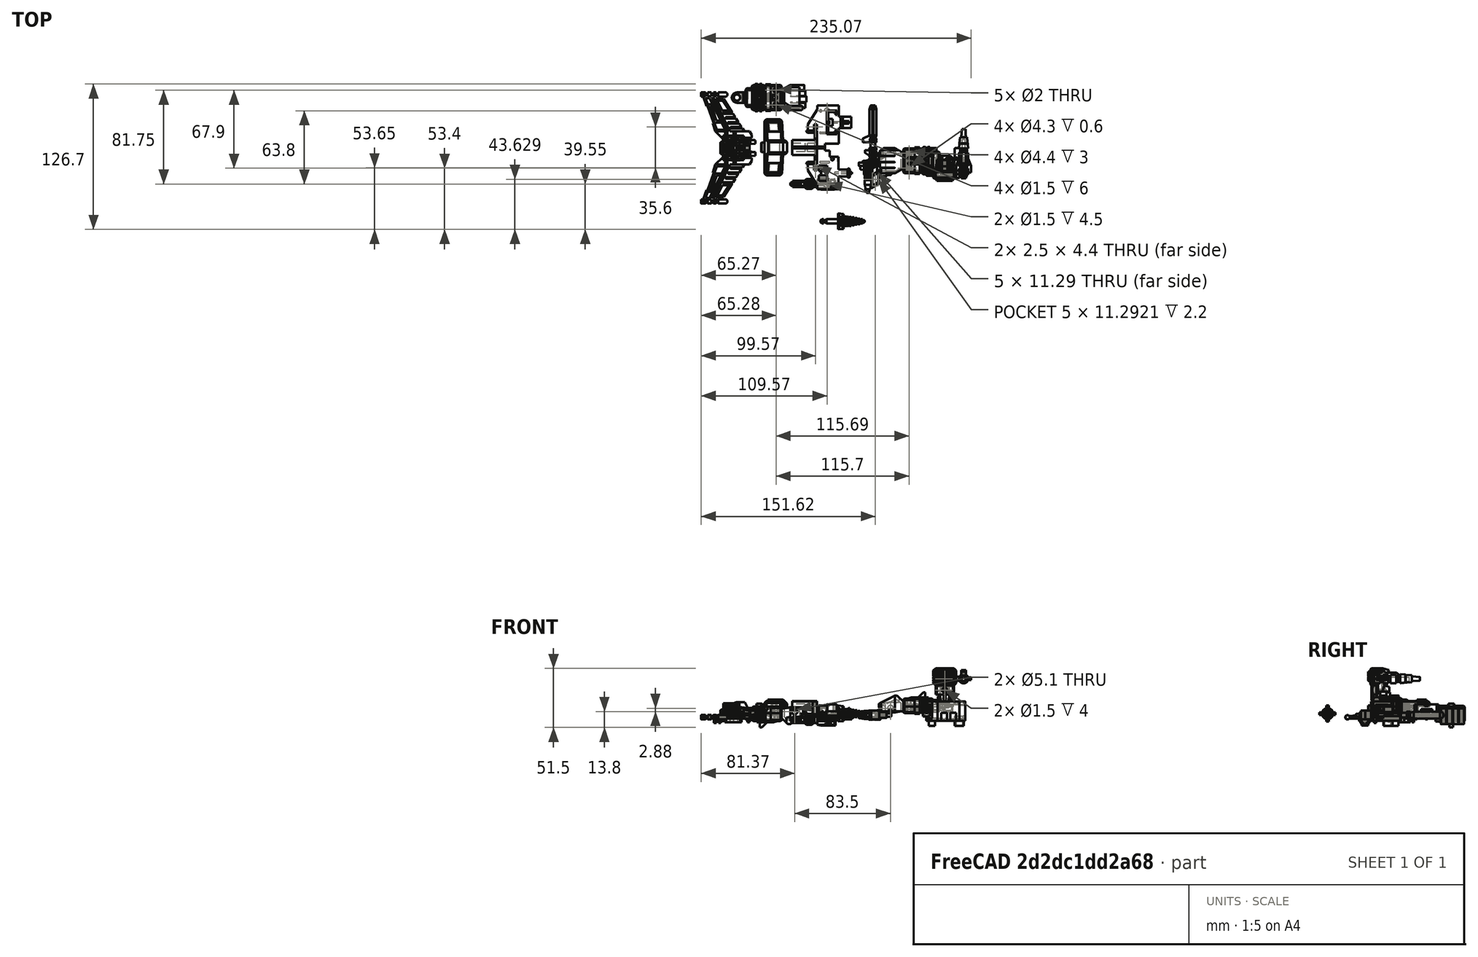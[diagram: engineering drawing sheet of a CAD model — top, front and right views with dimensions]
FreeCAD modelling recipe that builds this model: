
FCSTD DOCUMENT  (FreeCAD 1.0R39109 (Git))
Label: Accesories2
License: All rights reserved
LicenseURL: https://en.wikipedia.org/wiki/All_rights_reserved
objects: Sketcher::SketchObject×459, PartDesign::Pad×303, PartDesign::Pocket×204, PartDesign::Chamfer×40, PartDesign::Body×21, PartDesign::SubShapeBinder×9, PartDesign::Fillet×9, PartDesign::AdditiveLoft×7, PartDesign::Plane×4, App::Part×4, App::Link×3, PartDesign::Groove×3, PartDesign::SubtractiveLoft×2, Part::Mirroring×1, Part::Feature×1
note: 2658 computed .brp shape members not serialized (recipe doc carries the construction recipe); baked Part::Feature solids carry a one-line shape summary decoded from their .brp

FEATURE [Sketcher::SketchObject] Sketch508
  ArcFitTolerance = 1e-06
  AttachmentSupport = -> [XZ_Plane033]
  FullyConstrained = true
  MakeInternals = false
  MapMode = 5
  Placement = pos=(0,0,0) rot=(1,0,0;1.5708rad)
  sketch-geometry (30):
    g0: LineSegment StartX=0 StartY=0 StartZ=0 EndX=13.5 EndY=0 EndZ=0
    g1: LineSegment StartX=13.5 StartY=0 StartZ=0 EndX=13.5 EndY=-11.8 EndZ=0
    g2: LineSegment StartX=13.5 StartY=-11.8 StartZ=0 EndX=23.4 EndY=-11.8 EndZ=0
    g3: LineSegment StartX=23.4 StartY=-11.8 StartZ=0 EndX=23.4 EndY=0 EndZ=0
    g4: LineSegment StartX=23.4 StartY=0 StartZ=0 EndX=33.2 EndY=0 EndZ=0
    g5: LineSegment StartX=33.2 StartY=0 StartZ=0 EndX=33.2 EndY=17.7 EndZ=0
    g6: LineSegment StartX=33.2 StartY=17.7 StartZ=0 EndX=29.8 EndY=17.7 EndZ=0
    g7: LineSegment StartX=29.8 StartY=17.7 StartZ=0 EndX=16.75 EndY=25.9 EndZ=0
    g8: LineSegment StartX=16.75 StartY=25.9 StartZ=0 EndX=11.25 EndY=25.9 EndZ=0
    g9: LineSegment StartX=11.25 StartY=25.9 StartZ=0 EndX=11.25 EndY=27.1 EndZ=0
    g10: LineSegment StartX=11.25 StartY=27.1 StartZ=0 EndX=9.45 EndY=27.1 EndZ=0
    g11: LineSegment StartX=9.45 StartY=27.1 StartZ=0 EndX=9.45 EndY=19.8 EndZ=0
    g12: LineSegment StartX=9.45 StartY=19.8 StartZ=0 EndX=-16.15 EndY=19.8 EndZ=0
    g13: LineSegment StartX=-16.15 StartY=19.8 StartZ=0 EndX=-16.15 EndY=27.1 EndZ=0
    g14: LineSegment StartX=-16.15 StartY=27.1 StartZ=0 EndX=-17.95 EndY=27.1 EndZ=0
    g15: LineSegment StartX=-17.95 StartY=27.1 StartZ=0 EndX=-17.95 EndY=25.9 EndZ=0
    g16: LineSegment StartX=-17.95 StartY=25.9 StartZ=0 EndX=-23.45 EndY=25.9 EndZ=0
    g17: LineSegment StartX=-23.45 StartY=25.9 StartZ=0 EndX=-36.5 EndY=17.7 EndZ=0
    g18: LineSegment StartX=-36.5 StartY=17.7 StartZ=0 EndX=-39.9 EndY=17.7 EndZ=0
    g19: LineSegment StartX=-39.9 StartY=17.7 StartZ=0 EndX=-39.9 EndY=0 EndZ=0
    g20: LineSegment StartX=-39.9 StartY=0 StartZ=0 EndX=-28.8 EndY=0 EndZ=0
    g21: LineSegment StartX=-28.8 StartY=0 StartZ=0 EndX=-28.8 EndY=-10.7 EndZ=0
    g22: LineSegment StartX=-28.8 StartY=-10.7 StartZ=0 EndX=-22.8 EndY=-10.7 EndZ=0
    g23: LineSegment StartX=-22.8 StartY=-10.7 StartZ=0 EndX=-22.8 EndY=0 EndZ=0
    g24: LineSegment StartX=-22.8 StartY=0 StartZ=0 EndX=-12.9 EndY=0 EndZ=0
    g25: LineSegment StartX=-12.9 StartY=0 StartZ=0 EndX=-12.9 EndY=6.7 EndZ=0
    g26: LineSegment StartX=-12.9 StartY=6.7 StartZ=0 EndX=-6 EndY=6.7 EndZ=0
    g27: LineSegment StartX=-6 StartY=6.7 StartZ=0 EndX=-6 EndY=11 EndZ=0
    g28: LineSegment StartX=-6 StartY=11 StartZ=0 EndX=0 EndY=11 EndZ=0
    g29: LineSegment StartX=0 StartY=11 StartZ=0 EndX=0 EndY=0 EndZ=0
  constraints (91):
    c: Coincident(g0,g-1)
    c: PointOnObject(g0,g-1)
    c: Coincident(g1,g0)
    c: Vertical(g1)
    c: Coincident(g2,g1)
    c: Horizontal(g2)
    c: Coincident(g3,g2)
    c: PointOnObject(g3,g-1)
    c: Vertical(g3)
    c: Coincident(g4,g3)
    c: PointOnObject(g4,g-1)
    c: DistanceX(g0,g0) = 13.5
    c: Coincident(g5,g4)
    c: Vertical(g5)
    c: Coincident(g6,g5)
    c: Horizontal(g6)
    c: Coincident(g7,g6)
    c: Coincident(g8,g7)
    c: Horizontal(g8)
    c: Coincident(g9,g8)
    c: Vertical(g9)
    c: Coincident(g10,g9)
    c: Horizontal(g10)
    c: Coincident(g11,g10)
    c: Vertical(g11)
    c: Coincident(g12,g11)
    c: Horizontal(g12)
    c: Coincident(g13,g12)
    c: Vertical(g13)
    c: Coincident(g14,g13)
    c: Horizontal(g14)
    c: Coincident(g15,g14)
    c: Vertical(g15)
    c: Coincident(g16,g15)
    c: Horizontal(g16)
    c: Coincident(g17,g16)
    c: Coincident(g18,g17)
    c: Horizontal(g18)
    c: Coincident(g19,g18)
    c: PointOnObject(g19,g-1)
    c: Vertical(g19)
    c: Coincident(g20,g19)
    c: PointOnObject(g20,g-1)
    c: Coincident(g21,g20)
    c: Vertical(g21)
    c: Coincident(g22,g21)
    c: Horizontal(g22)
    c: Coincident(g23,g22)
    c: PointOnObject(g23,g-1)
    c: Vertical(g23)
    c: Coincident(g24,g23)
    c: PointOnObject(g24,g-1)
    c: Coincident(g25,g24)
    c: Vertical(g25)
    c: Coincident(g26,g25)
    c: Horizontal(g26)
    c: Coincident(g27,g26)
    c: Vertical(g27)
    c: Coincident(g28,g27)
    c: PointOnObject(g28,g-2)
    c: Horizontal(g28)
    c: Coincident(g29,g28)
    c: Coincident(g29,g0)
    c: DistanceX(g2,g2) = 9.9
    c: DistanceY(g1,g1) = 11.8
    c: DistanceX(g4,g4) = 9.8
    c: DistanceY(g5,g5) = 17.7
    c: DistanceY(g29,g29) = 11
    c: DistanceX(g28,g28) = 6
    c: DistanceX(g24,g0) = 12.9
    c: DistanceX(g19,g24) = 27
    c: DistanceX(g22,g22) = 6
    c: DistanceY(g23,g23) = 10.7
    c: DistanceX(g20,g20) = 11.1
    c: DistanceY(g19,g19) = 17.7
    c: DistanceX(g10,g10) = 1.8
    c: DistanceX(g14,g14) = 1.8
    c: DistanceY(g9,g9) = 1.2
    c: DistanceY(g15,g15) = 1.2
    c: DistanceX(g18,g18) = 3.4
    c: DistanceX(g6,g6) = 3.4
    c: DistanceY(g25,g25) = 6.7
    c: DistanceX(g19,g4) = 73.1
    c: DistanceX(g12,g12) = 25.6
    c: DistanceY(g11,g11) = 7.3
    c: DistanceX(g16,g16) = 5.5
    c: DistanceX(g8,g8) = 5.5
    c: DistanceY(g13,g13) = 7.3
    c: DistanceY(g28,g11) = 8.8
    c: DistanceX(g18,g12) = 23.75
    c: DistanceX(g11,g5) = 23.75
FEATURE [PartDesign::Pad] Pad351
  Direction = (0,-1,2e-16)
  Length = 2
  Length2 = 10
  Placement = pos=(0,0,0) rot=(1,0,0;1.5708rad)
  Profile = -> Sketch508
  ReferenceAxis = -> Sketch508 [N_Axis]
  Refine = true
  Suppressed = false
  Type = 0
FEATURE [Sketcher::SketchObject] Sketch509
  ArcFitTolerance = 1e-06
  AttachmentSupport = -> [Pad351]
  ExternalGeometry = -> [Pad351]
  FullyConstrained = true
  MakeInternals = false
  MapMode = 5
  Placement = pos=(0,-2,0) rot=(1,0,0;1.5708rad)
  sketch-geometry (8):
    g0: LineSegment StartX=-17.95 StartY=27.1 StartZ=0 EndX=-16.15 EndY=27.1 EndZ=0
    g1: LineSegment StartX=-16.15 StartY=27.1 StartZ=0 EndX=-16.15 EndY=19.8 EndZ=0
    g2: LineSegment StartX=-16.15 StartY=19.8 StartZ=0 EndX=9.45 EndY=19.8 EndZ=0
    g3: LineSegment StartX=9.45 StartY=19.8 StartZ=0 EndX=9.45 EndY=27.1 EndZ=0
    g4: LineSegment StartX=9.45 StartY=27.1 StartZ=0 EndX=11.25 EndY=27.1 EndZ=0
    g5: LineSegment StartX=11.25 StartY=27.1 StartZ=0 EndX=11.25 EndY=17.8 EndZ=0
    g6: LineSegment StartX=11.25 StartY=17.8 StartZ=0 EndX=-17.95 EndY=17.8 EndZ=0
    g7: LineSegment StartX=-17.95 StartY=27.1 StartZ=0 EndX=-17.95 EndY=17.8 EndZ=0
  constraints (18):
    c: Coincident(g0,g-7)
    c: Coincident(g0,g-5)
    c: Coincident(g1,g0)
    c: Coincident(g1,g-6)
    c: Coincident(g2,g1)
    c: Coincident(g2,g-6)
    c: Coincident(g3,g2)
    c: Coincident(g3,g-4)
    c: Coincident(g4,g3)
    c: Coincident(g4,g-3)
    c: Coincident(g5,g4)
    c: Vertical(g5)
    c: Coincident(g6,g5)
    c: Horizontal(g6)
    c: Coincident(g7,g0)
    c: Coincident(g7,g6)
    c: Vertical(g7)
    c: DistanceY(g6,g1) = 2
FEATURE [PartDesign::Pad] Pad352
  BaseFeature = -> Pad351
  Direction = (0,-1,2e-16)
  Length = 11
  Length2 = 10
  Placement = pos=(0,0,0) rot=(1,0,0;1.5708rad)
  Profile = -> Sketch509
  ReferenceAxis = -> Sketch509 [N_Axis]
  Refine = true
  Suppressed = false
  Type = 0
FEATURE [Sketcher::SketchObject] Sketch510
  ArcFitTolerance = 1e-06
  AttachmentSupport = -> [Pad352]
  ExternalGeometry = -> [Pad352]
  FullyConstrained = true
  MakeInternals = false
  MapMode = 5
  Placement = pos=(0,-13,0) rot=(1,0,0;1.5708rad)
  sketch-geometry (8):
    g0: LineSegment StartX=-17.95 StartY=27.1 StartZ=0 EndX=-17.95 EndY=21.7 EndZ=0
    g1: LineSegment StartX=-17.95 StartY=21.7 StartZ=0 EndX=-16.15 EndY=21.7 EndZ=0
    g2: LineSegment StartX=-16.15 StartY=21.7 StartZ=0 EndX=-16.15 EndY=27.1 EndZ=0
    g3: LineSegment StartX=-16.15 StartY=27.1 StartZ=0 EndX=-17.95 EndY=27.1 EndZ=0
    g4: LineSegment StartX=9.45 StartY=27.1 StartZ=0 EndX=9.45 EndY=21.7 EndZ=0
    g5: LineSegment StartX=9.45 StartY=21.7 StartZ=0 EndX=11.25 EndY=21.7 EndZ=0
    g6: LineSegment StartX=11.25 StartY=21.7 StartZ=0 EndX=11.25 EndY=27.1 EndZ=0
    g7: LineSegment StartX=11.25 StartY=27.1 StartZ=0 EndX=9.45 EndY=27.1 EndZ=0
  constraints (22):
    c: Coincident(g0,g1)
    c: Coincident(g1,g2)
    c: Coincident(g2,g3)
    c: Coincident(g3,g0)
    c: Vertical(g0)
    c: Vertical(g2)
    c: Horizontal(g1)
    c: Horizontal(g3)
    c: Coincident(g0,g-6)
    c: PointOnObject(g1,g-5)
    c: Coincident(g4,g5)
    c: Coincident(g5,g6)
    c: Coincident(g6,g7)
    c: Coincident(g7,g4)
    c: Vertical(g4)
    c: Vertical(g6)
    c: Horizontal(g5)
    c: Horizontal(g7)
    c: Coincident(g4,g-4)
    c: PointOnObject(g5,g-3)
    c: DistanceY(g0,g0) = 5.4
    c: DistanceY(g6,g6) = 5.4
FEATURE [PartDesign::Pocket] Pocket235
  BaseFeature = -> Pad352
  Direction = (0,1,-2e-16)
  Length = 10.7
  Length2 = 5
  Placement = pos=(0,0,0) rot=(1,0,0;1.5708rad)
  Profile = -> Sketch510
  ReferenceAxis = -> Sketch510 [N_Axis]
  Refine = true
  Suppressed = false
  Type = 0
FEATURE [Sketcher::SketchObject] Sketch511
  ArcFitTolerance = 1e-06
  AttachmentSupport = -> [Pocket235]
  ExternalGeometry = -> [Pocket235]
  FullyConstrained = true
  MakeInternals = false
  MapMode = 5
  Placement = pos=(0,-13,0) rot=(1,0,0;1.5708rad)
  sketch-geometry (4):
    g0: LineSegment StartX=-9.25 StartY=19.8 StartZ=0 EndX=2.55 EndY=19.8 EndZ=0
    g1: LineSegment StartX=2.55 StartY=19.8 StartZ=0 EndX=2.55 EndY=39.4 EndZ=0
    g2: LineSegment StartX=2.55 StartY=39.4 StartZ=0 EndX=-9.25 EndY=39.4 EndZ=0
    g3: LineSegment StartX=-9.25 StartY=39.4 StartZ=0 EndX=-9.25 EndY=19.8 EndZ=0
  constraints (13):
    c: Coincident(g0,g1)
    c: Coincident(g1,g2)
    c: Coincident(g2,g3)
    c: Coincident(g3,g0)
    c: Horizontal(g0)
    c: Horizontal(g2)
    c: Vertical(g1)
    c: Vertical(g3)
    c: PointOnObject(g0,g-3)
    c: DistanceX(g2,g2) = 11.8
    c: DistanceX(g-3,g-3) = 25.6
    c: DistanceX(g-3,g0) = 6.9
    c: DistanceY(g1,g1) = 19.6
FEATURE [PartDesign::Pad] Pad353
  BaseFeature = -> Pocket235
  Direction = (0,-1,2e-16)
  Length = 2
  Length2 = 10
  Placement = pos=(0,0,0) rot=(1,0,0;1.5708rad)
  Profile = -> Sketch511
  ReferenceAxis = -> Sketch511 [N_Axis]
  Refine = true
  Reversed = true
  Suppressed = false
  Type = 0
FEATURE [Sketcher::SketchObject] Sketch512
  ArcFitTolerance = 1e-06
  AttachmentSupport = -> [Pad353]
  ExternalGeometry = -> [Pad353]
  FullyConstrained = true
  MakeInternals = false
  MapMode = 5
  Placement = pos=(0,-11,3e-15) rot=(-1,0,0;1.5708rad)
  sketch-geometry (12):
    g0: LineSegment StartX=-9.25 StartY=-19.8 StartZ=0 EndX=-9.25 EndY=-39.4 EndZ=0
    g1: LineSegment StartX=2.55 StartY=-19.8 StartZ=0 EndX=2.55 EndY=-39.4 EndZ=0
    g2: LineSegment StartX=2.55 StartY=-39.4 StartZ=0 EndX=0.55 EndY=-39.4 EndZ=0
    g3: LineSegment StartX=0.55 StartY=-39.4 StartZ=0 EndX=0.55 EndY=-28.5 EndZ=0
    g4: LineSegment StartX=0.55 StartY=-28.5 StartZ=0 EndX=-7.25 EndY=-28.5 EndZ=0
    g5: LineSegment StartX=-7.25 StartY=-28.5 StartZ=0 EndX=-7.25 EndY=-39.4 EndZ=0
    g6: LineSegment StartX=-7.25 StartY=-39.4 StartZ=0 EndX=-9.25 EndY=-39.4 EndZ=0
    g7: LineSegment StartX=-9.25 StartY=-19.8 StartZ=0 EndX=-7.25 EndY=-19.8 EndZ=0
    g8: LineSegment StartX=-7.25 StartY=-19.8 StartZ=0 EndX=-7.25 EndY=-26 EndZ=0
    g9: LineSegment StartX=-7.25 StartY=-26 StartZ=0 EndX=0.55 EndY=-26 EndZ=0
    g10: LineSegment StartX=0.55 StartY=-26 StartZ=0 EndX=0.55 EndY=-19.8 EndZ=0
    g11: LineSegment StartX=2.55 StartY=-19.8 StartZ=0 EndX=0.55 EndY=-19.8 EndZ=0
  constraints (32):
    c: Coincident(g0,g-4)
    c: Coincident(g0,g-4)
    c: Coincident(g1,g-3)
    c: Coincident(g1,g-3)
    c: Coincident(g2,g1)
    c: Horizontal(g2)
    c: Coincident(g3,g2)
    c: Vertical(g3)
    c: Coincident(g4,g3)
    c: Horizontal(g4)
    c: Coincident(g5,g4)
    c: PointOnObject(g5,g-5)
    c: Vertical(g5)
    c: Coincident(g6,g5)
    c: Coincident(g6,g0)
    c: Coincident(g7,g0)
    c: Horizontal(g7)
    c: Coincident(g8,g7)
    c: Vertical(g8)
    c: Coincident(g9,g8)
    c: Horizontal(g9)
    c: Coincident(g10,g9)
    c: Vertical(g10)
    c: Coincident(g11,g1)
    c: Coincident(g11,g10)
    c: PointOnObject(g10,g-6)
    c: DistanceX(g7,g7) = 2
    c: DistanceX(g11,g11) = 2
    c: DistanceX(g2,g2) = 2
    c: DistanceX(g6,g6) = 2
    c: DistanceY(g4,g8) = 2.5
    c: DistanceY(g5,g4) = 10.9
FEATURE [PartDesign::Pad] Pad354
  BaseFeature = -> Pad353
  Direction = (0,1,2e-16)
  Length = 3
  Length2 = 10
  Placement = pos=(0,0,0) rot=(1,0,0;1.5708rad)
  Profile = -> Sketch512
  ReferenceAxis = -> Sketch512 [N_Axis]
  Refine = true
  Suppressed = false
  Type = 0
FEATURE [Sketcher::SketchObject] Sketch513
  ArcFitTolerance = 1e-06
  AttachmentSupport = -> [Pad354]
  ExternalGeometry = -> [Pad354]
  FullyConstrained = true
  MakeInternals = false
  MapMode = 5
  Placement = pos=(0,-13,8.7e-15) rot=(1,0,0;1.5708rad)
  sketch-geometry (4):
    g0: LineSegment StartX=-4.1 StartY=39.4 StartZ=0 EndX=-4.1 EndY=17.8 EndZ=0
    g1: LineSegment StartX=-4.1 StartY=17.8 StartZ=0 EndX=-2.6 EndY=17.8 EndZ=0
    g2: LineSegment StartX=-2.6 StartY=17.8 StartZ=0 EndX=-2.6 EndY=39.4 EndZ=0
    g3: LineSegment StartX=-2.6 StartY=39.4 StartZ=0 EndX=-4.1 EndY=39.4 EndZ=0
  constraints (14):
    c: Coincident(g0,g1)
    c: Coincident(g1,g2)
    c: Coincident(g2,g3)
    c: Coincident(g3,g0)
    c: Vertical(g0)
    c: Vertical(g2)
    c: Horizontal(g1)
    c: Horizontal(g3)
    c: PointOnObject(g0,g-3)
    c: PointOnObject(g1,g-4)
    c: DistanceX(g3,g3) = 1.5
    c: DistanceX(g-3,g-3) = 11.8
    c: DistanceX(g-3,g0) = 5.15
    c: DistanceX(g2,g-3) = 5.15
FEATURE [PartDesign::Pad] Pad355
  BaseFeature = -> Pad354
  Direction = (0,-1,2e-16)
  Length = 0.3
  Length2 = 10
  Placement = pos=(0,0,0) rot=(1,0,0;1.5708rad)
  Profile = -> Sketch513
  ReferenceAxis = -> Sketch513 [N_Axis]
  Refine = true
  Suppressed = false
  Type = 0
FEATURE [Sketcher::SketchObject] Sketch514
  ArcFitTolerance = 1e-06
  AttachmentSupport = -> [Pad355]
  ExternalGeometry = -> [Pad355]
  FullyConstrained = true
  MakeInternals = false
  MapMode = 5
  Placement = pos=(0,1.8e-15,0) rot=(-1,0,0;1.5708rad)
  sketch-geometry (11):
    g0: ArcOfCircle CenterX=9.45 CenterY=-14.95 CenterZ=0 NormalX=0 NormalY=0 NormalZ=1 AngleXU=0 Radius=0.65 StartAngle=3.14159 EndAngle=6.28319
    g1: ArcOfCircle CenterX=9.45 CenterY=-7.45 CenterZ=0 NormalX=0 NormalY=0 NormalZ=1 AngleXU=0 Radius=0.65 StartAngle=2e-16 EndAngle=3.14159
    g2: LineSegment StartX=8.8 StartY=-14.95 StartZ=0 EndX=8.8 EndY=-7.45 EndZ=0
    g3: LineSegment StartX=10.1 StartY=-14.95 StartZ=0 EndX=10.1 EndY=-7.45 EndZ=0
    g4: ArcOfCircle CenterX=-16.15 CenterY=-14.95 CenterZ=0 NormalX=0 NormalY=0 NormalZ=1 AngleXU=0 Radius=0.65 StartAngle=3.14159 EndAngle=6.28319
    g5: ArcOfCircle CenterX=-16.15 CenterY=-7.45 CenterZ=0 NormalX=0 NormalY=0 NormalZ=1 AngleXU=0 Radius=0.65 StartAngle=3e-16 EndAngle=3.14159
    g6: LineSegment StartX=-16.8 StartY=-14.95 StartZ=0 EndX=-16.8 EndY=-7.45 EndZ=0
    g7: LineSegment StartX=-15.5 StartY=-14.95 StartZ=0 EndX=-15.5 EndY=-7.45 EndZ=0
    g8: LineSegment [constr] StartX=9.45 StartY=-14.95 StartZ=0 EndX=-16.15 EndY=-14.95 EndZ=0
    g9: LineSegment [constr] StartX=9.45 StartY=-7.45 StartZ=0 EndX=-16.15 EndY=-7.45 EndZ=0
    g10: LineSegment [constr] StartX=-16.15 StartY=-14.95 StartZ=0 EndX=-16.15 EndY=-19.8 EndZ=0
  constraints (28):
    c: Tangent(g0,g2) = 1.5708
    c: Tangent(g0,g3) = -1.5708
    c: Tangent(g1,g2) = 1.5708
    c: Tangent(g1,g3) = -1.5708
    c: Equal(g0,g1)
    c: Vertical(g2)
    c: Tangent(g4,g6) = 1.5708
    c: Tangent(g4,g7) = -1.5708
    c: Tangent(g5,g6) = 1.5708
    c: Tangent(g5,g7) = -1.5708
    c: Equal(g4,g5)
    c: Vertical(g6)
    c: Diameter(g1) = 1.3
    c: Diameter(g5) = 1.3
    c: DistanceY(g4,g5) = 7.5
    c: Coincident(g8,g0)
    c: Coincident(g8,g4)
    c: Horizontal(g8)
    c: Coincident(g9,g1)
    c: Coincident(g9,g5)
    c: Horizontal(g9)
    c: DistanceX(g5,g1) = 26.9
    c: DistanceY(g5,g-3) = 7.45
    c: DistanceX(g-4,g-4) = 25.6
    c: DistanceX(g4,g0) = 25.6
    c: Coincident(g10,g4)
    c: Coincident(g10,g-4)
    c: Vertical(g10)
FEATURE [PartDesign::Pad] Pad356
  BaseFeature = -> Pad355
  Direction = (0,1,2e-16)
  Length = 2.5
  Length2 = 10
  Placement = pos=(0,0,0) rot=(1,0,0;1.5708rad)
  Profile = -> Sketch514
  ReferenceAxis = -> Sketch514 [N_Axis]
  Refine = true
  Suppressed = false
  Type = 0
FEATURE [Sketcher::SketchObject] Sketch515
  ArcFitTolerance = 1e-06
  AttachmentSupport = -> [Pad356]
  ExternalGeometry = -> [Pad356]
  FullyConstrained = true
  MakeInternals = false
  MapMode = 5
  Placement = pos=(0,1.8e-15,0) rot=(-1,0,0;1.5708rad)
  sketch-geometry (5):
    g0: Circle CenterX=28.55 CenterY=-9.15 CenterZ=0 NormalX=0 NormalY=0 NormalZ=1 AngleXU=0 Radius=2.35
    g1: Circle CenterX=-35.25 CenterY=-9.15 CenterZ=0 NormalX=0 NormalY=0 NormalZ=1 AngleXU=0 Radius=2.35
    g2: LineSegment [constr] StartX=-35.25 StartY=-9.15 StartZ=0 EndX=28.55 EndY=-9.15 EndZ=0
    g3: Circle CenterX=-35.25 CenterY=-9.15 CenterZ=0 NormalX=0 NormalY=0 NormalZ=1 AngleXU=0 Radius=0.75
    g4: Circle CenterX=28.55 CenterY=-9.15 CenterZ=0 NormalX=0 NormalY=0 NormalZ=1 AngleXU=0 Radius=0.75
  constraints (12):
    c: Diameter(g1) = 4.7
    c: Diameter(g0) = 4.7
    c: DistanceY(g0,g-3) = 9.15
    c: Coincident(g2,g1)
    c: Coincident(g2,g0)
    c: Horizontal(g2)
    c: DistanceX(g0,g-3) = 4.65
    c: DistanceX(g-4,g1) = 4.65
    c: Coincident(g3,g1)
    c: Coincident(g4,g0)
    c: Radius(g4) = 0.75
    c: Radius(g3) = 0.75
FEATURE [PartDesign::Pad] Pad357
  BaseFeature = -> Pad356
  Direction = (0,1,2e-16)
  Length = 3
  Length2 = 10
  Placement = pos=(0,0,0) rot=(1,0,0;1.5708rad)
  Profile = -> Sketch515
  ReferenceAxis = -> Sketch515 [N_Axis]
  Refine = true
  Suppressed = false
  Type = 0
FEATURE [Sketcher::SketchObject] Sketch516
  ArcFitTolerance = 1e-06
  AttachmentSupport = -> [Pad357]
  ExternalGeometry = -> [Pad357]
  FullyConstrained = true
  MakeInternals = false
  MapMode = 5
  Placement = pos=(0,1.8e-15,0) rot=(-1,0,0;1.5708rad)
  sketch-geometry (6):
    g0: Circle CenterX=-35.25 CenterY=-14.7 CenterZ=0 NormalX=0 NormalY=0 NormalZ=1 AngleXU=0 Radius=1
    g1: Circle CenterX=28.55 CenterY=-14.7 CenterZ=0 NormalX=0 NormalY=0 NormalZ=1 AngleXU=0 Radius=1
    g2: LineSegment [constr] StartX=-35.25 StartY=-9.15 StartZ=0 EndX=-35.25 EndY=-14.7 EndZ=0
    g3: LineSegment [constr] StartX=28.55 StartY=-9.15 StartZ=0 EndX=28.55 EndY=-14.7 EndZ=0
    g4: LineSegment [constr] StartX=28.55 StartY=-15.7 StartZ=0 EndX=28.55 EndY=-6.8 EndZ=0
    g5: LineSegment [constr] StartX=-35.25 StartY=-15.7 StartZ=0 EndX=-35.25 EndY=-6.8 EndZ=0
  constraints (18):
    c: Diameter(g1) = 2
    c: Diameter(g0) = 2
    c: Coincident(g2,g-3)
    c: Coincident(g2,g0)
    c: Vertical(g2)
    c: Coincident(g3,g-4)
    c: Coincident(g3,g1)
    c: Vertical(g3)
    c: PointOnObject(g4,g1)
    c: PointOnObject(g4,g-5)
    c: Vertical(g4)
    c: DistanceY(g4,g4) = 8.9
    c: PointOnObject(g5,g0)
    c: Vertical(g5)
    c: PointOnObject(g0,g5)
    c: DistanceY(g5,g5) = 8.9
    c: PointOnObject(g3,g4)
    c: PointOnObject(g5,g-6)
FEATURE [PartDesign::Pad] Pad358
  BaseFeature = -> Pad357
  Direction = (0,1,2e-16)
  Length = 3
  Length2 = 10
  Placement = pos=(0,0,0) rot=(1,0,0;1.5708rad)
  Profile = -> Sketch516
  ReferenceAxis = -> Sketch516 [N_Axis]
  Refine = true
  Suppressed = false
  Type = 0
FEATURE [Sketcher::SketchObject] Sketch517
  ArcFitTolerance = 1e-06
  AttachmentSupport = -> [Pad358]
  ExternalGeometry = -> [Pad358]
  FullyConstrained = true
  MakeInternals = false
  MapMode = 5
  Placement = pos=(0,1.8e-15,0) rot=(-1,0,0;1.5708rad)
  sketch-geometry (9):
    g0: LineSegment StartX=12.25 StartY=-17.9 StartZ=0 EndX=12.25 EndY=-20.4 EndZ=0
    g1: LineSegment StartX=12.25 StartY=-20.4 StartZ=0 EndX=16.65 EndY=-20.4 EndZ=0
    g2: LineSegment StartX=16.65 StartY=-20.4 StartZ=0 EndX=16.65 EndY=-17.9 EndZ=0
    g3: LineSegment StartX=16.65 StartY=-17.9 StartZ=0 EndX=12.25 EndY=-17.9 EndZ=0
    g4: LineSegment StartX=-23.35 StartY=-17.9 StartZ=0 EndX=-23.35 EndY=-20.4 EndZ=0
    g5: LineSegment StartX=-23.35 StartY=-20.4 StartZ=0 EndX=-18.95 EndY=-20.4 EndZ=0
    g6: LineSegment StartX=-18.95 StartY=-20.4 StartZ=0 EndX=-18.95 EndY=-17.9 EndZ=0
    g7: LineSegment StartX=-18.95 StartY=-17.9 StartZ=0 EndX=-23.35 EndY=-17.9 EndZ=0
    g8: LineSegment [constr] StartX=-18.95 StartY=-17.9 StartZ=0 EndX=12.25 EndY=-17.9 EndZ=0
  constraints (28):
    c: Coincident(g0,g1)
    c: Coincident(g1,g2)
    c: Coincident(g2,g3)
    c: Coincident(g3,g0)
    c: Vertical(g0)
    c: Vertical(g2)
    c: Horizontal(g1)
    c: Horizontal(g3)
    c: Coincident(g4,g5)
    c: Coincident(g5,g6)
    c: Coincident(g6,g7)
    c: Coincident(g7,g4)
    c: Vertical(g4)
    c: Vertical(g6)
    c: Horizontal(g5)
    c: Horizontal(g7)
    c: DistanceX(g7,g7) = 4.4
    c: DistanceX(g3,g3) = 4.4
    c: DistanceY(g2,g2) = 2.5
    c: DistanceY(g6,g6) = 2.5
    c: Coincident(g8,g6)
    c: Coincident(g8,g0)
    c: Horizontal(g8)
    c: DistanceX(g8,g8) = 31.2
    c: DistanceX(g-3,g-3) = 25.6
    c: DistanceX(g6,g-3) = 2.8
    c: DistanceX(g-3,g0) = 2.8
    c: DistanceY(g-4,g4) = 5.5
FEATURE [PartDesign::Pocket] Pocket236
  BaseFeature = -> Pad358
  Direction = (0,-1,-2e-16)
  Length = 5
  Length2 = 5
  Placement = pos=(0,0,0) rot=(1,0,0;1.5708rad)
  Profile = -> Sketch517
  ReferenceAxis = -> Sketch517 [N_Axis]
  Refine = true
  Suppressed = false
  Type = 0
FEATURE [Sketcher::SketchObject] Sketch518
  ArcFitTolerance = 1e-06
  AttachmentSupport = -> [Pocket236]
  ExternalGeometry = -> [Pocket236]
  FullyConstrained = true
  MakeInternals = false
  MapMode = 5
  Placement = pos=(0,-2,0) rot=(1,0,0;1.5708rad)
  sketch-geometry (4):
    g0: LineSegment StartX=-22.8 StartY=-10.7 StartZ=0 EndX=-22.8 EndY=-8.7 EndZ=0
    g1: LineSegment StartX=-22.8 StartY=-8.7 StartZ=0 EndX=-28.8 EndY=-8.7 EndZ=0
    g2: LineSegment StartX=-28.8 StartY=-8.7 StartZ=0 EndX=-28.8 EndY=-10.7 EndZ=0
    g3: LineSegment StartX=-28.8 StartY=-10.7 StartZ=0 EndX=-22.8 EndY=-10.7 EndZ=0
  constraints (11):
    c: Coincident(g0,g1)
    c: Coincident(g1,g2)
    c: Coincident(g2,g3)
    c: Coincident(g3,g0)
    c: Vertical(g0)
    c: Vertical(g2)
    c: Horizontal(g1)
    c: Horizontal(g3)
    c: Coincident(g0,g-3)
    c: PointOnObject(g1,g-4)
    c: DistanceY(g2,g2) = 2
FEATURE [PartDesign::Pad] Pad359
  BaseFeature = -> Pocket236
  Direction = (0,-1,2e-16)
  Length = 5.3
  Length2 = 10
  Placement = pos=(0,0,0) rot=(1,0,0;1.5708rad)
  Profile = -> Sketch518
  ReferenceAxis = -> Sketch518 [N_Axis]
  Refine = true
  Suppressed = false
  Type = 0
FEATURE [Sketcher::SketchObject] Sketch519
  ArcFitTolerance = 1e-06
  AttachmentSupport = -> [Pad359]
  ExternalGeometry = -> [Pad359]
  FullyConstrained = true
  MakeInternals = false
  MapMode = 5
  Placement = pos=(0,1.8e-15,0) rot=(-1,0,0;1.5708rad)
  sketch-geometry (6):
    g0: LineSegment StartX=-26.6 StartY=12.7 StartZ=0 EndX=-26.6 EndY=-1.7 EndZ=0
    g1: LineSegment StartX=-24.8 StartY=12.7 StartZ=0 EndX=-24.8 EndY=-1.7 EndZ=0
    g2: LineSegment StartX=-24.8 StartY=12.7 StartZ=0 EndX=-26.6 EndY=12.7 EndZ=0
    g3: ArcOfCircle CenterX=-25.7 CenterY=-1.7 CenterZ=0 NormalX=0 NormalY=0 NormalZ=1 AngleXU=0 Radius=0.9 StartAngle=3.14159 EndAngle=6.28319
    g4: LineSegment [constr] StartX=-24.8 StartY=-1.7 StartZ=0 EndX=-25.7 EndY=-1.7 EndZ=0
    g5: LineSegment [constr] StartX=-25.7 StartY=-1.7 StartZ=0 EndX=-26.6 EndY=-1.7 EndZ=0
  constraints (18):
    c: Vertical(g0)
    c: Vertical(g1)
    c: Coincident(g2,g1)
    c: Coincident(g2,g0)
    c: Horizontal(g2)
    c: Coincident(g3,g1)
    c: Coincident(g3,g0)
    c: Diameter(g3) = 1.8
    c: Coincident(g4,g1)
    c: Coincident(g4,g3)
    c: Horizontal(g4)
    c: Coincident(g5,g3)
    c: Coincident(g5,g0)
    c: Horizontal(g5)
    c: DistanceY(g-3,g1) = 2
    c: DistanceX(g-3,g-3) = 6
    c: DistanceX(g1,g-3) = 2
    c: DistanceY(g1,g1) = 14.4
FEATURE [PartDesign::Pad] Pad360
  BaseFeature = -> Pad359
  Direction = (0,1,2e-16)
  Length = 2.5
  Length2 = 10
  Placement = pos=(0,0,0) rot=(1,0,0;1.5708rad)
  Profile = -> Sketch519
  ReferenceAxis = -> Sketch519 [N_Axis]
  Refine = true
  Suppressed = false
  Type = 0
FEATURE [Sketcher::SketchObject] Sketch520
  ArcFitTolerance = 1e-06
  AttachmentSupport = -> [Pad360]
  ExternalGeometry = -> [Pad360]
  FullyConstrained = true
  MakeInternals = false
  MapMode = 5
  Placement = pos=(0,-4.3e-15,-10.7) rot=(1,0,0;3.14159rad)
  sketch-geometry (4):
    g0: LineSegment StartX=-24.8 StartY=0 StartZ=0 EndX=-26.6 EndY=0 EndZ=0
    g1: LineSegment StartX=-26.6 StartY=0 StartZ=0 EndX=-26.6 EndY=5.7 EndZ=0
    g2: LineSegment StartX=-24.8 StartY=0 StartZ=0 EndX=-24.8 EndY=5.7 EndZ=0
    g3: LineSegment StartX=-24.8 StartY=5.7 StartZ=0 EndX=-26.6 EndY=5.7 EndZ=0
  constraints (10):
    c: Coincident(g0,g-3)
    c: Coincident(g0,g-3)
    c: Coincident(g1,g0)
    c: Vertical(g1)
    c: Coincident(g2,g0)
    c: Vertical(g2)
    c: Coincident(g3,g2)
    c: Coincident(g3,g1)
    c: Horizontal(g3)
    c: DistanceY(g1,g-4) = 1.6
FEATURE [PartDesign::Pad] Pad361
  BaseFeature = -> Pad360
  Direction = (0,0,-1)
  Length = 2
  Length2 = 10
  Placement = pos=(0,0,0) rot=(1,0,0;1.5708rad)
  Profile = -> Sketch520
  ReferenceAxis = -> Sketch520 [N_Axis]
  Refine = true
  Suppressed = false
  Type = 0
FEATURE [Sketcher::SketchObject] Sketch521
  ArcFitTolerance = 1e-06
  AttachmentSupport = -> [Pad361]
  ExternalGeometry = -> [Pad361]
  FullyConstrained = true
  MakeInternals = false
  MapMode = 5
  Placement = pos=(0,-2,0) rot=(1,0,0;1.5708rad)
  sketch-geometry (4):
    g0: ArcOfCircle CenterX=-28.8 CenterY=-9.7 CenterZ=0 NormalX=0 NormalY=0 NormalZ=1 AngleXU=0 Radius=1 StartAngle=1.5708 EndAngle=4.71239
    g1: ArcOfCircle CenterX=-22.8 CenterY=-9.7 CenterZ=0 NormalX=0 NormalY=0 NormalZ=1 AngleXU=0 Radius=1 StartAngle=4.71239 EndAngle=7.85398
    g2: LineSegment StartX=-28.8 StartY=-8.7 StartZ=0 EndX=-28.8 EndY=-10.7 EndZ=0
    g3: LineSegment StartX=-22.8 StartY=-8.7 StartZ=0 EndX=-22.8 EndY=-10.7 EndZ=0
  constraints (10):
    c: Coincident(g0,g-4)
    c: Coincident(g0,g-4)
    c: Coincident(g1,g-3)
    c: Coincident(g1,g-3)
    c: PointOnObject(g0,g-4)
    c: PointOnObject(g1,g-3)
    c: Coincident(g2,g0)
    c: Coincident(g2,g0)
    c: Coincident(g3,g1)
    c: Coincident(g3,g1)
FEATURE [PartDesign::Pad] Pad362
  BaseFeature = -> Pad361
  Direction = (0,-1,2e-16)
  Length = 3.5
  Length2 = 10
  Placement = pos=(0,0,0) rot=(1,0,0;1.5708rad)
  Profile = -> Sketch521
  ReferenceAxis = -> Sketch521 [N_Axis]
  Refine = true
  Suppressed = false
  Type = 0
FEATURE [Sketcher::SketchObject] Sketch522
  ArcFitTolerance = 1e-06
  AttachmentSupport = -> [Pad362]
  ExternalGeometry = -> [Pad362]
  FullyConstrained = true
  MakeInternals = false
  MapMode = 5
  Placement = pos=(0,-2,0) rot=(1,0,0;1.5708rad)
  sketch-geometry (6):
    g0: Circle CenterX=-37.65 CenterY=2.85 CenterZ=0 NormalX=0 NormalY=0 NormalZ=1 AngleXU=0 Radius=1.25
    g1: Circle CenterX=-15.15 CenterY=2.85 CenterZ=0 NormalX=0 NormalY=0 NormalZ=1 AngleXU=0 Radius=1.25
    g2: LineSegment [constr] StartX=-37.65 StartY=2.85 StartZ=0 EndX=-15.15 EndY=2.85 EndZ=0
    g3: LineSegment [constr] StartX=-37.65 StartY=2.85 StartZ=0 EndX=-37.65 EndY=1.6 EndZ=0
    g4: LineSegment [constr] StartX=-37.65 StartY=2.85 StartZ=0 EndX=-38.9 EndY=2.85 EndZ=0
    g5: LineSegment [constr] StartX=-15.15 StartY=2.85 StartZ=0 EndX=-13.9 EndY=2.85 EndZ=0
  constraints (17):
    c: Diameter(g0) = 2.5
    c: Diameter(g1) = 2.5
    c: Coincident(g2,g0)
    c: Coincident(g2,g1)
    c: Horizontal(g2)
    c: Coincident(g3,g0)
    c: PointOnObject(g3,g0)
    c: Vertical(g3)
    c: DistanceY(g-3,g3) = 1.6
    c: Coincident(g4,g0)
    c: PointOnObject(g4,g0)
    c: Horizontal(g4)
    c: DistanceX(g-3,g4) = 1
    c: Coincident(g5,g1)
    c: PointOnObject(g5,g1)
    c: Horizontal(g5)
    c: DistanceX(g5,g-4) = 1
FEATURE [PartDesign::Pad] Pad363
  BaseFeature = -> Pad362
  Direction = (0,-1,2e-16)
  Length = 3.6
  Length2 = 10
  Placement = pos=(0,0,0) rot=(1,0,0;1.5708rad)
  Profile = -> Sketch522
  ReferenceAxis = -> Sketch522 [N_Axis]
  Refine = true
  Suppressed = false
  Type = 0
FEATURE [Sketcher::SketchObject] Sketch523
  ArcFitTolerance = 1e-06
  AttachmentSupport = -> [Pad363]
  ExternalGeometry = -> [Pad363]
  FullyConstrained = true
  MakeInternals = false
  MapMode = 5
  Placement = pos=(0,-2,0) rot=(1,0,0;1.5708rad)
  sketch-geometry (9):
    g0: LineSegment StartX=-32.8 StartY=16.4 StartZ=0 EndX=-32.8 EndY=9 EndZ=0
    g1: LineSegment StartX=-32.8 StartY=9 StartZ=0 EndX=-28.3 EndY=9 EndZ=0
    g2: LineSegment StartX=-28.3 StartY=9 StartZ=0 EndX=-28.3 EndY=16.4 EndZ=0
    g3: LineSegment StartX=-28.3 StartY=16.4 StartZ=0 EndX=-32.8 EndY=16.4 EndZ=0
    g4: LineSegment StartX=-23.3 StartY=16.4 StartZ=0 EndX=-23.3 EndY=9 EndZ=0
    g5: LineSegment StartX=-23.3 StartY=9 StartZ=0 EndX=-18.8 EndY=9 EndZ=0
    g6: LineSegment StartX=-18.8 StartY=9 StartZ=0 EndX=-18.8 EndY=16.4 EndZ=0
    g7: LineSegment StartX=-18.8 StartY=16.4 StartZ=0 EndX=-23.3 EndY=16.4 EndZ=0
    g8: LineSegment [constr] StartX=-23.3 StartY=9 StartZ=0 EndX=-28.3 EndY=9 EndZ=0
  constraints (28):
    c: Coincident(g0,g1)
    c: Coincident(g1,g2)
    c: Coincident(g2,g3)
    c: Coincident(g3,g0)
    c: Vertical(g0)
    c: Vertical(g2)
    c: Horizontal(g1)
    c: Horizontal(g3)
    c: Coincident(g4,g5)
    c: Coincident(g5,g6)
    c: Coincident(g6,g7)
    c: Coincident(g7,g4)
    c: Vertical(g4)
    c: Vertical(g6)
    c: Horizontal(g5)
    c: Horizontal(g7)
    c: DistanceY(g0,g0) = 7.4
    c: DistanceY(g6,g6) = 7.4
    c: DistanceX(g1,g1) = 4.5
    c: DistanceX(g5,g5) = 4.5
    c: Coincident(g8,g4)
    c: Coincident(g8,g1)
    c: Horizontal(g8)
    c: DistanceX(g8,g8) = 5
    c: DistanceX(g-4,g-3) = 6
    c: DistanceX(g-4,g1) = 0.5
    c: DistanceX(g4,g-3) = 0.5
    c: DistanceY(g-3,g4) = 9
FEATURE [PartDesign::Pad] Pad364
  BaseFeature = -> Pad363
  Direction = (0,-1,2e-16)
  Length = 7.7
  Length2 = 10
  Placement = pos=(0,0,0) rot=(1,0,0;1.5708rad)
  Profile = -> Sketch523
  ReferenceAxis = -> Sketch523 [N_Axis]
  Refine = true
  Suppressed = false
  Type = 0
FEATURE [Sketcher::SketchObject] Sketch524
  ArcFitTolerance = 1e-06
  AttachmentSupport = -> [Pad364]
  ExternalGeometry = -> [Pad364]
  FullyConstrained = true
  MakeInternals = false
  MapMode = 5
  Placement = pos=(0,1.8e-15,0) rot=(-1,0,0;1.5708rad)
  sketch-geometry (8):
    g0: LineSegment StartX=-31.45 StartY=-10.2 StartZ=0 EndX=-31.45 EndY=-15.2 EndZ=0
    g1: LineSegment StartX=-31.45 StartY=-15.2 StartZ=0 EndX=-29.65 EndY=-15.2 EndZ=0
    g2: LineSegment StartX=-29.65 StartY=-15.2 StartZ=0 EndX=-29.65 EndY=-10.2 EndZ=0
    g3: LineSegment StartX=-29.65 StartY=-10.2 StartZ=0 EndX=-31.45 EndY=-10.2 EndZ=0
    g4: LineSegment StartX=-21.95 StartY=-10.2 StartZ=0 EndX=-21.95 EndY=-15.2 EndZ=0
    g5: LineSegment StartX=-21.95 StartY=-15.2 StartZ=0 EndX=-20.15 EndY=-15.2 EndZ=0
    g6: LineSegment StartX=-20.15 StartY=-15.2 StartZ=0 EndX=-20.15 EndY=-10.2 EndZ=0
    g7: LineSegment StartX=-20.15 StartY=-10.2 StartZ=0 EndX=-21.95 EndY=-10.2 EndZ=0
  constraints (27):
    c: Coincident(g0,g1)
    c: Coincident(g1,g2)
    c: Coincident(g2,g3)
    c: Coincident(g3,g0)
    c: Vertical(g0)
    c: Vertical(g2)
    c: Horizontal(g1)
    c: Horizontal(g3)
    c: Coincident(g4,g5)
    c: Coincident(g5,g6)
    c: Coincident(g6,g7)
    c: Coincident(g7,g4)
    c: Vertical(g4)
    c: Vertical(g6)
    c: Horizontal(g5)
    c: Horizontal(g7)
    c: DistanceX(g-4,g-4) = 4.5
    c: DistanceX(g-3,g-3) = 4.5
    c: DistanceX(g3,g3) = 1.8
    c: DistanceX(g7,g7) = 1.8
    c: DistanceY(g0,g0) = 5
    c: DistanceY(g4,g4) = 5
    c: DistanceX(g-4,g0) = 1.35
    c: DistanceX(g-3,g4) = 1.35
    c: DistanceY(g-6,g-3) = 7.4
    c: DistanceY(g4,g-3) = 1.2
    c: DistanceY(g0,g-4) = 1.2
FEATURE [PartDesign::Pocket] Pocket237
  BaseFeature = -> Pad364
  Direction = (0,-1,-2e-16)
  Length = 7.6
  Length2 = 5
  Placement = pos=(0,0,0) rot=(1,0,0;1.5708rad)
  Profile = -> Sketch524
  ReferenceAxis = -> Sketch524 [N_Axis]
  Refine = true
  Suppressed = false
  Type = 0
FEATURE [Sketcher::SketchObject] Sketch525
  ArcFitTolerance = 1e-06
  AttachmentSupport = -> [Pocket237]
  ExternalGeometry = -> [Pocket237]
  FullyConstrained = true
  MakeInternals = false
  MapMode = 5
  Placement = pos=(0,-2,0) rot=(1,0,0;1.5708rad)
  sketch-geometry (4):
    g0: LineSegment StartX=-28.3 StartY=14.4 StartZ=0 EndX=-28.3 EndY=13.4 EndZ=0
    g1: LineSegment StartX=-28.3 StartY=13.4 StartZ=0 EndX=-23.3 EndY=13.4 EndZ=0
    g2: LineSegment StartX=-23.3 StartY=13.4 StartZ=0 EndX=-23.3 EndY=14.4 EndZ=0
    g3: LineSegment StartX=-23.3 StartY=14.4 StartZ=0 EndX=-28.3 EndY=14.4 EndZ=0
  constraints (12):
    c: Coincident(g0,g1)
    c: Coincident(g1,g2)
    c: Coincident(g2,g3)
    c: Coincident(g3,g0)
    c: Vertical(g0)
    c: Vertical(g2)
    c: Horizontal(g1)
    c: Horizontal(g3)
    c: PointOnObject(g0,g-3)
    c: PointOnObject(g1,g-4)
    c: DistanceY(g0,g0) = 1
    c: DistanceY(g0,g-3) = 2
FEATURE [PartDesign::Pad] Pad365
  BaseFeature = -> Pocket237
  Direction = (0,-1,2e-16)
  Length = 6
  Length2 = 10
  Placement = pos=(0,0,0) rot=(1,0,0;1.5708rad)
  Profile = -> Sketch525
  ReferenceAxis = -> Sketch525 [N_Axis]
  Refine = true
  Suppressed = false
  Type = 0
FEATURE [Sketcher::SketchObject] Sketch526
  ArcFitTolerance = 1e-06
  AttachmentSupport = -> [Pad365]
  ExternalGeometry = -> [Pad365]
  FullyConstrained = true
  MakeInternals = false
  MapMode = 5
  Placement = pos=(0,-8,0) rot=(1,0,0;1.5708rad)
  sketch-geometry (4):
    g0: LineSegment StartX=-28.3 StartY=13.4 StartZ=0 EndX=-28.3 EndY=10.4 EndZ=0
    g1: LineSegment StartX=-28.3 StartY=10.4 StartZ=0 EndX=-23.3 EndY=10.4 EndZ=0
    g2: LineSegment StartX=-23.3 StartY=10.4 StartZ=0 EndX=-23.3 EndY=13.4 EndZ=0
    g3: LineSegment StartX=-23.3 StartY=13.4 StartZ=0 EndX=-28.3 EndY=13.4 EndZ=0
  constraints (11):
    c: Coincident(g0,g1)
    c: Coincident(g1,g2)
    c: Coincident(g2,g3)
    c: Coincident(g3,g0)
    c: Vertical(g0)
    c: Vertical(g2)
    c: Horizontal(g1)
    c: Horizontal(g3)
    c: Coincident(g0,g-3)
    c: PointOnObject(g1,g-4)
    c: DistanceY(g1,g-6) = 4
FEATURE [PartDesign::Pad] Pad366
  BaseFeature = -> Pad365
  Direction = (0,-1,2e-16)
  Length = 1
  Length2 = 10
  Placement = pos=(0,0,0) rot=(1,0,0;1.5708rad)
  Profile = -> Sketch526
  ReferenceAxis = -> Sketch526 [N_Axis]
  Refine = true
  Reversed = true
  Suppressed = false
  Type = 0
FEATURE [Sketcher::SketchObject] Sketch527
  ArcFitTolerance = 1e-06
  AttachmentSupport = -> [Pad366]
  ExternalGeometry = -> [Pad366]
  FullyConstrained = true
  MakeInternals = false
  MapMode = 5
  Placement = pos=(0,1.8e-15,0) rot=(-1,0,0;1.5708rad)
  sketch-geometry (4):
    g0: LineSegment StartX=-28.3 StartY=-10.4 StartZ=0 EndX=-28.3 EndY=-13.4 EndZ=0
    g1: LineSegment StartX=-28.3 StartY=-13.4 StartZ=0 EndX=-23.3 EndY=-13.4 EndZ=0
    g2: LineSegment StartX=-23.3 StartY=-13.4 StartZ=0 EndX=-23.3 EndY=-10.4 EndZ=0
    g3: LineSegment StartX=-23.3 StartY=-10.4 StartZ=0 EndX=-28.3 EndY=-10.4 EndZ=0
  constraints (10):
    c: Coincident(g0,g1)
    c: Coincident(g1,g2)
    c: Coincident(g2,g3)
    c: Coincident(g3,g0)
    c: Vertical(g0)
    c: Vertical(g2)
    c: Horizontal(g1)
    c: Horizontal(g3)
    c: Coincident(g0,g-4)
    c: Coincident(g1,g-3)
FEATURE [PartDesign::Pocket] Pocket238
  BaseFeature = -> Pad366
  Direction = (0,-1,-2e-16)
  Length = 2
  Length2 = 5
  Placement = pos=(0,0,0) rot=(1,0,0;1.5708rad)
  Profile = -> Sketch527
  ReferenceAxis = -> Sketch527 [N_Axis]
  Refine = true
  Suppressed = false
  Type = 0
FEATURE [Sketcher::SketchObject] Sketch528
  ArcFitTolerance = 1e-06
  AttachmentSupport = -> [Pocket238]
  ExternalGeometry = -> [Pocket238]
  FullyConstrained = true
  MakeInternals = false
  MapMode = 5
  Placement = pos=(0,-2,0) rot=(1,0,0;1.5708rad)
  sketch-geometry (4):
    g0: LineSegment StartX=-4.1 StartY=17.8 StartZ=0 EndX=-4.1 EndY=11 EndZ=0
    g1: LineSegment StartX=-4.1 StartY=11 StartZ=0 EndX=-2.6 EndY=11 EndZ=0
    g2: LineSegment StartX=-2.6 StartY=11 StartZ=0 EndX=-2.6 EndY=17.8 EndZ=0
    g3: LineSegment StartX=-2.6 StartY=17.8 StartZ=0 EndX=-4.1 EndY=17.8 EndZ=0
  constraints (10):
    c: Coincident(g0,g1)
    c: Coincident(g1,g2)
    c: Coincident(g2,g3)
    c: Coincident(g3,g0)
    c: Vertical(g0)
    c: Vertical(g2)
    c: Horizontal(g1)
    c: Coincident(g0,g-3)
    c: PointOnObject(g1,g-4)
    c: Coincident(g2,g-3)
FEATURE [PartDesign::Pad] Pad367
  BaseFeature = -> Pocket238
  Direction = (0,-1,2e-16)
  Length = 0.3
  Length2 = 10
  Placement = pos=(0,0,0) rot=(1,0,0;1.5708rad)
  Profile = -> Sketch528
  ReferenceAxis = -> Sketch528 [N_Axis]
  Refine = true
  Suppressed = false
  Type = 0
FEATURE [PartDesign::Pad] Pad368
  BaseFeature = -> Pad367
  Direction = (1,0,0)
  Length = 0.6
  Length2 = 10
  Placement = pos=(0,0,0) rot=(1,0,0;1.5708rad)
  Profile = -> Pad367 [Face82]
  Refine = true
  Suppressed = false
  Type = 0
FEATURE [PartDesign::Pad] Pad369
  BaseFeature = -> Pad368
  Direction = (-1,0,0)
  Length = 0.6
  Length2 = 10
  Placement = pos=(0,0,0) rot=(1,0,0;1.5708rad)
  Profile = -> Pad368 [Face88]
  Refine = true
  Suppressed = false
  Type = 0
FEATURE [PartDesign::Pad] Pad370
  BaseFeature = -> Pad369
  Direction = (1,0,0)
  Length = 0.2
  Length2 = 10
  Placement = pos=(0,0,0) rot=(1,0,0;1.5708rad)
  Profile = -> Pad369 [Face28]
  Refine = true
  Suppressed = false
  Type = 0
FEATURE [PartDesign::Pad] Pad371
  BaseFeature = -> Pad370
  Direction = (-1,0,0)
  Length = 0.2
  Length2 = 10
  Placement = pos=(0,0,0) rot=(1,0,0;1.5708rad)
  Profile = -> Pad370 [Face27]
  Refine = true
  Suppressed = false
  Type = 0
FEATURE [PartDesign::Pocket] Pocket239
  BaseFeature = -> Pad371
  Direction = (-1,0,0)
  Length = 0.4
  Length2 = 5
  Placement = pos=(0,0,0) rot=(1,0,0;1.5708rad)
  Profile = -> Pad371 [Face40]
  Refine = true
  Suppressed = false
  Type = 0
FEATURE [PartDesign::Pocket] Pocket240
  BaseFeature = -> Pocket239
  Direction = (1,0,0)
  Length = 0.4
  Length2 = 5
  Placement = pos=(0,0,0) rot=(1,0,0;1.5708rad)
  Profile = -> Pocket239 [Face38]
  Refine = true
  Suppressed = false
  Type = 0
FEATURE [PartDesign::Pad] Pad372
  BaseFeature = -> Pocket240
  Direction = (1,0,0)
  Length = 0.6
  Length2 = 10
  Placement = pos=(0,0,0) rot=(1,0,0;1.5708rad)
  Profile = -> Pocket240 [Face39]
  Refine = true
  Suppressed = false
  Type = 0
FEATURE [PartDesign::Pad] Pad373
  BaseFeature = -> Pad372
  Direction = (-1,0,0)
  Length = 0.6
  Length2 = 10
  Placement = pos=(0,0,0) rot=(1,0,0;1.5708rad)
  Profile = -> Pad372 [Face39]
  Refine = true
  Suppressed = false
  Type = 0
FEATURE [PartDesign::Pocket] Pocket241
  BaseFeature = -> Pad373
  Direction = (0,1,0)
  Length = 2
  Length2 = 5
  Placement = pos=(0,0,0) rot=(1,0,0;1.5708rad)
  Profile = -> Pad373 [Face97,Face98]
  Refine = true
  Suppressed = false
  Type = 0
FEATURE [PartDesign::Pad] Pad374
  BaseFeature = -> Pocket241
  Direction = (0,1,0)
  Length = 2
  Length2 = 10
  Placement = pos=(0,0,0) rot=(1,0,0;1.5708rad)
  Profile = -> Pocket241 [Face102,Face106]
  Refine = true
  Suppressed = false
  Type = 0
FEATURE [PartDesign::Pocket] Pocket242
  BaseFeature = -> Pad374
  Direction = (0,1,0)
  Length = 3.6
  Length2 = 5
  Placement = pos=(0,0,0) rot=(1,0,0;1.5708rad)
  Profile = -> Pad374 [Face90,Face84]
  Refine = true
  Suppressed = false
  Type = 0
FEATURE [PartDesign::Pad] Pad375
  BaseFeature = -> Pocket242
  Direction = (1,0,0)
  Length = 1.2
  Length2 = 10
  Placement = pos=(0,0,0) rot=(1,0,0;1.5708rad)
  Profile = -> Pocket242 [Face26]
  Refine = true
  Suppressed = false
  Type = 0
FEATURE [Sketcher::SketchObject] Sketch529
  ArcFitTolerance = 1e-06
  AttachmentSupport = -> [Pad375]
  ExternalGeometry = -> [Pad375]
  FullyConstrained = true
  MakeInternals = false
  MapMode = 5
  Placement = pos=(0,-2,9e-16) rot=(1,0,0;1.5708rad)
  sketch-geometry (3):
    g0: Circle CenterX=-38.15 CenterY=4.5 CenterZ=0 NormalX=0 NormalY=0 NormalZ=1 AngleXU=0 Radius=1.2
    g1: Circle CenterX=-13.45 CenterY=4.5 CenterZ=0 NormalX=0 NormalY=0 NormalZ=1 AngleXU=0 Radius=1.2
    g2: LineSegment [constr] StartX=-38.15 StartY=4.5 StartZ=0 EndX=-13.45 EndY=4.5 EndZ=0
  constraints (8):
    c: Radius(g1) = 1.2
    c: Radius(g0) = 1.2
    c: DistanceX(g1,g-3) = 1.75
    c: DistanceY(g1,g-3) = 2.2
    c: Coincident(g2,g0)
    c: Coincident(g2,g1)
    c: Horizontal(g2)
    c: DistanceX(g-4,g0) = 1.75
FEATURE [PartDesign::Pad] Pad376
  BaseFeature = -> Pad375
  Direction = (0,-1,2e-16)
  Length = 3.6
  Length2 = 10
  Placement = pos=(0,0,0) rot=(1,0,0;1.5708rad)
  Profile = -> Sketch529
  ReferenceAxis = -> Sketch529 [N_Axis]
  Refine = true
  Suppressed = false
  Type = 0
FEATURE [PartDesign::Pad] Pad377
  BaseFeature = -> Pad376
  Direction = (0,-2e-16,-1)
  Length = 0.9
  Length2 = 10
  Placement = pos=(0,0,0) rot=(1,0,0;1.5708rad)
  Profile = -> Pad376 [Face18,Face9]
  Refine = true
  Suppressed = false
  Type = 0
FEATURE [Sketcher::SketchObject] Sketch507
  ArcFitTolerance = 1e-06
  AttachmentSupport = -> [Pad377]
  ExternalGeometry = -> [Pad377]
  FullyConstrained = true
  MakeInternals = false
  MapMode = 5
  Placement = pos=(0,-2,0) rot=(1,0,0;1.5708rad)
  sketch-geometry (8):
    g0: LineSegment StartX=13.5 StartY=-2.6 StartZ=0 EndX=13.5 EndY=-4.6 EndZ=0
    g1: LineSegment StartX=13.5 StartY=-4.6 StartZ=0 EndX=17.35 EndY=-4.6 EndZ=0
    g2: LineSegment StartX=17.35 StartY=-4.6 StartZ=0 EndX=17.35 EndY=-9.9 EndZ=0
    g3: LineSegment StartX=17.35 StartY=-9.9 StartZ=0 EndX=19.55 EndY=-9.9 EndZ=0
    g4: LineSegment StartX=19.55 StartY=-9.9 StartZ=0 EndX=19.55 EndY=-4.6 EndZ=0
    g5: LineSegment StartX=19.55 StartY=-4.6 StartZ=0 EndX=23.4 EndY=-4.6 EndZ=0
    g6: LineSegment StartX=23.4 StartY=-4.6 StartZ=0 EndX=23.4 EndY=-2.6 EndZ=0
    g7: LineSegment StartX=23.4 StartY=-2.6 StartZ=0 EndX=13.5 EndY=-2.6 EndZ=0
  constraints (25):
    c: Vertical(g0)
    c: Coincident(g1,g0)
    c: Horizontal(g1)
    c: Coincident(g2,g1)
    c: Vertical(g2)
    c: Coincident(g3,g2)
    c: Horizontal(g3)
    c: Coincident(g4,g3)
    c: Vertical(g4)
    c: Coincident(g5,g4)
    c: Horizontal(g5)
    c: Coincident(g6,g5)
    c: Vertical(g6)
    c: Coincident(g7,g6)
    c: Coincident(g7,g0)
    c: Horizontal(g7)
    c: DistanceX(g3,g3) = 2.2
    c: DistanceY(g0,g0) = 2
    c: DistanceY(g6,g6) = 2
    c: DistanceY(g-4,g2) = 1.9
    c: DistanceY(g-4,g1) = 7.2
    c: DistanceX(g-3,g-3) = 9.9
    c: DistanceX(g-4,g2) = 3.85
    c: PointOnObject(g0,g-4)
    c: PointOnObject(g6,g-5)
FEATURE [PartDesign::Pad] Pad350
  BaseFeature = -> Pad377
  Direction = (0,-1,2e-16)
  Length = 4.3
  Length2 = 10
  Placement = pos=(0,0,0) rot=(1,0,0;1.5708rad)
  Profile = -> Sketch507
  ReferenceAxis = -> Sketch507 [N_Axis]
  Refine = true
  Suppressed = false
  Type = 0
FEATURE [Sketcher::SketchObject] Sketch530
  ArcFitTolerance = 1e-06
  AttachmentSupport = -> [Pad350]
  ExternalGeometry = -> [Pad350]
  FullyConstrained = true
  MakeInternals = false
  MapMode = 5
  Placement = pos=(0,-2,0) rot=(1,0,0;1.5708rad)
  sketch-geometry (8):
    g0: LineSegment StartX=9.45 StartY=0.3 StartZ=0 EndX=9.45 EndY=8.05 EndZ=0
    g1: LineSegment StartX=9.45 StartY=8.05 StartZ=0 EndX=27.45 EndY=8.05 EndZ=0
    g2: LineSegment StartX=27.45 StartY=8.05 StartZ=0 EndX=27.45 EndY=0.3 EndZ=0
    g3: LineSegment StartX=27.45 StartY=0.3 StartZ=0 EndX=28.85 EndY=0.3 EndZ=0
    g4: LineSegment StartX=28.85 StartY=0.3 StartZ=0 EndX=28.85 EndY=9.45 EndZ=0
    g5: LineSegment StartX=28.85 StartY=9.45 StartZ=0 EndX=8.05 EndY=9.45 EndZ=0
    g6: LineSegment StartX=8.05 StartY=9.45 StartZ=0 EndX=8.05 EndY=0.3 EndZ=0
    g7: LineSegment StartX=9.45 StartY=0.3 StartZ=0 EndX=8.05 EndY=0.3 EndZ=0
  constraints (26):
    c: Vertical(g0)
    c: Coincident(g1,g0)
    c: Horizontal(g1)
    c: Coincident(g2,g1)
    c: Vertical(g2)
    c: Coincident(g3,g2)
    c: Horizontal(g3)
    c: Coincident(g4,g3)
    c: Vertical(g4)
    c: Coincident(g5,g4)
    c: Horizontal(g5)
    c: Coincident(g6,g5)
    c: Vertical(g6)
    c: Coincident(g7,g0)
    c: Coincident(g7,g6)
    c: Horizontal(g7)
    c: DistanceX(g7,g7) = 1.4
    c: DistanceX(g3,g3) = 1.4
    c: DistanceY(g0,g5) = 1.4
    c: DistanceX(g1,g1) = 18
    c: DistanceY(g0,g0) = 7.75
    c: DistanceY(g2,g2) = 7.75
    c: DistanceX(g-3,g-3) = 9.9
    c: DistanceX(g0,g-3) = 4.05
    c: DistanceX(g-3,g2) = 4.05
    c: DistanceY(g-4,g0) = 0.3
FEATURE [PartDesign::Pad] Pad378
  BaseFeature = -> Pad350
  Direction = (0,-1,2e-16)
  Length = 8.6
  Length2 = 10
  Placement = pos=(0,0,0) rot=(1,0,0;1.5708rad)
  Profile = -> Sketch530
  ReferenceAxis = -> Sketch530 [N_Axis]
  Refine = true
  Suppressed = false
  Type = 0
FEATURE [Sketcher::SketchObject] Sketch531
  ArcFitTolerance = 1e-06
  AttachmentSupport = -> [Pad378]
  ExternalGeometry = -> [Pad378]
  FullyConstrained = true
  MakeInternals = false
  MapMode = 5
  Placement = pos=(0,-2,0) rot=(1,0,0;1.5708rad)
  sketch-geometry (4):
    g0: LineSegment StartX=21.4 StartY=4.35 StartZ=0 EndX=21.4 EndY=8.05 EndZ=0
    g1: LineSegment StartX=21.4 StartY=8.05 StartZ=0 EndX=15.5 EndY=8.05 EndZ=0
    g2: LineSegment StartX=15.5 StartY=8.05 StartZ=0 EndX=15.5 EndY=4.35 EndZ=0
    g3: LineSegment StartX=15.5 StartY=4.35 StartZ=0 EndX=21.4 EndY=4.35 EndZ=0
  constraints (14):
    c: Coincident(g0,g1)
    c: Coincident(g1,g2)
    c: Coincident(g2,g3)
    c: Coincident(g3,g0)
    c: Vertical(g0)
    c: Vertical(g2)
    c: Horizontal(g1)
    c: Horizontal(g3)
    c: PointOnObject(g1,g-3)
    c: DistanceY(g2,g2) = 3.7
    c: DistanceX(g3,g3) = 5.9
    c: DistanceX(g-3,g-3) = 18
    c: DistanceX(g-4,g2) = 6.05
    c: DistanceX(g0,g-5) = 6.05
FEATURE [PartDesign::Pocket] Pocket234
  BaseFeature = -> Pad378
  Direction = (0,1,-2e-16)
  Length = 5
  Length2 = 5
  Placement = pos=(0,0,0) rot=(1,0,0;1.5708rad)
  Profile = -> Sketch531
  ReferenceAxis = -> Sketch531 [N_Axis]
  Refine = true
  Suppressed = false
  Type = 0
FEATURE [Sketcher::SketchObject] Sketch532
  ArcFitTolerance = 1e-06
  AttachmentSupport = -> [Pocket234]
  ExternalGeometry = -> [Pocket234]
  FullyConstrained = true
  MakeInternals = false
  MapMode = 5
  Placement = pos=(0,-2,0) rot=(1,0,0;1.5708rad)
  sketch-geometry (8):
    g0: LineSegment StartX=9.45 StartY=0.3 StartZ=0 EndX=12.05 EndY=0.3 EndZ=0
    g1: LineSegment StartX=12.05 StartY=0.3 StartZ=0 EndX=12.05 EndY=1.7 EndZ=0
    g2: LineSegment StartX=12.05 StartY=1.7 StartZ=0 EndX=9.45 EndY=1.7 EndZ=0
    g3: LineSegment StartX=9.45 StartY=1.7 StartZ=0 EndX=9.45 EndY=0.3 EndZ=0
    g4: LineSegment StartX=27.45 StartY=0.3 StartZ=0 EndX=27.45 EndY=1.7 EndZ=0
    g5: LineSegment StartX=27.45 StartY=1.7 StartZ=0 EndX=24.85 EndY=1.7 EndZ=0
    g6: LineSegment StartX=24.85 StartY=1.7 StartZ=0 EndX=24.85 EndY=0.3 EndZ=0
    g7: LineSegment StartX=24.85 StartY=0.3 StartZ=0 EndX=27.45 EndY=0.3 EndZ=0
  constraints (23):
    c: DistanceX(g-3,g-3) = 1.4
    c: Coincident(g0,g1)
    c: Coincident(g1,g2)
    c: Coincident(g2,g3)
    c: Coincident(g3,g0)
    c: Horizontal(g0)
    c: Horizontal(g2)
    c: Vertical(g1)
    c: Vertical(g3)
    c: Coincident(g0,g-4)
    c: Coincident(g4,g5)
    c: Coincident(g5,g6)
    c: Coincident(g6,g7)
    c: Coincident(g7,g4)
    c: Vertical(g4)
    c: Vertical(g6)
    c: Horizontal(g5)
    c: Horizontal(g7)
    c: Coincident(g4,g-5)
    c: DistanceY(g1,g1) = 1.4
    c: DistanceY(g6,g6) = 1.4
    c: DistanceX(g-7,g0) = 4
    c: DistanceX(g6,g-6) = 4
FEATURE [PartDesign::Pad] Pad379
  BaseFeature = -> Pocket234
  Direction = (0,-1,2e-16)
  Length = 1.8
  Length2 = 10
  Placement = pos=(0,0,0) rot=(1,0,0;1.5708rad)
  Profile = -> Sketch532
  ReferenceAxis = -> Sketch532 [N_Axis]
  Refine = true
  Suppressed = false
  Type = 0
FEATURE [Sketcher::SketchObject] Sketch533
  ArcFitTolerance = 1e-06
  AttachmentSupport = -> [Pad379]
  ExternalGeometry = -> [Pad379]
  FullyConstrained = true
  MakeInternals = false
  MapMode = 5
  Placement = pos=(0,3e-15,8.05) rot=(1,0,0;3.14159rad)
  sketch-geometry (4):
    g0: LineSegment StartX=16.95 StartY=10.3 StartZ=0 EndX=16.95 EndY=8.9 EndZ=0
    g1: LineSegment StartX=16.95 StartY=8.9 StartZ=0 EndX=19.95 EndY=8.9 EndZ=0
    g2: LineSegment StartX=19.95 StartY=8.9 StartZ=0 EndX=19.95 EndY=10.3 EndZ=0
    g3: LineSegment StartX=19.95 StartY=10.3 StartZ=0 EndX=16.95 EndY=10.3 EndZ=0
  constraints (13):
    c: Coincident(g0,g1)
    c: Coincident(g1,g2)
    c: Coincident(g2,g3)
    c: Coincident(g3,g0)
    c: Vertical(g0)
    c: Vertical(g2)
    c: Horizontal(g1)
    c: Horizontal(g3)
    c: DistanceX(g1,g1) = 3
    c: DistanceX(g-3,g-3) = 18
    c: DistanceX(g-3,g0) = 7.5
    c: DistanceY(g2,g2) = 1.4
    c: DistanceY(g2,g-3) = 0.3
FEATURE [PartDesign::Pad] Pad380
  BaseFeature = -> Pad379
  Direction = (0,0,-1)
  Length = 1
  Length2 = 10
  Placement = pos=(0,0,0) rot=(1,0,0;1.5708rad)
  Profile = -> Sketch533
  ReferenceAxis = -> Sketch533 [N_Axis]
  Refine = true
  Suppressed = false
  Type = 0
FEATURE [PartDesign::Chamfer] Chamfer006
  Angle = 45
  Base = -> Pad380 [Edge402,Edge399]
  BaseFeature = -> Pad380
  ChamferType = 0
  FlipDirection = false
  Placement = pos=(0,0,0) rot=(1,0,0;1.5708rad)
  Refine = true
  Size = 0.5
  Size2 = 1
  SupportTransform = false
  Suppressed = false
  UseAllEdges = false
FEATURE [PartDesign::Pad] Pad381
  BaseFeature = -> Chamfer006
  Direction = (-1,0,0)
  Length = 0.1
  Length2 = 10
  Placement = pos=(0,0,0) rot=(1,0,0;1.5708rad)
  Profile = -> Chamfer006 [Face15]
  Refine = true
  Suppressed = false
  Type = 0
FEATURE [PartDesign::Pad] Pad382
  BaseFeature = -> Pad381
  Direction = (1,0,0)
  Length = 0.1
  Length2 = 10
  Placement = pos=(0,0,0) rot=(1,0,0;1.5708rad)
  Profile = -> Pad381 [Face10]
  Refine = true
  Suppressed = false
  Type = 0
FEATURE [PartDesign::Chamfer] Chamfer005
  Angle = 45
  Base = -> Pad382 [Edge252,Edge228]
  BaseFeature = -> Pad382
  ChamferType = 0
  FlipDirection = false
  Placement = pos=(0,0,0) rot=(1,0,0;1.5708rad)
  Refine = true
  Size = 1
  Size2 = 1
  SupportTransform = false
  Suppressed = false
  UseAllEdges = false
FEATURE [PartDesign::Pocket] Pocket243
  BaseFeature = -> Chamfer005
  Direction = (0,1,-3e-16)
  Length = 0.8
  Length2 = 5
  Placement = pos=(0,0,0) rot=(1,0,0;1.5708rad)
  Profile = -> Chamfer005 [Face158,Face157]
  Refine = true
  Suppressed = false
  Type = 0
FEATURE [PartDesign::Pad] Pad383
  BaseFeature = -> Pocket243
  Direction = (0,-2e-16,-1)
  Length = 0.1
  Length2 = 10
  Placement = pos=(0,0,0) rot=(1,0,0;1.5708rad)
  Profile = -> Pocket243 [Face152]
  Refine = true
  Suppressed = false
  Type = 0
FEATURE [Sketcher::SketchObject] Sketch534
  ArcFitTolerance = 1e-06
  AttachmentSupport = -> [Pad383]
  ExternalGeometry = -> [Pad383]
  FullyConstrained = true
  MakeInternals = false
  MapMode = 5
  Placement = pos=(23.4,0,0) rot=(0.707107,0,0.707107;3.14159rad)
  sketch-geometry (3):
    g0: LineSegment StartX=-2.6 StartY=6.3 StartZ=0 EndX=-4 EndY=6.3 EndZ=0
    g1: LineSegment StartX=-2.6 StartY=6.3 StartZ=0 EndX=-1.6 EndY=4.3 EndZ=0
    g2: LineSegment StartX=-1.6 StartY=4.3 StartZ=0 EndX=-4 EndY=6.3 EndZ=0
  constraints (8):
    c: Coincident(g0,g-4)
    c: PointOnObject(g0,g-4)
    c: Coincident(g1,g0)
    c: PointOnObject(g1,g-3)
    c: Coincident(g2,g1)
    c: Coincident(g2,g0)
    c: DistanceX(g0,g0) = 1.4
    c: DistanceY(g1,g1) = 2
FEATURE [PartDesign::Pocket] Pocket244
  BaseFeature = -> Pad383
  Direction = (-1,0,2e-16)
  Length = 10
  Length2 = 5
  Placement = pos=(0,0,0) rot=(1,0,0;1.5708rad)
  Profile = -> Sketch534
  ReferenceAxis = -> Sketch534 [N_Axis]
  Refine = true
  Suppressed = false
  Type = 0
FEATURE [PartDesign::Chamfer] Chamfer007
  Angle = 45
  Base = -> Pocket244 [Edge380,Edge377]
  BaseFeature = -> Pocket244
  ChamferType = 0
  FlipDirection = false
  Placement = pos=(0,0,0) rot=(1,0,0;1.5708rad)
  Refine = true
  Size = 0.5
  Size2 = 1
  SupportTransform = false
  Suppressed = false
  UseAllEdges = false
FEATURE [Sketcher::SketchObject] Sketch535
  ArcFitTolerance = 1e-06
  AttachmentSupport = -> [Chamfer007]
  ExternalGeometry = -> [Chamfer007]
  FullyConstrained = true
  MakeInternals = false
  MapMode = 5
  Placement = pos=(27.35,0,0) rot=(0.707107,0,-0.707107;3.14159rad)
  sketch-geometry (4):
    g0: LineSegment StartX=-1.7 StartY=2 StartZ=0 EndX=-1.7 EndY=10.1 EndZ=0
    g1: LineSegment StartX=-1.7 StartY=10.1 StartZ=0 EndX=-3.7 EndY=10.1 EndZ=0
    g2: LineSegment StartX=-3.7 StartY=10.1 StartZ=0 EndX=-3.7 EndY=2 EndZ=0
    g3: LineSegment StartX=-3.7 StartY=2 StartZ=0 EndX=-1.7 EndY=2 EndZ=0
  constraints (11):
    c: Coincident(g0,g1)
    c: Coincident(g1,g2)
    c: Coincident(g2,g3)
    c: Coincident(g3,g0)
    c: Vertical(g0)
    c: Vertical(g2)
    c: Horizontal(g1)
    c: Horizontal(g3)
    c: Coincident(g0,g-5)
    c: PointOnObject(g1,g-4)
    c: DistanceX(g1,g1) = 2
FEATURE [PartDesign::Pad] Pad384
  BaseFeature = -> Chamfer007
  Direction = (-1,0,-2e-16)
  Length = 0.2
  Length2 = 10
  Placement = pos=(0,0,0) rot=(1,0,0;1.5708rad)
  Profile = -> Sketch535
  ReferenceAxis = -> Sketch535 [N_Axis]
  Refine = true
  Suppressed = false
  Type = 0
FEATURE [Sketcher::SketchObject] Sketch536
  ArcFitTolerance = 1e-06
  AttachmentSupport = -> [Pad384]
  ExternalGeometry = -> [Pad384]
  FullyConstrained = true
  MakeInternals = false
  MapMode = 5
  Placement = pos=(9.55,0,0) rot=(0.707107,0,0.707107;3.14159rad)
  sketch-geometry (4):
    g0: LineSegment StartX=1.7 StartY=2 StartZ=0 EndX=3.7 EndY=2 EndZ=0
    g1: LineSegment StartX=3.7 StartY=2 StartZ=0 EndX=3.7 EndY=10.1 EndZ=0
    g2: LineSegment StartX=3.7 StartY=10.1 StartZ=0 EndX=1.7 EndY=10.1 EndZ=0
    g3: LineSegment StartX=1.7 StartY=10.1 StartZ=0 EndX=1.7 EndY=2 EndZ=0
  constraints (11):
    c: Coincident(g0,g1)
    c: Coincident(g1,g2)
    c: Coincident(g2,g3)
    c: Coincident(g3,g0)
    c: Horizontal(g0)
    c: Horizontal(g2)
    c: Vertical(g1)
    c: Vertical(g3)
    c: Coincident(g0,g-4)
    c: PointOnObject(g1,g-5)
    c: DistanceX(g2,g2) = 2
FEATURE [PartDesign::Pad] Pad385
  BaseFeature = -> Pad384
  Direction = (1,0,-2e-16)
  Length = 0.2
  Length2 = 10
  Placement = pos=(0,0,0) rot=(1,0,0;1.5708rad)
  Profile = -> Sketch536
  ReferenceAxis = -> Sketch536 [N_Axis]
  Refine = true
  Suppressed = false
  Type = 0
FEATURE [Sketcher::SketchObject] Sketch537
  ArcFitTolerance = 1e-06
  AttachmentSupport = -> [Pad385]
  ExternalGeometry = -> [Pad385]
  FullyConstrained = true
  MakeInternals = false
  MapMode = 5
  Placement = pos=(4e-16,4e-16,1.7) rot=(1,0,0;3.14159rad)
  sketch-geometry (6):
    g0: LineSegment StartX=27.35 StartY=10.1 StartZ=0 EndX=27.15 EndY=10.1 EndZ=0
    g1: LineSegment StartX=27.15 StartY=10.1 StartZ=0 EndX=27.15 EndY=9.9 EndZ=0
    g2: LineSegment StartX=27.15 StartY=9.9 StartZ=0 EndX=27.35 EndY=10.1 EndZ=0
    g3: LineSegment StartX=9.55 StartY=10.1 StartZ=0 EndX=9.75 EndY=10.1 EndZ=0
    g4: LineSegment StartX=9.75 StartY=10.1 StartZ=0 EndX=9.75 EndY=9.9 EndZ=0
    g5: LineSegment StartX=9.75 StartY=9.9 StartZ=0 EndX=9.55 EndY=10.1 EndZ=0
  constraints (14):
    c: Coincident(g0,g-5)
    c: Coincident(g0,g-6)
    c: Coincident(g1,g0)
    c: PointOnObject(g1,g-6)
    c: Coincident(g2,g1)
    c: Coincident(g2,g0)
    c: Angle(g0,g2) = 0.785398
    c: Coincident(g3,g-3)
    c: Coincident(g3,g-4)
    c: Coincident(g4,g3)
    c: PointOnObject(g4,g-4)
    c: Coincident(g5,g4)
    c: Coincident(g5,g3)
    c: Angle(g5,g3) = 0.785398
FEATURE [PartDesign::Pocket] Pocket245
  BaseFeature = -> Pad385
  Direction = (0,0,1)
  Length = 2
  Length2 = 5
  Placement = pos=(0,0,0) rot=(1,0,0;1.5708rad)
  Profile = -> Sketch537
  ReferenceAxis = -> Sketch537 [N_Axis]
  Refine = true
  Suppressed = false
  Type = 0
FEATURE [PartDesign::Pocket] Pocket246
  BaseFeature = -> Pocket245
  Direction = (0,1,-3e-16)
  Length = 2.6
  Length2 = 5
  Placement = pos=(0,0,0) rot=(1,0,0;1.5708rad)
  Profile = -> Pocket245 [Face172,Face173]
  Refine = true
  Suppressed = false
  Type = 0
FEATURE [Sketcher::SketchObject] Sketch538
  ArcFitTolerance = 1e-06
  AttachmentSupport = -> [Pocket246]
  ExternalGeometry = -> [Pocket246]
  FullyConstrained = true
  MakeInternals = false
  MapMode = 5
  Placement = pos=(0,6e-16,0) rot=(-1,0,0;1.5708rad)
  sketch-geometry (8):
    g0: LineSegment StartX=-11.7 StartY=0.9 StartZ=0 EndX=-15.7 EndY=0.9 EndZ=0
    g1: LineSegment StartX=-15.7 StartY=0.9 StartZ=0 EndX=-15.7 EndY=0.1 EndZ=0
    g2: LineSegment StartX=-15.7 StartY=0.1 StartZ=0 EndX=-11.7 EndY=0.1 EndZ=0
    g3: LineSegment StartX=-11.7 StartY=0.1 StartZ=0 EndX=-11.7 EndY=0.9 EndZ=0
    g4: LineSegment StartX=-39.9 StartY=0.9 StartZ=0 EndX=-39.9 EndY=0.1 EndZ=0
    g5: LineSegment StartX=-39.9 StartY=0.1 StartZ=0 EndX=-35.9 EndY=0.1 EndZ=0
    g6: LineSegment StartX=-35.9 StartY=0.1 StartZ=0 EndX=-35.9 EndY=0.9 EndZ=0
    g7: LineSegment StartX=-35.9 StartY=0.9 StartZ=0 EndX=-39.9 EndY=0.9 EndZ=0
  constraints (22):
    c: Coincident(g0,g1)
    c: Coincident(g1,g2)
    c: Coincident(g2,g3)
    c: Coincident(g3,g0)
    c: Horizontal(g0)
    c: Horizontal(g2)
    c: Vertical(g1)
    c: Vertical(g3)
    c: Coincident(g0,g-6)
    c: Coincident(g4,g5)
    c: Coincident(g5,g6)
    c: Coincident(g6,g7)
    c: Coincident(g7,g4)
    c: Vertical(g4)
    c: Vertical(g6)
    c: Horizontal(g5)
    c: Horizontal(g7)
    c: Coincident(g4,g-4)
    c: DistanceX(g2,g2) = 4
    c: DistanceX(g5,g5) = 4
    c: DistanceY(g6,g6) = 0.8
    c: DistanceY(g3,g3) = 0.8
FEATURE [PartDesign::Pad] Pad386
  BaseFeature = -> Pocket246
  Direction = (0,1,2e-16)
  Length = 0.8
  Length2 = 10
  Placement = pos=(0,0,0) rot=(1,0,0;1.5708rad)
  Profile = -> Sketch538
  ReferenceAxis = -> Sketch538 [N_Axis]
  Refine = true
  Suppressed = false
  Type = 0
FEATURE [PartDesign::Chamfer] Chamfer008
  Angle = 45
  Base = -> Pad386 [Edge463,Edge453]
  BaseFeature = -> Pad386
  ChamferType = 0
  FlipDirection = false
  Placement = pos=(0,0,0) rot=(1,0,0;1.5708rad)
  Refine = true
  Size = 0.5
  Size2 = 1
  SupportTransform = false
  Suppressed = false
  UseAllEdges = false
FEATURE [PartDesign::Chamfer] Chamfer
  Angle = 45
  Base = -> Chamfer008 [Edge338]
  BaseFeature = -> Chamfer008
  ChamferType = 0
  FlipDirection = false
  Placement = pos=(0,0,0) rot=(1,0,0;1.5708rad)
  Refine = true
  Size = 1
  Size2 = 1
  SupportTransform = false
  Suppressed = false
  UseAllEdges = false
FEATURE [PartDesign::SubShapeBinder] Binder
  BindCopyOnChange = 0
  BindMode = 2
  ClaimChildren = false
  Context = -> Part [Body.Binder.]
  Fuse = false
  MakeFace = true
  OffsetFill = false
  OffsetIntersection = false
  OffsetJoinType = 0
  OffsetOpenResult = false
  PartialLoad = false
  Refine = true
  Relative = true
  _Version = 2
FEATURE [Sketcher::SketchObject] Sketch
  ArcFitTolerance = 1e-06
  AttachmentSupport = -> [Binder]
  ExternalGeometry = -> [Binder]
  FullyConstrained = true
  MakeInternals = false
  MapMode = 5
  Placement = pos=(0,0,-11.5) rot=(1,0,0;3.14159rad)
  sketch-geometry (9):
    g0: Circle CenterX=-66.55 CenterY=9.45 CenterZ=0 NormalX=0 NormalY=0 NormalZ=1 AngleXU=0 Radius=2.4
    g1: LineSegment StartX=-66.55 StartY=12.85 StartZ=0 EndX=-75.15 EndY=12.85 EndZ=0
    g2: LineSegment StartX=-75.15 StartY=12.85 StartZ=0 EndX=-75.15 EndY=6.05 EndZ=0
    g3: LineSegment StartX=-75.15 StartY=6.05 StartZ=0 EndX=-66.55 EndY=6.05 EndZ=0
    g4: ArcOfCircle CenterX=-66.55 CenterY=9.45 CenterZ=0 NormalX=0 NormalY=0 NormalZ=1 AngleXU=0 Radius=3.4 StartAngle=4.71239 EndAngle=7.85398
    g5: LineSegment [constr] StartX=-66.55 StartY=12.85 StartZ=0 EndX=-66.55 EndY=9.45 EndZ=0
    g6: LineSegment [constr] StartX=-66.55 StartY=9.45 StartZ=0 EndX=-66.55 EndY=6.05 EndZ=0
    g7: Circle CenterX=-72.1 CenterY=9.45 CenterZ=0 NormalX=0 NormalY=0 NormalZ=1 AngleXU=0 Radius=1.05
    g8: LineSegment [constr] StartX=-66.55 StartY=9.45 StartZ=0 EndX=-72.1 EndY=9.45 EndZ=0
  constraints (24):
    c: Coincident(g0,g-3)
    c: Radius(g-3) = 2.35
    c: Radius(g0) = 2.4
    c: Horizontal(g1)
    c: Coincident(g2,g1)
    c: Vertical(g2)
    c: Coincident(g3,g2)
    c: Horizontal(g3)
    c: Coincident(g4,g3)
    c: Coincident(g4,g1)
    c: Coincident(g5,g1)
    c: Coincident(g5,g4)
    c: Coincident(g4,g0)
    c: Vertical(g5)
    c: Coincident(g6,g0)
    c: Coincident(g6,g3)
    c: Vertical(g6)
    c: Coincident(g8,g0)
    c: Coincident(g8,g7)
    c: Horizontal(g8)
    c: Radius(g4) = 3.4
    c: Radius(g7) = 1.05
    c: DistanceX(g7,g0) = 5.55
    c: DistanceX(g1,g1) = 8.6
FEATURE [PartDesign::Pad] Pad
  Direction = (0,0,-1)
  Length = 2
  Length2 = 10
  Profile = -> Sketch
  ReferenceAxis = -> Sketch [N_Axis]
  Refine = true
  Suppressed = false
  Type = 0
FEATURE [Sketcher::SketchObject] Sketch539
  ArcFitTolerance = 1e-06
  AttachmentSupport = -> [Pad]
  ExternalGeometry = -> [Pad]
  FullyConstrained = true
  MakeInternals = false
  MapMode = 5
  Placement = pos=(0,0,-13.5) rot=(1,0,0;3.14159rad)
  sketch-geometry (4):
    g0: LineSegment StartX=-75.15 StartY=14.45 StartZ=0 EndX=-75.15 EndY=4.45 EndZ=0
    g1: LineSegment StartX=-75.15 StartY=4.45 StartZ=0 EndX=-60.15 EndY=4.45 EndZ=0
    g2: LineSegment StartX=-60.15 StartY=4.45 StartZ=0 EndX=-60.15 EndY=14.45 EndZ=0
    g3: LineSegment StartX=-60.15 StartY=14.45 StartZ=0 EndX=-75.15 EndY=14.45 EndZ=0
  constraints (12):
    c: Coincident(g0,g1)
    c: Coincident(g1,g2)
    c: Coincident(g2,g3)
    c: Coincident(g3,g0)
    c: Vertical(g0)
    c: Vertical(g2)
    c: Horizontal(g1)
    c: Horizontal(g3)
    c: DistanceX(g3,g3) = 15
    c: PointOnObject(g-3,g0)
    c: DistanceY(g0,g0) = 10
    c: DistanceY(g-4,g0) = 5
FEATURE [PartDesign::Pad] Pad387
  BaseFeature = -> Pad
  Direction = (0,0,-1)
  Length = 2
  Length2 = 10
  Profile = -> Sketch539
  ReferenceAxis = -> Sketch539 [N_Axis]
  Refine = true
  Suppressed = false
  Type = 0
FEATURE [Sketcher::SketchObject] Sketch540
  ArcFitTolerance = 1e-06
  AttachmentSupport = -> [Pad387]
  ExternalGeometry = -> [Pad387]
  FullyConstrained = true
  MakeInternals = false
  MapMode = 5
  Placement = pos=(-60.15,0,0) rot=(0.57735,0.57735,0.57735;2.0944rad)
  sketch-geometry (1):
    g0: Circle CenterX=-9.45 CenterY=-14.5 CenterZ=0 NormalX=0 NormalY=0 NormalZ=1 AngleXU=0 Radius=4.5
  constraints (4):
    c: Diameter(g0) = 9
    c: DistanceX(g-4,g-4) = 10
    c: DistanceX(g-3,g0) = 5
    c: DistanceY(g0,g-3) = 1
FEATURE [PartDesign::Pad] Pad388
  BaseFeature = -> Pad387
  Direction = (1,0,0)
  Length = 3
  Length2 = 10
  Profile = -> Sketch540
  ReferenceAxis = -> Sketch540 [N_Axis]
  Refine = true
  Reversed = true
  Suppressed = false
  Type = 0
FEATURE [Sketcher::SketchObject] Sketch541
  ArcFitTolerance = 1e-06
  AttachmentSupport = -> [Pad388]
  ExternalGeometry = -> [Pad388]
  FullyConstrained = true
  MakeInternals = false
  MapMode = 5
  Placement = pos=(-63.15,0,0) rot=(0.57735,-0.57735,-0.57735;2.0944rad)
  sketch-geometry (2):
    g0: ArcOfCircle CenterX=9.45 CenterY=-14.5 CenterZ=0 NormalX=0 NormalY=0 NormalZ=1 AngleXU=0 Radius=4.5 StartAngle=0.729728 EndAngle=2.41186
    g1: LineSegment StartX=6.0959 StartY=-11.5 StartZ=0 EndX=12.8041 EndY=-11.5 EndZ=0
  constraints (6):
    c: Tangent(g0,g-3) = -1.5708
    c: PointOnObject(g0,g-3)
    c: PointOnObject(g1,g-4)
    c: PointOnObject(g1,g-4)
    c: Coincident(g1,g0)
    c: Coincident(g1,g0)
FEATURE [PartDesign::Pocket] Pocket
  BaseFeature = -> Pad388
  Direction = (1,0,0)
  Length = 5
  Length2 = 5
  Profile = -> Sketch541
  ReferenceAxis = -> Sketch541 [N_Axis]
  Refine = true
  Suppressed = false
  Type = 0
FEATURE [PartDesign::Pocket] Pocket247
  BaseFeature = -> Pocket
  Direction = (0,0,-1)
  Length = 1.1
  Length2 = 5
  Profile = -> Pocket [Face18,Face19]
  Refine = true
  Suppressed = false
  Type = 0
FEATURE [Sketcher::SketchObject] Sketch542
  ArcFitTolerance = 1e-06
  AttachmentSupport = -> [Pocket247]
  ExternalGeometry = -> [Pocket247]
  FullyConstrained = true
  MakeInternals = false
  MapMode = 5
  Placement = pos=(0,0,-15.5) rot=(1,0,0;3.14159rad)
  sketch-geometry (4):
    g0: LineSegment StartX=-75.15 StartY=10.45 StartZ=0 EndX=-75.15 EndY=8.45 EndZ=0
    g1: LineSegment StartX=-75.15 StartY=8.45 StartZ=0 EndX=-60.15 EndY=8.45 EndZ=0
    g2: LineSegment StartX=-60.15 StartY=8.45 StartZ=0 EndX=-60.15 EndY=10.45 EndZ=0
    g3: LineSegment StartX=-60.15 StartY=10.45 StartZ=0 EndX=-75.15 EndY=10.45 EndZ=0
  constraints (13):
    c: Coincident(g0,g1)
    c: Coincident(g1,g2)
    c: Coincident(g2,g3)
    c: Coincident(g3,g0)
    c: Vertical(g0)
    c: Vertical(g2)
    c: Horizontal(g1)
    c: Horizontal(g3)
    c: PointOnObject(g0,g-4)
    c: PointOnObject(g1,g-3)
    c: DistanceY(g-4,g-4) = 10
    c: DistanceY(g0,g0) = 2
    c: DistanceY(g0,g-4) = 4
FEATURE [PartDesign::Pad] Pad389
  BaseFeature = -> Pocket247
  Direction = (0,0,-1)
  Length = 4
  Length2 = 10
  Profile = -> Sketch542
  ReferenceAxis = -> Sketch542 [N_Axis]
  Refine = true
  Suppressed = false
  Type = 0
FEATURE [Sketcher::SketchObject] Sketch543
  ArcFitTolerance = 1e-06
  AttachmentSupport = -> [Pad389]
  ExternalGeometry = -> [Pad389]
  FullyConstrained = true
  MakeInternals = false
  MapMode = 5
  Placement = pos=(-63.15,0,0) rot=(0.57735,-0.57735,-0.57735;2.0944rad)
  sketch-geometry (2):
    g0: ArcOfCircle CenterX=9.45 CenterY=-14.5 CenterZ=0 NormalX=0 NormalY=0 NormalZ=1 AngleXU=0 Radius=3 StartAngle=3.48143 EndAngle=5.94335
    g1: LineSegment StartX=6.62157 StartY=-15.5 StartZ=0 EndX=12.2784 EndY=-15.5 EndZ=0
  constraints (6):
    c: PointOnObject(g0,g-3)
    c: PointOnObject(g0,g-4)
    c: Radius(g0) = 3
    c: Coincident(g0,g-5)
    c: Coincident(g1,g0)
    c: Coincident(g1,g0)
FEATURE [PartDesign::Pad] Pad390
  BaseFeature = -> Pad389
  Direction = (-1,0,0)
  Length = 2
  Length2 = 10
  Profile = -> Sketch543
  ReferenceAxis = -> Sketch543 [N_Axis]
  Refine = true
  Suppressed = false
  Type = 0
FEATURE [Sketcher::SketchObject] Sketch544
  ArcFitTolerance = 1e-06
  AttachmentSupport = -> [Pad390]
  ExternalGeometry = -> [Pad390]
  FullyConstrained = true
  MakeInternals = false
  MapMode = 5
  Placement = pos=(-65.15,0,0) rot=(0.57735,-0.57735,-0.57735;2.0944rad)
  sketch-geometry (2):
    g0: ArcOfCircle CenterX=9.45 CenterY=-14.5 CenterZ=0 NormalX=0 NormalY=0 NormalZ=1 AngleXU=0 Radius=4.5 StartAngle=3.36569 EndAngle=6.05909
    g1: LineSegment StartX=5.06252 StartY=-15.5 StartZ=0 EndX=13.8375 EndY=-15.5 EndZ=0
  constraints (4):
    c: Coincident(g0,g-4)
    c: Tangent(g0,g-3) = -1.5708
    c: Coincident(g1,g0)
    c: Coincident(g1,g0)
FEATURE [PartDesign::Pad] Pad391
  BaseFeature = -> Pad390
  Direction = (-1,0,0)
  Length = 10
  Length2 = 10
  Profile = -> Sketch544
  ReferenceAxis = -> Sketch544 [N_Axis]
  Refine = true
  Suppressed = false
  Type = 0
FEATURE [Sketcher::SketchObject] Sketch545
  ArcFitTolerance = 1e-06
  AttachmentSupport = -> [Pad391]
  ExternalGeometry = -> [Pad391]
  FullyConstrained = true
  MakeInternals = false
  MapMode = 5
  Placement = pos=(-75.15,0,-1.368e-13) rot=(0.57735,-0.57735,-0.57735;2.0944rad)
  sketch-geometry (6):
    g0: ArcOfCircle CenterX=9.45 CenterY=-14.5 CenterZ=0 NormalX=0 NormalY=0 NormalZ=1 AngleXU=0 Radius=4.5 StartAngle=0.224093 EndAngle=0.714295
    g1: ArcOfCircle CenterX=9.45 CenterY=-14.5 CenterZ=0 NormalX=0 NormalY=0 NormalZ=1 AngleXU=0 Radius=4.5 StartAngle=2.4273 EndAngle=2.9175
    g2: LineSegment StartX=6.05 StartY=-11.5521 StartZ=0 EndX=6.05 EndY=-13.5 EndZ=0
    g3: LineSegment StartX=6.05 StartY=-13.5 StartZ=0 EndX=5.06252 EndY=-13.5 EndZ=0
    g4: LineSegment StartX=12.85 StartY=-11.5521 StartZ=0 EndX=12.85 EndY=-13.5 EndZ=0
    g5: LineSegment StartX=12.85 StartY=-13.5 StartZ=0 EndX=13.8375 EndY=-13.5 EndZ=0
  constraints (16):
    c: Radius(g-6) = 4.5
    c: PointOnObject(g0,g-4)
    c: PointOnObject(g1,g-5)
    c: PointOnObject(g1,g-8)
    c: Coincident(g1,g-6)
    c: Coincident(g0,g1)
    c: Radius(g1) = 4.5
    c: Coincident(g2,g1)
    c: Coincident(g2,g-8)
    c: Coincident(g3,g2)
    c: Coincident(g3,g1)
    c: Coincident(g0,g-9)
    c: Coincident(g4,g0)
    c: Coincident(g4,g-7)
    c: Coincident(g5,g4)
    c: Coincident(g5,g0)
FEATURE [PartDesign::Pad] Pad392
  BaseFeature = -> Pad391
  Direction = (-1,0,-1.8e-15)
  Length = 8.6
  Length2 = 10
  Profile = -> Sketch545
  ReferenceAxis = -> Sketch545 [N_Axis]
  Refine = true
  Reversed = true
  Suppressed = false
  Type = 0
FEATURE [Sketcher::SketchObject] Sketch546
  ArcFitTolerance = 1e-06
  AttachmentSupport = -> [Pad392]
  ExternalGeometry = -> [Pad392]
  FullyConstrained = true
  MakeInternals = false
  MapMode = 5
  Placement = pos=(0,0,-11.5) rot=(0,0,1;0rad)
  sketch-geometry (6):
    g0: LineSegment StartX=-66.55 StartY=-6.05 StartZ=0 EndX=-66.55 EndY=-5.06252 EndZ=0
    g1: LineSegment StartX=-66.55 StartY=-5.06252 StartZ=0 EndX=-67.55 EndY=-5.06252 EndZ=0
    g2: LineSegment StartX=-67.55 StartY=-5.06252 StartZ=0 EndX=-66.55 EndY=-6.05 EndZ=0
    g3: LineSegment StartX=-66.55 StartY=-12.85 StartZ=0 EndX=-66.55 EndY=-13.8375 EndZ=0
    g4: LineSegment StartX=-66.55 StartY=-13.8375 StartZ=0 EndX=-67.55 EndY=-13.8375 EndZ=0
    g5: LineSegment StartX=-67.55 StartY=-13.8375 StartZ=0 EndX=-66.55 EndY=-12.85 EndZ=0
  constraints (14):
    c: Coincident(g0,g-4)
    c: Coincident(g0,g-7)
    c: Coincident(g1,g0)
    c: PointOnObject(g1,g-7)
    c: Coincident(g2,g1)
    c: Coincident(g2,g0)
    c: DistanceX(g1,g1) = 1
    c: Coincident(g3,g-6)
    c: Coincident(g3,g-8)
    c: Coincident(g4,g3)
    c: PointOnObject(g4,g-8)
    c: Coincident(g5,g4)
    c: Coincident(g5,g3)
    c: DistanceX(g4,g4) = 1
FEATURE [PartDesign::Pocket] Pocket248
  BaseFeature = -> Pad392
  Direction = (0,0,-1)
  Length = 2
  Length2 = 5
  Profile = -> Sketch546
  ReferenceAxis = -> Sketch546 [N_Axis]
  Refine = true
  Suppressed = false
  Type = 0
FEATURE [Sketcher::SketchObject] Sketch547
  ArcFitTolerance = 1e-06
  AttachmentSupport = -> [Pocket248]
  ExternalGeometry = -> [Pocket248]
  FullyConstrained = true
  MakeInternals = false
  MapMode = 5
  Placement = pos=(-60.15,0,9.44e-14) rot=(0.57735,0.57735,0.57735;2.0944rad)
  sketch-geometry (1):
    g0: Circle CenterX=-9.45 CenterY=-14.5 CenterZ=0 NormalX=0 NormalY=0 NormalZ=1 AngleXU=0 Radius=3
  constraints (2):
    c: Coincident(g0,g-3)
    c: Radius(g0) = 3
FEATURE [PartDesign::Pad] Pad393
  BaseFeature = -> Pocket248
  Direction = (1,1e-16,-1.4e-15)
  Length = 1
  Length2 = 10
  Profile = -> Sketch547
  ReferenceAxis = -> Sketch547 [N_Axis]
  Refine = true
  Suppressed = false
  Type = 0
FEATURE [Sketcher::SketchObject] Sketch548
  ArcFitTolerance = 1e-06
  AttachmentSupport = -> [Pad393]
  ExternalGeometry = -> [Pad393]
  FullyConstrained = true
  MakeInternals = false
  MapMode = 5
  Placement = pos=(-59.15,-4.67e-14,8.1e-14) rot=(0.57735,0.57735,0.57735;2.0944rad)
  sketch-geometry (4):
    g0: LineSegment StartX=-10.45 StartY=-19.5 StartZ=0 EndX=-10.45 EndY=-17.3284 EndZ=0
    g1: LineSegment StartX=-8.45 StartY=-19.5 StartZ=0 EndX=-8.45 EndY=-17.3284 EndZ=0
    g2: LineSegment StartX=-8.45 StartY=-19.5 StartZ=0 EndX=-10.45 EndY=-19.5 EndZ=0
    g3: ArcOfCircle CenterX=-9.45 CenterY=-14.5 CenterZ=0 NormalX=0 NormalY=0 NormalZ=1 AngleXU=0 Radius=3 StartAngle=4.37255 EndAngle=5.05223
  constraints (11):
    c: Coincident(g0,g-3)
    c: PointOnObject(g0,g-4)
    c: Vertical(g0)
    c: Coincident(g1,g-3)
    c: PointOnObject(g1,g-4)
    c: Vertical(g1)
    c: Coincident(g2,g1)
    c: Coincident(g2,g0)
    c: Coincident(g3,g0)
    c: Coincident(g3,g1)
    c: Radius(g3) = 3
FEATURE [PartDesign::Pad] Pad394
  BaseFeature = -> Pad393
  Direction = (1,0,-1.3e-15)
  Length = 1
  Length2 = 10
  Profile = -> Sketch548
  ReferenceAxis = -> Sketch548 [N_Axis]
  Refine = true
  Reversed = true
  Suppressed = false
  Type = 0
FEATURE [Sketcher::SketchObject] Sketch549
  ArcFitTolerance = 1e-06
  AttachmentSupport = -> [Pad394]
  ExternalGeometry = -> [Pad394]
  FullyConstrained = true
  MakeInternals = false
  MapMode = 5
  Placement = pos=(0,0,-15.5) rot=(1,0,0;3.14159rad)
  sketch-geometry (6):
    g0: LineSegment StartX=-75.15 StartY=5.06252 StartZ=0 EndX=-75.15 EndY=4.45 EndZ=0
    g1: LineSegment StartX=-75.15 StartY=4.45 StartZ=0 EndX=-71.6762 EndY=4.45 EndZ=0
    g2: LineSegment StartX=-71.6762 StartY=4.45 StartZ=0 EndX=-75.15 EndY=5.06252 EndZ=0
    g3: LineSegment StartX=-75.15 StartY=14.45 StartZ=0 EndX=-75.15 EndY=13.8375 EndZ=0
    g4: LineSegment StartX=-75.15 StartY=14.45 StartZ=0 EndX=-71.6762 EndY=14.45 EndZ=0
    g5: LineSegment StartX=-71.6762 StartY=14.45 StartZ=0 EndX=-75.15 EndY=13.8375 EndZ=0
  constraints (14):
    c: Coincident(g0,g-6)
    c: Coincident(g0,g-6)
    c: Coincident(g1,g0)
    c: PointOnObject(g1,g-5)
    c: Coincident(g2,g1)
    c: Coincident(g2,g0)
    c: Coincident(g3,g-4)
    c: Coincident(g3,g-4)
    c: Coincident(g4,g3)
    c: PointOnObject(g4,g-3)
    c: Coincident(g5,g4)
    c: Coincident(g5,g3)
    c: Angle(g4,g5) = 0.174533
    c: Angle(g2,g1) = 0.174533
FEATURE [PartDesign::Pocket] Pocket249
  BaseFeature = -> Pad394
  Direction = (0,0,1)
  Length = 5
  Length2 = 5
  Profile = -> Sketch549
  ReferenceAxis = -> Sketch549 [N_Axis]
  Refine = true
  Suppressed = false
  Type = 0
FEATURE [Sketcher::SketchObject] Sketch550
  ArcFitTolerance = 1e-06
  AttachmentSupport = -> [Pocket249]
  ExternalGeometry = -> [Pocket249]
  FullyConstrained = true
  MakeInternals = false
  MapMode = 5
  Placement = pos=(-1.34e-14,-8.45,-4.255e-13) rot=(0,0.707107,0.707107;3.14159rad)
  sketch-geometry (3):
    g0: LineSegment StartX=75.15 StartY=-18.8875 StartZ=0 EndX=75.15 EndY=-19.5 EndZ=0
    g1: LineSegment StartX=75.15 StartY=-18.8875 StartZ=0 EndX=71.6762 EndY=-19.5 EndZ=0
    g2: LineSegment StartX=75.15 StartY=-19.5 StartZ=0 EndX=71.6762 EndY=-19.5 EndZ=0
  constraints (7):
    c: Coincident(g0,g-3)
    c: Coincident(g0,g-4)
    c: Coincident(g1,g0)
    c: PointOnObject(g1,g-4)
    c: Coincident(g2,g0)
    c: Coincident(g2,g1)
    c: Angle(g2,g1) = 0.174533
FEATURE [PartDesign::Pocket] Pocket250
  BaseFeature = -> Pocket249
  Direction = (-1.6e-15,-1,-5.04e-14)
  Length = 5
  Length2 = 5
  Profile = -> Sketch550
  ReferenceAxis = -> Sketch550 [N_Axis]
  Refine = true
  Suppressed = false
  Type = 0
FEATURE [Sketcher::SketchObject] Sketch551
  ArcFitTolerance = 1e-06
  AttachmentSupport = -> [Pocket250]
  ExternalGeometry = -> [Pocket250]
  FullyConstrained = false
  MakeInternals = false
  MapMode = 5
  Placement = pos=(2.81e-14,0,-19.5) rot=(1,0,0;3.14159rad)
  sketch-geometry (1):
    g0: Circle CenterX=-66.55 CenterY=9.45 CenterZ=0 NormalX=0 NormalY=0 NormalZ=1 AngleXU=0 Radius=3
  constraints (1):
    c: Radius(g0) = 3
FEATURE [PartDesign::Pad] Pad395
  BaseFeature = -> Pocket250
  Direction = (1.4e-15,0,-1)
  Length = 4
  Length2 = 10
  Profile = -> Sketch551
  ReferenceAxis = -> Sketch551 [N_Axis]
  Refine = true
  Reversed = true
  Suppressed = false
  Type = 0
FEATURE [Sketcher::SketchObject] Sketch552
  ArcFitTolerance = 1e-06
  AttachmentSupport = -> [Pad395]
  ExternalGeometry = -> [Pad395]
  FullyConstrained = true
  MakeInternals = false
  MapMode = 5
  Placement = pos=(5.09e-14,2.05e-14,-19.5) rot=(1,0,0;3.14159rad)
  sketch-geometry (1):
    g0: Circle CenterX=-66.55 CenterY=9.45 CenterZ=0 NormalX=0 NormalY=0 NormalZ=1 AngleXU=0 Radius=2
  constraints (2):
    c: Coincident(g0,g-3)
    c: Radius(g0) = 2
FEATURE [PartDesign::Pocket] Pocket251
  BaseFeature = -> Pad395
  Direction = (-2.6e-15,-1e-15,1)
  Length = 2
  Length2 = 5
  Profile = -> Sketch552
  ReferenceAxis = -> Sketch552 [N_Axis]
  Refine = true
  Suppressed = false
  Type = 0
FEATURE [Sketcher::SketchObject] Sketch553
  ArcFitTolerance = 1e-06
  AttachmentSupport = -> [Pocket251]
  ExternalGeometry = -> [Pocket251]
  FullyConstrained = true
  MakeInternals = false
  MapMode = 5
  Placement = pos=(5.18e-14,1.8e-14,-17.5) rot=(1,0,0;3.14159rad)
  sketch-geometry (1):
    g0: Circle CenterX=-66.55 CenterY=9.45 CenterZ=0 NormalX=0 NormalY=0 NormalZ=1 AngleXU=0 Radius=1
  constraints (2):
    c: Coincident(g0,g-3)
    c: Radius(g0) = 1
FEATURE [PartDesign::Pocket] Pocket252
  BaseFeature = -> Pocket251
  Direction = (-3e-15,-1e-15,1)
  Length = 5
  Length2 = 5
  Profile = -> Sketch553
  ReferenceAxis = -> Sketch553 [N_Axis]
  Refine = true
  Suppressed = false
  Type = 0
FEATURE [Sketcher::SketchObject] Sketch554
  ArcFitTolerance = 1e-06
  AttachmentSupport = -> [Pocket252]
  ExternalGeometry = -> [Pocket252]
  FullyConstrained = true
  MakeInternals = false
  MapMode = 5
  Placement = pos=(-75.15,0,-6.46e-14) rot=(0.57735,-0.57735,-0.57735;2.0944rad)
  sketch-geometry (1):
    g0: Circle CenterX=9.45 CenterY=-14.5 CenterZ=0 NormalX=0 NormalY=0 NormalZ=1 AngleXU=0 Radius=2.8
  constraints (2):
    c: Coincident(g0,g-3)
    c: Diameter(g0) = 5.6
FEATURE [PartDesign::Pad] Pad396
  BaseFeature = -> Pocket252
  Direction = (-1,0,0)
  Length = 2.5
  Length2 = 10
  Profile = -> Sketch554
  ReferenceAxis = -> Sketch554 [N_Axis]
  Refine = true
  Suppressed = false
  Type = 0
FEATURE [Sketcher::SketchObject] Sketch555
  ArcFitTolerance = 1e-06
  AttachmentSupport = -> [Pad396]
  ExternalGeometry = -> [Pad396]
  FullyConstrained = true
  MakeInternals = false
  MapMode = 5
  Placement = pos=(-77.65,0,0) rot=(0.57735,-0.57735,-0.57735;2.0944rad)
  sketch-geometry (1):
    g0: Circle CenterX=9.45 CenterY=-14.5 CenterZ=0 NormalX=0 NormalY=0 NormalZ=1 AngleXU=0 Radius=2.55
  constraints (3):
    c: Coincident(g0,g-3)
    c: Diameter(g-3) = 5.6
    c: Diameter(g0) = 5.1
FEATURE [PartDesign::Pad] Pad397
  BaseFeature = -> Pad396
  Direction = (-1,0,0)
  Length = 0.5
  Length2 = 10
  Profile = -> Sketch555
  ReferenceAxis = -> Sketch555 [N_Axis]
  Refine = true
  Suppressed = false
  Type = 0
FEATURE [Sketcher::SketchObject] Sketch556
  ArcFitTolerance = 1e-06
  AttachmentSupport = -> [Pad397]
  ExternalGeometry = -> [Pad397]
  FullyConstrained = true
  MakeInternals = false
  MapMode = 5
  Placement = pos=(-78.15,0,0) rot=(0.57735,-0.57735,-0.57735;2.0944rad)
  sketch-geometry (1):
    g0: Circle CenterX=9.45 CenterY=-14.5 CenterZ=0 NormalX=0 NormalY=0 NormalZ=1 AngleXU=0 Radius=2.8
  constraints (2):
    c: Coincident(g0,g-3)
    c: Equal(g0,g-3)
FEATURE [PartDesign::Pad] Pad398
  BaseFeature = -> Pad397
  Direction = (-1,0,0)
  Length = 1.7
  Length2 = 10
  Profile = -> Sketch556
  ReferenceAxis = -> Sketch556 [N_Axis]
  Refine = true
  Suppressed = false
  Type = 0
FEATURE [Sketcher::SketchObject] Sketch557
  ArcFitTolerance = 1e-06
  AttachmentSupport = -> [Pad398]
  ExternalGeometry = -> [Pad398]
  FullyConstrained = true
  MakeInternals = false
  MapMode = 5
  Placement = pos=(-79.85,0,0) rot=(0.57735,-0.57735,-0.57735;2.0944rad)
  sketch-geometry (1):
    g0: Circle CenterX=9.45 CenterY=-14.5 CenterZ=0 NormalX=0 NormalY=0 NormalZ=1 AngleXU=0 Radius=2.3
  constraints (3):
    c: Coincident(g0,g-3)
    c: Radius(g-3) = 2.8
    c: Radius(g0) = 2.3
FEATURE [PartDesign::Pad] Pad399
  BaseFeature = -> Pad398
  Direction = (-1,0,0)
  Length = 1
  Length2 = 10
  Profile = -> Sketch557
  ReferenceAxis = -> Sketch557 [N_Axis]
  Refine = true
  Suppressed = false
  Type = 0
FEATURE [Sketcher::SketchObject] Sketch558
  ArcFitTolerance = 1e-06
  AttachmentSupport = -> [Pad399]
  ExternalGeometry = -> [Pad399]
  FullyConstrained = true
  MakeInternals = false
  MapMode = 5
  Placement = pos=(-80.85,0,0) rot=(0.57735,-0.57735,-0.57735;2.0944rad)
  sketch-geometry (1):
    g0: Circle CenterX=9.45 CenterY=-14.5 CenterZ=0 NormalX=0 NormalY=0 NormalZ=1 AngleXU=0 Radius=2.8
  constraints (2):
    c: Coincident(g0,g-3)
    c: Equal(g0,g-3)
FEATURE [PartDesign::Pad] Pad400
  BaseFeature = -> Pad399
  Direction = (-1,0,0)
  Length = 2.5
  Length2 = 10
  Profile = -> Sketch558
  ReferenceAxis = -> Sketch558 [N_Axis]
  Refine = true
  Suppressed = false
  Type = 0
FEATURE [Sketcher::SketchObject] Sketch559
  ArcFitTolerance = 1e-06
  AttachmentSupport = -> [Pad400]
  ExternalGeometry = -> [Pad400]
  FullyConstrained = true
  MakeInternals = false
  MapMode = 5
  Placement = pos=(-83.35,0,0) rot=(0.57735,-0.57735,-0.57735;2.0944rad)
  sketch-geometry (1):
    g0: Circle CenterX=9.45 CenterY=-14.5 CenterZ=0 NormalX=0 NormalY=0 NormalZ=1 AngleXU=0 Radius=2.3
  constraints (2):
    c: Coincident(g0,g-3)
    c: Radius(g0) = 2.3
FEATURE [PartDesign::Pad] Pad401
  BaseFeature = -> Pad400
  Direction = (-1,0,0)
  Length = 1
  Length2 = 10
  Profile = -> Sketch559
  ReferenceAxis = -> Sketch559 [N_Axis]
  Refine = true
  Suppressed = false
  Type = 0
FEATURE [Sketcher::SketchObject] Sketch560
  ArcFitTolerance = 1e-06
  AttachmentSupport = -> [Pad401]
  ExternalGeometry = -> [Pad401]
  FullyConstrained = true
  MakeInternals = false
  MapMode = 5
  Placement = pos=(-84.35,0,0) rot=(0.57735,-0.57735,-0.57735;2.0944rad)
  sketch-geometry (1):
    g0: Circle CenterX=9.45 CenterY=-14.5 CenterZ=0 NormalX=0 NormalY=0 NormalZ=1 AngleXU=0 Radius=2.8
  constraints (2):
    c: Coincident(g0,g-3)
    c: Equal(g0,g-3)
FEATURE [PartDesign::Pad] Pad402
  BaseFeature = -> Pad401
  Direction = (-1,0,0)
  Length = 1.7
  Length2 = 10
  Profile = -> Sketch560
  ReferenceAxis = -> Sketch560 [N_Axis]
  Refine = true
  Suppressed = false
  Type = 0
FEATURE [Sketcher::SketchObject] Sketch561
  ArcFitTolerance = 1e-06
  AttachmentSupport = -> [Pad402]
  ExternalGeometry = -> [Pad402]
  FullyConstrained = true
  MakeInternals = false
  MapMode = 5
  Placement = pos=(-86.05,0,0) rot=(0.57735,-0.57735,-0.57735;2.0944rad)
  sketch-geometry (1):
    g0: Circle CenterX=9.45 CenterY=-14.5 CenterZ=0 NormalX=0 NormalY=0 NormalZ=1 AngleXU=0 Radius=2.55
  constraints (2):
    c: Coincident(g0,g-3)
    c: Radius(g0) = 2.55
FEATURE [PartDesign::Pad] Pad403
  BaseFeature = -> Pad402
  Direction = (-1,0,0)
  Length = 0.5
  Length2 = 10
  Profile = -> Sketch561
  ReferenceAxis = -> Sketch561 [N_Axis]
  Refine = true
  Suppressed = false
  Type = 0
FEATURE [Sketcher::SketchObject] Sketch562
  ArcFitTolerance = 1e-06
  AttachmentSupport = -> [Pad403]
  ExternalGeometry = -> [Pad403]
  FullyConstrained = true
  MakeInternals = false
  MapMode = 5
  Placement = pos=(-86.55,0,0) rot=(0.57735,-0.57735,-0.57735;2.0944rad)
  sketch-geometry (1):
    g0: Circle CenterX=9.45 CenterY=-14.5 CenterZ=0 NormalX=0 NormalY=0 NormalZ=1 AngleXU=0 Radius=2.8
  constraints (2):
    c: Coincident(g0,g-4)
    c: Equal(g0,g-4)
FEATURE [PartDesign::Pad] Pad404
  BaseFeature = -> Pad403
  Direction = (-1,0,0)
  Length = 1.9
  Length2 = 10
  Profile = -> Sketch562
  ReferenceAxis = -> Sketch562 [N_Axis]
  Refine = true
  Suppressed = false
  Type = 0
FEATURE [Sketcher::SketchObject] Sketch563
  ArcFitTolerance = 1e-06
  AttachmentSupport = -> [Pad404]
  ExternalGeometry = -> [Pad404]
  FullyConstrained = true
  MakeInternals = false
  MapMode = 5
  Placement = pos=(0,0,-11.5) rot=(0,0,1;0rad)
  sketch-geometry (4):
    g0: LineSegment StartX=-86.05 StartY=-8.65 StartZ=0 EndX=-86.05 EndY=-10.25 EndZ=0
    g1: LineSegment StartX=-86.05 StartY=-10.25 StartZ=0 EndX=-78.15 EndY=-10.25 EndZ=0
    g2: LineSegment StartX=-78.15 StartY=-10.25 StartZ=0 EndX=-78.15 EndY=-8.65 EndZ=0
    g3: LineSegment StartX=-78.15 StartY=-8.65 StartZ=0 EndX=-86.05 EndY=-8.65 EndZ=0
  constraints (12):
    c: Coincident(g0,g1)
    c: Coincident(g1,g2)
    c: Coincident(g2,g3)
    c: Coincident(g3,g0)
    c: Vertical(g0)
    c: Vertical(g2)
    c: Horizontal(g1)
    c: Horizontal(g3)
    c: PointOnObject(g0,g-4)
    c: PointOnObject(g1,g-3)
    c: DistanceY(g2,g2) = 1.6
    c: DistanceY(g-5,g2) = 0.8
FEATURE [PartDesign::Pad] Pad405
  BaseFeature = -> Pad404
  Direction = (0,0,1)
  Length = 9
  Length2 = 10
  Profile = -> Sketch563
  ReferenceAxis = -> Sketch563 [N_Axis]
  Refine = true
  Reversed = true
  Suppressed = false
  Type = 0
FEATURE [PartDesign::Pad] Pad406
  BaseFeature = -> Pad405
  Direction = (0,0,1)
  Length = 3
  Length2 = 10
  Profile = -> Sketch563
  ReferenceAxis = -> Sketch563 [N_Axis]
  Refine = true
  Suppressed = false
  Type = 0
FEATURE [Sketcher::SketchObject] Sketch564
  ArcFitTolerance = 1e-06
  AttachmentSupport = -> [Pad406]
  ExternalGeometry = -> [Pad406]
  FullyConstrained = true
  MakeInternals = false
  MapMode = 5
  Placement = pos=(0,-8.65,0) rot=(0,0.707107,0.707107;3.14159rad)
  sketch-geometry (12):
    g0: LineSegment StartX=78.15 StartY=-17.1833 StartZ=0 EndX=79.75 EndY=-18.7833 EndZ=0
    g1: LineSegment StartX=79.75 StartY=-18.7833 StartZ=0 EndX=84.45 EndY=-18.7833 EndZ=0
    g2: LineSegment StartX=84.45 StartY=-18.7833 StartZ=0 EndX=86.05 EndY=-17.1833 EndZ=0
    g3: LineSegment StartX=86.05 StartY=-17.1833 StartZ=0 EndX=86.05 EndY=-20.5 EndZ=0
    g4: LineSegment StartX=86.05 StartY=-20.5 StartZ=0 EndX=78.15 EndY=-20.5 EndZ=0
    g5: LineSegment StartX=78.15 StartY=-20.5 StartZ=0 EndX=78.15 EndY=-17.1833 EndZ=0
    g6: LineSegment StartX=78.15 StartY=-11.8167 StartZ=0 EndX=79.75 EndY=-10.2167 EndZ=0
    g7: LineSegment StartX=79.75 StartY=-10.2167 StartZ=0 EndX=84.45 EndY=-10.2167 EndZ=0
    g8: LineSegment StartX=84.45 StartY=-10.2167 StartZ=0 EndX=86.05 EndY=-11.8167 EndZ=0
    g9: LineSegment StartX=86.05 StartY=-11.8167 StartZ=0 EndX=86.05 EndY=-8.5 EndZ=0
    g10: LineSegment StartX=86.05 StartY=-8.5 StartZ=0 EndX=78.15 EndY=-8.5 EndZ=0
    g11: LineSegment StartX=78.15 StartY=-8.5 StartZ=0 EndX=78.15 EndY=-11.8167 EndZ=0
  constraints (28):
    c: Coincident(g0,g-10)
    c: Coincident(g1,g0)
    c: Horizontal(g1)
    c: Coincident(g2,g1)
    c: Coincident(g2,g-9)
    c: Coincident(g3,g2)
    c: Coincident(g3,g-9)
    c: Coincident(g4,g3)
    c: Coincident(g4,g-10)
    c: Coincident(g5,g4)
    c: Coincident(g5,g0)
    c: DistanceY(g0,g-5) = 1.6
    c: Angle(g0,g-11) = 0.785398
    c: Angle(g-14,g2) = 0.785398
    c: Coincident(g6,g-12)
    c: Coincident(g7,g6)
    c: Horizontal(g7)
    c: Coincident(g8,g7)
    c: Coincident(g8,g-13)
    c: Coincident(g9,g8)
    c: Coincident(g9,g-8)
    c: Coincident(g10,g9)
    c: Coincident(g10,g-7)
    c: Coincident(g11,g10)
    c: Coincident(g11,g6)
    c: DistanceY(g-12,g6) = 1.6
    c: Angle(g-12,g6) = 0.785398
    c: Angle(g8,g-13) = 0.785398
FEATURE [PartDesign::Pocket] Pocket253
  BaseFeature = -> Pad406
  Direction = (0,-1,2e-16)
  Length = 5
  Length2 = 5
  Profile = -> Sketch564
  ReferenceAxis = -> Sketch564 [N_Axis]
  Refine = true
  Suppressed = false
  Type = 0
FEATURE [Sketcher::SketchObject] Sketch565
  ArcFitTolerance = 1e-06
  AttachmentSupport = -> [Pocket253]
  ExternalGeometry = -> [Pocket253]
  FullyConstrained = true
  MakeInternals = false
  MapMode = 5
  Placement = pos=(0,-4.45,0) rot=(0,0.707107,0.707107;3.14159rad)
  sketch-geometry (5):
    g0: LineSegment StartX=78.15 StartY=-13.7 StartZ=0 EndX=78.15 EndY=-15.3 EndZ=0
    g1: LineSegment StartX=78.15 StartY=-15.3 StartZ=0 EndX=86.05 EndY=-15.3 EndZ=0
    g2: LineSegment StartX=86.05 StartY=-15.3 StartZ=0 EndX=86.05 EndY=-13.7 EndZ=0
    g3: LineSegment StartX=86.05 StartY=-13.7 StartZ=0 EndX=78.15 EndY=-13.7 EndZ=0
    g4: LineSegment [constr] StartX=78.15 StartY=-14.5 StartZ=0 EndX=86.05 EndY=-14.5 EndZ=0
  constraints (15):
    c: Coincident(g0,g1)
    c: Coincident(g1,g2)
    c: Coincident(g2,g3)
    c: Coincident(g3,g0)
    c: Vertical(g0)
    c: Vertical(g2)
    c: Horizontal(g1)
    c: Horizontal(g3)
    c: PointOnObject(g0,g-3)
    c: PointOnObject(g1,g-4)
    c: DistanceY(g0,g0) = 1.6
    c: DistanceY(g-3,g-3) = 5.36656
    c: Symmetric(g-3,g-3,g4)
    c: Symmetric(g-4,g-4,g4)
    c: DistanceY(g4,g0) = 0.8
FEATURE [PartDesign::Pad] Pad407
  BaseFeature = -> Pocket253
  Direction = (0,1,-2e-16)
  Length = 10
  Length2 = 10
  Profile = -> Sketch565
  ReferenceAxis = -> Sketch565 [N_Axis]
  Refine = true
  Reversed = true
  Suppressed = false
  Type = 0
FEATURE [Sketcher::SketchObject] Sketch566
  ArcFitTolerance = 1e-06
  AttachmentSupport = -> [Pad407]
  ExternalGeometry = -> [Pad407]
  FullyConstrained = true
  MakeInternals = false
  MapMode = 5
  Placement = pos=(0,-3e-15,-13.7) rot=(0,0,1;0rad)
  sketch-geometry (12):
    g0: LineSegment StartX=-86.05 StartY=-6.76672 StartZ=0 EndX=-86.05 EndY=-4.45 EndZ=0
    g1: LineSegment StartX=-86.05 StartY=-4.45 StartZ=0 EndX=-78.15 EndY=-4.45 EndZ=0
    g2: LineSegment StartX=-78.15 StartY=-4.45 StartZ=0 EndX=-78.15 EndY=-6.76672 EndZ=0
    g3: LineSegment StartX=-78.15 StartY=-6.76672 StartZ=0 EndX=-79.75 EndY=-5.16672 EndZ=0
    g4: LineSegment StartX=-79.75 StartY=-5.16672 StartZ=0 EndX=-84.45 EndY=-5.16672 EndZ=0
    g5: LineSegment StartX=-84.45 StartY=-5.16672 StartZ=0 EndX=-86.05 EndY=-6.76672 EndZ=0
    g6: LineSegment StartX=-86.05 StartY=-12.1333 StartZ=0 EndX=-86.05 EndY=-14.45 EndZ=0
    g7: LineSegment StartX=-86.05 StartY=-14.45 StartZ=0 EndX=-78.15 EndY=-14.45 EndZ=0
    g8: LineSegment StartX=-78.15 StartY=-14.45 StartZ=0 EndX=-78.15 EndY=-12.1333 EndZ=0
    g9: LineSegment StartX=-78.15 StartY=-12.1333 StartZ=0 EndX=-79.75 EndY=-13.7333 EndZ=0
    g10: LineSegment StartX=-79.75 StartY=-13.7333 StartZ=0 EndX=-84.45 EndY=-13.7333 EndZ=0
    g11: LineSegment StartX=-84.45 StartY=-13.7333 StartZ=0 EndX=-86.05 EndY=-12.1333 EndZ=0
  constraints (28):
    c: Coincident(g0,g-5)
    c: Coincident(g0,g-5)
    c: Coincident(g1,g0)
    c: Coincident(g1,g-4)
    c: Coincident(g2,g1)
    c: Coincident(g2,g-3)
    c: Coincident(g3,g2)
    c: Coincident(g4,g3)
    c: Horizontal(g4)
    c: Coincident(g5,g4)
    c: Coincident(g5,g0)
    c: Coincident(g6,g-6)
    c: Coincident(g6,g-7)
    c: Coincident(g7,g6)
    c: Coincident(g7,g-8)
    c: Coincident(g8,g7)
    c: Coincident(g8,g-8)
    c: Coincident(g9,g8)
    c: Coincident(g10,g9)
    c: Horizontal(g10)
    c: Coincident(g11,g10)
    c: Coincident(g11,g6)
    c: DistanceY(g-9,g4) = 1.6
    c: DistanceY(g10,g-12) = 1.6
    c: Angle(g11,g-12) = 0.785398
    c: Angle(g-11,g9) = 0.785398
    c: Angle(g-9,g5) = 0.785398
    c: Angle(g3,g-10) = 0.785398
FEATURE [PartDesign::Pocket] Pocket254
  BaseFeature = -> Pad407
  Direction = (0,0,-1)
  Length = 5
  Length2 = 5
  Profile = -> Sketch566
  ReferenceAxis = -> Sketch566 [N_Axis]
  Refine = true
  Suppressed = false
  Type = 0
FEATURE [Sketcher::SketchObject] Sketch567
  ArcFitTolerance = 1e-06
  AttachmentSupport = -> [Pocket254]
  ExternalGeometry = -> [Pocket254]
  FullyConstrained = true
  MakeInternals = false
  MapMode = 5
  Placement = pos=(-88.45,0,0) rot=(0.57735,-0.57735,-0.57735;2.0944rad)
  sketch-geometry (12):
    g0: ArcOfCircle CenterX=9.45 CenterY=-14.5 CenterZ=0 NormalX=0 NormalY=0 NormalZ=1 AngleXU=0 Radius=2.8 StartAngle=1.29963 EndAngle=1.84196
    g1: ArcOfCircle CenterX=9.45 CenterY=-14.5 CenterZ=0 NormalX=0 NormalY=0 NormalZ=1 AngleXU=0 Radius=2.8 StartAngle=2.87042 EndAngle=3.41276
    g2: ArcOfCircle CenterX=9.45 CenterY=-14.5 CenterZ=0 NormalX=0 NormalY=0 NormalZ=1 AngleXU=0 Radius=2.8 StartAngle=6.01202 EndAngle=6.55435
    g3: ArcOfCircle CenterX=9.45 CenterY=-14.5 CenterZ=0 NormalX=0 NormalY=0 NormalZ=1 AngleXU=0 Radius=2.8 StartAngle=4.44122 EndAngle=4.98356
    g4: LineSegment StartX=6.75232 StartY=-15.25 StartZ=0 EndX=8.7 EndY=-15.25 EndZ=0
    g5: LineSegment StartX=8.7 StartY=-15.25 StartZ=0 EndX=8.7 EndY=-17.1977 EndZ=0
    g6: LineSegment StartX=10.2 StartY=-17.1977 StartZ=0 EndX=10.2 EndY=-15.25 EndZ=0
    g7: LineSegment StartX=12.1477 StartY=-15.25 StartZ=0 EndX=10.2 EndY=-15.25 EndZ=0
    g8: LineSegment StartX=12.1477 StartY=-13.75 StartZ=0 EndX=10.2 EndY=-13.75 EndZ=0
    g9: LineSegment StartX=10.2 StartY=-11.8023 StartZ=0 EndX=10.2 EndY=-13.75 EndZ=0
    g10: LineSegment StartX=8.7 StartY=-11.8023 StartZ=0 EndX=8.7 EndY=-13.75 EndZ=0
    g11: LineSegment StartX=8.7 StartY=-13.75 StartZ=0 EndX=6.75232 EndY=-13.75 EndZ=0
  constraints (36):
    c: Tangent(g0,g-3) = -1.5708
    c: PointOnObject(g0,g-3)
    c: Tangent(g1,g-3) = -1.5708
    c: PointOnObject(g1,g-3)
    c: Tangent(g2,g-3) = -1.5708
    c: PointOnObject(g2,g-3)
    c: Tangent(g3,g-3) = -1.5708
    c: PointOnObject(g3,g-3)
    c: Coincident(g4,g1)
    c: Horizontal(g4)
    c: Coincident(g5,g4)
    c: Coincident(g5,g3)
    c: Vertical(g5)
    c: Coincident(g6,g3)
    c: Vertical(g6)
    c: Coincident(g7,g2)
    c: Coincident(g7,g6)
    c: Horizontal(g7)
    c: Coincident(g8,g2)
    c: Horizontal(g8)
    c: Coincident(g9,g0)
    c: Coincident(g9,g8)
    c: Vertical(g9)
    c: Coincident(g10,g0)
    c: Vertical(g10)
    c: Coincident(g11,g10)
    c: Coincident(g11,g1)
    c: Horizontal(g11)
    c: DistanceX(g0,g0) = 1.5
    c: DistanceX(g3,g3) = 1.5
    c: DistanceY(g1,g1) = 1.5
    c: DistanceY(g2,g2) = 1.5
    c: DistanceY(g2,g0) = 0.75
    c: DistanceY(g0,g1) = 0.75
    c: DistanceX(g3,g0) = 0.75
    c: DistanceX(g0,g0) = 0.75
FEATURE [PartDesign::Pad] Pad408
  BaseFeature = -> Pocket254
  Direction = (-1,0,0)
  Length = 8.2
  Length2 = 10
  Profile = -> Sketch567
  ReferenceAxis = -> Sketch567 [N_Axis]
  Refine = true
  Suppressed = false
  Type = 0
FEATURE [Sketcher::SketchObject] Sketch568
  ArcFitTolerance = 1e-06
  AttachmentSupport = -> [Pad408]
  ExternalGeometry = -> [Pad408]
  FullyConstrained = true
  MakeInternals = false
  MapMode = 5
  Placement = pos=(-88.45,0,0) rot=(0.57735,-0.57735,-0.57735;2.0944rad)
  sketch-geometry (1):
    g0: Circle CenterX=9.45 CenterY=-14.5 CenterZ=0 NormalX=0 NormalY=0 NormalZ=1 AngleXU=0 Radius=2
  constraints (2):
    c: Coincident(g0,g-3)
    c: Diameter(g0) = 4
FEATURE [PartDesign::Pad] Pad409
  BaseFeature = -> Pad408
  Direction = (-1,0,0)
  Length = 8.2
  Length2 = 10
  Profile = -> Sketch568
  ReferenceAxis = -> Sketch568 [N_Axis]
  Refine = true
  Suppressed = false
  Type = 0
FEATURE [Sketcher::SketchObject] Sketch569
  ArcFitTolerance = 1e-06
  AttachmentSupport = -> [Pad409]
  ExternalGeometry = -> [Pad409]
  FullyConstrained = true
  MakeInternals = false
  MapMode = 5
  Placement = pos=(-96.65,0,0) rot=(0.57735,-0.57735,-0.57735;2.0944rad)
  sketch-geometry (1):
    g0: Circle CenterX=9.45 CenterY=-14.5 CenterZ=0 NormalX=0 NormalY=0 NormalZ=1 AngleXU=0 Radius=1.5
  constraints (2):
    c: Coincident(g0,g-3)
    c: Diameter(g0) = 3
FEATURE [Sketcher::SketchObject] Sketch570
  ArcFitTolerance = 1e-06
  AttachmentOffset = pos=(0,0,2) rot=(0,0,1;0rad)
  AttachmentSupport = -> [Pad409]
  ExternalGeometry = -> [Pad409]
  FullyConstrained = true
  MakeInternals = false
  MapMode = 5
  Placement = pos=(-98.65,0,0) rot=(0.57735,-0.57735,-0.57735;2.0944rad)
  sketch-geometry (1):
    g0: Circle CenterX=9.45 CenterY=-14.5 CenterZ=0 NormalX=0 NormalY=0 NormalZ=1 AngleXU=0 Radius=1.15
  constraints (2):
    c: Coincident(g0,g-3)
    c: Diameter(g0) = 2.3
FEATURE [PartDesign::AdditiveLoft] AdditiveLoft
  BaseFeature = -> Pad409
  Closed = false
  Profile = -> Sketch569
  Refine = true
  Ruled = false
  Sections = -> [Sketch570]
  Suppressed = false
FEATURE [PartDesign::Chamfer] Chamfer009
  Angle = 45
  Base = -> AdditiveLoft [Edge250,Edge258]
  BaseFeature = -> AdditiveLoft
  ChamferType = 0
  FlipDirection = false
  Refine = true
  Size = 1
  Size2 = 1
  SupportTransform = false
  Suppressed = false
  UseAllEdges = false
FEATURE [App::Link] Link  label="Leg_Cannon2"
  LinkPlacement = pos=(0,63.8,0) rot=(0,0,1;0rad)
  LinkedObject = -> Body
  Placement = pos=(0,63.8,0) rot=(0,0,1;0rad)
FEATURE [Sketcher::SketchObject] Sketch571
  ArcFitTolerance = 1e-06
  AttachmentSupport = -> [XY_Plane035]
  FullyConstrained = true
  MakeInternals = false
  MapMode = 5
  sketch-geometry (4):
    g0: LineSegment StartX=0 StartY=0 StartZ=0 EndX=49 EndY=0 EndZ=0
    g1: LineSegment StartX=49 StartY=0 StartZ=0 EndX=49 EndY=15 EndZ=0
    g2: LineSegment StartX=49 StartY=15 StartZ=0 EndX=0 EndY=15 EndZ=0
    g3: LineSegment StartX=0 StartY=15 StartZ=0 EndX=0 EndY=0 EndZ=0
  constraints (11):
    c: Coincident(g0,g1)
    c: Coincident(g1,g2)
    c: Coincident(g2,g3)
    c: Coincident(g3,g0)
    c: Horizontal(g0)
    c: Horizontal(g2)
    c: Vertical(g1)
    c: Vertical(g3)
    c: Coincident(g0,g-1)
    c: DistanceY(g3,g3) = 15
    c: DistanceX(g2,g2) = 49
FEATURE [PartDesign::Pad] Pad410
  Direction = (0,0,1)
  Length = 4.75
  Length2 = 10
  Profile = -> Sketch571
  ReferenceAxis = -> Sketch571 [N_Axis]
  Refine = true
  Suppressed = false
  Type = 0
FEATURE [Sketcher::SketchObject] Sketch572
  ArcFitTolerance = 1e-06
  AttachmentSupport = -> [Pad410]
  ExternalGeometry = -> [Pad410]
  FullyConstrained = true
  MakeInternals = false
  MapMode = 5
  Placement = pos=(0,0,4.75) rot=(0,0,1;0rad)
  sketch-geometry (4):
    g0: LineSegment StartX=0 StartY=0 StartZ=0 EndX=18.55 EndY=-1.3 EndZ=0
    g1: LineSegment StartX=18.55 StartY=-1.3 StartZ=0 EndX=30.45 EndY=-1.3 EndZ=0
    g2: LineSegment StartX=30.45 StartY=-1.3 StartZ=0 EndX=49 EndY=0 EndZ=0
    g3: LineSegment StartX=0 StartY=0 StartZ=0 EndX=49 EndY=0 EndZ=0
  constraints (11):
    c: Coincident(g0,g-1)
    c: Coincident(g1,g0)
    c: Horizontal(g1)
    c: Coincident(g2,g1)
    c: Coincident(g2,g-3)
    c: DistanceY(g0,g0) = 1.3
    c: DistanceX(g1,g1) = 11.9
    c: DistanceX(g0,g2) = 49
    c: DistanceX(g0,g0) = 18.55
    c: Coincident(g3,g0)
    c: Coincident(g3,g2)
FEATURE [PartDesign::Pad] Pad411
  BaseFeature = -> Pad410
  Direction = (0,0,1)
  Length = 4.75
  Length2 = 10
  Profile = -> Sketch572
  ReferenceAxis = -> Sketch572 [N_Axis]
  Refine = true
  Reversed = true
  Suppressed = false
  Type = 0
FEATURE [Sketcher::SketchObject] Sketch573
  ArcFitTolerance = 1e-06
  AttachmentSupport = -> [Pad411]
  ExternalGeometry = -> [Pad411]
  FullyConstrained = true
  MakeInternals = false
  MapMode = 5
  Placement = pos=(0,0,4.75) rot=(0,0,1;0rad)
  sketch-geometry (4):
    g0: LineSegment StartX=18.55 StartY=-4.7 StartZ=0 EndX=30.45 EndY=-4.7 EndZ=0
    g1: LineSegment StartX=30.45 StartY=-4.7 StartZ=0 EndX=30.45 EndY=15 EndZ=0
    g2: LineSegment StartX=30.45 StartY=15 StartZ=0 EndX=18.55 EndY=15 EndZ=0
    g3: LineSegment StartX=18.55 StartY=15 StartZ=0 EndX=18.55 EndY=-4.7 EndZ=0
  constraints (12):
    c: Coincident(g0,g1)
    c: Coincident(g1,g2)
    c: Coincident(g2,g3)
    c: Coincident(g3,g0)
    c: Horizontal(g0)
    c: Horizontal(g2)
    c: Vertical(g1)
    c: Vertical(g3)
    c: PointOnObject(g1,g-4)
    c: PointOnObject(g-3,g3)
    c: PointOnObject(g-3,g1)
    c: DistanceY(g3,g3) = 19.7
FEATURE [PartDesign::Pad] Pad412
  BaseFeature = -> Pad411
  Direction = (0,0,1)
  Length = 4.75
  Length2 = 10
  Profile = -> Sketch573
  ReferenceAxis = -> Sketch573 [N_Axis]
  Refine = true
  Reversed = true
  Suppressed = false
  Type = 0
FEATURE [PartDesign::Pad] Pad413
  BaseFeature = -> Pad412
  Direction = (0,0,1)
  Length = 1.5
  Length2 = 10
  Profile = -> Sketch573
  ReferenceAxis = -> Sketch573 [N_Axis]
  Refine = true
  Suppressed = false
  Type = 0
FEATURE [Sketcher::SketchObject] Sketch574
  ArcFitTolerance = 1e-06
  AttachmentSupport = -> [Pad413]
  ExternalGeometry = -> [Pad413]
  FullyConstrained = true
  MakeInternals = false
  MapMode = 5
  Placement = pos=(0,0,4.75) rot=(0,0,1;0rad)
  sketch-geometry (6):
    g0: LineSegment StartX=0 StartY=15 StartZ=0 EndX=18.55 EndY=15 EndZ=0
    g1: LineSegment StartX=30.45 StartY=15 StartZ=0 EndX=49 EndY=15 EndZ=0
    g2: LineSegment StartX=49 StartY=15 StartZ=0 EndX=30.45 EndY=14 EndZ=0
    g3: LineSegment StartX=30.45 StartY=14 StartZ=0 EndX=30.45 EndY=15 EndZ=0
    g4: LineSegment StartX=0 StartY=15 StartZ=0 EndX=18.55 EndY=14 EndZ=0
    g5: LineSegment StartX=18.55 StartY=14 StartZ=0 EndX=18.55 EndY=15 EndZ=0
  constraints (14):
    c: Coincident(g0,g-3)
    c: Coincident(g0,g-5)
    c: Coincident(g1,g-6)
    c: Coincident(g1,g-4)
    c: Coincident(g2,g1)
    c: PointOnObject(g2,g-6)
    c: Coincident(g3,g2)
    c: Coincident(g3,g1)
    c: Coincident(g4,g0)
    c: PointOnObject(g4,g-5)
    c: Coincident(g5,g4)
    c: Coincident(g5,g0)
    c: DistanceY(g5,g5) = 1
    c: DistanceY(g3,g3) = 1
FEATURE [PartDesign::Pocket] Pocket255
  BaseFeature = -> Pad413
  Direction = (0,0,-1)
  Length = 3.25
  Length2 = 5
  Profile = -> Sketch574
  ReferenceAxis = -> Sketch574 [N_Axis]
  Refine = true
  Suppressed = false
  Type = 0
FEATURE [Sketcher::SketchObject] Sketch575
  ArcFitTolerance = 1e-06
  AttachmentSupport = -> [Pocket255]
  ExternalGeometry = -> [Pocket255]
  FullyConstrained = true
  MakeInternals = false
  MapMode = 5
  Placement = pos=(0,0,4.75) rot=(0,0,1;0rad)
  sketch-geometry (12):
    g0: LineSegment StartX=2.7 StartY=12.1505 StartZ=0 EndX=10.95 EndY=11.7058 EndZ=0
    g1: LineSegment StartX=10.95 StartY=11.7058 StartZ=0 EndX=10.95 EndY=1.93924 EndZ=0
    g2: LineSegment StartX=10.95 StartY=1.93924 StartZ=0 EndX=2.7 EndY=2.5174 EndZ=0
    g3: LineSegment StartX=2.7 StartY=2.5174 StartZ=0 EndX=2.7 EndY=12.1505 EndZ=0
    g4: LineSegment StartX=46.3 StartY=12.1505 StartZ=0 EndX=38.05 EndY=11.7058 EndZ=0
    g5: LineSegment StartX=38.05 StartY=11.7058 StartZ=0 EndX=38.05 EndY=1.93924 EndZ=0
    g6: LineSegment StartX=38.05 StartY=1.93924 StartZ=0 EndX=46.3 EndY=2.5174 EndZ=0
    g7: LineSegment StartX=46.3 StartY=2.5174 StartZ=0 EndX=46.3 EndY=12.1505 EndZ=0
    g8: LineSegment [constr] StartX=40.9003 StartY=14.5634 StartZ=0 EndX=41.0457 EndY=11.8673 EndZ=0
    g9: LineSegment [constr] StartX=8.09969 StartY=14.5634 StartZ=0 EndX=7.95435 EndY=11.8673 EndZ=0
    g10: LineSegment [constr] StartX=7.95734 StartY=2.14896 StartZ=0 EndX=7.76858 EndY=-0.544429 EndZ=0
    g11: LineSegment [constr] StartX=41.0427 StartY=2.14896 StartZ=0 EndX=41.2314 EndY=-0.544429 EndZ=0
  constraints (40):
    c: Coincident(g1,g0)
    c: Vertical(g1)
    c: Coincident(g2,g1)
    c: Coincident(g3,g2)
    c: Coincident(g3,g0)
    c: Coincident(g5,g4)
    c: Vertical(g5)
    c: Coincident(g6,g5)
    c: Coincident(g7,g6)
    c: Coincident(g7,g4)
    c: Vertical(g7)
    c: Vertical(g3)
    c: Parallel(g-3,g0)
    c: Parallel(g-6,g2)
    c: Parallel(g4,g-4)
    c: Parallel(g6,g-5)
    c: DistanceX(g0,g0) = 8.25
    c: DistanceX(g4,g4) = 8.25
    c: DistanceX(g-3,g0) = 2.7
    c: DistanceX(g4,g-4) = 2.7
    c: PointOnObject(g8,g-4)
    c: PointOnObject(g8,g4)
    c: PointOnObject(g9,g-3)
    c: PointOnObject(g9,g0)
    c: Perpendicular(g9,g-3)
    c: Perpendicular(g8,g-4)
    c: Distance(g4,g8) = 3
    c: Distance(g0,g9) = 3
    c: Distance(g9) = 2.7
    c: Distance(g8) = 2.7
    c: PointOnObject(g10,g2)
    c: PointOnObject(g10,g-6)
    c: Perpendicular(g-6,g10)
    c: Distance(g10) = 2.7
    c: PointOnObject(g11,g6)
    c: PointOnObject(g11,g-5)
    c: Perpendicular(g11,g6)
    c: Distance(g11) = 2.7
    c: Distance(g5,g11) = 3
    c: Distance(g10,g1) = 3
FEATURE [PartDesign::Pad] Pad414
  BaseFeature = -> Pocket255
  Direction = (0,0,1)
  Length = 1.5
  Length2 = 10
  Profile = -> Sketch575
  ReferenceAxis = -> Sketch575 [N_Axis]
  Refine = true
  Suppressed = false
  Type = 0
FEATURE [PartDesign::Chamfer] Chamfer010
  Angle = 45
  Base = -> Pad414 [Edge3,Edge2,Edge29,Edge30,Edge52,Edge31,Edge43,Edge17,Edge5,Edge14]
  BaseFeature = -> Pad414
  ChamferType = 0
  FlipDirection = false
  Refine = true
  Size = 1.5
  Size2 = 1
  SupportTransform = false
  Suppressed = false
  UseAllEdges = false
FEATURE [PartDesign::Chamfer] Chamfer011
  Angle = 45
  Base = -> Chamfer010 [Edge48,Edge21]
  BaseFeature = -> Chamfer010
  ChamferType = 0
  FlipDirection = false
  Refine = true
  Size = 3.5
  Size2 = 1
  SupportTransform = false
  Suppressed = false
  UseAllEdges = false
FEATURE [PartDesign::Chamfer] Chamfer012
  Angle = 45
  Base = -> Chamfer011 [Edge26,Edge28,Edge30,Edge15,Edge13,Edge11]
  BaseFeature = -> Chamfer011
  ChamferType = 0
  FlipDirection = false
  Refine = true
  Size = 1.49
  Size2 = 1
  SupportTransform = false
  Suppressed = false
  UseAllEdges = false
FEATURE [Sketcher::SketchObject] Sketch576
  ArcFitTolerance = 1e-06
  AttachmentSupport = -> [Chamfer012]
  ExternalGeometry = -> [Chamfer012]
  FullyConstrained = true
  MakeInternals = false
  MapMode = 5
  Placement = pos=(0,0,1.5) rot=(0,0,1;0rad)
  sketch-geometry (6):
    g0: LineSegment StartX=0 StartY=13.5 StartZ=0 EndX=1.58304 EndY=15 EndZ=0
    g1: LineSegment StartX=1.58304 StartY=15 StartZ=0 EndX=0 EndY=15 EndZ=0
    g2: LineSegment StartX=0 StartY=15 StartZ=0 EndX=0 EndY=13.5 EndZ=0
    g3: LineSegment StartX=49 StartY=13.5 StartZ=0 EndX=47.417 EndY=15 EndZ=0
    g4: LineSegment StartX=47.417 StartY=15 StartZ=0 EndX=49 EndY=15 EndZ=0
    g5: LineSegment StartX=49 StartY=15 StartZ=0 EndX=49 EndY=13.5 EndZ=0
  constraints (14):
    c: Coincident(g0,g-5)
    c: PointOnObject(g0,g-3)
    c: PointOnObject(g-4,g0)
    c: Coincident(g1,g0)
    c: Coincident(g1,g-5)
    c: Coincident(g2,g1)
    c: Coincident(g2,g0)
    c: Coincident(g3,g-9)
    c: PointOnObject(g3,g-7)
    c: Coincident(g4,g3)
    c: Coincident(g4,g-8)
    c: Coincident(g5,g4)
    c: Coincident(g5,g3)
    c: PointOnObject(g-6,g3)
FEATURE [PartDesign::Pocket] Pocket256
  BaseFeature = -> Chamfer012
  Direction = (0,0,-1)
  Length = 5
  Length2 = 5
  Profile = -> Sketch576
  ReferenceAxis = -> Sketch576 [N_Axis]
  Refine = true
  Suppressed = false
  Type = 0
FEATURE [Sketcher::SketchObject] Sketch577
  ArcFitTolerance = 1e-06
  AttachmentSupport = -> [Pocket256]
  ExternalGeometry = -> [Pocket256]
  FullyConstrained = true
  MakeInternals = false
  MapMode = 5
  Placement = pos=(0,0,0) rot=(1,0,0;3.14159rad)
  sketch-geometry (4):
    g0: LineSegment StartX=1.5 StartY=-1.39856 StartZ=0 EndX=1.5 EndY=-12.4978 EndZ=0
    g1: LineSegment StartX=1.5 StartY=-12.4978 StartZ=0 EndX=47.5 EndY=-12.4978 EndZ=0
    g2: LineSegment StartX=47.5 StartY=-12.4978 StartZ=0 EndX=47.5 EndY=-1.39856 EndZ=0
    g3: LineSegment StartX=47.5 StartY=-1.39856 StartZ=0 EndX=1.5 EndY=-1.39856 EndZ=0
  constraints (10):
    c: Coincident(g0,g1)
    c: Coincident(g1,g2)
    c: Coincident(g2,g3)
    c: Coincident(g3,g0)
    c: Vertical(g0)
    c: Vertical(g2)
    c: Horizontal(g1)
    c: Coincident(g0,g-8)
    c: PointOnObject(g-4,g1)
    c: Coincident(g2,g-7)
FEATURE [PartDesign::Pocket] Pocket257
  BaseFeature = -> Pocket256
  Direction = (0,0,1)
  Length = 3.25
  Length2 = 5
  Profile = -> Sketch577
  ReferenceAxis = -> Sketch577 [N_Axis]
  Refine = true
  Suppressed = false
  Type = 0
FEATURE [Sketcher::SketchObject] Sketch578
  ArcFitTolerance = 1e-06
  AttachmentSupport = -> [Pocket257]
  ExternalGeometry = -> [Pocket257]
  FullyConstrained = true
  MakeInternals = false
  MapMode = 5
  Placement = pos=(0,0,0) rot=(1,0,0;3.14159rad)
  sketch-geometry (4):
    g0: LineSegment StartX=20.04 StartY=1.2 StartZ=0 EndX=20.04 EndY=-1.39856 EndZ=0
    g1: LineSegment StartX=20.04 StartY=-1.39856 StartZ=0 EndX=28.96 EndY=-1.39856 EndZ=0
    g2: LineSegment StartX=28.96 StartY=-1.39856 StartZ=0 EndX=28.96 EndY=1.2 EndZ=0
    g3: LineSegment StartX=28.96 StartY=1.2 StartZ=0 EndX=20.04 EndY=1.2 EndZ=0
  constraints (10):
    c: Coincident(g0,g1)
    c: Coincident(g1,g2)
    c: Coincident(g2,g3)
    c: Coincident(g3,g0)
    c: Vertical(g0)
    c: Vertical(g2)
    c: Horizontal(g1)
    c: Coincident(g0,g-3)
    c: PointOnObject(g1,g-4)
    c: Coincident(g2,g-3)
FEATURE [PartDesign::Pocket] Pocket258
  BaseFeature = -> Pocket257
  Direction = (0,0,1)
  Length = 3.25
  Length2 = 5
  Profile = -> Sketch578
  ReferenceAxis = -> Sketch578 [N_Axis]
  Refine = true
  Suppressed = false
  Type = 0
FEATURE [Sketcher::SketchObject] Sketch579
  ArcFitTolerance = 1e-06
  AttachmentSupport = -> [Pocket258]
  ExternalGeometry = -> [Pocket258]
  FullyConstrained = true
  MakeInternals = false
  MapMode = 5
  Placement = pos=(0,0,3.25) rot=(1,0,0;3.14159rad)
  sketch-geometry (12):
    g0: LineSegment StartX=20.04 StartY=1.2 StartZ=0 EndX=20.04 EndY=-12.4978 EndZ=0
    g1: LineSegment StartX=20.04 StartY=-12.4978 StartZ=0 EndX=28.96 EndY=-12.4978 EndZ=0
    g2: LineSegment StartX=28.96 StartY=-12.4978 StartZ=0 EndX=28.96 EndY=1.2 EndZ=0
    g3: LineSegment StartX=28.96 StartY=1.2 StartZ=0 EndX=20.04 EndY=1.2 EndZ=0
    g4: LineSegment StartX=3.7 StartY=-3.27724 StartZ=0 EndX=9.95 EndY=-2.83924 EndZ=0
    g5: LineSegment StartX=9.95 StartY=-2.83924 StartZ=0 EndX=9.95 EndY=-10.8058 EndZ=0
    g6: LineSegment StartX=9.95 StartY=-10.8058 StartZ=0 EndX=3.7 EndY=-11.1427 EndZ=0
    g7: LineSegment StartX=3.7 StartY=-11.1427 StartZ=0 EndX=3.7 EndY=-3.27724 EndZ=0
    g8: LineSegment StartX=39.05 StartY=-2.83924 StartZ=0 EndX=45.3 EndY=-3.27724 EndZ=0
    g9: LineSegment StartX=45.3 StartY=-3.27724 StartZ=0 EndX=45.3 EndY=-11.1427 EndZ=0
    g10: LineSegment StartX=45.3 StartY=-11.1427 StartZ=0 EndX=39.05 EndY=-10.8058 EndZ=0
    g11: LineSegment StartX=39.05 StartY=-10.8058 StartZ=0 EndX=39.05 EndY=-2.83924 EndZ=0
  constraints (34):
    c: Coincident(g0,g1)
    c: Coincident(g1,g2)
    c: Coincident(g2,g3)
    c: Coincident(g3,g0)
    c: Vertical(g0)
    c: Vertical(g2)
    c: Horizontal(g1)
    c: Coincident(g0,g-7)
    c: PointOnObject(g1,g-6)
    c: Coincident(g2,g-7)
    c: Coincident(g5,g4)
    c: Vertical(g5)
    c: Coincident(g6,g5)
    c: Coincident(g7,g6)
    c: Coincident(g7,g4)
    c: Vertical(g7)
    c: Coincident(g9,g8)
    c: Vertical(g9)
    c: Coincident(g10,g9)
    c: Coincident(g11,g10)
    c: Coincident(g11,g8)
    c: Vertical(g11)
    c: DistanceX(g-15,g8) = 1
    c: DistanceX(g8,g-15) = 1
    c: DistanceX(g4,g-9) = 1
    c: DistanceX(g-10,g4) = 1
    c: Parallel(g-8,g4)
    c: Parallel(g6,g-11)
    c: Parallel(g8,g-15)
    c: Parallel(g10,g-14)
    c: DistanceY(g-14,g10) = 0.9
    c: DistanceY(g8,g-15) = 0.9
    c: DistanceY(g4,g-9) = 0.9
    c: DistanceY(g-11,g5) = 0.9
FEATURE [PartDesign::Pocket] Pocket259
  BaseFeature = -> Pocket258
  Direction = (0,0,1)
  Length = 1.5
  Length2 = 5
  Profile = -> Sketch579
  ReferenceAxis = -> Sketch579 [N_Axis]
  Refine = true
  Suppressed = false
  Type = 0
FEATURE [Sketcher::SketchObject] Sketch580
  ArcFitTolerance = 1e-06
  AttachmentSupport = -> [Pocket259]
  ExternalGeometry = -> [Pocket259]
  FullyConstrained = true
  MakeInternals = false
  MapMode = 5
  Placement = pos=(20.04,0,0) rot=(0.57735,0.57735,0.57735;2.0944rad)
  sketch-geometry (3):
    g0: LineSegment StartX=-1.2 StartY=4.75 StartZ=0 EndX=-1.2 EndY=1.75 EndZ=0
    g1: LineSegment StartX=-1.2 StartY=1.75 StartZ=0 EndX=1.8 EndY=4.75 EndZ=0
    g2: LineSegment StartX=1.8 StartY=4.75 StartZ=0 EndX=-1.2 EndY=4.75 EndZ=0
  constraints (8):
    c: Coincident(g0,g-4)
    c: PointOnObject(g1,g-4)
    c: Coincident(g2,g1)
    c: Coincident(g2,g0)
    c: Angle(g1,g0) = 0.785398
    c: Coincident(g0,g1)
    c: PointOnObject(g0,g-3)
    c: DistanceY(g0,g0) = 3
FEATURE [PartDesign::Pad] Pad415
  BaseFeature = -> Pocket259
  Direction = (1,0,0)
  Length = 9
  Length2 = 10
  Profile = -> Sketch580
  ReferenceAxis = -> Sketch580 [N_Axis]
  Refine = true
  Suppressed = false
  Type = 0
FEATURE [Sketcher::SketchObject] Sketch581
  ArcFitTolerance = 1e-06
  AttachmentSupport = -> [Pad415]
  ExternalGeometry = -> [Pad415]
  FullyConstrained = true
  MakeInternals = false
  MapMode = 5
  Placement = pos=(28.96,0,0) rot=(0.57735,-0.57735,-0.57735;2.0944rad)
  sketch-geometry (3):
    g0: LineSegment StartX=-12.4978 StartY=4.75 StartZ=0 EndX=-12.4978 EndY=2.75 EndZ=0
    g1: LineSegment StartX=-12.4978 StartY=2.75 StartZ=0 EndX=-10.4978 EndY=4.75 EndZ=0
    g2: LineSegment StartX=-10.4978 StartY=4.75 StartZ=0 EndX=-12.4978 EndY=4.75 EndZ=0
  constraints (8):
    c: Coincident(g0,g-4)
    c: PointOnObject(g-3,g0)
    c: Coincident(g1,g0)
    c: PointOnObject(g1,g-4)
    c: Coincident(g2,g1)
    c: Coincident(g2,g0)
    c: Angle(g1,g0) = 0.785398
    c: DistanceY(g0,g0) = 2
FEATURE [PartDesign::Pad] Pad416
  BaseFeature = -> Pad415
  Direction = (-1,0,0)
  Length = 28
  Length2 = 10
  Profile = -> Sketch581
  ReferenceAxis = -> Sketch581 [N_Axis]
  Refine = true
  Suppressed = false
  Type = 0
FEATURE [PartDesign::Pad] Pad417
  BaseFeature = -> Pad416
  Direction = (1,0,0)
  Length = 20
  Length2 = 10
  Profile = -> Pad416 [Face52]
  Refine = true
  Suppressed = false
  Type = 0
FEATURE [PartDesign::Pocket] Pocket260
  BaseFeature = -> Pad417
  Direction = (0,-1,-1.8e-15)
  Length = 5
  Length2 = 5
  Profile = -> Pad417 [Face56]
  Refine = true
  Suppressed = false
  Type = 0
FEATURE [Sketcher::SketchObject] Sketch582
  ArcFitTolerance = 1e-06
  AttachmentSupport = -> [Pocket260]
  ExternalGeometry = -> [Pocket260]
  FullyConstrained = true
  MakeInternals = false
  MapMode = 5
  Placement = pos=(0,0,3.25) rot=(1,0,0;3.14159rad)
  sketch-geometry (4):
    g0: LineSegment StartX=3.7 StartY=-3.27724 StartZ=0 EndX=9.95 EndY=-2.83924 EndZ=0
    g1: LineSegment StartX=9.95 StartY=-2.83924 StartZ=0 EndX=9.95 EndY=-10.8058 EndZ=0
    g2: LineSegment StartX=9.95 StartY=-10.8058 StartZ=0 EndX=3.7 EndY=-11.1427 EndZ=0
    g3: LineSegment StartX=3.7 StartY=-11.1427 StartZ=0 EndX=3.7 EndY=-3.27724 EndZ=0
  constraints (8):
    c: Coincident(g0,g-4)
    c: Coincident(g0,g-5)
    c: Coincident(g1,g0)
    c: Coincident(g1,g-6)
    c: Coincident(g2,g1)
    c: Coincident(g2,g-6)
    c: Coincident(g3,g2)
    c: Coincident(g3,g0)
FEATURE [PartDesign::Pocket] Pocket261
  BaseFeature = -> Pocket260
  Direction = (0,0,1)
  Length = 1.5
  Length2 = 5
  Profile = -> Sketch582
  ReferenceAxis = -> Sketch582 [N_Axis]
  Refine = true
  Suppressed = false
  Type = 0
FEATURE [Sketcher::SketchObject] Sketch583
  ArcFitTolerance = 1e-06
  AttachmentSupport = -> [Pocket261]
  ExternalGeometry = -> [Pocket261]
  FullyConstrained = true
  MakeInternals = false
  MapMode = 5
  Placement = pos=(0,0,0) rot=(1,0,0;3.14159rad)
  sketch-geometry (4):
    g0: Circle CenterX=32.3 CenterY=-13.7478 CenterZ=0 NormalX=0 NormalY=0 NormalZ=1 AngleXU=0 Radius=1.25
    g1: Circle CenterX=16.7 CenterY=-13.7478 CenterZ=0 NormalX=0 NormalY=0 NormalZ=1 AngleXU=0 Radius=1.25
    g2: LineSegment [constr] StartX=16.7 StartY=-13.7478 StartZ=0 EndX=17.95 EndY=-13.7478 EndZ=0
    g3: LineSegment [constr] StartX=32.3 StartY=-13.7478 StartZ=0 EndX=31.05 EndY=-13.7478 EndZ=0
  constraints (16):
    c: DistanceY(g-4,g-3) = 2.50218
    c: Diameter(g1) = 2.5
    c: Diameter(g0) = 2.5
    c: Tangent(g0,g-3)
    c: Tangent(g1,g-3)
    c: DistanceX(g-5,g-6) = 8.92
    c: DistanceX(g1,g0) = 15.6
    c: Coincident(g2,g1)
    c: PointOnObject(g2,g1)
    c: Horizontal(g2)
    c: Coincident(g3,g0)
    c: PointOnObject(g3,g0)
    c: Horizontal(g3)
    c: DistanceX(g2,g3) = 13.1
    c: DistanceX(g2,g-5) = 2.09
    c: DistanceX(g-6,g3) = 2.09
FEATURE [PartDesign::Pad] Pad418
  BaseFeature = -> Pocket261
  Direction = (0,0,-1)
  Length = 3
  Length2 = 10
  Profile = -> Sketch583
  ReferenceAxis = -> Sketch583 [N_Axis]
  Refine = true
  Suppressed = false
  Type = 0
FEATURE [Sketcher::SketchObject] Sketch584
  ArcFitTolerance = 1e-06
  AttachmentSupport = -> [Pad418]
  ExternalGeometry = -> [Pad418]
  FullyConstrained = true
  MakeInternals = false
  MapMode = 5
  Placement = pos=(0,15,0) rot=(0,0.707107,0.707107;3.14159rad)
  sketch-geometry (4):
    g0: LineSegment StartX=-28.55 StartY=2 StartZ=0 EndX=-28.55 EndY=0 EndZ=0
    g1: LineSegment StartX=-28.55 StartY=0 StartZ=0 EndX=-20.45 EndY=0 EndZ=0
    g2: LineSegment StartX=-20.45 StartY=0 StartZ=0 EndX=-20.45 EndY=2 EndZ=0
    g3: LineSegment StartX=-20.45 StartY=2 StartZ=0 EndX=-28.55 EndY=2 EndZ=0
  constraints (13):
    c: Coincident(g0,g1)
    c: Coincident(g1,g2)
    c: Coincident(g2,g3)
    c: Coincident(g3,g0)
    c: Vertical(g0)
    c: Vertical(g2)
    c: Horizontal(g1)
    c: Horizontal(g3)
    c: DistanceX(g3,g3) = 8.1
    c: DistanceY(g0,g0) = 2
    c: DistanceX(g-3,g-3) = 11.9
    c: DistanceX(g-3,g0) = 1.9
    c: PointOnObject(g0,g-4)
FEATURE [PartDesign::Pad] Pad419
  BaseFeature = -> Pad418
  Direction = (0,1,-2e-16)
  Length = 2.75
  Length2 = 10
  Profile = -> Sketch584
  ReferenceAxis = -> Sketch584 [N_Axis]
  Refine = true
  Suppressed = false
  Type = 0
FEATURE [Sketcher::SketchObject] Sketch585
  ArcFitTolerance = 1e-06
  AttachmentSupport = -> [Pad419]
  ExternalGeometry = -> [Pad419]
  FullyConstrained = true
  MakeInternals = false
  MapMode = 5
  Placement = pos=(28.55,0,0) rot=(0.57735,0.57735,0.57735;2.0944rad)
  sketch-geometry (3):
    g0: LineSegment StartX=15 StartY=2 StartZ=0 EndX=17.75 EndY=2 EndZ=0
    g1: LineSegment StartX=17.75 StartY=2 StartZ=0 EndX=15 EndY=2.1 EndZ=0
    g2: LineSegment StartX=15 StartY=2.1 StartZ=0 EndX=15 EndY=2 EndZ=0
  constraints (7):
    c: Coincident(g0,g-3)
    c: Coincident(g0,g-3)
    c: Coincident(g1,g0)
    c: PointOnObject(g1,g-4)
    c: Coincident(g2,g1)
    c: Coincident(g2,g0)
    c: DistanceY(g2,g2) = 0.1
FEATURE [PartDesign::Pad] Pad420
  BaseFeature = -> Pad419
  Direction = (1,0,0)
  Length = 8.1
  Length2 = 10
  Profile = -> Sketch585
  ReferenceAxis = -> Sketch585 [N_Axis]
  Refine = true
  Reversed = true
  Suppressed = false
  Type = 0
FEATURE [Sketcher::SketchObject] Sketch586
  ArcFitTolerance = 1e-06
  AttachmentSupport = -> [Pad420]
  ExternalGeometry = -> [Pad420]
  FullyConstrained = true
  MakeInternals = false
  MapMode = 5
  Placement = pos=(0,0,0) rot=(1,0,0;3.14159rad)
  sketch-geometry (6):
    g0: LineSegment StartX=28.55 StartY=-15 StartZ=0 EndX=28.55 EndY=-17.75 EndZ=0
    g1: LineSegment StartX=28.55 StartY=-17.75 StartZ=0 EndX=28.6 EndY=-15 EndZ=0
    g2: LineSegment StartX=28.6 StartY=-15 StartZ=0 EndX=28.55 EndY=-15 EndZ=0
    g3: LineSegment StartX=20.45 StartY=-17.75 StartZ=0 EndX=20.45 EndY=-15 EndZ=0
    g4: LineSegment StartX=20.45 StartY=-17.75 StartZ=0 EndX=20.4 EndY=-15 EndZ=0
    g5: LineSegment StartX=20.45 StartY=-15 StartZ=0 EndX=20.4 EndY=-15 EndZ=0
  constraints (14):
    c: Coincident(g0,g-4)
    c: Coincident(g0,g-4)
    c: Coincident(g1,g0)
    c: PointOnObject(g1,g-3)
    c: Coincident(g2,g1)
    c: Coincident(g2,g0)
    c: DistanceX(g2,g2) = 0.05
    c: Coincident(g3,g-5)
    c: Coincident(g3,g-6)
    c: Coincident(g4,g3)
    c: PointOnObject(g4,g-6)
    c: Coincident(g5,g3)
    c: Coincident(g5,g4)
    c: DistanceX(g5,g5) = 0.05
FEATURE [PartDesign::Pad] Pad421
  BaseFeature = -> Pad420
  Direction = (0,0,-1)
  Length = 3
  Length2 = 10
  Profile = -> Sketch586
  ReferenceAxis = -> Sketch586 [N_Axis]
  Refine = true
  Reversed = true
  Suppressed = false
  Type = 0
FEATURE [PartDesign::Pocket] Pocket262
  BaseFeature = -> Pad421
  Direction = (-1,2.6e-15,0)
  Length = 5
  Length2 = 5
  Profile = -> Pad421 [Face41]
  Refine = true
  Suppressed = false
  Type = 0
FEATURE [PartDesign::Pocket] Pocket263
  BaseFeature = -> Pocket262
  Direction = (1,-2.6e-15,0)
  Length = 5
  Length2 = 5
  Profile = -> Pocket262 [Face48]
  Refine = true
  Suppressed = false
  Type = 0
FEATURE [PartDesign::Chamfer] Chamfer013
  Angle = 45
  Base = -> Pocket263 [Edge106,Edge105,Edge38,Edge83]
  BaseFeature = -> Pocket263
  ChamferType = 0
  FlipDirection = false
  Refine = true
  Size = 0.3
  Size2 = 1
  SupportTransform = false
  Suppressed = false
  UseAllEdges = false
FEATURE [PartDesign::Body] Body032  label="Waist"
  AllowCompound = false
  Group = -> [Sketch571,Pad410,Sketch572,Pad411,Sketch573,Pad412,Pad413,Sketch574,Pocket255,Sketch575,Pad414,Chamfer010,Chamfer011,Chamfer012,Sketch576,Pocket256,Sketch577,Pocket257,Sketch578,Pocket258,Sketch579,Pocket259,Sketch580,Pad415,Sketch581,Pad416,Pad417,Pocket260,Sketch582,Pocket261,Sketch583,Pad418,Sketch584,Pad419,Sketch585,Pad420,Sketch586,Pad421,Pocket262,Pocket263,Chamfer013]
  Origin = -> Origin035
  Placement = pos=(-106,-2,0) rot=(0,0,1;1.5708rad)
  Tip = -> Chamfer013
FEATURE [Sketcher::SketchObject] Sketch640
  ArcFitTolerance = 1e-06
  AttachmentSupport = -> [XY_Plane037]
  FullyConstrained = true
  MakeInternals = false
  MapMode = 5
  sketch-geometry (4):
    g0: LineSegment StartX=0 StartY=0 StartZ=0 EndX=15.9 EndY=0 EndZ=0
    g1: LineSegment StartX=15.9 StartY=0 StartZ=0 EndX=15.9 EndY=13.8 EndZ=0
    g2: LineSegment StartX=15.9 StartY=13.8 StartZ=0 EndX=0 EndY=13.8 EndZ=0
    g3: LineSegment StartX=0 StartY=13.8 StartZ=0 EndX=0 EndY=0 EndZ=0
  constraints (11):
    c: Coincident(g0,g1)
    c: Coincident(g1,g2)
    c: Coincident(g2,g3)
    c: Coincident(g3,g0)
    c: Horizontal(g0)
    c: Horizontal(g2)
    c: Vertical(g1)
    c: Vertical(g3)
    c: Coincident(g0,g-1)
    c: DistanceY(g3,g3) = 13.8
    c: DistanceX(g0,g0) = 15.9
FEATURE [PartDesign::Pad] Pad454
  Direction = (0,0,1)
  Length = 7
  Length2 = 10
  Profile = -> Sketch640
  ReferenceAxis = -> Sketch640 [N_Axis]
  Refine = true
  Suppressed = false
  Type = 0
FEATURE [Sketcher::SketchObject] Sketch641
  ArcFitTolerance = 1e-06
  AttachmentSupport = -> [Pad454]
  ExternalGeometry = -> [Pad454]
  FullyConstrained = true
  MakeInternals = false
  MapMode = 5
  Placement = pos=(0,0,7) rot=(0,0,1;0rad)
  sketch-geometry (74):
    g0: LineSegment StartX=1.95 StartY=13.8 StartZ=0 EndX=13.95 EndY=13.8 EndZ=0
    g1: LineSegment StartX=13.95 StartY=13.8 StartZ=0 EndX=13.95 EndY=9.3 EndZ=0
    g2: LineSegment StartX=13.95 StartY=9.3 StartZ=0 EndX=12.2 EndY=0 EndZ=0
    g3: LineSegment StartX=12.2 StartY=0 StartZ=0 EndX=3.7 EndY=0 EndZ=0
    g4: LineSegment StartX=3.7 StartY=0 StartZ=0 EndX=1.95 EndY=9.3 EndZ=0
    g5: LineSegment StartX=1.95 StartY=9.3 StartZ=0 EndX=1.95 EndY=13.8 EndZ=0
    g6: LineSegment StartX=3.47633 StartY=12.3 StartZ=0 EndX=12.4237 EndY=12.3 EndZ=0
    g7: LineSegment StartX=12.4237 StartY=12.3 StartZ=0 EndX=12.4237 EndY=9.3 EndZ=0
    g8: LineSegment StartX=12.4237 StartY=9.3 StartZ=0 EndX=10.9559 EndY=1.5 EndZ=0
    g9: LineSegment StartX=10.9559 StartY=1.5 StartZ=0 EndX=4.94407 EndY=1.5 EndZ=0
    g10: LineSegment StartX=4.94407 StartY=1.5 StartZ=0 EndX=3.47633 EndY=9.3 EndZ=0
    g11: LineSegment StartX=3.47633 StartY=12.3 StartZ=0 EndX=3.47633 EndY=9.3 EndZ=0
    g12: LineSegment [constr] StartX=3.47633 StartY=9.3 StartZ=0 EndX=1.95 EndY=9.3 EndZ=0
    g13: LineSegment [constr] StartX=12.4237 StartY=9.3 StartZ=0 EndX=13.95 EndY=9.3 EndZ=0
    g14: LineSegment [constr] StartX=11.6898 StartY=5.4 StartZ=0 EndX=13.1639 EndY=5.12261 EndZ=0
    g15: LineSegment [constr] StartX=4.2102 StartY=5.4 StartZ=0 EndX=2.73607 EndY=5.12261 EndZ=0
    g16: ArcOfCircle CenterX=3.97633 CenterY=11.575 CenterZ=0 NormalX=0 NormalY=0 NormalZ=1 AngleXU=0 Radius=0.3 StartAngle=1.5708 EndAngle=4.71239
    g17: ArcOfCircle CenterX=11.9237 CenterY=11.575 CenterZ=0 NormalX=0 NormalY=0 NormalZ=1 AngleXU=0 Radius=0.3 StartAngle=4.71239 EndAngle=7.85398
    g18: LineSegment StartX=3.97633 StartY=11.875 StartZ=0 EndX=11.9237 EndY=11.875 EndZ=0
    g19: LineSegment StartX=3.97633 StartY=11.275 StartZ=0 EndX=11.9237 EndY=11.275 EndZ=0
    g20: ArcOfCircle CenterX=4.061 CenterY=10.575 CenterZ=0 NormalX=0 NormalY=0 NormalZ=1 AngleXU=0 Radius=0.3 StartAngle=1.5708 EndAngle=4.71239
    g21: ArcOfCircle CenterX=11.9237 CenterY=10.575 CenterZ=0 NormalX=0 NormalY=0 NormalZ=1 AngleXU=0 Radius=0.3 StartAngle=4.71239 EndAngle=7.85398
    g22: LineSegment StartX=4.061 StartY=10.875 StartZ=0 EndX=11.9237 EndY=10.875 EndZ=0
    g23: LineSegment StartX=4.061 StartY=10.275 StartZ=0 EndX=11.9237 EndY=10.275 EndZ=0
    g24: ArcOfCircle CenterX=4.061 CenterY=9.575 CenterZ=0 NormalX=0 NormalY=0 NormalZ=1 AngleXU=0 Radius=0.3 StartAngle=1.5708 EndAngle=4.71239
    g25: ArcOfCircle CenterX=11.839 CenterY=9.575 CenterZ=0 NormalX=0 NormalY=0 NormalZ=1 AngleXU=0 Radius=0.3 StartAngle=4.71239 EndAngle=7.85398
    g26: LineSegment StartX=4.061 StartY=9.875 StartZ=0 EndX=11.839 EndY=9.875 EndZ=0
    g27: LineSegment StartX=4.061 StartY=9.275 StartZ=0 EndX=11.839 EndY=9.275 EndZ=0
    g28: ArcOfCircle CenterX=4.25858 CenterY=8.525 CenterZ=0 NormalX=0 NormalY=0 NormalZ=1 AngleXU=0 Radius=0.3 StartAngle=1.5708 EndAngle=4.71239
    g29: ArcOfCircle CenterX=11.6414 CenterY=8.525 CenterZ=0 NormalX=0 NormalY=0 NormalZ=1 AngleXU=0 Radius=0.3 StartAngle=4.71239 EndAngle=7.85398
    g30: LineSegment StartX=4.25858 StartY=8.825 StartZ=0 EndX=11.6414 EndY=8.825 EndZ=0
    g31: LineSegment StartX=4.25858 StartY=8.225 StartZ=0 EndX=11.6414 EndY=8.225 EndZ=0
    g32: ArcOfCircle CenterX=4.45616 CenterY=7.475 CenterZ=0 NormalX=0 NormalY=0 NormalZ=1 AngleXU=0 Radius=0.3 StartAngle=1.5708 EndAngle=4.71239
    g33: ArcOfCircle CenterX=11.4438 CenterY=7.475 CenterZ=0 NormalX=0 NormalY=0 NormalZ=1 AngleXU=0 Radius=0.3 StartAngle=4.71239 EndAngle=7.85398
    g34: LineSegment StartX=4.45616 StartY=7.775 StartZ=0 EndX=11.4438 EndY=7.775 EndZ=0
    g35: LineSegment StartX=4.45616 StartY=7.175 StartZ=0 EndX=11.4438 EndY=7.175 EndZ=0
    g36: ArcOfCircle CenterX=4.65374 CenterY=6.425 CenterZ=0 NormalX=0 NormalY=0 NormalZ=1 AngleXU=0 Radius=0.3 StartAngle=1.5708 EndAngle=4.71239
    g37: ArcOfCircle CenterX=11.2463 CenterY=6.425 CenterZ=0 NormalX=0 NormalY=0 NormalZ=1 AngleXU=0 Radius=0.3 StartAngle=4.71239 EndAngle=7.85398
    g38: LineSegment StartX=4.65374 StartY=6.725 StartZ=0 EndX=11.2463 EndY=6.725 EndZ=0
    g39: LineSegment StartX=4.65374 StartY=6.125 StartZ=0 EndX=11.2463 EndY=6.125 EndZ=0
    g40: ArcOfCircle CenterX=4.85133 CenterY=5.375 CenterZ=0 NormalX=0 NormalY=0 NormalZ=1 AngleXU=0 Radius=0.3 StartAngle=1.5708 EndAngle=4.71239
    g41: ArcOfCircle CenterX=11.0487 CenterY=5.375 CenterZ=0 NormalX=0 NormalY=0 NormalZ=1 AngleXU=0 Radius=0.3 StartAngle=4.71239 EndAngle=7.85398
    g42: LineSegment StartX=4.85133 StartY=5.675 StartZ=0 EndX=11.0487 EndY=5.675 EndZ=0
    g43: LineSegment StartX=4.85133 StartY=5.075 StartZ=0 EndX=11.0487 EndY=5.075 EndZ=0
    g44: ArcOfCircle CenterX=5.04891 CenterY=4.325 CenterZ=0 NormalX=0 NormalY=0 NormalZ=1 AngleXU=0 Radius=0.3 StartAngle=1.5708 EndAngle=4.71239
    g45: ArcOfCircle CenterX=10.8511 CenterY=4.325 CenterZ=0 NormalX=0 NormalY=0 NormalZ=1 AngleXU=0 Radius=0.3 StartAngle=4.71239 EndAngle=7.85398
    g46: LineSegment StartX=5.04891 StartY=4.625 StartZ=0 EndX=10.8511 EndY=4.625 EndZ=0
    g47: LineSegment StartX=5.04891 StartY=4.025 StartZ=0 EndX=10.8511 EndY=4.025 EndZ=0
    g48: ArcOfCircle CenterX=5.24649 CenterY=3.275 CenterZ=0 NormalX=0 NormalY=0 NormalZ=1 AngleXU=0 Radius=0.3 StartAngle=1.5708 EndAngle=4.71239
    g49: ArcOfCircle CenterX=10.6535 CenterY=3.275 CenterZ=0 NormalX=0 NormalY=0 NormalZ=1 AngleXU=0 Radius=0.3 StartAngle=4.71239 EndAngle=7.85398
    g50: LineSegment StartX=5.24649 StartY=3.575 StartZ=0 EndX=10.6535 EndY=3.575 EndZ=0
    g51: LineSegment StartX=5.24649 StartY=2.975 StartZ=0 EndX=10.6535 EndY=2.975 EndZ=0
    g52: ArcOfCircle CenterX=5.44407 CenterY=2.225 CenterZ=0 NormalX=0 NormalY=0 NormalZ=1 AngleXU=0 Radius=0.3 StartAngle=1.5708 EndAngle=4.71239
    g53: ArcOfCircle CenterX=10.4559 CenterY=2.225 CenterZ=0 NormalX=0 NormalY=0 NormalZ=1 AngleXU=0 Radius=0.3 StartAngle=4.71239 EndAngle=7.85398
    g54: LineSegment StartX=5.44407 StartY=2.525 StartZ=0 EndX=10.4559 EndY=2.525 EndZ=0
    g55: LineSegment StartX=5.44407 StartY=1.925 StartZ=0 EndX=10.4559 EndY=1.925 EndZ=0
    g56: LineSegment [constr] StartX=3.97633 StartY=11.575 StartZ=0 EndX=4.061 EndY=10.575 EndZ=0
    g57: LineSegment [constr] StartX=4.061 StartY=10.575 StartZ=0 EndX=4.061 EndY=9.575 EndZ=0
    g58: LineSegment [constr] StartX=4.061 StartY=9.575 StartZ=0 EndX=4.25858 EndY=8.525 EndZ=0
    g59: LineSegment [constr] StartX=4.25858 StartY=8.525 StartZ=0 EndX=4.45616 EndY=7.475 EndZ=0
    g60: LineSegment [constr] StartX=4.45616 StartY=7.475 StartZ=0 EndX=4.65374 EndY=6.425 EndZ=0
    g61: LineSegment [constr] StartX=4.65374 StartY=6.425 StartZ=0 EndX=4.85133 EndY=5.375 EndZ=0
    g62: LineSegment [constr] StartX=4.85133 StartY=5.375 StartZ=0 EndX=5.04891 EndY=4.325 EndZ=0
    g63: LineSegment [constr] StartX=5.04891 StartY=4.325 StartZ=0 EndX=5.24649 EndY=3.275 EndZ=0
    g64: LineSegment [constr] StartX=5.24649 StartY=3.275 StartZ=0 EndX=5.44407 EndY=2.225 EndZ=0
    g65: LineSegment [constr] StartX=11.9237 StartY=11.575 StartZ=0 EndX=11.9237 EndY=10.575 EndZ=0
    g66: LineSegment [constr] StartX=11.9237 StartY=10.575 StartZ=0 EndX=11.839 EndY=9.575 EndZ=0
    g67: LineSegment [constr] StartX=11.839 StartY=9.575 StartZ=0 EndX=11.6414 EndY=8.525 EndZ=0
    g68: LineSegment [constr] StartX=11.6414 StartY=8.525 StartZ=0 EndX=11.4438 EndY=7.475 EndZ=0
    g69: LineSegment [constr] StartX=11.4438 StartY=7.475 StartZ=0 EndX=11.2463 EndY=6.425 EndZ=0
    g70: LineSegment [constr] StartX=11.2463 StartY=6.425 StartZ=0 EndX=11.0487 EndY=5.375 EndZ=0
    g71: LineSegment [constr] StartX=11.0487 StartY=5.375 StartZ=0 EndX=10.8511 EndY=4.325 EndZ=0
    g72: LineSegment [constr] StartX=10.8511 StartY=4.325 StartZ=0 EndX=10.6535 EndY=3.275 EndZ=0
    g73: LineSegment [constr] StartX=10.4559 StartY=2.225 StartZ=0 EndX=10.6535 EndY=3.275 EndZ=0
  constraints (184):
    c: PointOnObject(g0,g-3)
    c: PointOnObject(g0,g-3)
    c: Coincident(g1,g0)
    c: Vertical(g1)
    c: Coincident(g2,g1)
    c: PointOnObject(g2,g-4)
    c: Coincident(g3,g2)
    c: PointOnObject(g3,g-4)
    c: Coincident(g4,g3)
    c: Coincident(g5,g4)
    c: Coincident(g5,g0)
    c: Vertical(g5)
    c: DistanceX(g3,g3) = 8.5
    c: DistanceX(g0,g0) = 12
    c: DistanceY(g5,g5) = 4.5
    c: DistanceY(g1,g1) = 4.5
    c: DistanceX(g-5,g-6) = 15.9
    c: DistanceX(g-5,g0) = 1.95
    c: DistanceX(g-1,g3) = 3.7
    c: Horizontal(g6)
    c: Coincident(g7,g6)
    c: Vertical(g7)
    c: Coincident(g8,g7)
    c: Coincident(g9,g8)
    c: Horizontal(g9)
    c: Coincident(g10,g9)
    c: Coincident(g11,g6)
    c: Coincident(g11,g10)
    c: Vertical(g11)
    c: Parallel(g10,g4)
    c: Parallel(g8,g2)
    c: DistanceY(g6,g0) = 1.5
    c: DistanceY(g2,g8) = 1.5
    c: Coincident(g12,g10)
    c: Coincident(g12,g4)
    c: Horizontal(g12)
    c: Coincident(g13,g7)
    c: Coincident(g13,g1)
    c: Horizontal(g13)
    c: Symmetric(g8,g8,g14)
    c: PointOnObject(g14,g2)
    c: Perpendicular(g14,g8)
    c: Distance(g14) = 1.5
    c: Symmetric(g10,g10,g15)
    c: PointOnObject(g15,g4)
    c: Perpendicular(g15,g10)
    c: Distance(g15) = 1.5
    c: Tangent(g16,g18) = 1.5708
    c: Tangent(g16,g19) = -1.5708
    c: Tangent(g17,g18) = 1.5708
    c: Tangent(g17,g19) = -1.5708
    c: Equal(g16,g17)
    c: Horizontal(g18)
    c: Tangent(g20,g22) = 1.5708
    c: Tangent(g20,g23) = -1.5708
    c: Tangent(g21,g22) = 1.5708
    c: Tangent(g21,g23) = -1.5708
    c: Equal(g20,g21)
    c: Horizontal(g23)
    c: Tangent(g24,g26) = 1.5708
    c: Tangent(g24,g27) = -1.5708
    c: Tangent(g25,g26) = 1.5708
    c: Tangent(g25,g27) = -1.5708
    c: Equal(g24,g25)
    c: Horizontal(g26)
    c: Tangent(g28,g30) = 1.5708
    c: Tangent(g28,g31) = -1.5708
    c: Tangent(g29,g30) = 1.5708
    c: Tangent(g29,g31) = -1.5708
    c: Equal(g28,g29)
    c: Horizontal(g30)
    c: DistanceX(g6,g16) = 0.5
    c: DistanceX(g17,g6) = 0.5
    c: Radius(g16) = 0.3
    c: Radius(g20) = 0.3
    c: Radius(g24) = 0.3
    c: Radius(g28) = 0.3
    c: Tangent(g32,g34) = 1.5708
    c: Tangent(g32,g35) = -1.5708
    c: Tangent(g33,g34) = 1.5708
    c: Tangent(g33,g35) = -1.5708
    c: Equal(g32,g33)
    c: Horizontal(g34)
    c: Tangent(g36,g38) = 1.5708
    c: Tangent(g36,g39) = -1.5708
    c: Tangent(g37,g38) = 1.5708
    c: Tangent(g37,g39) = -1.5708
    c: Equal(g36,g37)
    c: Horizontal(g38)
    c: Tangent(g40,g42) = 1.5708
    c: Tangent(g40,g43) = -1.5708
    c: Tangent(g41,g42) = 1.5708
    c: Tangent(g41,g43) = -1.5708
    c: Equal(g40,g41)
    c: Horizontal(g42)
    c: Tangent(g44,g46) = 1.5708
    c: Tangent(g44,g47) = -1.5708
    c: Tangent(g45,g46) = 1.5708
    c: Tangent(g45,g47) = -1.5708
    c: Equal(g44,g45)
    c: Horizontal(g46)
    c: Tangent(g48,g50) = 1.5708
    c: Tangent(g48,g51) = -1.5708
    c: Tangent(g49,g50) = 1.5708
    c: Tangent(g49,g51) = -1.5708
    c: Equal(g48,g49)
    c: Horizontal(g50)
    c: Radius(g40) = 0.3
    c: Radius(g36) = 0.3
    c: Radius(g32) = 0.3
    c: Radius(g44) = 0.3
    c: Radius(g48) = 0.3
    c: Tangent(g52,g54) = 1.5708
    c: Tangent(g52,g55) = -1.5708
    c: Tangent(g53,g54) = 1.5708
    c: Tangent(g53,g55) = -1.5708
    c: Equal(g52,g53)
    c: Horizontal(g54)
    c: Radius(g52) = 0.3
    c: Coincident(g56,g16)
    c: Coincident(g56,g20)
    c: Coincident(g57,g20)
    c: Coincident(g57,g24)
    c: Vertical(g57)
    c: Coincident(g58,g24)
    c: Coincident(g58,g28)
    c: Coincident(g59,g28)
    c: Coincident(g59,g32)
    c: Coincident(g60,g32)
    c: Coincident(g60,g36)
    c: Coincident(g61,g36)
    c: Coincident(g61,g40)
    c: Coincident(g62,g40)
    c: Coincident(g62,g44)
    c: Parallel(g10,g58)
    c: Parallel(g10,g59)
    c: Parallel(g10,g60)
    c: Parallel(g10,g61)
    c: Parallel(g10,g62)
    c: DistanceX(g9,g52) = 0.5
    c: DistanceX(g53,g8) = 0.5
    c: DistanceY(g56,g56) = 1
    c: DistanceY(g57,g57) = 1
    c: DistanceY(g58,g58) = 1.05
    c: DistanceY(g59,g59) = 1.05
    c: DistanceY(g60,g60) = 1.05
    c: DistanceY(g61,g61) = 1.05
    c: DistanceY(g62,g62) = 1.05
    c: Coincident(g63,g44)
    c: Coincident(g63,g48)
    c: Coincident(g64,g48)
    c: Coincident(g64,g52)
    c: Parallel(g63,g10)
    c: Parallel(g64,g10)
    c: DistanceY(g63,g63) = 1.05
    c: DistanceY(g64,g64) = 1.05
    c: DistanceY(g16,g6) = 0.725
    c: DistanceY(g9,g52) = 0.725
    c: Coincident(g65,g17)
    c: Coincident(g65,g21)
    c: Vertical(g65)
    c: Coincident(g66,g21)
    c: Coincident(g66,g25)
    c: Coincident(g67,g25)
    c: Coincident(g67,g29)
    c: Coincident(g68,g29)
    c: Coincident(g68,g33)
    c: Coincident(g69,g33)
    c: Coincident(g69,g37)
    c: Coincident(g70,g37)
    c: Coincident(g70,g41)
    c: Coincident(g71,g41)
    c: Coincident(g71,g45)
    c: Coincident(g72,g45)
    c: Coincident(g72,g49)
    c: Parallel(g72,g8)
    c: Parallel(g71,g8)
    c: Parallel(g70,g8)
    c: Coincident(g73,g53)
    c: Coincident(g73,g49)
    c: Parallel(g73,g8)
    c: Parallel(g8,g69)
    c: Parallel(g68,g8)
    c: Parallel(g67,g8)
FEATURE [PartDesign::Pad] Pad455
  BaseFeature = -> Pad454
  Direction = (0,0,1)
  Length = 0.5
  Length2 = 10
  Profile = -> Sketch641
  ReferenceAxis = -> Sketch641 [N_Axis]
  Refine = true
  Suppressed = false
  Type = 0
FEATURE [Sketcher::SketchObject] Sketch642
  ArcFitTolerance = 1e-06
  AttachmentSupport = -> [Pad455]
  ExternalGeometry = -> [Pad455]
  FullyConstrained = true
  MakeInternals = false
  MapMode = 5
  Placement = pos=(0,0,0) rot=(0.57735,-0.57735,-0.57735;2.0944rad)
  sketch-geometry (12):
    g0: LineSegment StartX=-9 StartY=7 StartZ=0 EndX=-9 EndY=0 EndZ=0
    g1: LineSegment StartX=-9 StartY=0 StartZ=0 EndX=-7.9 EndY=0 EndZ=0
    g2: LineSegment StartX=-7.9 StartY=0 StartZ=0 EndX=-7.9 EndY=7 EndZ=0
    g3: LineSegment StartX=-7.9 StartY=7 StartZ=0 EndX=-9 EndY=7 EndZ=0
    g4: LineSegment StartX=-6 StartY=7 StartZ=0 EndX=-6 EndY=0 EndZ=0
    g5: LineSegment StartX=-6 StartY=0 StartZ=0 EndX=-4.9 EndY=0 EndZ=0
    g6: LineSegment StartX=-4.9 StartY=0 StartZ=0 EndX=-4.9 EndY=7 EndZ=0
    g7: LineSegment StartX=-4.9 StartY=7 StartZ=0 EndX=-6 EndY=7 EndZ=0
    g8: LineSegment StartX=-3 StartY=7 StartZ=0 EndX=-3 EndY=0 EndZ=0
    g9: LineSegment StartX=-3 StartY=0 StartZ=0 EndX=-1.9 EndY=0 EndZ=0
    g10: LineSegment StartX=-1.9 StartY=0 StartZ=0 EndX=-1.9 EndY=7 EndZ=0
    g11: LineSegment StartX=-1.9 StartY=7 StartZ=0 EndX=-3 EndY=7 EndZ=0
  constraints (37):
    c: Coincident(g0,g1)
    c: Coincident(g1,g2)
    c: Coincident(g2,g3)
    c: Coincident(g3,g0)
    c: Vertical(g0)
    c: Vertical(g2)
    c: Horizontal(g1)
    c: Horizontal(g3)
    c: PointOnObject(g0,g-3)
    c: PointOnObject(g1,g-4)
    c: Coincident(g4,g5)
    c: Coincident(g5,g6)
    c: Coincident(g6,g7)
    c: Coincident(g7,g4)
    c: Vertical(g4)
    c: Vertical(g6)
    c: Horizontal(g5)
    c: Horizontal(g7)
    c: PointOnObject(g5,g-4)
    c: Coincident(g8,g9)
    c: Coincident(g9,g10)
    c: Coincident(g10,g11)
    c: Coincident(g11,g8)
    c: Vertical(g8)
    c: Vertical(g10)
    c: Horizontal(g9)
    c: Horizontal(g11)
    c: PointOnObject(g8,g-3)
    c: PointOnObject(g9,g-4)
    c: DistanceX(g-3,g0) = 4.8
    c: DistanceX(g2,g4) = 1.9
    c: PointOnObject(g6,g-3)
    c: DistanceX(g6,g8) = 1.9
    c: DistanceX(g10,g-3) = 1.9
    c: DistanceX(g0,g2) = 1.1
    c: DistanceX(g4,g6) = 1.1
    c: DistanceX(g8,g10) = 1.1
FEATURE [PartDesign::Pocket] Pocket283
  BaseFeature = -> Pad455
  Direction = (1,0,0)
  Length = 1.1
  Length2 = 5
  Profile = -> Sketch642
  ReferenceAxis = -> Sketch642 [N_Axis]
  Refine = true
  Suppressed = false
  Type = 0
FEATURE [Sketcher::SketchObject] Sketch643
  ArcFitTolerance = 1e-06
  AttachmentSupport = -> [Pocket283]
  ExternalGeometry = -> [Pocket283]
  FullyConstrained = true
  MakeInternals = false
  MapMode = 5
  Placement = pos=(15.9,0,0) rot=(0.57735,0.57735,0.57735;2.0944rad)
  sketch-geometry (12):
    g0: LineSegment StartX=1.9 StartY=7 StartZ=0 EndX=1.9 EndY=0 EndZ=0
    g1: LineSegment StartX=1.9 StartY=0 StartZ=0 EndX=3 EndY=0 EndZ=0
    g2: LineSegment StartX=3 StartY=0 StartZ=0 EndX=3 EndY=7 EndZ=0
    g3: LineSegment StartX=3 StartY=7 StartZ=0 EndX=1.9 EndY=7 EndZ=0
    g4: LineSegment StartX=4.9 StartY=7 StartZ=0 EndX=4.9 EndY=0 EndZ=0
    g5: LineSegment StartX=4.9 StartY=0 StartZ=0 EndX=6 EndY=0 EndZ=0
    g6: LineSegment StartX=6 StartY=0 StartZ=0 EndX=6 EndY=7 EndZ=0
    g7: LineSegment StartX=6 StartY=7 StartZ=0 EndX=4.9 EndY=7 EndZ=0
    g8: LineSegment StartX=7.9 StartY=7 StartZ=0 EndX=7.9 EndY=0 EndZ=0
    g9: LineSegment StartX=7.9 StartY=0 StartZ=0 EndX=9 EndY=0 EndZ=0
    g10: LineSegment StartX=9 StartY=0 StartZ=0 EndX=9 EndY=7 EndZ=0
    g11: LineSegment StartX=9 StartY=7 StartZ=0 EndX=7.9 EndY=7 EndZ=0
  constraints (30):
    c: Coincident(g0,g1)
    c: Coincident(g1,g2)
    c: Coincident(g2,g3)
    c: Coincident(g3,g0)
    c: Vertical(g0)
    c: Vertical(g2)
    c: Horizontal(g1)
    c: Horizontal(g3)
    c: Coincident(g0,g-4)
    c: Coincident(g1,g-3)
    c: Coincident(g4,g5)
    c: Coincident(g5,g6)
    c: Coincident(g6,g7)
    c: Coincident(g7,g4)
    c: Vertical(g4)
    c: Vertical(g6)
    c: Horizontal(g5)
    c: Horizontal(g7)
    c: Coincident(g4,g-5)
    c: Coincident(g5,g-6)
    c: Coincident(g8,g9)
    c: Coincident(g9,g10)
    c: Coincident(g10,g11)
    c: Coincident(g11,g8)
    c: Vertical(g8)
    c: Vertical(g10)
    c: Horizontal(g9)
    c: Horizontal(g11)
    c: Coincident(g8,g-7)
    c: Coincident(g9,g-8)
FEATURE [PartDesign::Pocket] Pocket284
  BaseFeature = -> Pocket283
  Direction = (-1,0,0)
  Length = 1.1
  Length2 = 5
  Profile = -> Sketch643
  ReferenceAxis = -> Sketch643 [N_Axis]
  Refine = true
  Suppressed = false
  Type = 0
FEATURE [PartDesign::Chamfer] Chamfer018
  Angle = 30
  Base = -> Pocket284 [Edge77,Edge69,Edge61,Edge94,Edge58,Edge66,Edge74,Edge3]
  BaseFeature = -> Pocket284
  ChamferType = 2
  FlipDirection = false
  Refine = true
  Size = 1.4
  Size2 = 1
  SupportTransform = false
  Suppressed = false
  UseAllEdges = false
FEATURE [PartDesign::Chamfer] Chamfer019
  Angle = 60
  Base = -> Chamfer018 [Edge47,Edge55,Edge52,Edge56,Edge51,Edge44]
  BaseFeature = -> Chamfer018
  ChamferType = 2
  FlipDirection = false
  Refine = true
  Size = 0.81
  Size2 = 1
  SupportTransform = false
  Suppressed = false
  UseAllEdges = false
FEATURE [Sketcher::SketchObject] Sketch644
  ArcFitTolerance = 1e-06
  AttachmentSupport = -> [Chamfer019]
  ExternalGeometry = -> [Chamfer019]
  FullyConstrained = true
  MakeInternals = false
  MapMode = 5
  Placement = pos=(0,0,7.5) rot=(0,0,1;0rad)
  sketch-geometry (4):
    g0: LineSegment StartX=5.85 StartY=5.075 StartZ=0 EndX=5.85 EndY=-4.925 EndZ=0
    g1: LineSegment StartX=5.85 StartY=-4.925 StartZ=0 EndX=10.05 EndY=-4.925 EndZ=0
    g2: LineSegment StartX=10.05 StartY=-4.925 StartZ=0 EndX=10.05 EndY=5.075 EndZ=0
    g3: LineSegment StartX=10.05 StartY=5.075 StartZ=0 EndX=5.85 EndY=5.075 EndZ=0
  constraints (13):
    c: Coincident(g0,g1)
    c: Coincident(g1,g2)
    c: Coincident(g2,g3)
    c: Coincident(g3,g0)
    c: Vertical(g0)
    c: Vertical(g2)
    c: Horizontal(g1)
    c: Horizontal(g3)
    c: PointOnObject(g0,g-3)
    c: DistanceX(g3,g3) = 4.2
    c: DistanceX(g-4,g-5) = 8.5
    c: DistanceX(g-4,g0) = 2.15
    c: DistanceY(g0,g0) = 10
FEATURE [PartDesign::Pad] Pad456
  BaseFeature = -> Chamfer019
  Direction = (0,0,1)
  Length = 7.5
  Length2 = 10
  Profile = -> Sketch644
  ReferenceAxis = -> Sketch644 [N_Axis]
  Refine = true
  Reversed = true
  Suppressed = false
  Type = 0
FEATURE [PartDesign::Pad] Pad457
  BaseFeature = -> Pad456
  Direction = (0,0,1)
  Length = 1
  Length2 = 10
  Profile = -> Sketch644
  ReferenceAxis = -> Sketch644 [N_Axis]
  Refine = true
  Suppressed = false
  Type = 0
FEATURE [Sketcher::SketchObject] Sketch645
  ArcFitTolerance = 1e-06
  AttachmentSupport = -> [Pad457]
  ExternalGeometry = -> [Pad457]
  FullyConstrained = true
  MakeInternals = false
  MapMode = 5
  Placement = pos=(10.05,0,0) rot=(0.57735,0.57735,0.57735;2.0944rad)
  sketch-geometry (3):
    g0: LineSegment StartX=5.075 StartY=7.5 StartZ=0 EndX=5.075 EndY=8.5 EndZ=0
    g1: LineSegment StartX=5.075 StartY=8.5 StartZ=0 EndX=2.59991 EndY=8.5 EndZ=0
    g2: LineSegment StartX=5.075 StartY=7.5 StartZ=0 EndX=2.59991 EndY=8.5 EndZ=0
  constraints (7):
    c: Coincident(g0,g-3)
    c: Coincident(g0,g-4)
    c: Coincident(g1,g0)
    c: PointOnObject(g1,g-4)
    c: Coincident(g2,g0)
    c: Coincident(g2,g1)
    c: Angle(g2,g1) = 0.383972
FEATURE [PartDesign::Pocket] Pocket285
  BaseFeature = -> Pad457
  Direction = (-1,0,0)
  Length = 5
  Length2 = 5
  Profile = -> Sketch645
  ReferenceAxis = -> Sketch645 [N_Axis]
  Refine = true
  Suppressed = false
  Type = 0
FEATURE [Sketcher::SketchObject] Sketch646
  ArcFitTolerance = 1e-06
  AttachmentSupport = -> [Pocket285]
  ExternalGeometry = -> [Pocket285]
  FullyConstrained = true
  MakeInternals = false
  MapMode = 5
  Placement = pos=(0,0,7) rot=(0,0,1;0rad)
  sketch-geometry (6):
    g0: LineSegment StartX=5.85 StartY=6.125 StartZ=0 EndX=5.85 EndY=5.675 EndZ=0
    g1: LineSegment StartX=5.85 StartY=5.675 StartZ=0 EndX=10.05 EndY=5.675 EndZ=0
    g2: LineSegment StartX=10.05 StartY=5.675 StartZ=0 EndX=10.05 EndY=6.125 EndZ=0
    g3: LineSegment StartX=10.05 StartY=6.125 StartZ=0 EndX=5.85 EndY=6.125 EndZ=0
    g4: LineSegment [constr] StartX=5.85 StartY=5.675 StartZ=0 EndX=5.85 EndY=5.075 EndZ=0
    g5: LineSegment [constr] StartX=10.05 StartY=5.675 StartZ=0 EndX=10.05 EndY=5.075 EndZ=0
  constraints (16):
    c: Coincident(g0,g1)
    c: Coincident(g1,g2)
    c: Coincident(g2,g3)
    c: Coincident(g3,g0)
    c: Vertical(g0)
    c: Vertical(g2)
    c: Horizontal(g1)
    c: Horizontal(g3)
    c: PointOnObject(g0,g-5)
    c: PointOnObject(g1,g-6)
    c: Coincident(g4,g0)
    c: Coincident(g4,g-4)
    c: Coincident(g5,g1)
    c: Coincident(g5,g-3)
    c: Vertical(g5)
    c: Vertical(g4)
FEATURE [PartDesign::Pad] Pad458
  BaseFeature = -> Pocket285
  Direction = (0,0,1)
  Length = 0.3
  Length2 = 10
  Profile = -> Sketch646
  ReferenceAxis = -> Sketch646 [N_Axis]
  Refine = true
  Suppressed = false
  Type = 0
FEATURE [Sketcher::SketchObject] Sketch647
  ArcFitTolerance = 1e-06
  AttachmentSupport = -> [Pad458]
  ExternalGeometry = -> [Pad458]
  FullyConstrained = true
  MakeInternals = false
  MapMode = 5
  Placement = pos=(10.05,0,0) rot=(0.57735,0.57735,0.57735;2.0944rad)
  sketch-geometry (3):
    g0: LineSegment StartX=5.675 StartY=7.3 StartZ=0 EndX=6.125 EndY=7.3 EndZ=0
    g1: LineSegment StartX=6.125 StartY=7.3 StartZ=0 EndX=6.125 EndY=7.11819 EndZ=0
    g2: LineSegment StartX=6.125 StartY=7.11819 StartZ=0 EndX=5.675 EndY=7.3 EndZ=0
  constraints (7):
    c: Coincident(g0,g-5)
    c: Coincident(g0,g-4)
    c: Coincident(g1,g0)
    c: PointOnObject(g1,g-4)
    c: Coincident(g2,g1)
    c: Coincident(g2,g0)
    c: Angle(g2,g0) = 0.383972
FEATURE [PartDesign::Pocket] Pocket286
  BaseFeature = -> Pad458
  Direction = (-1,0,0)
  Length = 4.2
  Length2 = 5
  Profile = -> Sketch647
  ReferenceAxis = -> Sketch647 [N_Axis]
  Refine = true
  Suppressed = false
  Type = 0
FEATURE [Sketcher::SketchObject] Sketch648
  ArcFitTolerance = 1e-06
  AttachmentSupport = -> [Pocket286]
  ExternalGeometry = -> [Pocket286]
  FullyConstrained = true
  MakeInternals = false
  MapMode = 5
  Placement = pos=(5.85,0,0) rot=(0.57735,-0.57735,-0.57735;2.0944rad)
  sketch-geometry (3):
    g0: LineSegment StartX=4.925 StartY=8.5 StartZ=0 EndX=8.88862 EndY=0 EndZ=0
    g1: LineSegment StartX=8.88862 StartY=0 StartZ=0 EndX=4.925 EndY=0 EndZ=0
    g2: LineSegment StartX=4.925 StartY=8.5 StartZ=0 EndX=4.925 EndY=0 EndZ=0
  constraints (7):
    c: Coincident(g0,g-3)
    c: PointOnObject(g0,g-1)
    c: Coincident(g1,g0)
    c: Coincident(g1,g-3)
    c: Angle(g-3,g0) = 0.436332
    c: Coincident(g2,g0)
    c: Coincident(g2,g1)
FEATURE [PartDesign::Pad] Pad459
  BaseFeature = -> Pocket286
  Direction = (-1,0,0)
  Length = 4.2
  Length2 = 10
  Profile = -> Sketch648
  ReferenceAxis = -> Sketch648 [N_Axis]
  Refine = true
  Reversed = true
  Suppressed = false
  Type = 0
FEATURE [Sketcher::SketchObject] Sketch649
  ArcFitTolerance = 1e-06
  AttachmentSupport = -> [Pad459]
  ExternalGeometry = -> [Pad459]
  FullyConstrained = true
  MakeInternals = false
  MapMode = 5
  Placement = pos=(0,0,8.5) rot=(0,0,1;0rad)
  sketch-geometry (8):
    g0: LineSegment StartX=6.55 StartY=1.89991 StartZ=0 EndX=6.55 EndY=-4.225 EndZ=0
    g1: LineSegment StartX=6.55 StartY=-4.225 StartZ=0 EndX=9.35 EndY=-4.225 EndZ=0
    g2: LineSegment StartX=9.35 StartY=-4.225 StartZ=0 EndX=9.35 EndY=1.89991 EndZ=0
    g3: LineSegment StartX=9.35 StartY=1.89991 StartZ=0 EndX=6.55 EndY=1.89991 EndZ=0
    g4: LineSegment StartX=7.05 StartY=1.39991 StartZ=0 EndX=7.05 EndY=-3.725 EndZ=0
    g5: LineSegment StartX=7.05 StartY=-3.725 StartZ=0 EndX=8.85 EndY=-3.725 EndZ=0
    g6: LineSegment StartX=8.85 StartY=-3.725 StartZ=0 EndX=8.85 EndY=1.39991 EndZ=0
    g7: LineSegment StartX=8.85 StartY=1.39991 StartZ=0 EndX=7.05 EndY=1.39991 EndZ=0
  constraints (24):
    c: Coincident(g0,g1)
    c: Coincident(g1,g2)
    c: Coincident(g2,g3)
    c: Coincident(g3,g0)
    c: Vertical(g0)
    c: Vertical(g2)
    c: Horizontal(g1)
    c: Horizontal(g3)
    c: Coincident(g4,g5)
    c: Coincident(g5,g6)
    c: Coincident(g6,g7)
    c: Coincident(g7,g4)
    c: Vertical(g4)
    c: Vertical(g6)
    c: Horizontal(g5)
    c: Horizontal(g7)
    c: DistanceX(g-5,g0) = 0.7
    c: DistanceX(g2,g-4) = 0.7
    c: DistanceY(g0,g-5) = 0.7
    c: DistanceY(g-6,g0) = 0.7
    c: DistanceY(g0,g4) = 0.5
    c: DistanceX(g0,g4) = 0.5
    c: DistanceX(g5,g1) = 0.5
    c: DistanceY(g4,g0) = 0.5
FEATURE [PartDesign::Pocket] Pocket287
  BaseFeature = -> Pad459
  Direction = (0,0,-1)
  Length = 0.5
  Length2 = 5
  Profile = -> Sketch649
  ReferenceAxis = -> Sketch649 [N_Axis]
  Refine = true
  Suppressed = false
  Type = 0
FEATURE [Sketcher::SketchObject] Sketch650
  ArcFitTolerance = 1e-06
  AttachmentSupport = -> [Pocket287]
  ExternalGeometry = -> [Pocket287]
  FullyConstrained = true
  MakeInternals = false
  MapMode = 5
  Placement = pos=(0,0,-4.4e-15) rot=(1,0,0;3.14159rad)
  sketch-geometry (4):
    g0: LineSegment StartX=18.6 StartY=-14.3 StartZ=0 EndX=18.6 EndY=3.9 EndZ=0
    g1: LineSegment StartX=18.6 StartY=3.9 StartZ=0 EndX=-2.7 EndY=3.9 EndZ=0
    g2: LineSegment StartX=-2.7 StartY=3.9 StartZ=0 EndX=-2.7 EndY=-14.3 EndZ=0
    g3: LineSegment StartX=-2.7 StartY=-14.3 StartZ=0 EndX=18.6 EndY=-14.3 EndZ=0
  constraints (13):
    c: Coincident(g0,g1)
    c: Coincident(g1,g2)
    c: Coincident(g2,g3)
    c: Coincident(g3,g0)
    c: Vertical(g0)
    c: Vertical(g2)
    c: Horizontal(g1)
    c: Horizontal(g3)
    c: DistanceX(g3,g3) = 21.3
    c: DistanceY(g2,g2) = 18.2
    c: DistanceY(g2,g-5) = 0.5
    c: DistanceX(g-5,g-5) = 15.9
    c: DistanceX(g2,g-5) = 2.7
FEATURE [PartDesign::Pad] Pad460
  BaseFeature = -> Pocket287
  Direction = (0,0,-1)
  Length = 4.8
  Length2 = 10
  Profile = -> Sketch650
  ReferenceAxis = -> Sketch650 [N_Axis]
  Refine = true
  Suppressed = false
  Type = 0
FEATURE [PartDesign::Chamfer] Chamfer020
  Angle = 60
  Base = -> Pad460 [Edge94,Edge62]
  BaseFeature = -> Pad460
  ChamferType = 2
  FlipDirection = false
  Refine = true
  Size = 1
  Size2 = 1
  SupportTransform = false
  Suppressed = false
  UseAllEdges = false
FEATURE [Sketcher::SketchObject] Sketch651
  ArcFitTolerance = 1e-06
  AttachmentSupport = -> [Chamfer020]
  ExternalGeometry = -> [Chamfer020]
  FullyConstrained = true
  MakeInternals = false
  MapMode = 5
  Placement = pos=(0,0,-4.8) rot=(1,0,0;3.14159rad)
  sketch-geometry (16):
    g0: LineSegment StartX=15.9 StartY=-14.3 StartZ=0 EndX=22.4 EndY=-20.8 EndZ=0
    g1: LineSegment StartX=22.4 StartY=-20.8 StartZ=0 EndX=22.4 EndY=8.82361 EndZ=0
    g2: LineSegment StartX=22.4 StartY=8.82361 StartZ=0 EndX=19.15 EndY=10.7 EndZ=0
    g3: LineSegment StartX=19.15 StartY=10.7 StartZ=0 EndX=16.65 EndY=10.7 EndZ=0
    g4: LineSegment StartX=16.65 StartY=10.7 StartZ=0 EndX=16.65 EndY=3.9 EndZ=0
    g5: LineSegment StartX=16.65 StartY=3.9 StartZ=0 EndX=18.6 EndY=3.9 EndZ=0
    g6: LineSegment StartX=18.6 StartY=3.9 StartZ=0 EndX=18.6 EndY=-14.3 EndZ=0
    g7: LineSegment StartX=18.6 StartY=-14.3 StartZ=0 EndX=15.9 EndY=-14.3 EndZ=0
    g8: LineSegment StartX=4e-16 StartY=-14.3 StartZ=0 EndX=-6.5 EndY=-20.8 EndZ=0
    g9: LineSegment StartX=-6.5 StartY=-20.8 StartZ=0 EndX=-6.5 EndY=8.82361 EndZ=0
    g10: LineSegment StartX=-6.5 StartY=8.82361 StartZ=0 EndX=-3.25 EndY=10.7 EndZ=0
    g11: LineSegment StartX=-3.25 StartY=10.7 StartZ=0 EndX=-0.75 EndY=10.7 EndZ=0
    g12: LineSegment StartX=-0.75 StartY=10.7 StartZ=0 EndX=-0.75 EndY=3.9 EndZ=0
    g13: LineSegment StartX=-0.75 StartY=3.9 StartZ=0 EndX=-2.7 EndY=3.9 EndZ=0
    g14: LineSegment StartX=-2.7 StartY=3.9 StartZ=0 EndX=-2.7 EndY=-14.3 EndZ=0
    g15: LineSegment StartX=-2.7 StartY=-14.3 StartZ=0 EndX=4e-16 EndY=-14.3 EndZ=0
  constraints (44):
    c: PointOnObject(g0,g-4)
    c: Coincident(g1,g0)
    c: Vertical(g1)
    c: Coincident(g2,g1)
    c: Coincident(g3,g2)
    c: Horizontal(g3)
    c: Coincident(g4,g3)
    c: PointOnObject(g4,g-3)
    c: Vertical(g4)
    c: Coincident(g5,g4)
    c: Coincident(g5,g-5)
    c: Coincident(g6,g5)
    c: Coincident(g6,g-5)
    c: Coincident(g7,g6)
    c: Coincident(g7,g0)
    c: PointOnObject(g8,g-4)
    c: Coincident(g9,g8)
    c: Vertical(g9)
    c: Coincident(g10,g9)
    c: Coincident(g11,g10)
    c: Horizontal(g11)
    c: Coincident(g12,g11)
    c: PointOnObject(g12,g-3)
    c: Vertical(g12)
    c: Coincident(g13,g12)
    c: Coincident(g13,g-6)
    c: Coincident(g14,g13)
    c: Coincident(g14,g-6)
    c: Coincident(g15,g14)
    c: Coincident(g15,g8)
    c: DistanceX(g9,g11) = 5.75
    c: DistanceX(g3,g1) = 5.75
    c: DistanceY(g0,g3) = 31.5
    c: DistanceY(g8,g10) = 31.5
    c: DistanceY(g4,g4) = 6.8
    c: DistanceY(g12,g12) = 6.8
    c: Angle(g1,g0) = 0.785398
    c: Angle(g8,g9) = 0.785398
    c: DistanceX(g9,g13) = 3.8
    c: DistanceX(g5,g1) = 3.8
    c: Angle(g3,g2) = 2.61799
    c: Angle(g10,g11) = 2.61799
    c: DistanceX(g3,g3) = 2.5
    c: DistanceX(g11,g11) = 2.5
FEATURE [PartDesign::Pad] Pad461
  BaseFeature = -> Chamfer020
  Direction = (0,0,-1)
  Length = 1.75
  Length2 = 10
  Profile = -> Sketch651
  ReferenceAxis = -> Sketch651 [N_Axis]
  Refine = true
  Reversed = true
  Suppressed = false
  Type = 0
FEATURE [PartDesign::Pad] Pad462
  BaseFeature = -> Pad461
  Direction = (0,0,-1)
  Length = 1
  Length2 = 10
  Profile = -> Sketch651
  ReferenceAxis = -> Sketch651 [N_Axis]
  Refine = true
  Suppressed = false
  Type = 0
FEATURE [Sketcher::SketchObject] Sketch652
  ArcFitTolerance = 1e-06
  AttachmentSupport = -> [Pad462]
  ExternalGeometry = -> [Pad462]
  FullyConstrained = true
  MakeInternals = false
  MapMode = 5
  Placement = pos=(0,0,-4.8) rot=(1,0,0;3.14159rad)
  sketch-geometry (10):
    g0: LineSegment StartX=-0.75 StartY=1.9 StartZ=0 EndX=16.65 EndY=1.9 EndZ=0
    g1: LineSegment StartX=16.65 StartY=1.9 StartZ=0 EndX=16.65 EndY=-14.3 EndZ=0
    g2: LineSegment StartX=-0.75 StartY=1.9 StartZ=0 EndX=-0.75 EndY=-14.3 EndZ=0
    g3: LineSegment [constr] StartX=-0.75 StartY=3.9 StartZ=0 EndX=-0.75 EndY=1.9 EndZ=0
    g4: LineSegment [constr] StartX=16.65 StartY=3.9 StartZ=0 EndX=16.65 EndY=1.9 EndZ=0
    g5: LineSegment StartX=-0.75 StartY=-14.3 StartZ=0 EndX=-2.7 EndY=-14.3 EndZ=0
    g6: LineSegment StartX=-2.7 StartY=-14.3 StartZ=0 EndX=-2.7 EndY=3.9 EndZ=0
    g7: LineSegment StartX=-2.7 StartY=3.9 StartZ=0 EndX=18.6 EndY=3.9 EndZ=0
    g8: LineSegment StartX=18.6 StartY=3.9 StartZ=0 EndX=18.6 EndY=-14.3 EndZ=0
    g9: LineSegment StartX=18.6 StartY=-14.3 StartZ=0 EndX=16.65 EndY=-14.3 EndZ=0
  constraints (24):
    c: Horizontal(g0)
    c: Coincident(g1,g0)
    c: PointOnObject(g1,g-9)
    c: Vertical(g1)
    c: Coincident(g2,g0)
    c: PointOnObject(g2,g-8)
    c: Vertical(g2)
    c: Coincident(g3,g-6)
    c: Coincident(g3,g0)
    c: Coincident(g4,g-5)
    c: Coincident(g4,g0)
    c: Vertical(g4)
    c: Vertical(g3)
    c: DistanceY(g3,g3) = 2
    c: Coincident(g5,g2)
    c: Coincident(g5,g-8)
    c: Coincident(g6,g5)
    c: Coincident(g6,g-7)
    c: Coincident(g7,g6)
    c: Coincident(g7,g-5)
    c: Coincident(g8,g7)
    c: Coincident(g8,g-9)
    c: Coincident(g9,g8)
    c: Coincident(g9,g1)
FEATURE [PartDesign::Pad] Pad463
  BaseFeature = -> Pad462
  Direction = (0,0,-1)
  Length = 1
  Length2 = 10
  Profile = -> Sketch652
  ReferenceAxis = -> Sketch652 [N_Axis]
  Refine = true
  Suppressed = false
  Type = 0
FEATURE [PartDesign::Pocket] Pocket288
  BaseFeature = -> Pad463
  Direction = (7e-16,1,0)
  Length = 5
  Length2 = 5
  Profile = -> Pad463 [Face144,Face145]
  Refine = true
  Suppressed = false
  Type = 0
FEATURE [Sketcher::SketchObject] Sketch653
  ArcFitTolerance = 1e-06
  AttachmentOffset = pos=(0,0,-0.5) rot=(0,0,1;0rad)
  AttachmentSupport = -> [Pocket288]
  ExternalGeometry = -> [Pocket288]
  FullyConstrained = true
  MakeInternals = false
  MapMode = 5
  Placement = pos=(0,13.8,1e-16) rot=(0,0.707107,0.707107;3.14159rad)
  sketch-geometry (42):
    g0: LineSegment StartX=-13.95 StartY=-4.8 StartZ=0 EndX=-1.95 EndY=-4.8 EndZ=0
    g1: LineSegment StartX=-1.95 StartY=-4.8 StartZ=0 EndX=-1.95 EndY=-3.2 EndZ=0
    g2: LineSegment StartX=-13.95 StartY=-4.8 StartZ=0 EndX=-13.95 EndY=-3.2 EndZ=0
    g3: LineSegment [constr] StartX=-13.95 StartY=-3.2 StartZ=0 EndX=-13.95 EndY=2.8 EndZ=0
    g4: LineSegment [constr] StartX=-13.95 StartY=2.8 StartZ=0 EndX=-1.95 EndY=2.8 EndZ=0
    g5: LineSegment [constr] StartX=-1.95 StartY=2.8 StartZ=0 EndX=-1.95 EndY=-3.2 EndZ=0
    g6: ArcOfCircle [constr] CenterX=-7.95 CenterY=-3.2 CenterZ=0 NormalX=0 NormalY=0 NormalZ=1 AngleXU=0 Radius=6 StartAngle=0 EndAngle=3.14159
    g7: LineSegment [constr] StartX=-13.95 StartY=-3.2 StartZ=0 EndX=-7.95 EndY=-3.2 EndZ=0
    g8: LineSegment [constr] StartX=-7.95 StartY=-3.2 StartZ=0 EndX=-1.95 EndY=-3.2 EndZ=0
    g9: LineSegment StartX=-8.52466 StartY=2.57466 StartZ=0 EndX=-7.95 EndY=2 EndZ=0
    g10: LineSegment StartX=-9.32136 StartY=2.45267 StartZ=0 EndX=-9.7202 EndY=1.68942 EndZ=0
    g11: LineSegment StartX=-9.7202 StartY=1.68942 StartZ=0 EndX=-10.4005 EndY=2.04489 EndZ=0
    g12: LineSegment StartX=-11.1299 StartY=1.6475 StartZ=0 EndX=-11.2026 EndY=0.857196 EndZ=0
    g13: LineSegment StartX=-11.2026 StartY=0.857196 StartZ=0 EndX=-12.0314 EndY=0.93337 EndZ=0
    g14: LineSegment StartX=-12.5544 StartY=0.286387 StartZ=0 EndX=-12.3373 EndY=-0.408653 EndZ=0
    g15: LineSegment StartX=-12.3373 StartY=-0.408653 StartZ=0 EndX=-13.2056 EndY=-0.679893 EndZ=0
    g16: LineSegment StartX=-13.4313 StartY=-1.48818 StartZ=0 EndX=-13.0031 EndY=-1.97284 EndZ=0
    g17: LineSegment [constr] StartX=-7.95 StartY=2.8 StartZ=0 EndX=-7.95 EndY=-3.2 EndZ=0
    g18: LineSegment StartX=-13.0031 StartY=-1.97284 StartZ=0 EndX=-13.95 EndY=-3.2 EndZ=0
    g19: ArcOfCircle CenterX=-8.87822 CenterY=2.22111 CenterZ=0 NormalX=0 NormalY=0 NormalZ=1 AngleXU=0 Radius=0.5 StartAngle=0.785398 EndAngle=2.66007
    g20: ArcOfCircle CenterX=-10.632 CenterY=1.60174 CenterZ=0 NormalX=0 NormalY=0 NormalZ=1 AngleXU=0 Radius=0.5 StartAngle=1.08928 EndAngle=3.04995
    g21: ArcOfCircle CenterX=-12.0772 CenterY=0.435468 CenterZ=0 NormalX=0 NormalY=0 NormalZ=1 AngleXU=0 Radius=0.5 StartAngle=1.47915 EndAngle=3.44436
    g22: ArcOfCircle CenterX=-13.0565 CenterY=-1.15715 CenterZ=0 NormalX=0 NormalY=0 NormalZ=1 AngleXU=0 Radius=0.5 StartAngle=1.87356 EndAngle=3.86516
    g23: LineSegment [constr] StartX=-13.0565 StartY=-1.15715 StartZ=0 EndX=-12.0772 EndY=0.435468 EndZ=0
    g24: LineSegment [constr] StartX=-12.0772 StartY=0.435468 StartZ=0 EndX=-10.632 EndY=1.60174 EndZ=0
    g25: LineSegment [constr] StartX=-10.632 StartY=1.60174 StartZ=0 EndX=-8.87822 EndY=2.22111 EndZ=0
    g26: LineSegment [constr] StartX=-13.0565 StartY=-1.15715 StartZ=0 EndX=-13.95 EndY=-3.2 EndZ=0
    g27: LineSegment [constr] StartX=-8.87822 StartY=2.22111 StartZ=0 EndX=-7.95 EndY=2.8 EndZ=0
    g28: ArcOfCircle [constr] CenterX=-7.95 CenterY=-3.2 CenterZ=0 NormalX=0 NormalY=0 NormalZ=1 AngleXU=0 Radius=5.2 StartAngle=0 EndAngle=3.14159
    g29: LineSegment StartX=-7.95 StartY=2 StartZ=0 EndX=-7.37534 EndY=2.57466 EndZ=0
    g30: LineSegment StartX=-6.57864 StartY=2.45267 StartZ=0 EndX=-6.1798 EndY=1.68942 EndZ=0
    g31: LineSegment StartX=-6.1798 StartY=1.68942 StartZ=0 EndX=-5.49954 EndY=2.04489 EndZ=0
    g32: LineSegment StartX=-4.77007 StartY=1.6475 StartZ=0 EndX=-4.69744 EndY=0.857196 EndZ=0
    g33: LineSegment StartX=-4.69744 StartY=0.857196 StartZ=0 EndX=-3.86861 EndY=0.93337 EndZ=0
    g34: LineSegment StartX=-3.34559 StartY=0.286387 StartZ=0 EndX=-3.5627 EndY=-0.408653 EndZ=0
    g35: LineSegment StartX=-3.5627 StartY=-0.408653 StartZ=0 EndX=-2.69438 EndY=-0.679893 EndZ=0
    g36: LineSegment StartX=-2.46873 StartY=-1.48818 StartZ=0 EndX=-2.89688 EndY=-1.97284 EndZ=0
    g37: LineSegment StartX=-2.89688 StartY=-1.97284 StartZ=0 EndX=-1.95 EndY=-3.2 EndZ=0
    g38: ArcOfCircle CenterX=-7.02178 CenterY=2.22111 CenterZ=0 NormalX=0 NormalY=0 NormalZ=1 AngleXU=0 Radius=0.5 StartAngle=0.481521 EndAngle=2.35619
    g39: ArcOfCircle CenterX=-5.26797 CenterY=1.60174 CenterZ=0 NormalX=0 NormalY=0 NormalZ=1 AngleXU=0 Radius=0.5 StartAngle=0.0916473 EndAngle=2.05232
    g40: ArcOfCircle CenterX=-3.82285 CenterY=0.435468 CenterZ=0 NormalX=0 NormalY=0 NormalZ=1 AngleXU=0 Radius=0.5 StartAngle=5.98042 EndAngle=7.94563
    g41: ArcOfCircle CenterX=-2.84346 CenterY=-1.15715 CenterZ=0 NormalX=0 NormalY=0 NormalZ=1 AngleXU=0 Radius=0.5 StartAngle=5.55962 EndAngle=7.55121
  constraints (112):
    c: DistanceX(g-3,g-3) = 15.9
    c: PointOnObject(g0,g-3)
    c: PointOnObject(g0,g-3)
    c: Coincident(g1,g0)
    c: Vertical(g1)
    c: Coincident(g2,g0)
    c: Vertical(g2)
    c: Coincident(g3,g2)
    c: Vertical(g3)
    c: Coincident(g4,g3)
    c: Horizontal(g4)
    c: Coincident(g5,g4)
    c: Coincident(g5,g1)
    c: Vertical(g5)
    c: DistanceY(g0,g3) = 7.6
    c: DistanceX(g0,g0) = 12
    c: DistanceX(g-3,g0) = 1.95
    c: Coincident(g6,g2)
    c: Coincident(g6,g1)
    c: Coincident(g7,g2)
    c: Coincident(g7,g6)
    c: Coincident(g8,g6)
    c: Coincident(g8,g1)
    c: Horizontal(g8)
    c: Horizontal(g7)
    c: Tangent(g6,g4)
    c: Coincident(g11,g10)
    c: Coincident(g13,g12)
    c: Coincident(g15,g14)
    c: PointOnObject(g17,g6)
    c: Coincident(g17,g6)
    c: Vertical(g17)
    c: PointOnObject(g9,g17)
    c: Coincident(g18,g16)
    c: Coincident(g18,g2)
    c: Tangent(g9,g19) = 1.5708
    c: Tangent(g10,g19) = -1.5708
    c: Tangent(g11,g20) = -1.5708
    c: Tangent(g12,g20) = -1.5708
    c: Tangent(g13,g21) = -1.5708
    c: Tangent(g14,g21) = -1.5708
    c: Tangent(g15,g22) = -1.5708
    c: Tangent(g16,g22) = -1.5708
    c: Radius(g22) = 0.5
    c: Radius(g21) = 0.5
    c: Radius(g20) = 0.5
    c: Radius(g19) = 0.5
    c: Tangent(g19,g6)
    c: Tangent(g6,g20)
    c: Tangent(g22,g6)
    c: Tangent(g21,g6)
    c: Coincident(g23,g22)
    c: Coincident(g23,g21)
    c: Coincident(g24,g21)
    c: Coincident(g24,g20)
    c: Coincident(g25,g20)
    c: Coincident(g25,g19)
    c: Coincident(g26,g23)
    c: Coincident(g26,g2)
    c: Coincident(g27,g25)
    c: Coincident(g27,g17)
    c: PointOnObject(g28,g7)
    c: PointOnObject(g28,g8)
    c: Coincident(g28,g6)
    c: Radius(g28) = 5.2
    c: PointOnObject(g10,g28)
    c: PointOnObject(g12,g28)
    c: PointOnObject(g14,g28)
    c: PointOnObject(g16,g28)
    c: Perpendicular(g15,g14)
    c: Perpendicular(g12,g13)
    c: Perpendicular(g10,g11)
    c: Angle(g9,g17) = 2.35619
    c: PointOnObject(g9,g28)
    c: Distance(g16,g14) = 1.7
    c: Distance(g14,g12) = 1.7
    c: Distance(g12,g10) = 1.7
    c: Distance(g18) = 1.55
    c: Coincident(g29,g9)
    c: PointOnObject(g30,g28)
    c: Coincident(g31,g30)
    c: PointOnObject(g32,g28)
    c: Coincident(g33,g32)
    c: PointOnObject(g34,g28)
    c: Coincident(g35,g34)
    c: PointOnObject(g36,g28)
    c: Coincident(g37,g36)
    c: Coincident(g37,g1)
    c: Tangent(g29,g38) = 1.5708
    c: Tangent(g30,g38) = 1.5708
    c: Tangent(g31,g39) = 1.5708
    c: Tangent(g32,g39) = 1.5708
    c: Tangent(g33,g40) = 1.5708
    c: Tangent(g34,g40) = 1.5708
    c: Tangent(g35,g41) = 1.5708
    c: Tangent(g36,g41) = 1.5708
    c: Radius(g38) = 0.5
    c: Radius(g39) = 0.5
    c: Radius(g40) = 0.5
    c: Radius(g41) = 0.5
    c: Tangent(g38,g6)
    c: Tangent(g39,g6)
    c: Tangent(g40,g6)
    c: Tangent(g41,g6)
    c: Angle(g17,g29) = 2.35619
    c: Distance(g30,g32) = 1.7
    c: Distance(g32,g34) = 1.7
    c: Distance(g34,g36) = 1.7
    c: Distance(g1,g36) = 1.55
    c: Perpendicular(g31,g30)
    c: Perpendicular(g33,g32)
    c: Perpendicular(g35,g34)
FEATURE [Sketcher::SketchObject] Sketch654
  ArcFitTolerance = 1e-06
  AttachmentOffset = pos=(0,0,2) rot=(0,0,1;0rad)
  AttachmentSupport = -> [Pocket288]
  ExternalGeometry = -> [Sketch653]
  FullyConstrained = true
  MakeInternals = false
  MapMode = 5
  Placement = pos=(0,16.3,-4e-16) rot=(0,0.707107,0.707107;3.14159rad)
  sketch-geometry (58):
    g0: LineSegment StartX=-12.95 StartY=-4.8 StartZ=0 EndX=-2.95 EndY=-4.8 EndZ=0
    g1: LineSegment StartX=-12.95 StartY=-4.8 StartZ=0 EndX=-12.95 EndY=-3.5 EndZ=0
    g2: LineSegment StartX=-2.95 StartY=-4.8 StartZ=0 EndX=-2.95 EndY=-3.5 EndZ=0
    g3: ArcOfCircle [constr] CenterX=-7.95 CenterY=-3.5 CenterZ=0 NormalX=0 NormalY=0 NormalZ=1 AngleXU=0 Radius=5 StartAngle=0 EndAngle=3.14159
    g4: LineSegment [constr] StartX=-7.95 StartY=-3.5 StartZ=0 EndX=-12.95 EndY=-3.5 EndZ=0
    g5: LineSegment [constr] StartX=-7.95 StartY=-3.5 StartZ=0 EndX=-2.95 EndY=-3.5 EndZ=0
    g6: LineSegment [constr] StartX=-3.5627 StartY=-0.408653 StartZ=0 EndX=-7.95 EndY=-3.5 EndZ=0
    g7: LineSegment [constr] StartX=-4.69744 StartY=0.857196 StartZ=0 EndX=-7.95 EndY=-3.5 EndZ=0
    g8: LineSegment [constr] StartX=-6.1798 StartY=1.68942 StartZ=0 EndX=-7.95 EndY=-3.5 EndZ=0
    g9: LineSegment [constr] StartX=-7.95 StartY=2 StartZ=0 EndX=-7.95 EndY=-3.5 EndZ=0
    g10: LineSegment [constr] StartX=-9.7202 StartY=1.68942 StartZ=0 EndX=-7.95 EndY=-3.5 EndZ=0
    g11: LineSegment [constr] StartX=-11.2026 StartY=0.857196 StartZ=0 EndX=-7.95 EndY=-3.5 EndZ=0
    g12: LineSegment [constr] StartX=-12.3373 StartY=-0.408653 StartZ=0 EndX=-7.95 EndY=-3.5 EndZ=0
    g13: LineSegment [constr] StartX=-13.0031 StartY=-1.97284 StartZ=0 EndX=-7.95 EndY=-3.5 EndZ=0
    g14: LineSegment [constr] StartX=-2.89688 StartY=-1.97284 StartZ=0 EndX=-7.95 EndY=-3.5 EndZ=0
    g15: LineSegment StartX=-12.4984 StartY=-1.61462 StartZ=0 EndX=-12.2576 EndY=-2.19816 EndZ=0
    g16: LineSegment StartX=-12.2576 StartY=-2.19816 StartZ=0 EndX=-12.95 EndY=-3.5 EndZ=0
    g17: LineSegment StartX=-12.382 StartY=-1.29712 StartZ=0 EndX=-11.6286 EndY=-0.908043 EndZ=0
    g18: LineSegment StartX=-11.6286 StartY=-0.908043 StartZ=0 EndX=-11.6376 EndY=-0.225339 EndZ=0
    g19: LineSegment StartX=-11.4132 StartY=0.0266645 StartZ=0 EndX=-10.6419 EndY=0.106083 EndZ=0
    g20: LineSegment StartX=-10.6419 StartY=0.106083 StartZ=0 EndX=-10.3955 EndY=0.789237 EndZ=0
    g21: LineSegment StartX=-10.0952 StartY=0.945787 StartZ=0 EndX=-9.40282 EndY=0.759026 EndZ=0
    g22: LineSegment StartX=-9.40282 StartY=0.759026 StartZ=0 EndX=-8.90139 EndY=1.35038 EndZ=0
    g23: LineSegment StartX=-8.57627 StartY=1.39946 StartZ=0 EndX=-7.95 EndY=1 EndZ=0
    g24: LineSegment StartX=-7.95 StartY=1 StartZ=0 EndX=-7.32373 EndY=1.39946 EndZ=0
    g25: LineSegment StartX=-6.99861 StartY=1.35038 StartZ=0 EndX=-6.49718 EndY=0.759026 EndZ=0
    g26: LineSegment StartX=-6.49718 StartY=0.759026 StartZ=0 EndX=-5.80481 EndY=0.945787 EndZ=0
    g27: LineSegment StartX=-5.50454 StartY=0.789237 StartZ=0 EndX=-5.25813 EndY=0.106083 EndZ=0
    g28: LineSegment StartX=-5.25813 StartY=0.106083 StartZ=0 EndX=-4.48676 EndY=0.0266645 EndZ=0
    g29: LineSegment StartX=-4.26238 StartY=-0.225339 StartZ=0 EndX=-4.27145 EndY=-0.908043 EndZ=0
    g30: LineSegment StartX=-4.27145 StartY=-0.908043 StartZ=0 EndX=-3.51799 EndY=-1.29712 EndZ=0
    g31: LineSegment StartX=-3.4016 StartY=-1.61462 StartZ=0 EndX=-3.64242 EndY=-2.19816 EndZ=0
    g32: LineSegment StartX=-3.64242 StartY=-2.19816 StartZ=0 EndX=-2.95 EndY=-3.5 EndZ=0
    g33: ArcOfCircle CenterX=-5.73971 CenterY=0.704414 CenterZ=0 NormalX=0 NormalY=0 NormalZ=1 AngleXU=0 Radius=0.25 StartAngle=0.346165 EndAngle=1.83427
    g34: GeomPoint [constr] X=-5.58262 Y=1.00572 Z=0
    g35: ArcOfCircle CenterX=-7.18929 CenterY=1.18869 CenterZ=0 NormalX=0 NormalY=0 NormalZ=1 AngleXU=0 Radius=0.25 StartAngle=0.703303 EndAngle=2.13858
    g36: GeomPoint [constr] X=-7.13975 Y=1.51682 Z=0
    g37: ArcOfCircle CenterX=-8.71071 CenterY=1.18869 CenterZ=0 NormalX=0 NormalY=0 NormalZ=1 AngleXU=0 Radius=0.25 StartAngle=1.00301 EndAngle=2.43829
    g38: GeomPoint [constr] X=-8.76025 Y=1.51682 Z=0
    g39: ArcOfCircle CenterX=-10.1603 CenterY=0.704414 CenterZ=0 NormalX=0 NormalY=0 NormalZ=1 AngleXU=0 Radius=0.25 StartAngle=1.30732 EndAngle=2.79543
    g40: GeomPoint [constr] X=-10.3174 Y=1.00572 Z=0
    g41: ArcOfCircle CenterX=-11.3876 CenterY=-0.222021 CenterZ=0 NormalX=0 NormalY=0 NormalZ=1 AngleXU=0 Radius=0.25 StartAngle=1.67339 EndAngle=3.15487
    g42: GeomPoint [constr] X=-11.6406 Y=0.00325118 Z=0
    g43: ArcOfCircle CenterX=-12.2673 CenterY=-1.51925 CenterZ=0 NormalX=0 NormalY=0 NormalZ=1 AngleXU=0 Radius=0.25 StartAngle=2.04746 EndAngle=3.53299
    g44: GeomPoint [constr] X=-12.586 Y=-1.40243 Z=0
    g45: ArcOfCircle CenterX=-4.51236 CenterY=-0.222021 CenterZ=0 NormalX=0 NormalY=0 NormalZ=1 AngleXU=0 Radius=0.25 StartAngle=6.26991 EndAngle=7.75139
    g46: GeomPoint [constr] X=-4.25935 Y=0.00325118 Z=0
    g47: ArcOfCircle CenterX=-3.6327 CenterY=-1.51925 CenterZ=0 NormalX=0 NormalY=0 NormalZ=1 AngleXU=0 Radius=0.25 StartAngle=5.89179 EndAngle=7.37731
    g48: GeomPoint [constr] X=-3.31403 Y=-1.40243 Z=0
    g49: ArcOfCircle [constr] CenterX=-7.95 CenterY=-3.5 CenterZ=0 NormalX=0 NormalY=0 NormalZ=1 AngleXU=0 Radius=4.5 StartAngle=1e-16 EndAngle=3.14159
    g50: LineSegment [constr] StartX=-13.0565 StartY=-1.15715 StartZ=0 EndX=-7.95 EndY=-3.5 EndZ=0
    g51: LineSegment [constr] StartX=-12.0772 StartY=0.435468 StartZ=0 EndX=-7.95 EndY=-3.5 EndZ=0
    g52: LineSegment [constr] StartX=-10.632 StartY=1.60174 StartZ=0 EndX=-7.95 EndY=-3.5 EndZ=0
    g53: LineSegment [constr] StartX=-8.87822 StartY=2.22111 StartZ=0 EndX=-7.95 EndY=-3.5 EndZ=0
    g54: LineSegment [constr] StartX=-7.02178 StartY=2.22111 StartZ=0 EndX=-7.95 EndY=-3.5 EndZ=0
    g55: LineSegment [constr] StartX=-5.26797 StartY=1.60174 StartZ=0 EndX=-7.95 EndY=-3.5 EndZ=0
    g56: LineSegment [constr] StartX=-3.82285 StartY=0.435468 StartZ=0 EndX=-7.95 EndY=-3.5 EndZ=0
    g57: LineSegment [constr] StartX=-2.84346 StartY=-1.15715 StartZ=0 EndX=-7.95 EndY=-3.5 EndZ=0
  constraints (141):
    c: PointOnObject(g0,g-15)
    c: PointOnObject(g0,g-15)
    c: DistanceX(g0,g0) = 10
    c: DistanceX(g-15,g-15) = 12
    c: DistanceX(g-15,g0) = 1
    c: Coincident(g1,g0)
    c: Vertical(g1)
    c: Coincident(g2,g0)
    c: Vertical(g2)
    c: Coincident(g3,g1)
    c: Coincident(g3,g2)
    c: Coincident(g4,g3)
    c: Coincident(g4,g3)
    c: Coincident(g5,g3)
    c: Coincident(g5,g3)
    c: Horizontal(g5)
    c: Horizontal(g4)
    c: Coincident(g6,g-12)
    c: Coincident(g6,g3)
    c: Coincident(g7,g-10)
    c: Coincident(g7,g6)
    c: Coincident(g8,g-8)
    c: Coincident(g8,g6)
    c: Coincident(g9,g-6)
    c: Coincident(g9,g6)
    c: Coincident(g10,g-4)
    c: Coincident(g10,g6)
    c: Coincident(g11,g6)
    c: Coincident(g12,g6)
    c: Coincident(g13,g-17)
    c: Coincident(g13,g6)
    c: Coincident(g14,g-16)
    c: Coincident(g14,g6)
    c: DistanceY(g1,g1) = 1.3
    c: Coincident(g11,g-18)
    c: Coincident(g12,g-19)
    c: PointOnObject(g15,g13)
    c: Coincident(g16,g15)
    c: Coincident(g16,g1)
    c: Coincident(g18,g17)
    c: PointOnObject(g19,g11)
    c: Coincident(g20,g19)
    c: Coincident(g22,g21)
    c: PointOnObject(g23,g9)
    c: Coincident(g24,g23)
    c: PointOnObject(g25,g8)
    c: Coincident(g26,g25)
    c: PointOnObject(g27,g7)
    c: Coincident(g28,g27)
    c: PointOnObject(g29,g6)
    c: Coincident(g30,g29)
    c: PointOnObject(g31,g14)
    c: Coincident(g32,g31)
    c: Coincident(g32,g2)
    c: PointOnObject(g34,g26)
    c: PointOnObject(g34,g27)
    c: Tangent(g26,g33) = 1.5708
    c: Tangent(g27,g33) = 1.5708
    c: PointOnObject(g36,g24)
    c: PointOnObject(g36,g25)
    c: Tangent(g24,g35) = 1.5708
    c: Tangent(g25,g35) = 1.5708
    c: PointOnObject(g38,g22)
    c: PointOnObject(g38,g23)
    c: Tangent(g22,g37) = 1.5708
    c: Tangent(g23,g37) = 1.5708
    c: PointOnObject(g40,g20)
    c: PointOnObject(g40,g21)
    c: Tangent(g20,g39) = 1.5708
    c: Tangent(g21,g39) = 1.5708
    c: PointOnObject(g42,g18)
    c: PointOnObject(g42,g19)
    c: Tangent(g18,g41) = 1.5708
    c: Tangent(g19,g41) = 1.5708
    c: PointOnObject(g44,g15)
    c: PointOnObject(g44,g17)
    c: Tangent(g15,g43) = -1.5708
    c: Tangent(g17,g43) = 1.5708
    c: PointOnObject(g46,g28)
    c: PointOnObject(g46,g29)
    c: Tangent(g28,g45) = 1.5708
    c: Tangent(g29,g45) = 1.5708
    c: PointOnObject(g48,g30)
    c: PointOnObject(g48,g31)
    c: Tangent(g30,g47) = 1.5708
    c: Tangent(g31,g47) = 1.5708
    c: Radius(g43) = 0.25
    c: Radius(g41) = 0.25
    c: Radius(g39) = 0.25
    c: Radius(g37) = 0.25
    c: Radius(g35) = 0.25
    c: Radius(g33) = 0.25
    c: Radius(g45) = 0.25
    c: Radius(g47) = 0.25
    c: PointOnObject(g49,g4)
    c: PointOnObject(g49,g5)
    c: Coincident(g49,g3)
    c: Tangent(g43,g3)
    c: Tangent(g41,g3)
    c: Tangent(g39,g3)
    c: PointOnObject(g15,g49)
    c: Radius(g49) = 4.5
    c: Coincident(g50,g-20)
    c: Coincident(g50,g3)
    c: PointOnObject(g43,g50)
    c: Coincident(g51,g-21)
    c: Coincident(g51,g3)
    c: PointOnObject(g41,g51)
    c: Coincident(g52,g-22)
    c: Coincident(g52,g3)
    c: Coincident(g53,g-23)
    c: Coincident(g53,g3)
    c: PointOnObject(g39,g52)
    c: PointOnObject(g37,g53)
    c: Tangent(g37,g3)
    c: PointOnObject(g21,g10)
    c: PointOnObject(g21,g49)
    c: PointOnObject(g19,g49)
    c: PointOnObject(g23,g49)
    c: PointOnObject(g17,g12)
    c: PointOnObject(g17,g49)
    c: Tangent(g33,g3)
    c: Tangent(g45,g3)
    c: Tangent(g47,g3)
    c: PointOnObject(g25,g49)
    c: Tangent(g35,g3)
    c: Coincident(g54,g-24)
    c: Coincident(g54,g3)
    c: Coincident(g55,g-25)
    c: Coincident(g55,g3)
    c: Coincident(g56,g-26)
    c: Coincident(g56,g3)
    c: Coincident(g57,g-27)
    c: Coincident(g57,g3)
    c: PointOnObject(g47,g57)
    c: PointOnObject(g45,g56)
    c: PointOnObject(g33,g55)
    c: PointOnObject(g35,g54)
    c: PointOnObject(g27,g49)
    c: PointOnObject(g29,g49)
    c: PointOnObject(g31,g49)
FEATURE [PartDesign::AdditiveLoft] AdditiveLoft004
  BaseFeature = -> Pocket288
  Closed = false
  Profile = -> Sketch653
  Refine = true
  Ruled = false
  Sections = -> [Sketch654]
  Suppressed = false
FEATURE [Sketcher::SketchObject] Sketch655
  ArcFitTolerance = 1e-06
  AttachmentSupport = -> [AdditiveLoft004]
  ExternalGeometry = -> [AdditiveLoft004]
  FullyConstrained = true
  MakeInternals = false
  MapMode = 5
  Placement = pos=(0,3,0) rot=(1,0,0;1.5708rad)
  sketch-geometry (52):
    g0: LineSegment [constr] StartX=-6.5 StartY=-3.05 StartZ=0 EndX=-6.5 EndY=4.45 EndZ=0
    g1: LineSegment [constr] StartX=2e-16 StartY=4.45 StartZ=0 EndX=-6.5 EndY=4.45 EndZ=0
    g2: ArcOfCircle [constr] CenterX=1.28958 CenterY=-4.45713 CenterZ=0 NormalX=0 NormalY=0 NormalZ=1 AngleXU=0 Radius=9 StartAngle=1.71458 EndAngle=2.52217
    g3: LineSegment StartX=-6.5 StartY=-3.05 StartZ=0 EndX=-6.5 EndY=-1.73205 EndZ=0
    g4: ArcOfCircle CenterX=0.5 CenterY=-1.73205 CenterZ=0 NormalX=0 NormalY=0 NormalZ=1 AngleXU=0 Radius=7 StartAngle=2.77639 EndAngle=3.14159
    g5: LineSegment [constr] StartX=-2.7 StartY=-1.73205 StartZ=0 EndX=-6.5 EndY=-1.73205 EndZ=0
    g6: LineSegment StartX=-6.5 StartY=-3.05 StartZ=0 EndX=-2.7 EndY=-3.05 EndZ=0
    g7: LineSegment StartX=-2.7 StartY=-1.73205 StartZ=0 EndX=-2.7 EndY=-3.05 EndZ=0
    g8: LineSegment StartX=-2.7 StartY=-1.73205 StartZ=0 EndX=-1.7 EndY=0 EndZ=0
    g9: LineSegment StartX=-1.7 StartY=0 StartZ=0 EndX=0 EndY=0 EndZ=0
    g10: LineSegment StartX=-6.03835 StartY=0.767949 StartZ=0 EndX=-5.02039 EndY=1.23929 EndZ=0
    g11: LineSegment StartX=-5.02039 StartY=1.23929 StartZ=0 EndX=-5.06488 EndY=1.76417 EndZ=0
    g12: LineSegment StartX=-4.82364 StartY=2.08391 StartZ=0 EndX=-3.92183 EndY=2.26064 EndZ=0
    g13: LineSegment StartX=-3.92183 StartY=2.26064 StartZ=0 EndX=-3.83285 EndY=2.82808 EndZ=0
    g14: LineSegment StartX=-3.53351 StartY=3.08159 StartZ=0 EndX=-2.66084 EndY=3.07299 EndZ=0
    g15: LineSegment StartX=-2.66084 StartY=3.07299 StartZ=0 EndX=-2.45169 EndY=3.63046 EndZ=0
    g16: LineSegment StartX=-2.11157 StartY=3.81918 StartZ=0 EndX=-1.27669 EndY=3.65102 EndZ=0
    g17: LineSegment StartX=-1.27669 StartY=3.65102 StartZ=0 EndX=-0.961739 EndY=4.16724 EndZ=0
    g18: LineSegment StartX=-0.55564 StartY=4.2708 StartZ=0 EndX=0 EndY=3.95 EndZ=0
    g19: ArcOfCircle [constr] CenterX=1.294 CenterY=-4.45093 CenterZ=0 NormalX=0 NormalY=0 NormalZ=1 AngleXU=0 Radius=8.5 StartAngle=1.72363 EndAngle=2.52307
    g20: LineSegment [constr] StartX=-6.03835 StartY=0.767949 StartZ=0 EndX=-5.63124 EndY=0.477667 EndZ=0
    g21: ArcOfCircle CenterX=-4.76595 CenterY=1.78951 CenterZ=0 NormalX=0 NormalY=0 NormalZ=1 AngleXU=0 Radius=0.3 StartAngle=1.76431 EndAngle=3.22616
    g22: ArcOfCircle CenterX=-3.53647 CenterY=2.7816 CenterZ=0 NormalX=0 NormalY=0 NormalZ=1 AngleXU=0 Radius=0.3 StartAngle=1.56094 EndAngle=2.98605
    g23: ArcOfCircle CenterX=-2.1708 CenterY=3.52508 CenterZ=0 NormalX=0 NormalY=0 NormalZ=1 AngleXU=0 Radius=0.3 StartAngle=1.37204 EndAngle=2.78267
    g24: ArcOfCircle CenterX=-0.70564 CenterY=4.01099 CenterZ=0 NormalX=0 NormalY=0 NormalZ=1 AngleXU=0 Radius=0.3 StartAngle=1.0472 EndAngle=2.59377
    g25: LineSegment [constr] StartX=22.4 StartY=-3.05 StartZ=0 EndX=22.4 EndY=4.45 EndZ=0
    g26: LineSegment [constr] StartX=22.4 StartY=-1.73205 StartZ=0 EndX=18.6 EndY=-1.73205 EndZ=0
    g27: ArcOfCircle [constr] CenterX=14.606 CenterY=-4.45093 CenterZ=0 NormalX=0 NormalY=0 NormalZ=1 AngleXU=0 Radius=8.5 StartAngle=0.618575 EndAngle=1.41797
    g28: LineSegment [constr] StartX=21.531 StartY=0.478012 StartZ=0 EndX=21.9383 EndY=0.767949 EndZ=0
    g29: LineSegment StartX=0 StartY=3.95 StartZ=0 EndX=0 EndY=0 EndZ=0
    g30: ArcOfCircle [constr] CenterX=14.6104 CenterY=-4.45713 CenterZ=0 NormalX=0 NormalY=0 NormalZ=1 AngleXU=0 Radius=9 StartAngle=0.619422 EndAngle=1.42701
    g31: LineSegment [constr] StartX=22.4 StartY=4.45 StartZ=0 EndX=15.9 EndY=4.45 EndZ=0
    g32: LineSegment StartX=22.4 StartY=-3.05 StartZ=0 EndX=22.4 EndY=-1.73205 EndZ=0
    g33: LineSegment StartX=22.4 StartY=-3.05 StartZ=0 EndX=18.6 EndY=-3.05 EndZ=0
    g34: LineSegment StartX=18.6 StartY=-3.05 StartZ=0 EndX=18.6 EndY=-1.73205 EndZ=0
    g35: LineSegment StartX=18.6 StartY=-1.73205 StartZ=0 EndX=17.6 EndY=-5.8e-15 EndZ=0
    g36: LineSegment StartX=17.6 StartY=-5.8e-15 StartZ=0 EndX=15.9 EndY=-7e-16 EndZ=0
    g37: LineSegment StartX=15.9 StartY=-7e-16 StartZ=0 EndX=15.9 EndY=3.95 EndZ=0
    g38: ArcOfCircle CenterX=15.4 CenterY=-1.73205 CenterZ=0 NormalX=0 NormalY=0 NormalZ=1 AngleXU=0 Radius=7 StartAngle=6.28319 EndAngle=6.64839
    g39: LineSegment StartX=15.9 StartY=3.95 StartZ=0 EndX=16.4556 EndY=4.2708 EndZ=0
    g40: LineSegment StartX=16.8617 StartY=4.16724 StartZ=0 EndX=17.1767 EndY=3.65102 EndZ=0
    g41: LineSegment StartX=17.1767 StartY=3.65102 StartZ=0 EndX=18.0116 EndY=3.81918 EndZ=0
    g42: LineSegment StartX=18.3517 StartY=3.63046 StartZ=0 EndX=18.5608 EndY=3.07299 EndZ=0
    g43: LineSegment StartX=18.5608 StartY=3.07299 StartZ=0 EndX=19.4335 EndY=3.08159 EndZ=0
    g44: LineSegment StartX=19.7328 StartY=2.82808 StartZ=0 EndX=19.8218 EndY=2.26064 EndZ=0
    g45: LineSegment StartX=19.8218 StartY=2.26064 StartZ=0 EndX=20.7236 EndY=2.08391 EndZ=0
    g46: LineSegment StartX=20.9649 StartY=1.76417 StartZ=0 EndX=20.9204 EndY=1.23929 EndZ=0
    g47: LineSegment StartX=20.9204 StartY=1.23929 StartZ=0 EndX=21.9383 EndY=0.767949 EndZ=0
    g48: ArcOfCircle CenterX=16.6056 CenterY=4.01099 CenterZ=0 NormalX=0 NormalY=0 NormalZ=1 AngleXU=0 Radius=0.3 StartAngle=0.547818 EndAngle=2.0944
    g49: ArcOfCircle CenterX=18.0708 CenterY=3.52508 CenterZ=0 NormalX=0 NormalY=0 NormalZ=1 AngleXU=0 Radius=0.3 StartAngle=0.358923 EndAngle=1.76955
    g50: ArcOfCircle CenterX=19.4365 CenterY=2.7816 CenterZ=0 NormalX=0 NormalY=0 NormalZ=1 AngleXU=0 Radius=0.3 StartAngle=0.155548 EndAngle=1.58065
    g51: ArcOfCircle CenterX=20.666 CenterY=1.78951 CenterZ=0 NormalX=0 NormalY=0 NormalZ=1 AngleXU=0 Radius=0.3 StartAngle=6.19862 EndAngle=7.66046
  constraints (140):
    c: Vertical(g0)
    c: Coincident(g1,g0)
    c: Horizontal(g1)
    c: DistanceY(g0,g0) = 7.5
    c: Coincident(g0,g-3)
    c: Coincident(g2,g1)
    c: Coincident(g3,g0)
    c: PointOnObject(g3,g0)
    c: Coincident(g4,g3)
    c: Coincident(g4,g2)
    c: Coincident(g5,g-5)
    c: Coincident(g5,g3)
    c: Horizontal(g5)
    c: Radius(g4) = 7
    c: Coincident(g6,g0)
    c: PointOnObject(g7,g5)
    c: Coincident(g7,g-4)
    c: Vertical(g7)
    c: Coincident(g6,g7)
    c: Coincident(g8,g-6)
    c: Coincident(g8,g7)
    c: Coincident(g9,g8)
    c: Coincident(g9,g-1)
    c: Coincident(g11,g10)
    c: Coincident(g13,g12)
    c: Coincident(g15,g14)
    c: Coincident(g17,g16)
    c: DistanceY(g19,g1) = 0.5
    c: Radius(g19) = 8.5
    c: Coincident(g10,g2)
    c: Coincident(g20,g2)
    c: Coincident(g20,g19)
    c: Distance(g20) = 0.5
    c: Radius(g2) = 9
    c: Perpendicular(g2,g20)
    c: Tangent(g4,g0)
    c: DistanceY(g3,g2) = 2.5
    c: PointOnObject(g18,g19)
    c: PointOnObject(g16,g19)
    c: PointOnObject(g14,g19)
    c: PointOnObject(g12,g19)
    c: Tangent(g11,g21) = 1.5708
    c: Tangent(g12,g21) = 1.5708
    c: Tangent(g13,g22) = 1.5708
    c: Tangent(g14,g22) = 1.5708
    c: Tangent(g15,g23) = 1.5708
    c: Tangent(g16,g23) = 1.5708
    c: Tangent(g17,g24) = 1.5708
    c: Tangent(g18,g24) = 1.5708
    c: Radius(g21) = 0.3
    c: PointOnObject(g10,g19)
    c: Tangent(g21,g2)
    c: Radius(g22) = 0.3
    c: Radius(g23) = 0.3
    c: Radius(g24) = 0.3
    c: Tangent(g24,g2)
    c: Tangent(g23,g2)
    c: Tangent(g22,g2)
    c: Distance(g10,g12) = 1.5
    c: Distance(g12,g14) = 1.5
    c: Distance(g14,g16) = 1.5
    c: Angle(g17,g16) = 1.91986
    c: Angle(g15,g14) = 1.91986
    c: Angle(g13,g12) = 1.91986
    c: Angle(g11,g10) = 1.91986
    c: Vertical(g25)
    c: DistanceY(g25,g25) = 7.5
    c: PointOnObject(g26,g25)
    c: Coincident(g26,g-10)
    c: Horizontal(g26)
    c: Radius(g27) = 8.5
    c: DistanceY(g27,g30) = 0.5
    c: Coincident(g28,g27)
    c: Distance(g28) = 0.5
    c: Perpendicular(g27,g28)
    c: Coincident(g29,g18)
    c: Coincident(g29,g9)
    c: Vertical(g29)
    c: Coincident(g30,g28)
    c: Radius(g30) = 9
    c: Coincident(g25,g-12)
    c: Coincident(g31,g25)
    c: PointOnObject(g31,g-7)
    c: Horizontal(g31)
    c: Coincident(g30,g31)
    c: PointOnObject(g27,g-7)
    c: Coincident(g32,g25)
    c: Coincident(g32,g26)
    c: Coincident(g33,g25)
    c: Coincident(g33,g-10)
    c: Coincident(g34,g33)
    c: Coincident(g34,g26)
    c: Coincident(g35,g26)
    c: Coincident(g35,g-9)
    c: Coincident(g36,g35)
    c: Coincident(g36,g-7)
    c: Coincident(g37,g36)
    c: Coincident(g37,g27)
    c: Coincident(g38,g26)
    c: Coincident(g38,g28)
    c: Tangent(g38,g25)
    c: Radius(g38) = 7
    c: DistanceY(g26,g28) = 2.5
    c: PointOnObject(g1,g-2)
    c: PointOnObject(g19,g29)
    c: Angle(g18,g29) = 2.0944
    c: Coincident(g39,g27)
    c: PointOnObject(g40,g27)
    c: Coincident(g41,g40)
    c: PointOnObject(g42,g27)
    c: Coincident(g43,g42)
    c: PointOnObject(g44,g27)
    c: Coincident(g45,g44)
    c: PointOnObject(g46,g27)
    c: Coincident(g47,g46)
    c: Coincident(g47,g28)
    c: Tangent(g39,g48) = 1.5708
    c: Tangent(g40,g48) = 1.5708
    c: Tangent(g41,g49) = 1.5708
    c: Tangent(g42,g49) = 1.5708
    c: Tangent(g43,g50) = 1.5708
    c: Tangent(g44,g50) = 1.5708
    c: Tangent(g45,g51) = 1.5708
    c: Tangent(g46,g51) = 1.5708
    c: Radius(g48) = 0.3
    c: Radius(g49) = 0.3
    c: Radius(g50) = 0.3
    c: Radius(g51) = 0.3
    c: Tangent(g51,g30)
    c: Tangent(g50,g30)
    c: Tangent(g49,g30)
    c: Tangent(g48,g30)
    c: Angle(g37,g39) = 2.0944
    c: Distance(g40,g42) = 1.5
    c: Distance(g42,g44) = 1.5
    c: Distance(g44,g46) = 1.5
    c: Angle(g41,g40) = 1.91986
    c: Angle(g43,g42) = 1.91986
    c: Angle(g45,g44) = 1.91986
    c: Angle(g47,g46) = 1.91986
FEATURE [PartDesign::Pad] Pad464
  BaseFeature = -> AdditiveLoft004
  Direction = (0,-1,2e-16)
  Length = 1.9
  Length2 = 10
  Profile = -> Sketch655
  ReferenceAxis = -> Sketch655 [N_Axis]
  Refine = true
  Reversed = true
  Suppressed = false
  Type = 0
FEATURE [Sketcher::SketchObject] Sketch656
  ArcFitTolerance = 1e-06
  AttachmentOffset = pos=(0,0,-1.5) rot=(0,0,1;0rad)
  AttachmentSupport = -> [Pad464]
  ExternalGeometry = -> [Pad464]
  FullyConstrained = true
  MakeInternals = false
  MapMode = 5
  Placement = pos=(0,12.3,3e-16) rot=(0,0.707107,0.707107;3.14159rad)
  sketch-geometry (40):
    g0: LineSegment StartX=6.5 StartY=-3.05 StartZ=0 EndX=2.7 EndY=-3.05 EndZ=0
    g1: LineSegment StartX=2.7 StartY=-3.05 StartZ=0 EndX=2.7 EndY=-1.73205 EndZ=0
    g2: LineSegment StartX=2.7 StartY=-1.73205 StartZ=0 EndX=1.7 EndY=0 EndZ=0
    g3: LineSegment StartX=1.7 StartY=0 StartZ=0 EndX=0 EndY=0 EndZ=0
    g4: LineSegment StartX=0 StartY=0 StartZ=0 EndX=0 EndY=3.95 EndZ=0
    g5: LineSegment StartX=0 StartY=3.95 StartZ=0 EndX=0.55564 EndY=4.2708 EndZ=0
    g6: ArcOfCircle CenterX=0.70564 CenterY=4.01099 CenterZ=0 NormalX=0 NormalY=0 NormalZ=1 AngleXU=0 Radius=0.3 StartAngle=0.547818 EndAngle=2.0944
    g7: ArcOfCircle CenterX=2.1708 CenterY=3.52508 CenterZ=0 NormalX=0 NormalY=0 NormalZ=1 AngleXU=0 Radius=0.3 StartAngle=0.358923 EndAngle=1.76955
    g8: ArcOfCircle CenterX=3.53647 CenterY=2.7816 CenterZ=0 NormalX=0 NormalY=0 NormalZ=1 AngleXU=0 Radius=0.3 StartAngle=0.155548 EndAngle=1.58065
    g9: ArcOfCircle CenterX=4.76595 CenterY=1.78951 CenterZ=0 NormalX=0 NormalY=0 NormalZ=1 AngleXU=0 Radius=0.3 StartAngle=6.19862 EndAngle=7.66046
    g10: LineSegment StartX=0.961739 StartY=4.16724 StartZ=0 EndX=1.27669 EndY=3.65102 EndZ=0
    g11: LineSegment StartX=1.27669 StartY=3.65102 StartZ=0 EndX=2.11157 EndY=3.81918 EndZ=0
    g12: LineSegment StartX=2.45169 StartY=3.63046 StartZ=0 EndX=2.66084 EndY=3.07299 EndZ=0
    g13: LineSegment StartX=2.66084 StartY=3.07299 StartZ=0 EndX=3.53351 EndY=3.08159 EndZ=0
    g14: LineSegment StartX=3.83285 StartY=2.82808 StartZ=0 EndX=3.92183 EndY=2.26064 EndZ=0
    g15: LineSegment StartX=3.92183 StartY=2.26064 StartZ=0 EndX=4.82364 EndY=2.08391 EndZ=0
    g16: LineSegment StartX=5.06488 StartY=1.76417 StartZ=0 EndX=5.02039 EndY=1.23929 EndZ=0
    g17: LineSegment StartX=5.02039 StartY=1.23929 StartZ=0 EndX=6.03835 EndY=0.767949 EndZ=0
    g18: LineSegment StartX=6.5 StartY=-3.05 StartZ=0 EndX=6.5 EndY=-1.73205 EndZ=0
    g19: ArcOfCircle CenterX=-0.499998 CenterY=-1.73205 CenterZ=0 NormalX=0 NormalY=0 NormalZ=1 AngleXU=0 Radius=7 StartAngle=6.28319 EndAngle=6.64839
    g20: ArcOfCircle CenterX=-20.666 CenterY=1.78951 CenterZ=0 NormalX=0 NormalY=0 NormalZ=1 AngleXU=0 Radius=0.3 StartAngle=1.76431 EndAngle=3.22616
    g21: ArcOfCircle CenterX=-19.4365 CenterY=2.7816 CenterZ=0 NormalX=0 NormalY=0 NormalZ=1 AngleXU=0 Radius=0.3 StartAngle=1.56094 EndAngle=2.98604
    g22: ArcOfCircle CenterX=-18.0708 CenterY=3.52508 CenterZ=0 NormalX=0 NormalY=0 NormalZ=1 AngleXU=0 Radius=0.3 StartAngle=1.37204 EndAngle=2.78267
    g23: ArcOfCircle CenterX=-16.6056 CenterY=4.01099 CenterZ=0 NormalX=0 NormalY=0 NormalZ=1 AngleXU=0 Radius=0.3 StartAngle=1.0472 EndAngle=2.59377
    g24: LineSegment StartX=-15.9 StartY=3.95 StartZ=0 EndX=-15.9 EndY=0 EndZ=0
    g25: LineSegment StartX=-15.9 StartY=0 StartZ=0 EndX=-17.6 EndY=0 EndZ=0
    g26: LineSegment StartX=-17.6 StartY=0 StartZ=0 EndX=-18.6 EndY=-1.73205 EndZ=0
    g27: LineSegment StartX=-18.6 StartY=-1.73205 StartZ=0 EndX=-18.6 EndY=-3.05 EndZ=0
    g28: LineSegment StartX=-18.6 StartY=-3.05 StartZ=0 EndX=-22.4 EndY=-3.05 EndZ=0
    g29: LineSegment StartX=-22.4 StartY=-3.05 StartZ=0 EndX=-22.4 EndY=-1.73205 EndZ=0
    g30: ArcOfCircle CenterX=-15.4 CenterY=-1.73205 CenterZ=0 NormalX=0 NormalY=0 NormalZ=1 AngleXU=0 Radius=7 StartAngle=2.77639 EndAngle=3.14159
    g31: LineSegment StartX=-21.9383 StartY=0.767949 StartZ=0 EndX=-20.9204 EndY=1.23929 EndZ=0
    g32: LineSegment StartX=-20.9204 StartY=1.23929 StartZ=0 EndX=-20.9649 EndY=1.76417 EndZ=0
    g33: LineSegment StartX=-20.7236 StartY=2.08391 StartZ=0 EndX=-19.8218 EndY=2.26064 EndZ=0
    g34: LineSegment StartX=-19.8218 StartY=2.26064 StartZ=0 EndX=-19.7328 EndY=2.82808 EndZ=0
    g35: LineSegment StartX=-15.9 StartY=3.95 StartZ=0 EndX=-16.4556 EndY=4.2708 EndZ=0
    g36: LineSegment StartX=-16.8617 StartY=4.16724 StartZ=0 EndX=-17.1767 EndY=3.65102 EndZ=0
    g37: LineSegment StartX=-17.1767 StartY=3.65102 StartZ=0 EndX=-18.0116 EndY=3.81918 EndZ=0
    g38: LineSegment StartX=-18.3517 StartY=3.63046 StartZ=0 EndX=-18.5608 EndY=3.07299 EndZ=0
    g39: LineSegment StartX=-18.5608 StartY=3.07299 StartZ=0 EndX=-19.4335 EndY=3.08159 EndZ=0
  constraints (81):
    c: Coincident(g0,g-25)
    c: Coincident(g0,g-26)
    c: Coincident(g1,g0)
    c: Coincident(g1,g-27)
    c: Coincident(g2,g1)
    c: Coincident(g2,g-28)
    c: Coincident(g3,g2)
    c: Coincident(g3,g-1)
    c: Coincident(g4,g3)
    c: Coincident(g4,g-42)
    c: Coincident(g5,g4)
    c: Coincident(g5,g-42)
    c: Coincident(g6,g5)
    c: Tangent(g6,g-40) = -1.5708
    c: Coincident(g7,g-38)
    c: Tangent(g7,g-37) = -1.5708
    c: Coincident(g8,g-35)
    c: Tangent(g8,g-34) = -1.5708
    c: Coincident(g9,g-32)
    c: Tangent(g9,g-31) = -1.5708
    c: Coincident(g10,g6)
    c: Coincident(g10,g-39)
    c: Coincident(g11,g10)
    c: Coincident(g11,g7)
    c: Coincident(g12,g-37)
    c: Coincident(g12,g-36)
    c: Coincident(g13,g12)
    c: Coincident(g13,g-35)
    c: Coincident(g14,g-34)
    c: Coincident(g14,g-33)
    c: Coincident(g15,g14)
    c: Coincident(g15,g9)
    c: Coincident(g16,g9)
    c: Coincident(g16,g-30)
    c: Coincident(g17,g16)
    c: Coincident(g17,g-29)
    c: Coincident(g18,g0)
    c: Coincident(g18,g-24)
    c: Coincident(g19,g17)
    c: Coincident(g19,g-24)
    c: Tangent(g19,g-23)
    c: Coincident(g20,g-15)
    c: Tangent(g20,g-14) = -1.5708
    c: Coincident(g21,g-12)
    c: Tangent(g21,g-11) = -1.5708
    c: Coincident(g22,g-9)
    c: Tangent(g22,g-8) = -1.5708
    c: Coincident(g23,g-6)
    c: Tangent(g23,g-5) = -1.5708
    c: Coincident(g24,g-4)
    c: Coincident(g24,g-3)
    c: Coincident(g25,g24)
    c: Coincident(g25,g-22)
    c: Coincident(g26,g25)
    c: Coincident(g26,g-21)
    c: Coincident(g27,g-21)
    c: Coincident(g27,g-20)
    c: Coincident(g28,g27)
    c: Coincident(g28,g-19)
    c: Coincident(g29,g28)
    c: Coincident(g29,g-18)
    c: Coincident(g30,g29)
    c: Tangent(g30,g-17) = -1.5708
    c: Coincident(g31,g30)
    c: Coincident(g31,g-16)
    c: Coincident(g32,g31)
    c: Coincident(g32,g20)
    c: Coincident(g33,g20)
    c: Coincident(g33,g-13)
    c: Coincident(g34,g33)
    c: Coincident(g34,g21)
    c: Coincident(g35,g24)
    c: Coincident(g35,g23)
    c: Coincident(g36,g23)
    c: Coincident(g36,g-7)
    c: Coincident(g37,g-7)
    c: Coincident(g37,g22)
    c: Coincident(g38,g22)
    c: Coincident(g38,g-10)
    c: Coincident(g39,g38)
    c: Coincident(g39,g21)
FEATURE [PartDesign::Pad] Pad465
  BaseFeature = -> Pad464
  Direction = (0,1,-2e-16)
  Length = 1.9
  Length2 = 10
  Profile = -> Sketch656
  ReferenceAxis = -> Sketch656 [N_Axis]
  Refine = true
  Reversed = true
  Suppressed = false
  Type = 0
FEATURE [Sketcher::SketchObject] Sketch657
  ArcFitTolerance = 1e-06
  AttachmentSupport = -> [Pad465]
  ExternalGeometry = -> [Pad465]
  FullyConstrained = true
  MakeInternals = false
  MapMode = 5
  Placement = pos=(0,0,0) rot=(1,0,0;1.5708rad)
  sketch-geometry (8):
    g0: LineSegment StartX=5.85 StartY=3.5 StartZ=0 EndX=5.85 EndY=0 EndZ=0
    g1: LineSegment StartX=5.85 StartY=0 StartZ=0 EndX=0 EndY=0 EndZ=0
    g2: LineSegment StartX=0 StartY=0 StartZ=0 EndX=0 EndY=3.5 EndZ=0
    g3: LineSegment StartX=5.85 StartY=3.5 StartZ=0 EndX=0 EndY=3.5 EndZ=0
    g4: LineSegment StartX=15.9 StartY=0 StartZ=0 EndX=15.9 EndY=3.5 EndZ=0
    g5: LineSegment StartX=15.9 StartY=3.5 StartZ=0 EndX=10.05 EndY=3.5 EndZ=0
    g6: LineSegment StartX=10.05 StartY=3.5 StartZ=0 EndX=10.05 EndY=0 EndZ=0
    g7: LineSegment StartX=10.05 StartY=0 StartZ=0 EndX=15.9 EndY=0 EndZ=0
  constraints (21):
    c: PointOnObject(g0,g-3)
    c: Coincident(g0,g-4)
    c: Coincident(g1,g0)
    c: Coincident(g1,g-1)
    c: Coincident(g2,g1)
    c: PointOnObject(g2,g-5)
    c: Coincident(g3,g0)
    c: Coincident(g3,g2)
    c: DistanceY(g2,g2) = 3.5
    c: Horizontal(g3)
    c: Coincident(g4,g5)
    c: Coincident(g5,g6)
    c: Coincident(g6,g7)
    c: Coincident(g7,g4)
    c: Vertical(g4)
    c: Vertical(g6)
    c: Horizontal(g5)
    c: Horizontal(g7)
    c: Coincident(g4,g-6)
    c: PointOnObject(g5,g-8)
    c: DistanceY(g4,g4) = 3.5
FEATURE [PartDesign::Pad] Pad466
  BaseFeature = -> Pad465
  Direction = (0,-1,2e-16)
  Length = 3.9
  Length2 = 10
  Profile = -> Sketch657
  ReferenceAxis = -> Sketch657 [N_Axis]
  Refine = true
  Suppressed = false
  Type = 0
FEATURE [Sketcher::SketchObject] Sketch658
  ArcFitTolerance = 1e-06
  AttachmentSupport = -> [Pad466]
  ExternalGeometry = -> [Pad466]
  FullyConstrained = true
  MakeInternals = false
  MapMode = 5
  Placement = pos=(0,0,0) rot=(0.57735,-0.57735,-0.57735;2.0944rad)
  sketch-geometry (4):
    g0: LineSegment StartX=-8e-16 StartY=3.5 StartZ=0 EndX=-8e-16 EndY=0 EndZ=0
    g1: LineSegment StartX=-8e-16 StartY=0 StartZ=0 EndX=0.8 EndY=0 EndZ=0
    g2: LineSegment StartX=0.8 StartY=0 StartZ=0 EndX=0.8 EndY=3.5 EndZ=0
    g3: LineSegment StartX=0.8 StartY=3.5 StartZ=0 EndX=-8e-16 EndY=3.5 EndZ=0
  constraints (11):
    c: Coincident(g0,g1)
    c: Coincident(g1,g2)
    c: Coincident(g2,g3)
    c: Coincident(g3,g0)
    c: Vertical(g0)
    c: Vertical(g2)
    c: Horizontal(g1)
    c: Horizontal(g3)
    c: Coincident(g0,g-3)
    c: PointOnObject(g1,g-1)
    c: DistanceX(g3,g3) = 0.8
FEATURE [PartDesign::Pocket] Pocket289
  BaseFeature = -> Pad466
  Direction = (1,0,0)
  Length = 1
  Length2 = 5
  Profile = -> Sketch658
  ReferenceAxis = -> Sketch658 [N_Axis]
  Refine = true
  Suppressed = false
  Type = 0
FEATURE [Sketcher::SketchObject] Sketch659
  ArcFitTolerance = 1e-06
  AttachmentSupport = -> [Pocket289]
  ExternalGeometry = -> [Pocket289]
  FullyConstrained = true
  MakeInternals = false
  MapMode = 5
  Placement = pos=(15.9,0,0) rot=(0.57735,0.57735,0.57735;2.0944rad)
  sketch-geometry (4):
    g0: LineSegment StartX=8e-16 StartY=3.5 StartZ=0 EndX=-0.8 EndY=3.5 EndZ=0
    g1: LineSegment StartX=-0.8 StartY=3.5 StartZ=0 EndX=-0.8 EndY=-4.4e-15 EndZ=0
    g2: LineSegment StartX=-0.8 StartY=-4.4e-15 StartZ=0 EndX=8e-16 EndY=-4.4e-15 EndZ=0
    g3: LineSegment StartX=8e-16 StartY=-4.4e-15 StartZ=0 EndX=8e-16 EndY=3.5 EndZ=0
  constraints (11):
    c: Coincident(g0,g1)
    c: Coincident(g1,g2)
    c: Coincident(g2,g3)
    c: Coincident(g3,g0)
    c: Horizontal(g0)
    c: Horizontal(g2)
    c: Vertical(g1)
    c: Vertical(g3)
    c: Coincident(g0,g-3)
    c: PointOnObject(g1,g-4)
    c: DistanceX(g0,g0) = 0.8
FEATURE [PartDesign::Pocket] Pocket290
  BaseFeature = -> Pocket289
  Direction = (-1,0,0)
  Length = 1
  Length2 = 5
  Profile = -> Sketch659
  ReferenceAxis = -> Sketch659 [N_Axis]
  Refine = true
  Suppressed = false
  Type = 0
FEATURE [PartDesign::Chamfer] Chamfer021
  Angle = 30
  Base = -> Pocket290 [Edge377,Edge379,Edge281,Edge184]
  BaseFeature = -> Pocket290
  ChamferType = 2
  FlipDirection = false
  Refine = true
  Size = 0.9
  Size2 = 1
  SupportTransform = false
  Suppressed = false
  UseAllEdges = false
FEATURE [Sketcher::SketchObject] Sketch660
  ArcFitTolerance = 1e-06
  AttachmentSupport = -> [Chamfer021]
  ExternalGeometry = -> [Chamfer021]
  FullyConstrained = true
  MakeInternals = false
  MapMode = 5
  Placement = pos=(0,-3.9,0) rot=(1,0,0;1.5708rad)
  sketch-geometry (2):
    g0: Circle CenterX=2.75 CenterY=-0.75 CenterZ=0 NormalX=0 NormalY=0 NormalZ=1 AngleXU=0 Radius=2.75
    g1: Circle CenterX=13.15 CenterY=-0.75 CenterZ=0 NormalX=0 NormalY=0 NormalZ=1 AngleXU=0 Radius=2.75
  constraints (6):
    c: Diameter(g1) = 5.5
    c: Diameter(g0) = 5.5
    c: Tangent(g0,g-2)
    c: Tangent(g1,g-3)
    c: DistanceY(g0,g-1) = 0.75
    c: DistanceY(g1,g-3) = 0.75
FEATURE [Sketcher::SketchObject] Sketch661
  ArcFitTolerance = 1e-06
  AttachmentOffset = pos=(0,0,5.2) rot=(0,0,1;0rad)
  AttachmentSupport = -> [Chamfer021]
  ExternalGeometry = -> [Sketch660]
  FullyConstrained = true
  MakeInternals = false
  MapMode = 5
  Placement = pos=(0,-9.1,1.2e-15) rot=(1,0,0;1.5708rad)
  sketch-geometry (2):
    g0: Circle CenterX=2.75 CenterY=-0.75 CenterZ=0 NormalX=0 NormalY=0 NormalZ=1 AngleXU=0 Radius=1.9
    g1: Circle CenterX=13.15 CenterY=-0.75 CenterZ=0 NormalX=0 NormalY=0 NormalZ=1 AngleXU=0 Radius=1.9
  constraints (4):
    c: Coincident(g0,g-3)
    c: Coincident(g1,g-4)
    c: Diameter(g0) = 3.8
    c: Diameter(g1) = 3.8
FEATURE [PartDesign::AdditiveLoft] AdditiveLoft005
  BaseFeature = -> Chamfer021
  Closed = false
  Profile = -> Sketch660
  Refine = true
  Ruled = false
  Sections = -> [Sketch661]
  Suppressed = false
FEATURE [Sketcher::SketchObject] Sketch662
  ArcFitTolerance = 1e-06
  AttachmentSupport = -> [AdditiveLoft005]
  ExternalGeometry = -> [AdditiveLoft005]
  FullyConstrained = true
  MakeInternals = false
  MapMode = 5
  Placement = pos=(0,-3.9,0) rot=(1,0,0;1.5708rad)
  sketch-geometry (4):
    g0: LineSegment StartX=2.75 StartY=0 StartZ=0 EndX=2.75 EndY=-1.5 EndZ=0
    g1: LineSegment StartX=2.75 StartY=-1.5 StartZ=0 EndX=13.15 EndY=-1.5 EndZ=0
    g2: LineSegment StartX=13.15 StartY=-1.5 StartZ=0 EndX=13.15 EndY=0 EndZ=0
    g3: LineSegment StartX=13.15 StartY=0 StartZ=0 EndX=2.75 EndY=0 EndZ=0
  constraints (12):
    c: Coincident(g0,g1)
    c: Coincident(g1,g2)
    c: Coincident(g2,g3)
    c: Coincident(g3,g0)
    c: Vertical(g0)
    c: Vertical(g2)
    c: Horizontal(g1)
    c: Horizontal(g3)
    c: PointOnObject(g0,g-1)
    c: DistanceY(g0,g0) = 1.5
    c: PointOnObject(g-4,g0)
    c: PointOnObject(g-5,g2)
FEATURE [PartDesign::Pad] Pad467
  BaseFeature = -> AdditiveLoft005
  Direction = (0,-1,2e-16)
  Length = 5.2
  Length2 = 10
  Profile = -> Sketch662
  ReferenceAxis = -> Sketch662 [N_Axis]
  Refine = true
  Suppressed = false
  Type = 0
FEATURE [Sketcher::SketchObject] Sketch663
  ArcFitTolerance = 1e-06
  AttachmentSupport = -> [Pad467]
  ExternalGeometry = -> [Pad467]
  FullyConstrained = true
  MakeInternals = false
  MapMode = 5
  Placement = pos=(0,0,-5.8) rot=(1,0,0;3.14159rad)
  sketch-geometry (4):
    g0: LineSegment StartX=-0.75 StartY=9.1 StartZ=0 EndX=-0.75 EndY=3.9 EndZ=0
    g1: LineSegment StartX=-0.75 StartY=3.9 StartZ=0 EndX=16.65 EndY=3.9 EndZ=0
    g2: LineSegment StartX=16.65 StartY=3.9 StartZ=0 EndX=16.65 EndY=9.1 EndZ=0
    g3: LineSegment StartX=16.65 StartY=9.1 StartZ=0 EndX=-0.75 EndY=9.1 EndZ=0
  constraints (11):
    c: Coincident(g0,g1)
    c: Coincident(g1,g2)
    c: Coincident(g2,g3)
    c: Coincident(g3,g0)
    c: Vertical(g0)
    c: Vertical(g2)
    c: Horizontal(g1)
    c: Horizontal(g3)
    c: PointOnObject(g0,g-5)
    c: Coincident(g1,g-6)
    c: PointOnObject(g-7,g3)
FEATURE [PartDesign::Pocket] Pocket291
  BaseFeature = -> Pad467
  Direction = (0,0,1)
  Length = 4.3
  Length2 = 5
  Profile = -> Sketch663
  ReferenceAxis = -> Sketch663 [N_Axis]
  Refine = true
  Suppressed = false
  Type = 0
FEATURE [Sketcher::SketchObject] Sketch664
  ArcFitTolerance = 1e-06
  AttachmentSupport = -> [Pocket291]
  ExternalGeometry = -> [Pocket291]
  FullyConstrained = true
  MakeInternals = false
  MapMode = 5
  Placement = pos=(0,-4e-16,-1.5) rot=(1,0,0;3.14159rad)
  sketch-geometry (8):
    g0: LineSegment StartX=4.30429 StartY=9.1 StartZ=0 EndX=2.30429 EndY=9.1 EndZ=0
    g1: LineSegment StartX=2.30429 StartY=9.1 StartZ=0 EndX=2.30429 EndY=3.9 EndZ=0
    g2: LineSegment StartX=2.30429 StartY=3.9 StartZ=0 EndX=4.30429 EndY=3.9 EndZ=0
    g3: LineSegment StartX=4.30429 StartY=3.9 StartZ=0 EndX=4.30429 EndY=9.1 EndZ=0
    g4: LineSegment StartX=11.5957 StartY=9.1 StartZ=0 EndX=11.5957 EndY=3.9 EndZ=0
    g5: LineSegment StartX=11.5957 StartY=3.9 StartZ=0 EndX=13.5957 EndY=3.9 EndZ=0
    g6: LineSegment StartX=13.5957 StartY=3.9 StartZ=0 EndX=13.5957 EndY=9.1 EndZ=0
    g7: LineSegment StartX=13.5957 StartY=9.1 StartZ=0 EndX=11.5957 EndY=9.1 EndZ=0
  constraints (24):
    c: Coincident(g0,g1)
    c: Coincident(g1,g2)
    c: Coincident(g2,g3)
    c: Coincident(g3,g0)
    c: Horizontal(g0)
    c: Horizontal(g2)
    c: Vertical(g1)
    c: Vertical(g3)
    c: PointOnObject(g0,g-3)
    c: PointOnObject(g1,g-4)
    c: Coincident(g4,g5)
    c: Coincident(g5,g6)
    c: Coincident(g6,g7)
    c: Coincident(g7,g4)
    c: Vertical(g4)
    c: Vertical(g6)
    c: Horizontal(g5)
    c: Horizontal(g7)
    c: PointOnObject(g4,g-3)
    c: PointOnObject(g5,g-4)
    c: DistanceX(g0,g0) = 2
    c: DistanceX(g7,g7) = 2
    c: DistanceX(g6,g-3) = 1.3
    c: DistanceX(g-3,g0) = 1.3
FEATURE [PartDesign::Pad] Pad468
  BaseFeature = -> Pocket291
  Direction = (0,0,-1)
  Length = 1
  Length2 = 10
  Profile = -> Sketch664
  ReferenceAxis = -> Sketch664 [N_Axis]
  Refine = true
  Suppressed = false
  Type = 0
FEATURE [Sketcher::SketchObject] Sketch665
  ArcFitTolerance = 1e-06
  AttachmentSupport = -> [Pad468]
  ExternalGeometry = -> [Pad468]
  FullyConstrained = true
  MakeInternals = false
  MapMode = 5
  Placement = pos=(0,-9.1,-7.8e-15) rot=(1,0,0;1.5708rad)
  sketch-geometry (8):
    g0: LineSegment StartX=4.30429 StartY=-2.5 StartZ=0 EndX=4.30429 EndY=-0.4 EndZ=0
    g1: LineSegment StartX=4.30429 StartY=-0.4 StartZ=0 EndX=2.30429 EndY=-0.4 EndZ=0
    g2: LineSegment StartX=2.30429 StartY=-0.4 StartZ=0 EndX=2.30429 EndY=-2.5 EndZ=0
    g3: LineSegment StartX=2.30429 StartY=-2.5 StartZ=0 EndX=4.30429 EndY=-2.5 EndZ=0
    g4: LineSegment StartX=13.5957 StartY=-2.5 StartZ=0 EndX=13.5957 EndY=-0.4 EndZ=0
    g5: LineSegment StartX=13.5957 StartY=-0.4 StartZ=0 EndX=11.5957 EndY=-0.4 EndZ=0
    g6: LineSegment StartX=11.5957 StartY=-0.4 StartZ=0 EndX=11.5957 EndY=-2.5 EndZ=0
    g7: LineSegment StartX=11.5957 StartY=-2.5 StartZ=0 EndX=13.5957 EndY=-2.5 EndZ=0
  constraints (22):
    c: Coincident(g0,g1)
    c: Coincident(g1,g2)
    c: Coincident(g2,g3)
    c: Coincident(g3,g0)
    c: Vertical(g0)
    c: Vertical(g2)
    c: Horizontal(g1)
    c: Horizontal(g3)
    c: Coincident(g0,g-4)
    c: Coincident(g4,g5)
    c: Coincident(g5,g6)
    c: Coincident(g6,g7)
    c: Coincident(g7,g4)
    c: Vertical(g4)
    c: Vertical(g6)
    c: Horizontal(g5)
    c: Horizontal(g7)
    c: Coincident(g4,g-8)
    c: PointOnObject(g2,g-5)
    c: PointOnObject(g6,g-6)
    c: DistanceY(g2,g2) = 2.1
    c: DistanceY(g6,g6) = 2.1
FEATURE [PartDesign::Pad] Pad469
  BaseFeature = -> Pad468
  Direction = (0,-1,2e-16)
  Length = 0.5
  Length2 = 10
  Profile = -> Sketch665
  ReferenceAxis = -> Sketch665 [N_Axis]
  Refine = true
  Suppressed = false
  Type = 0
FEATURE [Sketcher::SketchObject] Sketch666
  ArcFitTolerance = 1e-06
  AttachmentSupport = -> [Pad469]
  ExternalGeometry = -> [Pad469]
  FullyConstrained = true
  MakeInternals = false
  MapMode = 5
  Placement = pos=(0,-9.6,0) rot=(1,0,0;1.5708rad)
  sketch-geometry (2):
    g0: Circle CenterX=2.75 CenterY=-0.75 CenterZ=0 NormalX=0 NormalY=0 NormalZ=1 AngleXU=0 Radius=1.9
    g1: Circle CenterX=13.15 CenterY=-0.75 CenterZ=0 NormalX=0 NormalY=0 NormalZ=1 AngleXU=0 Radius=1.9
  constraints (4):
    c: Coincident(g0,g-3)
    c: Equal(g0,g-3)
    c: Coincident(g1,g-4)
    c: Equal(g1,g-4)
FEATURE [Sketcher::SketchObject] Sketch667
  ArcFitTolerance = 1e-06
  AttachmentOffset = pos=(0,0,4.5) rot=(0,0,1;0rad)
  AttachmentSupport = -> [Pad469]
  ExternalGeometry = -> [Pad469]
  FullyConstrained = true
  MakeInternals = false
  MapMode = 5
  Placement = pos=(0,-14.1,1e-15) rot=(1,0,0;1.5708rad)
  sketch-geometry (2):
    g0: Circle CenterX=2.75 CenterY=-0.75 CenterZ=0 NormalX=0 NormalY=0 NormalZ=1 AngleXU=0 Radius=1.5
    g1: Circle CenterX=13.15 CenterY=-0.75 CenterZ=0 NormalX=0 NormalY=0 NormalZ=1 AngleXU=0 Radius=1.5
  constraints (4):
    c: Coincident(g0,g-3)
    c: Coincident(g1,g-4)
    c: Diameter(g0) = 3
    c: Diameter(g1) = 3
FEATURE [PartDesign::AdditiveLoft] AdditiveLoft006
  BaseFeature = -> Pad469
  Closed = false
  Profile = -> Sketch666
  Refine = true
  Ruled = false
  Sections = -> [Sketch667]
  Suppressed = false
FEATURE [Sketcher::SketchObject] Sketch668
  ArcFitTolerance = 1e-06
  AttachmentSupport = -> [AdditiveLoft006]
  ExternalGeometry = -> [AdditiveLoft006]
  FullyConstrained = true
  MakeInternals = false
  MapMode = 5
  Placement = pos=(0,0,7) rot=(0,0,1;0rad)
  sketch-geometry (8):
    g0: LineSegment StartX=1.9 StartY=0 StartZ=0 EndX=1.9 EndY=-9.1 EndZ=0
    g1: LineSegment StartX=1.9 StartY=-9.1 StartZ=0 EndX=3.4 EndY=-9.1 EndZ=0
    g2: LineSegment StartX=3.4 StartY=-9.1 StartZ=0 EndX=3.4 EndY=0 EndZ=0
    g3: LineSegment StartX=3.4 StartY=0 StartZ=0 EndX=1.9 EndY=0 EndZ=0
    g4: LineSegment StartX=14 StartY=-9.1 StartZ=0 EndX=14 EndY=0 EndZ=0
    g5: LineSegment StartX=14 StartY=0 StartZ=0 EndX=12.5 EndY=0 EndZ=0
    g6: LineSegment StartX=12.5 StartY=0 StartZ=0 EndX=12.5 EndY=-9.1 EndZ=0
    g7: LineSegment StartX=12.5 StartY=-9.1 StartZ=0 EndX=14 EndY=-9.1 EndZ=0
  constraints (22):
    c: Coincident(g0,g1)
    c: Coincident(g1,g2)
    c: Coincident(g2,g3)
    c: Coincident(g3,g0)
    c: Vertical(g0)
    c: Vertical(g2)
    c: Horizontal(g1)
    c: Horizontal(g3)
    c: PointOnObject(g0,g-5)
    c: DistanceX(g1,g1) = 1.5
    c: Coincident(g0,g-7)
    c: Coincident(g4,g5)
    c: Coincident(g5,g6)
    c: Coincident(g6,g7)
    c: Coincident(g7,g4)
    c: Vertical(g4)
    c: Vertical(g6)
    c: Horizontal(g5)
    c: Horizontal(g7)
    c: PointOnObject(g4,g-6)
    c: Coincident(g4,g-8)
    c: DistanceX(g7,g7) = 1.5
FEATURE [PartDesign::Pad] Pad470
  BaseFeature = -> AdditiveLoft006
  Direction = (0,0,1)
  Length = 8
  Length2 = 10
  Profile = -> Sketch668
  ReferenceAxis = -> Sketch668 [N_Axis]
  Refine = true
  Reversed = true
  Suppressed = false
  Type = 0
FEATURE [Sketcher::SketchObject] Sketch669
  ArcFitTolerance = 1e-06
  AttachmentSupport = -> [Pad470]
  ExternalGeometry = -> [Pad470]
  FullyConstrained = true
  MakeInternals = false
  MapMode = 5
  Placement = pos=(1.9,0,0) rot=(0.57735,-0.57735,-0.57735;2.0944rad)
  sketch-geometry (4):
    g0: LineSegment StartX=0 StartY=7 StartZ=0 EndX=9.1 EndY=7 EndZ=0
    g1: LineSegment StartX=9.1 StartY=7 StartZ=0 EndX=9.1 EndY=2.94926 EndZ=0
    g2: LineSegment StartX=9.1 StartY=2.94926 StartZ=0 EndX=0 EndY=4.3 EndZ=0
    g3: LineSegment StartX=0 StartY=4.3 StartZ=0 EndX=0 EndY=7 EndZ=0
  constraints (11):
    c: Coincident(g0,g-5)
    c: Coincident(g0,g-4)
    c: Coincident(g1,g0)
    c: PointOnObject(g1,g-3)
    c: Coincident(g2,g1)
    c: PointOnObject(g2,g-6)
    c: Coincident(g3,g2)
    c: Coincident(g3,g0)
    c: DistanceY(g-3,g-3) = 6.05074
    c: DistanceY(g-7,g1) = 2
    c: DistanceY(g3,g3) = 2.7
FEATURE [PartDesign::Pocket] Pocket292
  BaseFeature = -> Pad470
  Direction = (1,0,0)
  Length = 2
  Length2 = 5
  Profile = -> Sketch669
  ReferenceAxis = -> Sketch669 [N_Axis]
  Refine = true
  Suppressed = false
  Type = 0
FEATURE [Sketcher::SketchObject] Sketch670
  ArcFitTolerance = 1e-06
  AttachmentSupport = -> [Pocket292]
  ExternalGeometry = -> [Pocket292]
  FullyConstrained = true
  MakeInternals = false
  MapMode = 5
  Placement = pos=(14,0,0) rot=(0.57735,0.57735,0.57735;2.0944rad)
  sketch-geometry (4):
    g0: LineSegment StartX=0 StartY=7 StartZ=0 EndX=0 EndY=4.3 EndZ=0
    g1: LineSegment StartX=0 StartY=4.3 StartZ=0 EndX=-9.1 EndY=2.94926 EndZ=0
    g2: LineSegment StartX=-9.1 StartY=2.94926 StartZ=0 EndX=-9.1 EndY=7 EndZ=0
    g3: LineSegment StartX=-9.1 StartY=7 StartZ=0 EndX=0 EndY=7 EndZ=0
  constraints (9):
    c: PointOnObject(g0,g-3)
    c: Coincident(g0,g-7)
    c: Vertical(g0)
    c: Coincident(g1,g0)
    c: Coincident(g1,g-7)
    c: Coincident(g2,g1)
    c: Coincident(g2,g-4)
    c: Coincident(g3,g2)
    c: Coincident(g3,g0)
FEATURE [PartDesign::Pocket] Pocket293
  BaseFeature = -> Pocket292
  Direction = (-1,0,0)
  Length = 2
  Length2 = 5
  Profile = -> Sketch670
  ReferenceAxis = -> Sketch670 [N_Axis]
  Refine = true
  Suppressed = false
  Type = 0
FEATURE [Sketcher::SketchObject] Sketch671
  ArcFitTolerance = 1e-06
  AttachmentSupport = -> [Pocket293]
  ExternalGeometry = -> [Pocket293]
  FullyConstrained = true
  MakeInternals = false
  MapMode = 5
  Placement = pos=(0,-4e-16,-1.5) rot=(1,0,0;3.14159rad)
  sketch-geometry (4):
    g0: LineSegment StartX=5.04979 StartY=9.1 StartZ=0 EndX=5.04979 EndY=7.1 EndZ=0
    g1: LineSegment StartX=5.04979 StartY=7.1 StartZ=0 EndX=10.8498 EndY=7.1 EndZ=0
    g2: LineSegment StartX=10.8498 StartY=7.1 StartZ=0 EndX=10.8498 EndY=9.1 EndZ=0
    g3: LineSegment StartX=10.8498 StartY=9.1 StartZ=0 EndX=5.04979 EndY=9.1 EndZ=0
  constraints (13):
    c: Coincident(g0,g1)
    c: Coincident(g1,g2)
    c: Coincident(g2,g3)
    c: Coincident(g3,g0)
    c: Vertical(g0)
    c: Vertical(g2)
    c: Horizontal(g1)
    c: Horizontal(g3)
    c: PointOnObject(g0,g-3)
    c: DistanceY(g0,g0) = 2
    c: DistanceX(g3,g3) = 5.8
    c: DistanceX(g-3,g-3) = 7.29142
    c: DistanceX(g-3,g0) = 0.7455
FEATURE [PartDesign::Pad] Pad471
  BaseFeature = -> Pocket293
  Direction = (0,0,-1)
  Length = 8
  Length2 = 10
  Profile = -> Sketch671
  ReferenceAxis = -> Sketch671 [N_Axis]
  Refine = true
  Suppressed = false
  Type = 0
FEATURE [Sketcher::SketchObject] Sketch672
  ArcFitTolerance = 1e-06
  AttachmentSupport = -> [Pad471]
  ExternalGeometry = -> [Pad471]
  FullyConstrained = true
  MakeInternals = false
  MapMode = 5
  Placement = pos=(0,0,-4.8) rot=(1,0,0;3.14159rad)
  sketch-geometry (4):
    g0: LineSegment StartX=-0.25 StartY=1.9 StartZ=0 EndX=-0.25 EndY=-12.8 EndZ=0
    g1: LineSegment StartX=-0.25 StartY=-12.8 StartZ=0 EndX=16.15 EndY=-12.8 EndZ=0
    g2: LineSegment StartX=16.15 StartY=-12.8 StartZ=0 EndX=16.15 EndY=1.9 EndZ=0
    g3: LineSegment StartX=16.15 StartY=1.9 StartZ=0 EndX=-0.25 EndY=1.9 EndZ=0
  constraints (13):
    c: Coincident(g0,g1)
    c: Coincident(g1,g2)
    c: Coincident(g2,g3)
    c: Coincident(g3,g0)
    c: Vertical(g0)
    c: Vertical(g2)
    c: Horizontal(g1)
    c: Horizontal(g3)
    c: DistanceX(g3,g3) = 16.4
    c: PointOnObject(g0,g-3)
    c: DistanceX(g-3,g-3) = 17.4
    c: DistanceX(g-3,g0) = 0.5
    c: DistanceY(g-4,g0) = 1.5
FEATURE [PartDesign::Pocket] Pocket294
  BaseFeature = -> Pad471
  Direction = (0,0,1)
  Length = 3.5
  Length2 = 5
  Profile = -> Sketch672
  ReferenceAxis = -> Sketch672 [N_Axis]
  Refine = true
  Suppressed = false
  Type = 0
FEATURE [Sketcher::SketchObject] Sketch673
  ArcFitTolerance = 1e-06
  AttachmentSupport = -> [Pocket294]
  ExternalGeometry = -> [Pocket294]
  FullyConstrained = true
  MakeInternals = false
  MapMode = 5
  Placement = pos=(0,0,-1.3) rot=(1,0,0;3.14159rad)
  sketch-geometry (4):
    g0: LineSegment StartX=1.45 StartY=1.9 StartZ=0 EndX=1.45 EndY=-12.8 EndZ=0
    g1: LineSegment StartX=1.45 StartY=-12.8 StartZ=0 EndX=14.45 EndY=-12.8 EndZ=0
    g2: LineSegment StartX=14.45 StartY=-12.8 StartZ=0 EndX=14.45 EndY=1.9 EndZ=0
    g3: LineSegment StartX=14.45 StartY=1.9 StartZ=0 EndX=1.45 EndY=1.9 EndZ=0
  constraints (13):
    c: Coincident(g0,g1)
    c: Coincident(g1,g2)
    c: Coincident(g2,g3)
    c: Coincident(g3,g0)
    c: Vertical(g0)
    c: Vertical(g2)
    c: Horizontal(g1)
    c: Horizontal(g3)
    c: PointOnObject(g0,g-3)
    c: PointOnObject(g1,g-4)
    c: DistanceX(g3,g3) = 13
    c: DistanceX(g-3,g-3) = 16.4
    c: DistanceX(g-3,g0) = 1.7
FEATURE [PartDesign::Pocket] Pocket295
  BaseFeature = -> Pocket294
  Direction = (0,0,1)
  Length = 4
  Length2 = 5
  Profile = -> Sketch673
  ReferenceAxis = -> Sketch673 [N_Axis]
  Refine = true
  Suppressed = false
  Type = 0
FEATURE [Sketcher::SketchObject] Sketch674
  ArcFitTolerance = 1e-06
  AttachmentSupport = -> [Pocket295]
  ExternalGeometry = -> [Pocket295]
  FullyConstrained = true
  MakeInternals = false
  MapMode = 5
  Placement = pos=(0,0,2.7) rot=(1,0,0;3.14159rad)
  sketch-geometry (8):
    g0: LineSegment StartX=14.45 StartY=1.9 StartZ=0 EndX=9.25 EndY=1.9 EndZ=0
    g1: LineSegment StartX=9.25 StartY=1.9 StartZ=0 EndX=9.25 EndY=-1.9 EndZ=0
    g2: LineSegment StartX=9.25 StartY=-1.9 StartZ=0 EndX=14.45 EndY=-1.9 EndZ=0
    g3: LineSegment StartX=14.45 StartY=-1.9 StartZ=0 EndX=14.45 EndY=1.9 EndZ=0
    g4: LineSegment StartX=1.45 StartY=1.9 StartZ=0 EndX=1.45 EndY=-1.9 EndZ=0
    g5: LineSegment StartX=1.45 StartY=-1.9 StartZ=0 EndX=6.65 EndY=-1.9 EndZ=0
    g6: LineSegment StartX=6.65 StartY=-1.9 StartZ=0 EndX=6.65 EndY=1.9 EndZ=0
    g7: LineSegment StartX=6.65 StartY=1.9 StartZ=0 EndX=1.45 EndY=1.9 EndZ=0
  constraints (22):
    c: Coincident(g0,g1)
    c: Coincident(g1,g2)
    c: Coincident(g2,g3)
    c: Coincident(g3,g0)
    c: Horizontal(g0)
    c: Horizontal(g2)
    c: Vertical(g1)
    c: Vertical(g3)
    c: Coincident(g0,g-5)
    c: Coincident(g4,g5)
    c: Coincident(g5,g6)
    c: Coincident(g6,g7)
    c: Coincident(g7,g4)
    c: Vertical(g4)
    c: Vertical(g6)
    c: Horizontal(g5)
    c: Horizontal(g7)
    c: Coincident(g4,g-4)
    c: DistanceX(g2,g2) = 5.2
    c: DistanceX(g5,g5) = 5.2
    c: DistanceY(g6,g6) = 3.8
    c: DistanceY(g1,g1) = 3.8
FEATURE [PartDesign::Pad] Pad472
  BaseFeature = -> Pocket295
  Direction = (0,0,-1)
  Length = 1.5
  Length2 = 10
  Profile = -> Sketch674
  ReferenceAxis = -> Sketch674 [N_Axis]
  Refine = true
  Suppressed = false
  Type = 0
FEATURE [Sketcher::SketchObject] Sketch675
  ArcFitTolerance = 1e-06
  AttachmentSupport = -> [Pad472]
  ExternalGeometry = -> [Pad472]
  FullyConstrained = true
  MakeInternals = false
  MapMode = 5
  Placement = pos=(0,0,-5.8) rot=(1,0,0;3.14159rad)
  sketch-geometry (9):
    g0: LineSegment StartX=-3.55 StartY=0.55 StartZ=0 EndX=-3.55 EndY=-11.45 EndZ=0
    g1: LineSegment StartX=-3.55 StartY=-11.45 StartZ=0 EndX=-1.55 EndY=-11.45 EndZ=0
    g2: LineSegment StartX=-1.55 StartY=-11.45 StartZ=0 EndX=-1.55 EndY=0.55 EndZ=0
    g3: LineSegment StartX=-1.55 StartY=0.55 StartZ=0 EndX=-3.55 EndY=0.55 EndZ=0
    g4: LineSegment StartX=17.45 StartY=0.55 StartZ=0 EndX=17.45 EndY=-11.45 EndZ=0
    g5: LineSegment StartX=17.45 StartY=-11.45 StartZ=0 EndX=19.45 EndY=-11.45 EndZ=0
    g6: LineSegment StartX=19.45 StartY=-11.45 StartZ=0 EndX=19.45 EndY=0.55 EndZ=0
    g7: LineSegment StartX=19.45 StartY=0.55 StartZ=0 EndX=17.45 EndY=0.55 EndZ=0
    g8: LineSegment [constr] StartX=17.45 StartY=0.55 StartZ=0 EndX=-1.55 EndY=0.55 EndZ=0
  constraints (28):
    c: Coincident(g0,g1)
    c: Coincident(g1,g2)
    c: Coincident(g2,g3)
    c: Coincident(g3,g0)
    c: Vertical(g0)
    c: Vertical(g2)
    c: Horizontal(g1)
    c: Horizontal(g3)
    c: Coincident(g4,g5)
    c: Coincident(g5,g6)
    c: Coincident(g6,g7)
    c: Coincident(g7,g4)
    c: Vertical(g4)
    c: Vertical(g6)
    c: Horizontal(g5)
    c: Horizontal(g7)
    c: DistanceX(g3,g3) = 2
    c: DistanceX(g7,g7) = 2
    c: DistanceY(g0,g0) = 12
    c: DistanceY(g6,g6) = 12
    c: DistanceX(g2,g4) = 19
    c: Coincident(g8,g4)
    c: Coincident(g8,g2)
    c: Horizontal(g8)
    c: DistanceX(g2,g-4) = 0.8
    c: DistanceX(g-3,g4) = 0.8
    c: DistanceY(g2,g-4) = 1.35
    c: DistanceY(g-5,g1) = 1.35
FEATURE [PartDesign::Pad] Pad473
  BaseFeature = -> Pad472
  Direction = (0,0,-1)
  Length = 3.3
  Length2 = 10
  Profile = -> Sketch675
  ReferenceAxis = -> Sketch675 [N_Axis]
  Refine = true
  Suppressed = false
  Type = 0
FEATURE [Sketcher::SketchObject] Sketch676
  ArcFitTolerance = 1e-06
  AttachmentSupport = -> [Pad473]
  ExternalGeometry = -> [Pad473]
  FullyConstrained = true
  MakeInternals = false
  MapMode = 5
  Placement = pos=(0,0,-5.8) rot=(1,0,0;3.14159rad)
  sketch-geometry (26):
    g0: LineSegment StartX=22.4 StartY=-20.8 StartZ=0 EndX=29.4874 EndY=-23.2534 EndZ=0
    g1: LineSegment StartX=29.4874 StartY=-23.2534 StartZ=0 EndX=30.2432 EndY=-22.5986 EndZ=0
    g2: LineSegment StartX=30.2432 StartY=-22.5986 StartZ=0 EndX=44.4179 EndY=-27.5054 EndZ=0
    g3: LineSegment StartX=44.4179 StartY=-27.5054 StartZ=0 EndX=44.4179 EndY=-28.5054 EndZ=0
    g4: LineSegment StartX=44.4179 StartY=-28.5054 StartZ=0 EndX=52.5447 EndY=-31.3187 EndZ=0
    g5: LineSegment StartX=52.5447 StartY=-31.3187 StartZ=0 EndX=54.5447 EndY=-31.3187 EndZ=0
    g6: LineSegment StartX=54.5447 StartY=-31.3187 StartZ=0 EndX=54.5447 EndY=-18.3187 EndZ=0
    g7: LineSegment StartX=54.5447 StartY=-18.3187 StartZ=0 EndX=52.5447 EndY=-18.3187 EndZ=0
    g8: LineSegment StartX=52.5447 StartY=-18.3187 StartZ=0 EndX=50.6475 EndY=-17.1091 EndZ=0
    g9: LineSegment StartX=50.6475 StartY=-17.1091 StartZ=0 EndX=50.6475 EndY=-13.6091 EndZ=0
    g10: LineSegment StartX=50.6475 StartY=-13.6091 StartZ=0 EndX=22.4 EndY=4.4 EndZ=0
    g11: LineSegment [constr] StartX=52.5447 StartY=-31.3187 StartZ=0 EndX=52.5447 EndY=-18.3187 EndZ=0
    g12: LineSegment StartX=-6.5 StartY=-20.8 StartZ=0 EndX=-13.5874 EndY=-23.2534 EndZ=0
    g13: LineSegment StartX=-13.5874 StartY=-23.2534 StartZ=0 EndX=-14.3432 EndY=-22.5986 EndZ=0
    g14: LineSegment StartX=-14.3432 StartY=-22.5986 StartZ=0 EndX=-28.5179 EndY=-27.5054 EndZ=0
    g15: LineSegment StartX=-28.5179 StartY=-27.5054 StartZ=0 EndX=-28.5179 EndY=-28.5054 EndZ=0
    g16: LineSegment StartX=-28.5179 StartY=-28.5054 StartZ=0 EndX=-36.6447 EndY=-31.3187 EndZ=0
    g17: LineSegment StartX=-36.6447 StartY=-31.3187 StartZ=0 EndX=-38.6447 EndY=-31.3187 EndZ=0
    g18: LineSegment StartX=-38.6447 StartY=-31.3187 StartZ=0 EndX=-38.6447 EndY=-18.3187 EndZ=0
    g19: LineSegment StartX=-38.6447 StartY=-18.3187 StartZ=0 EndX=-36.6447 EndY=-18.3187 EndZ=0
    g20: LineSegment StartX=-36.6447 StartY=-18.3187 StartZ=0 EndX=-34.7475 EndY=-17.1091 EndZ=0
    g21: LineSegment StartX=-34.7475 StartY=-17.1091 StartZ=0 EndX=-34.7475 EndY=-13.6091 EndZ=0
    g22: LineSegment StartX=-34.7475 StartY=-13.6091 StartZ=0 EndX=-6.5 EndY=4.4 EndZ=0
    g23: LineSegment StartX=-6.5 StartY=4.4 StartZ=0 EndX=-6.5 EndY=-20.8 EndZ=0
    g24: LineSegment StartX=22.4 StartY=-20.8 StartZ=0 EndX=22.4 EndY=4.4 EndZ=0
    g25: LineSegment [constr] StartX=-36.6447 StartY=-31.3187 StartZ=0 EndX=-36.6447 EndY=-18.3187 EndZ=0
  constraints (74):
    c: Coincident(g0,g-4)
    c: Coincident(g1,g0)
    c: Coincident(g2,g1)
    c: Coincident(g3,g2)
    c: Coincident(g4,g3)
    c: Coincident(g5,g4)
    c: Horizontal(g5)
    c: Coincident(g6,g5)
    c: Vertical(g6)
    c: Coincident(g7,g6)
    c: Horizontal(g7)
    c: Coincident(g8,g7)
    c: Coincident(g9,g8)
    c: Vertical(g9)
    c: Coincident(g10,g9)
    c: PointOnObject(g10,g-4)
    c: DistanceX(g5,g5) = 2
    c: Distance(g2) = 15
    c: Distance(g0) = 7.5
    c: Distance(g4) = 8.6
    c: DistanceY(g10,g-5) = 6.3
    c: Distance(g10) = 33.5
    c: Parallel(g0,g2)
    c: Parallel(g2,g4)
    c: Distance(g3) = 1
    c: Distance(g1) = 1
    c: Distance(g8) = 2.25
    c: Vertical(g3)
    c: Coincident(g11,g4)
    c: Coincident(g11,g7)
    c: Vertical(g11)
    c: Distance(g11) = 13
    c: Parallel(g8,g10)
    c: DistanceY(g9,g9) = 3.5
    c: Angle(g1,g0) = 2.0944
    c: Coincident(g12,g-6)
    c: Coincident(g13,g12)
    c: Coincident(g14,g13)
    c: Coincident(g15,g14)
    c: Vertical(g15)
    c: Coincident(g16,g15)
    c: Coincident(g17,g16)
    c: Horizontal(g17)
    c: Coincident(g18,g17)
    c: Vertical(g18)
    c: Coincident(g19,g18)
    c: Horizontal(g19)
    c: Coincident(g20,g19)
    c: Coincident(g21,g20)
    c: Vertical(g21)
    c: Coincident(g22,g21)
    c: PointOnObject(g22,g-6)
    c: Coincident(g23,g22)
    c: Coincident(g23,g12)
    c: Coincident(g24,g0)
    c: Coincident(g24,g10)
    c: Distance(g12) = 7.5
    c: Distance(g22) = 33.5
    c: Distance(g14) = 15
    c: Distance(g16) = 8.6
    c: DistanceX(g17,g17) = 2
    c: DistanceY(g18,g18) = 13
    c: DistanceY(g21,g21) = 3.5
    c: Parallel(g12,g14)
    c: Parallel(g14,g16)
    c: Distance(g20) = 2.25
    c: Distance(g13) = 1
    c: DistanceY(g15,g15) = 1
    c: Angle(g12,g13) = 2.0944
    c: Coincident(g25,g16)
    c: Coincident(g25,g19)
    c: Vertical(g25)
    c: DistanceY(g22,g-7) = 6.3
    c: Parallel(g20,g22)
FEATURE [PartDesign::Pad] Pad474
  BaseFeature = -> Pad473
  Direction = (0,0,-1)
  Length = 2
  Length2 = 10
  Profile = -> Sketch676
  ReferenceAxis = -> Sketch676 [N_Axis]
  Refine = true
  Reversed = true
  Suppressed = false
  Type = 0
FEATURE [Sketcher::SketchObject] Sketch677
  ArcFitTolerance = 1e-06
  AttachmentSupport = -> [Pad474]
  ExternalGeometry = -> [Pad474]
  FullyConstrained = true
  MakeInternals = false
  MapMode = 5
  Placement = pos=(0,0,-3.8) rot=(0,0,1;0rad)
  sketch-geometry (8):
    g0: LineSegment StartX=22.4 StartY=10.3 StartZ=0 EndX=22.4 EndY=8.1 EndZ=0
    g1: LineSegment StartX=22.4 StartY=10.3 StartZ=0 EndX=51.5447 EndY=24.6187 EndZ=0
    g2: LineSegment StartX=51.5447 StartY=24.6187 StartZ=0 EndX=51.5447 EndY=22.4187 EndZ=0
    g3: LineSegment StartX=51.5447 StartY=22.4187 StartZ=0 EndX=22.4 EndY=8.1 EndZ=0
    g4: LineSegment StartX=-6.5 StartY=10.3 StartZ=0 EndX=-6.5 EndY=8.1 EndZ=0
    g5: LineSegment StartX=-6.5 StartY=8.1 StartZ=0 EndX=-35.6447 EndY=22.4187 EndZ=0
    g6: LineSegment StartX=-35.6447 StartY=22.4187 StartZ=0 EndX=-35.6447 EndY=24.6187 EndZ=0
    g7: LineSegment StartX=-35.6447 StartY=24.6187 StartZ=0 EndX=-6.5 EndY=10.3 EndZ=0
  constraints (24):
    c: PointOnObject(g0,g-3)
    c: PointOnObject(g0,g-3)
    c: Coincident(g1,g0)
    c: Coincident(g2,g1)
    c: Vertical(g2)
    c: Coincident(g3,g2)
    c: Coincident(g3,g0)
    c: DistanceY(g0,g0) = 2.2
    c: DistanceY(g0,g-4) = 10.5
    c: Parallel(g1,g3)
    c: DistanceY(g1,g-6) = 6.7
    c: DistanceX(g1,g-6) = 1
    c: PointOnObject(g4,g-7)
    c: PointOnObject(g4,g-7)
    c: Coincident(g5,g4)
    c: Coincident(g6,g5)
    c: Vertical(g6)
    c: Coincident(g7,g6)
    c: Coincident(g7,g4)
    c: DistanceY(g4,g4) = 2.2
    c: Parallel(g7,g5)
    c: DistanceX(g-10,g6) = 1
    c: DistanceY(g6,g-10) = 6.7
    c: DistanceY(g4,g-8) = 10.5
FEATURE [PartDesign::Pad] Pad475
  BaseFeature = -> Pad474
  Direction = (0,0,1)
  Length = 0.75
  Length2 = 10
  Profile = -> Sketch677
  ReferenceAxis = -> Sketch677 [N_Axis]
  Refine = true
  Suppressed = false
  Type = 0
FEATURE [Sketcher::SketchObject] Sketch678
  ArcFitTolerance = 1e-06
  AttachmentSupport = -> [Pad475]
  ExternalGeometry = -> [Pad475]
  FullyConstrained = true
  MakeInternals = false
  MapMode = 5
  Placement = pos=(1.14972,-2.34018,0) rot=(0.950013,0.220766,0.220766;1.62205rad)
  sketch-geometry (4):
    g0: LineSegment StartX=56.1485 StartY=-3.8 StartZ=0 EndX=52.1485 EndY=-3.05 EndZ=0
    g1: LineSegment StartX=52.1485 StartY=-3.05 StartZ=0 EndX=58.1485 EndY=-3.05 EndZ=0
    g2: LineSegment StartX=58.1485 StartY=-3.05 StartZ=0 EndX=58.1485 EndY=-3.8 EndZ=0
    g3: LineSegment StartX=56.1485 StartY=-3.8 StartZ=0 EndX=58.1485 EndY=-3.8 EndZ=0
  constraints (11):
    c: Coincident(g0,g-4)
    c: PointOnObject(g0,g-3)
    c: Coincident(g1,g0)
    c: Horizontal(g1)
    c: Coincident(g2,g1)
    c: Vertical(g2)
    c: Coincident(g3,g0)
    c: Coincident(g3,g2)
    c: Horizontal(g3)
    c: DistanceX(g0,g-4) = 4
    c: DistanceX(g-4,g1) = 2
FEATURE [PartDesign::Pocket] Pocket296
  BaseFeature = -> Pad475
  Direction = (-0.440953,0.89753,3e-16)
  Length = 5
  Length2 = 5
  Profile = -> Sketch678
  ReferenceAxis = -> Sketch678 [N_Axis]
  Refine = true
  Suppressed = false
  Type = 0
FEATURE [Sketcher::SketchObject] Sketch679
  ArcFitTolerance = 1e-06
  AttachmentSupport = -> [Pocket296]
  ExternalGeometry = -> [Pocket296]
  FullyConstrained = true
  MakeInternals = false
  MapMode = 5
  Placement = pos=(1.94187,3.95254,0) rot=(0.950013,-0.220766,-0.220766;1.62205rad)
  sketch-geometry (5):
    g0: LineSegment StartX=-41.8778 StartY=-3.05 StartZ=0 EndX=-37.8778 EndY=-3.05 EndZ=0
    g1: LineSegment StartX=-37.8778 StartY=-3.05 StartZ=0 EndX=-41.8778 EndY=-3.8 EndZ=0
    g2: LineSegment StartX=-41.8778 StartY=-3.8 StartZ=0 EndX=-43.8778 EndY=-3.8 EndZ=0
    g3: LineSegment StartX=-43.8778 StartY=-3.8 StartZ=0 EndX=-43.8778 EndY=-3.05 EndZ=0
    g4: LineSegment StartX=-41.8778 StartY=-3.05 StartZ=0 EndX=-43.8778 EndY=-3.05 EndZ=0
  constraints (13):
    c: Coincident(g0,g-5)
    c: PointOnObject(g0,g-3)
    c: Coincident(g1,g0)
    c: Coincident(g1,g-5)
    c: Coincident(g2,g1)
    c: Horizontal(g2)
    c: Coincident(g3,g2)
    c: Vertical(g3)
    c: Coincident(g4,g0)
    c: Coincident(g4,g3)
    c: Horizontal(g4)
    c: DistanceX(g0,g0) = 4
    c: DistanceX(g3,g0) = 2
FEATURE [PartDesign::Pocket] Pocket297
  BaseFeature = -> Pocket296
  Direction = (0.440953,0.89753,2e-16)
  Length = 5
  Length2 = 5
  Profile = -> Sketch679
  ReferenceAxis = -> Sketch679 [N_Axis]
  Refine = true
  Suppressed = false
  Type = 0
FEATURE [Sketcher::SketchObject] Sketch680
  ArcFitTolerance = 1e-06
  AttachmentSupport = -> [Pocket297]
  ExternalGeometry = -> [Pocket297]
  FullyConstrained = false
  MakeInternals = false
  MapMode = 5
  Placement = pos=(0,0,-3.8) rot=(0,0,1;0rad)
  sketch-geometry (105):
    g0: LineSegment StartX=-28.5179 StartY=27.5054 StartZ=0 EndX=-28.5179 EndY=25.7054 EndZ=0
    g1: LineSegment StartX=-28.5179 StartY=25.7054 StartZ=0 EndX=-15.8276 EndY=21.3125 EndZ=0
    g2: LineSegment StartX=-14.3432 StartY=22.5986 StartZ=0 EndX=-15.8276 EndY=21.3125 EndZ=0
    g3: LineSegment StartX=-8 StartY=12.3227 StartZ=0 EndX=-8 EndY=19.7319 EndZ=0
    g4: LineSegment StartX=-8 StartY=19.7319 StartZ=0 EndX=-13.2597 EndY=21.5526 EndZ=0
    g5: LineSegment StartX=-13.2597 StartY=21.5526 StartZ=0 EndX=-14.3276 EndY=20.6274 EndZ=0
    g6: LineSegment StartX=-14.3276 StartY=20.6274 StartZ=0 EndX=-14.3276 EndY=15.4314 EndZ=0
    g7: LineSegment StartX=-8 StartY=12.3227 StartZ=0 EndX=-14.3276 EndY=15.4314 EndZ=0
    g8: LineSegment StartX=-15.8276 StartY=19.7251 StartZ=0 EndX=-15.8276 EndY=16.1683 EndZ=0
    g9: LineSegment StartX=-15.8276 StartY=16.1683 StartZ=0 EndX=-35.5123 EndY=25.8394 EndZ=0
    g10: LineSegment StartX=-35.5123 StartY=25.8394 StartZ=0 EndX=-35.5123 EndY=29.3394 EndZ=0
    g11: LineSegment StartX=-35.5123 StartY=29.3394 StartZ=0 EndX=-30.0881 EndY=27.4617 EndZ=0
    g12: LineSegment StartX=-30.0881 StartY=27.4617 StartZ=0 EndX=-30.0881 EndY=24.6617 EndZ=0
    g13: LineSegment StartX=-30.0881 StartY=24.6617 StartZ=0 EndX=-15.8276 EndY=19.7251 EndZ=0
    g14: LineSegment StartX=-35.5123 StartY=20.2742 StartZ=0 EndX=-35.5123 EndY=19.2304 EndZ=0
    g15: LineSegment StartX=-35.5123 StartY=19.2304 StartZ=0 EndX=-33.2475 EndY=17.7865 EndZ=0
    g16: LineSegment StartX=-33.2475 StartY=17.7865 StartZ=0 EndX=-33.2475 EndY=14.4317 EndZ=0
    g17: LineSegment StartX=-33.2475 StartY=14.4317 StartZ=0 EndX=-24.5625 EndY=8.89458 EndZ=0
    g18: LineSegment StartX=-24.5625 StartY=8.89458 StartZ=0 EndX=-24.5625 EndY=14.8946 EndZ=0
    g19: LineSegment StartX=-24.5625 StartY=14.8946 StartZ=0 EndX=-35.5123 EndY=20.2742 EndZ=0
    g20: LineSegment StartX=-9 StartY=-2.80613 StartZ=0 EndX=-10.3 EndY=-1.97732 EndZ=0
    g21: LineSegment StartX=-9 StartY=-2.80613 StartZ=0 EndX=-9 EndY=7.1 EndZ=0
    g22: LineSegment StartX=-10.3 StartY=-1.97732 StartZ=0 EndX=-10.3 EndY=7.1 EndZ=0
    g23: LineSegment StartX=-13.3 StartY=-0.0646793 StartZ=0 EndX=-14.6 EndY=0.764132 EndZ=0
    g24: LineSegment StartX=-13.3 StartY=-0.0646793 StartZ=0 EndX=-13.3 EndY=9.21257 EndZ=0
    g25: LineSegment StartX=-14.6 StartY=0.764132 StartZ=0 EndX=-14.6 EndY=9.21257 EndZ=0
    g26: LineSegment StartX=-17.6 StartY=2.67677 StartZ=0 EndX=-18.9 EndY=3.50558 EndZ=0
    g27: LineSegment StartX=-17.6 StartY=2.67677 StartZ=0 EndX=-17.6 EndY=11.3251 EndZ=0
    g28: LineSegment StartX=-18.9 StartY=3.50558 StartZ=0 EndX=-18.9 EndY=11.3251 EndZ=0
    g29: ArcOfCircle CenterX=-18.25 CenterY=11.3251 CenterZ=0 NormalX=0 NormalY=0 NormalZ=1 AngleXU=0 Radius=0.65 StartAngle=2.5e-14 EndAngle=3.14159
    g30: ArcOfCircle CenterX=-13.95 CenterY=9.21257 CenterZ=0 NormalX=0 NormalY=0 NormalZ=1 AngleXU=0 Radius=0.65 StartAngle=-3.6e-15 EndAngle=3.14159
    g31: ArcOfCircle CenterX=-9.65 CenterY=7.1 CenterZ=0 NormalX=0 NormalY=0 NormalZ=1 AngleXU=0 Radius=0.65 StartAngle=5.8e-15 EndAngle=3.14159
    g32: LineSegment StartX=-23.2 StartY=6.24704 StartZ=0 EndX=-21.9 EndY=5.41823 EndZ=0
    g33: LineSegment StartX=-21.9 StartY=5.41823 StartZ=0 EndX=-21.9 EndY=13.4377 EndZ=0
    g34: LineSegment StartX=-23.2 StartY=6.24704 StartZ=0 EndX=-23.2 EndY=13.4377 EndZ=0
    g35: ArcOfCircle CenterX=-22.55 CenterY=13.4377 CenterZ=0 NormalX=0 NormalY=0 NormalZ=1 AngleXU=0 Radius=0.65 StartAngle=-1.87e-14 EndAngle=3.14159
    g36: LineSegment [constr] StartX=-18.9 StartY=11.3251 StartZ=0 EndX=-17.6 EndY=11.3251 EndZ=0
    g37: LineSegment [constr] StartX=-14.6 StartY=9.21257 StartZ=0 EndX=-13.3 EndY=9.21257 EndZ=0
    g38: LineSegment [constr] StartX=-10.3 StartY=7.1 StartZ=0 EndX=-9 EndY=7.1 EndZ=0
    g39: LineSegment [constr] StartX=-23.2 StartY=13.4377 StartZ=0 EndX=-21.9 EndY=13.4377 EndZ=0
    g40: LineSegment [constr] StartX=-9.65 StartY=7.1 StartZ=0 EndX=-13.95 EndY=9.21257 EndZ=0
    g41: LineSegment [constr] StartX=-13.95 StartY=9.21257 StartZ=0 EndX=-18.25 EndY=11.3251 EndZ=0
    g42: LineSegment [constr] StartX=-18.25 StartY=11.3251 StartZ=0 EndX=-22.55 EndY=13.4377 EndZ=0
    g43: LineSegment [constr] StartX=-31.4115 StartY=13.2612 StartZ=0 EndX=-32.2179 EndY=11.9964 EndZ=0
    g44: LineSegment [constr] StartX=-34.7475 StartY=16.1091 StartZ=0 EndX=-33.2475 EndY=16.1091 EndZ=0
    g45: LineSegment [constr] StartX=-35.5123 StartY=25.8394 StartZ=0 EndX=-35.5123 EndY=20.2742 EndZ=0
    g46: LineSegment [constr] StartX=-32.3095 StartY=29.818 StartZ=0 EndX=-32.8002 EndY=28.4005 EndZ=0
    g47: LineSegment [constr] StartX=-15.8276 StartY=21.3125 StartZ=0 EndX=-15.8276 EndY=19.7251 EndZ=0
    g48: LineSegment [constr] StartX=-24.9931 StartY=24.4853 StartZ=0 EndX=-25.4838 EndY=23.0678 EndZ=0
    g49: LineSegment [constr] StartX=-14.3276 StartY=15.4314 StartZ=0 EndX=-15.8276 EndY=16.1683 EndZ=0
    g50: LineSegment [constr] StartX=-9.08744 StartY=21.6957 StartZ=0 EndX=-9.57812 EndY=20.2782 EndZ=0
    g51: LineSegment [constr] StartX=-14.5692 StartY=22.4028 StartZ=0 EndX=-13.5869 EndY=21.2691 EndZ=0
    g52: LineSegment StartX=-14.3432 StartY=22.5986 StartZ=0 EndX=-28.5179 EndY=27.5054 EndZ=0
    g53: LineSegment StartX=24.9 StartY=-2.80613 StartZ=0 EndX=26.2 EndY=-1.97732 EndZ=0
    g54: LineSegment StartX=29.2 StartY=-0.0646793 StartZ=0 EndX=30.5 EndY=0.764132 EndZ=0
    g55: LineSegment StartX=33.5 StartY=2.67677 StartZ=0 EndX=34.8 EndY=3.50558 EndZ=0
    g56: LineSegment StartX=24.9 StartY=-2.80613 StartZ=0 EndX=24.9 EndY=7.1 EndZ=0
    g57: LineSegment StartX=26.2 StartY=-1.97732 StartZ=0 EndX=26.2 EndY=7.1 EndZ=0
    g58: LineSegment StartX=29.2 StartY=-0.0646793 StartZ=0 EndX=29.2 EndY=9.21257 EndZ=0
    g59: LineSegment StartX=30.5 StartY=0.764132 StartZ=0 EndX=30.5 EndY=9.21257 EndZ=0
    g60: LineSegment StartX=33.5 StartY=2.67677 StartZ=0 EndX=33.5 EndY=11.3251 EndZ=0
    g61: LineSegment StartX=34.8 StartY=3.50558 StartZ=0 EndX=34.8 EndY=11.3251 EndZ=0
    g62: ArcOfCircle CenterX=25.55 CenterY=7.1 CenterZ=0 NormalX=0 NormalY=0 NormalZ=1 AngleXU=0 Radius=0.65 StartAngle=-2.13e-14 EndAngle=3.14159
    g63: ArcOfCircle CenterX=29.85 CenterY=9.21257 CenterZ=0 NormalX=0 NormalY=0 NormalZ=1 AngleXU=0 Radius=0.65 StartAngle=-9.8e-15 EndAngle=3.14159
    g64: ArcOfCircle CenterX=34.15 CenterY=11.3251 CenterZ=0 NormalX=0 NormalY=0 NormalZ=1 AngleXU=0 Radius=0.65 StartAngle=-1.69e-14 EndAngle=3.14159
    g65: LineSegment [constr] StartX=34.8 StartY=11.3251 StartZ=0 EndX=33.5 EndY=11.3251 EndZ=0
    g66: LineSegment [constr] StartX=30.5 StartY=9.21257 StartZ=0 EndX=29.2 EndY=9.21257 EndZ=0
    g67: LineSegment [constr] StartX=26.2 StartY=7.1 StartZ=0 EndX=24.9 EndY=7.1 EndZ=0
    g68: LineSegment StartX=37.8 StartY=5.41823 StartZ=0 EndX=39.1 EndY=6.24704 EndZ=0
    g69: LineSegment StartX=39.1 StartY=6.24704 StartZ=0 EndX=39.1 EndY=13.4377 EndZ=0
    g70: LineSegment StartX=37.8 StartY=5.41823 StartZ=0 EndX=37.8 EndY=13.4377 EndZ=0
    g71: ArcOfCircle CenterX=38.45 CenterY=13.4377 CenterZ=0 NormalX=0 NormalY=0 NormalZ=1 AngleXU=0 Radius=0.65 StartAngle=1.92e-14 EndAngle=3.14159
    g72: LineSegment [constr] StartX=39.1 StartY=13.4377 StartZ=0 EndX=37.8 EndY=13.4377 EndZ=0
    g73: LineSegment [constr] StartX=25.55 StartY=7.1 StartZ=0 EndX=29.85 EndY=9.21257 EndZ=0
    g74: LineSegment [constr] StartX=29.85 StartY=9.21257 StartZ=0 EndX=34.15 EndY=11.3251 EndZ=0
    g75: LineSegment [constr] StartX=34.15 StartY=11.3251 StartZ=0 EndX=38.45 EndY=13.4377 EndZ=0
    g76: LineSegment StartX=30.2432 StartY=22.5986 StartZ=0 EndX=44.4179 EndY=27.5054 EndZ=0
    g77: LineSegment StartX=44.4179 StartY=27.5054 StartZ=0 EndX=44.4179 EndY=25.8558 EndZ=0
    g78: LineSegment StartX=44.4179 StartY=25.8558 StartZ=0 EndX=31.6036 EndY=21.4199 EndZ=0
    g79: LineSegment StartX=31.6036 StartY=21.4199 StartZ=0 EndX=30.2432 EndY=22.5986 EndZ=0
    g80: LineSegment StartX=23.9 StartY=19.7319 StartZ=0 EndX=29.1597 EndY=21.5526 EndZ=0
    g81: LineSegment StartX=29.1597 StartY=21.5526 StartZ=0 EndX=30.1036 EndY=20.7348 EndZ=0
    g82: LineSegment StartX=30.1036 StartY=20.7348 StartZ=0 EndX=30.1036 EndY=15.3704 EndZ=0
    g83: LineSegment StartX=30.1036 StartY=15.3704 StartZ=0 EndX=23.9 EndY=12.3227 EndZ=0
    g84: LineSegment StartX=23.9 StartY=12.3227 StartZ=0 EndX=23.9 EndY=19.7319 EndZ=0
    g85: LineSegment StartX=31.6036 StartY=16.1074 StartZ=0 EndX=51.4123 EndY=25.8394 EndZ=0
    g86: LineSegment StartX=51.4123 StartY=25.8394 StartZ=0 EndX=51.4123 EndY=29.3394 EndZ=0
    g87: LineSegment StartX=51.4123 StartY=29.3394 StartZ=0 EndX=45.8633 EndY=27.4185 EndZ=0
    g88: LineSegment StartX=45.8633 StartY=27.4185 StartZ=0 EndX=45.8633 EndY=24.7689 EndZ=0
    g89: LineSegment StartX=45.8633 StartY=24.7689 StartZ=0 EndX=31.6036 EndY=19.8326 EndZ=0
    g90: LineSegment StartX=31.6036 StartY=19.8326 StartZ=0 EndX=31.6036 EndY=16.1074 EndZ=0
    g91: LineSegment StartX=40.4625 StartY=14.8946 StartZ=0 EndX=51.4123 EndY=20.2742 EndZ=0
    g92: LineSegment StartX=51.4123 StartY=20.2742 StartZ=0 EndX=51.4123 EndY=19.2342 EndZ=0
    g93: LineSegment StartX=51.4123 StartY=19.2342 StartZ=0 EndX=49.1475 EndY=17.7903 EndZ=0
    g94: LineSegment StartX=49.1475 StartY=17.7903 StartZ=0 EndX=49.1475 EndY=14.4317 EndZ=0
    g95: LineSegment StartX=49.1475 StartY=14.4317 StartZ=0 EndX=40.4625 EndY=8.89458 EndZ=0
    g96: LineSegment StartX=40.4625 StartY=8.89458 StartZ=0 EndX=40.4625 EndY=14.8946 EndZ=0
    g97: LineSegment [constr] StartX=51.4123 StartY=25.8394 StartZ=0 EndX=51.4123 EndY=20.2742 EndZ=0
    g98: LineSegment [constr] StartX=31.6036 StartY=21.4199 StartZ=0 EndX=31.6036 EndY=19.8326 EndZ=0
    g99: LineSegment [constr] StartX=25.0441 StartY=21.7153 StartZ=0 EndX=25.5348 EndY=20.2978 EndZ=0
    g100: LineSegment [constr] StartX=36.7072 StartY=23.1866 StartZ=0 EndX=37.1979 EndY=21.7692 EndZ=0
    g101: LineSegment [constr] StartX=50.0027 StartY=30.4387 StartZ=0 EndX=50.4934 EndY=29.0213 EndZ=0
    g102: LineSegment [constr] StartX=47.2578 StartY=11.448 StartZ=0 EndX=46.4514 EndY=12.7128 EndZ=0
    g103: LineSegment [constr] StartX=31.6036 StartY=16.1074 StartZ=0 EndX=30.1036 EndY=15.3704 EndZ=0
    g104: LineSegment [constr] StartX=30.6138 StartY=22.2774 StartZ=0 EndX=29.6316 EndY=21.1437 EndZ=0
  constraints (307):
    c: Coincident(g0,g-3)
    c: Vertical(g0)
    c: Coincident(g1,g0)
    c: Coincident(g2,g-3)
    c: Coincident(g2,g1)
    c: Parallel(g2,g-4)
    c: DistanceY(g0,g0) = 1.8
    c: Parallel(g-3,g1)
    c: Coincident(g4,g3)
    c: Coincident(g5,g4)
    c: Coincident(g6,g5)
    c: Vertical(g6)
    c: Coincident(g7,g3)
    c: Coincident(g7,g6)
    c: Coincident(g9,g8)
    c: Coincident(g10,g9)
    c: Vertical(g10)
    c: Coincident(g11,g10)
    c: Coincident(g12,g11)
    c: Coincident(g13,g12)
    c: Coincident(g13,g8)
    c: Vertical(g14)
    c: Coincident(g15,g14)
    c: Coincident(g16,g15)
    c: Vertical(g16)
    c: Coincident(g17,g16)
    c: Coincident(g18,g17)
    c: Vertical(g18)
    c: Coincident(g19,g18)
    c: Coincident(g19,g14)
    c: PointOnObject(g20,g-5)
    c: PointOnObject(g20,g-5)
    c: Coincident(g21,g20)
    c: Coincident(g22,g20)
    c: Vertical(g22)
    c: PointOnObject(g23,g-5)
    c: PointOnObject(g23,g-5)
    c: Coincident(g24,g23)
    c: Vertical(g24)
    c: Coincident(g25,g23)
    c: Vertical(g25)
    c: PointOnObject(g26,g-5)
    c: PointOnObject(g26,g-5)
    c: Coincident(g27,g26)
    c: Vertical(g27)
    c: Coincident(g28,g26)
    c: Vertical(g28)
    c: Coincident(g29,g27)
    c: Coincident(g29,g28)
    c: Coincident(g30,g24)
    c: Coincident(g30,g25)
    c: Coincident(g31,g21)
    c: Coincident(g31,g22)
    c: PointOnObject(g32,g-5)
    c: PointOnObject(g32,g-5)
    c: Coincident(g33,g32)
    c: Vertical(g33)
    c: Coincident(g34,g32)
    c: Vertical(g34)
    c: Coincident(g35,g34)
    c: Coincident(g35,g33)
    c: Coincident(g36,g28)
    c: Coincident(g36,g27)
    c: Coincident(g37,g25)
    c: Coincident(g37,g24)
    c: Coincident(g38,g22)
    c: Coincident(g38,g21)
    c: Horizontal(g38)
    c: Coincident(g39,g34)
    c: Coincident(g39,g33)
    c: Horizontal(g39)
    c: Horizontal(g36)
    c: Horizontal(g37)
    c: PointOnObject(g31,g38)
    c: PointOnObject(g30,g37)
    c: PointOnObject(g29,g36)
    c: PointOnObject(g35,g39)
    c: Diameter(g35) = 1.3
    c: Diameter(g29) = 1.3
    c: Diameter(g30) = 1.3
    c: Diameter(g31) = 1.3
    c: Coincident(g40,g31)
    c: Coincident(g40,g30)
    c: Coincident(g41,g30)
    c: Coincident(g41,g29)
    c: Coincident(g42,g29)
    c: Coincident(g42,g35)
    c: Parallel(g42,g41)
    c: Parallel(g41,g40)
    c: DistanceX(g24,g22) = 3
    c: DistanceX(g27,g25) = 3
    c: DistanceX(g33,g28) = 3
    c: DistanceX(g20,g-5) = 2.5
    c: Vertical(g21)
    c: Parallel(g42,g-6)
    c: DistanceY(g31,g-6) = 1
    c: Parallel(g19,g-6)
    c: Parallel(g-5,g17)
    c: Distance(g19) = 12.2
    c: Distance(g17) = 10.3
    c: PointOnObject(g43,g17)
    c: PointOnObject(g43,g-5)
    c: Perpendicular(g-5,g43)
    c: Distance(g43) = 1.5
    c: Symmetric(g16,g16,g44)
    c: Perpendicular(g44,g16)
    c: Distance(g44) = 1.5
    c: PointOnObject(g44,g-7)
    c: Distance(g43,g-7) = 3
    c: Distance(g44,g-7) = 2.5
    c: Parallel(g15,g-8)
    c: DistanceY(g18,g18) = 6
    c: Parallel(g9,g-9)
    c: Coincident(g45,g9)
    c: Coincident(g45,g14)
    c: Vertical(g45)
    c: Parallel(g-9,g7)
    c: Parallel(g4,g-10)
    c: Vertical(g12)
    c: Parallel(g1,g13)
    c: Parallel(g2,g5)
    c: Vertical(g8)
    c: PointOnObject(g46,g-11)
    c: Symmetric(g11,g11,g46)
    c: Perpendicular(g46,g11)
    c: Distance(g46) = 1.5
    c: Parallel(g11,g-11)
    c: Distance(g10,g46) = 2.87
    c: DistanceY(g10,g10) = 3.5
    c: Coincident(g47,g1)
    c: Coincident(g47,g8)
    c: Vertical(g47)
    c: PointOnObject(g48,g1)
    c: PointOnObject(g48,g13)
    c: Perpendicular(g48,g1)
    c: Distance(g48) = 1.5
    c: Distance(g48,g0) = 3.73
    c: Vertical(g3)
    c: Coincident(g49,g6)
    c: Coincident(g49,g8)
    c: Parallel(g9,g49)
    c: DistanceX(g8,g6) = 1.5
    c: DistanceX(g3,g-10) = 1.5
    c: PointOnObject(g50,g-10)
    c: PointOnObject(g50,g4)
    c: Perpendicular(g50,g4)
    c: Distance(g3,g50) = 1.67
    c: Distance(g50) = 1.5
    c: PointOnObject(g51,g2)
    c: PointOnObject(g51,g5)
    c: Perpendicular(g5,g51)
    c: Distance(g51,g5) = 0.98
    c: Distance(g51) = 1.5
    c: Coincident(g52,g2)
    c: Coincident(g52,g0)
    c: PointOnObject(g53,g-12)
    c: PointOnObject(g53,g-12)
    c: PointOnObject(g54,g-12)
    c: PointOnObject(g54,g-12)
    c: PointOnObject(g55,g-12)
    c: PointOnObject(g55,g-12)
    c: Coincident(g56,g53)
    c: Vertical(g56)
    c: Coincident(g57,g53)
    c: Vertical(g57)
    c: Coincident(g58,g54)
    c: Vertical(g58)
    c: Coincident(g59,g54)
    c: Vertical(g59)
    c: Coincident(g60,g55)
    c: Vertical(g60)
    c: Coincident(g61,g55)
    c: Vertical(g61)
    c: Coincident(g62,g56)
    c: Coincident(g62,g57)
    c: Coincident(g63,g58)
    c: Coincident(g63,g59)
    c: Coincident(g64,g60)
    c: Coincident(g64,g61)
    c: Diameter(g62) = 1.3
    c: Diameter(g63) = 1.3
    c: Diameter(g64) = 1.3
    c: Coincident(g65,g61)
    c: Coincident(g65,g60)
    c: Coincident(g66,g59)
    c: Coincident(g66,g58)
    c: Coincident(g67,g57)
    c: Coincident(g67,g56)
    c: Horizontal(g67)
    c: Horizontal(g66)
    c: Horizontal(g65)
    c: PointOnObject(g63,g66)
    c: PointOnObject(g64,g65)
    c: PointOnObject(g62,g67)
    c: PointOnObject(g68,g-12)
    c: PointOnObject(g68,g-12)
    c: Coincident(g69,g68)
    c: Vertical(g69)
    c: Coincident(g70,g68)
    c: Vertical(g70)
    c: Coincident(g71,g70)
    c: Coincident(g71,g69)
    c: Coincident(g72,g69)
    c: Coincident(g72,g70)
    c: Horizontal(g72)
    c: PointOnObject(g71,g72)
    c: Coincident(g73,g62)
    c: Coincident(g73,g63)
    c: Coincident(g74,g63)
    c: Coincident(g74,g64)
    c: Coincident(g75,g64)
    c: Coincident(g75,g71)
    c: Parallel(g73,g74)
    c: Parallel(g74,g75)
    c: Diameter(g71) = 1.3
    c: DistanceX(g-12,g-12) = 28.2475
    c: DistanceX(g-12,g53) = 2.5
    c: DistanceX(g57,g58) = 3
    c: DistanceX(g59,g60) = 3
    c: DistanceX(g61,g70) = 3
    c: DistanceY(g56,g-18) = 1
    c: Parallel(g-18,g73)
    c: Coincident(g76,g-14)
    c: Coincident(g76,g-14)
    c: Coincident(g77,g76)
    c: Vertical(g77)
    c: Coincident(g78,g77)
    c: Coincident(g79,g78)
    c: Coincident(g79,g76)
    c: Parallel(g76,g78)
    c: Parallel(g-21,g79)
    c: Distance(g79) = 1.8
    c: Coincident(g81,g80)
    c: Coincident(g82,g81)
    c: Vertical(g82)
    c: Coincident(g83,g82)
    c: Coincident(g84,g83)
    c: Coincident(g84,g80)
    c: Vertical(g84)
    c: Parallel(g80,g-22)
    c: Parallel(g-17,g83)
    c: DistanceX(g-22,g80) = 1.5
    c: Coincident(g86,g85)
    c: Coincident(g87,g86)
    c: Coincident(g88,g87)
    c: Vertical(g88)
    c: Coincident(g89,g88)
    c: Coincident(g90,g89)
    c: Coincident(g90,g85)
    c: Coincident(g92,g91)
    c: Coincident(g93,g92)
    c: Coincident(g94,g93)
    c: Coincident(g95,g94)
    c: Coincident(g96,g95)
    c: Coincident(g96,g91)
    c: Vertical(g92)
    c: Vertical(g86)
    c: Coincident(g97,g85)
    c: Coincident(g97,g91)
    c: Vertical(g97)
    c: Vertical(g90)
    c: Coincident(g98,g78)
    c: Coincident(g98,g89)
    c: Vertical(g98)
    c: Parallel(g85,g-17)
    c: Parallel(g89,g78)
    c: Parallel(g87,g-15)
    c: PointOnObject(g99,g-22)
    c: PointOnObject(g99,g80)
    c: Perpendicular(g-22,g99)
    c: Distance(g99,g80) = 1.73
    c: Distance(g99) = 1.5
    c: PointOnObject(g100,g78)
    c: PointOnObject(g100,g89)
    c: Perpendicular(g78,g100)
    c: Distance(g100,g89) = 5.92
    c: Distance(g100) = 1.5
    c: DistanceX(g82,g85) = 1.5
    c: DistanceY(g86,g86) = 3.5
    c: PointOnObject(g101,g-15)
    c: PointOnObject(g101,g87)
    c: Perpendicular(g101,g-15)
    c: Distance(g101,g-15) = 2.69
    c: Distance(g101) = 1.5
    c: Distance(g91) = 12.2
    c: Distance(g95) = 10.3
    c: Vertical(g96)
    c: DistanceY(g96,g96) = 6
    c: Vertical(g94)
    c: Parallel(g-23,g93)
    c: PointOnObject(g102,g-12)
    c: PointOnObject(g102,g95)
    c: Distance(g102,g-13) = 4.02
    c: Distance(g102) = 1.5
    c: DistanceX(g93,g-23) = 1.5
    c: Parallel(g91,g-18)
    c: Parallel(g95,g-12)
    c: Coincident(g103,g85)
    c: Coincident(g103,g82)
    c: Parallel(g103,g85)
    c: PointOnObject(g104,g79)
    c: Symmetric(g81,g81,g104)
    c: Perpendicular(g81,g104)
    c: Parallel(g79,g81)
    c: Distance(g104) = 1.5
    c: Distance(g89) = 15.09
    c: DistanceY(g92,g92) = 1.04
FEATURE [PartDesign::Pocket] Pocket298
  BaseFeature = -> Pocket297
  Direction = (0,0,-1)
  Length = 0.5
  Length2 = 5
  Profile = -> Sketch680
  ReferenceAxis = -> Sketch680 [N_Axis]
  Refine = true
  Suppressed = false
  Type = 0
FEATURE [Sketcher::SketchObject] Sketch681
  ArcFitTolerance = 1e-06
  AttachmentSupport = -> [Pocket298]
  ExternalGeometry = -> [Pocket298]
  FullyConstrained = true
  MakeInternals = false
  MapMode = 5
  Placement = pos=(0,0,-4.3) rot=(0,0,1;0rad)
  sketch-geometry (32):
    g0: LineSegment StartX=-23.2 StartY=6.24704 StartZ=0 EndX=-21.9 EndY=5.41823 EndZ=0
    g1: LineSegment StartX=-21.9 StartY=5.41823 StartZ=0 EndX=-21.9 EndY=5.91823 EndZ=0
    g2: LineSegment StartX=-21.9 StartY=5.91823 StartZ=0 EndX=-23.2 EndY=6.74704 EndZ=0
    g3: LineSegment StartX=-23.2 StartY=6.74704 StartZ=0 EndX=-23.2 EndY=6.24704 EndZ=0
    g4: LineSegment StartX=-18.9 StartY=3.50558 StartZ=0 EndX=-17.6 EndY=2.67677 EndZ=0
    g5: LineSegment StartX=-17.6 StartY=2.67677 StartZ=0 EndX=-17.6 EndY=3.17677 EndZ=0
    g6: LineSegment StartX=-17.6 StartY=3.17677 StartZ=0 EndX=-18.9 EndY=4.00558 EndZ=0
    g7: LineSegment StartX=-18.9 StartY=4.00558 StartZ=0 EndX=-18.9 EndY=3.50558 EndZ=0
    g8: LineSegment StartX=-14.6 StartY=0.764132 StartZ=0 EndX=-13.3 EndY=-0.0646793 EndZ=0
    g9: LineSegment StartX=-13.3 StartY=-0.0646793 StartZ=0 EndX=-13.3 EndY=0.435321 EndZ=0
    g10: LineSegment StartX=-13.3 StartY=0.435321 StartZ=0 EndX=-14.6 EndY=1.26413 EndZ=0
    g11: LineSegment StartX=-14.6 StartY=1.26413 StartZ=0 EndX=-14.6 EndY=0.764132 EndZ=0
    g12: LineSegment StartX=-9 StartY=-2.80613 StartZ=0 EndX=-10.3 EndY=-1.97732 EndZ=0
    g13: LineSegment StartX=-10.3 StartY=-1.97732 StartZ=0 EndX=-10.3 EndY=-1.47732 EndZ=0
    g14: LineSegment StartX=-10.3 StartY=-1.47732 StartZ=0 EndX=-9 EndY=-2.30613 EndZ=0
    g15: LineSegment StartX=-9 StartY=-2.30613 StartZ=0 EndX=-9 EndY=-2.80613 EndZ=0
    g16: LineSegment StartX=24.9 StartY=-2.80613 StartZ=0 EndX=26.2 EndY=-1.97732 EndZ=0
    g17: LineSegment StartX=26.2 StartY=-1.97732 StartZ=0 EndX=26.2 EndY=-1.47732 EndZ=0
    g18: LineSegment StartX=26.2 StartY=-1.47732 StartZ=0 EndX=24.9 EndY=-2.30613 EndZ=0
    g19: LineSegment StartX=24.9 StartY=-2.30613 StartZ=0 EndX=24.9 EndY=-2.80613 EndZ=0
    g20: LineSegment StartX=29.2 StartY=-0.0646793 StartZ=0 EndX=30.5 EndY=0.764132 EndZ=0
    g21: LineSegment StartX=30.5 StartY=0.764132 StartZ=0 EndX=30.5 EndY=1.26413 EndZ=0
    g22: LineSegment StartX=30.5 StartY=1.26413 StartZ=0 EndX=29.2 EndY=0.435321 EndZ=0
    g23: LineSegment StartX=29.2 StartY=0.435321 StartZ=0 EndX=29.2 EndY=-0.0646793 EndZ=0
    g24: LineSegment StartX=33.5 StartY=2.67677 StartZ=0 EndX=34.8 EndY=3.50558 EndZ=0
    g25: LineSegment StartX=34.8 StartY=3.50558 StartZ=0 EndX=34.8 EndY=4.00558 EndZ=0
    g26: LineSegment StartX=34.8 StartY=4.00558 StartZ=0 EndX=33.5 EndY=3.17677 EndZ=0
    g27: LineSegment StartX=33.5 StartY=3.17677 StartZ=0 EndX=33.5 EndY=2.67677 EndZ=0
    g28: LineSegment StartX=39.1 StartY=6.24704 StartZ=0 EndX=37.8 EndY=5.41823 EndZ=0
    g29: LineSegment StartX=37.8 StartY=5.41823 StartZ=0 EndX=37.8 EndY=5.91823 EndZ=0
    g30: LineSegment StartX=37.8 StartY=5.91823 StartZ=0 EndX=39.1 EndY=6.74704 EndZ=0
    g31: LineSegment StartX=39.1 StartY=6.74704 StartZ=0 EndX=39.1 EndY=6.24704 EndZ=0
  constraints (80):
    c: Coincident(g0,g-14)
    c: Coincident(g0,g-13)
    c: Coincident(g1,g0)
    c: PointOnObject(g1,g-13)
    c: Coincident(g2,g1)
    c: PointOnObject(g2,g-14)
    c: Coincident(g3,g2)
    c: Coincident(g3,g0)
    c: DistanceY(g3,g3) = 0.5
    c: Parallel(g2,g0)
    c: Coincident(g4,g-12)
    c: Coincident(g4,g-11)
    c: Coincident(g5,g4)
    c: PointOnObject(g5,g-11)
    c: Coincident(g6,g5)
    c: PointOnObject(g6,g-12)
    c: Coincident(g7,g6)
    c: Coincident(g7,g4)
    c: Coincident(g8,g-10)
    c: Coincident(g8,g-9)
    c: Coincident(g9,g8)
    c: PointOnObject(g9,g-9)
    c: Coincident(g10,g9)
    c: PointOnObject(g10,g-10)
    c: Coincident(g11,g10)
    c: Coincident(g11,g8)
    c: Coincident(g12,g-7)
    c: Coincident(g12,g-8)
    c: Coincident(g13,g12)
    c: PointOnObject(g13,g-8)
    c: Coincident(g14,g13)
    c: PointOnObject(g14,g-7)
    c: Coincident(g15,g14)
    c: Coincident(g15,g12)
    c: Parallel(g14,g12)
    c: Parallel(g10,g8)
    c: Parallel(g6,g4)
    c: DistanceY(g7,g7) = 0.5
    c: DistanceY(g11,g11) = 0.5
    c: DistanceY(g13,g13) = 0.5
    c: Coincident(g16,g-16)
    c: Coincident(g16,g-17)
    c: Coincident(g17,g16)
    c: PointOnObject(g17,g-17)
    c: Coincident(g18,g17)
    c: PointOnObject(g18,g-16)
    c: Coincident(g19,g18)
    c: Coincident(g19,g16)
    c: Coincident(g20,g-19)
    c: Coincident(g20,g-20)
    c: Coincident(g21,g20)
    c: PointOnObject(g21,g-20)
    c: Coincident(g22,g21)
    c: PointOnObject(g22,g-19)
    c: Coincident(g23,g22)
    c: Coincident(g23,g20)
    c: Coincident(g24,g-22)
    c: Coincident(g24,g-23)
    c: Coincident(g25,g24)
    c: PointOnObject(g25,g-23)
    c: Coincident(g26,g25)
    c: PointOnObject(g26,g-22)
    c: Coincident(g27,g26)
    c: Coincident(g27,g24)
    c: Coincident(g28,g-26)
    c: Coincident(g28,g-25)
    c: Coincident(g29,g28)
    c: PointOnObject(g29,g-25)
    c: Coincident(g30,g29)
    c: PointOnObject(g30,g-26)
    c: Coincident(g31,g30)
    c: Coincident(g31,g28)
    c: Parallel(g30,g28)
    c: Parallel(g26,g24)
    c: Parallel(g22,g20)
    c: Parallel(g18,g16)
    c: DistanceY(g19,g19) = 0.5
    c: DistanceY(g23,g23) = 0.5
    c: DistanceY(g27,g27) = 0.5
    c: DistanceY(g29,g29) = 0.5
FEATURE [PartDesign::Pocket] Pocket299
  BaseFeature = -> Pocket298
  Direction = (0,0,-1)
  Length = 5
  Length2 = 5
  Profile = -> Sketch681
  ReferenceAxis = -> Sketch681 [N_Axis]
  Refine = true
  Suppressed = false
  Type = 0
FEATURE [Sketcher::SketchObject] Sketch682
  ArcFitTolerance = 1e-06
  AttachmentSupport = -> [Pocket299]
  ExternalGeometry = -> [Pocket299]
  FullyConstrained = true
  MakeInternals = false
  MapMode = 5
  Placement = pos=(0,31.3187,0) rot=(0,0.707107,0.707107;3.14159rad)
  sketch-geometry (4):
    g0: ArcOfCircle CenterX=38.6447 CenterY=-4.8 CenterZ=0 NormalX=0 NormalY=0 NormalZ=1 AngleXU=0 Radius=1 StartAngle=4.71239 EndAngle=7.85398
    g1: ArcOfCircle CenterX=-54.5447 CenterY=-4.8 CenterZ=0 NormalX=0 NormalY=0 NormalZ=1 AngleXU=0 Radius=1 StartAngle=1.5708 EndAngle=4.71239
    g2: LineSegment StartX=-54.5447 StartY=-3.8 StartZ=0 EndX=-54.5447 EndY=-5.8 EndZ=0
    g3: LineSegment StartX=38.6447 StartY=-3.8 StartZ=0 EndX=38.6447 EndY=-5.8 EndZ=0
  constraints (10):
    c: Coincident(g0,g-3)
    c: Coincident(g0,g-3)
    c: PointOnObject(g0,g-3)
    c: Coincident(g1,g-4)
    c: Coincident(g1,g-4)
    c: PointOnObject(g1,g-4)
    c: Coincident(g2,g1)
    c: Coincident(g2,g1)
    c: Coincident(g3,g0)
    c: Coincident(g3,g0)
FEATURE [PartDesign::Pad] Pad476
  BaseFeature = -> Pocket299
  Direction = (0,1,-2e-16)
  Length = 13
  Length2 = 10
  Profile = -> Sketch682
  ReferenceAxis = -> Sketch682 [N_Axis]
  Refine = true
  Reversed = true
  Suppressed = false
  Type = 0
FEATURE [Sketcher::SketchObject] Sketch683
  ArcFitTolerance = 1e-06
  AttachmentSupport = -> [Pad476]
  ExternalGeometry = -> [Pad476]
  FullyConstrained = true
  MakeInternals = false
  MapMode = 5
  Placement = pos=(0,18.3187,0) rot=(1,0,0;1.5708rad)
  sketch-geometry (2):
    g0: Circle CenterX=54.5447 CenterY=-4.8 CenterZ=0 NormalX=0 NormalY=0 NormalZ=1 AngleXU=0 Radius=1.9
    g1: Circle CenterX=-38.6447 CenterY=-4.8 CenterZ=0 NormalX=0 NormalY=0 NormalZ=1 AngleXU=0 Radius=1.9
  constraints (4):
    c: Coincident(g0,g-3)
    c: Diameter(g0) = 3.8
    c: Coincident(g1,g-4)
    c: Diameter(g1) = 3.8
FEATURE [PartDesign::Pad] Pad477
  BaseFeature = -> Pad476
  Direction = (0,-1,2e-16)
  Length = 8
  Length2 = 10
  Profile = -> Sketch683
  ReferenceAxis = -> Sketch683 [N_Axis]
  Refine = true
  Suppressed = false
  Type = 0
FEATURE [PartDesign::Fillet] Fillet020
  Base = -> Pad477 [Edge1280,Edge1248]
  BaseFeature = -> Pad477
  Radius = 1.9
  Refine = true
  SupportTransform = false
  Suppressed = false
  UseAllEdges = false
FEATURE [Sketcher::SketchObject] Sketch684
  ArcFitTolerance = 1e-06
  AttachmentOffset = pos=(0,0,2) rot=(0,0,1;0rad)
  AttachmentSupport = -> [Fillet020]
  ExternalGeometry = -> [Fillet020]
  FullyConstrained = true
  MakeInternals = false
  MapMode = 5
  Placement = pos=(0,20.3187,-4e-16) rot=(0,0.707107,0.707107;3.14159rad)
  sketch-geometry (2):
    g0: Circle CenterX=-54.5447 CenterY=-4.8 CenterZ=0 NormalX=0 NormalY=0 NormalZ=1 AngleXU=0 Radius=1.9
    g1: Circle CenterX=38.6447 CenterY=-4.8 CenterZ=0 NormalX=0 NormalY=0 NormalZ=1 AngleXU=0 Radius=1.9
  constraints (4):
    c: Coincident(g0,g-4)
    c: Equal(g0,g-4)
    c: Coincident(g1,g-3)
    c: Equal(g1,g-3)
FEATURE [PartDesign::Pad] Pad478
  BaseFeature = -> Fillet020
  Direction = (0,1,-2e-16)
  Length = 2.2
  Length2 = 10
  Profile = -> Sketch684
  ReferenceAxis = -> Sketch684 [N_Axis]
  Refine = true
  Suppressed = false
  Type = 0
FEATURE [Sketcher::SketchObject] Sketch685
  ArcFitTolerance = 1e-06
  AttachmentOffset = pos=(0,0,2) rot=(0,0,1;0rad)
  AttachmentSupport = -> [Pad478]
  ExternalGeometry = -> [Pad478]
  FullyConstrained = true
  MakeInternals = false
  MapMode = 5
  Placement = pos=(0,24.5187,-4e-16) rot=(0,0.707107,0.707107;3.14159rad)
  sketch-geometry (2):
    g0: Circle CenterX=38.6447 CenterY=-4.8 CenterZ=0 NormalX=0 NormalY=0 NormalZ=1 AngleXU=0 Radius=1.9
    g1: Circle CenterX=-54.5447 CenterY=-4.8 CenterZ=0 NormalX=0 NormalY=0 NormalZ=1 AngleXU=0 Radius=1.9
  constraints (4):
    c: Coincident(g0,g-3)
    c: Equal(g0,g-3)
    c: Coincident(g1,g-4)
    c: Equal(g1,g-4)
FEATURE [PartDesign::Pad] Pad479
  BaseFeature = -> Pad478
  Direction = (0,1,-2e-16)
  Length = 3
  Length2 = 10
  Profile = -> Sketch685
  ReferenceAxis = -> Sketch685 [N_Axis]
  Refine = true
  Suppressed = false
  Type = 0
FEATURE [Sketcher::SketchObject] Sketch686
  ArcFitTolerance = 1e-06
  AttachmentOffset = pos=(0,0,2) rot=(0,0,1;0rad)
  AttachmentSupport = -> [Pad479]
  ExternalGeometry = -> [Pad479]
  FullyConstrained = true
  MakeInternals = false
  MapMode = 5
  Placement = pos=(0,29.5187,-4e-16) rot=(0,0.707107,0.707107;3.14159rad)
  sketch-geometry (2):
    g0: Circle CenterX=38.6447 CenterY=-4.8 CenterZ=0 NormalX=0 NormalY=0 NormalZ=1 AngleXU=0 Radius=1.9
    g1: Circle CenterX=-54.5447 CenterY=-4.8 CenterZ=0 NormalX=0 NormalY=0 NormalZ=1 AngleXU=0 Radius=1.9
  constraints (4):
    c: Coincident(g0,g-3)
    c: Equal(g0,g-3)
    c: Coincident(g1,g-4)
    c: Equal(g1,g-4)
FEATURE [PartDesign::Pad] Pad480
  BaseFeature = -> Pad479
  Direction = (0,1,-2e-16)
  Length = 3.6
  Length2 = 10
  Profile = -> Sketch686
  ReferenceAxis = -> Sketch686 [N_Axis]
  Refine = true
  Suppressed = false
  Type = 0
FEATURE [Sketcher::SketchObject] Sketch687
  ArcFitTolerance = 1e-06
  AttachmentSupport = -> [Pad480]
  ExternalGeometry = -> [Pad480]
  FullyConstrained = true
  MakeInternals = false
  MapMode = 5
  Placement = pos=(0,33.1187,0) rot=(0,0.707107,0.707107;3.14159rad)
  sketch-geometry (48):
    g0: LineSegment StartX=38.0736 StartY=-2.98786 StartZ=0 EndX=38.0736 EndY=-3.41297 EndZ=0
    g1: LineSegment StartX=38.0736 StartY=-3.41297 StartZ=0 EndX=37.7726 EndY=-3.11197 EndZ=0
    g2: LineSegment StartX=39.2158 StartY=-2.98786 StartZ=0 EndX=39.2158 EndY=-3.41297 EndZ=0
    g3: LineSegment StartX=39.2158 StartY=-3.41297 StartZ=0 EndX=39.5168 EndY=-3.11197 EndZ=0
    g4: LineSegment StartX=40.3309 StartY=-3.92427 StartZ=0 EndX=40.0301 EndY=-4.225 EndZ=0
    g5: LineSegment StartX=40.0301 StartY=-4.225 StartZ=0 EndX=40.4556 EndY=-4.225 EndZ=0
    g6: LineSegment StartX=40.4556 StartY=-5.375 StartZ=0 EndX=40.0301 EndY=-5.375 EndZ=0
    g7: LineSegment StartX=40.0301 StartY=-5.375 StartZ=0 EndX=40.3309 EndY=-5.67573 EndZ=0
    g8: LineSegment StartX=39.5168 StartY=-6.48803 StartZ=0 EndX=39.2158 EndY=-6.18703 EndZ=0
    g9: LineSegment StartX=39.2158 StartY=-6.18703 StartZ=0 EndX=39.2158 EndY=-6.61214 EndZ=0
    g10: LineSegment StartX=38.0736 StartY=-6.61214 StartZ=0 EndX=38.0736 EndY=-6.18703 EndZ=0
    g11: LineSegment StartX=38.0736 StartY=-6.18703 StartZ=0 EndX=37.7726 EndY=-6.48803 EndZ=0
    g12: Circle [constr] CenterX=38.6447 CenterY=-4.8 CenterZ=0 NormalX=0 NormalY=0 NormalZ=1 AngleXU=0 Radius=1.5
    g13: LineSegment [constr] StartX=38.0736 StartY=-2.98786 StartZ=0 EndX=39.2158 EndY=-2.98786 EndZ=0
    g14: LineSegment [constr] StartX=38.0736 StartY=-6.61214 StartZ=0 EndX=39.2158 EndY=-6.61214 EndZ=0
    g15: LineSegment [constr] StartX=39.5168 StartY=-6.48803 StartZ=0 EndX=40.3309 EndY=-5.67573 EndZ=0
    g16: LineSegment [constr] StartX=40.4556 StartY=-5.375 StartZ=0 EndX=40.4556 EndY=-4.225 EndZ=0
    g17: LineSegment [constr] StartX=40.3309 StartY=-3.92427 StartZ=0 EndX=39.5168 EndY=-3.11197 EndZ=0
    g18: ArcOfCircle CenterX=38.6447 CenterY=-4.8 CenterZ=0 NormalX=0 NormalY=0 NormalZ=1 AngleXU=0 Radius=1.9 StartAngle=1.8761 EndAngle=2.04767
    g19: ArcOfCircle CenterX=38.6447 CenterY=-4.8 CenterZ=0 NormalX=0 NormalY=0 NormalZ=1 AngleXU=0 Radius=1.9 StartAngle=1.09393 EndAngle=1.2655
    g20: ArcOfCircle CenterX=38.6447 CenterY=-4.8 CenterZ=0 NormalX=0 NormalY=0 NormalZ=1 AngleXU=0 Radius=1.9 StartAngle=0.307452 EndAngle=0.479022
    g21: ArcOfCircle CenterX=38.6447 CenterY=-4.8 CenterZ=0 NormalX=0 NormalY=0 NormalZ=1 AngleXU=0 Radius=1.9 StartAngle=5.80416 EndAngle=5.97573
    g22: ArcOfCircle CenterX=38.6447 CenterY=-4.8 CenterZ=0 NormalX=0 NormalY=0 NormalZ=1 AngleXU=0 Radius=1.9 StartAngle=5.01769 EndAngle=5.18926
    g23: ArcOfCircle CenterX=38.6447 CenterY=-4.8 CenterZ=0 NormalX=0 NormalY=0 NormalZ=1 AngleXU=0 Radius=1.9 StartAngle=4.23552 EndAngle=4.40709
    g24: Circle [constr] CenterX=-54.5447 CenterY=-4.8 CenterZ=0 NormalX=0 NormalY=0 NormalZ=1 AngleXU=0 Radius=1.5
    g25: LineSegment StartX=-53.9736 StartY=-2.98786 StartZ=0 EndX=-53.9736 EndY=-3.41297 EndZ=0
    g26: LineSegment StartX=-53.9736 StartY=-3.41297 StartZ=0 EndX=-53.6726 EndY=-3.11197 EndZ=0
    g27: LineSegment StartX=-55.1158 StartY=-2.98786 StartZ=0 EndX=-55.1158 EndY=-3.41297 EndZ=0
    g28: LineSegment StartX=-55.1158 StartY=-3.41297 StartZ=0 EndX=-55.4168 EndY=-3.11197 EndZ=0
    g29: LineSegment StartX=-56.2309 StartY=-3.92427 StartZ=0 EndX=-55.9301 EndY=-4.225 EndZ=0
    g30: LineSegment StartX=-55.9301 StartY=-4.225 StartZ=0 EndX=-56.3556 EndY=-4.225 EndZ=0
    g31: LineSegment StartX=-56.3556 StartY=-5.375 StartZ=0 EndX=-55.9301 EndY=-5.375 EndZ=0
    g32: LineSegment StartX=-55.9301 StartY=-5.375 StartZ=0 EndX=-56.2309 EndY=-5.67573 EndZ=0
    g33: LineSegment [constr] StartX=-55.9301 StartY=-4.225 StartZ=0 EndX=-55.1158 EndY=-3.41297 EndZ=0
    g34: LineSegment [constr] StartX=-55.1158 StartY=-3.41297 StartZ=0 EndX=-53.9736 EndY=-3.41297 EndZ=0
    g35: LineSegment [constr] StartX=-55.9301 StartY=-4.225 StartZ=0 EndX=-55.9301 EndY=-5.375 EndZ=0
    g36: LineSegment StartX=-55.4168 StartY=-6.48803 StartZ=0 EndX=-55.1158 EndY=-6.18703 EndZ=0
    g37: LineSegment StartX=-55.1158 StartY=-6.18703 StartZ=0 EndX=-55.1158 EndY=-6.61214 EndZ=0
    g38: LineSegment StartX=-53.9736 StartY=-6.61214 StartZ=0 EndX=-53.9736 EndY=-6.18703 EndZ=0
    g39: LineSegment StartX=-53.9736 StartY=-6.18703 StartZ=0 EndX=-53.6726 EndY=-6.48803 EndZ=0
    g40: LineSegment [constr] StartX=-55.9301 StartY=-5.375 StartZ=0 EndX=-55.1158 EndY=-6.18703 EndZ=0
    g41: LineSegment [constr] StartX=-55.1158 StartY=-6.18703 StartZ=0 EndX=-53.9736 EndY=-6.18703 EndZ=0
    g42: ArcOfCircle CenterX=-54.5447 CenterY=-4.8 CenterZ=0 NormalX=0 NormalY=0 NormalZ=1 AngleXU=0 Radius=1.9 StartAngle=1.09393 EndAngle=1.2655
    g43: ArcOfCircle CenterX=-54.5447 CenterY=-4.8 CenterZ=0 NormalX=0 NormalY=0 NormalZ=1 AngleXU=0 Radius=1.9 StartAngle=1.8761 EndAngle=2.04767
    g44: ArcOfCircle CenterX=-54.5447 CenterY=-4.8 CenterZ=0 NormalX=0 NormalY=0 NormalZ=1 AngleXU=0 Radius=1.9 StartAngle=2.66257 EndAngle=2.83414
    g45: ArcOfCircle CenterX=-54.5447 CenterY=-4.8 CenterZ=0 NormalX=0 NormalY=0 NormalZ=1 AngleXU=0 Radius=1.9 StartAngle=3.44905 EndAngle=3.62061
    g46: ArcOfCircle CenterX=-54.5447 CenterY=-4.8 CenterZ=0 NormalX=0 NormalY=0 NormalZ=1 AngleXU=0 Radius=1.9 StartAngle=4.23552 EndAngle=4.40709
    g47: ArcOfCircle CenterX=-54.5447 CenterY=-4.8 CenterZ=0 NormalX=0 NormalY=0 NormalZ=1 AngleXU=0 Radius=1.9 StartAngle=5.01769 EndAngle=5.18926
  constraints (145):
    c: PointOnObject(g0,g-3)
    c: Coincident(g1,g0)
    c: PointOnObject(g1,g-3)
    c: PointOnObject(g2,g-3)
    c: Coincident(g3,g2)
    c: PointOnObject(g3,g-3)
    c: PointOnObject(g4,g-3)
    c: Coincident(g5,g4)
    c: PointOnObject(g5,g-3)
    c: PointOnObject(g6,g-3)
    c: Coincident(g7,g6)
    c: PointOnObject(g7,g-3)
    c: Horizontal(g6)
    c: Horizontal(g5)
    c: Vertical(g2)
    c: Vertical(g0)
    c: Angle(g3,g2) = 0.785398
    c: Angle(g5,g4) = 0.785398
    c: Angle(g0,g1) = 0.785398
    c: Angle(g7,g6) = 0.785398
    c: PointOnObject(g8,g-3)
    c: Coincident(g9,g8)
    c: PointOnObject(g9,g-3)
    c: Vertical(g9)
    c: PointOnObject(g10,g-3)
    c: Vertical(g10)
    c: Coincident(g11,g10)
    c: PointOnObject(g11,g-3)
    c: Angle(g11,g10) = 0.785398
    c: Angle(g9,g8) = 0.785398
    c: Coincident(g12,g-3)
    c: Radius(g12) = 1.5
    c: PointOnObject(g8,g12)
    c: PointOnObject(g10,g12)
    c: PointOnObject(g6,g12)
    c: PointOnObject(g4,g12)
    c: PointOnObject(g2,g12)
    c: PointOnObject(g0,g12)
    c: Coincident(g13,g0)
    c: Coincident(g13,g2)
    c: Horizontal(g13)
    c: Coincident(g14,g10)
    c: Coincident(g14,g9)
    c: Horizontal(g14)
    c: Coincident(g15,g8)
    c: Coincident(g15,g7)
    c: Coincident(g16,g6)
    c: Coincident(g16,g5)
    c: Vertical(g16)
    c: Coincident(g17,g4)
    c: Coincident(g17,g3)
    c: Distance(g17) = 1.15
    c: Distance(g16) = 1.15
    c: Distance(g7,g8) = 1.15
    c: DistanceX(g14,g14) = 1.1422
    c: Coincident(g18,g1)
    c: Coincident(g18,g0)
    c: Tangent(g18,g-3)
    c: Coincident(g19,g2)
    c: Coincident(g19,g3)
    c: Tangent(g19,g-3)
    c: Coincident(g20,g4)
    c: Coincident(g20,g5)
    c: Tangent(g20,g-3)
    c: Coincident(g21,g6)
    c: Coincident(g21,g7)
    c: Tangent(g21,g-3)
    c: Coincident(g22,g8)
    c: Coincident(g22,g9)
    c: Tangent(g22,g-3)
    c: Coincident(g23,g10)
    c: Coincident(g23,g11)
    c: Tangent(g23,g-3)
    c: Coincident(g24,g-4)
    c: Radius(g24) = 1.5
    c: PointOnObject(g25,g-4)
    c: PointOnObject(g25,g24)
    c: Vertical(g25)
    c: Coincident(g26,g25)
    c: PointOnObject(g26,g-4)
    c: PointOnObject(g27,g-4)
    c: PointOnObject(g27,g24)
    c: Vertical(g27)
    c: Coincident(g28,g27)
    c: PointOnObject(g28,g-4)
    c: PointOnObject(g29,g-4)
    c: PointOnObject(g29,g24)
    c: Coincident(g30,g29)
    c: PointOnObject(g30,g-4)
    c: PointOnObject(g31,g-4)
    c: PointOnObject(g31,g24)
    c: Coincident(g32,g31)
    c: PointOnObject(g32,g-4)
    c: Angle(g26,g25) = 0.785398
    c: Angle(g27,g28) = 0.785398
    c: Angle(g29,g30) = 0.785398
    c: Coincident(g33,g29)
    c: Coincident(g33,g27)
    c: Coincident(g34,g27)
    c: Coincident(g34,g25)
    c: Coincident(g35,g29)
    c: Coincident(g35,g31)
    c: Horizontal(g30)
    c: Horizontal(g31)
    c: Angle(g31,g32) = 0.785398
    c: Vertical(g35)
    c: Horizontal(g34)
    c: Distance(g33) = 1.15
    c: Distance(g35) = 1.15
    c: PointOnObject(g36,g-4)
    c: PointOnObject(g36,g24)
    c: Coincident(g37,g36)
    c: PointOnObject(g37,g-4)
    c: PointOnObject(g38,g-4)
    c: PointOnObject(g38,g24)
    c: Coincident(g39,g38)
    c: PointOnObject(g39,g-4)
    c: Vertical(g37)
    c: Vertical(g38)
    c: Angle(g36,g37) = 0.785398
    c: Angle(g38,g39) = 0.785398
    c: Coincident(g40,g31)
    c: Coincident(g40,g36)
    c: Coincident(g41,g36)
    c: Coincident(g41,g38)
    c: Horizontal(g41)
    c: Distance(g40) = 1.15
    c: Coincident(g42,g26)
    c: Coincident(g42,g25)
    c: Tangent(g42,g-4)
    c: Coincident(g43,g27)
    c: Coincident(g43,g28)
    c: Tangent(g43,g-4)
    c: Coincident(g44,g29)
    c: Coincident(g44,g30)
    c: Tangent(g44,g-4)
    c: Coincident(g45,g31)
    c: Coincident(g45,g32)
    c: Tangent(g45,g-4)
    c: Coincident(g46,g36)
    c: Coincident(g46,g37)
    c: Tangent(g46,g-4)
    c: Coincident(g47,g38)
    c: Coincident(g47,g39)
    c: Tangent(g47,g-4)
FEATURE [PartDesign::Pocket] Pocket300
  BaseFeature = -> Pad480
  Direction = (0,-1,2e-16)
  Length = 5
  Length2 = 5
  Profile = -> Sketch687
  ReferenceAxis = -> Sketch687 [N_Axis]
  Refine = true
  Suppressed = false
  Type = 0
FEATURE [PartDesign::Fillet] Fillet021
  Base = -> Pocket300 [Edge191,Edge558,Edge559,Edge561,Edge562,Edge564,Edge566,Edge567,Edge568,Edge570,Edge571,Edge189,Edge823,Edge819,Edge817,Edge813,Edge811,Edge807,Edge805,Edge801,Edge799,Edge795,Edge793,Edge790]
  BaseFeature = -> Pocket300
  Radius = 0.5
  Refine = true
  SupportTransform = false
  Suppressed = false
  UseAllEdges = false
FEATURE [Sketcher::SketchObject] Sketch688
  ArcFitTolerance = 1e-06
  AttachmentSupport = -> [Fillet021]
  ExternalGeometry = -> [Fillet021]
  FullyConstrained = true
  MakeInternals = false
  MapMode = 5
  Placement = pos=(0,0,-4.8) rot=(1,0,0;3.14159rad)
  sketch-geometry (4):
    g0: LineSegment StartX=3.65 StartY=-12.8 StartZ=0 EndX=12.25 EndY=-12.8 EndZ=0
    g1: LineSegment StartX=12.25 StartY=-12.8 StartZ=0 EndX=11.5221 EndY=-14.8 EndZ=0
    g2: LineSegment StartX=11.5221 StartY=-14.8 StartZ=0 EndX=4.37794 EndY=-14.8 EndZ=0
    g3: LineSegment StartX=4.37794 StartY=-14.8 StartZ=0 EndX=3.65 EndY=-12.8 EndZ=0
  constraints (12):
    c: PointOnObject(g0,g-6)
    c: PointOnObject(g0,g-6)
    c: Coincident(g1,g0)
    c: Coincident(g2,g1)
    c: Horizontal(g2)
    c: Coincident(g3,g2)
    c: Coincident(g3,g0)
    c: DistanceY(g-4,g2) = 1.5
    c: Angle(g-6,g1) = 1.22173
    c: Angle(g3,g0) = 1.22173
    c: DistanceX(g-4,g0) = 1.5
    c: DistanceX(g0,g-5) = 1.5
FEATURE [PartDesign::Pocket] Pocket301
  BaseFeature = -> Fillet021
  Direction = (0,0,1)
  Length = 5
  Length2 = 5
  Profile = -> Sketch688
  ReferenceAxis = -> Sketch688 [N_Axis]
  Refine = true
  Suppressed = false
  Type = 0
FEATURE [Sketcher::SketchObject] Sketch689
  ArcFitTolerance = 1e-06
  AttachmentSupport = -> [Pocket301]
  ExternalGeometry = -> [Pocket301]
  FullyConstrained = true
  MakeInternals = false
  MapMode = 5
  Placement = pos=(0,0,2.7) rot=(1,0,0;3.14159rad)
  sketch-geometry (2):
    g0: Circle CenterX=12.5 CenterY=-9.8 CenterZ=0 NormalX=0 NormalY=0 NormalZ=1 AngleXU=0 Radius=1.6
    g1: Circle CenterX=12.5 CenterY=-9.8 CenterZ=0 NormalX=0 NormalY=0 NormalZ=1 AngleXU=0 Radius=2.4
  constraints (5):
    c: Radius(g0) = 1.6
    c: DistanceX(g0,g-3) = 1.95
    c: DistanceY(g-3,g0) = 3
    c: Coincident(g1,g0)
    c: Radius(g1) = 2.4
FEATURE [PartDesign::Pad] Pad481
  BaseFeature = -> Pocket301
  Direction = (0,0,-1)
  Length = 11.8
  Length2 = 10
  Profile = -> Sketch689
  ReferenceAxis = -> Sketch689 [N_Axis]
  Refine = true
  Suppressed = false
  Type = 0
FEATURE [PartDesign::Pad] Pad482
  BaseFeature = -> Pad481
  Direction = (0,0,-1)
  Length = 5
  Length2 = 10
  Profile = -> Pad481 [Face551]
  Refine = true
  Suppressed = false
  Type = 0
FEATURE [Sketcher::SketchObject] Sketch690
  ArcFitTolerance = 1e-06
  AttachmentSupport = -> [Pad482]
  ExternalGeometry = -> [Pad482]
  FullyConstrained = true
  MakeInternals = false
  MapMode = 5
  Placement = pos=(0,0,-5.8) rot=(1,0,0;3.14159rad)
  sketch-geometry (5):
    g0: LineSegment StartX=-13.5874 StartY=-22.2534 StartZ=0 EndX=-13.5874 EndY=-16.2534 EndZ=0
    g1: LineSegment StartX=-13.5874 StartY=-16.2534 StartZ=0 EndX=-15.5874 EndY=-16.2534 EndZ=0
    g2: LineSegment StartX=-15.5874 StartY=-16.2534 StartZ=0 EndX=-15.5874 EndY=-22.2534 EndZ=0
    g3: LineSegment StartX=-15.5874 StartY=-22.2534 StartZ=0 EndX=-13.5874 EndY=-22.2534 EndZ=0
    g4: LineSegment [constr] StartX=-13.5874 StartY=-23.2534 StartZ=0 EndX=-13.5874 EndY=-22.2534 EndZ=0
  constraints (14):
    c: Coincident(g0,g1)
    c: Coincident(g1,g2)
    c: Coincident(g2,g3)
    c: Coincident(g3,g0)
    c: Vertical(g0)
    c: Vertical(g2)
    c: Horizontal(g1)
    c: Horizontal(g3)
    c: DistanceY(g2,g2) = 6
    c: DistanceX(g3,g3) = 2
    c: Coincident(g4,g-3)
    c: Coincident(g4,g0)
    c: Vertical(g4)
    c: DistanceY(g4,g4) = 1
FEATURE [PartDesign::Pad] Pad483
  BaseFeature = -> Pad482
  Direction = (0,0,-1)
  Length = 1.65
  Length2 = 10
  Profile = -> Sketch690
  ReferenceAxis = -> Sketch690 [N_Axis]
  Refine = true
  Suppressed = false
  Type = 0
FEATURE [Sketcher::SketchObject] Sketch691
  ArcFitTolerance = 1e-06
  AttachmentSupport = -> [Pad483]
  ExternalGeometry = -> [Pad483]
  FullyConstrained = true
  MakeInternals = false
  MapMode = 5
  Placement = pos=(0,0,-7.45) rot=(1,0,0;3.14159rad)
  sketch-geometry (8):
    g0: LineSegment StartX=-13.5874 StartY=-16.2534 StartZ=0 EndX=-15.5874 EndY=-16.2534 EndZ=0
    g1: LineSegment StartX=-15.5874 StartY=-16.2534 StartZ=0 EndX=-15.5874 EndY=-18.0034 EndZ=0
    g2: LineSegment StartX=-15.5874 StartY=-18.0034 StartZ=0 EndX=-13.5874 EndY=-18.0034 EndZ=0
    g3: LineSegment StartX=-13.5874 StartY=-18.0034 StartZ=0 EndX=-13.5874 EndY=-16.2534 EndZ=0
    g4: LineSegment StartX=-13.5874 StartY=-22.2534 StartZ=0 EndX=-13.5874 EndY=-20.1034 EndZ=0
    g5: LineSegment StartX=-13.5874 StartY=-20.1034 StartZ=0 EndX=-15.5874 EndY=-20.1034 EndZ=0
    g6: LineSegment StartX=-15.5874 StartY=-20.1034 StartZ=0 EndX=-15.5874 EndY=-22.2534 EndZ=0
    g7: LineSegment StartX=-15.5874 StartY=-22.2534 StartZ=0 EndX=-13.5874 EndY=-22.2534 EndZ=0
  constraints (22):
    c: Coincident(g0,g1)
    c: Coincident(g1,g2)
    c: Coincident(g2,g3)
    c: Coincident(g3,g0)
    c: Horizontal(g0)
    c: Horizontal(g2)
    c: Vertical(g1)
    c: Vertical(g3)
    c: Coincident(g0,g-6)
    c: PointOnObject(g1,g-5)
    c: Coincident(g4,g5)
    c: Coincident(g5,g6)
    c: Coincident(g6,g7)
    c: Coincident(g7,g4)
    c: Vertical(g4)
    c: Vertical(g6)
    c: Horizontal(g5)
    c: Horizontal(g7)
    c: Coincident(g4,g-4)
    c: PointOnObject(g5,g-5)
    c: DistanceY(g6,g6) = 2.15
    c: DistanceY(g3,g3) = 1.75
FEATURE [PartDesign::Pad] Pad484
  BaseFeature = -> Pad483
  Direction = (0,0,-1)
  Length = 2.2
  Length2 = 10
  Profile = -> Sketch691
  ReferenceAxis = -> Sketch691 [N_Axis]
  Refine = true
  Suppressed = false
  Type = 0
FEATURE [Sketcher::SketchObject] Sketch692
  ArcFitTolerance = 1e-06
  AttachmentSupport = -> [Pad484]
  ExternalGeometry = -> [Pad484]
  FullyConstrained = true
  MakeInternals = false
  MapMode = 5
  Placement = pos=(0,0,-5.8) rot=(1,0,0;3.14159rad)
  sketch-geometry (5):
    g0: ArcOfCircle CenterX=39.1 CenterY=-19.747 CenterZ=0 NormalX=0 NormalY=0 NormalZ=1 AngleXU=0 Radius=1 StartAngle=3.14159 EndAngle=6.28319
    g1: ArcOfCircle CenterX=39.1 CenterY=-11.747 CenterZ=0 NormalX=0 NormalY=0 NormalZ=1 AngleXU=0 Radius=1 StartAngle=-4.4e-15 EndAngle=3.14159
    g2: LineSegment StartX=38.1 StartY=-19.747 StartZ=0 EndX=38.1 EndY=-11.747 EndZ=0
    g3: LineSegment StartX=40.1 StartY=-19.747 StartZ=0 EndX=40.1 EndY=-11.747 EndZ=0
    g4: LineSegment [constr] StartX=39.1 StartY=-6.24704 StartZ=0 EndX=39.1 EndY=-11.747 EndZ=0
  constraints (12):
    c: Tangent(g0,g2) = 1.5708
    c: Tangent(g0,g3) = -1.5708
    c: Tangent(g1,g2) = 1.5708
    c: Tangent(g1,g3) = -1.5708
    c: Equal(g0,g1)
    c: Vertical(g2)
    c: Diameter(g0) = 2
    c: DistanceY(g0,g1) = 8
    c: Coincident(g4,g-3)
    c: Coincident(g4,g1)
    c: Vertical(g4)
    c: DistanceY(g4,g4) = 5.5
FEATURE [PartDesign::Pad] Pad485
  BaseFeature = -> Pad484
  Direction = (0,0,-1)
  Length = 2.2
  Length2 = 10
  Profile = -> Sketch692
  ReferenceAxis = -> Sketch692 [N_Axis]
  Refine = true
  Suppressed = false
  Type = 0
FEATURE [Sketcher::SketchObject] Sketch693
  ArcFitTolerance = 1e-06
  AttachmentSupport = -> [Pad485]
  ExternalGeometry = -> [Pad485]
  FullyConstrained = true
  MakeInternals = false
  MapMode = 5
  Placement = pos=(0,0,-5.8) rot=(1,0,0;3.14159rad)
  sketch-geometry (4):
    g0: Circle CenterX=3.25 CenterY=1.25 CenterZ=0 NormalX=0 NormalY=0 NormalZ=1 AngleXU=0 Radius=1.3
    g1: Circle CenterX=3.25 CenterY=1.25 CenterZ=0 NormalX=0 NormalY=0 NormalZ=1 AngleXU=0 Radius=2.1
    g2: Circle CenterX=13 CenterY=-3 CenterZ=0 NormalX=0 NormalY=0 NormalZ=1 AngleXU=0 Radius=1.8
    g3: Circle CenterX=13 CenterY=-3 CenterZ=0 NormalX=0 NormalY=0 NormalZ=1 AngleXU=0 Radius=2.5
  constraints (10):
    c: Coincident(g1,g0)
    c: Coincident(g3,g2)
    c: Radius(g0) = 1.3
    c: Radius(g1) = 2.1
    c: DistanceY(g0,g-3) = 0.65
    c: DistanceX(g-3,g0) = 4
    c: DistanceX(g-3,g2) = 13.75
    c: Radius(g2) = 1.8
    c: Radius(g3) = 2.5
    c: DistanceY(g2,g-3) = 4.9
FEATURE [PartDesign::Pad] Pad486
  BaseFeature = -> Pad485
  Direction = (0,0,-1)
  Length = 9
  Length2 = 10
  Profile = -> Sketch693
  ReferenceAxis = -> Sketch693 [N_Axis]
  Refine = true
  Reversed = true
  Suppressed = false
  Type = 0
FEATURE [PartDesign::Pocket] Pocket302
  BaseFeature = -> Pad486
  Direction = (0,0,-1)
  Length = 3.2
  Length2 = 5
  Profile = -> Pad486 [Face362]
  Refine = true
  Suppressed = false
  Type = 0
FEATURE [PartDesign::Pad] Pad487
  BaseFeature = -> Pocket302
  Direction = (0,0,-1)
  Length = 3.3
  Length2 = 10
  Profile = -> Pocket302 [Face449]
  Refine = true
  Suppressed = false
  Type = 0
FEATURE [Sketcher::SketchObject] Sketch694
  ArcFitTolerance = 1e-06
  AttachmentSupport = -> [Pad487]
  ExternalGeometry = -> [Pad487]
  FullyConstrained = true
  MakeInternals = false
  MapMode = 5
  Placement = pos=(0,0,-5.8) rot=(1,0,0;3.14159rad)
  sketch-geometry (1):
    g0: Circle CenterX=3.25 CenterY=1.25 CenterZ=0 NormalX=0 NormalY=0 NormalZ=1 AngleXU=0 Radius=1.30001
  constraints (2):
    c: Coincident(g0,g-3)
    c: Tangent(g0,g-3)
FEATURE [PartDesign::Pocket] Pocket303
  BaseFeature = -> Pad487
  Direction = (0,0,1)
  Length = 7
  Length2 = 5
  Profile = -> Sketch694
  ReferenceAxis = -> Sketch694 [N_Axis]
  Refine = true
  Suppressed = false
  Type = 0
FEATURE [Sketcher::SketchObject] Sketch695
  ArcFitTolerance = 1e-06
  AttachmentSupport = -> [Pocket303]
  ExternalGeometry = -> [Pocket303]
  FullyConstrained = true
  MakeInternals = false
  MapMode = 5
  Placement = pos=(0,0,2.7) rot=(1,0,0;3.14159rad)
  sketch-geometry (1):
    g0: Circle CenterX=13 CenterY=-3 CenterZ=0 NormalX=0 NormalY=0 NormalZ=1 AngleXU=0 Radius=1.8
  constraints (2):
    c: Coincident(g0,g-3)
    c: Equal(g0,g-3)
FEATURE [PartDesign::Pad] Pad488
  BaseFeature = -> Pocket303
  Direction = (0,0,-1)
  Length = 5
  Length2 = 10
  Profile = -> Sketch695
  ReferenceAxis = -> Sketch695 [N_Axis]
  Refine = true
  Suppressed = false
  Type = 0
FEATURE [PartDesign::Pocket] Pocket304
  BaseFeature = -> Pad488
  Direction = (0,0,1)
  Length = 0.4
  Length2 = 5
  Profile = -> Pad488 [Face491]
  Refine = true
  Suppressed = false
  Type = 0
FEATURE [Sketcher::SketchObject] Sketch709
  ArcFitTolerance = 1e-06
  AttachmentSupport = -> [XY_Plane039]
  FullyConstrained = true
  MakeInternals = false
  MapMode = 5
  sketch-geometry (8):
    g0: LineSegment StartX=0 StartY=24 StartZ=0 EndX=0 EndY=0 EndZ=0
    g1: LineSegment StartX=0 StartY=0 StartZ=0 EndX=9 EndY=0 EndZ=0
    g2: LineSegment StartX=9 StartY=0 StartZ=0 EndX=9 EndY=10 EndZ=0
    g3: LineSegment StartX=9 StartY=10 StartZ=0 EndX=25 EndY=10 EndZ=0
    g4: LineSegment StartX=25 StartY=10 StartZ=0 EndX=25 EndY=0 EndZ=0
    g5: LineSegment StartX=25 StartY=0 StartZ=0 EndX=34 EndY=0 EndZ=0
    g6: LineSegment StartX=34 StartY=0 StartZ=0 EndX=34 EndY=24 EndZ=0
    g7: LineSegment StartX=34 StartY=24 StartZ=0 EndX=0 EndY=24 EndZ=0
  constraints (23):
    c: PointOnObject(g0,g-2)
    c: Coincident(g0,g-1)
    c: Coincident(g1,g0)
    c: PointOnObject(g1,g-1)
    c: Coincident(g2,g1)
    c: Vertical(g2)
    c: Coincident(g3,g2)
    c: Horizontal(g3)
    c: Coincident(g4,g3)
    c: PointOnObject(g4,g-1)
    c: Vertical(g4)
    c: Coincident(g5,g4)
    c: PointOnObject(g5,g-1)
    c: Coincident(g6,g5)
    c: Vertical(g6)
    c: Coincident(g7,g6)
    c: Coincident(g7,g0)
    c: Horizontal(g7)
    c: DistanceX(g7,g7) = 34
    c: DistanceY(g0,g0) = 24
    c: DistanceX(g1,g1) = 9
    c: DistanceX(g5,g5) = 9
    c: DistanceY(g2,g0) = 14
FEATURE [PartDesign::Pad] Pad490
  Direction = (0,0,1)
  Length = 2.25
  Length2 = 10
  Profile = -> Sketch709
  ReferenceAxis = -> Sketch709 [N_Axis]
  Refine = true
  Suppressed = false
  Type = 0
FEATURE [Sketcher::SketchObject] Sketch710
  ArcFitTolerance = 1e-06
  AttachmentSupport = -> [Pad490]
  ExternalGeometry = -> [Pad490]
  FullyConstrained = true
  MakeInternals = false
  MapMode = 5
  Placement = pos=(0,0,2.25) rot=(0,0,1;0rad)
  sketch-geometry (7):
    g0: Circle CenterX=29 CenterY=11.2 CenterZ=0 NormalX=0 NormalY=0 NormalZ=1 AngleXU=0 Radius=2.55
    g1: Circle CenterX=5.1 CenterY=4.75 CenterZ=0 NormalX=0 NormalY=0 NormalZ=1 AngleXU=0 Radius=2.7
    g2: Circle CenterX=29 CenterY=11.2 CenterZ=0 NormalX=0 NormalY=0 NormalZ=1 AngleXU=0 Radius=4
    g3: LineSegment [constr] StartX=5.1 StartY=4.75 StartZ=0 EndX=5.1 EndY=2.05 EndZ=0
    g4: LineSegment [constr] StartX=5.1 StartY=4.75 StartZ=0 EndX=2.4 EndY=4.75 EndZ=0
    g5: LineSegment [constr] StartX=29 StartY=11.2 StartZ=0 EndX=29 EndY=7.2 EndZ=0
    g6: LineSegment [constr] StartX=29 StartY=11.2 StartZ=0 EndX=33 EndY=11.2 EndZ=0
  constraints (20):
    c: Coincident(g2,g0)
    c: Diameter(g2) = 8
    c: Diameter(g0) = 5.1
    c: Diameter(g1) = 5.4
    c: Coincident(g3,g1)
    c: PointOnObject(g3,g1)
    c: Vertical(g3)
    c: DistanceY(g-1,g3) = 2.05
    c: Coincident(g4,g1)
    c: PointOnObject(g4,g1)
    c: Horizontal(g4)
    c: DistanceX(g-1,g4) = 2.4
    c: Coincident(g5,g0)
    c: PointOnObject(g5,g2)
    c: Vertical(g5)
    c: DistanceY(g-4,g5) = 7.2
    c: Coincident(g6,g0)
    c: PointOnObject(g6,g2)
    c: Horizontal(g6)
    c: DistanceX(g6,g-3) = 1
FEATURE [PartDesign::Pad] Pad491
  BaseFeature = -> Pad490
  Direction = (0,0,1)
  Length = 4.5
  Length2 = 10
  Profile = -> Sketch710
  ReferenceAxis = -> Sketch710 [N_Axis]
  Refine = true
  Suppressed = false
  Type = 0
FEATURE [Sketcher::SketchObject] Sketch711
  ArcFitTolerance = 1e-06
  AttachmentSupport = -> [Pad491]
  ExternalGeometry = -> [Pad491]
  FullyConstrained = true
  MakeInternals = false
  MapMode = 5
  Placement = pos=(0,0,0) rot=(1,0,0;3.14159rad)
  sketch-geometry (4):
    g0: LineSegment StartX=34 StartY=-24 StartZ=0 EndX=34 EndY=-22 EndZ=0
    g1: LineSegment StartX=34 StartY=-22 StartZ=0 EndX=0 EndY=-22 EndZ=0
    g2: LineSegment StartX=0 StartY=-22 StartZ=0 EndX=0 EndY=-24 EndZ=0
    g3: LineSegment StartX=0 StartY=-24 StartZ=0 EndX=34 EndY=-24 EndZ=0
  constraints (11):
    c: Coincident(g0,g1)
    c: Coincident(g1,g2)
    c: Coincident(g2,g3)
    c: Coincident(g3,g0)
    c: Vertical(g0)
    c: Vertical(g2)
    c: Horizontal(g1)
    c: Horizontal(g3)
    c: Coincident(g0,g-4)
    c: PointOnObject(g1,g-5)
    c: DistanceY(g2,g2) = 2
FEATURE [PartDesign::Pad] Pad492
  BaseFeature = -> Pad491
  Direction = (0,0,-1)
  Length = 12.6
  Length2 = 10
  Profile = -> Sketch711
  ReferenceAxis = -> Sketch711 [N_Axis]
  Refine = true
  Suppressed = false
  Type = 0
FEATURE [Sketcher::SketchObject] Sketch712
  ArcFitTolerance = 1e-06
  AttachmentSupport = -> [Pad492]
  ExternalGeometry = -> [Pad492]
  FullyConstrained = true
  MakeInternals = false
  MapMode = 5
  Placement = pos=(0,0,-12.6) rot=(1,0,0;3.14159rad)
  sketch-geometry (10):
    g0: LineSegment StartX=34 StartY=-24 StartZ=0 EndX=34 EndY=-8.3 EndZ=0
    g1: LineSegment StartX=34 StartY=-8.3 StartZ=0 EndX=25 EndY=-8.3 EndZ=0
    g2: LineSegment StartX=25 StartY=-8.3 StartZ=0 EndX=25 EndY=-16.3 EndZ=0
    g3: LineSegment StartX=25 StartY=-16.3 StartZ=0 EndX=9 EndY=-16.3 EndZ=0
    g4: LineSegment StartX=9 StartY=-16.3 StartZ=0 EndX=9 EndY=-8.3 EndZ=0
    g5: LineSegment StartX=9 StartY=-8.3 StartZ=0 EndX=1.8e-15 EndY=-8.3 EndZ=0
    g6: LineSegment StartX=1.8e-15 StartY=-8.3 StartZ=0 EndX=1.8e-15 EndY=-22 EndZ=0
    g7: LineSegment StartX=1.8e-15 StartY=-22 StartZ=0 EndX=5.1 EndY=-22 EndZ=0
    g8: LineSegment StartX=5.1 StartY=-22 StartZ=0 EndX=5.1 EndY=-24 EndZ=0
    g9: LineSegment StartX=5.1 StartY=-24 StartZ=0 EndX=34 EndY=-24 EndZ=0
  constraints (29):
    c: Coincident(g0,g-4)
    c: Vertical(g0)
    c: DistanceY(g0,g0) = 15.7
    c: Coincident(g1,g0)
    c: Horizontal(g1)
    c: Coincident(g2,g1)
    c: Vertical(g2)
    c: Coincident(g3,g2)
    c: Horizontal(g3)
    c: Coincident(g4,g3)
    c: Vertical(g4)
    c: Coincident(g5,g4)
    c: Horizontal(g5)
    c: Coincident(g6,g5)
    c: Coincident(g7,g6)
    c: Horizontal(g7)
    c: Coincident(g8,g7)
    c: PointOnObject(g8,g-4)
    c: Vertical(g8)
    c: Coincident(g9,g8)
    c: Coincident(g9,g0)
    c: DistanceX(g1,g1) = 9
    c: DistanceX(g5,g5) = 9
    c: DistanceX(g3,g3) = 16
    c: Vertical(g6)
    c: DistanceY(g2,g2) = 8
    c: DistanceY(g4,g4) = 8
    c: DistanceY(g6,g6) = 13.7
    c: DistanceX(g7,g7) = 5.1
FEATURE [PartDesign::Pad] Pad493
  BaseFeature = -> Pad492
  Direction = (0,0,-1)
  Length = 2
  Length2 = 10
  Profile = -> Sketch712
  ReferenceAxis = -> Sketch712 [N_Axis]
  Refine = true
  Suppressed = false
  Type = 0
FEATURE [PartDesign::Pocket] Pocket316
  BaseFeature = -> Pad493
  Direction = (0,0,1)
  Length = 12.6
  Length2 = 5
  Profile = -> Pad493 [Face6]
  Refine = true
  Suppressed = false
  Type = 0
FEATURE [Sketcher::SketchObject] Sketch713
  ArcFitTolerance = 1e-06
  AttachmentSupport = -> [Pocket316]
  ExternalGeometry = -> [Pocket316]
  FullyConstrained = true
  MakeInternals = false
  MapMode = 5
  Placement = pos=(0,24,0) rot=(0,0.707107,0.707107;3.14159rad)
  sketch-geometry (12):
    g0: LineSegment StartX=-29.1 StartY=2.25 StartZ=0 EndX=-29.1 EndY=-14.6 EndZ=0
    g1: LineSegment StartX=-29.1 StartY=-14.6 StartZ=0 EndX=-26.1 EndY=-14.6 EndZ=0
    g2: LineSegment StartX=-26.1 StartY=-14.6 StartZ=0 EndX=-26.1 EndY=2.25 EndZ=0
    g3: LineSegment StartX=-26.1 StartY=2.25 StartZ=0 EndX=-29.1 EndY=2.25 EndZ=0
    g4: LineSegment StartX=-21.1 StartY=2.25 StartZ=0 EndX=-21.1 EndY=-14.6 EndZ=0
    g5: LineSegment StartX=-21.1 StartY=-14.6 StartZ=0 EndX=-18.1 EndY=-14.6 EndZ=0
    g6: LineSegment StartX=-18.1 StartY=-14.6 StartZ=0 EndX=-18.1 EndY=2.25 EndZ=0
    g7: LineSegment StartX=-18.1 StartY=2.25 StartZ=0 EndX=-21.1 EndY=2.25 EndZ=0
    g8: LineSegment StartX=-13.1 StartY=2.25 StartZ=0 EndX=-13.1 EndY=-14.6 EndZ=0
    g9: LineSegment StartX=-13.1 StartY=-14.6 StartZ=0 EndX=-10.1 EndY=-14.6 EndZ=0
    g10: LineSegment StartX=-10.1 StartY=-14.6 StartZ=0 EndX=-10.1 EndY=2.25 EndZ=0
    g11: LineSegment StartX=-10.1 StartY=2.25 StartZ=0 EndX=-13.1 EndY=2.25 EndZ=0
  constraints (38):
    c: Coincident(g0,g1)
    c: Coincident(g1,g2)
    c: Coincident(g2,g3)
    c: Coincident(g3,g0)
    c: Vertical(g0)
    c: Vertical(g2)
    c: Horizontal(g1)
    c: Horizontal(g3)
    c: PointOnObject(g0,g-3)
    c: PointOnObject(g1,g-5)
    c: Coincident(g4,g5)
    c: Coincident(g5,g6)
    c: Coincident(g6,g7)
    c: Coincident(g7,g4)
    c: Vertical(g4)
    c: Vertical(g6)
    c: Horizontal(g5)
    c: Horizontal(g7)
    c: PointOnObject(g5,g-5)
    c: Coincident(g8,g9)
    c: Coincident(g9,g10)
    c: Coincident(g10,g11)
    c: Coincident(g11,g8)
    c: Vertical(g8)
    c: Vertical(g10)
    c: Horizontal(g9)
    c: Horizontal(g11)
    c: PointOnObject(g8,g-3)
    c: PointOnObject(g9,g-5)
    c: DistanceX(g-5,g-5) = 28.9
    c: DistanceX(g1,g1) = 3
    c: DistanceX(g5,g5) = 3
    c: DistanceX(g9,g9) = 3
    c: PointOnObject(g4,g-3)
    c: DistanceX(g10,g-4) = 5
    c: DistanceX(g6,g8) = 5
    c: DistanceX(g2,g4) = 5
    c: DistanceX(g-6,g0) = 4.9
FEATURE [PartDesign::Pad] Pad494
  BaseFeature = -> Pocket316
  Direction = (0,1,-2e-16)
  Length = 2
  Length2 = 10
  Profile = -> Sketch713
  ReferenceAxis = -> Sketch713 [N_Axis]
  Refine = true
  Suppressed = false
  Type = 0
FEATURE [Sketcher::SketchObject] Sketch714
  ArcFitTolerance = 1e-06
  AttachmentSupport = -> [Pad494]
  ExternalGeometry = -> [Pad494]
  FullyConstrained = true
  MakeInternals = false
  MapMode = 5
  Placement = pos=(0,0,0) rot=(1,0,0;3.14159rad)
  sketch-geometry (12):
    g0: LineSegment StartX=9.13 StartY=-22 StartZ=0 EndX=10.83 EndY=-22 EndZ=0
    g1: LineSegment StartX=10.83 StartY=-22 StartZ=0 EndX=10.83 EndY=-10 EndZ=0
    g2: LineSegment StartX=10.83 StartY=-10 StartZ=0 EndX=9.13 EndY=-10 EndZ=0
    g3: LineSegment StartX=9.13 StartY=-10 StartZ=0 EndX=9.13 EndY=-22 EndZ=0
    g4: LineSegment StartX=14.59 StartY=-22 StartZ=0 EndX=16.29 EndY=-22 EndZ=0
    g5: LineSegment StartX=16.29 StartY=-22 StartZ=0 EndX=16.29 EndY=-10 EndZ=0
    g6: LineSegment StartX=16.29 StartY=-10 StartZ=0 EndX=14.59 EndY=-10 EndZ=0
    g7: LineSegment StartX=14.59 StartY=-10 StartZ=0 EndX=14.59 EndY=-22 EndZ=0
    g8: LineSegment StartX=18.92 StartY=-22 StartZ=0 EndX=22.52 EndY=-22 EndZ=0
    g9: LineSegment StartX=22.52 StartY=-22 StartZ=0 EndX=22.52 EndY=-10 EndZ=0
    g10: LineSegment StartX=22.52 StartY=-10 StartZ=0 EndX=18.92 EndY=-10 EndZ=0
    g11: LineSegment StartX=18.92 StartY=-10 StartZ=0 EndX=18.92 EndY=-22 EndZ=0
  constraints (36):
    c: Coincident(g0,g1)
    c: Coincident(g1,g2)
    c: Coincident(g2,g3)
    c: Coincident(g3,g0)
    c: Horizontal(g0)
    c: Horizontal(g2)
    c: Vertical(g1)
    c: Vertical(g3)
    c: Coincident(g4,g5)
    c: Coincident(g5,g6)
    c: Coincident(g6,g7)
    c: Coincident(g7,g4)
    c: Horizontal(g4)
    c: Horizontal(g6)
    c: Vertical(g5)
    c: Vertical(g7)
    c: Coincident(g8,g9)
    c: Coincident(g9,g10)
    c: Coincident(g10,g11)
    c: Coincident(g11,g8)
    c: Horizontal(g8)
    c: Horizontal(g10)
    c: Vertical(g9)
    c: Vertical(g11)
    c: PointOnObject(g9,g-3)
    c: PointOnObject(g5,g-3)
    c: PointOnObject(g1,g-3)
    c: PointOnObject(g8,g-5)
    c: PointOnObject(g4,g-5)
    c: PointOnObject(g0,g-5)
    c: DistanceX(g8,g8) = 3.6
    c: DistanceX(g4,g4) = 1.7
    c: DistanceX(g0,g0) = 1.7
    c: DistanceX(g0,g4) = 3.76
    c: DistanceX(g4,g8) = 2.63
    c: DistanceX(g8,g-5) = 11.48
FEATURE [PartDesign::Pocket] Pocket317
  BaseFeature = -> Pad494
  Direction = (0,0,1)
  Length = 0.8
  Length2 = 5
  Profile = -> Sketch714
  ReferenceAxis = -> Sketch714 [N_Axis]
  Refine = true
  Suppressed = false
  Type = 0
FEATURE [PartDesign::Pocket] Pocket318
  BaseFeature = -> Pocket317
  Direction = (0,0,1)
  Length = 0.3
  Length2 = 5
  Profile = -> Pocket317 [Face41]
  Refine = true
  Suppressed = false
  Type = 0
FEATURE [PartDesign::Pocket] Pocket319
  BaseFeature = -> Pocket318
  Direction = (0,0,1)
  Length = 0.2
  Length2 = 5
  Profile = -> Pocket318 [Face37]
  Refine = true
  Suppressed = false
  Type = 0
FEATURE [PartDesign::Pocket] Pocket320
  BaseFeature = -> Pocket319
  Direction = (0,0,1)
  Length = 0.2
  Length2 = 5
  Profile = -> Pocket319 [Face45]
  Refine = true
  Suppressed = false
  Type = 0
FEATURE [Sketcher::SketchObject] Sketch715
  ArcFitTolerance = 1e-06
  AttachmentSupport = -> [Pocket320]
  ExternalGeometry = -> [Pocket320]
  FullyConstrained = true
  MakeInternals = false
  MapMode = 5
  Placement = pos=(0,0,-14.6) rot=(1,0,0;3.14159rad)
  sketch-geometry (8):
    g0: LineSegment StartX=25 StartY=-11.2 StartZ=0 EndX=25.4 EndY=-11.2 EndZ=0
    g1: LineSegment StartX=25.4 StartY=-11.2 StartZ=0 EndX=25.4 EndY=-8.3 EndZ=0
    g2: LineSegment StartX=25.4 StartY=-8.3 StartZ=0 EndX=25 EndY=-8.3 EndZ=0
    g3: LineSegment StartX=25 StartY=-8.3 StartZ=0 EndX=25 EndY=-11.2 EndZ=0
    g4: LineSegment StartX=27.15 StartY=-8.3 StartZ=0 EndX=27.15 EndY=-11.2 EndZ=0
    g5: LineSegment StartX=27.15 StartY=-11.2 StartZ=0 EndX=29.25 EndY=-11.2 EndZ=0
    g6: LineSegment StartX=29.25 StartY=-11.2 StartZ=0 EndX=29.25 EndY=-8.3 EndZ=0
    g7: LineSegment StartX=29.25 StartY=-8.3 StartZ=0 EndX=27.15 EndY=-8.3 EndZ=0
  constraints (23):
    c: PointOnObject(g0,g-4)
    c: Horizontal(g0)
    c: Coincident(g1,g0)
    c: PointOnObject(g1,g-3)
    c: Vertical(g1)
    c: Coincident(g2,g1)
    c: Coincident(g2,g-4)
    c: Coincident(g3,g2)
    c: Coincident(g3,g0)
    c: DistanceY(g3,g3) = 2.9
    c: DistanceX(g2,g2) = 0.4
    c: Coincident(g4,g5)
    c: Coincident(g5,g6)
    c: Coincident(g6,g7)
    c: Coincident(g7,g4)
    c: Vertical(g4)
    c: Vertical(g6)
    c: Horizontal(g5)
    c: Horizontal(g7)
    c: PointOnObject(g4,g-3)
    c: DistanceY(g4,g4) = 2.9
    c: DistanceX(g7,g7) = 2.1
    c: DistanceX(g1,g4) = 1.75
FEATURE [PartDesign::Pocket] Pocket321
  BaseFeature = -> Pocket320
  Direction = (0,0,1)
  Length = 5
  Length2 = 5
  Profile = -> Sketch715
  ReferenceAxis = -> Sketch715 [N_Axis]
  Refine = true
  Suppressed = false
  Type = 0
FEATURE [PartDesign::Fillet] Fillet022
  Base = -> Pocket321 [Edge119,Edge116,Edge124,Edge82,Edge104,Edge102,Edge94,Edge81,Edge80,Edge78,Edge59,Edge57,Edge56]
  BaseFeature = -> Pocket321
  Radius = 0.5
  Refine = true
  SupportTransform = false
  Suppressed = false
  UseAllEdges = false
FEATURE [Sketcher::SketchObject] Sketch716
  ArcFitTolerance = 1e-06
  AttachmentSupport = -> [Fillet022]
  ExternalGeometry = -> [Fillet022]
  FullyConstrained = true
  MakeInternals = false
  MapMode = 5
  Placement = pos=(0,0,-14.6) rot=(1,0,0;3.14159rad)
  sketch-geometry (6):
    g0: LineSegment StartX=25 StartY=-11.2 StartZ=0 EndX=23.1 EndY=-11.2 EndZ=0
    g1: LineSegment StartX=23.1 StartY=-11.2 StartZ=0 EndX=23.1 EndY=-8.3 EndZ=0
    g2: LineSegment StartX=23.1 StartY=-8.3 StartZ=0 EndX=3.1 EndY=-8.3 EndZ=0
    g3: LineSegment StartX=3.1 StartY=-8.3 StartZ=0 EndX=3.1 EndY=-16.3 EndZ=0
    g4: LineSegment StartX=3.1 StartY=-16.3 StartZ=0 EndX=25 EndY=-16.3 EndZ=0
    g5: LineSegment StartX=25 StartY=-16.3 StartZ=0 EndX=25 EndY=-11.2 EndZ=0
  constraints (16):
    c: Coincident(g0,g-6)
    c: Horizontal(g0)
    c: Coincident(g1,g0)
    c: Vertical(g1)
    c: Coincident(g2,g1)
    c: PointOnObject(g2,g-5)
    c: Horizontal(g2)
    c: Coincident(g3,g2)
    c: Vertical(g3)
    c: Coincident(g4,g3)
    c: Coincident(g4,g-6)
    c: Horizontal(g4)
    c: Coincident(g5,g4)
    c: Coincident(g5,g0)
    c: DistanceX(g0,g0) = 1.9
    c: DistanceX(g2,g2) = 20
FEATURE [PartDesign::Pad] Pad495
  BaseFeature = -> Fillet022
  Direction = (0,0,-1)
  Length = 2.6
  Length2 = 10
  Profile = -> Sketch716
  ReferenceAxis = -> Sketch716 [N_Axis]
  Refine = true
  Reversed = true
  Suppressed = false
  Type = 0
FEATURE [PartDesign::Pad] Pad496
  BaseFeature = -> Pad495
  Direction = (0,0,1)
  Length = 0.9
  Length2 = 10
  Profile = -> Pad495 [Face48]
  Refine = true
  Suppressed = false
  Type = 0
FEATURE [Sketcher::SketchObject] Sketch717
  ArcFitTolerance = 1e-06
  AttachmentSupport = -> [Pad496]
  ExternalGeometry = -> [Pad496]
  FullyConstrained = true
  MakeInternals = false
  MapMode = 5
  Placement = pos=(0,0,-11.7) rot=(0,0,1;0rad)
  sketch-geometry (11):
    g0: LineSegment StartX=3.1 StartY=11.6 StartZ=0 EndX=3.1 EndY=8.3 EndZ=0
    g1: LineSegment StartX=3.1 StartY=8.3 StartZ=0 EndX=0.5 EndY=8.3 EndZ=0
    g2: LineSegment StartX=3.1 StartY=11.6 StartZ=0 EndX=1.81082e-11 EndY=11.6 EndZ=0
    g3: LineSegment StartX=1.8108e-11 StartY=11.6 StartZ=0 EndX=1.8108e-11 EndY=8.8 EndZ=0
    g4: LineSegment StartX=29.25 StartY=8.8 StartZ=0 EndX=29.25 EndY=11.6 EndZ=0
    g5: LineSegment StartX=34 StartY=8.8 StartZ=0 EndX=34 EndY=11.6 EndZ=0
    g6: LineSegment StartX=34 StartY=11.6 StartZ=0 EndX=29.25 EndY=11.6 EndZ=0
    g7: ArcOfCircle CenterX=33.5 CenterY=8.8 CenterZ=0 NormalX=0 NormalY=0 NormalZ=1 AngleXU=0 Radius=0.5 StartAngle=4.71239 EndAngle=6.28319
    g8: ArcOfCircle CenterX=29.75 CenterY=8.8 CenterZ=0 NormalX=0 NormalY=0 NormalZ=1 AngleXU=0 Radius=0.5 StartAngle=3.14159 EndAngle=4.71239
    g9: LineSegment StartX=29.75 StartY=8.3 StartZ=0 EndX=33.5 EndY=8.3 EndZ=0
    g10: ArcOfCircle CenterX=0.499996 CenterY=8.8 CenterZ=0 NormalX=0 NormalY=0 NormalZ=1 AngleXU=0 Radius=0.499996 StartAngle=3.14158 EndAngle=4.7124
  constraints (29):
    c: Coincident(g0,g-8)
    c: Coincident(g1,g0)
    c: Coincident(g2,g0)
    c: Horizontal(g2)
    c: PointOnObject(g0,g-7)
    c: Coincident(g3,g2)
    c: Vertical(g3)
    c: Vertical(g4)
    c: Coincident(g6,g5)
    c: Coincident(g6,g4)
    c: Horizontal(g6)
    c: Coincident(g7,g-5)
    c: PointOnObject(g5,g-3)
    c: DistanceY(g5,g5) = 2.8
    c: Coincident(g4,g-6)
    c: Coincident(g7,g-4)
    c: Coincident(g7,g5)
    c: DistanceY(g5,g7) = 0
    c: DistanceY(g3,g2) = 2.8
    c: Coincident(g8,g4)
    c: Coincident(g8,g-10)
    c: Coincident(g9,g8)
    c: Coincident(g7,g9)
    c: DistanceX(g8,g8) = 0
    c: Coincident(g3,g-9)
    c: Coincident(g1,g-8)
    c: Coincident(g10,g1)
    c: Coincident(g10,g3)
    c: Tangent(g10,g-11)
FEATURE [PartDesign::Pad] Pad497
  BaseFeature = -> Pad496
  Direction = (0,0,1)
  Length = 0.3
  Length2 = 10
  Profile = -> Sketch717
  ReferenceAxis = -> Sketch717 [N_Axis]
  Refine = true
  Suppressed = false
  Type = 0
FEATURE [Sketcher::SketchObject] Sketch718
  ArcFitTolerance = 1e-06
  AttachmentSupport = -> [Pad497]
  ExternalGeometry = -> [Pad497]
  FullyConstrained = true
  MakeInternals = false
  MapMode = 5
  Placement = pos=(0,0,0.2) rot=(1,0,0;3.14159rad)
  sketch-geometry (6):
    g0: LineSegment StartX=25 StartY=-0.5 StartZ=0 EndX=25 EndY=-15.5 EndZ=0
    g1: LineSegment StartX=25 StartY=-15.5 StartZ=0 EndX=34 EndY=-15.5 EndZ=0
    g2: LineSegment StartX=34 StartY=-15.5 StartZ=0 EndX=34 EndY=-0.5 EndZ=0
    g3: ArcOfCircle CenterX=33.5 CenterY=-0.5 CenterZ=0 NormalX=0 NormalY=0 NormalZ=1 AngleXU=0 Radius=0.5 StartAngle=-2.85105e-11 EndAngle=1.5708
    g4: ArcOfCircle CenterX=25.5 CenterY=-0.5 CenterZ=0 NormalX=0 NormalY=0 NormalZ=1 AngleXU=0 Radius=0.5 StartAngle=1.5708 EndAngle=3.14159
    g5: LineSegment StartX=25.5 StartY=1e-16 StartZ=0 EndX=33.5 EndY=-7.69e-14 EndZ=0
  constraints (14):
    c: Coincident(g0,g-5)
    c: Vertical(g0)
    c: Coincident(g1,g0)
    c: Horizontal(g1)
    c: PointOnObject(g1,g-7)
    c: Coincident(g2,g1)
    c: Coincident(g2,g-7)
    c: Coincident(g3,g2)
    c: Tangent(g3,g-6) = -1.5708
    c: Coincident(g4,g0)
    c: Tangent(g4,g-4) = -1.5708
    c: Coincident(g5,g3)
    c: Coincident(g5,g4)
    c: DistanceY(g0,g0) = 15
FEATURE [PartDesign::Pad] Pad498
  BaseFeature = -> Pad497
  Direction = (0,0,-1)
  Length = 2.2
  Length2 = 10
  Profile = -> Sketch718
  ReferenceAxis = -> Sketch718 [N_Axis]
  Refine = true
  Suppressed = false
  Type = 0
FEATURE [Sketcher::SketchObject] Sketch719
  ArcFitTolerance = 1e-06
  AttachmentSupport = -> [Pad498]
  ExternalGeometry = -> [Pad498]
  FullyConstrained = false
  MakeInternals = false
  MapMode = 5
  Placement = pos=(0,0,-14.6) rot=(1,0,0;3.14159rad)
  sketch-geometry (4):
    g0: ArcOfCircle CenterX=16.9908 CenterY=-15.9899 CenterZ=0 NormalX=0 NormalY=0 NormalZ=1 AngleXU=0 Radius=4 StartAngle=6.24568 EndAngle=9.46229
    g1: LineSegment StartX=12.9936 StartY=-16.1399 StartZ=0 EndX=10.4936 EndY=-16.1399 EndZ=0
    g2: LineSegment StartX=20.988 StartY=-16.1399 StartZ=0 EndX=23.488 EndY=-16.1399 EndZ=0
    g3: ArcOfCircle CenterX=16.9908 CenterY=-15.9899 CenterZ=0 NormalX=0 NormalY=0 NormalZ=1 AngleXU=0 Radius=6.49892 StartAngle=6.2601 EndAngle=9.44786
  constraints (11):
    c: DistanceY(g0,g0) = 0.15
    c: DistanceY(g0,g0) = 0.15
    c: Radius(g0) = 4
    c: Coincident(g1,g0)
    c: Horizontal(g1)
    c: Coincident(g2,g0)
    c: Horizontal(g2)
    c: Coincident(g3,g1)
    c: Coincident(g3,g2)
    c: Coincident(g3,g0)
    c: DistanceX(g1,g1) = 2.5
FEATURE [PartDesign::Pad] Pad499
  BaseFeature = -> Pad498
  Direction = (0,0,-1)
  Length = 1.6
  Length2 = 10
  Profile = -> Sketch719
  ReferenceAxis = -> Sketch719 [N_Axis]
  Refine = true
  Suppressed = false
  Type = 0
FEATURE [Sketcher::SketchObject] Sketch720
  ArcFitTolerance = 1e-06
  AttachmentSupport = -> [Pad499]
  ExternalGeometry = -> [Pad499]
  FullyConstrained = true
  MakeInternals = false
  MapMode = 5
  Placement = pos=(0,0,-16.2) rot=(1,0,0;3.14159rad)
  sketch-geometry (4):
    g0: ArcOfCircle CenterX=16.9908 CenterY=-15.9899 CenterZ=0 NormalX=0 NormalY=0 NormalZ=1 AngleXU=0 Radius=6.49892 StartAngle=6.2601 EndAngle=9.44786
    g1: LineSegment StartX=10.4936 StartY=-16.1399 StartZ=0 EndX=14.9964 EndY=-16.1399 EndZ=0
    g2: LineSegment StartX=23.488 StartY=-16.1399 StartZ=0 EndX=18.9852 EndY=-16.1399 EndZ=0
    g3: ArcOfCircle CenterX=16.9908 CenterY=-15.9899 CenterZ=0 NormalX=0 NormalY=0 NormalZ=1 AngleXU=0 Radius=2 StartAngle=6.20811 EndAngle=9.49985
  constraints (10):
    c: Tangent(g0,g-3) = -1.5708
    c: Coincident(g0,g-3)
    c: Coincident(g1,g0)
    c: Horizontal(g1)
    c: Coincident(g2,g0)
    c: Horizontal(g2)
    c: Coincident(g3,g1)
    c: Coincident(g3,g2)
    c: Radius(g3) = 2
    c: Coincident(g3,g0)
FEATURE [PartDesign::Pad] Pad500
  BaseFeature = -> Pad499
  Direction = (0,0,-1)
  Length = 1
  Length2 = 10
  Profile = -> Sketch720
  ReferenceAxis = -> Sketch720 [N_Axis]
  Refine = true
  Suppressed = false
  Type = 0
FEATURE [Sketcher::SketchObject] Sketch721
  ArcFitTolerance = 1e-06
  AttachmentSupport = -> [Pad500]
  ExternalGeometry = -> [Pad500]
  FullyConstrained = true
  MakeInternals = false
  MapMode = 5
  Placement = pos=(0,0,-14.6) rot=(1,0,0;3.14159rad)
  sketch-geometry (8):
    g0: LineSegment StartX=21.1 StartY=-24 StartZ=0 EndX=21.1 EndY=-26 EndZ=0
    g1: LineSegment StartX=21.1 StartY=-26 StartZ=0 EndX=26.1 EndY=-26 EndZ=0
    g2: LineSegment StartX=26.1 StartY=-26 StartZ=0 EndX=26.1 EndY=-24 EndZ=0
    g3: LineSegment StartX=26.1 StartY=-24 StartZ=0 EndX=21.1 EndY=-24 EndZ=0
    g4: LineSegment StartX=13.1 StartY=-24 StartZ=0 EndX=13.1 EndY=-26 EndZ=0
    g5: LineSegment StartX=13.1 StartY=-26 StartZ=0 EndX=18.1 EndY=-26 EndZ=0
    g6: LineSegment StartX=18.1 StartY=-26 StartZ=0 EndX=18.1 EndY=-24 EndZ=0
    g7: LineSegment StartX=18.1 StartY=-24 StartZ=0 EndX=13.1 EndY=-24 EndZ=0
  constraints (20):
    c: Coincident(g0,g1)
    c: Coincident(g1,g2)
    c: Coincident(g2,g3)
    c: Coincident(g3,g0)
    c: Vertical(g0)
    c: Vertical(g2)
    c: Horizontal(g1)
    c: Horizontal(g3)
    c: Coincident(g0,g-7)
    c: Coincident(g1,g-8)
    c: Coincident(g4,g5)
    c: Coincident(g5,g6)
    c: Coincident(g6,g7)
    c: Coincident(g7,g4)
    c: Vertical(g4)
    c: Vertical(g6)
    c: Horizontal(g5)
    c: Horizontal(g7)
    c: Coincident(g4,g-6)
    c: Coincident(g5,g-5)
FEATURE [PartDesign::Pad] Pad501
  BaseFeature = -> Pad500
  Direction = (0,0,-1)
  Length = 10
  Length2 = 10
  Profile = -> Sketch721
  ReferenceAxis = -> Sketch721 [N_Axis]
  Refine = true
  Reversed = true
  Suppressed = false
  Type = 0
FEATURE [Sketcher::SketchObject] Sketch722
  ArcFitTolerance = 1e-06
  AttachmentSupport = -> [Pad501]
  ExternalGeometry = -> [Pad501]
  FullyConstrained = true
  MakeInternals = false
  MapMode = 5
  Placement = pos=(0,0,-14.6) rot=(1,0,0;3.14159rad)
  sketch-geometry (1):
    g0: Circle CenterX=16.9908 CenterY=-23.7899 CenterZ=0 NormalX=0 NormalY=0 NormalZ=1 AngleXU=0 Radius=0.75
  constraints (3):
    c: Radius(g0) = 0.75
    c: DistanceX(g-3,g0) = 0
    c: DistanceY(g0,g-3) = 7.8
FEATURE [PartDesign::Pocket] Pocket322
  BaseFeature = -> Pad501
  Direction = (0,0,1)
  Length = 8
  Length2 = 5
  Profile = -> Sketch722
  ReferenceAxis = -> Sketch722 [N_Axis]
  Refine = true
  Suppressed = false
  Type = 0
FEATURE [PartDesign::Pocket] Pocket323
  BaseFeature = -> Pocket322
  Direction = (0,-1,0)
  Length = 0.1
  Length2 = 5
  Profile = -> Pocket322 [Face41]
  Refine = true
  Suppressed = false
  Type = 0
FEATURE [PartDesign::Pocket] Pocket324
  BaseFeature = -> Pocket323
  Direction = (0,-1,0)
  Length = 0.1
  Length2 = 5
  Profile = -> Pocket323 [Face39]
  Refine = true
  Suppressed = false
  Type = 0
FEATURE [PartDesign::Pocket] Pocket325
  BaseFeature = -> Pocket324
  Direction = (-1,0,-6e-16)
  Length = 0.1
  Length2 = 5
  Profile = -> Pocket324 [Face8]
  Refine = true
  Suppressed = false
  Type = 0
FEATURE [Sketcher::SketchObject] Sketch723
  ArcFitTolerance = 1e-06
  AttachmentSupport = -> [Pocket325]
  ExternalGeometry = -> [Pocket325]
  FullyConstrained = true
  MakeInternals = false
  MapMode = 5
  Placement = pos=(0,0,-17.2) rot=(1,0,0;3.14159rad)
  sketch-geometry (4):
    g0: LineSegment StartX=0.5 StartY=-8.3 StartZ=0 EndX=0.5 EndY=-23.5 EndZ=0
    g1: LineSegment StartX=0.5 StartY=-23.5 StartZ=0 EndX=34 EndY=-23.5 EndZ=0
    g2: LineSegment StartX=34 StartY=-23.5 StartZ=0 EndX=34 EndY=-8.3 EndZ=0
    g3: LineSegment StartX=34 StartY=-8.3 StartZ=0 EndX=0.5 EndY=-8.3 EndZ=0
  constraints (10):
    c: Coincident(g0,g1)
    c: Coincident(g1,g2)
    c: Coincident(g2,g3)
    c: Coincident(g3,g0)
    c: Vertical(g0)
    c: Vertical(g2)
    c: Horizontal(g1)
    c: Horizontal(g3)
    c: Coincident(g0,g-3)
    c: Coincident(g1,g-6)
FEATURE [PartDesign::Pocket] Pocket326
  BaseFeature = -> Pocket325
  Direction = (0,0,1)
  Length = 2.6
  Length2 = 5
  Profile = -> Sketch723
  ReferenceAxis = -> Sketch723 [N_Axis]
  Refine = true
  Suppressed = false
  Type = 0
FEATURE [PartDesign::Pad] Pad502
  BaseFeature = -> Pocket326
  Direction = (0,0,-1)
  Length = 8
  Length2 = 10
  Profile = -> Pocket326 [Face81]
  Refine = true
  Suppressed = false
  Type = 0
FEATURE [Sketcher::SketchObject] Sketch724
  ArcFitTolerance = 1e-06
  AttachmentSupport = -> [Pad502]
  ExternalGeometry = -> [Pad502]
  FullyConstrained = true
  MakeInternals = false
  MapMode = 5
  Placement = pos=(0,0,2.25) rot=(0,0,1;0rad)
  sketch-geometry (5):
    g0: ArcOfCircle CenterX=33.5 CenterY=0.5 CenterZ=0 NormalX=0 NormalY=0 NormalZ=1 AngleXU=0 Radius=0.5 StartAngle=4.71239 EndAngle=6.28319
    g1: LineSegment StartX=33.5 StartY=0 StartZ=0 EndX=32.35 EndY=0 EndZ=0
    g2: LineSegment StartX=32.35 StartY=0 StartZ=0 EndX=32.35 EndY=0.65 EndZ=0
    g3: LineSegment StartX=34 StartY=0.5 StartZ=0 EndX=34 EndY=0.65 EndZ=0
    g4: LineSegment StartX=34 StartY=0.65 StartZ=0 EndX=32.35 EndY=0.65 EndZ=0
  constraints (13):
    c: Coincident(g0,g-5)
    c: Tangent(g0,g-4) = -1.5708
    c: Coincident(g1,g0)
    c: PointOnObject(g1,g-5)
    c: Coincident(g2,g1)
    c: Vertical(g2)
    c: Coincident(g3,g0)
    c: PointOnObject(g3,g-3)
    c: Coincident(g4,g3)
    c: Coincident(g4,g2)
    c: Horizontal(g4)
    c: DistanceX(g1,g1) = 1.15
    c: DistanceY(g3,g3) = 0.15
FEATURE [PartDesign::Pocket] Pocket327
  BaseFeature = -> Pad502
  Direction = (0,0,-1)
  Length = 5
  Length2 = 5
  Profile = -> Sketch724
  ReferenceAxis = -> Sketch724 [N_Axis]
  Refine = true
  Suppressed = false
  Type = 1
FEATURE [PartDesign::Fillet] Fillet014
  Base = -> Pocket327 [Edge91]
  BaseFeature = -> Pocket327
  Radius = 0.5
  Refine = true
  SupportTransform = false
  Suppressed = false
  UseAllEdges = false
FEATURE [Sketcher::SketchObject] Sketch725
  ArcFitTolerance = 1e-06
  AttachmentSupport = -> [Fillet014]
  ExternalGeometry = -> [Fillet014]
  FullyConstrained = true
  MakeInternals = false
  MapMode = 5
  Placement = pos=(0,0,-14.6) rot=(1,0,0;3.14159rad)
  sketch-geometry (9):
    g0: LineSegment StartX=16.2 StartY=-8.3 StartZ=0 EndX=8.2 EndY=-8.3 EndZ=0
    g1: LineSegment StartX=8.2 StartY=-8.3 StartZ=0 EndX=8.2 EndY=-16.1 EndZ=0
    g2: LineSegment StartX=8.2 StartY=-16.1 StartZ=0 EndX=12.2 EndY=-16.1 EndZ=0
    g3: LineSegment StartX=12.2 StartY=-16.1 StartZ=0 EndX=12.2 EndY=-24.9 EndZ=0
    g4: LineSegment StartX=12.2 StartY=-24.9 StartZ=0 EndX=20.2 EndY=-24.9 EndZ=0
    g5: LineSegment StartX=20.2 StartY=-24.9 StartZ=0 EndX=20.2 EndY=-16.1 EndZ=0
    g6: LineSegment StartX=20.2 StartY=-16.1 StartZ=0 EndX=24.2 EndY=-16.1 EndZ=0
    g7: LineSegment StartX=24.2 StartY=-16.1 StartZ=0 EndX=24.2 EndY=-8.3 EndZ=0
    g8: LineSegment StartX=24.2 StartY=-8.3 StartZ=0 EndX=16.2 EndY=-8.3 EndZ=0
  constraints (27):
    c: PointOnObject(g0,g-3)
    c: PointOnObject(g0,g-3)
    c: Coincident(g1,g0)
    c: Vertical(g1)
    c: Coincident(g2,g1)
    c: Horizontal(g2)
    c: Coincident(g3,g2)
    c: Vertical(g3)
    c: Coincident(g4,g3)
    c: Horizontal(g4)
    c: Coincident(g5,g4)
    c: Vertical(g5)
    c: Coincident(g6,g5)
    c: Horizontal(g6)
    c: Coincident(g7,g6)
    c: PointOnObject(g7,g-3)
    c: Coincident(g8,g7)
    c: Coincident(g8,g0)
    c: DistanceX(g8,g8) = 8
    c: DistanceX(g0,g0) = 8
    c: Vertical(g7)
    c: DistanceX(g0,g-3) = 6.9
    c: DistanceY(g7,g7) = 7.8
    c: DistanceY(g1,g1) = 7.8
    c: DistanceX(g2,g5) = 8
    c: DistanceX(g5,g6) = 4
    c: DistanceY(g3,g3) = 8.8
FEATURE [PartDesign::Pocket] Pocket328
  BaseFeature = -> Fillet014
  Direction = (0,0,1)
  Length = 5.25
  Length2 = 5
  Profile = -> Sketch725
  ReferenceAxis = -> Sketch725 [N_Axis]
  Refine = true
  Suppressed = false
  Type = 0
FEATURE [PartDesign::Fillet] Fillet015
  Base = -> Pocket328 [Edge212,Edge230]
  BaseFeature = -> Pocket328
  Radius = 0.5
  Refine = true
  SupportTransform = false
  Suppressed = false
  UseAllEdges = false
FEATURE [Sketcher::SketchObject] Sketch726
  ArcFitTolerance = 1e-06
  AttachmentSupport = -> [Fillet015]
  ExternalGeometry = -> [Fillet015]
  FullyConstrained = true
  MakeInternals = false
  MapMode = 5
  Placement = pos=(12.2,0,0) rot=(0.57735,0.57735,0.57735;2.0944rad)
  sketch-geometry (5):
    g0: LineSegment StartX=18.1 StartY=-14.6 StartZ=0 EndX=24.1 EndY=-14.6 EndZ=0
    g1: LineSegment StartX=24.1 StartY=-14.6 StartZ=0 EndX=24.1 EndY=-15.5 EndZ=0
    g2: LineSegment StartX=18.1 StartY=-14.6 StartZ=0 EndX=18.1 EndY=-15.5 EndZ=0
    g3: ArcOfCircle CenterX=21.1 CenterY=-15.5 CenterZ=0 NormalX=0 NormalY=0 NormalZ=1 AngleXU=0 Radius=3 StartAngle=3.14159 EndAngle=6.28319
    g4: LineSegment [constr] StartX=18.1 StartY=-15.5 StartZ=0 EndX=24.1 EndY=-15.5 EndZ=0
  constraints (15):
    c: PointOnObject(g0,g-3)
    c: PointOnObject(g0,g-3)
    c: Coincident(g1,g0)
    c: Vertical(g1)
    c: Coincident(g2,g0)
    c: Vertical(g2)
    c: Coincident(g3,g2)
    c: Coincident(g3,g1)
    c: Diameter(g3) = 6
    c: DistanceY(g2,g2) = 0.9
    c: DistanceY(g1,g1) = 0.9
    c: Coincident(g4,g2)
    c: Coincident(g4,g1)
    c: PointOnObject(g3,g4)
    c: DistanceX(g-3,g0) = 2
FEATURE [PartDesign::Pad] Pad503
  BaseFeature = -> Fillet015
  Direction = (1,0,0)
  Length = 2
  Length2 = 10
  Profile = -> Sketch726
  ReferenceAxis = -> Sketch726 [N_Axis]
  Refine = true
  Reversed = true
  Suppressed = false
  Type = 0
FEATURE [Sketcher::SketchObject] Sketch727
  ArcFitTolerance = 1e-06
  AttachmentSupport = -> [Pad503]
  ExternalGeometry = -> [Pad503]
  FullyConstrained = true
  MakeInternals = false
  MapMode = 5
  Placement = pos=(20.2,0,0) rot=(0.57735,-0.57735,-0.57735;2.0944rad)
  sketch-geometry (4):
    g0: LineSegment StartX=-24.1 StartY=-14.6 StartZ=0 EndX=-18.1 EndY=-14.6 EndZ=0
    g1: LineSegment StartX=-18.1 StartY=-14.6 StartZ=0 EndX=-18.1 EndY=-15.5 EndZ=0
    g2: LineSegment StartX=-24.1 StartY=-14.6 StartZ=0 EndX=-24.1 EndY=-15.5 EndZ=0
    g3: ArcOfCircle CenterX=-21.1 CenterY=-15.5 CenterZ=0 NormalX=0 NormalY=0 NormalZ=1 AngleXU=0 Radius=3 StartAngle=3.14159 EndAngle=6.28318
  constraints (9):
    c: Coincident(g0,g-5)
    c: Coincident(g0,g-3)
    c: Coincident(g1,g0)
    c: Coincident(g1,g-4)
    c: Coincident(g2,g0)
    c: Coincident(g2,g-5)
    c: Coincident(g3,g2)
    c: Coincident(g3,g1)
    c: Tangent(g3,g-4)
FEATURE [PartDesign::Pad] Pad504
  BaseFeature = -> Pad503
  Direction = (-1,0,0)
  Length = 2
  Length2 = 10
  Profile = -> Sketch727
  ReferenceAxis = -> Sketch727 [N_Axis]
  Refine = true
  Reversed = true
  Suppressed = false
  Type = 0
FEATURE [Sketcher::SketchObject] Sketch728
  ArcFitTolerance = 1e-06
  AttachmentSupport = -> [Pad504]
  ExternalGeometry = -> [Pad504]
  FullyConstrained = true
  MakeInternals = false
  MapMode = 5
  Placement = pos=(20.2,0,0) rot=(0.57735,-0.57735,-0.57735;2.0944rad)
  sketch-geometry (1):
    g0: Circle CenterX=-21.1 CenterY=-15.5 CenterZ=0 NormalX=0 NormalY=0 NormalZ=1 AngleXU=0 Radius=1.5
  constraints (2):
    c: Coincident(g0,g-3)
    c: Diameter(g0) = 3
FEATURE [PartDesign::Pad] Pad505
  BaseFeature = -> Pad504
  Direction = (-1,0,0)
  Length = 8
  Length2 = 10
  Profile = -> Sketch728
  ReferenceAxis = -> Sketch728 [N_Axis]
  Refine = true
  Suppressed = false
  Type = 0
FEATURE [PartDesign::Body] Body036  label="Base"
  AllowCompound = false
  Group = -> [Sketch709,Pad490,Sketch710,Pad491,Sketch711,Pad492,Sketch712,Pad493,Pocket316,Sketch713,Pad494,Sketch714,Pocket317,Pocket318,Pocket319,Pocket320,Sketch715,Pocket321,Fillet022,Sketch716,Pad495,Pad496,Sketch717,Pad497,Sketch718,Pad498,Sketch719,Pad499,Sketch720,Pad500,Sketch721,Pad501,Sketch722,Pocket322,Pocket323,Pocket324,Pocket325,Sketch723,Pocket326,Pad502,Sketch724,Pocket327,Fillet014,+9 more]
  Origin = -> Origin039
  Placement = pos=(19.8,21.9,-10) rot=(-1,0,0;3.14159rad)
  Tip = -> Pad505
FEATURE [Sketcher::SketchObject] Sketch729
  ArcFitTolerance = 1e-06
  AttachmentSupport = -> [XZ_Plane040]
  FullyConstrained = true
  MakeInternals = false
  MapMode = 5
  Placement = pos=(0,0,0) rot=(1,0,0;1.5708rad)
  sketch-geometry (20):
    g0: LineSegment StartX=0 StartY=0 StartZ=0 EndX=-7.9 EndY=0 EndZ=0
    g1: LineSegment StartX=-7.9 StartY=0 StartZ=0 EndX=-7.9 EndY=8 EndZ=0
    g2: LineSegment StartX=-7.9 StartY=8 StartZ=0 EndX=-11.9 EndY=8 EndZ=0
    g3: LineSegment StartX=-11.9 StartY=8 StartZ=0 EndX=-11.9 EndY=16 EndZ=0
    g4: LineSegment StartX=-11.9 StartY=16 StartZ=0 EndX=-13.95 EndY=18.05 EndZ=0
    g5: LineSegment StartX=-13.95 StartY=18.05 StartZ=0 EndX=-13.95 EndY=28.95 EndZ=0
    g6: LineSegment StartX=-13.95 StartY=28.95 StartZ=0 EndX=-11.9 EndY=31 EndZ=0
    g7: LineSegment StartX=-11.9 StartY=31 StartZ=0 EndX=4 EndY=31 EndZ=0
    g8: LineSegment StartX=4 StartY=31 StartZ=0 EndX=6.05 EndY=28.95 EndZ=0
    g9: LineSegment StartX=6.05 StartY=28.95 StartZ=0 EndX=6.05 EndY=18.05 EndZ=0
    g10: LineSegment StartX=6.05 StartY=18.05 StartZ=0 EndX=4 EndY=16 EndZ=0
    g11: LineSegment StartX=4 StartY=16 StartZ=0 EndX=4 EndY=8 EndZ=0
    g12: LineSegment StartX=4 StartY=8 StartZ=0 EndX=0 EndY=8 EndZ=0
    g13: LineSegment StartX=0 StartY=0 StartZ=0 EndX=0 EndY=8 EndZ=0
    g14: LineSegment [constr] StartX=0 StartY=8 StartZ=0 EndX=-7.9 EndY=8 EndZ=0
    g15: LineSegment [constr] StartX=-11.9 StartY=16 StartZ=0 EndX=4 EndY=16 EndZ=0
    g16: LineSegment [constr] StartX=-13.95 StartY=18.05 StartZ=0 EndX=6.05 EndY=18.05 EndZ=0
    g17: LineSegment [constr] StartX=-13.95 StartY=28.95 StartZ=0 EndX=6.05 EndY=28.95 EndZ=0
    g18: LineSegment [constr] StartX=4 StartY=31 StartZ=0 EndX=4 EndY=16 EndZ=0
    g19: LineSegment [constr] StartX=-11.9 StartY=31 StartZ=0 EndX=-11.9 EndY=16 EndZ=0
  constraints (53):
    c: Horizontal(g0)
    c: Coincident(g1,g0)
    c: Vertical(g1)
    c: Coincident(g2,g1)
    c: Horizontal(g2)
    c: Coincident(g3,g2)
    c: Vertical(g3)
    c: Coincident(g4,g3)
    c: Coincident(g5,g4)
    c: Vertical(g5)
    c: Coincident(g6,g5)
    c: Coincident(g7,g6)
    c: Horizontal(g7)
    c: Coincident(g8,g7)
    c: Coincident(g9,g8)
    c: Vertical(g9)
    c: Coincident(g10,g9)
    c: Coincident(g11,g10)
    c: Vertical(g11)
    c: Coincident(g12,g11)
    c: Horizontal(g12)
    c: Coincident(g13,g0)
    c: Coincident(g13,g12)
    c: DistanceX(g0,g0) = 7.9
    c: Vertical(g13)
    c: Coincident(g14,g12)
    c: Coincident(g14,g1)
    c: Horizontal(g14)
    c: Coincident(g15,g3)
    c: Coincident(g15,g10)
    c: Horizontal(g15)
    c: Coincident(g16,g4)
    c: Coincident(g16,g9)
    c: Horizontal(g16)
    c: Coincident(g17,g5)
    c: Coincident(g17,g8)
    c: Horizontal(g17)
    c: DistanceX(g2,g2) = 4
    c: DistanceX(g12,g12) = 4
    c: DistanceY(g13,g13) = 8
    c: DistanceX(g17,g17) = 20
    c: DistanceY(g10,g7) = 15
    c: Coincident(g18,g7)
    c: Coincident(g18,g10)
    c: Vertical(g18)
    c: Coincident(g19,g6)
    c: Coincident(g19,g3)
    c: Vertical(g19)
    c: DistanceX(g7,g8) = 2.05
    c: DistanceY(g8,g7) = 2.05
    c: DistanceY(g10,g9) = 2.05
    c: DistanceY(g11,g11) = 8
    c: Coincident(g0,g-1)
FEATURE [PartDesign::Pad] Pad506
  Direction = (0,-1,2e-16)
  Length = 1.2
  Length2 = 10
  Placement = pos=(0,0,0) rot=(1,0,0;1.5708rad)
  Profile = -> Sketch729
  ReferenceAxis = -> Sketch729 [N_Axis]
  Refine = true
  Suppressed = false
  Type = 0
FEATURE [Sketcher::SketchObject] Sketch730
  ArcFitTolerance = 1e-06
  AttachmentSupport = -> [Pad506]
  ExternalGeometry = -> [Pad506]
  FullyConstrained = true
  MakeInternals = false
  MapMode = 5
  Placement = pos=(0,3.6e-15,0) rot=(-1,0,0;1.5708rad)
  sketch-geometry (4):
    g0: LineSegment StartX=-7.9 StartY=0 StartZ=0 EndX=-7.9 EndY=-10.7 EndZ=0
    g1: LineSegment StartX=-7.9 StartY=-10.7 StartZ=0 EndX=0 EndY=-10.7 EndZ=0
    g2: LineSegment StartX=0 StartY=-10.7 StartZ=0 EndX=0 EndY=0 EndZ=0
    g3: LineSegment StartX=0 StartY=0 StartZ=0 EndX=-7.9 EndY=0 EndZ=0
  constraints (11):
    c: Coincident(g0,g1)
    c: Coincident(g1,g2)
    c: Coincident(g2,g3)
    c: Coincident(g3,g0)
    c: Vertical(g0)
    c: Vertical(g2)
    c: Horizontal(g1)
    c: Horizontal(g3)
    c: Coincident(g0,g-4)
    c: PointOnObject(g1,g-2)
    c: DistanceY(g0,g0) = 10.7
FEATURE [PartDesign::Pad] Pad507
  BaseFeature = -> Pad506
  Direction = (0,1,2e-16)
  Length = 1.8
  Length2 = 10
  Placement = pos=(0,0,0) rot=(1,0,0;1.5708rad)
  Profile = -> Sketch730
  ReferenceAxis = -> Sketch730 [N_Axis]
  Refine = true
  Suppressed = false
  Type = 0
FEATURE [Sketcher::SketchObject] Sketch731
  ArcFitTolerance = 1e-06
  AttachmentSupport = -> [Pad507]
  ExternalGeometry = -> [Pad507]
  FullyConstrained = true
  MakeInternals = false
  MapMode = 5
  Placement = pos=(-7.9,4.3e-15,0) rot=(0.707107,0,-0.707107;3.14159rad)
  sketch-geometry (5):
    g0: ArcOfCircle CenterX=-3 CenterY=1.2 CenterZ=0 NormalX=0 NormalY=0 NormalZ=1 AngleXU=0 Radius=3 StartAngle=4.71239 EndAngle=6.28319
    g1: LineSegment StartX=-4e-16 StartY=1.2 StartZ=0 EndX=0 EndY=-1.8 EndZ=0
    g2: LineSegment StartX=0 StartY=-1.8 StartZ=0 EndX=-3 EndY=-1.8 EndZ=0
    g3: ArcOfCircle CenterX=-3 CenterY=1.2 CenterZ=0 NormalX=0 NormalY=0 NormalZ=1 AngleXU=0 Radius=1.5 StartAngle=3.14159 EndAngle=6.28319
    g4: LineSegment StartX=-4.5 StartY=1.2 StartZ=0 EndX=-1.5 EndY=1.2 EndZ=0
  constraints (15):
    c: Coincident(g0,g-5)
    c: PointOnObject(g0,g-4)
    c: PointOnObject(g0,g-6)
    c: Radius(g0) = 3
    c: Coincident(g1,g0)
    c: Coincident(g1,g-5)
    c: Coincident(g2,g1)
    c: Coincident(g2,g0)
    c: PointOnObject(g3,g-6)
    c: PointOnObject(g3,g-6)
    c: Radius(g3) = 1.5
    c: DistanceX(g3,g0) = 1.5
    c: Coincident(g4,g3)
    c: Coincident(g4,g3)
    c: Horizontal(g4)
FEATURE [PartDesign::Pocket] Pocket329
  BaseFeature = -> Pad507
  Direction = (1,0,2e-16)
  Length = 8
  Length2 = 5
  Placement = pos=(0,0,0) rot=(1,0,0;1.5708rad)
  Profile = -> Sketch731
  ReferenceAxis = -> Sketch731 [N_Axis]
  Refine = true
  Suppressed = false
  Type = 0
FEATURE [Sketcher::SketchObject] Sketch732
  ArcFitTolerance = 1e-06
  AttachmentSupport = -> [Pocket329]
  ExternalGeometry = -> [Pocket329]
  FullyConstrained = true
  MakeInternals = false
  MapMode = 5
  Placement = pos=(0,3.6e-15,0) rot=(-1,0,0;1.5708rad)
  sketch-geometry (10):
    g0: LineSegment StartX=0.05 StartY=-10.7 StartZ=0 EndX=0.05 EndY=-19.4 EndZ=0
    g1: LineSegment StartX=0.05 StartY=-19.4 StartZ=0 EndX=3.55 EndY=-19.4 EndZ=0
    g2: LineSegment StartX=3.55 StartY=-19.4 StartZ=0 EndX=3.55 EndY=-10.7 EndZ=0
    g3: LineSegment StartX=3.55 StartY=-10.7 StartZ=0 EndX=0.05 EndY=-10.7 EndZ=0
    g4: LineSegment StartX=-11.45 StartY=-10.7 StartZ=0 EndX=-11.45 EndY=-19.4 EndZ=0
    g5: LineSegment StartX=-11.45 StartY=-19.4 StartZ=0 EndX=-7.95 EndY=-19.4 EndZ=0
    g6: LineSegment StartX=-7.95 StartY=-19.4 StartZ=0 EndX=-7.95 EndY=-10.7 EndZ=0
    g7: LineSegment StartX=-7.95 StartY=-10.7 StartZ=0 EndX=-11.45 EndY=-10.7 EndZ=0
    g8: LineSegment [constr] StartX=0.05 StartY=-19.4 StartZ=0 EndX=-7.95 EndY=-19.4 EndZ=0
    g9: LineSegment [constr] StartX=0.05 StartY=-10.7 StartZ=0 EndX=-7.95 EndY=-10.7 EndZ=0
  constraints (29):
    c: Coincident(g0,g1)
    c: Coincident(g1,g2)
    c: Coincident(g2,g3)
    c: Coincident(g3,g0)
    c: Vertical(g0)
    c: Vertical(g2)
    c: Horizontal(g1)
    c: Horizontal(g3)
    c: Coincident(g4,g5)
    c: Coincident(g5,g6)
    c: Coincident(g6,g7)
    c: Coincident(g7,g4)
    c: Vertical(g4)
    c: Vertical(g6)
    c: Horizontal(g5)
    c: Horizontal(g7)
    c: DistanceX(g4,g2) = 15
    c: DistanceX(g-4,g-6) = 15.9
    c: DistanceX(g-4,g4) = 0.45
    c: DistanceX(g1,g1) = 3.5
    c: DistanceX(g5,g5) = 3.5
    c: DistanceY(g2,g2) = 8.7
    c: Coincident(g8,g0)
    c: Coincident(g8,g5)
    c: Horizontal(g8)
    c: Coincident(g9,g0)
    c: Coincident(g9,g6)
    c: Horizontal(g9)
    c: DistanceY(g2,g-6) = 2.7
FEATURE [PartDesign::Pad] Pad508
  BaseFeature = -> Pocket329
  Direction = (0,1,2e-16)
  Length = 9.8
  Length2 = 10
  Placement = pos=(0,0,0) rot=(1,0,0;1.5708rad)
  Profile = -> Sketch732
  ReferenceAxis = -> Sketch732 [N_Axis]
  Refine = true
  Suppressed = false
  Type = 0
FEATURE [Sketcher::SketchObject] Sketch733
  ArcFitTolerance = 1e-06
  AttachmentSupport = -> [Pad508]
  ExternalGeometry = -> [Pad508]
  FullyConstrained = true
  MakeInternals = false
  MapMode = 5
  Placement = pos=(3.55,0,0) rot=(0.707107,0,0.707107;3.14159rad)
  sketch-geometry (5):
    g0: LineSegment StartX=14.9 StartY=-9.8 StartZ=0 EndX=16.2 EndY=-5.36289 EndZ=0
    g1: LineSegment StartX=16.2 StartY=-5.36289 StartZ=0 EndX=18.3746 EndY=-6 EndZ=0
    g2: LineSegment StartX=18.3746 StartY=-6 StartZ=0 EndX=19.4 EndY=-2.5 EndZ=0
    g3: LineSegment StartX=14.9 StartY=-9.8 StartZ=0 EndX=19.4 EndY=-9.8 EndZ=0
    g4: LineSegment StartX=19.4 StartY=-2.5 StartZ=0 EndX=19.4 EndY=-9.8 EndZ=0
  constraints (14):
    c: PointOnObject(g0,g-4)
    c: DistanceX(g-4,g0) = 4.2
    c: Coincident(g1,g0)
    c: Coincident(g2,g1)
    c: PointOnObject(g2,g-5)
    c: DistanceY(g-5,g2) = 7.3
    c: Parallel(g0,g2)
    c: DistanceX(g-4,g0) = 5.5
    c: DistanceY(g-5,g1) = 3.8
    c: Perpendicular(g2,g1)
    c: Coincident(g3,g0)
    c: Coincident(g3,g-5)
    c: Coincident(g4,g2)
    c: Coincident(g4,g3)
FEATURE [PartDesign::Pocket] Pocket330
  BaseFeature = -> Pad508
  Direction = (-1,0,2e-16)
  Length = 16
  Length2 = 5
  Placement = pos=(0,0,0) rot=(1,0,0;1.5708rad)
  Profile = -> Sketch733
  ReferenceAxis = -> Sketch733 [N_Axis]
  Refine = true
  Suppressed = false
  Type = 0
FEATURE [Sketcher::SketchObject] Sketch734
  ArcFitTolerance = 1e-06
  AttachmentSupport = -> [Pocket330]
  ExternalGeometry = -> [Pocket330]
  FullyConstrained = true
  MakeInternals = false
  MapMode = 5
  Placement = pos=(3.55,0,0) rot=(0.707107,0,0.707107;3.14159rad)
  sketch-geometry (4):
    g0: LineSegment StartX=16.2 StartY=-5.36289 StartZ=0 EndX=14.9 EndY=-9.8 EndZ=0
    g1: LineSegment StartX=14.9 StartY=-9.8 StartZ=0 EndX=10.7 EndY=-9.8 EndZ=0
    g2: LineSegment StartX=10.7 StartY=-9.8 StartZ=0 EndX=10.7 EndY=-3.75148 EndZ=0
    g3: LineSegment StartX=16.2 StartY=-5.36289 StartZ=0 EndX=10.7 EndY=-3.75148 EndZ=0
  constraints (9):
    c: Coincident(g0,g-5)
    c: Coincident(g0,g-5)
    c: Coincident(g1,g0)
    c: Coincident(g1,g-4)
    c: Coincident(g2,g1)
    c: PointOnObject(g2,g-3)
    c: Coincident(g3,g0)
    c: Coincident(g3,g2)
    c: Parallel(g-6,g3)
FEATURE [PartDesign::Pocket] Pocket331
  BaseFeature = -> Pocket330
  Direction = (-1,0,2e-16)
  Length = 0.5
  Length2 = 5
  Placement = pos=(0,0,0) rot=(1,0,0;1.5708rad)
  Profile = -> Sketch734
  ReferenceAxis = -> Sketch734 [N_Axis]
  Refine = true
  Suppressed = false
  Type = 0
FEATURE [Sketcher::SketchObject] Sketch735
  ArcFitTolerance = 1e-06
  AttachmentSupport = -> [Pocket331]
  ExternalGeometry = -> [Pocket331]
  FullyConstrained = true
  MakeInternals = false
  MapMode = 5
  Placement = pos=(-11.45,0,0) rot=(0.707107,0,-0.707107;3.14159rad)
  sketch-geometry (4):
    g0: LineSegment StartX=-16.2 StartY=-5.36289 StartZ=0 EndX=-14.9 EndY=-9.8 EndZ=0
    g1: LineSegment StartX=-14.9 StartY=-9.8 StartZ=0 EndX=-10.7 EndY=-9.8 EndZ=0
    g2: LineSegment StartX=-10.7 StartY=-9.8 StartZ=0 EndX=-10.7 EndY=-3.75148 EndZ=0
    g3: LineSegment StartX=-10.7 StartY=-3.75148 StartZ=0 EndX=-16.2 EndY=-5.36289 EndZ=0
  constraints (8):
    c: Coincident(g0,g-6)
    c: Coincident(g0,g-5)
    c: Coincident(g1,g0)
    c: Coincident(g1,g-4)
    c: Coincident(g2,g1)
    c: Coincident(g2,g-6)
    c: Coincident(g3,g2)
    c: Coincident(g3,g-6)
FEATURE [PartDesign::Pocket] Pocket332
  BaseFeature = -> Pocket331
  Direction = (1,0,2e-16)
  Length = 0.5
  Length2 = 5
  Placement = pos=(0,0,0) rot=(1,0,0;1.5708rad)
  Profile = -> Sketch735
  ReferenceAxis = -> Sketch735 [N_Axis]
  Refine = true
  Suppressed = false
  Type = 0
FEATURE [Sketcher::SketchObject] Sketch736
  ArcFitTolerance = 1e-06
  AttachmentSupport = -> [Pocket332]
  ExternalGeometry = -> [Pocket332]
  FullyConstrained = true
  MakeInternals = false
  MapMode = 5
  Placement = pos=(3.55,0,0) rot=(0.707107,0,0.707107;3.14159rad)
  sketch-geometry (6):
    g0: LineSegment StartX=19.4 StartY=-2.5 StartZ=0 EndX=19.4 EndY=0 EndZ=0
    g1: LineSegment StartX=19.4 StartY=-2.5 StartZ=0 EndX=20.9 EndY=-2.5 EndZ=0
    g2: LineSegment StartX=20.9 StartY=-2.5 StartZ=0 EndX=20.9 EndY=-4 EndZ=0
    g3: LineSegment StartX=20.9 StartY=-4 StartZ=0 EndX=22.9 EndY=-4 EndZ=0
    g4: LineSegment StartX=22.9 StartY=-4 StartZ=0 EndX=22.9 EndY=-5.3e-15 EndZ=0
    g5: LineSegment StartX=22.9 StartY=-5.3e-15 StartZ=0 EndX=19.4 EndY=0 EndZ=0
  constraints (16):
    c: Coincident(g0,g-4)
    c: Coincident(g0,g-4)
    c: Coincident(g1,g0)
    c: Horizontal(g1)
    c: Coincident(g2,g1)
    c: Vertical(g2)
    c: Coincident(g3,g2)
    c: Horizontal(g3)
    c: Coincident(g4,g3)
    c: PointOnObject(g4,g-3)
    c: Vertical(g4)
    c: Coincident(g5,g4)
    c: Coincident(g5,g0)
    c: DistanceX(g1,g1) = 1.5
    c: DistanceX(g3,g3) = 2
    c: DistanceY(g4,g4) = 4
FEATURE [PartDesign::Pad] Pad509
  BaseFeature = -> Pocket332
  Direction = (1,0,-2e-16)
  Length = 15
  Length2 = 10
  Placement = pos=(0,0,0) rot=(1,0,0;1.5708rad)
  Profile = -> Sketch736
  ReferenceAxis = -> Sketch736 [N_Axis]
  Refine = true
  Reversed = true
  Suppressed = false
  Type = 0
FEATURE [Sketcher::SketchObject] Sketch737
  ArcFitTolerance = 1e-06
  AttachmentSupport = -> [Pad509]
  ExternalGeometry = -> [Pad509]
  FullyConstrained = true
  MakeInternals = false
  MapMode = 5
  Placement = pos=(0.05,0,0) rot=(0.707107,0,-0.707107;3.14159rad)
  sketch-geometry (4):
    g0: LineSegment StartX=-10.7 StartY=-1.3e-15 StartZ=0 EndX=-19.4 EndY=-1.3e-15 EndZ=0
    g1: LineSegment StartX=-19.4 StartY=-1.3e-15 StartZ=0 EndX=-19.4 EndY=-3 EndZ=0
    g2: LineSegment StartX=-19.4 StartY=-3 StartZ=0 EndX=-10.7 EndY=-3 EndZ=0
    g3: LineSegment StartX=-10.7 StartY=-3 StartZ=0 EndX=-10.7 EndY=-1.3e-15 EndZ=0
  constraints (11):
    c: Coincident(g0,g1)
    c: Coincident(g1,g2)
    c: Coincident(g2,g3)
    c: Coincident(g3,g0)
    c: Horizontal(g0)
    c: Horizontal(g2)
    c: Vertical(g1)
    c: Vertical(g3)
    c: Coincident(g0,g-4)
    c: PointOnObject(g1,g-5)
    c: DistanceY(g1,g1) = 3
FEATURE [PartDesign::Pad] Pad510
  BaseFeature = -> Pad509
  Direction = (-1,0,-2e-16)
  Length = 8
  Length2 = 10
  Placement = pos=(0,0,0) rot=(1,0,0;1.5708rad)
  Profile = -> Sketch737
  ReferenceAxis = -> Sketch737 [N_Axis]
  Refine = true
  Suppressed = false
  Type = 0
FEATURE [PartDesign::Pocket] Pocket333
  BaseFeature = -> Pad510
  Direction = (1,0,2e-16)
  Length = 8
  Length2 = 5
  Placement = pos=(0,0,0) rot=(1,0,0;1.5708rad)
  Profile = -> Pad510 [Face39]
  Refine = true
  Suppressed = false
  Type = 0
FEATURE [Sketcher::SketchObject] Sketch738
  ArcFitTolerance = 1e-06
  AttachmentSupport = -> [Pocket333]
  ExternalGeometry = -> [Pocket333]
  FullyConstrained = true
  MakeInternals = false
  MapMode = 5
  Placement = pos=(5e-15,5e-15,22.9) rot=(0,0,1;3.14159rad)
  sketch-geometry (5):
    g0: LineSegment StartX=-3.55 StartY=-4 StartZ=0 EndX=11.45 EndY=-4 EndZ=0
    g1: LineSegment StartX=-3.55 StartY=-4 StartZ=0 EndX=0.2 EndY=-9.8 EndZ=0
    g2: LineSegment StartX=0.2 StartY=-9.8 StartZ=0 EndX=7.7 EndY=-9.8 EndZ=0
    g3: LineSegment StartX=7.7 StartY=-9.8 StartZ=0 EndX=11.45 EndY=-4 EndZ=0
    g4: LineSegment [constr] StartX=7.95 StartY=-9.8 StartZ=0 EndX=7.7 EndY=-9.8 EndZ=0
  constraints (13):
    c: Coincident(g0,g-3)
    c: Coincident(g0,g-3)
    c: Coincident(g1,g0)
    c: Coincident(g2,g1)
    c: Horizontal(g2)
    c: Coincident(g3,g2)
    c: Coincident(g3,g0)
    c: DistanceX(g2,g2) = 7.5
    c: DistanceX(g0,g0) = 15
    c: DistanceX(g2,g0) = 3.75
    c: Coincident(g4,g-4)
    c: Coincident(g4,g2)
    c: Horizontal(g4)
FEATURE [PartDesign::Pad] Pad511
  BaseFeature = -> Pocket333
  Direction = (0,0,1)
  Length = 2
  Length2 = 10
  Placement = pos=(0,0,0) rot=(1,0,0;1.5708rad)
  Profile = -> Sketch738
  ReferenceAxis = -> Sketch738 [N_Axis]
  Refine = true
  Reversed = true
  Suppressed = false
  Type = 0
FEATURE [Sketcher::SketchObject] Sketch739
  ArcFitTolerance = 1e-06
  AttachmentSupport = -> [Pad511]
  ExternalGeometry = -> [Pad511]
  FullyConstrained = true
  MakeInternals = false
  MapMode = 5
  Placement = pos=(0,9.8,-2.2e-15) rot=(-1,0,0;1.5708rad)
  sketch-geometry (4):
    g0: LineSegment StartX=-7.7 StartY=-22.9 StartZ=0 EndX=-7.7 EndY=-29.3 EndZ=0
    g1: LineSegment StartX=-7.7 StartY=-29.3 StartZ=0 EndX=-0.2 EndY=-29.3 EndZ=0
    g2: LineSegment StartX=-0.2 StartY=-29.3 StartZ=0 EndX=-0.2 EndY=-22.9 EndZ=0
    g3: LineSegment StartX=-0.2 StartY=-22.9 StartZ=0 EndX=-7.7 EndY=-22.9 EndZ=0
  constraints (10):
    c: Coincident(g0,g1)
    c: Coincident(g1,g2)
    c: Coincident(g2,g3)
    c: Coincident(g3,g0)
    c: Vertical(g0)
    c: Vertical(g2)
    c: Horizontal(g1)
    c: Coincident(g0,g-5)
    c: Coincident(g2,g-5)
    c: DistanceY(g-6,g0) = 1.7
FEATURE [PartDesign::Pad] Pad512
  BaseFeature = -> Pad511
  Direction = (0,1,2e-16)
  Length = 10
  Length2 = 10
  Placement = pos=(0,0,0) rot=(1,0,0;1.5708rad)
  Profile = -> Sketch739
  ReferenceAxis = -> Sketch739 [N_Axis]
  Refine = true
  Reversed = true
  Suppressed = false
  Type = 0
FEATURE [Sketcher::SketchObject] Sketch740
  ArcFitTolerance = 1e-06
  AttachmentSupport = -> [Pad512]
  ExternalGeometry = -> [Pad512]
  FullyConstrained = true
  MakeInternals = false
  MapMode = 5
  Placement = pos=(0,9.8,5.1e-15) rot=(-1,0,0;1.5708rad)
  sketch-geometry (4):
    g0: LineSegment StartX=-7.7 StartY=-22.9 StartZ=0 EndX=-7.7 EndY=-29.3 EndZ=0
    g1: LineSegment StartX=-7.7 StartY=-29.3 StartZ=0 EndX=-0.2 EndY=-29.3 EndZ=0
    g2: LineSegment StartX=-0.2 StartY=-29.3 StartZ=0 EndX=-0.2 EndY=-22.9 EndZ=0
    g3: LineSegment StartX=-0.2 StartY=-22.9 StartZ=0 EndX=-7.7 EndY=-22.9 EndZ=0
  constraints (10):
    c: Coincident(g0,g1)
    c: Coincident(g1,g2)
    c: Coincident(g2,g3)
    c: Coincident(g3,g0)
    c: Vertical(g0)
    c: Vertical(g2)
    c: Horizontal(g1)
    c: Horizontal(g3)
    c: Coincident(g0,g-4)
    c: Coincident(g1,g-5)
FEATURE [PartDesign::Pocket] Pocket334
  BaseFeature = -> Pad512
  Direction = (0,-1,-2e-16)
  Length = 0.5
  Length2 = 5
  Placement = pos=(0,0,0) rot=(1,0,0;1.5708rad)
  Profile = -> Sketch740
  ReferenceAxis = -> Sketch740 [N_Axis]
  Refine = true
  Suppressed = false
  Type = 0
FEATURE [Sketcher::SketchObject] Sketch741
  ArcFitTolerance = 1e-06
  AttachmentSupport = -> [Pocket334]
  ExternalGeometry = -> [Pocket334]
  FullyConstrained = true
  MakeInternals = false
  MapMode = 5
  Placement = pos=(-0.2,0,0) rot=(0.707107,0,0.707107;3.14159rad)
  sketch-geometry (4):
    g0: LineSegment StartX=22.9 StartY=-9.3 StartZ=0 EndX=29.3 EndY=-4 EndZ=0
    g1: LineSegment StartX=29.3 StartY=-4 StartZ=0 EndX=29.3 EndY=-9.3 EndZ=0
    g2: LineSegment StartX=29.3 StartY=-9.3 StartZ=0 EndX=22.9 EndY=-9.3 EndZ=0
    g3: LineSegment [constr] StartX=29.3 StartY=-4 StartZ=0 EndX=22.9 EndY=-4 EndZ=0
  constraints (9):
    c: Coincident(g0,g-4)
    c: PointOnObject(g0,g-3)
    c: Coincident(g1,g0)
    c: Coincident(g1,g-4)
    c: Coincident(g2,g1)
    c: Coincident(g2,g0)
    c: Coincident(g3,g0)
    c: Coincident(g3,g-5)
    c: Horizontal(g3)
FEATURE [PartDesign::Pocket] Pocket335
  BaseFeature = -> Pocket334
  Direction = (-1,0,2e-16)
  Length = 8
  Length2 = 5
  Placement = pos=(0,0,0) rot=(1,0,0;1.5708rad)
  Profile = -> Sketch741
  ReferenceAxis = -> Sketch741 [N_Axis]
  Refine = true
  Suppressed = false
  Type = 0
FEATURE [Sketcher::SketchObject] Sketch742
  ArcFitTolerance = 1e-06
  AttachmentSupport = -> [Pocket335]
  ExternalGeometry = -> [Pocket335]
  FullyConstrained = true
  MakeInternals = false
  MapMode = 5
  Placement = pos=(0,3.6e-15,0) rot=(-1,0,0;1.5708rad)
  sketch-geometry (6):
    g0: LineSegment StartX=-10.95 StartY=-22.9 StartZ=0 EndX=-7.7 EndY=-22.9 EndZ=0
    g1: LineSegment StartX=-0.2 StartY=-22.9 StartZ=0 EndX=3.05 EndY=-22.9 EndZ=0
    g2: LineSegment StartX=-7.7 StartY=-22.9 StartZ=0 EndX=-7.7 EndY=-28.8 EndZ=0
    g3: LineSegment StartX=-7.7 StartY=-28.8 StartZ=0 EndX=-10.95 EndY=-22.9 EndZ=0
    g4: LineSegment StartX=-0.2 StartY=-22.9 StartZ=0 EndX=-0.2 EndY=-28.8 EndZ=0
    g5: LineSegment StartX=-0.2 StartY=-28.8 StartZ=0 EndX=3.05 EndY=-22.9 EndZ=0
  constraints (16):
    c: PointOnObject(g0,g-3)
    c: DistanceX(g-3,g0) = 0.5
    c: Coincident(g1,g-5)
    c: PointOnObject(g1,g-4)
    c: DistanceX(g1,g-4) = 0.5
    c: Coincident(g0,g-6)
    c: Coincident(g2,g0)
    c: PointOnObject(g2,g-6)
    c: Coincident(g3,g0)
    c: Coincident(g3,g2)
    c: DistanceY(g-6,g2) = 0.5
    c: Coincident(g4,g1)
    c: PointOnObject(g4,g-5)
    c: Coincident(g5,g4)
    c: Coincident(g5,g1)
    c: DistanceY(g-5,g4) = 0.5
FEATURE [PartDesign::Pad] Pad513
  BaseFeature = -> Pocket335
  Direction = (0,1,2e-16)
  Length = 4
  Length2 = 10
  Placement = pos=(0,0,0) rot=(1,0,0;1.5708rad)
  Profile = -> Sketch742
  ReferenceAxis = -> Sketch742 [N_Axis]
  Refine = true
  Suppressed = false
  Type = 0
FEATURE [PartDesign::Plane] DatumPlane
  AttachmentSupport = -> [Pad513]
  Length = 62.1321
  MapMode = 13
  Placement = pos=(-10.2,2.66667,25.0333) rot=(0.44522,-0.44522,-0.77689;1.82061rad)
  ResizeMode = 0
  Width = 85.7262
FEATURE [Sketcher::SketchObject] Sketch743
  ArcFitTolerance = 1e-06
  AttachmentSupport = -> [DatumPlane]
  ExternalGeometry = -> [Pad513]
  FullyConstrained = false
  MakeInternals = false
  MapMode = 5
  Placement = pos=(-10.2,2.66667,25.0333) rot=(0.44522,-0.44522,-0.77689;1.82061rad)
  sketch-geometry (3):
    g0: LineSegment StartX=2.66667 StartY=-2.47257 StartZ=0 EndX=2.66667 EndY=4.94514 EndZ=0
    g1: LineSegment StartX=2.66667 StartY=-2.47257 StartZ=0 EndX=-1.33333 EndY=-2.47257 EndZ=0
    g2: LineSegment StartX=-1.33333 StartY=-2.47257 StartZ=0 EndX=2.66667 EndY=4.94514 EndZ=0
  constraints (6):
    c: Coincident(g0,g-3)
    c: Coincident(g1,g0)
    c: Coincident(g1,g-4)
    c: Horizontal(g1)
    c: Coincident(g2,g-4)
    c: Coincident(g2,g-3)
FEATURE [PartDesign::Pad] Pad514
  BaseFeature = -> Pad513
  Direction = (-0.862799,0,0.505547)
  Length = 1
  Length2 = 10
  Placement = pos=(0,0,0) rot=(1,0,0;1.5708rad)
  Profile = -> Sketch743
  ReferenceAxis = -> Sketch743 [N_Axis]
  Refine = true
  Reversed = true
  Suppressed = false
  Type = 0
FEATURE [PartDesign::Plane] DatumPlane001
  AttachmentSupport = -> [Pad514]
  Length = 62.1321
  MapMode = 13
  Placement = pos=(1.05,2.66667,27.1667) rot=(0.44522,0.44522,0.77689;1.82061rad)
  ResizeMode = 0
  Width = 85.7262
FEATURE [Sketcher::SketchObject] Sketch744
  ArcFitTolerance = 1e-06
  AttachmentSupport = -> [DatumPlane001]
  ExternalGeometry = -> [Pad514]
  FullyConstrained = true
  MakeInternals = false
  MapMode = 5
  Placement = pos=(1.05,2.66667,27.1667) rot=(0.44522,0.44522,0.77689;1.82061rad)
  sketch-geometry (3):
    g0: LineSegment StartX=1.33333 StartY=-4.94514 StartZ=0 EndX=-2.66667 EndY=-4.94514 EndZ=0
    g1: LineSegment StartX=-2.66667 StartY=-4.94514 StartZ=0 EndX=-2.66667 EndY=2.47257 EndZ=0
    g2: LineSegment StartX=-2.66667 StartY=2.47257 StartZ=0 EndX=1.33333 EndY=-4.94514 EndZ=0
  constraints (6):
    c: Coincident(g0,g-4)
    c: Coincident(g0,g-4)
    c: Coincident(g1,g0)
    c: Coincident(g1,g-3)
    c: Coincident(g2,g-3)
    c: Coincident(g2,g-4)
FEATURE [PartDesign::Pad] Pad515
  BaseFeature = -> Pad514
  Direction = (0.862799,-1e-16,0.505547)
  Length = 1
  Length2 = 10
  Placement = pos=(0,0,0) rot=(1,0,0;1.5708rad)
  Profile = -> Sketch744
  ReferenceAxis = -> Sketch744 [N_Axis]
  Refine = true
  Reversed = true
  Suppressed = false
  Type = 0
FEATURE [PartDesign::Plane] DatumPlane002
  AttachmentSupport = -> [Pad515]
  Length = 83.5878
  MapMode = 13
  Placement = pos=(0.883333,5.76667,24.8667) rot=(0.28749,0.513529,0.808478;2.29154rad)
  ResizeMode = 0
  Width = 94.743
FEATURE [Sketcher::SketchObject] Sketch745
  ArcFitTolerance = 1e-06
  AttachmentSupport = -> [DatumPlane002]
  ExternalGeometry = -> [Pad515]
  FullyConstrained = true
  MakeInternals = false
  MapMode = 5
  Placement = pos=(0.883333,5.76667,24.8667) rot=(0.28749,0.513529,0.808478;2.29154rad)
  sketch-geometry (3):
    g0: LineSegment StartX=-0.939745 StartY=4.34542 StartZ=0 EndX=-2.63868 EndY=-2.17271 EndZ=0
    g1: LineSegment StartX=-2.63868 StartY=-2.17271 StartZ=0 EndX=3.57843 EndY=-2.17271 EndZ=0
    g2: LineSegment StartX=3.57843 StartY=-2.17271 StartZ=0 EndX=-0.939745 EndY=4.34542 EndZ=0
  constraints (6):
    c: Coincident(g0,g-4)
    c: Coincident(g0,g-4)
    c: Coincident(g1,g0)
    c: Coincident(g1,g-3)
    c: Coincident(g2,g-3)
    c: Coincident(g2,g-4)
FEATURE [PartDesign::Pad] Pad516
  BaseFeature = -> Pad515
  Direction = (0.771642,0.473176,0.425057)
  Length = 4
  Length2 = 10
  Placement = pos=(0,0,0) rot=(1,0,0;1.5708rad)
  Profile = -> Sketch745
  ReferenceAxis = -> Sketch745 [N_Axis]
  Refine = true
  Reversed = true
  Suppressed = false
  Type = 0
FEATURE [PartDesign::Plane] DatumPlane003
  AttachmentSupport = -> [Pad516]
  Length = 83.5878
  MapMode = 13
  Placement = pos=(-8.78333,5.76667,24.8667) rot=(0.833374,0.46655,0.296343;2.1679rad)
  ResizeMode = 0
  Width = 94.743
FEATURE [Sketcher::SketchObject] Sketch746
  ArcFitTolerance = 1e-06
  AttachmentSupport = -> [DatumPlane003]
  ExternalGeometry = -> [Pad516]
  FullyConstrained = true
  MakeInternals = false
  MapMode = 5
  Placement = pos=(-8.78333,5.76667,24.8667) rot=(0.833374,0.46655,0.296343;2.1679rad)
  sketch-geometry (3):
    g0: LineSegment StartX=3.57843 StartY=-2.17271 StartZ=0 EndX=-0.939745 EndY=4.34542 EndZ=0
    g1: LineSegment StartX=-0.939745 StartY=4.34542 StartZ=0 EndX=-2.63868 EndY=-2.17271 EndZ=0
    g2: LineSegment StartX=-2.63868 StartY=-2.17271 StartZ=0 EndX=3.57843 EndY=-2.17271 EndZ=0
  constraints (6):
    c: Coincident(g0,g-4)
    c: Coincident(g0,g-3)
    c: Coincident(g1,g-3)
    c: Coincident(g1,g-3)
    c: Coincident(g2,g1)
    c: Coincident(g2,g-4)
FEATURE [PartDesign::Pad] Pad517
  BaseFeature = -> Pad516
  Direction = (0.771642,-0.473176,-0.425057)
  Length = 4
  Length2 = 10
  Placement = pos=(0,0,0) rot=(1,0,0;1.5708rad)
  Profile = -> Sketch746
  ReferenceAxis = -> Sketch746 [N_Axis]
  Refine = true
  Suppressed = false
  Type = 0
FEATURE [Sketcher::SketchObject] Sketch747
  ArcFitTolerance = 1e-06
  AttachmentSupport = -> [Pad517]
  ExternalGeometry = -> [Pad517]
  FullyConstrained = true
  MakeInternals = false
  MapMode = 5
  Placement = pos=(0,9.8,5.1e-15) rot=(-1,0,0;1.5708rad)
  sketch-geometry (4):
    g0: LineSegment StartX=-6.35 StartY=-29.3 StartZ=0 EndX=-1.55 EndY=-29.3 EndZ=0
    g1: LineSegment StartX=-1.55 StartY=-29.3 StartZ=0 EndX=-1.55 EndY=-24.4 EndZ=0
    g2: LineSegment StartX=-1.55 StartY=-24.4 StartZ=0 EndX=-6.35 EndY=-24.4 EndZ=0
    g3: LineSegment StartX=-6.35 StartY=-24.4 StartZ=0 EndX=-6.35 EndY=-29.3 EndZ=0
  constraints (13):
    c: Coincident(g0,g1)
    c: Coincident(g1,g2)
    c: Coincident(g2,g3)
    c: Coincident(g3,g0)
    c: Horizontal(g0)
    c: Horizontal(g2)
    c: Vertical(g1)
    c: Vertical(g3)
    c: PointOnObject(g0,g-4)
    c: DistanceX(g-3,g-3) = 7.5
    c: DistanceX(g2,g2) = 4.8
    c: DistanceX(g-3,g2) = 1.35
    c: DistanceY(g2,g-3) = 1.5
FEATURE [PartDesign::Pocket] Pocket336
  BaseFeature = -> Pad517
  Direction = (0,-1,-2e-16)
  Length = 9.8
  Length2 = 5
  Placement = pos=(0,0,0) rot=(1,0,0;1.5708rad)
  Profile = -> Sketch747
  ReferenceAxis = -> Sketch747 [N_Axis]
  Refine = true
  Suppressed = false
  Type = 0
FEATURE [Sketcher::SketchObject] Sketch748
  ArcFitTolerance = 1e-06
  AttachmentSupport = -> [Pocket336]
  ExternalGeometry = -> [Pocket336]
  FullyConstrained = true
  MakeInternals = false
  MapMode = 5
  Placement = pos=(6.05,0,0) rot=(0.707107,0,0.707107;3.14159rad)
  sketch-geometry (1):
    g0: Circle CenterX=21.9 CenterY=1.2 CenterZ=0 NormalX=0 NormalY=0 NormalZ=1 AngleXU=0 Radius=3.35
  constraints (4):
    c: PointOnObject(g0,g-3)
    c: Diameter(g0) = 6.7
    c: DistanceX(g-3,g-3) = 0
    c: DistanceX(g-3,g0) = 3.85
FEATURE [PartDesign::Pad] Pad518
  BaseFeature = -> Pocket336
  Direction = (1,0,-2e-16)
  Length = 7.2
  Length2 = 10
  Placement = pos=(0,0,0) rot=(1,0,0;1.5708rad)
  Profile = -> Sketch748
  ReferenceAxis = -> Sketch748 [N_Axis]
  Refine = true
  Reversed = true
  Suppressed = false
  Type = 0
FEATURE [PartDesign::Pocket] Pocket337
  BaseFeature = -> Pad518
  Direction = (-1,0,0)
  Length = 7.5
  Length2 = 5
  Placement = pos=(0,0,0) rot=(1,0,0;1.5708rad)
  Profile = -> Pad518 [Face2]
  Refine = true
  Suppressed = false
  Type = 0
FEATURE [Sketcher::SketchObject] Sketch749
  ArcFitTolerance = 1e-06
  AttachmentSupport = -> [Pocket337]
  ExternalGeometry = -> [Pocket337]
  FullyConstrained = true
  MakeInternals = false
  MapMode = 5
  Placement = pos=(6.05,0,1.6e-15) rot=(0.707107,0,0.707107;3.14159rad)
  sketch-geometry (1):
    g0: Circle CenterX=21.9 CenterY=1.2 CenterZ=0 NormalX=0 NormalY=0 NormalZ=1 AngleXU=0 Radius=1.85
  constraints (2):
    c: Coincident(g0,g-3)
    c: Diameter(g0) = 3.7
FEATURE [PartDesign::Pocket] Pocket338
  BaseFeature = -> Pocket337
  Direction = (-1,0,2e-16)
  Length = 6.2
  Length2 = 5
  Placement = pos=(0,0,0) rot=(1,0,0;1.5708rad)
  Profile = -> Sketch749
  ReferenceAxis = -> Sketch749 [N_Axis]
  Refine = true
  Suppressed = false
  Type = 0
FEATURE [Sketcher::SketchObject] Sketch750
  ArcFitTolerance = 1e-06
  AttachmentSupport = -> [Pocket338]
  ExternalGeometry = -> [Pocket338]
  FullyConstrained = true
  MakeInternals = false
  MapMode = 5
  Placement = pos=(6.05,0,1.6e-15) rot=(0.707107,0,0.707107;3.14159rad)
  sketch-geometry (2):
    g0: LineSegment StartX=18.55 StartY=1.2 StartZ=0 EndX=25.25 EndY=1.2 EndZ=0
    g1: ArcOfCircle CenterX=21.9 CenterY=1.2 CenterZ=0 NormalX=0 NormalY=0 NormalZ=1 AngleXU=0 Radius=3.35 StartAngle=0 EndAngle=3.14159
  constraints (5):
    c: Coincident(g0,g-5)
    c: Coincident(g0,g-4)
    c: Coincident(g1,g0)
    c: Coincident(g1,g0)
    c: Coincident(g1,g-3)
FEATURE [PartDesign::Pocket] Pocket339
  BaseFeature = -> Pocket338
  Direction = (-1,0,2e-16)
  Length = 3.2
  Length2 = 5
  Placement = pos=(0,0,0) rot=(1,0,0;1.5708rad)
  Profile = -> Sketch750
  ReferenceAxis = -> Sketch750 [N_Axis]
  Refine = true
  Suppressed = false
  Type = 0
FEATURE [Sketcher::SketchObject] Sketch751
  ArcFitTolerance = 1e-06
  AttachmentSupport = -> [Pocket339]
  ExternalGeometry = -> [Pocket339]
  FullyConstrained = true
  MakeInternals = false
  MapMode = 5
  Placement = pos=(0,1.1422e-08,0) rot=(-1,0,0;1.5708rad)
  sketch-geometry (22):
    g0: LineSegment StartX=-9.45781 StartY=-26.3 StartZ=0 EndX=-9.75078 EndY=-25.8 EndZ=0
    g1: LineSegment StartX=-9.45781 StartY=-26.3 StartZ=0 EndX=-13.95 EndY=-26.3 EndZ=0
    g2: LineSegment StartX=-13.95 StartY=-26.3 StartZ=0 EndX=-13.95 EndY=-25.8 EndZ=0
    g3: LineSegment StartX=-9.75078 StartY=-25.8 StartZ=0 EndX=-13.95 EndY=-25.8 EndZ=0
    g4: LineSegment StartX=-13.95 StartY=-24 StartZ=0 EndX=-10.8055 EndY=-24 EndZ=0
    g5: LineSegment StartX=-10.8055 StartY=-24 StartZ=0 EndX=-11.0984 EndY=-23.5 EndZ=0
    g6: LineSegment StartX=-11.0984 StartY=-23.5 StartZ=0 EndX=-13.95 EndY=-23.5 EndZ=0
    g7: LineSegment StartX=-13.95 StartY=-23.5 StartZ=0 EndX=-13.95 EndY=-24 EndZ=0
    g8: LineSegment StartX=-13.95 StartY=-21.2 StartZ=0 EndX=-13.95 EndY=-21.7 EndZ=0
    g9: LineSegment StartX=-13.95 StartY=-21.7 StartZ=0 EndX=-11.45 EndY=-21.7 EndZ=0
    g10: LineSegment StartX=-11.45 StartY=-21.7 StartZ=0 EndX=-11.45 EndY=-21.2 EndZ=0
    g11: LineSegment StartX=-11.45 StartY=-21.2 StartZ=0 EndX=-13.95 EndY=-21.2 EndZ=0
    g12: LineSegment StartX=-13.95 StartY=-18.9 StartZ=0 EndX=-13.95 EndY=-19.4 EndZ=0
    g13: LineSegment StartX=-13.95 StartY=-19.4 StartZ=0 EndX=-11.45 EndY=-19.4 EndZ=0
    g14: LineSegment StartX=-11.45 StartY=-19.4 StartZ=0 EndX=-11.45 EndY=-18.9 EndZ=0
    g15: LineSegment StartX=-11.45 StartY=-18.9 StartZ=0 EndX=-13.95 EndY=-18.9 EndZ=0
    g16: LineSegment [constr] StartX=-9.45781 StartY=-26.3 StartZ=0 EndX=1.55781 EndY=-26.3 EndZ=0
    g17: LineSegment [constr] StartX=-9.75078 StartY=-25.8 StartZ=0 EndX=1.85078 EndY=-25.8 EndZ=0
    g18: LineSegment StartX=1.85078 StartY=-25.8 StartZ=0 EndX=1.55781 EndY=-26.3 EndZ=0
    g19: LineSegment StartX=1.55781 StartY=-26.3 StartZ=0 EndX=6.05 EndY=-26.3 EndZ=0
    g20: LineSegment StartX=1.85078 StartY=-25.8 StartZ=0 EndX=6.05 EndY=-25.8 EndZ=0
    g21: LineSegment StartX=6.05 StartY=-25.8 StartZ=0 EndX=6.05 EndY=-26.3 EndZ=0
  constraints (64):
    c: PointOnObject(g0,g-4)
    c: PointOnObject(g0,g-4)
    c: Coincident(g1,g0)
    c: PointOnObject(g1,g-5)
    c: Horizontal(g1)
    c: Coincident(g2,g1)
    c: PointOnObject(g2,g-5)
    c: Coincident(g3,g0)
    c: Coincident(g3,g2)
    c: Horizontal(g3)
    c: DistanceY(g-3,g1) = 4.7
    c: DistanceY(g2,g2) = 0.5
    c: PointOnObject(g4,g-5)
    c: Horizontal(g4)
    c: DistanceY(g2,g4) = 1.8
    c: PointOnObject(g4,g-4)
    c: Coincident(g5,g4)
    c: PointOnObject(g5,g-4)
    c: Coincident(g6,g5)
    c: PointOnObject(g6,g-5)
    c: Coincident(g7,g6)
    c: Coincident(g7,g4)
    c: Horizontal(g6)
    c: DistanceY(g7,g7) = 0.5
    c: Coincident(g8,g9)
    c: Coincident(g9,g10)
    c: Coincident(g10,g11)
    c: Coincident(g11,g8)
    c: Vertical(g8)
    c: Vertical(g10)
    c: Horizontal(g9)
    c: Horizontal(g11)
    c: PointOnObject(g8,g-5)
    c: PointOnObject(g9,g-6)
    c: DistanceY(g8,g8) = 0.5
    c: DistanceY(g6,g8) = 1.8
    c: Coincident(g12,g13)
    c: Coincident(g13,g14)
    c: Coincident(g14,g15)
    c: Coincident(g15,g12)
    c: Vertical(g12)
    c: Vertical(g14)
    c: Horizontal(g13)
    c: Horizontal(g15)
    c: PointOnObject(g12,g-5)
    c: PointOnObject(g13,g-6)
    c: DistanceY(g12,g12) = 0.5
    c: DistanceY(g8,g12) = 1.8
    c: Coincident(g16,g0)
    c: PointOnObject(g16,g-8)
    c: Horizontal(g16)
    c: Coincident(g17,g0)
    c: PointOnObject(g17,g-8)
    c: Horizontal(g17)
    c: Coincident(g18,g17)
    c: Coincident(g18,g16)
    c: Coincident(g19,g18)
    c: PointOnObject(g19,g-7)
    c: Horizontal(g19)
    c: Coincident(g20,g17)
    c: PointOnObject(g20,g-7)
    c: Horizontal(g20)
    c: Coincident(g21,g20)
    c: Coincident(g21,g19)
FEATURE [PartDesign::Pocket] Pocket340
  BaseFeature = -> Pocket339
  Direction = (1.53512e-09,-1,-5.66476e-10)
  Length = 0.5
  Length2 = 5
  Placement = pos=(0,0,0) rot=(1,0,0;1.5708rad)
  Profile = -> Sketch751
  ReferenceAxis = -> Sketch751 [N_Axis]
  Refine = true
  Suppressed = false
  Type = 0
FEATURE [Sketcher::SketchObject] Sketch752
  ArcFitTolerance = 1e-06
  AttachmentSupport = -> [Pocket340]
  ExternalGeometry = -> [Pocket340]
  FullyConstrained = true
  MakeInternals = false
  MapMode = 5
  Placement = pos=(7.67558e-10,-0.5,-2.83238e-10) rot=(-1,0,0;1.5708rad)
  sketch-geometry (20):
    g0: LineSegment StartX=-13.95 StartY=-18.9 StartZ=0 EndX=-13.95 EndY=-19.4 EndZ=0
    g1: LineSegment StartX=-13.95 StartY=-19.4 StartZ=0 EndX=-13.45 EndY=-19.4 EndZ=0
    g2: LineSegment StartX=-13.45 StartY=-19.4 StartZ=0 EndX=-13.45 EndY=-18.9 EndZ=0
    g3: LineSegment StartX=-13.45 StartY=-18.9 StartZ=0 EndX=-13.95 EndY=-18.9 EndZ=0
    g4: LineSegment StartX=-13.95 StartY=-21.2 StartZ=0 EndX=-13.95 EndY=-21.7 EndZ=0
    g5: LineSegment StartX=-13.95 StartY=-21.7 StartZ=0 EndX=-13.45 EndY=-21.7 EndZ=0
    g6: LineSegment StartX=-13.45 StartY=-21.7 StartZ=0 EndX=-13.45 EndY=-21.2 EndZ=0
    g7: LineSegment StartX=-13.45 StartY=-21.2 StartZ=0 EndX=-13.95 EndY=-21.2 EndZ=0
    g8: LineSegment StartX=-13.95 StartY=-23.5 StartZ=0 EndX=-13.95 EndY=-24 EndZ=0
    g9: LineSegment StartX=-13.95 StartY=-24 StartZ=0 EndX=-13.45 EndY=-24 EndZ=0
    g10: LineSegment StartX=-13.45 StartY=-24 StartZ=0 EndX=-13.45 EndY=-23.5 EndZ=0
    g11: LineSegment StartX=-13.45 StartY=-23.5 StartZ=0 EndX=-13.95 EndY=-23.5 EndZ=0
    g12: LineSegment StartX=-13.95 StartY=-25.8 StartZ=0 EndX=-13.95 EndY=-26.3 EndZ=0
    g13: LineSegment StartX=-13.95 StartY=-26.3 StartZ=0 EndX=-13.45 EndY=-26.3 EndZ=0
    g14: LineSegment StartX=-13.45 StartY=-26.3 StartZ=0 EndX=-13.45 EndY=-25.8 EndZ=0
    g15: LineSegment StartX=-13.45 StartY=-25.8 StartZ=0 EndX=-13.95 EndY=-25.8 EndZ=0
    g16: LineSegment StartX=6.05 StartY=-25.8 StartZ=0 EndX=5.55 EndY=-25.8 EndZ=0
    g17: LineSegment StartX=5.55 StartY=-25.8 StartZ=0 EndX=5.55 EndY=-26.3 EndZ=0
    g18: LineSegment StartX=5.55 StartY=-26.3 StartZ=0 EndX=6.05 EndY=-26.3 EndZ=0
    g19: LineSegment StartX=6.05 StartY=-26.3 StartZ=0 EndX=6.05 EndY=-25.8 EndZ=0
  constraints (55):
    c: Coincident(g0,g1)
    c: Coincident(g1,g2)
    c: Coincident(g2,g3)
    c: Coincident(g3,g0)
    c: Vertical(g0)
    c: Vertical(g2)
    c: Horizontal(g1)
    c: Horizontal(g3)
    c: Coincident(g0,g-14)
    c: PointOnObject(g1,g-13)
    c: Coincident(g4,g5)
    c: Coincident(g5,g6)
    c: Coincident(g6,g7)
    c: Coincident(g7,g4)
    c: Vertical(g4)
    c: Vertical(g6)
    c: Horizontal(g5)
    c: Horizontal(g7)
    c: Coincident(g4,g-10)
    c: PointOnObject(g5,g-11)
    c: Coincident(g8,g9)
    c: Coincident(g9,g10)
    c: Coincident(g10,g11)
    c: Coincident(g11,g8)
    c: Vertical(g8)
    c: Vertical(g10)
    c: Horizontal(g9)
    c: Horizontal(g11)
    c: Coincident(g8,g-8)
    c: PointOnObject(g9,g-4)
    c: Coincident(g12,g13)
    c: Coincident(g13,g14)
    c: Coincident(g14,g15)
    c: Coincident(g15,g12)
    c: Vertical(g12)
    c: Vertical(g14)
    c: Horizontal(g13)
    c: Horizontal(g15)
    c: Coincident(g12,g-7)
    c: PointOnObject(g13,g-6)
    c: DistanceX(g15,g15) = 0.5
    c: DistanceX(g11,g11) = 0.5
    c: DistanceX(g7,g7) = 0.5
    c: DistanceX(g3,g3) = 0.5
    c: Coincident(g16,g17)
    c: Coincident(g17,g18)
    c: Coincident(g18,g19)
    c: Coincident(g19,g16)
    c: Horizontal(g16)
    c: Horizontal(g18)
    c: Vertical(g17)
    c: Vertical(g19)
    c: Coincident(g16,g-17)
    c: PointOnObject(g17,g-16)
    c: DistanceX(g16,g16) = 0.5
FEATURE [PartDesign::Pocket] Pocket341
  BaseFeature = -> Pocket340
  Direction = (1.53512e-09,-1,-5.66476e-10)
  Length = 5
  Length2 = 5
  Placement = pos=(0,0,0) rot=(1,0,0;1.5708rad)
  Profile = -> Sketch752
  ReferenceAxis = -> Sketch752 [N_Axis]
  Refine = true
  Suppressed = false
  Type = 0
FEATURE [Sketcher::SketchObject] Sketch753
  ArcFitTolerance = 1e-06
  AttachmentSupport = -> [Pocket341]
  ExternalGeometry = -> [Pocket341]
  FullyConstrained = true
  MakeInternals = false
  MapMode = 5
  Placement = pos=(0,-1.2,5e-16) rot=(1,0,0;1.5708rad)
  sketch-geometry (3):
    g0: Circle CenterX=-3.95 CenterY=21.9 CenterZ=0 NormalX=0 NormalY=0 NormalZ=1 AngleXU=0 Radius=0.75
    g1: Circle CenterX=-3.95 CenterY=11.9 CenterZ=0 NormalX=0 NormalY=0 NormalZ=1 AngleXU=0 Radius=0.75
    g2: LineSegment [constr] StartX=-3.95 StartY=21.9 StartZ=0 EndX=-3.95 EndY=11.9 EndZ=0
  constraints (10):
    c: Radius(g0) = 0.75
    c: Radius(g1) = 0.75
    c: Coincident(g2,g0)
    c: Coincident(g2,g1)
    c: Vertical(g2)
    c: DistanceY(g-3,g-3) = 6.7
    c: DistanceY(g0,g-3) = 3.35
    c: DistanceY(g2,g2) = 10
    c: DistanceX(g-4,g-4) = 15.9
    c: DistanceX(g-4,g0) = 7.95
FEATURE [PartDesign::Pocket] Pocket342
  BaseFeature = -> Pocket341
  Direction = (0,1,-2e-16)
  Length = 4
  Length2 = 5
  Placement = pos=(0,0,0) rot=(1,0,0;1.5708rad)
  Profile = -> Sketch753
  ReferenceAxis = -> Sketch753 [N_Axis]
  Refine = true
  Suppressed = false
  Type = 0
FEATURE [PartDesign::Chamfer] Chamfer022
  Angle = 20
  Base = -> Pocket342 [Edge33,Edge29]
  BaseFeature = -> Pocket342
  ChamferType = 2
  FlipDirection = false
  Placement = pos=(0,0,0) rot=(1,0,0;1.5708rad)
  Refine = true
  Size = 3
  Size2 = 1
  SupportTransform = false
  Suppressed = false
  UseAllEdges = false
FEATURE [PartDesign::Body] Body037  label="Front_Head"
  AllowCompound = false
  Group = -> [Sketch729,Pad506,Sketch730,Pad507,Sketch731,Pocket329,Sketch732,Pad508,Sketch733,Pocket330,Sketch734,Pocket331,Sketch735,Pocket332,Sketch736,Pad509,Sketch737,Pad510,Pocket333,Sketch738,Pad511,Sketch739,Pad512,Sketch740,Pocket334,Sketch741,Pocket335,Sketch742,Pad513,DatumPlane,Sketch743,Pad514,DatumPlane001,Sketch744,Pad515,DatumPlane002,Sketch745,Pad516,DatumPlane003,Sketch746,Pad517,Sketch747,+15 more]
  Origin = -> Origin040
  Placement = pos=(39.95,2,2.5) rot=(0,0,1;0rad)
  Tip = -> Chamfer022
FEATURE [PartDesign::SubShapeBinder] Binder001
  BindCopyOnChange = 0
  BindMode = 0
  ClaimChildren = false
  Context = -> Part001 [Body038.Binder001.]
  Fuse = false
  MakeFace = true
  OffsetFill = false
  OffsetIntersection = false
  OffsetJoinType = 0
  OffsetOpenResult = false
  PartialLoad = false
  Refine = true
  Relative = true
  Support = -> [Body037[Chamfer022.Face46]]
  _Version = 2
FEATURE [Sketcher::SketchObject] Sketch754
  ArcFitTolerance = 1e-06
  AttachmentSupport = -> [Binder001]
  ExternalGeometry = -> [Binder001]
  FullyConstrained = true
  MakeInternals = false
  MapMode = 5
  Placement = pos=(-3.07023e-09,2,1.13295e-09) rot=(0,0.707107,0.707107;3.14159rad)
  sketch-geometry (4):
    g0: LineSegment StartX=-38.35 StartY=33.5 StartZ=0 EndX=-38.35 EndY=26.95 EndZ=0
    g1: LineSegment StartX=-38.35 StartY=26.95 StartZ=0 EndX=-33.65 EndY=26.95 EndZ=0
    g2: LineSegment StartX=-33.65 StartY=26.95 StartZ=0 EndX=-33.65 EndY=33.5 EndZ=0
    g3: LineSegment StartX=-33.65 StartY=33.5 StartZ=0 EndX=-38.35 EndY=33.5 EndZ=0
  constraints (12):
    c: Coincident(g0,g1)
    c: Coincident(g1,g2)
    c: Coincident(g2,g3)
    c: Coincident(g3,g0)
    c: Vertical(g0)
    c: Vertical(g2)
    c: Horizontal(g1)
    c: Horizontal(g3)
    c: PointOnObject(g0,g-4)
    c: DistanceY(g-3,g0) = 0.05
    c: DistanceX(g-3,g0) = 0.05
    c: DistanceX(g1,g-3) = 0.05
FEATURE [PartDesign::Pad] Pad519
  Direction = (-1.53512e-09,1,5.66476e-10)
  Length = 10
  Length2 = 10
  Profile = -> Sketch754
  ReferenceAxis = -> Sketch754 [N_Axis]
  Refine = true
  Suppressed = false
  Type = 0
FEATURE [Sketcher::SketchObject] Sketch755
  ArcFitTolerance = 1e-06
  AttachmentSupport = -> [Pad519]
  ExternalGeometry = -> [Pad519]
  FullyConstrained = true
  MakeInternals = false
  MapMode = 5
  Placement = pos=(33.65,5.16566e-08,0) rot=(0.57735,-0.57735,-0.57735;2.0944rad)
  sketch-geometry (3):
    g0: LineSegment StartX=-12 StartY=33.5 StartZ=0 EndX=-9.9 EndY=26.95 EndZ=0
    g1: LineSegment StartX=-12 StartY=33.5 StartZ=0 EndX=-12 EndY=26.95 EndZ=0
    g2: LineSegment StartX=-9.9 StartY=26.95 StartZ=0 EndX=-12 EndY=26.95 EndZ=0
  constraints (7):
    c: Coincident(g0,g-4)
    c: Coincident(g1,g0)
    c: Coincident(g2,g0)
    c: Coincident(g2,g1)
    c: Coincident(g1,g-4)
    c: PointOnObject(g0,g-3)
    c: DistanceX(g2,g2) = 2.1
FEATURE [PartDesign::Pocket] Pocket343
  BaseFeature = -> Pad519
  Direction = (1,1.53512e-09,1e-16)
  Length = 5
  Length2 = 5
  Profile = -> Sketch755
  ReferenceAxis = -> Sketch755 [N_Axis]
  Refine = true
  Suppressed = false
  Type = 0
FEATURE [Sketcher::SketchObject] Sketch756
  ArcFitTolerance = 1e-06
  AttachmentSupport = -> [Pocket343]
  ExternalGeometry = -> [Pocket343]
  FullyConstrained = true
  MakeInternals = false
  MapMode = 5
  Placement = pos=(33.65,5.16566e-08,0) rot=(0.57735,-0.57735,-0.57735;2.0944rad)
  sketch-geometry (3):
    g0: LineSegment StartX=-12 StartY=33.5 StartZ=0 EndX=-6 EndY=33.5 EndZ=0
    g1: LineSegment StartX=-12 StartY=33.5 StartZ=0 EndX=-11.4407 EndY=31.7556 EndZ=0
    g2: LineSegment StartX=-11.4407 StartY=31.7556 StartZ=0 EndX=-6 EndY=33.5 EndZ=0
  constraints (8):
    c: Coincident(g0,g-4)
    c: Coincident(g1,g0)
    c: Coincident(g2,g1)
    c: Coincident(g2,g0)
    c: PointOnObject(g0,g-3)
    c: PointOnObject(g1,g-4)
    c: DistanceX(g0,g0) = 6
    c: Perpendicular(g-4,g2)
FEATURE [PartDesign::Pocket] Pocket344
  BaseFeature = -> Pocket343
  Direction = (1,1.53512e-09,1e-16)
  Length = 5
  Length2 = 5
  Profile = -> Sketch756
  ReferenceAxis = -> Sketch756 [N_Axis]
  Refine = true
  Suppressed = false
  Type = 0
FEATURE [Sketcher::SketchObject] Sketch757
  ArcFitTolerance = 1e-06
  AttachmentOffset = pos=(0,0,-12) rot=(0,0,1;0rad)
  AttachmentSupport = -> [XZ_Plane041]
  ExternalGeometry = -> [Pocket344]
  FullyConstrained = true
  MakeInternals = false
  MapMode = 5
  Placement = pos=(0,12,-2.7e-15) rot=(1,0,0;1.5708rad)
  sketch-geometry (4):
    g0: LineSegment StartX=37.65 StartY=31.0556 StartZ=0 EndX=34.35 EndY=31.0556 EndZ=0
    g1: LineSegment StartX=34.35 StartY=31.0556 StartZ=0 EndX=34.35 EndY=26.95 EndZ=0
    g2: LineSegment StartX=34.35 StartY=26.95 StartZ=0 EndX=37.65 EndY=26.95 EndZ=0
    g3: LineSegment StartX=37.65 StartY=26.95 StartZ=0 EndX=37.65 EndY=31.0556 EndZ=0
  constraints (12):
    c: Coincident(g0,g1)
    c: Coincident(g1,g2)
    c: Coincident(g2,g3)
    c: Coincident(g3,g0)
    c: Horizontal(g0)
    c: Horizontal(g2)
    c: Vertical(g1)
    c: Vertical(g3)
    c: PointOnObject(g2,g-6)
    c: DistanceY(g0,g-5) = 0.7
    c: DistanceX(g0,g-5) = 0.7
    c: DistanceX(g-4,g0) = 0.7
FEATURE [PartDesign::Pocket] Pocket345
  BaseFeature = -> Pocket344
  Direction = (0,1,-2e-16)
  Length = 2.1
  Length2 = 5
  Profile = -> Sketch757
  ReferenceAxis = -> Sketch757 [N_Axis]
  Refine = true
  Reversed = true
  Suppressed = false
  Type = 0
FEATURE [PartDesign::Body] Body038  label="Forehead"
  AllowCompound = false
  Group = -> [Binder001,Sketch754,Pad519,Sketch755,Pocket343,Sketch756,Pocket344,Sketch757,Pocket345]
  Origin = -> Origin041
  Tip = -> Pocket345
FEATURE [PartDesign::SubShapeBinder] Binder002
  BindCopyOnChange = 0
  BindMode = 2
  ClaimChildren = false
  Context = -> Part001 [Body039.Binder002.]
  Fuse = false
  MakeFace = true
  OffsetFill = false
  OffsetIntersection = false
  OffsetJoinType = 0
  OffsetOpenResult = false
  PartialLoad = false
  Refine = true
  Relative = true
  _Version = 2
FEATURE [Sketcher::SketchObject] Sketch758
  ArcFitTolerance = 1e-06
  AttachmentSupport = -> [Binder002]
  ExternalGeometry = -> [Binder002]
  FullyConstrained = true
  MakeInternals = false
  MapMode = 5
  Placement = pos=(0,4.5,-1e-15) rot=(0,0.707107,0.707107;3.14159rad)
  sketch-geometry (4):
    g0: LineSegment StartX=-43.5 StartY=23.35 StartZ=0 EndX=-43.5 EndY=21.95 EndZ=0
    g1: LineSegment StartX=-43.5 StartY=21.95 StartZ=0 EndX=-28.5 EndY=21.95 EndZ=0
    g2: LineSegment StartX=-28.5 StartY=21.95 StartZ=0 EndX=-28.5 EndY=23.35 EndZ=0
    g3: LineSegment StartX=-28.5 StartY=23.35 StartZ=0 EndX=-43.5 EndY=23.35 EndZ=0
  constraints (12):
    c: Coincident(g0,g1)
    c: Coincident(g1,g2)
    c: Coincident(g2,g3)
    c: Coincident(g3,g0)
    c: Vertical(g0)
    c: Vertical(g2)
    c: Horizontal(g1)
    c: Horizontal(g3)
    c: PointOnObject(g0,g-3)
    c: PointOnObject(g1,g-4)
    c: DistanceY(g-4,g1) = 0.05
    c: DistanceY(g2,g-4) = 0.05
FEATURE [PartDesign::Pad] Pad520
  Direction = (0,1,-2e-16)
  Length = 3
  Length2 = 10
  Profile = -> Sketch758
  ReferenceAxis = -> Sketch758 [N_Axis]
  Refine = true
  Suppressed = false
  Type = 0
FEATURE [Sketcher::SketchObject] Sketch759
  ArcFitTolerance = 1e-06
  AttachmentSupport = -> [Pad520]
  ExternalGeometry = -> [Pad520]
  FullyConstrained = true
  MakeInternals = false
  MapMode = 5
  Placement = pos=(43.5,0,0) rot=(0.57735,0.57735,0.57735;2.0944rad)
  sketch-geometry (3):
    g0: LineSegment StartX=7.5 StartY=21.95 StartZ=0 EndX=7.5 EndY=21.0898 EndZ=0
    g1: LineSegment StartX=7.5 StartY=21.0898 StartZ=0 EndX=4.5 EndY=21.95 EndZ=0
    g2: LineSegment StartX=7.5 StartY=21.95 StartZ=0 EndX=4.5 EndY=21.95 EndZ=0
  constraints (7):
    c: Coincident(g0,g-3)
    c: Vertical(g0)
    c: Coincident(g1,g0)
    c: Coincident(g1,g-3)
    c: Coincident(g2,g0)
    c: Coincident(g2,g1)
    c: Angle(g1,g2) = 0.279253
FEATURE [PartDesign::Pad] Pad521
  BaseFeature = -> Pad520
  Direction = (1,0,0)
  Length = 15
  Length2 = 10
  Profile = -> Sketch759
  ReferenceAxis = -> Sketch759 [N_Axis]
  Refine = true
  Reversed = true
  Suppressed = false
  Type = 0
FEATURE [Sketcher::SketchObject] Sketch760
  ArcFitTolerance = 1e-06
  AttachmentOffset = pos=(0,0,-3.55) rot=(0,0,1;0rad)
  AttachmentSupport = -> [Pad521]
  ExternalGeometry = -> [Pad521]
  FullyConstrained = true
  MakeInternals = false
  MapMode = 5
  Placement = pos=(32.05,0,0) rot=(0.57735,-0.57735,-0.57735;2.0944rad)
  sketch-geometry (4):
    g0: LineSegment StartX=-7.5 StartY=21.0898 StartZ=0 EndX=-4.5 EndY=21.95 EndZ=0
    g1: LineSegment StartX=-4.5 StartY=21.95 StartZ=0 EndX=-4.5 EndY=19.8398 EndZ=0
    g2: LineSegment StartX=-4.5 StartY=19.8398 StartZ=0 EndX=-7.5 EndY=19.8398 EndZ=0
    g3: LineSegment StartX=-7.5 StartY=21.0898 StartZ=0 EndX=-7.5 EndY=19.8398 EndZ=0
  constraints (10):
    c: Coincident(g0,g-3)
    c: Coincident(g0,g-3)
    c: Coincident(g1,g0)
    c: Vertical(g1)
    c: Coincident(g2,g1)
    c: Horizontal(g2)
    c: Coincident(g3,g0)
    c: Coincident(g3,g2)
    c: Vertical(g3)
    c: DistanceY(g3,g3) = 1.25
FEATURE [PartDesign::Pad] Pad522
  BaseFeature = -> Pad521
  Direction = (-1,0,0)
  Length = 7.9
  Length2 = 10
  Profile = -> Sketch760
  ReferenceAxis = -> Sketch760 [N_Axis]
  Refine = true
  Reversed = true
  Suppressed = false
  Type = 0
FEATURE [PartDesign::Chamfer] Chamfer023
  Angle = 51.7
  Base = -> Pad522 [Edge10,Edge5]
  BaseFeature = -> Pad522
  ChamferType = 2
  FlipDirection = false
  Refine = true
  Size = 2.8
  Size2 = 1
  SupportTransform = false
  Suppressed = false
  UseAllEdges = false
FEATURE [Sketcher::SketchObject] Sketch761
  ArcFitTolerance = 1e-06
  AttachmentSupport = -> [Chamfer023]
  ExternalGeometry = -> [Chamfer023]
  FullyConstrained = true
  MakeInternals = false
  MapMode = 5
  Placement = pos=(0,4.5,-1.2e-15) rot=(1,0,0;1.5708rad)
  sketch-geometry (4):
    g0: LineSegment StartX=32.05 StartY=21.95 StartZ=0 EndX=32.05 EndY=19.8398 EndZ=0
    g1: LineSegment StartX=32.05 StartY=19.8398 StartZ=0 EndX=39.95 EndY=19.8398 EndZ=0
    g2: LineSegment StartX=39.95 StartY=19.8398 StartZ=0 EndX=39.95 EndY=21.95 EndZ=0
    g3: LineSegment StartX=39.95 StartY=21.95 StartZ=0 EndX=32.05 EndY=21.95 EndZ=0
  constraints (10):
    c: Coincident(g0,g1)
    c: Coincident(g1,g2)
    c: Coincident(g2,g3)
    c: Coincident(g3,g0)
    c: Vertical(g0)
    c: Vertical(g2)
    c: Horizontal(g1)
    c: Horizontal(g3)
    c: Coincident(g0,g-5)
    c: Coincident(g1,g-4)
FEATURE [PartDesign::Pocket] Pocket346
  BaseFeature = -> Chamfer023
  Direction = (0,1,-2e-16)
  Length = 0.5
  Length2 = 5
  Profile = -> Sketch761
  ReferenceAxis = -> Sketch761 [N_Axis]
  Refine = true
  Suppressed = false
  Type = 0
FEATURE [PartDesign::SubShapeBinder] Binder003
  BindCopyOnChange = 0
  BindMode = 0
  ClaimChildren = false
  Context = -> Part001 [Body039.Binder003.]
  Fuse = false
  MakeFace = true
  OffsetFill = false
  OffsetIntersection = false
  OffsetJoinType = 0
  OffsetOpenResult = false
  PartialLoad = false
  Refine = true
  Relative = true
  Support = -> [Body037[Chamfer022.Face9]]
  _Version = 2
FEATURE [PartDesign::Pad] Pad523
  BaseFeature = -> Pocket346
  Direction = (-0.34202,0.264208,0.901785)
  Length = 1.15
  Length2 = 10
  Profile = -> Binder003
  Refine = true
  Suppressed = false
  Type = 0
FEATURE [PartDesign::SubShapeBinder] Binder004
  BindCopyOnChange = 0
  BindMode = 0
  ClaimChildren = false
  Context = -> Part001 [Body039.Binder004.]
  Fuse = false
  MakeFace = true
  OffsetFill = false
  OffsetIntersection = false
  OffsetJoinType = 0
  OffsetOpenResult = false
  PartialLoad = false
  Refine = true
  Relative = true
  Support = -> [Body037[Chamfer022.Face3]]
  _Version = 2
FEATURE [PartDesign::Pad] Pad524
  BaseFeature = -> Pad523
  Direction = (0.34202,0.264208,0.901785)
  Length = 1.15
  Length2 = 10
  Profile = -> Binder004
  Refine = true
  Suppressed = false
  Type = 0
FEATURE [Sketcher::SketchObject] Sketch762
  ArcFitTolerance = 1e-06
  AttachmentSupport = -> [Pad524]
  FullyConstrained = false
  MakeInternals = false
  MapMode = 5
  Placement = pos=(8.66157,-10.9674,2.5e-15) rot=(-0.238465,0.686708,0.686708;3.60978rad)
  sketch-geometry (4):
    g0: LineSegment StartX=-31.1329 StartY=23.9039 StartZ=0 EndX=-31.1329 EndY=19.0653 EndZ=0
    g1: LineSegment StartX=-31.1329 StartY=19.0653 StartZ=0 EndX=-24.8565 EndY=19.0653 EndZ=0
    g2: LineSegment StartX=-24.8565 StartY=19.0653 StartZ=0 EndX=-24.8565 EndY=23.9039 EndZ=0
    g3: LineSegment StartX=-24.8565 StartY=23.9039 StartZ=0 EndX=-31.1329 EndY=23.9039 EndZ=0
  constraints (8):
    c: Coincident(g0,g1)
    c: Coincident(g1,g2)
    c: Coincident(g2,g3)
    c: Coincident(g3,g0)
    c: Vertical(g0)
    c: Vertical(g2)
    c: Horizontal(g1)
    c: Horizontal(g3)
FEATURE [PartDesign::Pocket] Pocket347
  BaseFeature = -> Pad524
  Direction = (0.619779,-0.784776,-1e-16)
  Length = 5
  Length2 = 5
  Profile = -> Sketch762
  ReferenceAxis = -> Sketch762 [N_Axis]
  Refine = true
  Reversed = true
  Suppressed = false
  Type = 0
FEATURE [Sketcher::SketchObject] Sketch763
  ArcFitTolerance = 1e-06
  AttachmentSupport = -> [Pocket347]
  FullyConstrained = false
  MakeInternals = false
  MapMode = 5
  Placement = pos=(18.9955,24.0525,-5.5e-15) rot=(0.238465,0.686708,0.686708;2.67341rad)
  sketch-geometry (4):
    g0: LineSegment StartX=-32.7692 StartY=24.2107 StartZ=0 EndX=-32.7692 EndY=19.0694 EndZ=0
    g1: LineSegment StartX=-32.7692 StartY=19.0694 StartZ=0 EndX=-25.3296 EndY=19.0694 EndZ=0
    g2: LineSegment StartX=-25.3296 StartY=19.0694 StartZ=0 EndX=-25.3296 EndY=24.2107 EndZ=0
    g3: LineSegment StartX=-25.3296 StartY=24.2107 StartZ=0 EndX=-32.7692 EndY=24.2107 EndZ=0
  constraints (8):
    c: Coincident(g0,g1)
    c: Coincident(g1,g2)
    c: Coincident(g2,g3)
    c: Coincident(g3,g0)
    c: Vertical(g0)
    c: Vertical(g2)
    c: Horizontal(g1)
    c: Horizontal(g3)
FEATURE [PartDesign::Pocket] Pocket348
  BaseFeature = -> Pocket347
  Direction = (-0.619779,-0.784776,-1e-16)
  Length = 5
  Length2 = 5
  Profile = -> Sketch763
  ReferenceAxis = -> Sketch763 [N_Axis]
  Refine = true
  Reversed = true
  Suppressed = false
  Type = 0
FEATURE [Sketcher::SketchObject] Sketch764
  ArcFitTolerance = 1e-06
  AttachmentSupport = -> [Pocket348]
  FullyConstrained = false
  MakeInternals = false
  MapMode = 5
  Placement = pos=(0,7.5,-1.9e-15) rot=(0,0.707107,0.707107;3.14159rad)
  sketch-geometry (4):
    g0: LineSegment StartX=-40.767 StartY=23.941 StartZ=0 EndX=-40.767 EndY=18.9885 EndZ=0
    g1: LineSegment StartX=-40.767 StartY=18.9885 StartZ=0 EndX=-31.3192 EndY=18.9885 EndZ=0
    g2: LineSegment StartX=-31.3192 StartY=18.9885 StartZ=0 EndX=-31.3192 EndY=23.941 EndZ=0
    g3: LineSegment StartX=-31.3192 StartY=23.941 StartZ=0 EndX=-40.767 EndY=23.941 EndZ=0
  constraints (8):
    c: Coincident(g0,g1)
    c: Coincident(g1,g2)
    c: Coincident(g2,g3)
    c: Coincident(g3,g0)
    c: Vertical(g0)
    c: Vertical(g2)
    c: Horizontal(g1)
    c: Horizontal(g3)
FEATURE [PartDesign::Pocket] Pocket349
  BaseFeature = -> Pocket348
  Direction = (0,-1,2e-16)
  Length = 5
  Length2 = 5
  Profile = -> Sketch764
  ReferenceAxis = -> Sketch764 [N_Axis]
  Refine = true
  Reversed = true
  Suppressed = false
  Type = 0
FEATURE [Sketcher::SketchObject] Sketch765
  ArcFitTolerance = 1e-06
  AttachmentSupport = -> [Pocket349]
  ExternalGeometry = -> [Pocket349]
  FullyConstrained = false
  MakeInternals = false
  MapMode = 5
  Placement = pos=(-2.13118,1.64632,5.61917) rot=(0.984502,0.024907,0.173594;2.86094rad)
  sketch-geometry (4):
    g0: LineSegment StartX=44.8351 StartY=0.998103 StartZ=0 EndX=44.8351 EndY=-2.80002 EndZ=0
    g1: LineSegment StartX=44.8351 StartY=0.998103 StartZ=0 EndX=48.0276 EndY=1.31802 EndZ=0
    g2: LineSegment StartX=48.0276 StartY=1.31802 StartZ=0 EndX=48.0276 EndY=0.53823 EndZ=0
    g3: LineSegment StartX=44.8351 StartY=-2.80002 StartZ=0 EndX=48.0276 EndY=0.53823 EndZ=0
  constraints (8):
    c: Coincident(g0,g-4)
    c: Vertical(g0)
    c: Coincident(g1,g0)
    c: Coincident(g1,g-3)
    c: Coincident(g2,g1)
    c: Vertical(g2)
    c: Coincident(g3,g0)
    c: Coincident(g3,g2)
FEATURE [PartDesign::Pocket] Pocket350
  BaseFeature = -> Pocket349
  Direction = (-0.34202,0.264208,0.901785)
  Length = 0.055
  Length2 = 5
  Profile = -> Sketch765
  ReferenceAxis = -> Sketch765 [N_Axis]
  Refine = true
  Suppressed = false
  Type = 0
FEATURE [Sketcher::SketchObject] Sketch766
  ArcFitTolerance = 1e-06
  AttachmentSupport = -> [Pocket350]
  ExternalGeometry = -> [Pocket350]
  FullyConstrained = false
  MakeInternals = false
  MapMode = 5
  Placement = pos=(10.5536,8.15257,27.826) rot=(0.984502,-0.024907,-0.173594;2.86094rad)
  sketch-geometry (4):
    g0: LineSegment StartX=22.8228 StartY=3.86161 StartZ=0 EndX=19.6303 EndY=1.31254 EndZ=0
    g1: LineSegment StartX=22.8228 StartY=3.86161 StartZ=0 EndX=22.8228 EndY=-3.10803 EndZ=0
    g2: LineSegment StartX=22.8228 StartY=-3.10803 StartZ=0 EndX=19.6303 EndY=-1.21614 EndZ=0
    g3: LineSegment StartX=19.6303 StartY=1.31254 StartZ=0 EndX=19.6303 EndY=-1.21614 EndZ=0
  constraints (8):
    c: Coincident(g1,g0)
    c: Vertical(g1)
    c: Coincident(g2,g1)
    c: Coincident(g3,g2)
    c: Vertical(g3)
    c: Coincident(g3,g0)
    c: PointOnObject(g-3,g1)
    c: PointOnObject(g-5,g3)
FEATURE [PartDesign::Pocket] Pocket351
  BaseFeature = -> Pocket350
  Direction = (0.34202,0.264208,0.901785)
  Length = 0.055
  Length2 = 5
  Profile = -> Sketch766
  ReferenceAxis = -> Sketch766 [N_Axis]
  Refine = true
  Suppressed = false
  Type = 0
FEATURE [Sketcher::SketchObject] Sketch767
  ArcFitTolerance = 1e-06
  AttachmentSupport = -> [Pocket351]
  ExternalGeometry = -> [Pocket351]
  FullyConstrained = false
  MakeInternals = false
  MapMode = 5
  Placement = pos=(10.5724,8.1671,27.8756) rot=(0.984502,-0.024907,-0.173594;2.86094rad)
  sketch-geometry (3):
    g0: LineSegment StartX=19.6303 StartY=1.31802 StartZ=0 EndX=19.6303 EndY=1.30901 EndZ=0
    g1: LineSegment StartX=19.6303 StartY=1.30901 StartZ=0 EndX=19.6409 EndY=1.31695 EndZ=0
    g2: LineSegment StartX=19.6409 StartY=1.31695 StartZ=0 EndX=19.6303 EndY=1.31802 EndZ=0
  constraints (6):
    c: Coincident(g0,g-6)
    c: PointOnObject(g0,g-4)
    c: Coincident(g1,g0)
    c: PointOnObject(g1,g-3)
    c: Coincident(g2,g1)
    c: Coincident(g2,g0)
FEATURE [PartDesign::Pocket] Pocket352
  BaseFeature = -> Pocket351
  Direction = (0.34202,0.264208,0.901785)
  Length = 5
  Length2 = 5
  Profile = -> Sketch767
  ReferenceAxis = -> Sketch767 [N_Axis]
  Refine = true
  Reversed = true
  Suppressed = false
  Type = 0
FEATURE [Sketcher::SketchObject] Sketch768
  ArcFitTolerance = 1e-06
  AttachmentSupport = -> [Pocket352]
  ExternalGeometry = -> [Pocket352]
  FullyConstrained = true
  MakeInternals = false
  MapMode = 5
  Placement = pos=(0,7.5,0) rot=(0,0.707107,0.707107;3.14159rad)
  sketch-geometry (18):
    g0: LineSegment StartX=-36.8546 StartY=22.85 StartZ=0 EndX=-36.8546 EndY=20.8398 EndZ=0
    g1: LineSegment StartX=-35.1454 StartY=22.85 StartZ=0 EndX=-35.1454 EndY=20.8398 EndZ=0
    g2: ArcOfCircle CenterX=-37.8546 CenterY=20.8398 CenterZ=0 NormalX=0 NormalY=0 NormalZ=1 AngleXU=0 Radius=1 StartAngle=4.71239 EndAngle=6.28319
    g3: ArcOfCircle CenterX=-34.1454 CenterY=20.8398 CenterZ=0 NormalX=0 NormalY=0 NormalZ=1 AngleXU=0 Radius=1 StartAngle=3.14159 EndAngle=4.71239
    g4: ArcOfCircle CenterX=-34.6454 CenterY=22.85 CenterZ=0 NormalX=0 NormalY=0 NormalZ=1 AngleXU=0 Radius=0.5 StartAngle=1.5708 EndAngle=3.14159
    g5: ArcOfCircle CenterX=-37.3546 CenterY=22.85 CenterZ=0 NormalX=0 NormalY=0 NormalZ=1 AngleXU=0 Radius=0.5 StartAngle=1.4e-15 EndAngle=1.5708
    g6: LineSegment StartX=-34.1454 StartY=19.8398 StartZ=0 EndX=-37.8546 EndY=19.8398 EndZ=0
    g7: LineSegment StartX=-34.6454 StartY=23.35 StartZ=0 EndX=-37.3546 EndY=23.35 EndZ=0
    g8: LineSegment [constr] StartX=-37.3546 StartY=23.35 StartZ=0 EndX=-37.3546 EndY=22.85 EndZ=0
    g9: LineSegment [constr] StartX=-36.8546 StartY=22.85 StartZ=0 EndX=-37.3546 EndY=22.85 EndZ=0
    g10: LineSegment [constr] StartX=-34.6454 StartY=23.35 StartZ=0 EndX=-34.6454 EndY=22.85 EndZ=0
    g11: LineSegment [constr] StartX=-35.1454 StartY=22.85 StartZ=0 EndX=-34.6454 EndY=22.85 EndZ=0
    g12: LineSegment [constr] StartX=-34.1454 StartY=19.8398 StartZ=0 EndX=-34.1454 EndY=20.8398 EndZ=0
    g13: LineSegment [constr] StartX=-34.1454 StartY=20.8398 StartZ=0 EndX=-35.1454 EndY=20.8398 EndZ=0
    g14: LineSegment [constr] StartX=-36.8546 StartY=20.8398 StartZ=0 EndX=-37.8546 EndY=20.8398 EndZ=0
    g15: LineSegment [constr] StartX=-37.8546 StartY=20.8398 StartZ=0 EndX=-37.8546 EndY=19.8398 EndZ=0
    g16: LineSegment [constr] StartX=-35.1454 StartY=22.85 StartZ=0 EndX=-36.8546 EndY=22.85 EndZ=0
    g17: LineSegment [constr] StartX=-35.1454 StartY=20.8398 StartZ=0 EndX=-36.8546 EndY=20.8398 EndZ=0
  constraints (48):
    c: DistanceX(g-3,g-3) = 7.90917
    c: Vertical(g0)
    c: Vertical(g1)
    c: Coincident(g2,g0)
    c: PointOnObject(g2,g-4)
    c: Coincident(g3,g1)
    c: PointOnObject(g3,g-4)
    c: Coincident(g4,g1)
    c: PointOnObject(g4,g-3)
    c: Coincident(g5,g0)
    c: PointOnObject(g5,g-3)
    c: Coincident(g6,g3)
    c: Coincident(g6,g2)
    c: Coincident(g7,g4)
    c: Tangent(g7,g5) = -1.5708
    c: Coincident(g8,g5)
    c: Coincident(g8,g5)
    c: Coincident(g9,g0)
    c: Coincident(g9,g5)
    c: Coincident(g10,g4)
    c: Coincident(g10,g4)
    c: Coincident(g11,g1)
    c: Coincident(g11,g4)
    c: Coincident(g12,g3)
    c: Coincident(g12,g3)
    c: Coincident(g13,g3)
    c: Coincident(g13,g1)
    c: Coincident(g14,g0)
    c: Coincident(g14,g2)
    c: Horizontal(g14)
    c: Coincident(g15,g2)
    c: Coincident(g15,g2)
    c: Coincident(g16,g1)
    c: Coincident(g16,g0)
    c: Horizontal(g16)
    c: Coincident(g17,g1)
    c: Coincident(g17,g0)
    c: Vertical(g15)
    c: Vertical(g12)
    c: Vertical(g10)
    c: Horizontal(g11)
    c: Horizontal(g13)
    c: Horizontal(g9)
    c: Radius(g2) = 1
    c: Radius(g5) = 0.5
    c: Horizontal(g17)
    c: DistanceX(g-3,g5) = 2.6
    c: DistanceX(g4,g-3) = 2.6
FEATURE [PartDesign::Pocket] Pocket353
  BaseFeature = -> Pocket352
  Direction = (0,-1,2e-16)
  Length = 0.5
  Length2 = 5
  Profile = -> Sketch768
  ReferenceAxis = -> Sketch768 [N_Axis]
  Refine = true
  Suppressed = false
  Type = 0
FEATURE [PartDesign::Pad] Pad525
  BaseFeature = -> Pocket353
  Direction = (-1,0,0)
  Length = 8
  Length2 = 10
  Profile = -> Pocket353 [Face26]
  Refine = true
  Suppressed = false
  Type = 0
FEATURE [Sketcher::SketchObject] Sketch769
  ArcFitTolerance = 1e-06
  AttachmentSupport = -> [Pad525]
  ExternalGeometry = -> [Pad525]
  FullyConstrained = true
  MakeInternals = false
  MapMode = 5
  Placement = pos=(0,5,0) rot=(1,0,0;1.5708rad)
  sketch-geometry (6):
    g0: LineSegment StartX=39.95 StartY=21.8066 StartZ=0 EndX=42.9795 EndY=21.8025 EndZ=0
    g1: LineSegment StartX=42.9795 StartY=21.8025 StartZ=0 EndX=39.95 EndY=20.6535 EndZ=0
    g2: LineSegment StartX=39.95 StartY=21.8066 StartZ=0 EndX=39.95 EndY=20.6535 EndZ=0
    g3: LineSegment StartX=32.05 StartY=21.8066 StartZ=0 EndX=32.05 EndY=20.6535 EndZ=0
    g4: LineSegment StartX=32.05 StartY=21.8066 StartZ=0 EndX=29.0205 EndY=21.8025 EndZ=0
    g5: LineSegment StartX=29.0205 StartY=21.8025 StartZ=0 EndX=32.05 EndY=20.6535 EndZ=0
  constraints (14):
    c: Coincident(g0,g-4)
    c: Coincident(g0,g-6)
    c: Coincident(g1,g0)
    c: PointOnObject(g1,g-4)
    c: PointOnObject(g-5,g1)
    c: Coincident(g2,g0)
    c: Coincident(g2,g1)
    c: PointOnObject(g3,g-8)
    c: Coincident(g3,g-8)
    c: Coincident(g4,g3)
    c: Coincident(g4,g-9)
    c: Coincident(g5,g4)
    c: Coincident(g5,g3)
    c: PointOnObject(g-9,g5)
FEATURE [PartDesign::Pad] Pad526
  BaseFeature = -> Pad525
  Direction = (0,-1,2e-16)
  Length = 1
  Length2 = 10
  Profile = -> Sketch769
  ReferenceAxis = -> Sketch769 [N_Axis]
  Refine = true
  Reversed = true
  Suppressed = false
  Type = 0
FEATURE [Sketcher::SketchObject] Sketch770
  ArcFitTolerance = 1e-06
  AttachmentSupport = -> [Pad526]
  FullyConstrained = false
  MakeInternals = false
  MapMode = 5
  Placement = pos=(18.9955,24.0525,1.93e-14) rot=(0.238465,0.686708,0.686708;2.67341rad)
  sketch-geometry (4):
    g0: LineSegment StartX=-25.9821 StartY=23.9852 StartZ=0 EndX=-32.2421 EndY=23.9852 EndZ=0
    g1: LineSegment StartX=-32.2421 StartY=23.9852 StartZ=0 EndX=-32.2421 EndY=18.8838 EndZ=0
    g2: LineSegment StartX=-32.2421 StartY=18.8838 StartZ=0 EndX=-25.9821 EndY=18.8838 EndZ=0
    g3: LineSegment StartX=-25.9821 StartY=18.8838 StartZ=0 EndX=-25.9821 EndY=23.9852 EndZ=0
  constraints (8):
    c: Coincident(g0,g1)
    c: Coincident(g1,g2)
    c: Coincident(g2,g3)
    c: Coincident(g3,g0)
    c: Horizontal(g0)
    c: Horizontal(g2)
    c: Vertical(g1)
    c: Vertical(g3)
FEATURE [PartDesign::Pocket] Pocket354
  BaseFeature = -> Pad526
  Direction = (-0.619779,-0.784776,0)
  Length = 5
  Length2 = 5
  Profile = -> Sketch770
  ReferenceAxis = -> Sketch770 [N_Axis]
  Refine = true
  Reversed = true
  Suppressed = false
  Type = 0
FEATURE [Sketcher::SketchObject] Sketch771
  ArcFitTolerance = 1e-06
  AttachmentSupport = -> [Pocket354]
  FullyConstrained = false
  MakeInternals = false
  MapMode = 5
  Placement = pos=(8.66157,-10.9674,1.76e-14) rot=(-0.238465,0.686708,0.686708;3.60978rad)
  sketch-geometry (4):
    g0: LineSegment StartX=-30.3416 StartY=23.9443 StartZ=0 EndX=-30.3416 EndY=19.3307 EndZ=0
    g1: LineSegment StartX=-30.3416 StartY=19.3307 StartZ=0 EndX=-23.9997 EndY=19.3307 EndZ=0
    g2: LineSegment StartX=-23.9997 StartY=19.3307 StartZ=0 EndX=-23.9997 EndY=23.9443 EndZ=0
    g3: LineSegment StartX=-23.9997 StartY=23.9443 StartZ=0 EndX=-30.3416 EndY=23.9443 EndZ=0
  constraints (8):
    c: Coincident(g0,g1)
    c: Coincident(g1,g2)
    c: Coincident(g2,g3)
    c: Coincident(g3,g0)
    c: Vertical(g0)
    c: Vertical(g2)
    c: Horizontal(g1)
    c: Horizontal(g3)
FEATURE [PartDesign::Pocket] Pocket355
  BaseFeature = -> Pocket354
  Direction = (0.619779,-0.784776,1.5e-15)
  Length = 5
  Length2 = 5
  Profile = -> Sketch771
  ReferenceAxis = -> Sketch771 [N_Axis]
  Refine = true
  Reversed = true
  Suppressed = false
  Type = 0
FEATURE [PartDesign::Body] Body039  label="Eyes"
  AllowCompound = false
  Group = -> [Binder002,Sketch758,Pad520,Sketch759,Pad521,Sketch760,Pad522,Chamfer023,Sketch761,Pocket346,Binder003,Pad523,Binder004,Pad524,Sketch762,Pocket347,Sketch763,Pocket348,Sketch764,Pocket349,Sketch765,Pocket350,Sketch766,Pocket351,Sketch767,Pocket352,Sketch768,Pocket353,Pad525,Sketch769,Pad526,Sketch770,Pocket354,Sketch771,Pocket355]
  Origin = -> Origin042
  Tip = -> Pocket355
FEATURE [PartDesign::SubShapeBinder] Binder005
  BindCopyOnChange = 0
  BindMode = 2
  ClaimChildren = false
  Context = -> Part001 [Body040.Binder005.]
  Fuse = false
  MakeFace = true
  OffsetFill = false
  OffsetIntersection = false
  OffsetJoinType = 0
  OffsetOpenResult = false
  PartialLoad = false
  Refine = true
  Relative = true
  _Version = 2
FEATURE [Sketcher::SketchObject] Sketch772
  ArcFitTolerance = 1e-06
  AttachmentSupport = -> [Binder005]
  ExternalGeometry = -> [Binder005]
  FullyConstrained = true
  MakeInternals = false
  MapMode = 5
  Placement = pos=(0,5,-1.1e-15) rot=(0,0.707107,0.707107;3.14159rad)
  sketch-geometry (6):
    g0: LineSegment StartX=-40 StartY=19.8078 StartZ=0 EndX=-40 EndY=16.9078 EndZ=0
    g1: LineSegment StartX=-40 StartY=16.9078 StartZ=0 EndX=-38.5 EndY=13.2 EndZ=0
    g2: LineSegment StartX=-38.5 StartY=13.2 StartZ=0 EndX=-33.5 EndY=13.2 EndZ=0
    g3: LineSegment StartX=-33.5 StartY=13.2 StartZ=0 EndX=-32 EndY=16.9078 EndZ=0
    g4: LineSegment StartX=-32 StartY=16.9078 StartZ=0 EndX=-32 EndY=19.8078 EndZ=0
    g5: LineSegment StartX=-40 StartY=19.8078 StartZ=0 EndX=-32 EndY=19.8078 EndZ=0
  constraints (17):
    c: PointOnObject(g0,g-3)
    c: Symmetric(g-3,g-3,g0)
    c: Coincident(g1,g0)
    c: PointOnObject(g1,g-5)
    c: Coincident(g2,g1)
    c: PointOnObject(g2,g-5)
    c: Coincident(g3,g2)
    c: Symmetric(g-4,g-4,g3)
    c: Coincident(g4,g3)
    c: PointOnObject(g4,g-4)
    c: Coincident(g5,g0)
    c: Coincident(g5,g4)
    c: Horizontal(g5)
    c: DistanceX(g2,g2) = 5
    c: DistanceX(g-5,g-5) = 8
    c: DistanceX(g-5,g1) = 1.5
    c: DistanceY(g0,g0) = 2.9
FEATURE [PartDesign::Pad] Pad527
  Direction = (0,1,-2e-16)
  Length = 3
  Length2 = 10
  Profile = -> Sketch772
  ReferenceAxis = -> Sketch772 [N_Axis]
  Refine = true
  Suppressed = false
  Type = 0
FEATURE [Sketcher::SketchObject] Sketch773
  ArcFitTolerance = 1e-06
  AttachmentOffset = pos=(0,0,-3.2) rot=(0,0,1;0rad)
  AttachmentSupport = -> [Pad527]
  ExternalGeometry = -> [Pad527]
  FullyConstrained = true
  MakeInternals = false
  MapMode = 5
  Placement = pos=(35.2,-4e-16,-1.295e-13) rot=(0.57735,-0.57735,-0.57735;2.0944rad)
  sketch-geometry (6):
    g0: LineSegment StartX=-7.05 StartY=19.8078 StartZ=0 EndX=-7.05 EndY=23.3478 EndZ=0
    g1: LineSegment StartX=-7.05 StartY=23.3478 StartZ=0 EndX=-7.65 EndY=23.3478 EndZ=0
    g2: LineSegment StartX=-7.65 StartY=23.3478 StartZ=0 EndX=-10 EndY=17.9578 EndZ=0
    g3: LineSegment StartX=-10 StartY=17.9578 StartZ=0 EndX=-8 EndY=17.7578 EndZ=0
    g4: LineSegment StartX=-8 StartY=17.7578 StartZ=0 EndX=-8 EndY=19.8078 EndZ=0
    g5: LineSegment StartX=-8 StartY=19.8078 StartZ=0 EndX=-7.05 EndY=19.8078 EndZ=0
  constraints (17):
    c: PointOnObject(g0,g-3)
    c: Vertical(g0)
    c: Coincident(g1,g0)
    c: Horizontal(g1)
    c: Coincident(g2,g1)
    c: Coincident(g3,g2)
    c: PointOnObject(g3,g-4)
    c: Coincident(g4,g3)
    c: Coincident(g4,g-4)
    c: Coincident(g5,g4)
    c: Coincident(g5,g0)
    c: DistanceX(g2,g4) = 2
    c: DistanceX(g5,g5) = 0.95
    c: DistanceY(g0,g0) = 3.54
    c: DistanceX(g1,g1) = 0.6
    c: DistanceY(g4,g4) = 2.05
    c: DistanceY(g3,g2) = 0.2
FEATURE [PartDesign::Pad] Pad528
  BaseFeature = -> Pad527
  Direction = (-1,1e-16,3.7e-15)
  Length = 1.6
  Length2 = 10
  Profile = -> Sketch773
  ReferenceAxis = -> Sketch773 [N_Axis]
  Refine = true
  Reversed = true
  Suppressed = false
  Type = 0
FEATURE [Sketcher::SketchObject] Sketch774
  ArcFitTolerance = 1e-06
  AttachmentSupport = -> [Pad528]
  ExternalGeometry = -> [Pad528]
  FullyConstrained = true
  MakeInternals = false
  MapMode = 5
  Placement = pos=(0,8,-2.2e-15) rot=(0,0.707107,0.707107;3.14159rad)
  sketch-geometry (12):
    g0: LineSegment StartX=-35.2 StartY=19.8078 StartZ=0 EndX=-35.2 EndY=20.7078 EndZ=0
    g1: LineSegment StartX=-35.2 StartY=19.8078 StartZ=0 EndX=-34.3 EndY=19.8078 EndZ=0
    g2: ArcOfCircle CenterX=-34.2046 CenterY=20.8033 CenterZ=0 NormalX=0 NormalY=0 NormalZ=1 AngleXU=0 Radius=1 StartAngle=3.23717 EndAngle=4.61681
    g3: LineSegment StartX=-36.8 StartY=19.8078 StartZ=0 EndX=-36.8 EndY=20.7078 EndZ=0
    g4: LineSegment StartX=-36.8 StartY=19.8078 StartZ=0 EndX=-37.7 EndY=19.8078 EndZ=0
    g5: ArcOfCircle CenterX=-37.7954 CenterY=20.8033 CenterZ=0 NormalX=0 NormalY=0 NormalZ=1 AngleXU=0 Radius=1 StartAngle=4.80797 EndAngle=6.1876
    g6: LineSegment StartX=-36.8 StartY=23.3478 StartZ=0 EndX=-37.1 EndY=23.3478 EndZ=0
    g7: LineSegment StartX=-36.8 StartY=23.3478 StartZ=0 EndX=-36.8 EndY=22.9678 EndZ=0
    g8: ArcOfCircle CenterX=-37.3809 CenterY=22.8177 CenterZ=0 NormalX=0 NormalY=0 NormalZ=1 AngleXU=0 Radius=0.6 StartAngle=0.252997 EndAngle=1.08358
    g9: LineSegment StartX=-35.2 StartY=23.3478 StartZ=0 EndX=-34.9 EndY=23.3478 EndZ=0
    g10: LineSegment StartX=-35.2 StartY=23.3478 StartZ=0 EndX=-35.2 EndY=22.9678 EndZ=0
    g11: ArcOfCircle CenterX=-34.6191 CenterY=22.8177 CenterZ=0 NormalX=0 NormalY=0 NormalZ=1 AngleXU=0 Radius=0.6 StartAngle=2.05801 EndAngle=2.8886
  constraints (36):
    c: Coincident(g0,g-3)
    c: PointOnObject(g0,g-4)
    c: Coincident(g1,g0)
    c: PointOnObject(g1,g-3)
    c: Coincident(g2,g1)
    c: Coincident(g0,g2)
    c: Radius(g2) = 1
    c: DistanceX(g1,g1) = 0.9
    c: DistanceY(g0,g0) = 0.9
    c: Coincident(g3,g-6)
    c: PointOnObject(g3,g-5)
    c: Coincident(g4,g3)
    c: PointOnObject(g4,g-6)
    c: Coincident(g5,g3)
    c: Coincident(g5,g4)
    c: DistanceY(g3,g3) = 0.9
    c: DistanceX(g4,g4) = 0.9
    c: Radius(g5) = 1
    c: Coincident(g6,g-5)
    c: Horizontal(g6)
    c: Coincident(g7,g6)
    c: PointOnObject(g7,g-5)
    c: Coincident(g8,g6)
    c: Coincident(g8,g7)
    c: Radius(g8) = 0.6
    c: DistanceX(g6,g6) = 0.3
    c: DistanceY(g7,g7) = 0.38
    c: Coincident(g9,g-4)
    c: Horizontal(g9)
    c: Coincident(g10,g9)
    c: PointOnObject(g10,g-4)
    c: Coincident(g11,g10)
    c: Coincident(g11,g9)
    c: DistanceY(g10,g10) = 0.38
    c: Radius(g11) = 0.6
    c: DistanceX(g9,g9) = 0.3
FEATURE [PartDesign::Pad] Pad529
  BaseFeature = -> Pad528
  Direction = (0,1,-2e-16)
  Length = 0.95
  Length2 = 10
  Profile = -> Sketch774
  ReferenceAxis = -> Sketch774 [N_Axis]
  Refine = true
  Reversed = true
  Suppressed = false
  Type = 0
FEATURE [PartDesign::Pocket] Pocket356
  BaseFeature = -> Pad529
  Direction = (-1,0,7.00259e-11)
  Length = 5
  Length2 = 5
  Profile = -> Pad529 [Face18]
  Refine = true
  Suppressed = false
  Type = 0
FEATURE [PartDesign::Pocket] Pocket357
  BaseFeature = -> Pocket356
  Direction = (1,0,6.8623e-12)
  Length = 5
  Length2 = 5
  Profile = -> Pocket356 [Face18]
  Refine = true
  Suppressed = false
  Type = 0
FEATURE [PartDesign::Chamfer] Chamfer024
  Angle = 70
  Base = -> Pocket357 [Edge20,Edge21]
  BaseFeature = -> Pocket357
  ChamferType = 2
  FlipDirection = false
  Refine = true
  Size = 1.05
  Size2 = 1
  SupportTransform = false
  Suppressed = false
  UseAllEdges = false
FEATURE [PartDesign::Chamfer] Chamfer025
  Angle = 70
  Base = -> Chamfer024 [Edge22,Edge23]
  BaseFeature = -> Chamfer024
  ChamferType = 2
  FlipDirection = false
  Refine = true
  Size = 1.05
  Size2 = 1
  SupportTransform = false
  Suppressed = false
  UseAllEdges = false
FEATURE [Sketcher::SketchObject] Sketch775
  ArcFitTolerance = 1e-06
  AttachmentOffset = pos=(0,0,2.2) rot=(0,0,1;0rad)
  AttachmentSupport = -> [Chamfer025]
  ExternalGeometry = -> [Chamfer025]
  FullyConstrained = false
  MakeInternals = false
  MapMode = 5
  Placement = pos=(33,-8.78e-14,-1.313e-13) rot=(0.57735,-0.57735,-0.57735;2.0944rad)
  sketch-geometry (3):
    g0: ArcOfCircle CenterX=-22.9873 CenterY=17.7298 CenterZ=0 NormalX=0 NormalY=0 NormalZ=1 AngleXU=0 Radius=15 StartAngle=5.97641 EndAngle=6.242
    g1: LineSegment StartX=-8 StartY=17.1122 StartZ=0 EndX=-8 EndY=13.2 EndZ=0
    g2: LineSegment StartX=-8 StartY=13.2 StartZ=0 EndX=-8.68759 EndY=13.2 EndZ=0
  constraints (7):
    c: Coincident(g0,g-3)
    c: Coincident(g1,g0)
    c: Coincident(g1,g-3)
    c: Coincident(g2,g1)
    c: Coincident(g2,g0)
    c: Horizontal(g2)
    c: Radius(g0) = 15
FEATURE [PartDesign::Pad] Pad530
  BaseFeature = -> Chamfer025
  Direction = (-1,2.7e-15,4e-15)
  Length = 6
  Length2 = 10
  Profile = -> Sketch775
  ReferenceAxis = -> Sketch775 [N_Axis]
  Refine = true
  Reversed = true
  Suppressed = false
  Type = 0
FEATURE [PartDesign::Pocket] Pocket358
  BaseFeature = -> Pad530
  Direction = (2.7e-15,1,-2.45e-14)
  Length = 5
  Length2 = 5
  Profile = -> Pad530 [Face22,Face24]
  Refine = true
  Suppressed = false
  Type = 0
FEATURE [Sketcher::SketchObject] Sketch776
  ArcFitTolerance = 1e-06
  AttachmentSupport = -> [Pocket358]
  ExternalGeometry = -> [Pocket358]
  FullyConstrained = true
  MakeInternals = false
  MapMode = 5
  Placement = pos=(0,8,0) rot=(0,0.707107,0.707107;3.14159rad)
  sketch-geometry (4):
    g0: LineSegment StartX=-37.3673 StartY=13.2 StartZ=0 EndX=-34.6327 EndY=13.2 EndZ=0
    g1: LineSegment StartX=-34.6327 StartY=13.2 StartZ=0 EndX=-34.6327 EndY=15.4 EndZ=0
    g2: LineSegment StartX=-34.6327 StartY=15.4 StartZ=0 EndX=-37.3673 EndY=15.4 EndZ=0
    g3: LineSegment StartX=-37.3673 StartY=15.4 StartZ=0 EndX=-37.3673 EndY=13.2 EndZ=0
  constraints (10):
    c: Coincident(g0,g1)
    c: Coincident(g1,g2)
    c: Coincident(g2,g3)
    c: Coincident(g3,g0)
    c: Horizontal(g2)
    c: Vertical(g1)
    c: Vertical(g3)
    c: Coincident(g0,g-3)
    c: Coincident(g0,g-3)
    c: DistanceY(g3,g3) = 2.2
FEATURE [PartDesign::Pad] Pad531
  BaseFeature = -> Pocket358
  Direction = (0,1,-2e-16)
  Length = 2
  Length2 = 10
  Profile = -> Sketch776
  ReferenceAxis = -> Sketch776 [N_Axis]
  Refine = true
  Suppressed = false
  Type = 0
FEATURE [Sketcher::SketchObject] Sketch777
  ArcFitTolerance = 1e-06
  AttachmentSupport = -> [Pad531]
  ExternalGeometry = -> [Pad531]
  FullyConstrained = true
  MakeInternals = false
  MapMode = 5
  Placement = pos=(34.6327,0,0) rot=(0.57735,-0.57735,-0.57735;2.0944rad)
  sketch-geometry (3):
    g0: LineSegment StartX=-10 StartY=13.9 StartZ=0 EndX=-8.5 EndY=15.4 EndZ=0
    g1: LineSegment StartX=-8.5 StartY=15.4 StartZ=0 EndX=-10 EndY=15.4 EndZ=0
    g2: LineSegment StartX=-10 StartY=15.4 StartZ=0 EndX=-10 EndY=13.9 EndZ=0
  constraints (8):
    c: PointOnObject(g0,g-3)
    c: PointOnObject(g0,g-4)
    c: Coincident(g1,g0)
    c: Coincident(g1,g-4)
    c: Coincident(g2,g1)
    c: Coincident(g2,g0)
    c: DistanceY(g2,g2) = 1.5
    c: DistanceX(g1,g1) = 1.5
FEATURE [PartDesign::Pocket] Pocket359
  BaseFeature = -> Pad531
  Direction = (1,0,0)
  Length = 5
  Length2 = 5
  Profile = -> Sketch777
  ReferenceAxis = -> Sketch777 [N_Axis]
  Refine = true
  Suppressed = false
  Type = 0
FEATURE [Sketcher::SketchObject] Sketch778
  ArcFitTolerance = 1e-06
  AttachmentSupport = -> [Pocket359]
  ExternalGeometry = -> [Pocket359]
  FullyConstrained = true
  MakeInternals = false
  MapMode = 5
  Placement = pos=(0,8,0) rot=(0,0.707107,0.707107;3.14159rad)
  sketch-geometry (16):
    g0: LineSegment StartX=-37.5673 StartY=17.05 StartZ=0 EndX=-37.5673 EndY=16.85 EndZ=0
    g1: LineSegment StartX=-37.5673 StartY=16.85 StartZ=0 EndX=-34.4327 EndY=16.85 EndZ=0
    g2: LineSegment StartX=-34.4327 StartY=16.85 StartZ=0 EndX=-34.4327 EndY=17.05 EndZ=0
    g3: LineSegment StartX=-35.6 StartY=17.45 StartZ=0 EndX=-36.4 EndY=17.45 EndZ=0
    g4: LineSegment StartX=-37.5673 StartY=16.65 StartZ=0 EndX=-37.5673 EndY=16.5 EndZ=0
    g5: LineSegment StartX=-37.0673 StartY=16 StartZ=0 EndX=-34.9327 EndY=16 EndZ=0
    g6: LineSegment StartX=-34.4327 StartY=16.5 StartZ=0 EndX=-34.4327 EndY=16.65 EndZ=0
    g7: LineSegment StartX=-34.4327 StartY=16.65 StartZ=0 EndX=-37.5673 EndY=16.65 EndZ=0
    g8: ArcOfCircle CenterX=-37.0673 CenterY=16.5 CenterZ=0 NormalX=0 NormalY=0 NormalZ=1 AngleXU=0 Radius=0.5 StartAngle=3.14159 EndAngle=4.71239
    g9: GeomPoint [constr] X=-37.5673 Y=16 Z=0
    g10: ArcOfCircle CenterX=-34.9327 CenterY=16.5 CenterZ=0 NormalX=0 NormalY=0 NormalZ=1 AngleXU=0 Radius=0.5 StartAngle=4.71239 EndAngle=6.28319
    g11: GeomPoint [constr] X=-34.4327 Y=16 Z=0
    g12: LineSegment [constr] StartX=-37.5673 StartY=16.65 StartZ=0 EndX=-37.5673 EndY=16.85 EndZ=0
    g13: LineSegment [constr] StartX=-34.4327 StartY=16.65 StartZ=0 EndX=-34.4327 EndY=16.85 EndZ=0
    g14: ArcOfCircle CenterX=-35.3753 CenterY=12.5561 CenterZ=0 NormalX=0 NormalY=0 NormalZ=1 AngleXU=0 Radius=5 StartAngle=1.77721 EndAngle=2.02463
    g15: ArcOfCircle CenterX=-36.6247 CenterY=12.5561 CenterZ=0 NormalX=0 NormalY=0 NormalZ=1 AngleXU=0 Radius=5 StartAngle=1.11696 EndAngle=1.36439
  constraints (45):
    c: Coincident(g0,g1)
    c: Coincident(g1,g2)
    c: Vertical(g0)
    c: Vertical(g2)
    c: Horizontal(g1)
    c: Horizontal(g3)
    c: Coincident(g6,g7)
    c: Coincident(g7,g4)
    c: Vertical(g4)
    c: Vertical(g6)
    c: Horizontal(g5)
    c: Horizontal(g7)
    c: DistanceX(g-3,g-3) = 2.73467
    c: DistanceX(g9,g-3) = 0.2
    c: DistanceX(g-3,g11) = 0.2
    c: PointOnObject(g9,g4)
    c: PointOnObject(g9,g5)
    c: Tangent(g4,g8) = -1.5708
    c: Tangent(g5,g8) = -1.5708
    c: PointOnObject(g11,g5)
    c: PointOnObject(g11,g6)
    c: Tangent(g5,g10) = -1.5708
    c: Tangent(g6,g10) = -1.5708
    c: Radius(g10) = 0.5
    c: Radius(g8) = 0.5
    c: DistanceY(g5,g4) = 0.65
    c: Coincident(g12,g4)
    c: Coincident(g12,g0)
    c: Coincident(g13,g6)
    c: Coincident(g13,g1)
    c: Vertical(g13)
    c: Vertical(g12)
    c: DistanceY(g12,g12) = 0.2
    c: Coincident(g14,g0)
    c: Coincident(g14,g3)
    c: Coincident(g15,g3)
    c: Coincident(g15,g2)
    c: DistanceY(g0,g0) = 0.2
    c: DistanceY(g2,g2) = 0.2
    c: DistanceX(g-4,g3) = 0.4
    c: DistanceX(g3,g-4) = 0.4
    c: DistanceY(g-3,g5) = 0.6
    c: Radius(g14) = 5
    c: Radius(g15) = 5
    c: DistanceY(g0,g3) = 0.6
FEATURE [PartDesign::Pad] Pad532
  BaseFeature = -> Pocket359
  Direction = (0,1,-2e-16)
  Length = 0.3
  Length2 = 10
  Profile = -> Sketch778
  ReferenceAxis = -> Sketch778 [N_Axis]
  Refine = true
  Suppressed = false
  Type = 0
FEATURE [PartDesign::Body] Body040  label="Lower_Face"
  AllowCompound = false
  Group = -> [Binder005,Sketch772,Pad527,Sketch773,Pad528,Sketch774,Pad529,Pocket356,Pocket357,Chamfer024,Chamfer025,Sketch775,Pad530,Pocket358,Sketch776,Pad531,Sketch777,Pocket359,Sketch778,Pad532]
  Origin = -> Origin043
  Tip = -> Pad532
FEATURE [Sketcher::SketchObject] Sketch779
  ArcFitTolerance = 1e-06
  AttachmentSupport = -> [XZ_Plane044]
  FullyConstrained = true
  MakeInternals = false
  MapMode = 5
  Placement = pos=(0,0,0) rot=(1,0,0;1.5708rad)
  sketch-geometry (1):
    g0: Circle CenterX=0 CenterY=0 CenterZ=0 NormalX=0 NormalY=0 NormalZ=1 AngleXU=0 Radius=4
  constraints (2):
    c: Coincident(g0,g-1)
    c: Diameter(g0) = 8
FEATURE [PartDesign::Pad] Pad533
  Direction = (0,-1,2e-16)
  Length = 5.4
  Length2 = 10
  Placement = pos=(0,0,0) rot=(1,0,0;1.5708rad)
  Profile = -> Sketch779
  ReferenceAxis = -> Sketch779 [N_Axis]
  Refine = true
  Suppressed = false
  Type = 0
FEATURE [Sketcher::SketchObject] Sketch780
  ArcFitTolerance = 1e-06
  AttachmentSupport = -> [Pad533]
  FullyConstrained = true
  MakeInternals = false
  MapMode = 5
  Placement = pos=(0,0,0) rot=(-1,0,0;1.5708rad)
  sketch-geometry (1):
    g0: Circle CenterX=0 CenterY=0 CenterZ=0 NormalX=0 NormalY=0 NormalZ=1 AngleXU=0 Radius=3
  constraints (2):
    c: Coincident(g0,g-1)
    c: Diameter(g0) = 6
FEATURE [PartDesign::Pad] Pad534
  BaseFeature = -> Pad533
  Direction = (0,1,2e-16)
  Length = 2.3
  Length2 = 10
  Placement = pos=(0,0,0) rot=(1,0,0;1.5708rad)
  Profile = -> Sketch780
  ReferenceAxis = -> Sketch780 [N_Axis]
  Refine = true
  Suppressed = false
  Type = 0
FEATURE [Sketcher::SketchObject] Sketch781
  ArcFitTolerance = 1e-06
  AttachmentSupport = -> [Pad534]
  ExternalGeometry = -> [Pad534]
  FullyConstrained = true
  MakeInternals = false
  MapMode = 5
  Placement = pos=(0,2.3,0) rot=(-1,0,0;1.5708rad)
  sketch-geometry (1):
    g0: Circle CenterX=0 CenterY=0 CenterZ=0 NormalX=0 NormalY=0 NormalZ=1 AngleXU=0 Radius=4.00001
  constraints (2):
    c: Coincident(g0,g-1)
    c: Tangent(g0,g-3)
FEATURE [PartDesign::Pad] Pad535
  BaseFeature = -> Pad534
  Direction = (0,1,2e-16)
  Length = 4.5
  Length2 = 10
  Placement = pos=(0,0,0) rot=(1,0,0;1.5708rad)
  Profile = -> Sketch781
  ReferenceAxis = -> Sketch781 [N_Axis]
  Refine = true
  Suppressed = false
  Type = 0
FEATURE [Sketcher::SketchObject] Sketch782
  ArcFitTolerance = 1e-06
  AttachmentSupport = -> [Pad535]
  ExternalGeometry = -> [Pad535]
  FullyConstrained = true
  MakeInternals = false
  MapMode = 5
  Placement = pos=(0,6.8,1.8e-15) rot=(-1,0,0;1.5708rad)
  sketch-geometry (1):
    g0: Circle CenterX=0 CenterY=0 CenterZ=0 NormalX=0 NormalY=0 NormalZ=1 AngleXU=0 Radius=2.99999
  constraints (2):
    c: Coincident(g0,g-1)
    c: Tangent(g0,g-3)
FEATURE [PartDesign::Pad] Pad536
  BaseFeature = -> Pad535
  Direction = (0,1,2e-16)
  Length = 2
  Length2 = 10
  Placement = pos=(0,0,0) rot=(1,0,0;1.5708rad)
  Profile = -> Sketch782
  ReferenceAxis = -> Sketch782 [N_Axis]
  Refine = true
  Suppressed = false
  Type = 0
FEATURE [Sketcher::SketchObject] Sketch783
  ArcFitTolerance = 1e-06
  AttachmentSupport = -> [Pad536]
  ExternalGeometry = -> [Pad536]
  FullyConstrained = true
  MakeInternals = false
  MapMode = 5
  Placement = pos=(0,8.8,3e-15) rot=(-1,0,0;1.5708rad)
  sketch-geometry (1):
    g0: Circle CenterX=0 CenterY=0 CenterZ=0 NormalX=0 NormalY=0 NormalZ=1 AngleXU=0 Radius=4.00001
  constraints (2):
    c: Coincident(g0,g-1)
    c: Tangent(g0,g-3)
FEATURE [PartDesign::Pad] Pad537
  BaseFeature = -> Pad536
  Direction = (0,1,2e-16)
  Length = 5
  Length2 = 10
  Placement = pos=(0,0,0) rot=(1,0,0;1.5708rad)
  Profile = -> Sketch783
  ReferenceAxis = -> Sketch783 [N_Axis]
  Refine = true
  Suppressed = false
  Type = 0
FEATURE [Sketcher::SketchObject] Sketch784
  ArcFitTolerance = 1e-06
  AttachmentSupport = -> [Pad537]
  ExternalGeometry = -> [Pad537]
  FullyConstrained = true
  MakeInternals = false
  MapMode = 5
  Placement = pos=(0,13.8,0) rot=(-1,0,0;1.5708rad)
  sketch-geometry (1):
    g0: Circle CenterX=0 CenterY=0 CenterZ=0 NormalX=0 NormalY=0 NormalZ=1 AngleXU=0 Radius=2.99999
  constraints (2):
    c: Coincident(g0,g-1)
    c: Tangent(g0,g-3)
FEATURE [PartDesign::Pad] Pad538
  BaseFeature = -> Pad537
  Direction = (0,1,2e-16)
  Length = 3.6
  Length2 = 10
  Placement = pos=(0,0,0) rot=(1,0,0;1.5708rad)
  Profile = -> Sketch784
  ReferenceAxis = -> Sketch784 [N_Axis]
  Refine = true
  Suppressed = false
  Type = 0
FEATURE [Sketcher::SketchObject] Sketch785
  ArcFitTolerance = 1e-06
  AttachmentSupport = -> [XY_Plane044]
  ExternalGeometry = -> [Pad538]
  FullyConstrained = true
  MakeInternals = false
  MapMode = 5
  sketch-geometry (16):
    g0: LineSegment StartX=2.49999 StartY=16.7 StartZ=0 EndX=2.49999 EndY=16.4 EndZ=0
    g1: LineSegment StartX=2.49999 StartY=16.4 StartZ=0 EndX=3.09999 EndY=16.4 EndZ=0
    g2: LineSegment StartX=3.09999 StartY=16.4 StartZ=0 EndX=3.09999 EndY=16.7 EndZ=0
    g3: LineSegment StartX=3.09999 StartY=16.7 StartZ=0 EndX=2.49999 EndY=16.7 EndZ=0
    g4: LineSegment StartX=2.49999 StartY=15.7 StartZ=0 EndX=2.49999 EndY=15.4 EndZ=0
    g5: LineSegment StartX=2.49999 StartY=15.4 StartZ=0 EndX=3.09999 EndY=15.4 EndZ=0
    g6: LineSegment StartX=3.09999 StartY=15.4 StartZ=0 EndX=3.09999 EndY=15.7 EndZ=0
    g7: LineSegment StartX=3.09999 StartY=15.7 StartZ=0 EndX=2.49999 EndY=15.7 EndZ=0
    g8: LineSegment StartX=2.49999 StartY=14.7 StartZ=0 EndX=2.49999 EndY=14.4 EndZ=0
    g9: LineSegment StartX=2.49999 StartY=14.4 StartZ=0 EndX=3.09999 EndY=14.4 EndZ=0
    g10: LineSegment StartX=3.09999 StartY=14.4 StartZ=0 EndX=3.09999 EndY=14.7 EndZ=0
    g11: LineSegment StartX=3.09999 StartY=14.7 StartZ=0 EndX=2.49999 EndY=14.7 EndZ=0
    g12: LineSegment [constr] StartX=2.49999 StartY=16.4 StartZ=0 EndX=2.49999 EndY=15.7 EndZ=0
    g13: LineSegment [constr] StartX=2.49999 StartY=15.4 StartZ=0 EndX=2.49999 EndY=14.7 EndZ=0
    g14: LineSegment [constr] StartX=3.09999 StartY=16.4 StartZ=0 EndX=3.09999 EndY=15.7 EndZ=0
    g15: LineSegment [constr] StartX=3.09999 StartY=15.4 StartZ=0 EndX=3.09999 EndY=14.7 EndZ=0
  constraints (46):
    c: Coincident(g0,g1)
    c: Coincident(g1,g2)
    c: Coincident(g2,g3)
    c: Coincident(g3,g0)
    c: Vertical(g0)
    c: Vertical(g2)
    c: Horizontal(g1)
    c: Horizontal(g3)
    c: Coincident(g4,g5)
    c: Coincident(g5,g6)
    c: Coincident(g6,g7)
    c: Coincident(g7,g4)
    c: Vertical(g4)
    c: Vertical(g6)
    c: Horizontal(g5)
    c: Horizontal(g7)
    c: Coincident(g8,g9)
    c: Coincident(g9,g10)
    c: Coincident(g10,g11)
    c: Coincident(g11,g8)
    c: Vertical(g8)
    c: Vertical(g10)
    c: Horizontal(g9)
    c: Horizontal(g11)
    c: DistanceY(g2,g2) = 0.3
    c: DistanceY(g6,g6) = 0.3
    c: DistanceY(g10,g10) = 0.3
    c: DistanceY(g-3,g-3) = 3.6
    c: DistanceX(g0,g-4) = 0.5
    c: Coincident(g12,g0)
    c: Coincident(g12,g4)
    c: Coincident(g13,g4)
    c: Coincident(g13,g8)
    c: Vertical(g12)
    c: Vertical(g13)
    c: DistanceX(g3,g3) = 0.6
    c: Coincident(g14,g1)
    c: Coincident(g14,g6)
    c: Coincident(g15,g5)
    c: Coincident(g15,g10)
    c: Vertical(g15)
    c: Vertical(g14)
    c: DistanceY(g2,g-4) = 0.7
    c: DistanceY(g14,g14) = 0.7
    c: DistanceY(g15,g15) = 0.7
    c: DistanceY(g-3,g9) = 0.6
FEATURE [PartDesign::Groove] Groove
  Angle = 360
  Angle2 = 60
  Axis = (0,1,0)
  Base = (0,0,0)
  BaseFeature = -> Pad538
  Placement = pos=(0,0,0) rot=(1,0,0;1.5708rad)
  Profile = -> Sketch785
  ReferenceAxis = -> Sketch785 [V_Axis]
  Refine = true
  Suppressed = false
  Type = 0
FEATURE [Sketcher::SketchObject] Sketch786
  ArcFitTolerance = 1e-06
  AttachmentSupport = -> [Groove]
  FullyConstrained = true
  MakeInternals = false
  MapMode = 5
  Placement = pos=(0,17.4,0) rot=(-1,0,0;1.5708rad)
  sketch-geometry (1):
    g0: Circle CenterX=0 CenterY=0 CenterZ=0 NormalX=0 NormalY=0 NormalZ=1 AngleXU=0 Radius=4
  constraints (2):
    c: Coincident(g0,g-1)
    c: Diameter(g0) = 8
FEATURE [Sketcher::SketchObject] Sketch787
  ArcFitTolerance = 1e-06
  AttachmentOffset = pos=(0,0,10) rot=(0,0,1;0rad)
  AttachmentSupport = -> [Groove]
  FullyConstrained = true
  MakeInternals = false
  MapMode = 5
  Placement = pos=(0,27.4,2.2e-15) rot=(-1,0,0;1.5708rad)
  sketch-geometry (1):
    g0: Circle CenterX=0 CenterY=0 CenterZ=0 NormalX=0 NormalY=0 NormalZ=1 AngleXU=0 Radius=2.95
  constraints (2):
    c: Coincident(g0,g-1)
    c: Diameter(g0) = 5.9
FEATURE [PartDesign::AdditiveLoft] AdditiveLoft007
  BaseFeature = -> Groove
  Closed = false
  Placement = pos=(0,0,0) rot=(1,0,0;1.5708rad)
  Profile = -> Sketch786
  Refine = true
  Ruled = false
  Sections = -> [Sketch787]
  Suppressed = false
FEATURE [Sketcher::SketchObject] Sketch788
  ArcFitTolerance = 1e-06
  AttachmentSupport = -> [YZ_Plane044]
  ExternalGeometry = -> [AdditiveLoft007]
  FullyConstrained = true
  MakeInternals = false
  MapMode = 5
  Placement = pos=(0,0,0) rot=(0.57735,0.57735,0.57735;2.0944rad)
  sketch-geometry (4):
    g0: LineSegment StartX=21.7 StartY=3.7 StartZ=0 EndX=21.7 EndY=3.1 EndZ=0
    g1: LineSegment StartX=21.7 StartY=3.1 StartZ=0 EndX=22 EndY=3.1 EndZ=0
    g2: LineSegment StartX=22 StartY=3.1 StartZ=0 EndX=22 EndY=3.7 EndZ=0
    g3: LineSegment StartX=22 StartY=3.7 StartZ=0 EndX=21.7 EndY=3.7 EndZ=0
  constraints (12):
    c: Coincident(g0,g1)
    c: Coincident(g1,g2)
    c: Coincident(g2,g3)
    c: Coincident(g3,g0)
    c: Vertical(g0)
    c: Vertical(g2)
    c: Horizontal(g1)
    c: Horizontal(g3)
    c: DistanceX(g3,g3) = 0.3
    c: DistanceY(g0,g0) = 0.6
    c: DistanceX(g-3,g0) = 4.3
    c: DistanceY(g0,g-3) = 0.9
FEATURE [PartDesign::Groove] Groove001
  Angle = 360
  Angle2 = 60
  Axis = (0,1,0)
  Base = (0,0,0)
  BaseFeature = -> AdditiveLoft007
  Placement = pos=(0,0,0) rot=(1,0,0;1.5708rad)
  Profile = -> Sketch788
  ReferenceAxis = -> Sketch788 [H_Axis]
  Refine = true
  Reversed = true
  Suppressed = false
  Type = 0
FEATURE [Sketcher::SketchObject] Sketch789
  ArcFitTolerance = 1e-06
  AttachmentSupport = -> [Groove001]
  FullyConstrained = true
  MakeInternals = false
  MapMode = 5
  Placement = pos=(0,27.4,0) rot=(-1,0,0;1.5708rad)
  sketch-geometry (1):
    g0: Circle CenterX=0 CenterY=0 CenterZ=0 NormalX=0 NormalY=0 NormalZ=1 AngleXU=0 Radius=1.95
  constraints (2):
    c: Coincident(g0,g-1)
    c: Diameter(g0) = 3.9
FEATURE [Sketcher::SketchObject] Sketch790
  ArcFitTolerance = 1e-06
  AttachmentOffset = pos=(0,0,7) rot=(0,0,1;0rad)
  AttachmentSupport = -> [Groove001]
  FullyConstrained = true
  MakeInternals = false
  MapMode = 5
  Placement = pos=(0,34.4,1.6e-15) rot=(-1,0,0;1.5708rad)
  sketch-geometry (1):
    g0: Circle CenterX=0 CenterY=0 CenterZ=0 NormalX=0 NormalY=0 NormalZ=1 AngleXU=0 Radius=1.6
  constraints (2):
    c: Coincident(g0,g-1)
    c: Diameter(g0) = 3.2
FEATURE [PartDesign::AdditiveLoft] AdditiveLoft008
  BaseFeature = -> Groove001
  Closed = false
  Placement = pos=(0,0,0) rot=(1,0,0;1.5708rad)
  Profile = -> Sketch789
  Refine = true
  Ruled = false
  Sections = -> [Sketch790]
  Suppressed = false
FEATURE [Sketcher::SketchObject] Sketch791
  ArcFitTolerance = 1e-06
  AttachmentSupport = -> [AdditiveLoft008]
  FullyConstrained = true
  MakeInternals = false
  MapMode = 5
  Placement = pos=(0,-5.4,0) rot=(1,0,0;1.5708rad)
  sketch-geometry (1):
    g0: Circle CenterX=0 CenterY=0 CenterZ=0 NormalX=0 NormalY=0 NormalZ=1 AngleXU=0 Radius=2.7
  constraints (2):
    c: Coincident(g0,g-1)
    c: Diameter(g0) = 5.4
FEATURE [Sketcher::SketchObject] Sketch792
  ArcFitTolerance = 1e-06
  AttachmentOffset = pos=(0,0,2) rot=(0,0,1;0rad)
  AttachmentSupport = -> [AdditiveLoft008]
  FullyConstrained = true
  MakeInternals = false
  MapMode = 5
  Placement = pos=(0,-7.4,4e-16) rot=(1,0,0;1.5708rad)
  sketch-geometry (1):
    g0: Circle CenterX=0 CenterY=0 CenterZ=0 NormalX=0 NormalY=0 NormalZ=1 AngleXU=0 Radius=2.45
  constraints (2):
    c: Coincident(g0,g-1)
    c: Diameter(g0) = 4.9
FEATURE [PartDesign::AdditiveLoft] AdditiveLoft009
  BaseFeature = -> AdditiveLoft008
  Closed = false
  Placement = pos=(0,0,0) rot=(1,0,0;1.5708rad)
  Profile = -> Sketch792
  Refine = true
  Ruled = false
  Sections = -> [Sketch791]
  Suppressed = false
FEATURE [Sketcher::SketchObject] Sketch793
  ArcFitTolerance = 1e-06
  AttachmentSupport = -> [AdditiveLoft009]
  FullyConstrained = true
  MakeInternals = false
  MapMode = 5
  Placement = pos=(0,-7.4,3.1e-15) rot=(1,0,0;1.5708rad)
  sketch-geometry (1):
    g0: Circle CenterX=0 CenterY=0 CenterZ=0 NormalX=0 NormalY=0 NormalZ=1 AngleXU=0 Radius=2
  constraints (2):
    c: Coincident(g0,g-1)
    c: Diameter(g0) = 4
FEATURE [PartDesign::Pad] Pad539
  BaseFeature = -> AdditiveLoft009
  Direction = (0,-1,2e-16)
  Length = 1
  Length2 = 10
  Placement = pos=(0,0,0) rot=(1,0,0;1.5708rad)
  Profile = -> Sketch793
  ReferenceAxis = -> Sketch793 [N_Axis]
  Refine = true
  Suppressed = false
  Type = 0
FEATURE [Sketcher::SketchObject] Sketch794
  ArcFitTolerance = 1e-06
  AttachmentSupport = -> [XY_Plane044]
  ExternalGeometry = -> [Pad539]
  FullyConstrained = true
  MakeInternals = false
  MapMode = 5
  sketch-geometry (8):
    g0: LineSegment StartX=-6.45 StartY=-3.5 StartZ=0 EndX=6.45 EndY=-3.5 EndZ=0
    g1: LineSegment StartX=6.45 StartY=-3.5 StartZ=0 EndX=6.45 EndY=2.3 EndZ=0
    g2: LineSegment StartX=6.45 StartY=2.3 StartZ=0 EndX=4.00001 EndY=8.8 EndZ=0
    g3: LineSegment StartX=-4.00001 StartY=8.8 StartZ=0 EndX=-6.45 EndY=2.3 EndZ=0
    g4: LineSegment StartX=-6.45 StartY=-3.5 StartZ=0 EndX=-6.45 EndY=2.3 EndZ=0
    g5: LineSegment [constr] StartX=-4.00001 StartY=2.3 StartZ=0 EndX=-6.45 EndY=2.3 EndZ=0
    g6: LineSegment [constr] StartX=4.00001 StartY=2.3 StartZ=0 EndX=6.45 EndY=2.3 EndZ=0
    g7: LineSegment StartX=4.00001 StartY=8.8 StartZ=0 EndX=-4.00001 EndY=8.8 EndZ=0
  constraints (20):
    c: Horizontal(g0)
    c: Coincident(g1,g0)
    c: Vertical(g1)
    c: Coincident(g2,g1)
    c: Coincident(g2,g-4)
    c: Coincident(g3,g-4)
    c: Coincident(g4,g0)
    c: Coincident(g4,g3)
    c: Vertical(g4)
    c: Coincident(g5,g-5)
    c: Coincident(g5,g3)
    c: Horizontal(g5)
    c: Coincident(g6,g-5)
    c: Coincident(g6,g1)
    c: Horizontal(g6)
    c: DistanceX(g0,g0) = 12.9
    c: DistanceX(g0,g-1) = 6.45
    c: Coincident(g7,g2)
    c: Coincident(g7,g3)
    c: DistanceY(g-6,g0) = 1.9
FEATURE [PartDesign::Pad] Pad540
  BaseFeature = -> Pad539
  Direction = (0,0,1)
  Length = 1
  Length2 = 10
  Placement = pos=(0,0,0) rot=(1,0,0;1.5708rad)
  Profile = -> Sketch794
  ReferenceAxis = -> Sketch794 [N_Axis]
  Refine = true
  Suppressed = false
  Type = 0
FEATURE [PartDesign::Pad] Pad541
  BaseFeature = -> Pad540
  Direction = (0,0,1)
  Length = 1
  Length2 = 10
  Placement = pos=(0,0,0) rot=(1,0,0;1.5708rad)
  Profile = -> Sketch794
  ReferenceAxis = -> Sketch794 [N_Axis]
  Refine = true
  Reversed = true
  Suppressed = false
  Type = 0
FEATURE [Sketcher::SketchObject] Sketch795
  ArcFitTolerance = 1e-06
  AttachmentSupport = -> [Pad541]
  ExternalGeometry = -> [Pad541]
  FullyConstrained = true
  MakeInternals = false
  MapMode = 5
  Placement = pos=(-6.45,0,-5.7e-15) rot=(0.707107,0,-0.707107;3.14159rad)
  sketch-geometry (1):
    g0: Circle CenterX=0 CenterY=3.2 CenterZ=0 NormalX=0 NormalY=0 NormalZ=1 AngleXU=0 Radius=1.8
  constraints (3):
    c: PointOnObject(g0,g-2)
    c: Radius(g0) = 1.8
    c: DistanceY(g0,g-3) = 2.2
FEATURE [PartDesign::Pad] Pad542
  BaseFeature = -> Pad541
  Direction = (-1,0,-2e-16)
  Length = 4
  Length2 = 10
  Placement = pos=(0,0,0) rot=(1,0,0;1.5708rad)
  Profile = -> Sketch795
  ReferenceAxis = -> Sketch795 [N_Axis]
  Refine = true
  Reversed = true
  Suppressed = false
  Type = 0
FEATURE [PartDesign::Pad] Pad543
  BaseFeature = -> Pad542
  Direction = (-1,0,-2e-16)
  Length = 4
  Length2 = 10
  Placement = pos=(0,0,0) rot=(1,0,0;1.5708rad)
  Profile = -> Sketch795
  ReferenceAxis = -> Sketch795 [N_Axis]
  Refine = true
  Suppressed = false
  Type = 0
FEATURE [Sketcher::SketchObject] Sketch796
  ArcFitTolerance = 1e-06
  AttachmentOffset = pos=(0,0,3) rot=(0,0,1;0rad)
  AttachmentSupport = -> [Pad543]
  ExternalGeometry = -> [Pad543]
  FullyConstrained = true
  MakeInternals = false
  MapMode = 5
  Placement = pos=(0,0,-4) rot=(1,0,0;3.14159rad)
  sketch-geometry (4):
    g0: LineSegment StartX=-1.2 StartY=3.4 StartZ=0 EndX=-1.2 EndY=-25.4 EndZ=0
    g1: LineSegment StartX=-1.2 StartY=-25.4 StartZ=0 EndX=1.2 EndY=-25.4 EndZ=0
    g2: LineSegment StartX=1.2 StartY=-25.4 StartZ=0 EndX=1.2 EndY=3.4 EndZ=0
    g3: LineSegment StartX=1.2 StartY=3.4 StartZ=0 EndX=-1.2 EndY=3.4 EndZ=0
  constraints (13):
    c: Coincident(g0,g1)
    c: Coincident(g1,g2)
    c: Coincident(g2,g3)
    c: Coincident(g3,g0)
    c: Vertical(g0)
    c: Vertical(g2)
    c: Horizontal(g1)
    c: Horizontal(g3)
    c: DistanceX(g0,g-1) = 1.2
    c: DistanceX(g-1,g2) = 1.2
    c: DistanceY(g0,g0) = 28.8
    c: DistanceY(g-4,g1) = 2
    c: DistanceY(g2,g-3) = 2
FEATURE [PartDesign::Pocket] Pocket360
  BaseFeature = -> Pad543
  Direction = (0,0,1)
  Length = 5.2
  Length2 = 5
  Placement = pos=(0,0,0) rot=(1,0,0;1.5708rad)
  Profile = -> Sketch796
  ReferenceAxis = -> Sketch796 [N_Axis]
  Refine = true
  Suppressed = false
  Type = 0
FEATURE [Sketcher::SketchObject] Sketch797
  ArcFitTolerance = 1e-06
  AttachmentOffset = pos=(0,0,3) rot=(0,0,1;0rad)
  AttachmentSupport = -> [Pocket360]
  ExternalGeometry = -> [Pocket360]
  FullyConstrained = true
  MakeInternals = false
  MapMode = 5
  Placement = pos=(0,0,4) rot=(0,0,1;3.14159rad)
  sketch-geometry (4):
    g0: LineSegment StartX=-2 StartY=5.4 StartZ=0 EndX=-2 EndY=-16.7 EndZ=0
    g1: LineSegment StartX=-2 StartY=-16.7 StartZ=0 EndX=2 EndY=-16.7 EndZ=0
    g2: LineSegment StartX=2 StartY=-16.7 StartZ=0 EndX=2 EndY=5.4 EndZ=0
    g3: LineSegment StartX=2 StartY=5.4 StartZ=0 EndX=-2 EndY=5.4 EndZ=0
  constraints (12):
    c: Coincident(g0,g1)
    c: Coincident(g1,g2)
    c: Coincident(g2,g3)
    c: Coincident(g3,g0)
    c: Vertical(g0)
    c: Vertical(g2)
    c: Horizontal(g1)
    c: Horizontal(g3)
    c: DistanceX(g0,g-1) = 2
    c: DistanceX(g-1,g2) = 2
    c: PointOnObject(g0,g-3)
    c: PointOnObject(g0,g-4)
FEATURE [PartDesign::Pad] Pad544
  BaseFeature = -> Pocket360
  Direction = (0,0,1)
  Length = 2.5
  Length2 = 10
  Placement = pos=(0,0,0) rot=(1,0,0;1.5708rad)
  Profile = -> Sketch797
  ReferenceAxis = -> Sketch797 [N_Axis]
  Refine = true
  Reversed = true
  Suppressed = false
  Type = 0
FEATURE [PartDesign::Pad] Pad545
  BaseFeature = -> Pad544
  Direction = (0,0,1)
  Length = 1.4
  Length2 = 10
  Placement = pos=(0,0,0) rot=(1,0,0;1.5708rad)
  Profile = -> Sketch797
  ReferenceAxis = -> Sketch797 [N_Axis]
  Refine = true
  Suppressed = false
  Type = 0
FEATURE [Sketcher::SketchObject] Sketch798
  ArcFitTolerance = 1e-06
  AttachmentSupport = -> [Pad545]
  ExternalGeometry = -> [Pad545]
  FullyConstrained = true
  MakeInternals = false
  MapMode = 5
  Placement = pos=(-2,0,0) rot=(0.707107,0,-0.707107;3.14159rad)
  sketch-geometry (3):
    g0: LineSegment StartX=-3 StartY=-16.7 StartZ=0 EndX=-5.4 EndY=-16.7 EndZ=0
    g1: LineSegment StartX=-5.4 StartY=-16.7 StartZ=0 EndX=-5.4 EndY=-14.3 EndZ=0
    g2: LineSegment StartX=-5.4 StartY=-14.3 StartZ=0 EndX=-3 EndY=-16.7 EndZ=0
  constraints (8):
    c: PointOnObject(g0,g-4)
    c: Coincident(g0,g-4)
    c: Coincident(g1,g0)
    c: PointOnObject(g1,g-3)
    c: Coincident(g2,g1)
    c: Coincident(g2,g0)
    c: Angle(g1,g2) = 0.785398
    c: DistanceY(g1,g1) = 2.4
FEATURE [PartDesign::Pocket] Pocket361
  BaseFeature = -> Pad545
  Direction = (1,0,2e-16)
  Length = 5
  Length2 = 5
  Placement = pos=(0,0,0) rot=(1,0,0;1.5708rad)
  Profile = -> Sketch798
  ReferenceAxis = -> Sketch798 [N_Axis]
  Refine = true
  Suppressed = false
  Type = 0
FEATURE [Sketcher::SketchObject] Sketch799
  ArcFitTolerance = 1e-06
  AttachmentSupport = -> [Pocket361]
  ExternalGeometry = -> [Pocket361]
  FullyConstrained = true
  MakeInternals = false
  MapMode = 5
  Placement = pos=(-2,0,0) rot=(0.707107,0,-0.707107;3.14159rad)
  sketch-geometry (4):
    g0: LineSegment StartX=-5.4 StartY=-4.6 StartZ=0 EndX=-7.5 EndY=-2.5 EndZ=0
    g1: LineSegment StartX=-7.5 StartY=-2.5 StartZ=0 EndX=-7.5 EndY=-1.4 EndZ=0
    g2: LineSegment StartX=-7.5 StartY=-1.4 StartZ=0 EndX=-5.4 EndY=-1.4 EndZ=0
    g3: LineSegment StartX=-5.4 StartY=-1.4 StartZ=0 EndX=-5.4 EndY=-4.6 EndZ=0
  constraints (12):
    c: PointOnObject(g0,g-3)
    c: Coincident(g1,g0)
    c: Vertical(g1)
    c: Coincident(g2,g1)
    c: PointOnObject(g2,g-3)
    c: Coincident(g3,g2)
    c: Coincident(g3,g0)
    c: DistanceY(g3,g3) = 3.2
    c: DistanceX(g2,g2) = 2.1
    c: Horizontal(g2)
    c: Angle(g3,g0) = 0.785398
    c: DistanceY(g2,g-3) = 6.8
FEATURE [PartDesign::Pad] Pad546
  BaseFeature = -> Pocket361
  Direction = (-1,0,-2e-16)
  Length = 4
  Length2 = 10
  Placement = pos=(0,0,0) rot=(1,0,0;1.5708rad)
  Profile = -> Sketch799
  ReferenceAxis = -> Sketch799 [N_Axis]
  Refine = true
  Reversed = true
  Suppressed = false
  Type = 0
FEATURE [Sketcher::SketchObject] Sketch800
  ArcFitTolerance = 1e-06
  AttachmentSupport = -> [Pad546]
  ExternalGeometry = -> [Pad546]
  FullyConstrained = true
  MakeInternals = false
  MapMode = 5
  Placement = pos=(0,0,5.4) rot=(0,0,1;3.14159rad)
  sketch-geometry (4):
    g0: LineSegment StartX=1 StartY=-1.4 StartZ=0 EndX=1 EndY=5.4 EndZ=0
    g1: LineSegment StartX=1 StartY=5.4 StartZ=0 EndX=-1 EndY=5.4 EndZ=0
    g2: LineSegment StartX=-1 StartY=5.4 StartZ=0 EndX=-1 EndY=-1.4 EndZ=0
    g3: LineSegment StartX=-1 StartY=-1.4 StartZ=0 EndX=1 EndY=-1.4 EndZ=0
  constraints (12):
    c: Coincident(g0,g1)
    c: Coincident(g1,g2)
    c: Coincident(g2,g3)
    c: Coincident(g3,g0)
    c: Vertical(g0)
    c: Vertical(g2)
    c: Horizontal(g1)
    c: Horizontal(g3)
    c: PointOnObject(g0,g-4)
    c: PointOnObject(g1,g-3)
    c: DistanceX(g0,g-5) = 1
    c: DistanceX(g-6,g1) = 1
FEATURE [PartDesign::Pad] Pad547
  BaseFeature = -> Pad546
  Direction = (0,0,1)
  Length = 1.8
  Length2 = 10
  Placement = pos=(0,0,0) rot=(1,0,0;1.5708rad)
  Profile = -> Sketch800
  ReferenceAxis = -> Sketch800 [N_Axis]
  Refine = true
  Suppressed = false
  Type = 0
FEATURE [PartDesign::Body] Body041  label="Head_Gun"
  AllowCompound = false
  Group = -> [Sketch779,Pad533,Sketch780,Pad534,Sketch781,Pad535,Sketch782,Pad536,Sketch783,Pad537,Sketch784,Pad538,Sketch785,Groove,Sketch786,Sketch787,AdditiveLoft007,Sketch788,Groove001,Sketch789,Sketch790,AdditiveLoft008,Sketch791,Sketch792,AdditiveLoft009,Sketch793,Pad539,Sketch794,Pad540,Pad541,Sketch795,Pad542,Pad543,Sketch796,Pocket360,Sketch797,Pad544,Pad545,Sketch798,Pocket361,Sketch799,Pad546,+2 more]
  Origin = -> Origin044
  Placement = pos=(52.5,4,24.4) rot=(0,0,1;0rad)
  Tip = -> Pad547
FEATURE [PartDesign::SubShapeBinder] Binder006
  BindCopyOnChange = 0
  BindMode = 0
  ClaimChildren = false
  Context = -> Part001 [Body042.Binder006.]
  Fuse = false
  MakeFace = true
  OffsetFill = false
  OffsetIntersection = false
  OffsetJoinType = 0
  OffsetOpenResult = false
  PartialLoad = false
  Refine = true
  Relative = true
  Support = -> [Body037[Chamfer022.Face54]]
  _Version = 2
FEATURE [Sketcher::SketchObject] Sketch801
  ArcFitTolerance = 1e-06
  AttachmentSupport = -> [Binder006]
  ExternalGeometry = -> [Binder006]
  FullyConstrained = true
  MakeInternals = false
  MapMode = 5
  Placement = pos=(0,0.8,-4e-16) rot=(1,0,0;1.5708rad)
  sketch-geometry (15):
    g0: LineSegment StartX=32.05 StartY=10.5 StartZ=0 EndX=32.05 EndY=2.5 EndZ=0
    g1: LineSegment StartX=32.05 StartY=2.5 StartZ=0 EndX=39.95 EndY=2.5 EndZ=0
    g2: LineSegment StartX=39.95 StartY=2.5 StartZ=0 EndX=39.95 EndY=10.5 EndZ=0
    g3: LineSegment StartX=39.95 StartY=10.5 StartZ=0 EndX=43.95 EndY=10.5 EndZ=0
    g4: LineSegment StartX=43.95 StartY=10.5 StartZ=0 EndX=43.95 EndY=18.5 EndZ=0
    g5: LineSegment StartX=43.95 StartY=18.5 StartZ=0 EndX=46 EndY=20.55 EndZ=0
    g6: LineSegment StartX=46 StartY=20.55 StartZ=0 EndX=46 EndY=28.3 EndZ=0
    g7: LineSegment StartX=46 StartY=28.3 StartZ=0 EndX=46 EndY=31.45 EndZ=0
    g8: LineSegment StartX=46 StartY=31.45 StartZ=0 EndX=43.95 EndY=33.5 EndZ=0
    g9: LineSegment StartX=43.95 StartY=33.5 StartZ=0 EndX=28.05 EndY=33.5 EndZ=0
    g10: LineSegment StartX=28.05 StartY=33.5 StartZ=0 EndX=26 EndY=31.45 EndZ=0
    g11: LineSegment StartX=26 StartY=31.45 StartZ=0 EndX=26 EndY=20.55 EndZ=0
    g12: LineSegment StartX=26 StartY=20.55 StartZ=0 EndX=28.05 EndY=18.5 EndZ=0
    g13: LineSegment StartX=28.05 StartY=18.5 StartZ=0 EndX=28.05 EndY=10.5 EndZ=0
    g14: LineSegment StartX=28.05 StartY=10.5 StartZ=0 EndX=32.05 EndY=10.5 EndZ=0
  constraints (32):
    c: Coincident(g0,g-26)
    c: Vertical(g0)
    c: Coincident(g1,g0)
    c: Horizontal(g1)
    c: Coincident(g2,g1)
    c: Coincident(g2,g-24)
    c: Vertical(g2)
    c: Coincident(g3,g2)
    c: Coincident(g3,g-23)
    c: Coincident(g4,g3)
    c: Coincident(g4,g-22)
    c: Coincident(g5,g4)
    c: Coincident(g5,g-21)
    c: Coincident(g6,g5)
    c: Coincident(g6,g-19)
    c: Coincident(g7,g6)
    c: Coincident(g7,g-17)
    c: Coincident(g8,g7)
    c: Coincident(g8,g-16)
    c: Coincident(g9,g8)
    c: Coincident(g9,g-15)
    c: Coincident(g10,g9)
    c: Coincident(g10,g-14)
    c: Coincident(g11,g10)
    c: Coincident(g11,g-7)
    c: Coincident(g12,g11)
    c: Coincident(g12,g-4)
    c: Coincident(g13,g12)
    c: Coincident(g13,g-26)
    c: Coincident(g14,g13)
    c: Coincident(g14,g0)
    c: DistanceY(g0,g0) = 8
FEATURE [PartDesign::Pad] Pad548
  Direction = (0,-1,2e-16)
  Length = 3
  Length2 = 10
  Profile = -> Sketch801
  ReferenceAxis = -> Sketch801 [N_Axis]
  Refine = true
  Suppressed = false
  Type = 0
FEATURE [Sketcher::SketchObject] Sketch802
  ArcFitTolerance = 1e-06
  AttachmentSupport = -> [Pad548]
  ExternalGeometry = -> [Pad548]
  FullyConstrained = true
  MakeInternals = false
  MapMode = 5
  Placement = pos=(0,-2.2,5e-16) rot=(1,0,0;1.5708rad)
  sketch-geometry (16):
    g0: LineSegment StartX=26 StartY=20.55 StartZ=0 EndX=28.05 EndY=18.5 EndZ=0
    g1: LineSegment StartX=28.05 StartY=18.5 StartZ=0 EndX=28.05 EndY=10.5 EndZ=0
    g2: LineSegment StartX=28.05 StartY=10.5 StartZ=0 EndX=32.05 EndY=10.5 EndZ=0
    g3: LineSegment StartX=32.05 StartY=10.5 StartZ=0 EndX=35.25 EndY=10.5 EndZ=0
    g4: LineSegment StartX=35.25 StartY=10.5 StartZ=0 EndX=35.25 EndY=5.5 EndZ=0
    g5: LineSegment StartX=35.25 StartY=5.5 StartZ=0 EndX=36.75 EndY=5.5 EndZ=0
    g6: LineSegment StartX=36.75 StartY=5.5 StartZ=0 EndX=36.75 EndY=10.5 EndZ=0
    g7: LineSegment StartX=36.75 StartY=10.5 StartZ=0 EndX=39.95 EndY=10.5 EndZ=0
    g8: LineSegment StartX=39.95 StartY=10.5 StartZ=0 EndX=43.95 EndY=10.5 EndZ=0
    g9: LineSegment StartX=43.95 StartY=10.5 StartZ=0 EndX=43.95 EndY=18.5 EndZ=0
    g10: LineSegment StartX=43.95 StartY=18.5 StartZ=0 EndX=46 EndY=20.55 EndZ=0
    g11: LineSegment StartX=46 StartY=20.55 StartZ=0 EndX=46 EndY=31.45 EndZ=0
    g12: LineSegment StartX=46 StartY=31.45 StartZ=0 EndX=43.95 EndY=33.5 EndZ=0
    g13: LineSegment StartX=43.95 StartY=33.5 StartZ=0 EndX=28.05 EndY=33.5 EndZ=0
    g14: LineSegment StartX=26 StartY=20.55 StartZ=0 EndX=26 EndY=31.45 EndZ=0
    g15: LineSegment StartX=26 StartY=31.45 StartZ=0 EndX=28.05 EndY=33.5 EndZ=0
  constraints (37):
    c: Coincident(g0,g-10)
    c: Coincident(g0,g-3)
    c: Coincident(g1,g0)
    c: Coincident(g1,g-4)
    c: Coincident(g2,g1)
    c: Coincident(g2,g-5)
    c: Coincident(g3,g2)
    c: Horizontal(g3)
    c: Coincident(g4,g3)
    c: Vertical(g4)
    c: Coincident(g5,g4)
    c: Horizontal(g5)
    c: Coincident(g6,g5)
    c: Vertical(g6)
    c: Coincident(g7,g6)
    c: Coincident(g7,g-8)
    c: Horizontal(g7)
    c: Coincident(g8,g7)
    c: Coincident(g8,g-9)
    c: Coincident(g9,g8)
    c: Coincident(g9,g-15)
    c: Coincident(g10,g9)
    c: Coincident(g10,g-15)
    c: Coincident(g11,g10)
    c: Coincident(g11,g-14)
    c: Coincident(g12,g11)
    c: Coincident(g12,g-13)
    c: Coincident(g13,g12)
    c: Coincident(g13,g-12)
    c: Coincident(g14,g0)
    c: Coincident(g14,g-11)
    c: Coincident(g15,g14)
    c: Coincident(g15,g13)
    c: DistanceX(g5,g5) = 1.5
    c: DistanceY(g4,g4) = 5
    c: DistanceX(g-6,g-6) = 7.9
    c: DistanceX(g2,g3) = 3.2
FEATURE [PartDesign::Pad] Pad549
  BaseFeature = -> Pad548
  Direction = (0,-1,2e-16)
  Length = 1.5
  Length2 = 10
  Profile = -> Sketch802
  ReferenceAxis = -> Sketch802 [N_Axis]
  Refine = true
  Suppressed = false
  Type = 0
FEATURE [Sketcher::SketchObject] Sketch803
  ArcFitTolerance = 1e-06
  AttachmentSupport = -> [Pad549]
  ExternalGeometry = -> [Pad549]
  FullyConstrained = true
  MakeInternals = false
  MapMode = 5
  Placement = pos=(0,-3.7,9e-16) rot=(1,0,0;1.5708rad)
  sketch-geometry (8):
    g0: LineSegment StartX=26 StartY=31.45 StartZ=0 EndX=28.05 EndY=33.5 EndZ=0
    g1: LineSegment StartX=28.05 StartY=33.5 StartZ=0 EndX=43.95 EndY=33.5 EndZ=0
    g2: LineSegment StartX=43.95 StartY=33.5 StartZ=0 EndX=46 EndY=31.45 EndZ=0
    g3: LineSegment StartX=46 StartY=31.45 StartZ=0 EndX=46 EndY=20.55 EndZ=0
    g4: LineSegment StartX=46 StartY=20.55 StartZ=0 EndX=43.95 EndY=18.5 EndZ=0
    g5: LineSegment StartX=43.95 StartY=18.5 StartZ=0 EndX=28.05 EndY=18.5 EndZ=0
    g6: LineSegment StartX=28.05 StartY=18.5 StartZ=0 EndX=26 EndY=20.55 EndZ=0
    g7: LineSegment StartX=26 StartY=20.55 StartZ=0 EndX=26 EndY=31.45 EndZ=0
  constraints (16):
    c: Coincident(g0,g-9)
    c: Coincident(g0,g-4)
    c: Coincident(g1,g0)
    c: Coincident(g1,g-5)
    c: Coincident(g2,g1)
    c: Coincident(g2,g-6)
    c: Coincident(g3,g2)
    c: Coincident(g3,g-7)
    c: Coincident(g4,g3)
    c: Coincident(g4,g-7)
    c: Coincident(g5,g4)
    c: Coincident(g5,g-8)
    c: Coincident(g6,g5)
    c: Coincident(g6,g-9)
    c: Coincident(g7,g6)
    c: Coincident(g7,g0)
FEATURE [PartDesign::Pad] Pad550
  BaseFeature = -> Pad549
  Direction = (0,-1,2e-16)
  Length = 1
  Length2 = 10
  Profile = -> Sketch803
  ReferenceAxis = -> Sketch803 [N_Axis]
  Refine = true
  Suppressed = false
  Type = 0
FEATURE [Sketcher::SketchObject] Sketch804
  ArcFitTolerance = 1e-06
  AttachmentSupport = -> [Pad550]
  ExternalGeometry = -> [Pad550]
  FullyConstrained = true
  MakeInternals = false
  MapMode = 5
  Placement = pos=(0,-4.7,1.1e-15) rot=(1,0,0;1.5708rad)
  sketch-geometry (4):
    g0: LineSegment StartX=28.5 StartY=30.5 StartZ=0 EndX=28.5 EndY=21.5 EndZ=0
    g1: LineSegment StartX=28.5 StartY=21.5 StartZ=0 EndX=43.5 EndY=21.5 EndZ=0
    g2: LineSegment StartX=43.5 StartY=21.5 StartZ=0 EndX=43.5 EndY=30.5 EndZ=0
    g3: LineSegment StartX=43.5 StartY=30.5 StartZ=0 EndX=28.5 EndY=30.5 EndZ=0
  constraints (14):
    c: Coincident(g0,g1)
    c: Coincident(g1,g2)
    c: Coincident(g2,g3)
    c: Coincident(g3,g0)
    c: Vertical(g0)
    c: Vertical(g2)
    c: Horizontal(g1)
    c: Horizontal(g3)
    c: DistanceX(g3,g3) = 15
    c: DistanceY(g0,g0) = 9
    c: DistanceX(g-4,g-4) = 15.9
    c: DistanceY(g-5,g-5) = 10.9
    c: DistanceY(g0,g-3) = 0.95
    c: DistanceX(g-4,g0) = 0.45
FEATURE [PartDesign::Pad] Pad551
  BaseFeature = -> Pad550
  Direction = (0,-1,2e-16)
  Length = 2
  Length2 = 10
  Profile = -> Sketch804
  ReferenceAxis = -> Sketch804 [N_Axis]
  Refine = true
  Suppressed = false
  Type = 0
FEATURE [Sketcher::SketchObject] Sketch805
  ArcFitTolerance = 1e-06
  AttachmentSupport = -> [Pad551]
  ExternalGeometry = -> [Pad551]
  FullyConstrained = true
  MakeInternals = false
  MapMode = 5
  Placement = pos=(39.95,0,0) rot=(0.57735,0.57735,0.57735;2.0944rad)
  sketch-geometry (5):
    g0: ArcOfCircle CenterX=0.8 CenterY=5.5 CenterZ=0 NormalX=0 NormalY=0 NormalZ=1 AngleXU=0 Radius=1.5 StartAngle=1.5708 EndAngle=4.71239
    g1: LineSegment StartX=0.8 StartY=7 StartZ=0 EndX=0.8 EndY=4 EndZ=0
    g2: ArcOfCircle CenterX=0.8 CenterY=5.5 CenterZ=0 NormalX=0 NormalY=0 NormalZ=1 AngleXU=0 Radius=3 StartAngle=3.14159 EndAngle=4.71239
    g3: LineSegment StartX=-2.2 StartY=5.5 StartZ=0 EndX=-2.2 EndY=2.5 EndZ=0
    g4: LineSegment StartX=-2.2 StartY=2.5 StartZ=0 EndX=0.8 EndY=2.5 EndZ=0
  constraints (13):
    c: PointOnObject(g0,g-3)
    c: PointOnObject(g0,g-3)
    c: DistanceY(g-4,g0) = 1.5
    c: Radius(g0) = 1.5
    c: PointOnObject(g0,g-3)
    c: Coincident(g1,g0)
    c: Coincident(g1,g0)
    c: Coincident(g2,g-4)
    c: Coincident(g2,g0)
    c: Tangent(g3,g2) = -1.5708
    c: Coincident(g3,g-5)
    c: Coincident(g4,g3)
    c: Coincident(g4,g2)
FEATURE [PartDesign::Pocket] Pocket362
  BaseFeature = -> Pad551
  Direction = (-1,0,0)
  Length = 8
  Length2 = 5
  Profile = -> Sketch805
  ReferenceAxis = -> Sketch805 [N_Axis]
  Refine = true
  Suppressed = false
  Type = 0
FEATURE [Sketcher::SketchObject] Sketch806
  ArcFitTolerance = 1e-06
  AttachmentSupport = -> [Pocket362]
  ExternalGeometry = -> [Pocket362]
  FullyConstrained = true
  MakeInternals = false
  MapMode = 5
  Placement = pos=(39.95,0,0) rot=(0.57735,0.57735,0.57735;2.0944rad)
  sketch-geometry (4):
    g0: ArcOfCircle CenterX=0.8 CenterY=6.94 CenterZ=0 NormalX=0 NormalY=0 NormalZ=1 AngleXU=0 Radius=4.44 StartAngle=3.47189 EndAngle=4.71239
    g1: ArcOfCircle CenterX=0.8 CenterY=5.5 CenterZ=0 NormalX=0 NormalY=0 NormalZ=1 AngleXU=0 Radius=3 StartAngle=3.14159 EndAngle=4.71239
    g2: LineSegment StartX=-3.4 StartY=5.5 StartZ=0 EndX=-2.2 EndY=5.5 EndZ=0
    g3: LineSegment [constr] StartX=0.8 StartY=5.5 StartZ=0 EndX=0.8 EndY=6.94 EndZ=0
  constraints (10):
    c: Coincident(g1,g0)
    c: Coincident(g2,g0)
    c: Horizontal(g2)
    c: Coincident(g0,g-3)
    c: DistanceX(g2,g2) = 1.2
    c: Tangent(g1,g-3) = -1.5708
    c: Coincident(g3,g1)
    c: Coincident(g3,g0)
    c: Vertical(g3)
    c: Coincident(g2,g1)
FEATURE [PartDesign::Pad] Pad552
  BaseFeature = -> Pocket362
  Direction = (1,0,0)
  Length = 1.5
  Length2 = 10
  Profile = -> Sketch806
  ReferenceAxis = -> Sketch806 [N_Axis]
  Refine = true
  Reversed = true
  Suppressed = false
  Type = 0
FEATURE [Sketcher::SketchObject] Sketch807
  ArcFitTolerance = 1e-06
  AttachmentSupport = -> [Pad552]
  ExternalGeometry = -> [Pad552]
  FullyConstrained = true
  MakeInternals = false
  MapMode = 5
  Placement = pos=(32.05,0,0) rot=(0.57735,-0.57735,-0.57735;2.0944rad)
  sketch-geometry (3):
    g0: ArcOfCircle CenterX=-0.8 CenterY=5.5 CenterZ=0 NormalX=0 NormalY=0 NormalZ=1 AngleXU=0 Radius=3 StartAngle=4.71239 EndAngle=6.28319
    g1: ArcOfCircle CenterX=-0.8 CenterY=6.94 CenterZ=0 NormalX=0 NormalY=0 NormalZ=1 AngleXU=0 Radius=4.44 StartAngle=4.71239 EndAngle=5.95289
    g2: LineSegment StartX=3.4 StartY=5.5 StartZ=0 EndX=2.2 EndY=5.5 EndZ=0
  constraints (6):
    c: Coincident(g0,g-4)
    c: Tangent(g0,g-3) = -1.5708
    c: Coincident(g1,g0)
    c: Tangent(g1,g-4) = -1.5708
    c: Coincident(g2,g1)
    c: Coincident(g2,g0)
FEATURE [PartDesign::Pad] Pad553
  BaseFeature = -> Pad552
  Direction = (-1,0,0)
  Length = 1.5
  Length2 = 10
  Profile = -> Sketch807
  ReferenceAxis = -> Sketch807 [N_Axis]
  Refine = true
  Reversed = true
  Suppressed = false
  Type = 0
FEATURE [PartDesign::Chamfer] Chamfer026
  Angle = 45
  Base = -> Pad553 [Edge41,Edge44,Edge70,Edge46,Edge28,Edge30,Edge33,Edge39,Edge35,Edge37]
  BaseFeature = -> Pad553
  ChamferType = 0
  FlipDirection = false
  Refine = true
  Size = 0.99
  Size2 = 1
  SupportTransform = false
  Suppressed = false
  UseAllEdges = false
FEATURE [PartDesign::Chamfer] Chamfer027
  Angle = 30
  Base = -> Chamfer026 [Edge114]
  BaseFeature = -> Chamfer026
  ChamferType = 2
  FlipDirection = false
  Refine = true
  Size = 1.99
  Size2 = 1
  SupportTransform = false
  Suppressed = false
  UseAllEdges = false
FEATURE [PartDesign::Chamfer] Chamfer028
  Angle = 20
  Base = -> Chamfer027 [Edge4]
  BaseFeature = -> Chamfer027
  ChamferType = 2
  FlipDirection = false
  Refine = true
  Size = 1.99
  Size2 = 1
  SupportTransform = false
  Suppressed = false
  UseAllEdges = false
FEATURE [PartDesign::Chamfer] Chamfer029
  Angle = 70
  Base = -> Chamfer028 [Edge24]
  BaseFeature = -> Chamfer028
  ChamferType = 2
  FlipDirection = false
  Refine = true
  Size = 0.72
  Size2 = 1
  SupportTransform = false
  Suppressed = false
  UseAllEdges = false
FEATURE [Sketcher::SketchObject] Sketch808
  ArcFitTolerance = 1e-06
  AttachmentSupport = -> [Chamfer029]
  ExternalGeometry = -> [Chamfer029]
  FullyConstrained = true
  MakeInternals = false
  MapMode = 5
  Placement = pos=(0,0.8,-2e-16) rot=(0,0.707107,0.707107;3.14159rad)
  sketch-geometry (3):
    g0: Circle CenterX=-36 CenterY=24.4 CenterZ=0 NormalX=0 NormalY=0 NormalZ=1 AngleXU=0 Radius=1
    g1: Circle CenterX=-36 CenterY=14.4 CenterZ=0 NormalX=0 NormalY=0 NormalZ=1 AngleXU=0 Radius=1
    g2: LineSegment [constr] StartX=-36 StartY=24.4 StartZ=0 EndX=-36 EndY=14.4 EndZ=0
  constraints (9):
    c: DistanceX(g-3,g-3) = 15.9
    c: DistanceX(g-3,g0) = 7.95
    c: Coincident(g2,g0)
    c: Coincident(g2,g1)
    c: Vertical(g2)
    c: DistanceY(g0,g-3) = 9.1
    c: DistanceY(g2,g2) = 10
    c: Radius(g0) = 1
    c: Radius(g1) = 1
FEATURE [PartDesign::Pocket] Pocket363
  BaseFeature = -> Chamfer029
  Direction = (0,-1,2e-16)
  Length = 5
  Length2 = 5
  Profile = -> Sketch808
  ReferenceAxis = -> Sketch808 [N_Axis]
  Refine = true
  Suppressed = false
  Type = 1
FEATURE [Sketcher::SketchObject] Sketch809
  ArcFitTolerance = 1e-06
  AttachmentSupport = -> [Pocket363]
  ExternalGeometry = -> [Pocket363]
  FullyConstrained = true
  MakeInternals = false
  MapMode = 5
  Placement = pos=(0,-6.7,2e-15) rot=(1,0,0;1.5708rad)
  sketch-geometry (2):
    g0: Circle CenterX=36 CenterY=14.4 CenterZ=0 NormalX=0 NormalY=0 NormalZ=1 AngleXU=0 Radius=2.25
    g1: Circle CenterX=36 CenterY=24.4 CenterZ=0 NormalX=0 NormalY=0 NormalZ=1 AngleXU=0 Radius=2.25
  constraints (4):
    c: Coincident(g0,g-4)
    c: Coincident(g1,g-3)
    c: Diameter(g1) = 4.5
    c: Diameter(g0) = 4.5
FEATURE [PartDesign::Pocket] Pocket364
  BaseFeature = -> Pocket363
  Direction = (0,1,-2e-16)
  Length = 6
  Length2 = 5
  Profile = -> Sketch809
  ReferenceAxis = -> Sketch809 [N_Axis]
  Refine = true
  Suppressed = false
  Type = 0
FEATURE [Sketcher::SketchObject] Sketch810
  ArcFitTolerance = 1e-06
  AttachmentSupport = -> [Pocket364]
  ExternalGeometry = -> [Pocket364]
  FullyConstrained = true
  MakeInternals = false
  MapMode = 5
  Placement = pos=(46,0,0) rot=(0.57735,0.57735,0.57735;2.0944rad)
  sketch-geometry (2):
    g0: ArcOfCircle CenterX=0.8 CenterY=24.4 CenterZ=0 NormalX=0 NormalY=0 NormalZ=1 AngleXU=0 Radius=1.85 StartAngle=1.5708 EndAngle=4.71239
    g1: LineSegment StartX=0.8 StartY=26.25 StartZ=0 EndX=0.8 EndY=22.55 EndZ=0
  constraints (7):
    c: PointOnObject(g0,g-3)
    c: Radius(g0) = 1.85
    c: PointOnObject(g0,g-3)
    c: DistanceY(g-3,g0) = 2
    c: Coincident(g1,g0)
    c: Coincident(g1,g0)
    c: Vertical(g1)
FEATURE [PartDesign::Pocket] Pocket365
  BaseFeature = -> Pocket364
  Direction = (-1,0,0)
  Length = 6.2
  Length2 = 5
  Profile = -> Sketch810
  ReferenceAxis = -> Sketch810 [N_Axis]
  Refine = true
  Suppressed = false
  Type = 0
FEATURE [Sketcher::SketchObject] Sketch811
  ArcFitTolerance = 1e-06
  AttachmentSupport = -> [Pocket365]
  ExternalGeometry = -> [Pocket365]
  FullyConstrained = true
  MakeInternals = false
  MapMode = 5
  Placement = pos=(39.8,0,0) rot=(0.57735,0.57735,0.57735;2.0944rad)
  sketch-geometry (2):
    g0: ArcOfCircle CenterX=0.8 CenterY=24.4 CenterZ=0 NormalX=0 NormalY=0 NormalZ=1 AngleXU=0 Radius=3.4 StartAngle=1.5708 EndAngle=4.71239
    g1: LineSegment StartX=0.8 StartY=27.8 StartZ=0 EndX=0.8 EndY=21 EndZ=0
  constraints (6):
    c: PointOnObject(g0,g-4)
    c: Radius(g0) = 3.4
    c: Coincident(g0,g-5)
    c: Coincident(g1,g0)
    c: Coincident(g1,g0)
    c: Vertical(g1)
FEATURE [PartDesign::Pocket] Pocket366
  BaseFeature = -> Pocket365
  Direction = (-1,0,0)
  Length = 3.1
  Length2 = 5
  Profile = -> Sketch811
  ReferenceAxis = -> Sketch811 [N_Axis]
  Refine = true
  Reversed = true
  Suppressed = false
  Type = 0
FEATURE [PartDesign::Pocket] Pocket367
  BaseFeature = -> Pocket366
  Direction = (-1,0,0)
  Length = 1.1
  Length2 = 5
  Profile = -> Pocket366 [Face59]
  Refine = true
  Suppressed = false
  Type = 0
FEATURE [Sketcher::SketchObject] Sketch812
  ArcFitTolerance = 1e-06
  AttachmentSupport = -> [Pocket367]
  ExternalGeometry = -> [Pocket367]
  FullyConstrained = true
  MakeInternals = false
  MapMode = 5
  Placement = pos=(26,0,0) rot=(0.57735,-0.57735,-0.57735;2.0944rad)
  sketch-geometry (16):
    g0: LineSegment StartX=-0.8 StartY=28.8 StartZ=0 EndX=-0.8 EndY=28.3 EndZ=0
    g1: LineSegment StartX=-0.8 StartY=28.3 StartZ=0 EndX=3.71 EndY=28.3 EndZ=0
    g2: LineSegment StartX=3.71 StartY=28.3 StartZ=0 EndX=3.71 EndY=28.8 EndZ=0
    g3: LineSegment StartX=3.71 StartY=28.8 StartZ=0 EndX=-0.8 EndY=28.8 EndZ=0
    g4: LineSegment StartX=-0.8 StartY=26 StartZ=0 EndX=3.71 EndY=26 EndZ=0
    g5: LineSegment StartX=3.71 StartY=26 StartZ=0 EndX=3.71 EndY=26.5 EndZ=0
    g6: LineSegment StartX=3.71 StartY=26.5 StartZ=0 EndX=-0.8 EndY=26.5 EndZ=0
    g7: LineSegment StartX=-0.8 StartY=26.5 StartZ=0 EndX=-0.8 EndY=26 EndZ=0
    g8: LineSegment StartX=-0.8 StartY=24.2 StartZ=0 EndX=-0.8 EndY=23.7 EndZ=0
    g9: LineSegment StartX=-0.8 StartY=23.7 StartZ=0 EndX=3.71 EndY=23.7 EndZ=0
    g10: LineSegment StartX=3.71 StartY=23.7 StartZ=0 EndX=3.71 EndY=24.2 EndZ=0
    g11: LineSegment StartX=3.71 StartY=24.2 StartZ=0 EndX=-0.8 EndY=24.2 EndZ=0
    g12: LineSegment StartX=-0.8 StartY=21.9 StartZ=0 EndX=-0.8 EndY=21.4 EndZ=0
    g13: LineSegment StartX=-0.8 StartY=21.4 StartZ=0 EndX=3.71 EndY=21.4 EndZ=0
    g14: LineSegment StartX=3.71 StartY=21.4 StartZ=0 EndX=3.71 EndY=21.9 EndZ=0
    g15: LineSegment StartX=3.71 StartY=21.9 StartZ=0 EndX=-0.8 EndY=21.9 EndZ=0
  constraints (48):
    c: Coincident(g0,g1)
    c: Coincident(g1,g2)
    c: Coincident(g2,g3)
    c: Coincident(g3,g0)
    c: Vertical(g0)
    c: Vertical(g2)
    c: Horizontal(g1)
    c: Horizontal(g3)
    c: PointOnObject(g0,g-4)
    c: PointOnObject(g1,g-3)
    c: DistanceY(g2,g2) = 0.5
    c: DistanceY(g2,g-3) = 2.65
    c: Coincident(g4,g5)
    c: Coincident(g5,g6)
    c: Coincident(g6,g7)
    c: Coincident(g7,g4)
    c: Horizontal(g4)
    c: Horizontal(g6)
    c: Vertical(g5)
    c: Vertical(g7)
    c: PointOnObject(g4,g-4)
    c: Coincident(g8,g9)
    c: Coincident(g9,g10)
    c: Coincident(g10,g11)
    c: Coincident(g11,g8)
    c: Vertical(g8)
    c: Vertical(g10)
    c: Horizontal(g9)
    c: Horizontal(g11)
    c: PointOnObject(g8,g-4)
    c: PointOnObject(g9,g-3)
    c: Coincident(g12,g13)
    c: Coincident(g13,g14)
    c: Coincident(g14,g15)
    c: Coincident(g15,g12)
    c: Vertical(g12)
    c: Vertical(g14)
    c: Horizontal(g13)
    c: Horizontal(g15)
    c: PointOnObject(g12,g-4)
    c: PointOnObject(g13,g-3)
    c: DistanceY(g12,g12) = 0.5
    c: DistanceY(g8,g8) = 0.5
    c: DistanceY(g7,g7) = 0.5
    c: DistanceY(g5,g1) = 1.8
    c: PointOnObject(g5,g-3)
    c: DistanceY(g10,g4) = 1.8
    c: DistanceY(g14,g9) = 1.8
FEATURE [PartDesign::Pocket] Pocket368
  BaseFeature = -> Pocket367
  Direction = (1,0,0)
  Length = 0.5
  Length2 = 5
  Profile = -> Sketch812
  ReferenceAxis = -> Sketch812 [N_Axis]
  Refine = true
  Suppressed = false
  Type = 0
FEATURE [PartDesign::Pocket] Pocket369
  BaseFeature = -> Pocket368
  Direction = (0,-1,0)
  Length = 5
  Length2 = 5
  Profile = -> Pocket368 [Face27,Face25,Face23,Face21]
  Refine = true
  Suppressed = false
  Type = 0
FEATURE [Sketcher::SketchObject] Sketch813
  ArcFitTolerance = 1e-06
  AttachmentSupport = -> [Pocket369]
  ExternalGeometry = -> [Pocket369]
  FullyConstrained = true
  MakeInternals = false
  MapMode = 5
  Placement = pos=(0,-4.7,1.1e-15) rot=(1,0,0;1.5708rad)
  sketch-geometry (42):
    g0: LineSegment StartX=26.99 StartY=28.8 StartZ=0 EndX=26.99 EndY=28.3 EndZ=0
    g1: LineSegment StartX=26.99 StartY=28.3 StartZ=0 EndX=28.5 EndY=28.3 EndZ=0
    g2: LineSegment StartX=28.5 StartY=28.3 StartZ=0 EndX=28.5 EndY=28.8 EndZ=0
    g3: LineSegment StartX=28.5 StartY=28.8 StartZ=0 EndX=26.99 EndY=28.8 EndZ=0
    g4: LineSegment StartX=26.99 StartY=26.5 StartZ=0 EndX=26.99 EndY=26 EndZ=0
    g5: LineSegment StartX=26.99 StartY=26 StartZ=0 EndX=28.5 EndY=26 EndZ=0
    g6: LineSegment StartX=28.5 StartY=26 StartZ=0 EndX=28.5 EndY=26.5 EndZ=0
    g7: LineSegment StartX=28.5 StartY=26.5 StartZ=0 EndX=26.99 EndY=26.5 EndZ=0
    g8: LineSegment StartX=26.99 StartY=24.2 StartZ=0 EndX=26.99 EndY=23.7 EndZ=0
    g9: LineSegment StartX=26.99 StartY=23.7 StartZ=0 EndX=28.5 EndY=23.7 EndZ=0
    g10: LineSegment StartX=28.5 StartY=23.7 StartZ=0 EndX=28.5 EndY=24.2 EndZ=0
    g11: LineSegment StartX=28.5 StartY=24.2 StartZ=0 EndX=26.99 EndY=24.2 EndZ=0
    g12: LineSegment [constr] StartX=26.99 StartY=21.4 StartZ=0 EndX=26.5 EndY=21.4 EndZ=0
    g13: LineSegment [constr] StartX=26.99 StartY=23.7 StartZ=0 EndX=26.5 EndY=23.7 EndZ=0
    g14: LineSegment [constr] StartX=26.99 StartY=28.8 StartZ=0 EndX=26.5 EndY=28.8 EndZ=0
    g15: LineSegment [constr] StartX=26.99 StartY=28.3 StartZ=0 EndX=26.5 EndY=28.3 EndZ=0
    g16: LineSegment [constr] StartX=26.99 StartY=26.5 StartZ=0 EndX=26.5 EndY=26.5 EndZ=0
    g17: LineSegment [constr] StartX=26.5 StartY=26 StartZ=0 EndX=26.99 EndY=26 EndZ=0
    g18: LineSegment [constr] StartX=26.99 StartY=24.2 StartZ=0 EndX=26.5 EndY=24.2 EndZ=0
    g19: LineSegment StartX=26.99 StartY=21.4 StartZ=0 EndX=45.01 EndY=21.4 EndZ=0
    g20: LineSegment StartX=28.5 StartY=21.5 StartZ=0 EndX=26.99 EndY=21.5 EndZ=0
    g21: LineSegment StartX=28.5 StartY=21.5 StartZ=0 EndX=45.01 EndY=21.5 EndZ=0
    g22: LineSegment StartX=45.01 StartY=21.5 StartZ=0 EndX=45.01 EndY=21.4 EndZ=0
    g23: LineSegment StartX=26.99 StartY=21.5 StartZ=0 EndX=26.99 EndY=21.4 EndZ=0
    g24: LineSegment StartX=45.01 StartY=28.8 StartZ=0 EndX=43.5 EndY=28.8 EndZ=0
    g25: LineSegment StartX=43.5 StartY=28.8 StartZ=0 EndX=43.5 EndY=28.3 EndZ=0
    g26: LineSegment StartX=43.5 StartY=28.3 StartZ=0 EndX=45.01 EndY=28.3 EndZ=0
    g27: LineSegment StartX=45.01 StartY=28.3 StartZ=0 EndX=45.01 EndY=28.8 EndZ=0
    g28: LineSegment StartX=45.01 StartY=26.5 StartZ=0 EndX=43.5 EndY=26.5 EndZ=0
    g29: LineSegment StartX=43.5 StartY=26.5 StartZ=0 EndX=43.5 EndY=26 EndZ=0
    g30: LineSegment StartX=43.5 StartY=26 StartZ=0 EndX=45.01 EndY=26 EndZ=0
    g31: LineSegment StartX=45.01 StartY=26 StartZ=0 EndX=45.01 EndY=26.5 EndZ=0
    g32: LineSegment StartX=45.01 StartY=24.2 StartZ=0 EndX=43.5 EndY=24.2 EndZ=0
    g33: LineSegment StartX=43.5 StartY=24.2 StartZ=0 EndX=43.5 EndY=23.7 EndZ=0
    g34: LineSegment StartX=43.5 StartY=23.7 StartZ=0 EndX=45.01 EndY=23.7 EndZ=0
    g35: LineSegment StartX=45.01 StartY=23.7 StartZ=0 EndX=45.01 EndY=24.2 EndZ=0
    g36: LineSegment [constr] StartX=28.5 StartY=24.2 StartZ=0 EndX=43.5 EndY=24.2 EndZ=0
    g37: LineSegment [constr] StartX=28.5 StartY=23.7 StartZ=0 EndX=43.5 EndY=23.7 EndZ=0
    g38: LineSegment [constr] StartX=28.5 StartY=26 StartZ=0 EndX=43.5 EndY=26 EndZ=0
    g39: LineSegment [constr] StartX=28.5 StartY=26.5 StartZ=0 EndX=43.5 EndY=26.5 EndZ=0
    g40: LineSegment [constr] StartX=43.5 StartY=28.3 StartZ=0 EndX=28.5 EndY=28.3 EndZ=0
    g41: LineSegment [constr] StartX=28.5 StartY=28.8 StartZ=0 EndX=43.5 EndY=28.8 EndZ=0
  constraints (112):
    c: Coincident(g0,g1)
    c: Coincident(g1,g2)
    c: Coincident(g2,g3)
    c: Coincident(g3,g0)
    c: Vertical(g0)
    c: Vertical(g2)
    c: Horizontal(g1)
    c: Horizontal(g3)
    c: PointOnObject(g0,g-3)
    c: PointOnObject(g1,g-4)
    c: Coincident(g4,g5)
    c: Coincident(g5,g6)
    c: Coincident(g6,g7)
    c: Coincident(g7,g4)
    c: Vertical(g4)
    c: Vertical(g6)
    c: Horizontal(g5)
    c: Horizontal(g7)
    c: PointOnObject(g4,g-3)
    c: PointOnObject(g5,g-4)
    c: Coincident(g8,g9)
    c: Coincident(g9,g10)
    c: Coincident(g10,g11)
    c: Coincident(g11,g8)
    c: Vertical(g8)
    c: Vertical(g10)
    c: Horizontal(g9)
    c: Horizontal(g11)
    c: PointOnObject(g8,g-3)
    c: PointOnObject(g9,g-4)
    c: PointOnObject(g12,g-3)
    c: Coincident(g12,g-8)
    c: Coincident(g13,g8)
    c: Coincident(g13,g-7)
    c: Coincident(g14,g0)
    c: Coincident(g14,g-5)
    c: Coincident(g15,g0)
    c: Coincident(g15,g-5)
    c: Coincident(g16,g4)
    c: Coincident(g16,g-10)
    c: Coincident(g17,g-10)
    c: Coincident(g17,g4)
    c: Coincident(g18,g8)
    c: Coincident(g18,g-9)
    c: Horizontal(g18)
    c: Horizontal(g13)
    c: Horizontal(g12)
    c: Horizontal(g17)
    c: Horizontal(g16)
    c: Horizontal(g15)
    c: Horizontal(g14)
    c: PointOnObject(g19,g-11)
    c: Horizontal(g19)
    c: Coincident(g19,g12)
    c: Coincident(g20,g-12)
    c: PointOnObject(g20,g-3)
    c: Horizontal(g20)
    c: Coincident(g21,g20)
    c: PointOnObject(g21,g-11)
    c: Horizontal(g21)
    c: Coincident(g22,g21)
    c: Coincident(g22,g19)
    c: Coincident(g23,g20)
    c: Coincident(g23,g12)
    c: Coincident(g24,g25)
    c: Coincident(g25,g26)
    c: Coincident(g26,g27)
    c: Coincident(g27,g24)
    c: Horizontal(g24)
    c: Horizontal(g26)
    c: Vertical(g25)
    c: Vertical(g27)
    c: PointOnObject(g24,g-11)
    c: PointOnObject(g25,g-13)
    c: Coincident(g28,g29)
    c: Coincident(g29,g30)
    c: Coincident(g30,g31)
    c: Coincident(g31,g28)
    c: Horizontal(g28)
    c: Horizontal(g30)
    c: Vertical(g29)
    c: Vertical(g31)
    c: PointOnObject(g28,g-11)
    c: PointOnObject(g29,g-13)
    c: Coincident(g32,g33)
    c: Coincident(g33,g34)
    c: Coincident(g34,g35)
    c: Coincident(g35,g32)
    c: Horizontal(g32)
    c: Horizontal(g34)
    c: Vertical(g33)
    c: Vertical(g35)
    c: PointOnObject(g32,g-11)
    c: PointOnObject(g33,g-13)
    c: Coincident(g36,g10)
    c: Coincident(g36,g32)
    c: Horizontal(g36)
    c: Coincident(g37,g9)
    c: Coincident(g37,g33)
    c: Horizontal(g37)
    c: Coincident(g38,g5)
    c: Coincident(g38,g29)
    c: Horizontal(g38)
    c: Coincident(g39,g6)
    c: Coincident(g39,g28)
    c: Horizontal(g39)
    c: Coincident(g40,g25)
    c: Coincident(g40,g1)
    c: Horizontal(g40)
    c: Coincident(g41,g2)
    c: Coincident(g41,g24)
    c: Horizontal(g41)
FEATURE [PartDesign::Pocket] Pocket370
  BaseFeature = -> Pocket369
  Direction = (0,1,-2e-16)
  Length = 0.5
  Length2 = 5
  Profile = -> Sketch813
  ReferenceAxis = -> Sketch813 [N_Axis]
  Refine = true
  Suppressed = false
  Type = 0
FEATURE [Sketcher::SketchObject] Sketch814
  ArcFitTolerance = 1e-06
  AttachmentSupport = -> [Pocket370]
  ExternalGeometry = -> [Pocket370]
  FullyConstrained = true
  MakeInternals = false
  MapMode = 5
  Placement = pos=(11.145,11.145,-2.8e-15) rot=(0.862856,-0.357407,-0.357407;1.71777rad)
  sketch-geometry (16):
    g0: LineSegment StartX=21.0081 StartY=28.8 StartZ=0 EndX=21.0081 EndY=28.3 EndZ=0
    g1: LineSegment StartX=21.0081 StartY=28.3 StartZ=0 EndX=22.4082 EndY=28.3 EndZ=0
    g2: LineSegment StartX=22.4082 StartY=28.3 StartZ=0 EndX=22.4082 EndY=28.8 EndZ=0
    g3: LineSegment StartX=22.4082 StartY=28.8 StartZ=0 EndX=21.0081 EndY=28.8 EndZ=0
    g4: LineSegment StartX=21.0081 StartY=26.5 StartZ=0 EndX=21.0081 EndY=26 EndZ=0
    g5: LineSegment StartX=21.0081 StartY=26 StartZ=0 EndX=22.4082 EndY=26 EndZ=0
    g6: LineSegment StartX=22.4082 StartY=26 StartZ=0 EndX=22.4082 EndY=26.5 EndZ=0
    g7: LineSegment StartX=22.4082 StartY=26.5 StartZ=0 EndX=21.0081 EndY=26.5 EndZ=0
    g8: LineSegment StartX=21.0081 StartY=24.2 StartZ=0 EndX=21.0081 EndY=23.7 EndZ=0
    g9: LineSegment StartX=21.0081 StartY=23.7 StartZ=0 EndX=22.4082 EndY=23.7 EndZ=0
    g10: LineSegment StartX=22.4082 StartY=23.7 StartZ=0 EndX=22.4082 EndY=24.2 EndZ=0
    g11: LineSegment StartX=22.4082 StartY=24.2 StartZ=0 EndX=21.0081 EndY=24.2 EndZ=0
    g12: LineSegment StartX=21.0081 StartY=21.9 StartZ=0 EndX=21.0081 EndY=21.4 EndZ=0
    g13: LineSegment StartX=21.0081 StartY=21.4 StartZ=0 EndX=22.4082 EndY=21.4 EndZ=0
    g14: LineSegment StartX=22.4082 StartY=21.4 StartZ=0 EndX=22.4082 EndY=21.9 EndZ=0
    g15: LineSegment StartX=22.4082 StartY=21.9 StartZ=0 EndX=21.0081 EndY=21.9 EndZ=0
  constraints (40):
    c: Coincident(g0,g1)
    c: Coincident(g1,g2)
    c: Coincident(g2,g3)
    c: Coincident(g3,g0)
    c: Vertical(g0)
    c: Vertical(g2)
    c: Horizontal(g1)
    c: Horizontal(g3)
    c: Coincident(g0,g-8)
    c: Coincident(g1,g-4)
    c: Coincident(g4,g5)
    c: Coincident(g5,g6)
    c: Coincident(g6,g7)
    c: Coincident(g7,g4)
    c: Vertical(g4)
    c: Vertical(g6)
    c: Horizontal(g5)
    c: Horizontal(g7)
    c: Coincident(g4,g-7)
    c: Coincident(g5,g-5)
    c: Coincident(g8,g9)
    c: Coincident(g9,g10)
    c: Coincident(g10,g11)
    c: Coincident(g11,g8)
    c: Vertical(g8)
    c: Vertical(g10)
    c: Horizontal(g9)
    c: Horizontal(g11)
    c: Coincident(g8,g-6)
    c: Coincident(g9,g-9)
    c: Coincident(g12,g13)
    c: Coincident(g13,g14)
    c: Coincident(g14,g15)
    c: Coincident(g15,g12)
    c: Vertical(g12)
    c: Vertical(g14)
    c: Horizontal(g13)
    c: Horizontal(g15)
    c: Coincident(g12,g-10)
    c: Coincident(g13,g-11)
FEATURE [PartDesign::Pocket] Pocket371
  BaseFeature = -> Pocket370
  Direction = (0.707107,0.707107,0)
  Length = 0.5
  Length2 = 5
  Profile = -> Sketch814
  ReferenceAxis = -> Sketch814 [N_Axis]
  Refine = true
  Suppressed = false
  Type = 0
FEATURE [Sketcher::SketchObject] Sketch815
  ArcFitTolerance = 1e-06
  AttachmentSupport = -> [Pocket371]
  ExternalGeometry = -> [Pocket371]
  FullyConstrained = true
  MakeInternals = false
  MapMode = 5
  Placement = pos=(0,-4.7,1.1e-15) rot=(1,0,0;1.5708rad)
  sketch-geometry (9):
    g0: LineSegment StartX=26.99 StartY=21.9 StartZ=0 EndX=26.99 EndY=21.5 EndZ=0
    g1: LineSegment StartX=26.99 StartY=21.5 StartZ=0 EndX=28.5 EndY=21.5 EndZ=0
    g2: LineSegment StartX=28.5 StartY=21.5 StartZ=0 EndX=28.5 EndY=21.9 EndZ=0
    g3: LineSegment StartX=28.5 StartY=21.9 StartZ=0 EndX=26.99 EndY=21.9 EndZ=0
    g4: LineSegment StartX=45.01 StartY=21.5 StartZ=0 EndX=45.01 EndY=21.9 EndZ=0
    g5: LineSegment StartX=45.01 StartY=21.9 StartZ=0 EndX=43.5 EndY=21.9 EndZ=0
    g6: LineSegment StartX=43.5 StartY=21.9 StartZ=0 EndX=43.5 EndY=21.5 EndZ=0
    g7: LineSegment StartX=43.5 StartY=21.5 StartZ=0 EndX=45.01 EndY=21.5 EndZ=0
    g8: LineSegment [constr] StartX=28.5 StartY=21.9 StartZ=0 EndX=43.5 EndY=21.9 EndZ=0
  constraints (23):
    c: Coincident(g0,g1)
    c: Coincident(g1,g2)
    c: Coincident(g2,g3)
    c: Coincident(g3,g0)
    c: Vertical(g0)
    c: Vertical(g2)
    c: Horizontal(g1)
    c: Horizontal(g3)
    c: Coincident(g0,g-3)
    c: Coincident(g1,g-4)
    c: Coincident(g4,g5)
    c: Coincident(g5,g6)
    c: Coincident(g6,g7)
    c: Coincident(g7,g4)
    c: Vertical(g4)
    c: Vertical(g6)
    c: Horizontal(g5)
    c: Horizontal(g7)
    c: Coincident(g4,g-5)
    c: PointOnObject(g5,g-6)
    c: Coincident(g8,g2)
    c: Coincident(g8,g5)
    c: Horizontal(g8)
FEATURE [PartDesign::Pocket] Pocket372
  BaseFeature = -> Pocket371
  Direction = (0,1,-2e-16)
  Length = 0.5
  Length2 = 5
  Profile = -> Sketch815
  ReferenceAxis = -> Sketch815 [N_Axis]
  Refine = true
  Suppressed = false
  Type = 0
FEATURE [Sketcher::SketchObject] Sketch816
  ArcFitTolerance = 1e-06
  AttachmentSupport = -> [Pocket372]
  ExternalGeometry = -> [Pocket372]
  FullyConstrained = true
  MakeInternals = false
  MapMode = 5
  Placement = pos=(24.855,-24.855,7e-15) rot=(0.862856,0.357407,0.357407;1.71777rad)
  sketch-geometry (16):
    g0: LineSegment StartX=28.5035 StartY=21.9 StartZ=0 EndX=28.5035 EndY=21.4 EndZ=0
    g1: LineSegment StartX=28.5035 StartY=21.4 StartZ=0 EndX=29.9035 EndY=21.4 EndZ=0
    g2: LineSegment StartX=29.9035 StartY=21.4 StartZ=0 EndX=29.9035 EndY=21.9 EndZ=0
    g3: LineSegment StartX=29.9035 StartY=21.9 StartZ=0 EndX=28.5035 EndY=21.9 EndZ=0
    g4: LineSegment StartX=28.5035 StartY=24.2 StartZ=0 EndX=28.5035 EndY=23.7 EndZ=0
    g5: LineSegment StartX=28.5035 StartY=23.7 StartZ=0 EndX=29.9035 EndY=23.7 EndZ=0
    g6: LineSegment StartX=29.9035 StartY=23.7 StartZ=0 EndX=29.9035 EndY=24.2 EndZ=0
    g7: LineSegment StartX=29.9035 StartY=24.2 StartZ=0 EndX=28.5035 EndY=24.2 EndZ=0
    g8: LineSegment StartX=28.5035 StartY=26.5 StartZ=0 EndX=29.9035 EndY=26.5 EndZ=0
    g9: LineSegment StartX=29.9035 StartY=26.5 StartZ=0 EndX=29.9035 EndY=26 EndZ=0
    g10: LineSegment StartX=29.9035 StartY=26 StartZ=0 EndX=28.5035 EndY=26 EndZ=0
    g11: LineSegment StartX=28.5035 StartY=26 StartZ=0 EndX=28.5035 EndY=26.5 EndZ=0
    g12: LineSegment StartX=28.5035 StartY=28.8 StartZ=0 EndX=28.5035 EndY=28.3 EndZ=0
    g13: LineSegment StartX=28.5035 StartY=28.3 StartZ=0 EndX=29.9035 EndY=28.3 EndZ=0
    g14: LineSegment StartX=29.9035 StartY=28.3 StartZ=0 EndX=29.9035 EndY=28.8 EndZ=0
    g15: LineSegment StartX=29.9035 StartY=28.8 StartZ=0 EndX=28.5035 EndY=28.8 EndZ=0
  constraints (40):
    c: Coincident(g0,g1)
    c: Coincident(g1,g2)
    c: Coincident(g2,g3)
    c: Coincident(g3,g0)
    c: Vertical(g2)
    c: Horizontal(g1)
    c: Horizontal(g3)
    c: Coincident(g0,g-7)
    c: PointOnObject(g1,g-6)
    c: Coincident(g4,g5)
    c: Coincident(g5,g6)
    c: Coincident(g6,g7)
    c: Coincident(g7,g4)
    c: Vertical(g6)
    c: Horizontal(g5)
    c: Horizontal(g7)
    c: Coincident(g4,g-5)
    c: PointOnObject(g5,g-6)
    c: Coincident(g8,g9)
    c: Coincident(g9,g10)
    c: Coincident(g10,g11)
    c: Coincident(g11,g8)
    c: Horizontal(g8)
    c: Horizontal(g10)
    c: Vertical(g9)
    c: Coincident(g8,g-4)
    c: PointOnObject(g9,g-6)
    c: Coincident(g12,g13)
    c: Coincident(g13,g14)
    c: Coincident(g14,g15)
    c: Coincident(g15,g12)
    c: Vertical(g14)
    c: Horizontal(g13)
    c: Horizontal(g15)
    c: Coincident(g12,g-3)
    c: PointOnObject(g13,g-6)
    c: Coincident(g12,g-3)
    c: Coincident(g10,g-4)
    c: Coincident(g4,g-5)
    c: Coincident(g0,g-7)
FEATURE [PartDesign::Pocket] Pocket373
  BaseFeature = -> Pocket372
  Direction = (-0.707107,0.707107,-2e-16)
  Length = 0.5
  Length2 = 5
  Profile = -> Sketch816
  ReferenceAxis = -> Sketch816 [N_Axis]
  Refine = true
  Suppressed = false
  Type = 0
FEATURE [Sketcher::SketchObject] Sketch817
  ArcFitTolerance = 1e-06
  AttachmentSupport = -> [Pocket373]
  ExternalGeometry = -> [Pocket373]
  FullyConstrained = true
  MakeInternals = false
  MapMode = 5
  Placement = pos=(46,0,0) rot=(0.57735,0.57735,0.57735;2.0944rad)
  sketch-geometry (16):
    g0: LineSegment StartX=-3.71 StartY=21.9 StartZ=0 EndX=-3.71 EndY=21.4 EndZ=0
    g1: LineSegment StartX=-3.71 StartY=21.4 StartZ=0 EndX=0.8 EndY=21.4 EndZ=0
    g2: LineSegment StartX=0.8 StartY=21.4 StartZ=0 EndX=0.8 EndY=21.9 EndZ=0
    g3: LineSegment StartX=0.8 StartY=21.9 StartZ=0 EndX=-3.71 EndY=21.9 EndZ=0
    g4: LineSegment StartX=-3.71 StartY=24.2 StartZ=0 EndX=-3.71 EndY=23.7 EndZ=0
    g5: LineSegment StartX=-3.71 StartY=23.7 StartZ=0 EndX=0.8 EndY=23.7 EndZ=0
    g6: LineSegment StartX=0.8 StartY=23.7 StartZ=0 EndX=0.8 EndY=24.2 EndZ=0
    g7: LineSegment StartX=0.8 StartY=24.2 StartZ=0 EndX=-3.71 EndY=24.2 EndZ=0
    g8: LineSegment StartX=-3.71 StartY=26.5 StartZ=0 EndX=-3.71 EndY=26 EndZ=0
    g9: LineSegment StartX=-3.71 StartY=26 StartZ=0 EndX=0.8 EndY=26 EndZ=0
    g10: LineSegment StartX=0.8 StartY=26 StartZ=0 EndX=0.8 EndY=26.5 EndZ=0
    g11: LineSegment StartX=0.8 StartY=26.5 StartZ=0 EndX=-3.71 EndY=26.5 EndZ=0
    g12: LineSegment StartX=-3.71 StartY=28.8 StartZ=0 EndX=-3.71 EndY=28.3 EndZ=0
    g13: LineSegment StartX=-3.71 StartY=28.3 StartZ=0 EndX=0.8 EndY=28.3 EndZ=0
    g14: LineSegment StartX=0.8 StartY=28.3 StartZ=0 EndX=0.8 EndY=28.8 EndZ=0
    g15: LineSegment StartX=0.8 StartY=28.8 StartZ=0 EndX=-3.71 EndY=28.8 EndZ=0
  constraints (40):
    c: Coincident(g0,g1)
    c: Coincident(g1,g2)
    c: Coincident(g2,g3)
    c: Coincident(g3,g0)
    c: Vertical(g2)
    c: Horizontal(g1)
    c: Horizontal(g3)
    c: Coincident(g0,g-6)
    c: PointOnObject(g1,g-9)
    c: Coincident(g4,g5)
    c: Coincident(g5,g6)
    c: Coincident(g6,g7)
    c: Coincident(g7,g4)
    c: Vertical(g6)
    c: Horizontal(g5)
    c: Horizontal(g7)
    c: Coincident(g4,g-5)
    c: PointOnObject(g6,g-10)
    c: Coincident(g4,g-5)
    c: Coincident(g0,g-6)
    c: Coincident(g8,g9)
    c: Coincident(g9,g10)
    c: Coincident(g10,g11)
    c: Coincident(g11,g8)
    c: Vertical(g10)
    c: Horizontal(g9)
    c: Horizontal(g11)
    c: Coincident(g8,g-4)
    c: PointOnObject(g9,g-10)
    c: Coincident(g12,g13)
    c: Coincident(g13,g14)
    c: Coincident(g14,g15)
    c: Coincident(g15,g12)
    c: Vertical(g14)
    c: Horizontal(g13)
    c: Horizontal(g15)
    c: Coincident(g12,g-3)
    c: PointOnObject(g13,g-8)
    c: Coincident(g12,g-3)
    c: Coincident(g8,g-4)
FEATURE [PartDesign::Pocket] Pocket374
  BaseFeature = -> Pocket373
  Direction = (-1,0,0)
  Length = 0.5
  Length2 = 5
  Profile = -> Sketch817
  ReferenceAxis = -> Sketch817 [N_Axis]
  Refine = true
  Suppressed = false
  Type = 0
FEATURE [Sketcher::SketchObject] Sketch818
  ArcFitTolerance = 1e-06
  AttachmentSupport = -> [Pocket374]
  ExternalGeometry = -> [Pocket374]
  FullyConstrained = true
  MakeInternals = false
  MapMode = 5
  Placement = pos=(45.5,0,0) rot=(0.57735,0.57735,0.57735;2.0944rad)
  sketch-geometry (4):
    g0: ArcOfCircle CenterX=0.800007 CenterY=24.4 CenterZ=0 NormalX=0 NormalY=0 NormalZ=1 AngleXU=0 Radius=1.85 StartAngle=1.5708 EndAngle=4.71239
    g1: ArcOfCircle CenterX=0.800007 CenterY=24.4 CenterZ=0 NormalX=0 NormalY=0 NormalZ=1 AngleXU=0 Radius=3.35 StartAngle=1.5708 EndAngle=4.71239
    g2: LineSegment StartX=0.8 StartY=26.25 StartZ=0 EndX=0.8 EndY=27.75 EndZ=0
    g3: LineSegment StartX=0.8 StartY=22.55 StartZ=0 EndX=0.8 EndY=21.05 EndZ=0
  constraints (11):
    c: Coincident(g0,g-7)
    c: Coincident(g0,g-4)
    c: Tangent(g0,g-3)
    c: PointOnObject(g1,g-5)
    c: PointOnObject(g1,g-9)
    c: Radius(g1) = 3.35
    c: Coincident(g1,g0)
    c: Coincident(g2,g0)
    c: Coincident(g2,g1)
    c: Coincident(g3,g0)
    c: Coincident(g3,g1)
FEATURE [PartDesign::Pad] Pad554
  BaseFeature = -> Pocket374
  Direction = (1,0,0)
  Length = 0.5
  Length2 = 10
  Profile = -> Sketch818
  ReferenceAxis = -> Sketch818 [N_Axis]
  Refine = true
  Suppressed = false
  Type = 0
FEATURE [Sketcher::SketchObject] Sketch819
  ArcFitTolerance = 1e-06
  AttachmentSupport = -> [Pad554]
  ExternalGeometry = -> [Pad554]
  FullyConstrained = true
  MakeInternals = false
  MapMode = 5
  Placement = pos=(0,-6.7,2e-15) rot=(1,0,0;1.5708rad)
  sketch-geometry (12):
    g0: LineSegment StartX=29.22 StartY=28.8 StartZ=0 EndX=29.22 EndY=28.3 EndZ=0
    g1: LineSegment StartX=29.22 StartY=28.3 StartZ=0 EndX=42.7757 EndY=28.3 EndZ=0
    g2: LineSegment StartX=42.7757 StartY=28.3 StartZ=0 EndX=42.7757 EndY=28.8 EndZ=0
    g3: LineSegment StartX=42.7757 StartY=28.8 StartZ=0 EndX=29.22 EndY=28.8 EndZ=0
    g4: LineSegment StartX=42.7757 StartY=26 StartZ=0 EndX=42.7757 EndY=26.5 EndZ=0
    g5: LineSegment StartX=42.7757 StartY=26.5 StartZ=0 EndX=29.22 EndY=26.5 EndZ=0
    g6: LineSegment StartX=29.22 StartY=26.5 StartZ=0 EndX=29.22 EndY=26 EndZ=0
    g7: LineSegment StartX=29.22 StartY=26 StartZ=0 EndX=42.7757 EndY=26 EndZ=0
    g8: LineSegment [constr] StartX=29.22 StartY=26.5 StartZ=0 EndX=28.5 EndY=26.5 EndZ=0
    g9: LineSegment [constr] StartX=29.22 StartY=26 StartZ=0 EndX=28.5 EndY=26 EndZ=0
    g10: LineSegment [constr] StartX=29.22 StartY=28.3 StartZ=0 EndX=28.5 EndY=28.3 EndZ=0
    g11: LineSegment [constr] StartX=29.22 StartY=28.8 StartZ=0 EndX=28.5 EndY=28.8 EndZ=0
  constraints (32):
    c: Coincident(g0,g1)
    c: Coincident(g1,g2)
    c: Coincident(g2,g3)
    c: Coincident(g3,g0)
    c: Vertical(g0)
    c: Vertical(g2)
    c: Horizontal(g1)
    c: Horizontal(g3)
    c: PointOnObject(g0,g-3)
    c: PointOnObject(g1,g-4)
    c: Coincident(g4,g5)
    c: Coincident(g5,g6)
    c: Coincident(g6,g7)
    c: Coincident(g7,g4)
    c: Vertical(g4)
    c: Vertical(g6)
    c: Horizontal(g5)
    c: Horizontal(g7)
    c: PointOnObject(g4,g-4)
    c: PointOnObject(g5,g-3)
    c: Coincident(g8,g5)
    c: Coincident(g8,g-7)
    c: Coincident(g9,g6)
    c: Coincident(g9,g-8)
    c: Coincident(g10,g0)
    c: Coincident(g10,g-6)
    c: Coincident(g11,g0)
    c: Coincident(g11,g-5)
    c: Horizontal(g11)
    c: Horizontal(g10)
    c: Horizontal(g8)
    c: Horizontal(g9)
FEATURE [PartDesign::Pocket] Pocket375
  BaseFeature = -> Pad554
  Direction = (0,1,-2e-16)
  Length = 0.5
  Length2 = 5
  Profile = -> Sketch819
  ReferenceAxis = -> Sketch819 [N_Axis]
  Refine = true
  Suppressed = false
  Type = 0
FEATURE [Sketcher::SketchObject] Sketch820
  ArcFitTolerance = 1e-06
  AttachmentSupport = -> [Pocket375]
  ExternalGeometry = -> [Pocket375]
  FullyConstrained = true
  MakeInternals = false
  MapMode = 5
  Placement = pos=(39.9252,-14.5316,5.5e-15) rot=(0.710565,0.497543,0.497543;1.90603rad)
  sketch-geometry (8):
    g0: LineSegment StartX=8.33421 StartY=28.8 StartZ=0 EndX=8.33421 EndY=28.3 EndZ=0
    g1: LineSegment StartX=8.33421 StartY=28.3 StartZ=0 EndX=10.4519 EndY=28.3 EndZ=0
    g2: LineSegment StartX=10.4519 StartY=28.3 StartZ=0 EndX=10.4519 EndY=28.8 EndZ=0
    g3: LineSegment StartX=10.4519 StartY=28.8 StartZ=0 EndX=8.33421 EndY=28.8 EndZ=0
    g4: LineSegment StartX=8.33421 StartY=26.5 StartZ=0 EndX=8.33421 EndY=26 EndZ=0
    g5: LineSegment StartX=8.33421 StartY=26 StartZ=0 EndX=10.4519 EndY=26 EndZ=0
    g6: LineSegment StartX=10.4519 StartY=26 StartZ=0 EndX=10.4519 EndY=26.5 EndZ=0
    g7: LineSegment StartX=10.4519 StartY=26.5 StartZ=0 EndX=8.33421 EndY=26.5 EndZ=0
  constraints (20):
    c: Coincident(g0,g1)
    c: Coincident(g1,g2)
    c: Coincident(g2,g3)
    c: Coincident(g3,g0)
    c: Vertical(g2)
    c: Horizontal(g1)
    c: Horizontal(g3)
    c: Coincident(g0,g-4)
    c: PointOnObject(g1,g-5)
    c: Coincident(g4,g5)
    c: Coincident(g5,g6)
    c: Coincident(g6,g7)
    c: Coincident(g7,g4)
    c: Vertical(g6)
    c: Horizontal(g5)
    c: Horizontal(g7)
    c: Coincident(g4,g-3)
    c: PointOnObject(g5,g-5)
    c: Coincident(g4,g-6)
    c: Coincident(g0,g-4)
FEATURE [PartDesign::Pocket] Pocket376
  BaseFeature = -> Pocket375
  Direction = (-0.939693,0.34202,3e-16)
  Length = 0.5
  Length2 = 5
  Profile = -> Sketch820
  ReferenceAxis = -> Sketch820 [N_Axis]
  Refine = true
  Suppressed = false
  Type = 0
FEATURE [PartDesign::Pocket] Pocket377
  BaseFeature = -> Pocket376
  Direction = (0.34202,0.939693,2e-16)
  Length = 0.5
  Length2 = 5
  Profile = -> Pocket376 [Face64,Face62]
  Refine = true
  Suppressed = false
  Type = 0
FEATURE [Sketcher::SketchObject] Sketch821
  ArcFitTolerance = 1e-06
  AttachmentSupport = -> [Pocket377]
  ExternalGeometry = -> [Pocket377]
  FullyConstrained = true
  MakeInternals = false
  MapMode = 5
  Placement = pos=(23.6486,8.60738,-3.3e-15) rot=(0.710565,-0.497543,-0.497543;1.90603rad)
  sketch-geometry (8):
    g0: LineSegment StartX=16.2898 StartY=28.8 StartZ=0 EndX=14.1846 EndY=28.8 EndZ=0
    g1: LineSegment StartX=14.1846 StartY=28.8 StartZ=0 EndX=14.1846 EndY=28.3 EndZ=0
    g2: LineSegment StartX=14.1846 StartY=28.3 StartZ=0 EndX=16.2898 EndY=28.3 EndZ=0
    g3: LineSegment StartX=16.2898 StartY=28.3 StartZ=0 EndX=16.2898 EndY=28.8 EndZ=0
    g4: LineSegment StartX=16.2898 StartY=26.5 StartZ=0 EndX=14.1846 EndY=26.5 EndZ=0
    g5: LineSegment StartX=14.1846 StartY=26.5 StartZ=0 EndX=14.1846 EndY=26 EndZ=0
    g6: LineSegment StartX=14.1846 StartY=26 StartZ=0 EndX=16.2898 EndY=26 EndZ=0
    g7: LineSegment StartX=16.2898 StartY=26 StartZ=0 EndX=16.2898 EndY=26.5 EndZ=0
  constraints (20):
    c: Coincident(g0,g1)
    c: Coincident(g1,g2)
    c: Coincident(g2,g3)
    c: Coincident(g3,g0)
    c: Horizontal(g0)
    c: Horizontal(g2)
    c: Vertical(g1)
    c: Coincident(g0,g-3)
    c: PointOnObject(g1,g-5)
    c: Coincident(g4,g5)
    c: Coincident(g5,g6)
    c: Coincident(g6,g7)
    c: Coincident(g7,g4)
    c: Horizontal(g4)
    c: Horizontal(g6)
    c: Vertical(g5)
    c: Coincident(g4,g-4)
    c: PointOnObject(g5,g-5)
    c: Coincident(g6,g-4)
    c: Coincident(g2,g-3)
FEATURE [PartDesign::Pocket] Pocket378
  BaseFeature = -> Pocket377
  Direction = (0.939693,0.34202,0)
  Length = 0.5
  Length2 = 5
  Profile = -> Sketch821
  ReferenceAxis = -> Sketch821 [N_Axis]
  Refine = true
  Suppressed = false
  Type = 0
FEATURE [PartDesign::Pocket] Pocket379
  BaseFeature = -> Pocket378
  Direction = (-0.34202,0.939693,1e-16)
  Length = 0.5
  Length2 = 5
  Profile = -> Pocket378 [Face115,Face113]
  Refine = true
  Suppressed = false
  Type = 0
FEATURE [PartDesign::Body] Body042  label="Rear_Head"
  AllowCompound = false
  Group = -> [Binder006,Sketch801,Pad548,Sketch802,Pad549,Sketch803,Pad550,Sketch804,Pad551,Sketch805,Pocket362,Sketch806,Pad552,Sketch807,Pad553,Chamfer026,Chamfer027,Chamfer028,Chamfer029,Sketch808,Pocket363,Sketch809,Pocket364,Sketch810,Pocket365,Sketch811,Pocket366,Pocket367,Sketch812,Pocket368,Pocket369,Sketch813,Pocket370,Sketch814,Pocket371,Sketch815,Pocket372,Sketch816,Pocket373,Sketch817,Pocket374,+10 more]
  Origin = -> Origin045
  Tip = -> Pocket379
FEATURE [App::Part] Part001  label="Head"
  Group = -> [Body036,Body037,Body038,Body039,Body040,Body041,Body042]
  Origin = -> Origin038
  Placement = pos=(-199,59,-19) rot=(0.57735,-0.57735,-0.57735;2.0944rad)
FEATURE [Sketcher::SketchObject] Sketch822
  ArcFitTolerance = 1e-06
  AttachmentSupport = -> [XY_Plane046]
  FullyConstrained = true
  MakeInternals = false
  MapMode = 5
  sketch-geometry (8):
    g0: LineSegment StartX=0 StartY=0 StartZ=0 EndX=0 EndY=21.7 EndZ=0
    g1: LineSegment StartX=0 StartY=21.7 StartZ=0 EndX=26 EndY=21.7 EndZ=0
    g2: LineSegment StartX=0 StartY=0 StartZ=0 EndX=26 EndY=0 EndZ=0
    g3: LineSegment StartX=26 StartY=0 StartZ=0 EndX=26 EndY=2.9 EndZ=0
    g4: LineSegment StartX=26 StartY=2.9 StartZ=0 EndX=31.6 EndY=2.9 EndZ=0
    g5: LineSegment StartX=31.6 StartY=2.9 StartZ=0 EndX=31.6 EndY=18.8 EndZ=0
    g6: LineSegment StartX=31.6 StartY=18.8 StartZ=0 EndX=26 EndY=18.8 EndZ=0
    g7: LineSegment StartX=26 StartY=21.7 StartZ=0 EndX=26 EndY=18.8 EndZ=0
  constraints (23):
    c: Coincident(g0,g-1)
    c: PointOnObject(g0,g-2)
    c: DistanceY(g0,g0) = 21.7
    c: Coincident(g1,g0)
    c: Horizontal(g1)
    c: Coincident(g2,g0)
    c: PointOnObject(g2,g-1)
    c: DistanceX(g1,g1) = 26
    c: DistanceX(g2,g2) = 26
    c: Coincident(g3,g2)
    c: Vertical(g3)
    c: Coincident(g4,g3)
    c: Horizontal(g4)
    c: Coincident(g5,g4)
    c: Vertical(g5)
    c: Coincident(g6,g5)
    c: Horizontal(g6)
    c: Coincident(g7,g1)
    c: Coincident(g7,g6)
    c: Vertical(g7)
    c: DistanceY(g5,g5) = 15.9
    c: DistanceX(g4,g4) = 5.6
    c: DistanceY(g3,g3) = 2.9
FEATURE [PartDesign::Pad] Pad555
  Direction = (0,0,1)
  Length = 6
  Length2 = 10
  Profile = -> Sketch822
  ReferenceAxis = -> Sketch822 [N_Axis]
  Refine = true
  Suppressed = false
  Type = 0
FEATURE [Sketcher::SketchObject] Sketch823
  ArcFitTolerance = 1e-06
  AttachmentSupport = -> [Pad555]
  ExternalGeometry = -> [Pad555]
  FullyConstrained = true
  MakeInternals = false
  MapMode = 5
  Placement = pos=(0,0,6) rot=(0,0,1;0rad)
  sketch-geometry (4):
    g0: LineSegment StartX=0 StartY=21.7 StartZ=0 EndX=0 EndY=0 EndZ=0
    g1: LineSegment StartX=0 StartY=0 StartZ=0 EndX=26 EndY=0 EndZ=0
    g2: LineSegment StartX=26 StartY=0 StartZ=0 EndX=26 EndY=21.7 EndZ=0
    g3: LineSegment StartX=26 StartY=21.7 StartZ=0 EndX=0 EndY=21.7 EndZ=0
  constraints (10):
    c: Coincident(g0,g1)
    c: Coincident(g1,g2)
    c: Coincident(g2,g3)
    c: Coincident(g3,g0)
    c: Vertical(g0)
    c: Vertical(g2)
    c: Horizontal(g1)
    c: Horizontal(g3)
    c: Coincident(g0,g-3)
    c: Coincident(g1,g-4)
FEATURE [PartDesign::Pad] Pad556
  BaseFeature = -> Pad555
  Direction = (0,0,1)
  Length = 1
  Length2 = 10
  Profile = -> Sketch823
  ReferenceAxis = -> Sketch823 [N_Axis]
  Refine = true
  Suppressed = false
  Type = 0
FEATURE [Sketcher::SketchObject] Sketch824
  ArcFitTolerance = 1e-06
  AttachmentSupport = -> [Pad556]
  ExternalGeometry = -> [Pad556]
  FullyConstrained = true
  MakeInternals = false
  MapMode = 5
  Placement = pos=(0,0,0) rot=(1,0,0;3.14159rad)
  sketch-geometry (8):
    g0: LineSegment StartX=1.5 StartY=-2 StartZ=0 EndX=24.5 EndY=-2 EndZ=0
    g1: LineSegment StartX=24.5 StartY=-2 StartZ=0 EndX=24.5 EndY=-4.4 EndZ=0
    g2: LineSegment StartX=24.5 StartY=-4.4 StartZ=0 EndX=30.1 EndY=-4.4 EndZ=0
    g3: LineSegment StartX=30.1 StartY=-4.4 StartZ=0 EndX=30.1 EndY=-17.3 EndZ=0
    g4: LineSegment StartX=30.1 StartY=-17.3 StartZ=0 EndX=24.5 EndY=-17.3 EndZ=0
    g5: LineSegment StartX=24.5 StartY=-17.3 StartZ=0 EndX=24.5 EndY=-19.7 EndZ=0
    g6: LineSegment StartX=24.5 StartY=-19.7 StartZ=0 EndX=1.5 EndY=-19.7 EndZ=0
    g7: LineSegment StartX=1.5 StartY=-19.7 StartZ=0 EndX=1.5 EndY=-2 EndZ=0
  constraints (24):
    c: Horizontal(g0)
    c: Coincident(g1,g0)
    c: Vertical(g1)
    c: Coincident(g2,g1)
    c: Horizontal(g2)
    c: Coincident(g3,g2)
    c: Vertical(g3)
    c: Coincident(g4,g3)
    c: Horizontal(g4)
    c: Coincident(g5,g4)
    c: Vertical(g5)
    c: Coincident(g6,g5)
    c: Horizontal(g6)
    c: Coincident(g7,g6)
    c: Coincident(g7,g0)
    c: Vertical(g7)
    c: DistanceX(g-1,g0) = 1.5
    c: DistanceX(g2,g-5) = 1.5
    c: DistanceX(g0,g-5) = 1.5
    c: DistanceX(g4,g-6) = 1.5
    c: DistanceY(g-4,g5) = 2
    c: DistanceY(g0,g-3) = 2
    c: DistanceY(g1,g-5) = 1.5
    c: DistanceY(g-6,g4) = 1.5
FEATURE [PartDesign::Pocket] Pocket380
  BaseFeature = -> Pad556
  Direction = (0,0,1)
  Length = 4.5
  Length2 = 5
  Profile = -> Sketch824
  ReferenceAxis = -> Sketch824 [N_Axis]
  Refine = true
  Suppressed = false
  Type = 0
FEATURE [Sketcher::SketchObject] Sketch825
  ArcFitTolerance = 1e-06
  AttachmentSupport = -> [Pocket380]
  ExternalGeometry = -> [Pocket380]
  FullyConstrained = true
  MakeInternals = false
  MapMode = 5
  Placement = pos=(0,0,4.5) rot=(1,0,0;3.14159rad)
  sketch-geometry (4):
    g0: LineSegment StartX=1.5 StartY=-2 StartZ=0 EndX=1.5 EndY=-19.7 EndZ=0
    g1: LineSegment StartX=1.5 StartY=-19.7 StartZ=0 EndX=24.5 EndY=-19.7 EndZ=0
    g2: LineSegment StartX=24.5 StartY=-19.7 StartZ=0 EndX=24.5 EndY=-2 EndZ=0
    g3: LineSegment StartX=24.5 StartY=-2 StartZ=0 EndX=1.5 EndY=-2 EndZ=0
  constraints (10):
    c: Coincident(g0,g1)
    c: Coincident(g1,g2)
    c: Coincident(g2,g3)
    c: Coincident(g3,g0)
    c: Vertical(g0)
    c: Vertical(g2)
    c: Horizontal(g1)
    c: Horizontal(g3)
    c: Coincident(g0,g-3)
    c: Coincident(g1,g-4)
FEATURE [PartDesign::Pocket] Pocket381
  BaseFeature = -> Pocket380
  Direction = (0,0,1)
  Length = 1
  Length2 = 5
  Profile = -> Sketch825
  ReferenceAxis = -> Sketch825 [N_Axis]
  Refine = true
  Suppressed = false
  Type = 0
FEATURE [PartDesign::Chamfer] Chamfer030
  Angle = 45
  Base = -> Pocket381 [Edge4,Edge41,Edge43,Edge45,Edge2,Edge1]
  BaseFeature = -> Pocket381
  ChamferType = 0
  FlipDirection = false
  Refine = true
  Size = 0.5
  Size2 = 1
  SupportTransform = false
  Suppressed = false
  UseAllEdges = false
FEATURE [PartDesign::Chamfer] Chamfer031
  Angle = 45
  Base = -> Chamfer030 [Edge1]
  BaseFeature = -> Chamfer030
  ChamferType = 0
  FlipDirection = false
  Refine = true
  Size = 0.999
  Size2 = 1
  SupportTransform = false
  Suppressed = false
  UseAllEdges = false
FEATURE [Sketcher::SketchObject] Sketch826
  ArcFitTolerance = 1e-06
  AttachmentSupport = -> [Chamfer031]
  ExternalGeometry = -> [Chamfer031]
  FullyConstrained = true
  MakeInternals = false
  MapMode = 5
  Placement = pos=(0,0,0) rot=(1,0,0;3.14159rad)
  sketch-geometry (7):
    g0: LineSegment StartX=31.6 StartY=-6.4 StartZ=0 EndX=31.6 EndY=-15.3 EndZ=0
    g1: LineSegment StartX=31.6 StartY=-15.3 StartZ=0 EndX=39.05 EndY=-15.3 EndZ=0
    g2: LineSegment StartX=31.6 StartY=-6.4 StartZ=0 EndX=39.05 EndY=-6.4 EndZ=0
    g3: ArcOfCircle CenterX=39.05 CenterY=-10.85 CenterZ=0 NormalX=0 NormalY=0 NormalZ=1 AngleXU=0 Radius=4.45 StartAngle=4.71239 EndAngle=7.85398
    g4: LineSegment [constr] StartX=39.05 StartY=-6.4 StartZ=0 EndX=39.05 EndY=-10.85 EndZ=0
    g5: LineSegment [constr] StartX=39.05 StartY=-10.85 StartZ=0 EndX=39.05 EndY=-15.3 EndZ=0
    g6: LineSegment [constr] StartX=39.05 StartY=-10.85 StartZ=0 EndX=43.5 EndY=-10.85 EndZ=0
  constraints (21):
    c: PointOnObject(g0,g-3)
    c: PointOnObject(g0,g-3)
    c: Coincident(g1,g0)
    c: Horizontal(g1)
    c: Coincident(g2,g0)
    c: Horizontal(g2)
    c: Coincident(g3,g2)
    c: Coincident(g3,g1)
    c: Coincident(g4,g2)
    c: Coincident(g4,g3)
    c: Coincident(g5,g3)
    c: Coincident(g5,g1)
    c: Vertical(g4)
    c: Vertical(g5)
    c: Diameter(g3) = 8.9
    c: DistanceY(g-3,g-3) = 15.9
    c: DistanceY(g0,g-3) = 3.5
    c: Coincident(g6,g3)
    c: PointOnObject(g6,g3)
    c: Horizontal(g6)
    c: DistanceX(g0,g6) = 11.9
FEATURE [PartDesign::Pad] Pad557
  BaseFeature = -> Chamfer031
  Direction = (0,0,-1)
  Length = 1.8
  Length2 = 10
  Profile = -> Sketch826
  ReferenceAxis = -> Sketch826 [N_Axis]
  Refine = true
  Reversed = true
  Suppressed = false
  Type = 0
FEATURE [Sketcher::SketchObject] Sketch827
  ArcFitTolerance = 1e-06
  AttachmentSupport = -> [Pad557]
  ExternalGeometry = -> [Pad557]
  FullyConstrained = true
  MakeInternals = false
  MapMode = 5
  Placement = pos=(0,6.4,0) rot=(1,0,0;1.5708rad)
  sketch-geometry (3):
    g0: LineSegment StartX=31.6 StartY=1.8 StartZ=0 EndX=33.6 EndY=1.8 EndZ=0
    g1: LineSegment StartX=33.6 StartY=1.8 StartZ=0 EndX=31.6 EndY=3.8 EndZ=0
    g2: LineSegment StartX=31.6 StartY=3.8 StartZ=0 EndX=31.6 EndY=1.8 EndZ=0
  constraints (8):
    c: Coincident(g0,g-4)
    c: PointOnObject(g0,g-4)
    c: Coincident(g1,g0)
    c: PointOnObject(g1,g-3)
    c: Coincident(g2,g1)
    c: Coincident(g2,g0)
    c: DistanceX(g0,g0) = 2
    c: Angle(g1,g0) = 0.785398
FEATURE [PartDesign::Pad] Pad558
  BaseFeature = -> Pad557
  Direction = (0,-1,2e-16)
  Length = 1.5
  Length2 = 10
  Profile = -> Sketch827
  ReferenceAxis = -> Sketch827 [N_Axis]
  Refine = true
  Reversed = true
  Suppressed = false
  Type = 0
FEATURE [Sketcher::SketchObject] Sketch828
  ArcFitTolerance = 1e-06
  AttachmentSupport = -> [Pad558]
  ExternalGeometry = -> [Pad558]
  FullyConstrained = true
  MakeInternals = false
  MapMode = 5
  Placement = pos=(0,15.3,0) rot=(0,0.707107,0.707107;3.14159rad)
  sketch-geometry (3):
    g0: LineSegment StartX=-33.6 StartY=1.8 StartZ=0 EndX=-31.6 EndY=3.8 EndZ=0
    g1: LineSegment StartX=-31.6 StartY=3.8 StartZ=0 EndX=-31.6 EndY=1.8 EndZ=0
    g2: LineSegment StartX=-31.6 StartY=1.8 StartZ=0 EndX=-33.6 EndY=1.8 EndZ=0
  constraints (6):
    c: Coincident(g0,g-5)
    c: Coincident(g0,g-5)
    c: Coincident(g1,g0)
    c: Coincident(g1,g-4)
    c: Coincident(g2,g1)
    c: Coincident(g2,g0)
FEATURE [PartDesign::Pad] Pad559
  BaseFeature = -> Pad558
  Direction = (0,1,-2e-16)
  Length = 1.5
  Length2 = 10
  Profile = -> Sketch828
  ReferenceAxis = -> Sketch828 [N_Axis]
  Refine = true
  Reversed = true
  Suppressed = false
  Type = 0
FEATURE [Sketcher::SketchObject] Sketch829
  ArcFitTolerance = 1e-06
  AttachmentSupport = -> [Pad559]
  ExternalGeometry = -> [Pad559]
  FullyConstrained = true
  MakeInternals = false
  MapMode = 5
  Placement = pos=(0,0,1.8) rot=(0,0,1;0rad)
  sketch-geometry (4):
    g0: LineSegment StartX=31.6 StartY=13.8 StartZ=0 EndX=31.6 EndY=7.9 EndZ=0
    g1: LineSegment StartX=31.6 StartY=7.9 StartZ=0 EndX=33.6 EndY=7.9 EndZ=0
    g2: LineSegment StartX=33.6 StartY=7.9 StartZ=0 EndX=33.6 EndY=13.8 EndZ=0
    g3: LineSegment StartX=33.6 StartY=13.8 StartZ=0 EndX=31.6 EndY=13.8 EndZ=0
  constraints (10):
    c: Coincident(g0,g1)
    c: Coincident(g1,g2)
    c: Coincident(g2,g3)
    c: Coincident(g3,g0)
    c: Vertical(g0)
    c: Vertical(g2)
    c: Horizontal(g1)
    c: Horizontal(g3)
    c: Coincident(g0,g-3)
    c: Coincident(g1,g-4)
FEATURE [PartDesign::Pocket] Pocket382
  BaseFeature = -> Pad559
  Direction = (0,0,-1)
  Length = 5
  Length2 = 5
  Profile = -> Sketch829
  ReferenceAxis = -> Sketch829 [N_Axis]
  Refine = true
  Suppressed = false
  Type = 0
FEATURE [Sketcher::SketchObject] Sketch830
  ArcFitTolerance = 1e-06
  AttachmentOffset = pos=(0,0,-1.5) rot=(0,0,1;0rad)
  AttachmentSupport = -> [Pocket382]
  ExternalGeometry = -> [Pocket382]
  FullyConstrained = true
  MakeInternals = false
  MapMode = 5
  Placement = pos=(31.6,0,0) rot=(0.57735,-0.57735,-0.57735;2.0944rad)
  sketch-geometry (8):
    g0: LineSegment StartX=-15.3 StartY=0 StartZ=0 EndX=-15.3 EndY=-3 EndZ=0
    g1: LineSegment StartX=-15.3 StartY=-3 StartZ=0 EndX=-6.4 EndY=-3 EndZ=0
    g2: LineSegment StartX=-6.4 StartY=-3 StartZ=0 EndX=-6.4 EndY=0 EndZ=0
    g3: LineSegment StartX=-15.3 StartY=0 StartZ=0 EndX=-13.8 EndY=0 EndZ=0
    g4: LineSegment StartX=-13.8 StartY=0 StartZ=0 EndX=-13.8 EndY=-1.5 EndZ=0
    g5: LineSegment StartX=-13.8 StartY=-1.5 StartZ=0 EndX=-7.9 EndY=-1.5 EndZ=0
    g6: LineSegment StartX=-7.9 StartY=-1.5 StartZ=0 EndX=-7.9 EndY=0 EndZ=0
    g7: LineSegment StartX=-6.4 StartY=0 StartZ=0 EndX=-7.9 EndY=0 EndZ=0
  constraints (22):
    c: Coincident(g0,g-3)
    c: Vertical(g0)
    c: Coincident(g1,g0)
    c: Horizontal(g1)
    c: Coincident(g2,g1)
    c: Coincident(g2,g-4)
    c: Vertical(g2)
    c: Coincident(g3,g0)
    c: PointOnObject(g3,g-1)
    c: Coincident(g4,g3)
    c: Vertical(g4)
    c: Coincident(g5,g4)
    c: Horizontal(g5)
    c: Coincident(g6,g5)
    c: PointOnObject(g6,g-1)
    c: Vertical(g6)
    c: Coincident(g7,g2)
    c: Coincident(g7,g6)
    c: DistanceY(g0,g0) = 3
    c: DistanceY(g0,g4) = 1.5
    c: DistanceX(g3,g3) = 1.5
    c: DistanceX(g7,g7) = 1.5
FEATURE [PartDesign::Pad] Pad560
  BaseFeature = -> Pocket382
  Direction = (-1,0,0)
  Length = 3
  Length2 = 10
  Profile = -> Sketch830
  ReferenceAxis = -> Sketch830 [N_Axis]
  Refine = true
  Reversed = true
  Suppressed = false
  Type = 0
FEATURE [Sketcher::SketchObject] Sketch831
  ArcFitTolerance = 1e-06
  AttachmentSupport = -> [Pad560]
  ExternalGeometry = -> [Pad560]
  FullyConstrained = true
  MakeInternals = false
  MapMode = 5
  Placement = pos=(0,0,0) rot=(1,0,0;3.14159rad)
  sketch-geometry (1):
    g0: Circle CenterX=39.05 CenterY=-10.85 CenterZ=0 NormalX=0 NormalY=0 NormalZ=1 AngleXU=0 Radius=3.7
  constraints (2):
    c: Coincident(g0,g-3)
    c: Diameter(g0) = 7.4
FEATURE [PartDesign::Pad] Pad561
  BaseFeature = -> Pad560
  Direction = (0,0,-1)
  Length = 4.5
  Length2 = 10
  Profile = -> Sketch831
  ReferenceAxis = -> Sketch831 [N_Axis]
  Refine = true
  Suppressed = false
  Type = 0
FEATURE [Sketcher::SketchObject] Sketch832
  ArcFitTolerance = 1e-06
  AttachmentSupport = -> [Pad561]
  ExternalGeometry = -> [Pad561]
  FullyConstrained = true
  MakeInternals = false
  MapMode = 5
  Placement = pos=(0,0,1.8) rot=(0,0,1;0rad)
  sketch-geometry (1):
    g0: Circle CenterX=39.05 CenterY=10.85 CenterZ=0 NormalX=0 NormalY=0 NormalZ=1 AngleXU=0 Radius=2.75
  constraints (2):
    c: Coincident(g0,g-3)
    c: Radius(g0) = 2.75
FEATURE [PartDesign::Pocket] Pocket383
  BaseFeature = -> Pad561
  Direction = (0,0,-1)
  Length = 5
  Length2 = 5
  Profile = -> Sketch832
  ReferenceAxis = -> Sketch832 [N_Axis]
  Refine = true
  Suppressed = false
  Type = 0
FEATURE [Sketcher::SketchObject] Sketch833
  ArcFitTolerance = 1e-06
  AttachmentSupport = -> [Pocket383]
  ExternalGeometry = -> [Pocket383]
  FullyConstrained = true
  MakeInternals = false
  MapMode = 5
  Placement = pos=(0,0,0) rot=(0.57735,-0.57735,-0.57735;2.0944rad)
  sketch-geometry (2):
    g0: ArcOfCircle CenterX=-10.85 CenterY=0 CenterZ=0 NormalX=0 NormalY=0 NormalZ=1 AngleXU=0 Radius=2 StartAngle=0 EndAngle=3.14159
    g1: LineSegment StartX=-12.85 StartY=2e-16 StartZ=0 EndX=-8.85 EndY=0 EndZ=0
  constraints (8):
    c: PointOnObject(g0,g-3)
    c: PointOnObject(g0,g-3)
    c: PointOnObject(g0,g-3)
    c: Radius(g0) = 2
    c: DistanceX(g-3,g-1) = 21.7
    c: DistanceX(g-3,g0) = 8.85
    c: Coincident(g1,g0)
    c: Coincident(g1,g0)
FEATURE [PartDesign::Pocket] Pocket384
  BaseFeature = -> Pocket383
  Direction = (1,0,0)
  Length = 1.5
  Length2 = 5
  Profile = -> Sketch833
  ReferenceAxis = -> Sketch833 [N_Axis]
  Refine = true
  Suppressed = false
  Type = 0
FEATURE [Sketcher::SketchObject] Sketch834
  ArcFitTolerance = 1e-06
  AttachmentSupport = -> [Pocket384]
  ExternalGeometry = -> [Pocket384]
  FullyConstrained = true
  MakeInternals = false
  MapMode = 5
  Placement = pos=(0,0,5.5) rot=(1,0,0;3.14159rad)
  sketch-geometry (4):
    g0: LineSegment StartX=9.7 StartY=-9.2 StartZ=0 EndX=9.7 EndY=-12.5 EndZ=0
    g1: LineSegment StartX=9.7 StartY=-12.5 StartZ=0 EndX=19.3 EndY=-12.5 EndZ=0
    g2: LineSegment StartX=19.3 StartY=-12.5 StartZ=0 EndX=19.3 EndY=-9.2 EndZ=0
    g3: LineSegment StartX=19.3 StartY=-9.2 StartZ=0 EndX=9.7 EndY=-9.2 EndZ=0
  constraints (13):
    c: Coincident(g0,g1)
    c: Coincident(g1,g2)
    c: Coincident(g2,g3)
    c: Coincident(g3,g0)
    c: Vertical(g0)
    c: Vertical(g2)
    c: Horizontal(g1)
    c: Horizontal(g3)
    c: DistanceY(g0,g0) = 3.3
    c: DistanceX(g3,g3) = 9.6
    c: DistanceX(g-1,g0) = 9.7
    c: DistanceY(g-4,g-1) = 21.7
    c: DistanceY(g0,g-1) = 9.2
FEATURE [PartDesign::Pocket] Pocket385
  BaseFeature = -> Pocket384
  Direction = (0,0,1)
  Length = 5
  Length2 = 5
  Profile = -> Sketch834
  ReferenceAxis = -> Sketch834 [N_Axis]
  Refine = true
  Suppressed = false
  Type = 1
FEATURE [Sketcher::SketchObject] Sketch835
  ArcFitTolerance = 1e-06
  AttachmentSupport = -> [Pocket385]
  ExternalGeometry = -> [Pocket385]
  FullyConstrained = true
  MakeInternals = false
  MapMode = 5
  Placement = pos=(0,0,5.5) rot=(1,0,0;3.14159rad)
  sketch-geometry (8):
    g0: LineSegment StartX=1.5 StartY=-10.1 StartZ=0 EndX=1.5 EndY=-11.6 EndZ=0
    g1: LineSegment StartX=1.5 StartY=-11.6 StartZ=0 EndX=8.7 EndY=-11.6 EndZ=0
    g2: LineSegment StartX=8.7 StartY=-11.6 StartZ=0 EndX=8.7 EndY=-14.85 EndZ=0
    g3: LineSegment StartX=8.7 StartY=-14.85 StartZ=0 EndX=9.7 EndY=-14.85 EndZ=0
    g4: LineSegment StartX=9.7 StartY=-14.85 StartZ=0 EndX=9.7 EndY=-6.85 EndZ=0
    g5: LineSegment StartX=9.7 StartY=-6.85 StartZ=0 EndX=8.7 EndY=-6.85 EndZ=0
    g6: LineSegment StartX=8.7 StartY=-6.85 StartZ=0 EndX=8.7 EndY=-10.1 EndZ=0
    g7: LineSegment StartX=8.7 StartY=-10.1 StartZ=0 EndX=1.5 EndY=-10.1 EndZ=0
  constraints (25):
    c: PointOnObject(g0,g-3)
    c: PointOnObject(g0,g-3)
    c: Coincident(g1,g0)
    c: Horizontal(g1)
    c: Coincident(g2,g1)
    c: Vertical(g2)
    c: Coincident(g3,g2)
    c: Horizontal(g3)
    c: Coincident(g4,g3)
    c: Vertical(g4)
    c: Coincident(g5,g4)
    c: Horizontal(g5)
    c: Coincident(g6,g5)
    c: Vertical(g6)
    c: Coincident(g7,g6)
    c: Coincident(g7,g0)
    c: Horizontal(g7)
    c: DistanceY(g0,g0) = 1.5
    c: DistanceX(g5,g5) = 1
    c: DistanceX(g3,g3) = 1
    c: PointOnObject(g-4,g4)
    c: DistanceY(g3,g4) = 8
    c: DistanceY(g-5,g-5) = 3.3
    c: DistanceY(g-4,g4) = 2.35
    c: DistanceY(g6,g-4) = 0.9
FEATURE [PartDesign::Pad] Pad562
  BaseFeature = -> Pocket385
  Direction = (0,0,-1)
  Length = 3.5
  Length2 = 10
  Profile = -> Sketch835
  ReferenceAxis = -> Sketch835 [N_Axis]
  Refine = true
  Suppressed = false
  Type = 0
FEATURE [Sketcher::SketchObject] Sketch836
  ArcFitTolerance = 1e-06
  AttachmentSupport = -> [Pad562]
  ExternalGeometry = -> [Pad562]
  FullyConstrained = true
  MakeInternals = false
  MapMode = 5
  Placement = pos=(0,0,5.5) rot=(1,0,0;3.14159rad)
  sketch-geometry (8):
    g0: Circle CenterX=4.85 CenterY=-4.4 CenterZ=0 NormalX=0 NormalY=0 NormalZ=1 AngleXU=0 Radius=2.1
    g1: Circle CenterX=4.85 CenterY=-17.3 CenterZ=0 NormalX=0 NormalY=0 NormalZ=1 AngleXU=0 Radius=2.1
    g2: Circle CenterX=4.85 CenterY=-4.4 CenterZ=0 NormalX=0 NormalY=0 NormalZ=1 AngleXU=0 Radius=0.75
    g3: Circle CenterX=4.85 CenterY=-17.3 CenterZ=0 NormalX=0 NormalY=0 NormalZ=1 AngleXU=0 Radius=0.75
    g4: LineSegment [constr] StartX=4.85 StartY=-4.4 StartZ=0 EndX=4.85 EndY=-2.3 EndZ=0
    g5: LineSegment [constr] StartX=4.85 StartY=-17.3 StartZ=0 EndX=4.85 EndY=-19.4 EndZ=0
    g6: LineSegment [constr] StartX=4.85 StartY=-17.3 StartZ=0 EndX=2.75 EndY=-17.3 EndZ=0
    g7: LineSegment [constr] StartX=4.85 StartY=-4.4 StartZ=0 EndX=2.75 EndY=-4.4 EndZ=0
  constraints (22):
    c: Diameter(g1) = 4.2
    c: Diameter(g0) = 4.2
    c: Coincident(g2,g0)
    c: Coincident(g3,g1)
    c: Radius(g3) = 0.75
    c: Radius(g2) = 0.75
    c: Coincident(g4,g0)
    c: PointOnObject(g4,g0)
    c: Vertical(g4)
    c: Coincident(g5,g1)
    c: PointOnObject(g5,g1)
    c: Vertical(g5)
    c: DistanceY(g4,g-1) = 2.3
    c: DistanceY(g-4,g5) = 2.3
    c: Coincident(g6,g1)
    c: PointOnObject(g6,g1)
    c: Horizontal(g6)
    c: Coincident(g7,g0)
    c: PointOnObject(g7,g0)
    c: Horizontal(g7)
    c: DistanceX(g-1,g7) = 2.75
    c: DistanceX(g-4,g6) = 2.75
FEATURE [PartDesign::Pad] Pad563
  BaseFeature = -> Pad562
  Direction = (0,0,-1)
  Length = 6
  Length2 = 10
  Profile = -> Sketch836
  ReferenceAxis = -> Sketch836 [N_Axis]
  Refine = true
  Suppressed = false
  Type = 0
FEATURE [Sketcher::SketchObject] Sketch837
  ArcFitTolerance = 1e-06
  AttachmentSupport = -> [Pad563]
  ExternalGeometry = -> [Pad563]
  FullyConstrained = true
  MakeInternals = false
  MapMode = 5
  Placement = pos=(0,0,0) rot=(1,0,0;3.14159rad)
  sketch-geometry (8):
    g0: ArcOfCircle CenterX=4.85 CenterY=-17.3 CenterZ=0 NormalX=0 NormalY=0 NormalZ=1 AngleXU=0 Radius=2.68328 StartAngle=4.24874 EndAngle=5.17604
    g1: ArcOfCircle CenterX=4.85 CenterY=-4.4 CenterZ=0 NormalX=0 NormalY=0 NormalZ=1 AngleXU=0 Radius=2.68328 StartAngle=1.10715 EndAngle=2.03444
    g2: LineSegment StartX=3.65 StartY=-19.7 StartZ=0 EndX=3.65 EndY=-19.0234 EndZ=0
    g3: LineSegment StartX=6.05 StartY=-19.7 StartZ=0 EndX=6.05 EndY=-19.0234 EndZ=0
    g4: ArcOfCircle CenterX=4.85 CenterY=-17.3 CenterZ=0 NormalX=0 NormalY=0 NormalZ=1 AngleXU=0 Radius=2.09999 StartAngle=4.10414 EndAngle=5.32064
    g5: LineSegment StartX=3.65 StartY=-2 StartZ=0 EndX=3.65 EndY=-2.67663 EndZ=0
    g6: LineSegment StartX=6.05 StartY=-2 StartZ=0 EndX=6.05 EndY=-2.67663 EndZ=0
    g7: ArcOfCircle CenterX=4.85 CenterY=-4.39999 CenterZ=0 NormalX=0 NormalY=0 NormalZ=1 AngleXU=0 Radius=2.09999 StartAngle=0.962548 EndAngle=2.17904
  constraints (26):
    c: PointOnObject(g0,g-6)
    c: PointOnObject(g0,g-6)
    c: PointOnObject(g1,g-4)
    c: PointOnObject(g1,g-4)
    c: Coincident(g1,g-3)
    c: Coincident(g0,g-5)
    c: DistanceX(g1,g-9) = 0.9
    c: DistanceX(g0,g-10) = 0.9
    c: Coincident(g2,g0)
    c: PointOnObject(g2,g-8)
    c: Vertical(g2)
    c: Coincident(g3,g0)
    c: PointOnObject(g3,g-8)
    c: Vertical(g3)
    c: Coincident(g4,g2)
    c: Coincident(g4,g3)
    c: Tangent(g-8,g4)
    c: Coincident(g5,g1)
    c: PointOnObject(g5,g-7)
    c: Vertical(g5)
    c: Coincident(g6,g1)
    c: PointOnObject(g6,g-7)
    c: Vertical(g6)
    c: Coincident(g7,g5)
    c: Coincident(g7,g6)
    c: Tangent(g7,g-7)
FEATURE [PartDesign::Pocket] Pocket386
  BaseFeature = -> Pad563
  Direction = (0,0,1)
  Length = 5.5
  Length2 = 5
  Profile = -> Sketch837
  ReferenceAxis = -> Sketch837 [N_Axis]
  Refine = true
  Suppressed = false
  Type = 0
FEATURE [Sketcher::SketchObject] Sketch838
  ArcFitTolerance = 1e-06
  AttachmentSupport = -> [Pocket386]
  ExternalGeometry = -> [Pocket386]
  FullyConstrained = true
  MakeInternals = false
  MapMode = 5
  Placement = pos=(0,0,5.5) rot=(1,0,0;3.14159rad)
  sketch-geometry (7):
    g0: Circle CenterX=20.05 CenterY=-7.2 CenterZ=0 NormalX=0 NormalY=0 NormalZ=1 AngleXU=0 Radius=0.75
    g1: Circle CenterX=20.05 CenterY=-14.5 CenterZ=0 NormalX=0 NormalY=0 NormalZ=1 AngleXU=0 Radius=0.75
    g2: LineSegment [constr] StartX=20.05 StartY=-14.5 StartZ=0 EndX=19.3 EndY=-14.5 EndZ=0
    g3: LineSegment [constr] StartX=19.3 StartY=-14.5 StartZ=0 EndX=19.3 EndY=-12.5 EndZ=0
    g4: LineSegment [constr] StartX=20.05 StartY=-14.5 StartZ=0 EndX=20.05 EndY=-13.75 EndZ=0
    g5: LineSegment [constr] StartX=20.05 StartY=-13.75 StartZ=0 EndX=20.05 EndY=-7.95 EndZ=0
    g6: LineSegment [constr] StartX=20.05 StartY=-7.2 StartZ=0 EndX=20.05 EndY=-7.95 EndZ=0
  constraints (20):
    c: Diameter(g1) = 1.5
    c: Diameter(g0) = 1.5
    c: Coincident(g2,g1)
    c: PointOnObject(g2,g1)
    c: Horizontal(g2)
    c: Coincident(g3,g2)
    c: Coincident(g3,g-3)
    c: Vertical(g3)
    c: Coincident(g4,g1)
    c: PointOnObject(g4,g1)
    c: Vertical(g4)
    c: Coincident(g5,g4)
    c: PointOnObject(g5,g0)
    c: Vertical(g5)
    c: Coincident(g6,g0)
    c: Coincident(g6,g5)
    c: Vertical(g6)
    c: DistanceY(g5,g5) = 5.8
    c: DistanceY(g3,g-3) = 3.3
    c: DistanceY(g-3,g5) = 1.25
FEATURE [PartDesign::Pad] Pad564
  BaseFeature = -> Pocket386
  Direction = (0,0,-1)
  Length = 1.5
  Length2 = 10
  Profile = -> Sketch838
  ReferenceAxis = -> Sketch838 [N_Axis]
  Refine = true
  Suppressed = false
  Type = 0
FEATURE [Sketcher::SketchObject] Sketch839
  ArcFitTolerance = 1e-06
  AttachmentSupport = -> [Pad564]
  ExternalGeometry = -> [Pad564]
  FullyConstrained = false
  MakeInternals = false
  MapMode = 5
  Placement = pos=(0,0,7) rot=(0,0,1;0rad)
  sketch-geometry (11):
    g0: LineSegment StartX=19.3 StartY=12.5 StartZ=0 EndX=4 EndY=12.5 EndZ=0
    g1: LineSegment StartX=19.3 StartY=9.2 StartZ=0 EndX=4 EndY=9.2 EndZ=0
    g2: LineSegment StartX=4 StartY=9.2 StartZ=0 EndX=4 EndY=7.7 EndZ=0
    g3: LineSegment StartX=4 StartY=7.7 StartZ=0 EndX=21.8 EndY=7.7 EndZ=0
    g4: LineSegment StartX=21.8 StartY=7.7 StartZ=0 EndX=21.8 EndY=14 EndZ=0
    g5: LineSegment StartX=21.8 StartY=14 StartZ=0 EndX=4 EndY=14 EndZ=0
    g6: LineSegment StartX=4 StartY=14 StartZ=0 EndX=4 EndY=12.5 EndZ=0
    g7: LineSegment [constr] StartX=4 StartY=12.5 StartZ=0 EndX=4 EndY=9.2 EndZ=0
    g8: LineSegment StartX=19.3 StartY=12.5 StartZ=0 EndX=20.3 EndY=12.5 EndZ=0
    g9: LineSegment StartX=20.3 StartY=12.5 StartZ=0 EndX=20.3 EndY=9.14209 EndZ=0
    g10: LineSegment StartX=20.3 StartY=9.14209 StartZ=0 EndX=19.3 EndY=9.2 EndZ=0
  constraints (29):
    c: Coincident(g0,g-4)
    c: Horizontal(g0)
    c: Coincident(g1,g-5)
    c: Horizontal(g1)
    c: Coincident(g2,g1)
    c: Vertical(g2)
    c: Coincident(g3,g2)
    c: Horizontal(g3)
    c: Coincident(g4,g3)
    c: Vertical(g4)
    c: Coincident(g5,g4)
    c: Horizontal(g5)
    c: Coincident(g6,g5)
    c: Coincident(g6,g0)
    c: Vertical(g6)
    c: DistanceY(g2,g2) = 1.5
    c: DistanceY(g6,g6) = 1.5
    c: Coincident(g7,g0)
    c: Coincident(g7,g1)
    c: Vertical(g7)
    c: DistanceX(g5,g5) = 17.8
    c: Coincident(g8,g0)
    c: Horizontal(g8)
    c: Coincident(g9,g8)
    c: Vertical(g9)
    c: Coincident(g10,g9)
    c: Coincident(g10,g1)
    c: DistanceX(g8,g8) = 1
    c: DistanceX(g8,g4) = 1.5
FEATURE [PartDesign::Pad] Pad565
  BaseFeature = -> Pad564
  Direction = (0,0,1)
  Length = 1
  Length2 = 10
  Profile = -> Sketch839
  ReferenceAxis = -> Sketch839 [N_Axis]
  Refine = true
  Suppressed = false
  Type = 0
FEATURE [Sketcher::SketchObject] Sketch840
  ArcFitTolerance = 1e-06
  AttachmentSupport = -> [Pad565]
  ExternalGeometry = -> [Pad565]
  FullyConstrained = true
  MakeInternals = false
  MapMode = 5
  Placement = pos=(0,7.7,0) rot=(1,0,0;1.5708rad)
  sketch-geometry (3):
    g0: LineSegment StartX=4 StartY=7 StartZ=0 EndX=4 EndY=8 EndZ=0
    g1: LineSegment StartX=4 StartY=8 StartZ=0 EndX=7 EndY=8 EndZ=0
    g2: LineSegment StartX=7 StartY=8 StartZ=0 EndX=4 EndY=7 EndZ=0
  constraints (7):
    c: Coincident(g0,g-3)
    c: Coincident(g1,g0)
    c: PointOnObject(g1,g-3)
    c: Coincident(g2,g1)
    c: Coincident(g2,g0)
    c: DistanceX(g1,g1) = 3
    c: Coincident(g0,g-4)
FEATURE [PartDesign::Pocket] Pocket387
  BaseFeature = -> Pad565
  Direction = (0,1,-2e-16)
  Length = 6.3
  Length2 = 5
  Profile = -> Sketch840
  ReferenceAxis = -> Sketch840 [N_Axis]
  Refine = true
  Suppressed = false
  Type = 0
FEATURE [Sketcher::SketchObject] Sketch841
  ArcFitTolerance = 1e-06
  AttachmentSupport = -> [Pocket387]
  ExternalGeometry = -> [Pocket387]
  FullyConstrained = true
  MakeInternals = false
  MapMode = 5
  Placement = pos=(0,0,7) rot=(0,0,1;0rad)
  sketch-geometry (10):
    g0: LineSegment StartX=9.7 StartY=14 StartZ=0 EndX=14.2 EndY=14 EndZ=0
    g1: LineSegment StartX=14.2 StartY=14 StartZ=0 EndX=14.2 EndY=22.5 EndZ=0
    g2: LineSegment StartX=14.2 StartY=22.5 StartZ=0 EndX=9.7 EndY=22.5 EndZ=0
    g3: LineSegment StartX=9.7 StartY=22.5 StartZ=0 EndX=9.7 EndY=14 EndZ=0
    g4: LineSegment StartX=9.7 StartY=7.7 StartZ=0 EndX=9.7 EndY=-0.8 EndZ=0
    g5: LineSegment StartX=9.7 StartY=-0.8 StartZ=0 EndX=14.2 EndY=-0.8 EndZ=0
    g6: LineSegment StartX=14.2 StartY=-0.8 StartZ=0 EndX=14.2 EndY=7.7 EndZ=0
    g7: LineSegment StartX=14.2 StartY=7.7 StartZ=0 EndX=9.7 EndY=7.7 EndZ=0
    g8: LineSegment [constr] StartX=9.7 StartY=14 StartZ=0 EndX=9.7 EndY=12.5 EndZ=0
    g9: LineSegment [constr] StartX=9.7 StartY=9.2 StartZ=0 EndX=9.7 EndY=7.7 EndZ=0
  constraints (28):
    c: Coincident(g0,g1)
    c: Coincident(g1,g2)
    c: Coincident(g2,g3)
    c: Coincident(g3,g0)
    c: Horizontal(g0)
    c: Horizontal(g2)
    c: Vertical(g1)
    c: Vertical(g3)
    c: PointOnObject(g0,g-3)
    c: Coincident(g4,g5)
    c: Coincident(g5,g6)
    c: Coincident(g6,g7)
    c: Coincident(g7,g4)
    c: Vertical(g4)
    c: Vertical(g6)
    c: Horizontal(g5)
    c: Horizontal(g7)
    c: PointOnObject(g4,g-4)
    c: DistanceX(g7,g7) = 4.5
    c: DistanceX(g0,g0) = 4.5
    c: Coincident(g8,g0)
    c: Coincident(g8,g-5)
    c: Coincident(g9,g-5)
    c: Coincident(g9,g4)
    c: Vertical(g8)
    c: Vertical(g9)
    c: DistanceY(g5,g-7) = 0.8
    c: DistanceY(g-6,g1) = 0.8
FEATURE [PartDesign::Pad] Pad566
  BaseFeature = -> Pocket387
  Direction = (0,0,1)
  Length = 0.8
  Length2 = 10
  Profile = -> Sketch841
  ReferenceAxis = -> Sketch841 [N_Axis]
  Refine = true
  Suppressed = false
  Type = 0
FEATURE [Sketcher::SketchObject] Sketch842
  ArcFitTolerance = 1e-06
  AttachmentSupport = -> [Pad566]
  ExternalGeometry = -> [Pad566]
  FullyConstrained = true
  MakeInternals = false
  MapMode = 5
  Placement = pos=(0,0,7) rot=(0,0,1;0rad)
  sketch-geometry (24):
    g0: LineSegment StartX=14.2 StartY=21.7 StartZ=0 EndX=14.2 EndY=14 EndZ=0
    g1: LineSegment StartX=14.2 StartY=14 StartZ=0 EndX=15.7 EndY=14 EndZ=0
    g2: LineSegment StartX=15.7 StartY=14 StartZ=0 EndX=15.7 EndY=21.7 EndZ=0
    g3: LineSegment StartX=15.7 StartY=21.7 StartZ=0 EndX=14.2 EndY=21.7 EndZ=0
    g4: LineSegment StartX=17.7 StartY=21.7 StartZ=0 EndX=17.7 EndY=14 EndZ=0
    g5: LineSegment StartX=17.7 StartY=14 StartZ=0 EndX=19.2 EndY=14 EndZ=0
    g6: LineSegment StartX=19.2 StartY=14 StartZ=0 EndX=19.2 EndY=21.7 EndZ=0
    g7: LineSegment StartX=19.2 StartY=21.7 StartZ=0 EndX=17.7 EndY=21.7 EndZ=0
    g8: LineSegment StartX=21.2 StartY=21.7 StartZ=0 EndX=21.2 EndY=14 EndZ=0
    g9: LineSegment StartX=21.2 StartY=14 StartZ=0 EndX=22.7 EndY=14 EndZ=0
    g10: LineSegment StartX=22.7 StartY=14 StartZ=0 EndX=22.7 EndY=21.7 EndZ=0
    g11: LineSegment StartX=22.7 StartY=21.7 StartZ=0 EndX=21.2 EndY=21.7 EndZ=0
    g12: LineSegment StartX=14.2 StartY=7.7 StartZ=0 EndX=14.2 EndY=0 EndZ=0
    g13: LineSegment StartX=14.2 StartY=0 StartZ=0 EndX=15.7 EndY=0 EndZ=0
    g14: LineSegment StartX=15.7 StartY=0 StartZ=0 EndX=15.7 EndY=7.7 EndZ=0
    g15: LineSegment StartX=15.7 StartY=7.7 StartZ=0 EndX=14.2 EndY=7.7 EndZ=0
    g16: LineSegment StartX=17.7 StartY=7.7 StartZ=0 EndX=17.7 EndY=0 EndZ=0
    g17: LineSegment StartX=17.7 StartY=0 StartZ=0 EndX=19.2 EndY=0 EndZ=0
    g18: LineSegment StartX=19.2 StartY=0 StartZ=0 EndX=19.2 EndY=7.7 EndZ=0
    g19: LineSegment StartX=19.2 StartY=7.7 StartZ=0 EndX=17.7 EndY=7.7 EndZ=0
    g20: LineSegment StartX=21.2 StartY=7.7 StartZ=0 EndX=21.2 EndY=0 EndZ=0
    g21: LineSegment StartX=21.2 StartY=0 StartZ=0 EndX=22.7 EndY=0 EndZ=0
    g22: LineSegment StartX=22.7 StartY=0 StartZ=0 EndX=22.7 EndY=7.7 EndZ=0
    g23: LineSegment StartX=22.7 StartY=7.7 StartZ=0 EndX=21.2 EndY=7.7 EndZ=0
  constraints (70):
    c: Coincident(g0,g1)
    c: Coincident(g1,g2)
    c: Coincident(g2,g3)
    c: Coincident(g3,g0)
    c: Vertical(g0)
    c: Vertical(g2)
    c: Horizontal(g1)
    c: Horizontal(g3)
    c: Coincident(g0,g-3)
    c: PointOnObject(g1,g-6)
    c: Coincident(g4,g5)
    c: Coincident(g5,g6)
    c: Coincident(g6,g7)
    c: Coincident(g7,g4)
    c: Vertical(g4)
    c: Vertical(g6)
    c: Horizontal(g5)
    c: Horizontal(g7)
    c: PointOnObject(g4,g-3)
    c: PointOnObject(g5,g-6)
    c: Coincident(g8,g9)
    c: Coincident(g9,g10)
    c: Coincident(g10,g11)
    c: Coincident(g11,g8)
    c: Vertical(g8)
    c: Vertical(g10)
    c: Horizontal(g9)
    c: Horizontal(g11)
    c: PointOnObject(g8,g-3)
    c: PointOnObject(g8,g-6)
    c: DistanceX(g3,g3) = 1.5
    c: DistanceX(g2,g4) = 2
    c: DistanceX(g7,g7) = 1.5
    c: DistanceX(g6,g8) = 2
    c: DistanceX(g8,g10) = 1.5
    c: Coincident(g12,g13)
    c: Coincident(g13,g14)
    c: Coincident(g14,g15)
    c: Coincident(g15,g12)
    c: Vertical(g12)
    c: Vertical(g14)
    c: Horizontal(g13)
    c: Horizontal(g15)
    c: Coincident(g12,g-5)
    c: PointOnObject(g13,g-4)
    c: Coincident(g16,g17)
    c: Coincident(g17,g18)
    c: Coincident(g18,g19)
    c: Coincident(g19,g16)
    c: Vertical(g16)
    c: Vertical(g18)
    c: Horizontal(g17)
    c: Horizontal(g19)
    c: PointOnObject(g16,g-5)
    c: PointOnObject(g17,g-4)
    c: DistanceX(g15,g15) = 1.5
    c: DistanceX(g14,g16) = 2
    c: DistanceX(g16,g18) = 1.5
    c: Coincident(g20,g21)
    c: Coincident(g21,g22)
    c: Coincident(g22,g23)
    c: Coincident(g23,g20)
    c: Vertical(g20)
    c: Vertical(g22)
    c: Horizontal(g21)
    c: Horizontal(g23)
    c: PointOnObject(g20,g-5)
    c: PointOnObject(g21,g-4)
    c: DistanceX(g18,g20) = 2
    c: DistanceX(g23,g23) = 1.5
FEATURE [PartDesign::Pocket] Pocket388
  BaseFeature = -> Pad566
  Direction = (0,0,-1)
  Length = 0.5
  Length2 = 5
  Profile = -> Sketch842
  ReferenceAxis = -> Sketch842 [N_Axis]
  Refine = true
  Suppressed = false
  Type = 0
FEATURE [Sketcher::SketchObject] Sketch843
  ArcFitTolerance = 1e-06
  AttachmentSupport = -> [Pocket388]
  ExternalGeometry = -> [Pocket388]
  FullyConstrained = true
  MakeInternals = false
  MapMode = 5
  Placement = pos=(0,21.7,0) rot=(0,0.707107,0.707107;3.14159rad)
  sketch-geometry (4):
    g0: LineSegment StartX=-14.2 StartY=7 StartZ=0 EndX=-14.2 EndY=0 EndZ=0
    g1: LineSegment StartX=-14.2 StartY=0 StartZ=0 EndX=-9.7 EndY=0 EndZ=0
    g2: LineSegment StartX=-9.7 StartY=0 StartZ=0 EndX=-9.7 EndY=7 EndZ=0
    g3: LineSegment StartX=-9.7 StartY=7 StartZ=0 EndX=-14.2 EndY=7 EndZ=0
  constraints (10):
    c: Coincident(g0,g1)
    c: Coincident(g1,g2)
    c: Coincident(g2,g3)
    c: Coincident(g3,g0)
    c: Vertical(g0)
    c: Vertical(g2)
    c: Horizontal(g1)
    c: Coincident(g0,g-3)
    c: PointOnObject(g1,g-4)
    c: Coincident(g2,g-3)
FEATURE [PartDesign::Pad] Pad567
  BaseFeature = -> Pocket388
  Direction = (0,1,-2e-16)
  Length = 0.8
  Length2 = 10
  Profile = -> Sketch843
  ReferenceAxis = -> Sketch843 [N_Axis]
  Refine = true
  Suppressed = false
  Type = 0
FEATURE [Sketcher::SketchObject] Sketch844
  ArcFitTolerance = 1e-06
  AttachmentSupport = -> [Pad567]
  ExternalGeometry = -> [Pad567]
  FullyConstrained = true
  MakeInternals = false
  MapMode = 5
  Placement = pos=(0,0,0) rot=(1,0,0;1.5708rad)
  sketch-geometry (4):
    g0: LineSegment StartX=9.7 StartY=7 StartZ=0 EndX=9.7 EndY=0 EndZ=0
    g1: LineSegment StartX=9.7 StartY=0 StartZ=0 EndX=14.2 EndY=0 EndZ=0
    g2: LineSegment StartX=14.2 StartY=0 StartZ=0 EndX=14.2 EndY=7 EndZ=0
    g3: LineSegment StartX=14.2 StartY=7 StartZ=0 EndX=9.7 EndY=7 EndZ=0
  constraints (10):
    c: Coincident(g0,g1)
    c: Coincident(g1,g2)
    c: Coincident(g2,g3)
    c: Coincident(g3,g0)
    c: Vertical(g0)
    c: Vertical(g2)
    c: Horizontal(g1)
    c: Coincident(g0,g-3)
    c: PointOnObject(g1,g-4)
    c: Coincident(g2,g-3)
FEATURE [PartDesign::Pad] Pad568
  BaseFeature = -> Pad567
  Direction = (0,-1,2e-16)
  Length = 0.8
  Length2 = 10
  Profile = -> Sketch844
  ReferenceAxis = -> Sketch844 [N_Axis]
  Refine = true
  Suppressed = false
  Type = 0
FEATURE [Sketcher::SketchObject] Sketch845
  ArcFitTolerance = 1e-06
  AttachmentSupport = -> [Pad568]
  ExternalGeometry = -> [Pad568]
  FullyConstrained = true
  MakeInternals = false
  MapMode = 5
  Placement = pos=(0,0,0) rot=(1,0,0;1.5708rad)
  sketch-geometry (12):
    g0: LineSegment StartX=14.2 StartY=6.5 StartZ=0 EndX=14.2 EndY=0 EndZ=0
    g1: LineSegment StartX=14.2 StartY=0 StartZ=0 EndX=15.7 EndY=0 EndZ=0
    g2: LineSegment StartX=15.7 StartY=0 StartZ=0 EndX=15.7 EndY=6.5 EndZ=0
    g3: LineSegment StartX=15.7 StartY=6.5 StartZ=0 EndX=14.2 EndY=6.5 EndZ=0
    g4: LineSegment StartX=17.7 StartY=6.5 StartZ=0 EndX=17.7 EndY=0 EndZ=0
    g5: LineSegment StartX=17.7 StartY=0 StartZ=0 EndX=19.2 EndY=0 EndZ=0
    g6: LineSegment StartX=19.2 StartY=0 StartZ=0 EndX=19.2 EndY=6.5 EndZ=0
    g7: LineSegment StartX=19.2 StartY=6.5 StartZ=0 EndX=17.7 EndY=6.5 EndZ=0
    g8: LineSegment StartX=21.2 StartY=6.5 StartZ=0 EndX=21.2 EndY=0 EndZ=0
    g9: LineSegment StartX=21.2 StartY=0 StartZ=0 EndX=22.7 EndY=0 EndZ=0
    g10: LineSegment StartX=22.7 StartY=0 StartZ=0 EndX=22.7 EndY=6.5 EndZ=0
    g11: LineSegment StartX=22.7 StartY=6.5 StartZ=0 EndX=21.2 EndY=6.5 EndZ=0
  constraints (30):
    c: Coincident(g0,g1)
    c: Coincident(g1,g2)
    c: Coincident(g2,g3)
    c: Coincident(g3,g0)
    c: Vertical(g0)
    c: Vertical(g2)
    c: Horizontal(g1)
    c: Coincident(g0,g-4)
    c: PointOnObject(g1,g-3)
    c: Coincident(g4,g5)
    c: Coincident(g5,g6)
    c: Coincident(g6,g7)
    c: Coincident(g7,g4)
    c: Vertical(g4)
    c: Vertical(g6)
    c: Horizontal(g5)
    c: Coincident(g4,g-5)
    c: Coincident(g8,g9)
    c: Coincident(g9,g10)
    c: Coincident(g10,g11)
    c: Coincident(g11,g8)
    c: Vertical(g8)
    c: Vertical(g10)
    c: Horizontal(g9)
    c: Coincident(g8,g-6)
    c: PointOnObject(g9,g-3)
    c: Coincident(g2,g-4)
    c: Coincident(g6,g-5)
    c: Coincident(g10,g-6)
    c: PointOnObject(g4,g-3)
FEATURE [PartDesign::Pocket] Pocket389
  BaseFeature = -> Pad568
  Direction = (0,1,-2e-16)
  Length = 0.5
  Length2 = 5
  Profile = -> Sketch845
  ReferenceAxis = -> Sketch845 [N_Axis]
  Refine = true
  Suppressed = false
  Type = 0
FEATURE [Sketcher::SketchObject] Sketch846
  ArcFitTolerance = 1e-06
  AttachmentSupport = -> [Pocket389]
  ExternalGeometry = -> [Pocket389]
  FullyConstrained = true
  MakeInternals = false
  MapMode = 5
  Placement = pos=(0,21.7,0) rot=(0,0.707107,0.707107;3.14159rad)
  sketch-geometry (12):
    g0: LineSegment StartX=-15.7 StartY=6.5 StartZ=0 EndX=-15.7 EndY=0 EndZ=0
    g1: LineSegment StartX=-15.7 StartY=0 StartZ=0 EndX=-14.2 EndY=0 EndZ=0
    g2: LineSegment StartX=-14.2 StartY=0 StartZ=0 EndX=-14.2 EndY=6.5 EndZ=0
    g3: LineSegment StartX=-14.2 StartY=6.5 StartZ=0 EndX=-15.7 EndY=6.5 EndZ=0
    g4: LineSegment StartX=-17.7 StartY=6.5 StartZ=0 EndX=-19.2 EndY=6.5 EndZ=0
    g5: LineSegment StartX=-19.2 StartY=6.5 StartZ=0 EndX=-19.2 EndY=0 EndZ=0
    g6: LineSegment StartX=-19.2 StartY=0 StartZ=0 EndX=-17.7 EndY=0 EndZ=0
    g7: LineSegment StartX=-17.7 StartY=0 StartZ=0 EndX=-17.7 EndY=6.5 EndZ=0
    g8: LineSegment StartX=-21.2 StartY=6.5 StartZ=0 EndX=-22.7 EndY=6.5 EndZ=0
    g9: LineSegment StartX=-22.7 StartY=6.5 StartZ=0 EndX=-22.7 EndY=0 EndZ=0
    g10: LineSegment StartX=-22.7 StartY=0 StartZ=0 EndX=-21.2 EndY=0 EndZ=0
    g11: LineSegment StartX=-21.2 StartY=0 StartZ=0 EndX=-21.2 EndY=6.5 EndZ=0
  constraints (30):
    c: Coincident(g0,g1)
    c: Coincident(g1,g2)
    c: Coincident(g2,g3)
    c: Coincident(g3,g0)
    c: Vertical(g0)
    c: Vertical(g2)
    c: Horizontal(g1)
    c: Horizontal(g3)
    c: Coincident(g0,g-6)
    c: Coincident(g1,g-3)
    c: Coincident(g4,g5)
    c: Coincident(g5,g6)
    c: Coincident(g6,g7)
    c: Coincident(g7,g4)
    c: Horizontal(g6)
    c: Vertical(g5)
    c: Vertical(g7)
    c: Coincident(g4,g-5)
    c: PointOnObject(g5,g-3)
    c: Coincident(g8,g9)
    c: Coincident(g9,g10)
    c: Coincident(g10,g11)
    c: Coincident(g11,g8)
    c: Horizontal(g10)
    c: Vertical(g9)
    c: Vertical(g11)
    c: Coincident(g8,g-4)
    c: PointOnObject(g9,g-3)
    c: Coincident(g8,g-4)
    c: Coincident(g-5,g4)
FEATURE [PartDesign::Pocket] Pocket390
  BaseFeature = -> Pocket389
  Direction = (0,-1,2e-16)
  Length = 0.5
  Length2 = 5
  Profile = -> Sketch846
  ReferenceAxis = -> Sketch846 [N_Axis]
  Refine = true
  Suppressed = false
  Type = 0
FEATURE [PartDesign::Chamfer] Chamfer032
  Angle = 45
  Base = -> Pocket390 [Edge30,Edge31,Edge47,Edge54,Edge59,Edge66,Edge71,Edge78,Edge84,Edge83,Edge284,Edge292,Edge206,Edge283,Edge291,Edge299,Edge210,Edge88,Edge227,Edge92,Edge22,Edge213,Edge217,Edge218,Edge223,Edge224,Edge121]
  BaseFeature = -> Pocket390
  ChamferType = 0
  FlipDirection = false
  Refine = true
  Size = 0.999
  Size2 = 1
  SupportTransform = false
  Suppressed = false
  UseAllEdges = false
FEATURE [Sketcher::SketchObject] Sketch847
  ArcFitTolerance = 1e-06
  AttachmentSupport = -> [Chamfer032]
  ExternalGeometry = -> [Chamfer032]
  FullyConstrained = true
  MakeInternals = false
  MapMode = 5
  Placement = pos=(0,21.7,0) rot=(0,0.707107,0.707107;3.14159rad)
  sketch-geometry (2):
    g0: ArcOfCircle CenterX=-20.2 CenterY=0 CenterZ=0 NormalX=0 NormalY=0 NormalZ=1 AngleXU=0 Radius=2.85 StartAngle=0 EndAngle=3.14159
    g1: LineSegment StartX=-23.05 StartY=0 StartZ=0 EndX=-17.35 EndY=0 EndZ=0
  constraints (8):
    c: PointOnObject(g0,g-5)
    c: PointOnObject(g0,g-7)
    c: Diameter(g0) = 5.7
    c: PointOnObject(g0,g-3)
    c: DistanceX(g-4,g-6) = 2
    c: DistanceX(g-4,g0) = 1
    c: Coincident(g1,g0)
    c: Coincident(g1,g0)
FEATURE [PartDesign::Pad] Pad569
  BaseFeature = -> Chamfer032
  Direction = (0,1,-2e-16)
  Length = 1
  Length2 = 10
  Profile = -> Sketch847
  ReferenceAxis = -> Sketch847 [N_Axis]
  Refine = true
  Suppressed = false
  Type = 0
FEATURE [PartDesign::Pad] Pad570
  BaseFeature = -> Pad569
  Direction = (0,1,-2e-16)
  Length = 1
  Length2 = 10
  Profile = -> Sketch847
  ReferenceAxis = -> Sketch847 [N_Axis]
  Refine = true
  Reversed = true
  Suppressed = false
  Type = 0
FEATURE [Sketcher::SketchObject] Sketch848
  ArcFitTolerance = 1e-06
  AttachmentSupport = -> [Pad570]
  ExternalGeometry = -> [Pad570]
  FullyConstrained = true
  MakeInternals = false
  MapMode = 5
  Placement = pos=(0,0.5,0) rot=(1,0,0;1.5708rad)
  sketch-geometry (2):
    g0: ArcOfCircle CenterX=20.2 CenterY=-7.42045e-06 CenterZ=0 NormalX=0 NormalY=0 NormalZ=1 AngleXU=0 Radius=2.85 StartAngle=2.60367e-06 EndAngle=3.14159
    g1: LineSegment StartX=17.35 StartY=5.3e-15 StartZ=0 EndX=23.05 EndY=0 EndZ=0
  constraints (5):
    c: Coincident(g0,g-4)
    c: Coincident(g0,g-4)
    c: Tangent(g0,g-3)
    c: Coincident(g1,g0)
    c: Coincident(g1,g0)
FEATURE [PartDesign::Pad] Pad571
  BaseFeature = -> Pad570
  Direction = (0,-1,2e-16)
  Length = 1.5
  Length2 = 10
  Profile = -> Sketch848
  ReferenceAxis = -> Sketch848 [N_Axis]
  Refine = true
  Suppressed = false
  Type = 0
FEATURE [Sketcher::SketchObject] Sketch849
  ArcFitTolerance = 1e-06
  AttachmentSupport = -> [Pad571]
  ExternalGeometry = -> [Pad571]
  FullyConstrained = true
  MakeInternals = false
  MapMode = 5
  Placement = pos=(0,-1,2e-16) rot=(1,0,0;1.5708rad)
  sketch-geometry (4):
    g0: LineSegment StartX=19.2 StartY=2.66879 StartZ=0 EndX=19.2 EndY=0 EndZ=0
    g1: LineSegment StartX=21.2 StartY=2.66879 StartZ=0 EndX=21.2 EndY=0 EndZ=0
    g2: LineSegment StartX=21.2 StartY=0 StartZ=0 EndX=19.2 EndY=0 EndZ=0
    g3: ArcOfCircle CenterX=20.2 CenterY=-7.41995e-06 CenterZ=0 NormalX=0 NormalY=0 NormalZ=1 AngleXU=0 Radius=2.85 StartAngle=1.21229 EndAngle=1.9293
  constraints (11):
    c: Coincident(g0,g-4)
    c: Vertical(g0)
    c: Coincident(g1,g-5)
    c: Vertical(g1)
    c: Coincident(g2,g1)
    c: Coincident(g2,g0)
    c: Horizontal(g2)
    c: Coincident(g3,g0)
    c: Coincident(g3,g1)
    c: Tangent(g3,g-3)
    c: PointOnObject(g0,g-1)
FEATURE [PartDesign::Pocket] Pocket391
  BaseFeature = -> Pad571
  Direction = (0,1,-2e-16)
  Length = 0.5
  Length2 = 5
  Profile = -> Sketch849
  ReferenceAxis = -> Sketch849 [N_Axis]
  Refine = true
  Suppressed = false
  Type = 0
FEATURE [Sketcher::SketchObject] Sketch850
  ArcFitTolerance = 1e-06
  AttachmentSupport = -> [Pocket391]
  ExternalGeometry = -> [Pocket391]
  FullyConstrained = true
  MakeInternals = false
  MapMode = 5
  Placement = pos=(0,22.7,0) rot=(0,0.707107,0.707107;3.14159rad)
  sketch-geometry (4):
    g0: LineSegment StartX=-21.2 StartY=2.6688 StartZ=0 EndX=-21.2 EndY=-4e-16 EndZ=0
    g1: LineSegment StartX=-19.2 StartY=2.6688 StartZ=0 EndX=-19.2 EndY=-4e-16 EndZ=0
    g2: LineSegment StartX=-21.2 StartY=-4e-16 StartZ=0 EndX=-19.2 EndY=-2e-16 EndZ=0
    g3: ArcOfCircle CenterX=-20.2 CenterY=1.84568e-05 CenterZ=0 NormalX=0 NormalY=0 NormalZ=1 AngleXU=0 Radius=2.84998 StartAngle=1.21229 EndAngle=1.92931
  constraints (11):
    c: Coincident(g0,g-5)
    c: PointOnObject(g0,g-6)
    c: Vertical(g0)
    c: Coincident(g1,g-4)
    c: PointOnObject(g1,g-6)
    c: Vertical(g1)
    c: Coincident(g2,g0)
    c: Coincident(g2,g1)
    c: Coincident(g3,g0)
    c: Coincident(g3,g1)
    c: Tangent(g3,g-3)
FEATURE [PartDesign::Pocket] Pocket392
  BaseFeature = -> Pocket391
  Direction = (0,-1,2e-16)
  Length = 0.5
  Length2 = 5
  Profile = -> Sketch850
  ReferenceAxis = -> Sketch850 [N_Axis]
  Refine = true
  Suppressed = false
  Type = 0
FEATURE [PartDesign::SubShapeBinder] Binder008
  BindCopyOnChange = 0
  BindMode = 2
  ClaimChildren = false
  Context = -> Part002 [Body044.Binder007.]
  Fuse = false
  MakeFace = true
  OffsetFill = false
  OffsetIntersection = false
  OffsetJoinType = 0
  OffsetOpenResult = false
  PartialLoad = false
  Refine = true
  Relative = true
  _Version = 2
FEATURE [Sketcher::SketchObject] Sketch879
  ArcFitTolerance = 1e-06
  AttachmentSupport = -> [Binder008]
  ExternalGeometry = -> [Binder008]
  FullyConstrained = true
  MakeInternals = false
  MapMode = 5
  Placement = pos=(0,0,1e-16) rot=(1,0,0;3.14159rad)
  sketch-geometry (8):
    g0: LineSegment StartX=0 StartY=0 StartZ=0 EndX=26 EndY=0 EndZ=0
    g1: LineSegment StartX=26 StartY=-2.9 StartZ=0 EndX=26 EndY=0 EndZ=0
    g2: LineSegment StartX=26 StartY=-2.9 StartZ=0 EndX=31.6 EndY=-2.9 EndZ=0
    g3: LineSegment StartX=31.6 StartY=-2.9 StartZ=0 EndX=31.6 EndY=-18.8 EndZ=0
    g4: LineSegment StartX=31.6 StartY=-18.8 StartZ=0 EndX=26 EndY=-18.8 EndZ=0
    g5: LineSegment StartX=26 StartY=-18.8 StartZ=0 EndX=26 EndY=-21.7 EndZ=0
    g6: LineSegment StartX=26 StartY=-21.7 StartZ=0 EndX=0 EndY=-21.7 EndZ=0
    g7: LineSegment StartX=0 StartY=-21.7 StartZ=0 EndX=0 EndY=0 EndZ=0
  constraints (21):
    c: Coincident(g0,g-1)
    c: PointOnObject(g0,g-1)
    c: Coincident(g1,g-9)
    c: Coincident(g1,g0)
    c: Vertical(g1)
    c: Coincident(g2,g1)
    c: Horizontal(g2)
    c: Coincident(g3,g2)
    c: Vertical(g3)
    c: PointOnObject(g-12,g3)
    c: Coincident(g4,g3)
    c: Coincident(g4,g-13)
    c: Horizontal(g4)
    c: Coincident(g5,g4)
    c: Vertical(g5)
    c: Coincident(g6,g5)
    c: PointOnObject(g6,g-2)
    c: Horizontal(g6)
    c: PointOnObject(g-6,g6)
    c: Coincident(g7,g6)
    c: Coincident(g7,g0)
FEATURE [PartDesign::Pad] Pad586
  Direction = (0,0,-1)
  Length = 4.5
  Length2 = 10
  Profile = -> Sketch879
  ReferenceAxis = -> Sketch879 [N_Axis]
  Refine = true
  Suppressed = false
  Type = 0
FEATURE [Sketcher::SketchObject] Sketch880
  ArcFitTolerance = 1e-06
  AttachmentSupport = -> [Pad586]
  ExternalGeometry = -> [Pad586]
  FullyConstrained = true
  MakeInternals = false
  MapMode = 5
  Placement = pos=(0,0,-4.5) rot=(1,0,0;3.14159rad)
  sketch-geometry (4):
    g0: LineSegment StartX=0 StartY=0 StartZ=0 EndX=0 EndY=-21.7 EndZ=0
    g1: LineSegment StartX=0 StartY=-21.7 StartZ=0 EndX=26 EndY=-21.7 EndZ=0
    g2: LineSegment StartX=26 StartY=-21.7 StartZ=0 EndX=26 EndY=0 EndZ=0
    g3: LineSegment StartX=26 StartY=0 StartZ=0 EndX=0 EndY=0 EndZ=0
  constraints (10):
    c: Coincident(g0,g1)
    c: Coincident(g1,g2)
    c: Coincident(g2,g3)
    c: Coincident(g3,g0)
    c: Vertical(g0)
    c: Vertical(g2)
    c: Horizontal(g1)
    c: Horizontal(g3)
    c: Coincident(g0,g-1)
    c: Coincident(g1,g-5)
FEATURE [PartDesign::Pad] Pad587
  BaseFeature = -> Pad586
  Direction = (0,0,-1)
  Length = 1
  Length2 = 10
  Profile = -> Sketch880
  ReferenceAxis = -> Sketch880 [N_Axis]
  Refine = true
  Suppressed = false
  Type = 0
FEATURE [Sketcher::SketchObject] Sketch881
  ArcFitTolerance = 1e-06
  AttachmentSupport = -> [Pad587]
  ExternalGeometry = -> [Pad587]
  FullyConstrained = true
  MakeInternals = false
  MapMode = 5
  Placement = pos=(31.6,0,0) rot=(0.57735,0.57735,0.57735;2.0944rad)
  sketch-geometry (4):
    g0: LineSegment StartX=7.95 StartY=0 StartZ=0 EndX=7.95 EndY=-1.4 EndZ=0
    g1: LineSegment StartX=7.95 StartY=-1.4 StartZ=0 EndX=13.75 EndY=-1.4 EndZ=0
    g2: LineSegment StartX=13.75 StartY=-1.4 StartZ=0 EndX=13.75 EndY=0 EndZ=0
    g3: LineSegment StartX=13.75 StartY=0 StartZ=0 EndX=7.95 EndY=0 EndZ=0
  constraints (12):
    c: Coincident(g0,g1)
    c: Coincident(g1,g2)
    c: Coincident(g2,g3)
    c: Coincident(g3,g0)
    c: Vertical(g0)
    c: Vertical(g2)
    c: Horizontal(g1)
    c: Horizontal(g3)
    c: PointOnObject(g0,g-1)
    c: DistanceX(g1,g1) = 5.8
    c: DistanceY(g0,g0) = 1.4
    c: DistanceX(g2,g-3) = 5.05
FEATURE [PartDesign::Pad] Pad588
  BaseFeature = -> Pad587
  Direction = (1,0,0)
  Length = 1.9
  Length2 = 10
  Profile = -> Sketch881
  ReferenceAxis = -> Sketch881 [N_Axis]
  Refine = true
  Suppressed = false
  Type = 0
FEATURE [Sketcher::SketchObject] Sketch882
  ArcFitTolerance = 1e-06
  AttachmentSupport = -> [Pad588]
  ExternalGeometry = -> [Pad588]
  FullyConstrained = true
  MakeInternals = false
  MapMode = 5
  Placement = pos=(0,0,1e-16) rot=(0,0,1;0rad)
  sketch-geometry (8):
    g0: LineSegment StartX=1.5 StartY=19.7 StartZ=0 EndX=24.5 EndY=19.7 EndZ=0
    g1: LineSegment StartX=24.5 StartY=19.7 StartZ=0 EndX=24.5 EndY=17.3 EndZ=0
    g2: LineSegment StartX=24.5 StartY=17.3 StartZ=0 EndX=30.1 EndY=17.3 EndZ=0
    g3: LineSegment StartX=30.1 StartY=17.3 StartZ=0 EndX=30.1 EndY=4.4 EndZ=0
    g4: LineSegment StartX=30.1 StartY=4.4 StartZ=0 EndX=24.5 EndY=4.4 EndZ=0
    g5: LineSegment StartX=24.5 StartY=4.4 StartZ=0 EndX=24.5 EndY=2 EndZ=0
    g6: LineSegment StartX=24.5 StartY=2 StartZ=0 EndX=1.5 EndY=2 EndZ=0
    g7: LineSegment StartX=1.5 StartY=19.7 StartZ=0 EndX=1.5 EndY=2 EndZ=0
  constraints (24):
    c: Horizontal(g0)
    c: Coincident(g1,g0)
    c: Vertical(g1)
    c: Coincident(g2,g1)
    c: Horizontal(g2)
    c: Coincident(g3,g2)
    c: Vertical(g3)
    c: Coincident(g4,g3)
    c: Horizontal(g4)
    c: Coincident(g5,g4)
    c: Vertical(g5)
    c: Coincident(g6,g5)
    c: Horizontal(g6)
    c: Coincident(g7,g0)
    c: Coincident(g7,g6)
    c: Vertical(g7)
    c: DistanceX(g-8,g0) = 1.5
    c: DistanceX(g2,g-4) = 1.5
    c: DistanceX(g1,g-3) = 1.5
    c: DistanceX(g4,g-6) = 1.5
    c: DistanceY(g0,g-8) = 2
    c: DistanceY(g-7,g5) = 2
    c: DistanceY(g-6,g4) = 1.5
    c: DistanceY(g1,g-3) = 1.5
FEATURE [PartDesign::Pocket] Pocket407
  BaseFeature = -> Pad588
  Direction = (0,0,-1)
  Length = 3
  Length2 = 5
  Profile = -> Sketch882
  ReferenceAxis = -> Sketch882 [N_Axis]
  Refine = true
  Suppressed = false
  Type = 0
FEATURE [Sketcher::SketchObject] Sketch883
  ArcFitTolerance = 1e-06
  AttachmentSupport = -> [Pocket407]
  ExternalGeometry = -> [Pocket407]
  FullyConstrained = true
  MakeInternals = false
  MapMode = 5
  Placement = pos=(0,0,-3) rot=(0,0,1;0rad)
  sketch-geometry (4):
    g0: LineSegment StartX=1.5 StartY=19.7 StartZ=0 EndX=1.5 EndY=2 EndZ=0
    g1: LineSegment StartX=1.5 StartY=2 StartZ=0 EndX=24.5 EndY=2 EndZ=0
    g2: LineSegment StartX=24.5 StartY=2 StartZ=0 EndX=24.5 EndY=19.7 EndZ=0
    g3: LineSegment StartX=24.5 StartY=19.7 StartZ=0 EndX=1.5 EndY=19.7 EndZ=0
  constraints (10):
    c: Coincident(g0,g1)
    c: Coincident(g1,g2)
    c: Coincident(g2,g3)
    c: Coincident(g3,g0)
    c: Vertical(g0)
    c: Vertical(g2)
    c: Horizontal(g1)
    c: Horizontal(g3)
    c: Coincident(g0,g-4)
    c: Coincident(g1,g-5)
FEATURE [PartDesign::Pocket] Pocket408
  BaseFeature = -> Pocket407
  Direction = (0,0,-1)
  Length = 1
  Length2 = 5
  Profile = -> Sketch883
  ReferenceAxis = -> Sketch883 [N_Axis]
  Refine = true
  Suppressed = false
  Type = 0
FEATURE [PartDesign::Chamfer] Chamfer036
  Angle = 45
  Base = -> Pocket408 [Edge58,Edge54,Edge56,Edge47,Edge49,Edge51]
  BaseFeature = -> Pocket408
  ChamferType = 0
  FlipDirection = false
  Refine = true
  Size = 0.5
  Size2 = 1
  SupportTransform = false
  Suppressed = false
  UseAllEdges = false
FEATURE [PartDesign::Chamfer] Chamfer037
  Angle = 45
  Base = -> Chamfer036 [Edge34]
  BaseFeature = -> Chamfer036
  ChamferType = 0
  FlipDirection = false
  Refine = true
  Size = 0.999
  Size2 = 1
  SupportTransform = false
  Suppressed = false
  UseAllEdges = false
FEATURE [Sketcher::SketchObject] Sketch884
  ArcFitTolerance = 1e-06
  AttachmentSupport = -> [Chamfer037]
  ExternalGeometry = -> [Chamfer037]
  FullyConstrained = true
  MakeInternals = false
  MapMode = 5
  Placement = pos=(0,0,0) rot=(0.57735,-0.57735,-0.57735;2.0944rad)
  sketch-geometry (2):
    g0: ArcOfCircle CenterX=-10.85 CenterY=1e-16 CenterZ=0 NormalX=0 NormalY=0 NormalZ=1 AngleXU=0 Radius=2 StartAngle=3.14159 EndAngle=6.28319
    g1: LineSegment StartX=-12.85 StartY=3e-16 StartZ=0 EndX=-8.85 EndY=-4e-16 EndZ=0
  constraints (8):
    c: PointOnObject(g0,g-3)
    c: PointOnObject(g0,g-3)
    c: Radius(g0) = 2
    c: PointOnObject(g0,g-3)
    c: DistanceX(g-3,g-3) = 21.7
    c: DistanceX(g-3,g0) = 8.85
    c: Coincident(g1,g0)
    c: Coincident(g1,g0)
FEATURE [PartDesign::Pocket] Pocket409
  BaseFeature = -> Chamfer037
  Direction = (1,0,0)
  Length = 1.5
  Length2 = 5
  Profile = -> Sketch884
  ReferenceAxis = -> Sketch884 [N_Axis]
  Refine = true
  Suppressed = false
  Type = 0
FEATURE [Sketcher::SketchObject] Sketch885
  ArcFitTolerance = 1e-06
  AttachmentSupport = -> [Pocket409]
  ExternalGeometry = -> [Pocket409]
  FullyConstrained = true
  MakeInternals = false
  MapMode = 5
  Placement = pos=(0,0,-4) rot=(0,0,1;0rad)
  sketch-geometry (9):
    g0: LineSegment StartX=1.5 StartY=8.6 StartZ=0 EndX=1.5 EndY=7.3 EndZ=0
    g1: LineSegment StartX=1.5 StartY=7.3 StartZ=0 EndX=14.5 EndY=7.3 EndZ=0
    g2: LineSegment StartX=14.5 StartY=7.3 StartZ=0 EndX=14.5 EndY=8.6 EndZ=0
    g3: LineSegment StartX=14.5 StartY=8.6 StartZ=0 EndX=1.5 EndY=8.6 EndZ=0
    g4: LineSegment StartX=1.5 StartY=14.4 StartZ=0 EndX=1.5 EndY=13.1 EndZ=0
    g5: LineSegment StartX=1.5 StartY=13.1 StartZ=0 EndX=14.5 EndY=13.1 EndZ=0
    g6: LineSegment StartX=14.5 StartY=13.1 StartZ=0 EndX=14.5 EndY=14.4 EndZ=0
    g7: LineSegment StartX=14.5 StartY=14.4 StartZ=0 EndX=1.5 EndY=14.4 EndZ=0
    g8: LineSegment [constr] StartX=14.5 StartY=13.1 StartZ=0 EndX=14.5 EndY=8.6 EndZ=0
  constraints (26):
    c: Coincident(g0,g1)
    c: Coincident(g1,g2)
    c: Coincident(g2,g3)
    c: Coincident(g3,g0)
    c: Vertical(g0)
    c: Vertical(g2)
    c: Horizontal(g1)
    c: Horizontal(g3)
    c: PointOnObject(g0,g-4)
    c: Coincident(g4,g5)
    c: Coincident(g5,g6)
    c: Coincident(g6,g7)
    c: Coincident(g7,g4)
    c: Vertical(g4)
    c: Vertical(g6)
    c: Horizontal(g5)
    c: Horizontal(g7)
    c: PointOnObject(g4,g-3)
    c: Coincident(g8,g5)
    c: Coincident(g8,g2)
    c: Vertical(g8)
    c: DistanceY(g8,g8) = 4.5
    c: DistanceY(g6,g6) = 1.3
    c: DistanceY(g2,g2) = 1.3
    c: DistanceY(g2,g-6) = 0.25
    c: DistanceX(g7,g7) = 13
FEATURE [PartDesign::Pad] Pad589
  BaseFeature = -> Pocket409
  Direction = (0,0,1)
  Length = 6
  Length2 = 10
  Profile = -> Sketch885
  ReferenceAxis = -> Sketch885 [N_Axis]
  Refine = true
  Suppressed = false
  Type = 0
FEATURE [Sketcher::SketchObject] Sketch886
  ArcFitTolerance = 1e-06
  AttachmentSupport = -> [Pad589]
  ExternalGeometry = -> [Pad589]
  FullyConstrained = true
  MakeInternals = false
  MapMode = 5
  Placement = pos=(0,7.3,0) rot=(1,0,0;1.5708rad)
  sketch-geometry (3):
    g0: LineSegment StartX=1.5 StartY=0 StartZ=0 EndX=1.5 EndY=2 EndZ=0
    g1: LineSegment StartX=1.5 StartY=2 StartZ=0 EndX=2.22794 EndY=2 EndZ=0
    g2: LineSegment StartX=2.22794 StartY=2 StartZ=0 EndX=1.5 EndY=0 EndZ=0
  constraints (7):
    c: Coincident(g0,g-3)
    c: Coincident(g0,g-4)
    c: Coincident(g1,g0)
    c: PointOnObject(g1,g-4)
    c: Coincident(g2,g1)
    c: Coincident(g2,g0)
    c: Angle(g2,g0) = 0.349066
FEATURE [PartDesign::Pocket] Pocket410
  BaseFeature = -> Pad589
  Direction = (0,1,-2e-16)
  Length = 8
  Length2 = 5
  Profile = -> Sketch886
  ReferenceAxis = -> Sketch886 [N_Axis]
  Refine = true
  Suppressed = false
  Type = 0
FEATURE [Sketcher::SketchObject] Sketch887
  ArcFitTolerance = 1e-06
  AttachmentSupport = -> [Pocket410]
  ExternalGeometry = -> [Pocket410]
  FullyConstrained = true
  MakeInternals = false
  MapMode = 5
  Placement = pos=(0,0,-4) rot=(0,0,1;0rad)
  sketch-geometry (6):
    g0: LineSegment StartX=1.5 StartY=11.5 StartZ=0 EndX=1.5 EndY=10.2 EndZ=0
    g1: LineSegment StartX=1.5 StartY=10.2 StartZ=0 EndX=14.5 EndY=10.2 EndZ=0
    g2: LineSegment StartX=14.5 StartY=10.2 StartZ=0 EndX=14.5 EndY=11.5 EndZ=0
    g3: LineSegment StartX=14.5 StartY=11.5 StartZ=0 EndX=1.5 EndY=11.5 EndZ=0
    g4: LineSegment [constr] StartX=14.5 StartY=11.5 StartZ=0 EndX=14.5 EndY=13.1 EndZ=0
    g5: LineSegment [constr] StartX=14.5 StartY=10.2 StartZ=0 EndX=14.5 EndY=8.6 EndZ=0
  constraints (17):
    c: Coincident(g0,g1)
    c: Coincident(g1,g2)
    c: Coincident(g2,g3)
    c: Coincident(g3,g0)
    c: Vertical(g0)
    c: Vertical(g2)
    c: Horizontal(g1)
    c: Horizontal(g3)
    c: PointOnObject(g0,g-3)
    c: Coincident(g4,g2)
    c: Coincident(g4,g-4)
    c: Vertical(g4)
    c: DistanceY(g2,g2) = 1.3
    c: Coincident(g5,g1)
    c: Coincident(g5,g-5)
    c: DistanceY(g4,g4) = 1.6
    c: DistanceY(g5,g5) = 1.6
FEATURE [PartDesign::Pad] Pad590
  BaseFeature = -> Pocket410
  Direction = (0,0,1)
  Length = 2
  Length2 = 10
  Profile = -> Sketch887
  ReferenceAxis = -> Sketch887 [N_Axis]
  Refine = true
  Suppressed = false
  Type = 0
FEATURE [Sketcher::SketchObject] Sketch888
  ArcFitTolerance = 1e-06
  AttachmentSupport = -> [Pad590]
  ExternalGeometry = -> [Pad590]
  FullyConstrained = true
  MakeInternals = false
  MapMode = 5
  Placement = pos=(0,0,-4) rot=(0,0,1;0rad)
  sketch-geometry (2):
    g0: Circle CenterX=4.85 CenterY=17.3 CenterZ=0 NormalX=0 NormalY=0 NormalZ=1 AngleXU=0 Radius=3.15
    g1: Circle CenterX=4.85 CenterY=4.4 CenterZ=0 NormalX=0 NormalY=0 NormalZ=1 AngleXU=0 Radius=3.15
  constraints (6):
    c: Radius(g1) = 3.15
    c: Radius(g0) = 3.15
    c: DistanceX(g-3,g0) = 3.35
    c: DistanceY(g0,g-3) = 2.4
    c: DistanceX(g-4,g1) = 3.35
    c: DistanceY(g-4,g1) = 2.4
FEATURE [PartDesign::Pad] Pad591
  BaseFeature = -> Pad590
  Direction = (0,0,1)
  Length = 4
  Length2 = 10
  Profile = -> Sketch888
  ReferenceAxis = -> Sketch888 [N_Axis]
  Refine = true
  Suppressed = false
  Type = 0
FEATURE [Sketcher::SketchObject] Sketch889
  ArcFitTolerance = 1e-06
  AttachmentSupport = -> [Pad591]
  ExternalGeometry = -> [Pad591]
  FullyConstrained = true
  MakeInternals = false
  MapMode = 5
  Placement = pos=(0,0,2e-16) rot=(0,0,1;0rad)
  sketch-geometry (8):
    g0: LineSegment StartX=1.5 StartY=19.7 StartZ=0 EndX=2.80978 EndY=19.7 EndZ=0
    g1: LineSegment StartX=1.5 StartY=19.7 StartZ=0 EndX=1.5 EndY=15.7 EndZ=0
    g2: LineSegment StartX=1.5 StartY=15.7 StartZ=0 EndX=2.13661 EndY=15.7 EndZ=0
    g3: ArcOfCircle CenterX=4.85 CenterY=17.3 CenterZ=0 NormalX=0 NormalY=0 NormalZ=1 AngleXU=0 Radius=3.15 StartAngle=2.27534 EndAngle=3.67438
    g4: LineSegment StartX=2.80978 StartY=2 StartZ=0 EndX=1.5 EndY=2 EndZ=0
    g5: LineSegment StartX=1.5 StartY=2 StartZ=0 EndX=1.5 EndY=6 EndZ=0
    g6: LineSegment StartX=1.5 StartY=6 StartZ=0 EndX=2.13661 EndY=6 EndZ=0
    g7: ArcOfCircle CenterX=4.85002 CenterY=4.4 CenterZ=0 NormalX=0 NormalY=0 NormalZ=1 AngleXU=0 Radius=3.15001 StartAngle=2.60881 EndAngle=4.00784
  constraints (22):
    c: Coincident(g0,g-5)
    c: Coincident(g0,g-4)
    c: Coincident(g1,g0)
    c: PointOnObject(g1,g-5)
    c: Coincident(g2,g1)
    c: PointOnObject(g2,g-4)
    c: Horizontal(g2)
    c: Coincident(g3,g2)
    c: Coincident(g3,g0)
    c: Tangent(g3,g-4)
    c: DistanceY(g1,g1) = 4
    c: Coincident(g4,g-7)
    c: Coincident(g4,g-8)
    c: Coincident(g5,g4)
    c: PointOnObject(g5,g-8)
    c: DistanceY(g5,g5) = 4
    c: Coincident(g6,g5)
    c: PointOnObject(g6,g-7)
    c: Horizontal(g6)
    c: Coincident(g7,g4)
    c: Coincident(g7,g6)
    c: Tangent(g7,g-7)
FEATURE [PartDesign::Pad] Pad592
  BaseFeature = -> Pad591
  Direction = (0,0,1)
  Length = 4
  Length2 = 10
  Profile = -> Sketch889
  ReferenceAxis = -> Sketch889 [N_Axis]
  Refine = true
  Reversed = true
  Suppressed = false
  Type = 0
FEATURE [Sketcher::SketchObject] Sketch890
  ArcFitTolerance = 1e-06
  AttachmentSupport = -> [Pad592]
  ExternalGeometry = -> [Pad592]
  FullyConstrained = true
  MakeInternals = false
  MapMode = 5
  Placement = pos=(0,0,2e-16) rot=(0,0,1;0rad)
  sketch-geometry (2):
    g0: Circle CenterX=4.85 CenterY=17.3 CenterZ=0 NormalX=0 NormalY=0 NormalZ=1 AngleXU=0 Radius=2.15
    g1: Circle CenterX=4.85 CenterY=4.4 CenterZ=0 NormalX=0 NormalY=0 NormalZ=1 AngleXU=0 Radius=2.15
  constraints (4):
    c: Coincident(g0,g-3)
    c: Radius(g0) = 2.15
    c: Coincident(g1,g-4)
    c: Radius(g1) = 2.15
FEATURE [PartDesign::Pocket] Pocket411
  BaseFeature = -> Pad592
  Direction = (0,0,-1)
  Length = 0.6
  Length2 = 5
  Profile = -> Sketch890
  ReferenceAxis = -> Sketch890 [N_Axis]
  Refine = true
  Suppressed = false
  Type = 0
FEATURE [Sketcher::SketchObject] Sketch891
  ArcFitTolerance = 1e-06
  AttachmentSupport = -> [Pocket411]
  ExternalGeometry = -> [Pocket411]
  FullyConstrained = true
  MakeInternals = false
  MapMode = 5
  Placement = pos=(0,0,-0.6) rot=(0,0,1;0rad)
  sketch-geometry (2):
    g0: Circle CenterX=4.85 CenterY=17.3 CenterZ=0 NormalX=0 NormalY=0 NormalZ=1 AngleXU=0 Radius=1
    g1: Circle CenterX=4.85 CenterY=4.4 CenterZ=0 NormalX=0 NormalY=0 NormalZ=1 AngleXU=0 Radius=1
  constraints (4):
    c: Coincident(g0,g-3)
    c: Radius(g0) = 1
    c: Coincident(g1,g-4)
    c: Radius(g1) = 1
FEATURE [PartDesign::Pocket] Pocket412
  BaseFeature = -> Pocket411
  Direction = (0,0,-1)
  Length = 5
  Length2 = 5
  Profile = -> Sketch891
  ReferenceAxis = -> Sketch891 [N_Axis]
  Refine = true
  Suppressed = false
  Type = 1
FEATURE [Sketcher::SketchObject] Sketch892
  ArcFitTolerance = 1e-06
  AttachmentSupport = -> [Pocket412]
  ExternalGeometry = -> [Pocket412]
  FullyConstrained = true
  MakeInternals = false
  MapMode = 5
  Placement = pos=(0,0,-4) rot=(0,0,1;0rad)
  sketch-geometry (10):
    g0: LineSegment StartX=17 StartY=13.35 StartZ=0 EndX=23.1 EndY=13.35 EndZ=0
    g1: LineSegment StartX=23.1 StartY=13.35 StartZ=0 EndX=23.1 EndY=14.85 EndZ=0
    g2: LineSegment StartX=23.1 StartY=14.85 StartZ=0 EndX=17 EndY=14.85 EndZ=0
    g3: LineSegment StartX=17 StartY=14.85 StartZ=0 EndX=17 EndY=13.35 EndZ=0
    g4: LineSegment StartX=17 StartY=8.35 StartZ=0 EndX=17 EndY=6.85 EndZ=0
    g5: LineSegment StartX=17 StartY=6.85 StartZ=0 EndX=23.1 EndY=6.85 EndZ=0
    g6: LineSegment StartX=23.1 StartY=6.85 StartZ=0 EndX=23.1 EndY=8.35 EndZ=0
    g7: LineSegment StartX=23.1 StartY=8.35 StartZ=0 EndX=17 EndY=8.35 EndZ=0
    g8: LineSegment [constr] StartX=23.1 StartY=13.35 StartZ=0 EndX=23.1 EndY=8.35 EndZ=0
    g9: LineSegment [constr] StartX=17 StartY=13.35 StartZ=0 EndX=17 EndY=8.35 EndZ=0
  constraints (29):
    c: Coincident(g0,g1)
    c: Coincident(g1,g2)
    c: Coincident(g2,g3)
    c: Coincident(g3,g0)
    c: Horizontal(g0)
    c: Horizontal(g2)
    c: Vertical(g1)
    c: Vertical(g3)
    c: Coincident(g4,g5)
    c: Coincident(g5,g6)
    c: Coincident(g6,g7)
    c: Coincident(g7,g4)
    c: Vertical(g4)
    c: Vertical(g6)
    c: Horizontal(g5)
    c: Horizontal(g7)
    c: Coincident(g8,g0)
    c: Coincident(g8,g6)
    c: Coincident(g9,g0)
    c: Coincident(g9,g4)
    c: Vertical(g9)
    c: Vertical(g8)
    c: DistanceY(g3,g3) = 1.5
    c: DistanceY(g9,g9) = 5
    c: DistanceY(g4,g4) = 1.5
    c: DistanceY(g-4,g-3) = 4.5
    c: DistanceY(g-3,g0) = 0.25
    c: DistanceX(g-3,g0) = 2.5
    c: DistanceX(g2,g2) = 6.1
FEATURE [PartDesign::Pad] Pad593
  BaseFeature = -> Pocket412
  Direction = (0,0,1)
  Length = 9
  Length2 = 10
  Profile = -> Sketch892
  ReferenceAxis = -> Sketch892 [N_Axis]
  Refine = true
  Suppressed = false
  Type = 0
FEATURE [Sketcher::SketchObject] Sketch893
  ArcFitTolerance = 1e-06
  AttachmentSupport = -> [Pad593]
  ExternalGeometry = -> [Pad593]
  FullyConstrained = true
  MakeInternals = false
  MapMode = 5
  Placement = pos=(0,6.85,0) rot=(1,0,0;1.5708rad)
  sketch-geometry (7):
    g0: LineSegment StartX=19 StartY=5 StartZ=0 EndX=21.1 EndY=5 EndZ=0
    g1: LineSegment StartX=21.1 StartY=5 StartZ=0 EndX=21.1 EndY=3.05 EndZ=0
    g2: LineSegment StartX=19 StartY=5 StartZ=0 EndX=19 EndY=3.05 EndZ=0
    g3: ArcOfCircle CenterX=20.05 CenterY=3.05 CenterZ=0 NormalX=0 NormalY=0 NormalZ=1 AngleXU=0 Radius=1.05 StartAngle=3.14159 EndAngle=6.28319
    g4: LineSegment [constr] StartX=20.05 StartY=3.05 StartZ=0 EndX=19 EndY=3.05 EndZ=0
    g5: LineSegment [constr] StartX=20.05 StartY=3.05 StartZ=0 EndX=21.1 EndY=3.05 EndZ=0
    g6: LineSegment [constr] StartX=20.05 StartY=3.05 StartZ=0 EndX=20.05 EndY=2 EndZ=0
  constraints (21):
    c: PointOnObject(g0,g-3)
    c: PointOnObject(g0,g-3)
    c: Coincident(g1,g0)
    c: Vertical(g1)
    c: Coincident(g2,g0)
    c: Vertical(g2)
    c: Coincident(g3,g2)
    c: Coincident(g3,g1)
    c: Coincident(g4,g3)
    c: Coincident(g4,g2)
    c: Coincident(g5,g3)
    c: Coincident(g5,g1)
    c: Horizontal(g4)
    c: Horizontal(g5)
    c: DistanceX(g0,g0) = 2.1
    c: DistanceX(g-3,g-3) = 6.1
    c: DistanceX(g-3,g0) = 2
    c: Coincident(g6,g3)
    c: PointOnObject(g6,g3)
    c: Vertical(g6)
    c: DistanceY(g6,g0) = 3
FEATURE [PartDesign::Pocket] Pocket413
  BaseFeature = -> Pad593
  Direction = (0,1,-2e-16)
  Length = 5
  Length2 = 5
  Profile = -> Sketch893
  ReferenceAxis = -> Sketch893 [N_Axis]
  Refine = true
  Suppressed = false
  Type = 1
FEATURE [Sketcher::SketchObject] Sketch894
  ArcFitTolerance = 1e-06
  AttachmentSupport = -> [Pocket413]
  ExternalGeometry = -> [Pocket413]
  FullyConstrained = true
  MakeInternals = false
  MapMode = 5
  Placement = pos=(0,0,-5.5) rot=(1,0,0;3.14159rad)
  sketch-geometry (2):
    g0: Circle CenterX=4.85 CenterY=-4.4 CenterZ=0 NormalX=0 NormalY=0 NormalZ=1 AngleXU=0 Radius=2.2
    g1: Circle CenterX=4.85 CenterY=-17.3 CenterZ=0 NormalX=0 NormalY=0 NormalZ=1 AngleXU=0 Radius=2.2
  constraints (4):
    c: Coincident(g0,g-3)
    c: Coincident(g1,g-4)
    c: Diameter(g1) = 4.4
    c: Diameter(g0) = 4.4
FEATURE [PartDesign::Pocket] Pocket414
  BaseFeature = -> Pocket413
  Direction = (0,0,1)
  Length = 3
  Length2 = 5
  Profile = -> Sketch894
  ReferenceAxis = -> Sketch894 [N_Axis]
  Refine = true
  Suppressed = false
  Type = 0
FEATURE [Sketcher::SketchObject] Sketch895
  ArcFitTolerance = 1e-06
  AttachmentSupport = -> [Pocket414]
  ExternalGeometry = -> [Pocket414]
  FullyConstrained = true
  MakeInternals = false
  MapMode = 5
  Placement = pos=(0,0,-5.5) rot=(1,0,0;3.14159rad)
  sketch-geometry (4):
    g0: LineSegment StartX=9.7 StartY=0.8 StartZ=0 EndX=9.7 EndY=-22.5 EndZ=0
    g1: LineSegment StartX=9.7 StartY=-22.5 StartZ=0 EndX=14.2 EndY=-22.5 EndZ=0
    g2: LineSegment StartX=14.2 StartY=-22.5 StartZ=0 EndX=14.2 EndY=0.8 EndZ=0
    g3: LineSegment StartX=14.2 StartY=0.8 StartZ=0 EndX=9.7 EndY=0.8 EndZ=0
  constraints (12):
    c: Coincident(g0,g1)
    c: Coincident(g1,g2)
    c: Coincident(g2,g3)
    c: Coincident(g3,g0)
    c: Vertical(g0)
    c: Vertical(g2)
    c: Horizontal(g1)
    c: Horizontal(g3)
    c: DistanceX(g1,g1) = 4.5
    c: DistanceX(g-3,g0) = 9.7
    c: DistanceY(g0,g-3) = 0.8
    c: DistanceY(g0,g0) = 23.3
FEATURE [PartDesign::Pad] Pad594
  BaseFeature = -> Pocket414
  Direction = (0,0,-1)
  Length = 0.8
  Length2 = 10
  Profile = -> Sketch895
  ReferenceAxis = -> Sketch895 [N_Axis]
  Refine = true
  Suppressed = false
  Type = 0
FEATURE [Sketcher::SketchObject] Sketch896
  ArcFitTolerance = 1e-06
  AttachmentSupport = -> [Pad594]
  ExternalGeometry = -> [Pad594]
  FullyConstrained = true
  MakeInternals = false
  MapMode = 5
  Placement = pos=(0,0,0) rot=(1,0,0;1.5708rad)
  sketch-geometry (4):
    g0: LineSegment StartX=9.7 StartY=-5.5 StartZ=0 EndX=14.2 EndY=-5.5 EndZ=0
    g1: LineSegment StartX=14.2 StartY=-5.5 StartZ=0 EndX=14.2 EndY=0 EndZ=0
    g2: LineSegment StartX=14.2 StartY=0 StartZ=0 EndX=9.7 EndY=0 EndZ=0
    g3: LineSegment StartX=9.7 StartY=0 StartZ=0 EndX=9.7 EndY=-5.5 EndZ=0
  constraints (10):
    c: Coincident(g0,g1)
    c: Coincident(g1,g2)
    c: Coincident(g2,g3)
    c: Coincident(g3,g0)
    c: Horizontal(g2)
    c: Vertical(g1)
    c: Vertical(g3)
    c: Coincident(g0,g-3)
    c: PointOnObject(g1,g-4)
    c: Coincident(g0,g-3)
FEATURE [PartDesign::Pad] Pad595
  BaseFeature = -> Pad594
  Direction = (0,-1,2e-16)
  Length = 0.8
  Length2 = 10
  Profile = -> Sketch896
  ReferenceAxis = -> Sketch896 [N_Axis]
  Refine = true
  Suppressed = false
  Type = 0
FEATURE [Sketcher::SketchObject] Sketch897
  ArcFitTolerance = 1e-06
  AttachmentSupport = -> [Pad595]
  ExternalGeometry = -> [Pad595]
  FullyConstrained = true
  MakeInternals = false
  MapMode = 5
  Placement = pos=(0,21.7,0) rot=(0,0.707107,0.707107;3.14159rad)
  sketch-geometry (4):
    g0: LineSegment StartX=-9.7 StartY=-5.5 StartZ=0 EndX=-9.7 EndY=0 EndZ=0
    g1: LineSegment StartX=-9.7 StartY=0 StartZ=0 EndX=-14.2 EndY=0 EndZ=0
    g2: LineSegment StartX=-14.2 StartY=0 StartZ=0 EndX=-14.2 EndY=-5.5 EndZ=0
    g3: LineSegment StartX=-14.2 StartY=-5.5 StartZ=0 EndX=-9.7 EndY=-5.5 EndZ=0
  constraints (10):
    c: Coincident(g0,g1)
    c: Coincident(g1,g2)
    c: Coincident(g2,g3)
    c: Coincident(g3,g0)
    c: Vertical(g0)
    c: Vertical(g2)
    c: Horizontal(g1)
    c: Coincident(g0,g-3)
    c: PointOnObject(g1,g-4)
    c: Coincident(g2,g-3)
FEATURE [PartDesign::Pad] Pad596
  BaseFeature = -> Pad595
  Direction = (0,1,-2e-16)
  Length = 0.8
  Length2 = 10
  Profile = -> Sketch897
  ReferenceAxis = -> Sketch897 [N_Axis]
  Refine = true
  Suppressed = false
  Type = 0
FEATURE [Sketcher::SketchObject] Sketch898
  ArcFitTolerance = 1e-06
  AttachmentSupport = -> [Pad596]
  ExternalGeometry = -> [Pad596]
  FullyConstrained = true
  MakeInternals = false
  MapMode = 5
  Placement = pos=(0,0,-5.5) rot=(1,0,0;3.14159rad)
  sketch-geometry (12):
    g0: LineSegment StartX=14.2 StartY=0 StartZ=0 EndX=14.2 EndY=-21.7 EndZ=0
    g1: LineSegment StartX=14.2 StartY=-21.7 StartZ=0 EndX=15.7 EndY=-21.7 EndZ=0
    g2: LineSegment StartX=15.7 StartY=-21.7 StartZ=0 EndX=15.7 EndY=0 EndZ=0
    g3: LineSegment StartX=15.7 StartY=0 StartZ=0 EndX=14.2 EndY=0 EndZ=0
    g4: LineSegment StartX=17.7 StartY=-21.7 StartZ=0 EndX=19.2 EndY=-21.7 EndZ=0
    g5: LineSegment StartX=19.2 StartY=-21.7 StartZ=0 EndX=19.2 EndY=0 EndZ=0
    g6: LineSegment StartX=19.2 StartY=0 StartZ=0 EndX=17.7 EndY=0 EndZ=0
    g7: LineSegment StartX=17.7 StartY=0 StartZ=0 EndX=17.7 EndY=-21.7 EndZ=0
    g8: LineSegment StartX=21.2 StartY=0 StartZ=0 EndX=21.2 EndY=-21.7 EndZ=0
    g9: LineSegment StartX=21.2 StartY=-21.7 StartZ=0 EndX=22.7 EndY=-21.7 EndZ=0
    g10: LineSegment StartX=22.7 StartY=-21.7 StartZ=0 EndX=22.7 EndY=0 EndZ=0
    g11: LineSegment StartX=22.7 StartY=0 StartZ=0 EndX=21.2 EndY=0 EndZ=0
  constraints (36):
    c: Coincident(g0,g1)
    c: Coincident(g1,g2)
    c: Coincident(g2,g3)
    c: Coincident(g3,g0)
    c: Vertical(g0)
    c: Vertical(g2)
    c: Horizontal(g1)
    c: Horizontal(g3)
    c: Coincident(g0,g-5)
    c: PointOnObject(g1,g-4)
    c: Coincident(g4,g5)
    c: Coincident(g5,g6)
    c: Coincident(g6,g7)
    c: Coincident(g7,g4)
    c: Horizontal(g4)
    c: Horizontal(g6)
    c: Vertical(g5)
    c: Vertical(g7)
    c: PointOnObject(g4,g-4)
    c: PointOnObject(g5,g-5)
    c: Coincident(g8,g9)
    c: Coincident(g9,g10)
    c: Coincident(g10,g11)
    c: Coincident(g11,g8)
    c: Vertical(g8)
    c: Vertical(g10)
    c: Horizontal(g9)
    c: Horizontal(g11)
    c: PointOnObject(g8,g-5)
    c: PointOnObject(g9,g-4)
    c: DistanceX(g1,g1) = 1.5
    c: DistanceX(g-4,g-4) = 11.8
    c: DistanceX(g1,g4) = 2
    c: DistanceX(g4,g4) = 1.5
    c: DistanceX(g4,g8) = 2
    c: DistanceX(g9,g9) = 1.5
FEATURE [PartDesign::Pocket] Pocket415
  BaseFeature = -> Pad596
  Direction = (0,0,1)
  Length = 0.5
  Length2 = 5
  Profile = -> Sketch898
  ReferenceAxis = -> Sketch898 [N_Axis]
  Refine = true
  Suppressed = false
  Type = 0
FEATURE [Sketcher::SketchObject] Sketch899
  ArcFitTolerance = 1e-06
  AttachmentSupport = -> [Pocket415]
  ExternalGeometry = -> [Pocket415]
  FullyConstrained = true
  MakeInternals = false
  MapMode = 5
  Placement = pos=(0,21.7,0) rot=(0,0.707107,0.707107;3.14159rad)
  sketch-geometry (12):
    g0: LineSegment StartX=-15.7 StartY=-5 StartZ=0 EndX=-14.2 EndY=-5 EndZ=0
    g1: LineSegment StartX=-14.2 StartY=-5 StartZ=0 EndX=-14.2 EndY=0 EndZ=0
    g2: LineSegment StartX=-14.2 StartY=0 StartZ=0 EndX=-15.7 EndY=0 EndZ=0
    g3: LineSegment StartX=-15.7 StartY=0 StartZ=0 EndX=-15.7 EndY=-5 EndZ=0
    g4: LineSegment StartX=-19.2 StartY=-5 StartZ=0 EndX=-17.7 EndY=-5 EndZ=0
    g5: LineSegment StartX=-17.7 StartY=-5 StartZ=0 EndX=-17.7 EndY=0 EndZ=0
    g6: LineSegment StartX=-17.7 StartY=0 StartZ=0 EndX=-19.2 EndY=0 EndZ=0
    g7: LineSegment StartX=-19.2 StartY=0 StartZ=0 EndX=-19.2 EndY=-5 EndZ=0
    g8: LineSegment StartX=-22.7 StartY=-5 StartZ=0 EndX=-21.2 EndY=-5 EndZ=0
    g9: LineSegment StartX=-21.2 StartY=-5 StartZ=0 EndX=-21.2 EndY=0 EndZ=0
    g10: LineSegment StartX=-21.2 StartY=0 StartZ=0 EndX=-22.7 EndY=0 EndZ=0
    g11: LineSegment StartX=-22.7 StartY=0 StartZ=0 EndX=-22.7 EndY=-5 EndZ=0
  constraints (30):
    c: Coincident(g0,g1)
    c: Coincident(g1,g2)
    c: Coincident(g2,g3)
    c: Coincident(g3,g0)
    c: Horizontal(g0)
    c: Horizontal(g2)
    c: Vertical(g1)
    c: Vertical(g3)
    c: Coincident(g0,g-3)
    c: Coincident(g1,g-6)
    c: Coincident(g4,g5)
    c: Coincident(g5,g6)
    c: Coincident(g6,g7)
    c: Coincident(g7,g4)
    c: Horizontal(g6)
    c: Vertical(g5)
    c: Vertical(g7)
    c: Coincident(g4,g-4)
    c: PointOnObject(g5,g-6)
    c: Coincident(g8,g9)
    c: Coincident(g9,g10)
    c: Coincident(g10,g11)
    c: Coincident(g11,g8)
    c: Horizontal(g10)
    c: Vertical(g9)
    c: Vertical(g11)
    c: Coincident(g8,g-5)
    c: PointOnObject(g9,g-6)
    c: Coincident(g8,g-5)
    c: Coincident(g-4,g4)
FEATURE [PartDesign::Pocket] Pocket416
  BaseFeature = -> Pocket415
  Direction = (0,-1,2e-16)
  Length = 0.5
  Length2 = 5
  Profile = -> Sketch899
  ReferenceAxis = -> Sketch899 [N_Axis]
  Refine = true
  Suppressed = false
  Type = 0
FEATURE [Sketcher::SketchObject] Sketch900
  ArcFitTolerance = 1e-06
  AttachmentSupport = -> [Pocket416]
  ExternalGeometry = -> [Pocket416]
  FullyConstrained = true
  MakeInternals = false
  MapMode = 5
  Placement = pos=(0,0,0) rot=(1,0,0;1.5708rad)
  sketch-geometry (12):
    g0: LineSegment StartX=21.2 StartY=-5 StartZ=0 EndX=22.7 EndY=-5 EndZ=0
    g1: LineSegment StartX=22.7 StartY=-5 StartZ=0 EndX=22.7 EndY=0 EndZ=0
    g2: LineSegment StartX=22.7 StartY=0 StartZ=0 EndX=21.2 EndY=0 EndZ=0
    g3: LineSegment StartX=21.2 StartY=0 StartZ=0 EndX=21.2 EndY=-5 EndZ=0
    g4: LineSegment StartX=17.7 StartY=-5 StartZ=0 EndX=19.2 EndY=-5 EndZ=0
    g5: LineSegment StartX=19.2 StartY=-5 StartZ=0 EndX=19.2 EndY=0 EndZ=0
    g6: LineSegment StartX=19.2 StartY=0 StartZ=0 EndX=17.7 EndY=0 EndZ=0
    g7: LineSegment StartX=17.7 StartY=0 StartZ=0 EndX=17.7 EndY=-5 EndZ=0
    g8: LineSegment StartX=15.7 StartY=-5 StartZ=0 EndX=15.7 EndY=0 EndZ=0
    g9: LineSegment StartX=15.7 StartY=0 StartZ=0 EndX=14.2 EndY=0 EndZ=0
    g10: LineSegment StartX=14.2 StartY=0 StartZ=0 EndX=14.2 EndY=-5 EndZ=0
    g11: LineSegment StartX=14.2 StartY=-5 StartZ=0 EndX=15.7 EndY=-5 EndZ=0
  constraints (30):
    c: Coincident(g0,g1)
    c: Coincident(g1,g2)
    c: Coincident(g2,g3)
    c: Coincident(g3,g0)
    c: Horizontal(g2)
    c: Vertical(g1)
    c: Vertical(g3)
    c: Coincident(g0,g-3)
    c: PointOnObject(g1,g-6)
    c: Coincident(g4,g5)
    c: Coincident(g5,g6)
    c: Coincident(g6,g7)
    c: Coincident(g7,g4)
    c: Horizontal(g6)
    c: Vertical(g5)
    c: Vertical(g7)
    c: Coincident(g4,g-4)
    c: PointOnObject(g5,g-6)
    c: Coincident(g8,g9)
    c: Coincident(g9,g10)
    c: Coincident(g10,g11)
    c: Coincident(g11,g8)
    c: Vertical(g8)
    c: Vertical(g10)
    c: Horizontal(g9)
    c: Horizontal(g11)
    c: Coincident(g8,g-5)
    c: Coincident(g9,g-6)
    c: Coincident(g4,g-4)
    c: Coincident(g0,g-3)
FEATURE [PartDesign::Pocket] Pocket417
  BaseFeature = -> Pocket416
  Direction = (0,1,-2e-16)
  Length = 0.5
  Length2 = 5
  Profile = -> Sketch900
  ReferenceAxis = -> Sketch900 [N_Axis]
  Refine = true
  Suppressed = false
  Type = 0
FEATURE [Sketcher::SketchObject] Sketch901
  ArcFitTolerance = 1e-06
  AttachmentSupport = -> [Pocket417]
  ExternalGeometry = -> [Pocket417]
  FullyConstrained = true
  MakeInternals = false
  MapMode = 5
  Placement = pos=(0,0.5,0) rot=(1,0,0;1.5708rad)
  sketch-geometry (2):
    g0: ArcOfCircle CenterX=20.2 CenterY=0 CenterZ=0 NormalX=0 NormalY=0 NormalZ=1 AngleXU=0 Radius=2.85 StartAngle=3.14159 EndAngle=6.28319
    g1: LineSegment StartX=17.35 StartY=3e-16 StartZ=0 EndX=23.05 EndY=-7e-16 EndZ=0
  constraints (7):
    c: PointOnObject(g0,g-1)
    c: PointOnObject(g0,g-1)
    c: Radius(g0) = 2.85
    c: PointOnObject(g0,g-4)
    c: DistanceX(g-3,g0) = 1.65
    c: Coincident(g1,g0)
    c: Coincident(g1,g0)
FEATURE [PartDesign::Pad] Pad597
  BaseFeature = -> Pocket417
  Direction = (0,-1,2e-16)
  Length = 1.5
  Length2 = 10
  Profile = -> Sketch901
  ReferenceAxis = -> Sketch901 [N_Axis]
  Refine = true
  Suppressed = false
  Type = 0
FEATURE [Sketcher::SketchObject] Sketch902
  ArcFitTolerance = 1e-06
  AttachmentSupport = -> [Pad597]
  ExternalGeometry = -> [Pad597]
  FullyConstrained = true
  MakeInternals = false
  MapMode = 5
  Placement = pos=(0,21.2,0) rot=(0,0.707107,0.707107;3.14159rad)
  sketch-geometry (2):
    g0: ArcOfCircle CenterX=-20.2 CenterY=-4.6e-15 CenterZ=0 NormalX=0 NormalY=0 NormalZ=1 AngleXU=0 Radius=2.85 StartAngle=3.14159 EndAngle=6.28319
    g1: LineSegment StartX=-23.05 StartY=-5.5e-15 StartZ=0 EndX=-17.35 EndY=-5.3e-15 EndZ=0
  constraints (4):
    c: Tangent(g0,g-3) = -1.5708
    c: Coincident(g0,g-3)
    c: Coincident(g1,g0)
    c: Coincident(g1,g0)
FEATURE [PartDesign::Pad] Pad598
  BaseFeature = -> Pad597
  Direction = (0,1,-2e-16)
  Length = 1.5
  Length2 = 10
  Profile = -> Sketch902
  ReferenceAxis = -> Sketch902 [N_Axis]
  Refine = true
  Suppressed = false
  Type = 0
FEATURE [Sketcher::SketchObject] Sketch903
  ArcFitTolerance = 1e-06
  AttachmentSupport = -> [Pad598]
  ExternalGeometry = -> [Pad598]
  FullyConstrained = true
  MakeInternals = false
  MapMode = 5
  Placement = pos=(0,22.7,0) rot=(0,0.707107,0.707107;3.14159rad)
  sketch-geometry (4):
    g0: LineSegment StartX=-21.2 StartY=-2.6688 StartZ=0 EndX=-21.2 EndY=-5.8e-15 EndZ=0
    g1: LineSegment StartX=-19.2 StartY=-2.6688 StartZ=0 EndX=-19.2 EndY=-5.8e-15 EndZ=0
    g2: LineSegment StartX=-19.2 StartY=-5.8e-15 StartZ=0 EndX=-21.2 EndY=-5.8e-15 EndZ=0
    g3: ArcOfCircle CenterX=-20.2 CenterY=-1.65468e-05 CenterZ=0 NormalX=0 NormalY=0 NormalZ=1 AngleXU=0 Radius=2.84998 StartAngle=4.35388 EndAngle=5.0709
  constraints (11):
    c: Coincident(g0,g-5)
    c: PointOnObject(g0,g-4)
    c: Vertical(g0)
    c: Coincident(g1,g-6)
    c: PointOnObject(g1,g-4)
    c: Vertical(g1)
    c: Coincident(g2,g1)
    c: Coincident(g2,g0)
    c: Coincident(g3,g0)
    c: Coincident(g3,g1)
    c: Tangent(g3,g-3)
FEATURE [PartDesign::Pocket] Pocket418
  BaseFeature = -> Pad598
  Direction = (0,-1,2e-16)
  Length = 0.5
  Length2 = 5
  Profile = -> Sketch903
  ReferenceAxis = -> Sketch903 [N_Axis]
  Refine = true
  Suppressed = false
  Type = 0
FEATURE [Sketcher::SketchObject] Sketch904
  ArcFitTolerance = 1e-06
  AttachmentSupport = -> [Pocket418]
  ExternalGeometry = -> [Pocket418]
  FullyConstrained = true
  MakeInternals = false
  MapMode = 5
  Placement = pos=(0,-1,2e-16) rot=(1,0,0;1.5708rad)
  sketch-geometry (4):
    g0: LineSegment StartX=19.2 StartY=-2.6688 StartZ=0 EndX=19.2 EndY=0 EndZ=0
    g1: LineSegment StartX=21.2 StartY=-2.6688 StartZ=0 EndX=21.2 EndY=-4e-16 EndZ=0
    g2: LineSegment StartX=21.2 StartY=-4e-16 StartZ=0 EndX=19.2 EndY=0 EndZ=0
    g3: ArcOfCircle CenterX=20.2 CenterY=-2.79372e-05 CenterZ=0 NormalX=0 NormalY=0 NormalZ=1 AngleXU=0 Radius=2.84997 StartAngle=4.35388 EndAngle=5.0709
  constraints (11):
    c: Coincident(g0,g-6)
    c: PointOnObject(g0,g-3)
    c: Vertical(g0)
    c: Coincident(g1,g-5)
    c: PointOnObject(g1,g-3)
    c: Vertical(g1)
    c: Coincident(g2,g1)
    c: Coincident(g2,g0)
    c: Coincident(g3,g0)
    c: Coincident(g3,g1)
    c: Tangent(g3,g-4)
FEATURE [PartDesign::Pocket] Pocket419
  BaseFeature = -> Pocket418
  Direction = (0,1,-2e-16)
  Length = 0.5
  Length2 = 5
  Profile = -> Sketch904
  ReferenceAxis = -> Sketch904 [N_Axis]
  Refine = true
  Suppressed = false
  Type = 0
FEATURE [PartDesign::Chamfer] Chamfer038
  Angle = 45
  Base = -> Pocket419 [Edge188,Edge205,Edge304,Edge303,Edge302,Edge226,Edge227,Edge228,Edge229,Edge204,Edge198,Edge197,Edge189,Edge192,Edge193,Edge186,Edge185,Edge288,Edge295,Edge301,Edge164,Edge157,Edge151,Edge143,Edge140,Edge141,Edge142]
  BaseFeature = -> Pocket419
  ChamferType = 0
  FlipDirection = false
  Refine = true
  Size = 0.999
  Size2 = 1
  SupportTransform = false
  Suppressed = false
  UseAllEdges = false
FEATURE [Sketcher::SketchObject] Sketch905
  ArcFitTolerance = 1e-06
  AttachmentSupport = -> [Chamfer038]
  ExternalGeometry = -> [Chamfer038]
  FullyConstrained = true
  MakeInternals = false
  MapMode = 5
  Placement = pos=(0,0,-5) rot=(1,0,0;3.14159rad)
  sketch-geometry (9):
    g0: Circle CenterX=20.2 CenterY=-4.949 CenterZ=0 NormalX=0 NormalY=0 NormalZ=1 AngleXU=0 Radius=3
    g1: Circle CenterX=20.2 CenterY=-17.151 CenterZ=0 NormalX=0 NormalY=0 NormalZ=1 AngleXU=0 Radius=2.6
    g2: LineSegment [constr] StartX=20.2 StartY=-4.949 StartZ=0 EndX=20.2 EndY=-1.949 EndZ=0
    g3: LineSegment [constr] StartX=20.2 StartY=-4.949 StartZ=0 EndX=20.2 EndY=-7.949 EndZ=0
    g4: LineSegment [constr] StartX=20.2 StartY=-17.151 StartZ=0 EndX=20.2 EndY=-14.551 EndZ=0
    g5: LineSegment [constr] StartX=20.2 StartY=-17.151 StartZ=0 EndX=20.2 EndY=-19.751 EndZ=0
    g6: LineSegment [constr] StartX=20.2 StartY=-17.151 StartZ=0 EndX=17.6 EndY=-17.151 EndZ=0
    g7: LineSegment [constr] StartX=20.2 StartY=-4.949 StartZ=0 EndX=17.2 EndY=-4.949 EndZ=0
    g8: LineSegment [constr] StartX=20.2 StartY=-7.949 StartZ=0 EndX=20.2 EndY=-14.551 EndZ=0
  constraints (27):
    c: Diameter(g0) = 6
    c: Diameter(g1) = 5.2
    c: Coincident(g2,g0)
    c: PointOnObject(g2,g0)
    c: Vertical(g2)
    c: Coincident(g3,g0)
    c: PointOnObject(g3,g0)
    c: Vertical(g3)
    c: Coincident(g4,g1)
    c: PointOnObject(g4,g1)
    c: Vertical(g4)
    c: Coincident(g5,g1)
    c: PointOnObject(g5,g1)
    c: Vertical(g5)
    c: Coincident(g6,g1)
    c: PointOnObject(g6,g1)
    c: Horizontal(g6)
    c: Coincident(g7,g0)
    c: PointOnObject(g7,g0)
    c: Horizontal(g7)
    c: DistanceX(g-3,g-3) = 2
    c: DistanceX(g-3,g2) = 1
    c: Coincident(g8,g3)
    c: Coincident(g8,g4)
    c: Vertical(g8)
    c: DistanceY(g0,g-3) = 3.95
    c: DistanceY(g-4,g1) = 3.55
FEATURE [PartDesign::Pad] Pad599
  BaseFeature = -> Chamfer038
  Direction = (0,0,-1)
  Length = 3.5
  Length2 = 10
  Profile = -> Sketch905
  ReferenceAxis = -> Sketch905 [N_Axis]
  Refine = true
  Suppressed = false
  Type = 0
FEATURE [Sketcher::SketchObject] Sketch906
  ArcFitTolerance = 1e-06
  AttachmentSupport = -> [Pad599]
  ExternalGeometry = -> [Pad599]
  FullyConstrained = true
  MakeInternals = false
  MapMode = 5
  Placement = pos=(0,0,-8.5) rot=(1,0,0;3.14159rad)
  sketch-geometry (2):
    g0: Circle CenterX=20.2 CenterY=-4.949 CenterZ=0 NormalX=0 NormalY=0 NormalZ=1 AngleXU=0 Radius=2.025
    g1: Circle CenterX=20.2 CenterY=-17.151 CenterZ=0 NormalX=0 NormalY=0 NormalZ=1 AngleXU=0 Radius=1.65
  constraints (4):
    c: Coincident(g0,g-3)
    c: Coincident(g1,g-4)
    c: Diameter(g1) = 3.3
    c: Diameter(g0) = 4.05
FEATURE [PartDesign::Pocket] Pocket420
  BaseFeature = -> Pad599
  Direction = (0,0,1)
  Length = 4.5
  Length2 = 5
  Profile = -> Sketch906
  ReferenceAxis = -> Sketch906 [N_Axis]
  Refine = true
  Suppressed = false
  Type = 0
FEATURE [Sketcher::SketchObject] Sketch907
  ArcFitTolerance = 1e-06
  AttachmentSupport = -> [Pocket420]
  ExternalGeometry = -> [Pocket420]
  FullyConstrained = true
  MakeInternals = false
  MapMode = 5
  Placement = pos=(0,0,-4) rot=(0,0,1;0rad)
  sketch-geometry (2):
    g0: Circle CenterX=20.2 CenterY=4.949 CenterZ=0 NormalX=0 NormalY=0 NormalZ=1 AngleXU=0 Radius=3
    g1: Circle CenterX=20.2 CenterY=17.151 CenterZ=0 NormalX=0 NormalY=0 NormalZ=1 AngleXU=0 Radius=3
  constraints (4):
    c: Coincident(g0,g-4)
    c: Coincident(g1,g-3)
    c: Radius(g0) = 3
    c: Radius(g1) = 3
FEATURE [PartDesign::Pad] Pad600
  BaseFeature = -> Pocket420
  Direction = (0,0,1)
  Length = 1
  Length2 = 10
  Profile = -> Sketch907
  ReferenceAxis = -> Sketch907 [N_Axis]
  Refine = true
  Suppressed = false
  Type = 0
FEATURE [PartDesign::Body] Body045  label="Left_Inner_Arm"
  AllowCompound = false
  Group = -> [Binder008,Sketch879,Pad586,Sketch880,Pad587,Sketch881,Pad588,Sketch882,Pocket407,Sketch883,Pocket408,Chamfer036,Chamfer037,Sketch884,Pocket409,Sketch885,Pad589,Sketch886,Pocket410,Sketch887,Pad590,Sketch888,Pad591,Sketch889,Pad592,Sketch890,Pocket411,Sketch891,Pocket412,Sketch892,Pad593,Sketch893,Pocket413,Sketch894,Pocket414,Sketch895,Pad594,Sketch896,Pad595,Sketch897,Pad596,Sketch898,Pocket415,+19 more]
  Origin = -> Origin049
  Placement = pos=(-1.42e-14,1.42e-14,0) rot=(0,0,1;0rad)
  Tip = -> Pad600
FEATURE [Sketcher::SketchObject] Sketch908
  ArcFitTolerance = 1e-06
  AttachmentSupport = -> [XZ_Plane050]
  FullyConstrained = true
  MakeInternals = false
  MapMode = 5
  Placement = pos=(0,0,0) rot=(1,0,0;1.5708rad)
  sketch-geometry (1):
    g0: Circle CenterX=0 CenterY=0 CenterZ=0 NormalX=0 NormalY=0 NormalZ=1 AngleXU=0 Radius=2
  constraints (2):
    c: Coincident(g0,g-1)
    c: Radius(g0) = 2
FEATURE [PartDesign::Pad] Pad601
  Direction = (0,-1,2e-16)
  Length = 3
  Length2 = 10
  Placement = pos=(0,0,0) rot=(1,0,0;1.5708rad)
  Profile = -> Sketch908
  ReferenceAxis = -> Sketch908 [N_Axis]
  Refine = true
  Suppressed = false
  Type = 0
FEATURE [Sketcher::SketchObject] Sketch909
  ArcFitTolerance = 1e-06
  AttachmentSupport = -> [Pad601]
  ExternalGeometry = -> [Pad601]
  FullyConstrained = true
  MakeInternals = false
  MapMode = 5
  Placement = pos=(0,-3,0) rot=(1,0,0;1.5708rad)
  sketch-geometry (4):
    g0: LineSegment StartX=2 StartY=0 StartZ=0 EndX=6.75 EndY=0 EndZ=0
    g1: LineSegment StartX=6.75 StartY=0 StartZ=0 EndX=6.75 EndY=2 EndZ=0
    g2: LineSegment StartX=6.75 StartY=2 StartZ=0 EndX=-3.206e-13 EndY=2 EndZ=0
    g3: ArcOfCircle CenterX=-3.212e-13 CenterY=-3.345e-13 CenterZ=0 NormalX=0 NormalY=0 NormalZ=1 AngleXU=0 Radius=2 StartAngle=1.673e-13 EndAngle=1.5708
  constraints (13):
    c: PointOnObject(g0,g-3)
    c: PointOnObject(g0,g-1)
    c: Horizontal(g0)
    c: Coincident(g1,g0)
    c: Vertical(g1)
    c: Coincident(g2,g1)
    c: PointOnObject(g2,g-3)
    c: Horizontal(g2)
    c: DistanceX(g0,g0) = 4.75
    c: Coincident(g3,g0)
    c: Coincident(g3,g2)
    c: Tangent(g3,g-3)
    c: DistanceX(g3,g2) = 0
FEATURE [PartDesign::Pad] Pad602
  BaseFeature = -> Pad601
  Direction = (0,-1,2e-16)
  Length = 3
  Length2 = 10
  Placement = pos=(0,0,0) rot=(1,0,0;1.5708rad)
  Profile = -> Sketch909
  ReferenceAxis = -> Sketch909 [N_Axis]
  Refine = true
  Reversed = true
  Suppressed = false
  Type = 0
FEATURE [Sketcher::SketchObject] Sketch910
  ArcFitTolerance = 1e-06
  AttachmentSupport = -> [Pad602]
  ExternalGeometry = -> [Pad602]
  FullyConstrained = true
  MakeInternals = false
  MapMode = 5
  Placement = pos=(0,-3,1.3e-15) rot=(1,0,0;1.5708rad)
  sketch-geometry (15):
    g0: LineSegment StartX=1 StartY=2 StartZ=0 EndX=1 EndY=8 EndZ=0
    g1: LineSegment StartX=1 StartY=8 StartZ=0 EndX=2.3 EndY=8 EndZ=0
    g2: LineSegment StartX=2.3 StartY=8 StartZ=0 EndX=2.3 EndY=8.7 EndZ=0
    g3: LineSegment StartX=2.3 StartY=8.7 StartZ=0 EndX=1 EndY=10 EndZ=0
    g4: LineSegment StartX=1 StartY=10 StartZ=0 EndX=-2.2 EndY=10 EndZ=0
    g5: LineSegment StartX=-2.2 StartY=10 StartZ=0 EndX=-9.5 EndY=2.7 EndZ=0
    g6: LineSegment StartX=-9.5 StartY=2.7 StartZ=0 EndX=-9.5 EndY=1 EndZ=0
    g7: LineSegment StartX=-9.5 StartY=1 StartZ=0 EndX=-5.25 EndY=1 EndZ=0
    g8: LineSegment StartX=-5.25 StartY=1 StartZ=0 EndX=-5.25 EndY=2 EndZ=0
    g9: LineSegment StartX=-5.25 StartY=2 StartZ=0 EndX=-2 EndY=2 EndZ=0
    g10: LineSegment StartX=-2 StartY=2 StartZ=0 EndX=-2 EndY=6.59786e-11 EndZ=0
    g11: LineSegment StartX=1 StartY=2 StartZ=0 EndX=-6.62992e-11 EndY=2 EndZ=0
    g12: ArcOfCircle CenterX=-1.1487e-05 CenterY=1.1487e-05 CenterZ=0 NormalX=0 NormalY=0 NormalZ=1 AngleXU=0 Radius=1.99999 StartAngle=1.57079 EndAngle=3.1416
    g13: LineSegment [constr] StartX=1 StartY=10 StartZ=0 EndX=1 EndY=8 EndZ=0
    g14: LineSegment [constr] StartX=-6.62992e-11 StartY=2 StartZ=0 EndX=-2 EndY=2 EndZ=0
  constraints (43):
    c: PointOnObject(g0,g-3)
    c: Vertical(g0)
    c: Coincident(g1,g0)
    c: Horizontal(g1)
    c: Coincident(g2,g1)
    c: Vertical(g2)
    c: Coincident(g3,g2)
    c: Coincident(g4,g3)
    c: Horizontal(g4)
    c: Coincident(g5,g4)
    c: Coincident(g6,g5)
    c: Vertical(g6)
    c: Coincident(g7,g6)
    c: Horizontal(g7)
    c: Coincident(g8,g7)
    c: Vertical(g8)
    c: Coincident(g9,g8)
    c: Horizontal(g9)
    c: Coincident(g10,g9)
    c: PointOnObject(g10,g-4)
    c: Vertical(g10)
    c: Coincident(g11,g0)
    c: Coincident(g11,g-4)
    c: Coincident(g12,g11)
    c: Coincident(g12,g10)
    c: DistanceY(g0,g3) = 8
    c: DistanceX(g7,g7) = 4.25
    c: DistanceY(g0,g3) = 2
    c: DistanceX(g1,g1) = 1.3
    c: Angle(g5,g4) = 2.35619
    c: Coincident(g13,g3)
    c: Coincident(g13,g0)
    c: Vertical(g13)
    c: Angle(g3,g2) = 2.35619
    c: DistanceY(g8,g8) = 1
    c: PointOnObject(g10,g-1)
    c: DistanceX(g9,g0) = 3
    c: DistanceY(g6,g6) = 1.7
    c: Coincident(g14,g11)
    c: Coincident(g14,g9)
    c: Tangent(g14,g12)
    c: Horizontal(g14)
    c: DistanceX(g9,g9) = 3.25
FEATURE [PartDesign::Pad] Pad603
  BaseFeature = -> Pad602
  Direction = (0,-1,2e-16)
  Length = 3
  Length2 = 10
  Placement = pos=(0,0,0) rot=(1,0,0;1.5708rad)
  Profile = -> Sketch910
  ReferenceAxis = -> Sketch910 [N_Axis]
  Refine = true
  Reversed = true
  Suppressed = false
  Type = 0
FEATURE [Sketcher::SketchObject] Sketch911
  ArcFitTolerance = 1e-06
  AttachmentSupport = -> [Pad603]
  ExternalGeometry = -> [Pad603]
  FullyConstrained = true
  MakeInternals = false
  MapMode = 5
  Placement = pos=(0,-3,1.2e-15) rot=(1,0,0;1.5708rad)
  sketch-geometry (1):
    g0: Circle CenterX=0 CenterY=0 CenterZ=0 NormalX=0 NormalY=0 NormalZ=1 AngleXU=0 Radius=2.00001
  constraints (2):
    c: Coincident(g0,g-1)
    c: Tangent(g0,g-3)
FEATURE [PartDesign::Pad] Pad604
  BaseFeature = -> Pad603
  Direction = (0,-1,2e-16)
  Length = 1
  Length2 = 10
  Placement = pos=(0,0,0) rot=(1,0,0;1.5708rad)
  Profile = -> Sketch911
  ReferenceAxis = -> Sketch911 [N_Axis]
  Refine = true
  Suppressed = false
  Type = 0
FEATURE [Sketcher::SketchObject] Sketch912
  ArcFitTolerance = 1e-06
  AttachmentSupport = -> [Pad604]
  ExternalGeometry = -> [Pad604]
  FullyConstrained = true
  MakeInternals = false
  MapMode = 5
  Placement = pos=(0,-1.2e-15,0) rot=(-1,0,0;1.5708rad)
  sketch-geometry (1):
    g0: Circle CenterX=0 CenterY=0 CenterZ=0 NormalX=0 NormalY=0 NormalZ=1 AngleXU=0 Radius=1.99999
  constraints (2):
    c: Coincident(g0,g-1)
    c: Tangent(g0,g-3)
FEATURE [PartDesign::Pad] Pad605
  BaseFeature = -> Pad604
  Direction = (0,1,2e-16)
  Length = 1
  Length2 = 10
  Placement = pos=(0,0,0) rot=(1,0,0;1.5708rad)
  Profile = -> Sketch912
  ReferenceAxis = -> Sketch912 [N_Axis]
  Refine = true
  Suppressed = false
  Type = 0
FEATURE [Sketcher::SketchObject] Sketch913
  ArcFitTolerance = 1e-06
  AttachmentSupport = -> [Pad605]
  FullyConstrained = true
  MakeInternals = false
  MapMode = 5
  Placement = pos=(0,1,0) rot=(-1,0,0;1.5708rad)
  sketch-geometry (1):
    g0: Circle CenterX=0 CenterY=0 CenterZ=0 NormalX=0 NormalY=0 NormalZ=1 AngleXU=0 Radius=1
  constraints (2):
    c: Coincident(g0,g-1)
    c: Diameter(g0) = 2
FEATURE [PartDesign::Pad] Pad606
  BaseFeature = -> Pad605
  Direction = (0,1,2e-16)
  Length = 2.6
  Length2 = 10
  Placement = pos=(0,0,0) rot=(1,0,0;1.5708rad)
  Profile = -> Sketch913
  ReferenceAxis = -> Sketch913 [N_Axis]
  Refine = true
  Suppressed = false
  Type = 0
FEATURE [Sketcher::SketchObject] Sketch914
  ArcFitTolerance = 1e-06
  AttachmentSupport = -> [Pad606]
  ExternalGeometry = -> [Pad606]
  FullyConstrained = true
  MakeInternals = false
  MapMode = 5
  Placement = pos=(0,-4,1e-15) rot=(1,0,0;1.5708rad)
  sketch-geometry (1):
    g0: Circle CenterX=0 CenterY=0 CenterZ=0 NormalX=0 NormalY=0 NormalZ=1 AngleXU=0 Radius=1
  constraints (2):
    c: Coincident(g0,g-1)
    c: Diameter(g0) = 2
FEATURE [PartDesign::Pad] Pad607
  BaseFeature = -> Pad606
  Direction = (0,-1,2e-16)
  Length = 2.6
  Length2 = 10
  Placement = pos=(0,0,0) rot=(1,0,0;1.5708rad)
  Profile = -> Sketch914
  ReferenceAxis = -> Sketch914 [N_Axis]
  Refine = true
  Suppressed = false
  Type = 0
FEATURE [Sketcher::SketchObject] Sketch915
  ArcFitTolerance = 1e-06
  AttachmentSupport = -> [Pad607]
  ExternalGeometry = -> [Pad607]
  FullyConstrained = true
  MakeInternals = false
  MapMode = 5
  Placement = pos=(0,9e-16,2) rot=(0,0,1;3.14159rad)
  sketch-geometry (2):
    g0: Circle CenterX=-3.5 CenterY=1.5 CenterZ=0 NormalX=0 NormalY=0 NormalZ=1 AngleXU=0 Radius=0.75
    g1: LineSegment [constr] StartX=-3.5 StartY=1.5 StartZ=0 EndX=-4.25 EndY=1.5 EndZ=0
  constraints (7):
    c: Diameter(g0) = 1.5
    c: DistanceY(g-3,g-3) = 3
    c: DistanceY(g0,g-4) = 1.5
    c: Coincident(g1,g0)
    c: PointOnObject(g1,g0)
    c: Horizontal(g1)
    c: DistanceX(g-4,g1) = 2.5
FEATURE [PartDesign::Pad] Pad608
  BaseFeature = -> Pad607
  Direction = (0,0,1)
  Length = 1.5
  Length2 = 10
  Placement = pos=(0,0,0) rot=(1,0,0;1.5708rad)
  Profile = -> Sketch915
  ReferenceAxis = -> Sketch915 [N_Axis]
  Refine = true
  Suppressed = false
  Type = 0
FEATURE [Sketcher::SketchObject] Sketch916
  ArcFitTolerance = 1e-06
  AttachmentSupport = -> [Pad608]
  ExternalGeometry = -> [Pad608]
  FullyConstrained = true
  MakeInternals = false
  MapMode = 5
  Placement = pos=(0,-3,1.2e-15) rot=(1,0,0;1.5708rad)
  sketch-geometry (5):
    g0: ArcOfCircle CenterX=1.1e-15 CenterY=9 CenterZ=0 NormalX=0 NormalY=0 NormalZ=1 AngleXU=0 Radius=1 StartAngle=4.71239 EndAngle=7.85398
    g1: LineSegment StartX=1.1e-15 StartY=10 StartZ=0 EndX=1.1e-15 EndY=9 EndZ=0
    g2: LineSegment StartX=1.1e-15 StartY=9 StartZ=0 EndX=1.1e-15 EndY=8 EndZ=0
    g3: LineSegment [constr] StartX=1 StartY=10 StartZ=0 EndX=1 EndY=9 EndZ=0
    g4: LineSegment [constr] StartX=1.1e-15 StartY=9 StartZ=0 EndX=1 EndY=9 EndZ=0
  constraints (14):
    c: Diameter(g0) = 2
    c: Coincident(g1,g0)
    c: Coincident(g1,g0)
    c: Coincident(g2,g0)
    c: Coincident(g2,g0)
    c: Vertical(g1)
    c: Vertical(g2)
    c: PointOnObject(g0,g-3)
    c: Coincident(g3,g-3)
    c: Vertical(g3)
    c: Coincident(g4,g0)
    c: PointOnObject(g4,g0)
    c: Horizontal(g4)
    c: Tangent(g3,g0) = 1.5708
FEATURE [PartDesign::Pad] Pad609
  BaseFeature = -> Pad608
  Direction = (0,-1,2e-16)
  Length = 2.5
  Length2 = 10
  Placement = pos=(0,0,0) rot=(1,0,0;1.5708rad)
  Profile = -> Sketch916
  ReferenceAxis = -> Sketch916 [N_Axis]
  Refine = true
  Suppressed = false
  Type = 0
FEATURE [PartDesign::Body] Body046  label="Trigger1"
  AllowCompound = false
  Group = -> [Sketch908,Pad601,Sketch909,Pad602,Sketch910,Pad603,Sketch911,Pad604,Sketch912,Pad605,Sketch913,Pad606,Sketch914,Pad607,Sketch915,Pad608,Sketch916,Pad609]
  Origin = -> Origin050
  Placement = pos=(20.05,9.35,3) rot=(-0.71,0,0.71;3.14159rad)
  Tip = -> Pad609
FEATURE [Sketcher::SketchObject] Sketch306
  ArcFitTolerance = 1e-06
  AttachmentSupport = -> [XZ_Plane031]
  FullyConstrained = false
  MakeInternals = false
  MapMode = 5
  Placement = pos=(0,0,0) rot=(1,0,0;1.5708rad)
  sketch-geometry (4):
    g0: LineSegment StartX=46.5745 StartY=12.8542 StartZ=0 EndX=41.5745 EndY=12.8542 EndZ=0
    g1: LineSegment StartX=41.5745 StartY=12.8542 StartZ=0 EndX=41.5745 EndY=10.8542 EndZ=0
    g2: LineSegment StartX=41.5745 StartY=10.8542 StartZ=0 EndX=46.5745 EndY=10.8542 EndZ=0
    g3: LineSegment StartX=46.5745 StartY=10.8542 StartZ=0 EndX=46.5745 EndY=12.8542 EndZ=0
  constraints (10):
    c: Coincident(g0,g1)
    c: Coincident(g1,g2)
    c: Coincident(g2,g3)
    c: Coincident(g3,g0)
    c: Horizontal(g0)
    c: Horizontal(g2)
    c: Vertical(g1)
    c: Vertical(g3)
    c: DistanceX(g0,g0) = 5
    c: DistanceY(g3,g3) = 2
FEATURE [PartDesign::Pad] Pad207
  Direction = (0,-1,2e-16)
  Length = 5
  Length2 = 10
  Placement = pos=(0,0,0) rot=(1,0,0;1.5708rad)
  Profile = -> Sketch306
  ReferenceAxis = -> Sketch306 [N_Axis]
  Refine = true
  Suppressed = false
  Type = 0
FEATURE [Sketcher::SketchObject] Sketch307
  ArcFitTolerance = 1e-06
  AttachmentSupport = -> [Pad207]
  ExternalGeometry = -> [Pad207]
  FullyConstrained = true
  MakeInternals = false
  MapMode = 5
  Placement = pos=(0,4.8e-15,10.8542) rot=(1,0,0;3.14159rad)
  sketch-geometry (1):
    g0: Circle CenterX=44.0745 CenterY=2.5 CenterZ=0 NormalX=0 NormalY=0 NormalZ=1 AngleXU=0 Radius=1
  constraints (2):
    c: Symmetric(g-3,g-4,g0)
    c: Radius(g0) = 1
FEATURE [PartDesign::Pocket] Pocket216
  BaseFeature = -> Pad207
  Direction = (0,0,1)
  Length = 5
  Length2 = 5
  Placement = pos=(0,0,0) rot=(1,0,0;1.5708rad)
  Profile = -> Sketch307
  ReferenceAxis = -> Sketch307 [N_Axis]
  Refine = true
  Suppressed = false
  Type = 0
FEATURE [Sketcher::SketchObject] Sketch308
  ArcFitTolerance = 1e-06
  AttachmentSupport = -> [Pocket216]
  ExternalGeometry = -> [Pocket216]
  FullyConstrained = true
  MakeInternals = false
  MapMode = 5
  Placement = pos=(0,4.8e-15,10.8542) rot=(1,0,0;3.14159rad)
  sketch-geometry (9):
    g0: Circle [constr] CenterX=44.0745 CenterY=2.5 CenterZ=0 NormalX=0 NormalY=0 NormalZ=1 AngleXU=0 Radius=1.4
    g1: Circle [constr] CenterX=44.0745 CenterY=2.5 CenterZ=0 NormalX=0 NormalY=0 NormalZ=1 AngleXU=0 Radius=1.9
    g2: ArcOfCircle CenterX=44.0745 CenterY=2.5 CenterZ=0 NormalX=0 NormalY=0 NormalZ=1 AngleXU=0 Radius=1.4 StartAngle=3.91679 EndAngle=8.64958
    g3: ArcOfCircle CenterX=44.0745 CenterY=2.5 CenterZ=0 NormalX=0 NormalY=0 NormalZ=1 AngleXU=0 Radius=1.9 StartAngle=4.15813 EndAngle=8.40824
    g4: LineSegment [constr] StartX=43.0745 StartY=4.11555 StartZ=0 EndX=43.0745 EndY=3.4798 EndZ=0
    g5: LineSegment [constr] StartX=43.0745 StartY=3.4798 StartZ=0 EndX=43.0745 EndY=1.5202 EndZ=0
    g6: LineSegment [constr] StartX=43.0745 StartY=1.5202 StartZ=0 EndX=43.0745 EndY=0.884451 EndZ=0
    g7: LineSegment StartX=43.0745 StartY=4.11555 StartZ=0 EndX=43.0745 EndY=3.4798 EndZ=0
    g8: LineSegment StartX=43.0745 StartY=1.5202 StartZ=0 EndX=43.0745 EndY=0.884451 EndZ=0
  constraints (22):
    c: Coincident(g0,g-3)
    c: Coincident(g1,g0)
    c: Radius(g1) = 1.9
    c: Radius(g0) = 1.4
    c: Tangent(g2,g0) = -1.5708
    c: PointOnObject(g2,g0)
    c: Tangent(g3,g1) = -1.5708
    c: PointOnObject(g3,g1)
    c: Coincident(g4,g3)
    c: Coincident(g4,g2)
    c: Coincident(g5,g2)
    c: Coincident(g5,g2)
    c: Coincident(g6,g2)
    c: Coincident(g6,g3)
    c: Vertical(g5)
    c: Vertical(g6)
    c: Vertical(g4)
    c: Coincident(g7,g3)
    c: Coincident(g7,g2)
    c: Coincident(g8,g2)
    c: Coincident(g8,g3)
    c: Tangent(g5,g-3)
FEATURE [PartDesign::Pocket] Pocket217
  BaseFeature = -> Pocket216
  Direction = (0,0,1)
  Length = 5
  Length2 = 5
  Placement = pos=(0,0,0) rot=(1,0,0;1.5708rad)
  Profile = -> Sketch308
  ReferenceAxis = -> Sketch308 [N_Axis]
  Refine = true
  Suppressed = false
  Type = 0
FEATURE [Sketcher::SketchObject] Sketch309
  ArcFitTolerance = 1e-06
  AttachmentSupport = -> [Pocket217]
  ExternalGeometry = -> [Pocket217]
  FullyConstrained = true
  MakeInternals = false
  MapMode = 5
  Placement = pos=(0,5.7e-15,12.8542) rot=(0,0,1;3.14159rad)
  sketch-geometry (1):
    g0: Circle CenterX=-44.0745 CenterY=2.5 CenterZ=0 NormalX=0 NormalY=0 NormalZ=1 AngleXU=0 Radius=1.9
  constraints (2):
    c: Coincident(g0,g-3)
    c: Equal(g0,g-3)
FEATURE [PartDesign::Pocket] Pocket218
  BaseFeature = -> Pocket217
  Direction = (0,0,-1)
  Length = 1
  Length2 = 5
  Placement = pos=(0,0,0) rot=(1,0,0;1.5708rad)
  Profile = -> Sketch309
  ReferenceAxis = -> Sketch309 [N_Axis]
  Refine = true
  Suppressed = false
  Type = 0
FEATURE [PartDesign::Pocket] Pocket421
  BaseFeature = -> Pocket218
  Direction = (0,-1,0)
  Length = 0.1
  Length2 = 5
  Placement = pos=(0,0,0) rot=(1,0,0;1.5708rad)
  Profile = -> Pocket218 [Face5]
  Refine = true
  Suppressed = false
  Type = 0
FEATURE [PartDesign::Pocket] Pocket422
  BaseFeature = -> Pocket421
  Direction = (0,1,0)
  Length = 0.1
  Length2 = 5
  Placement = pos=(0,0,0) rot=(1,0,0;1.5708rad)
  Profile = -> Pocket421 [Face11]
  Refine = true
  Suppressed = false
  Type = 0
FEATURE [Sketcher::SketchObject] Sketch917
  ArcFitTolerance = 1e-06
  AttachmentSupport = -> [Pocket422]
  ExternalGeometry = -> [Pocket422]
  FullyConstrained = true
  MakeInternals = false
  MapMode = 5
  Placement = pos=(46.5745,0,0) rot=(0.707107,0,0.707107;3.14159rad)
  sketch-geometry (4):
    g0: LineSegment StartX=10.8542 StartY=4 StartZ=0 EndX=10.8542 EndY=1 EndZ=0
    g1: LineSegment StartX=10.8542 StartY=1 StartZ=0 EndX=12.8542 EndY=1 EndZ=0
    g2: LineSegment StartX=12.8542 StartY=1 StartZ=0 EndX=12.8542 EndY=4 EndZ=0
    g3: LineSegment StartX=12.8542 StartY=4 StartZ=0 EndX=10.8542 EndY=4 EndZ=0
  constraints (12):
    c: Coincident(g0,g1)
    c: Coincident(g1,g2)
    c: Coincident(g2,g3)
    c: Coincident(g3,g0)
    c: Vertical(g0)
    c: Vertical(g2)
    c: Horizontal(g1)
    c: Horizontal(g3)
    c: PointOnObject(g0,g-3)
    c: PointOnObject(g1,g-4)
    c: DistanceY(g0,g-3) = 0.9
    c: DistanceY(g-3,g0) = 0.9
FEATURE [PartDesign::Pocket] Pocket423
  BaseFeature = -> Pocket422
  Direction = (-1,0,2e-16)
  Length = 0.2
  Length2 = 5
  Placement = pos=(0,0,0) rot=(1,0,0;1.5708rad)
  Profile = -> Sketch917
  ReferenceAxis = -> Sketch917 [N_Axis]
  Refine = true
  Suppressed = false
  Type = 0
FEATURE [PartDesign::Body] Body029  label="Spring_Stop1"
  AllowCompound = false
  Group = -> [Sketch306,Pad207,Sketch307,Pocket216,Sketch308,Pocket217,Sketch309,Pocket218,Pocket421,Pocket422,Sketch917,Pocket423]
  Origin = -> Origin031
  Placement = pos=(5,8.35,-44.57) rot=(-0.71,0,-0.71;3.14159rad)
  Tip = -> Pocket423
FEATURE [Sketcher::SketchObject] Sketch918
  ArcFitTolerance = 1e-06
  AttachmentSupport = -> [XZ_Plane051]
  FullyConstrained = true
  MakeInternals = false
  MapMode = 5
  Placement = pos=(0,0,0) rot=(1,0,0;1.5708rad)
  sketch-geometry (10):
    g0: LineSegment StartX=0 StartY=0 StartZ=0 EndX=0 EndY=9.5 EndZ=0
    g1: LineSegment StartX=0 StartY=9.5 StartZ=0 EndX=4.42111 EndY=13.8407 EndZ=0
    g2: ArcOfCircle CenterX=6.52288 CenterY=11.7 CenterZ=0 NormalX=0 NormalY=0 NormalZ=1 AngleXU=0 Radius=3 StartAngle=1.10301 EndAngle=2.34702
    g3: LineSegment StartX=7.87562 StartY=14.3777 StartZ=0 EndX=20.5 EndY=8 EndZ=0
    g4: LineSegment StartX=20.5 StartY=8 StartZ=0 EndX=20.5 EndY=3 EndZ=0
    g5: LineSegment StartX=20.5 StartY=3 StartZ=0 EndX=19.5 EndY=1 EndZ=0
    g6: LineSegment StartX=19.5 StartY=1 StartZ=0 EndX=18.5 EndY=1 EndZ=0
    g7: LineSegment StartX=18.5 StartY=1 StartZ=0 EndX=18.5 EndY=0 EndZ=0
    g8: LineSegment StartX=18.5 StartY=0 StartZ=0 EndX=0 EndY=0 EndZ=0
    g9: LineSegment [constr] StartX=6.52288 StartY=11.7 StartZ=0 EndX=6.52288 EndY=14.7 EndZ=0
  constraints (29):
    c: Coincident(g0,g-1)
    c: Vertical(g0)
    c: Coincident(g1,g0)
    c: Coincident(g4,g3)
    c: Vertical(g4)
    c: Coincident(g5,g4)
    c: Coincident(g6,g5)
    c: Horizontal(g6)
    c: Coincident(g7,g6)
    c: PointOnObject(g7,g-1)
    c: Vertical(g7)
    c: Coincident(g8,g7)
    c: Coincident(g8,g0)
    c: DistanceY(g0,g0) = 9.5
    c: Coincident(g9,g2)
    c: PointOnObject(g9,g2)
    c: Vertical(g9)
    c: DistanceY(g7,g9) = 14.7
    c: Tangent(g2,g1) = 1.5708
    c: DistanceX(g0,g4) = 20.5
    c: DistanceY(g7,g3) = 8
    c: Tangent(g3,g2) = 1.5708
    c: DistanceX(g8,g8) = 18.5
    c: Radius(g2) = 3
    c: DistanceY(g3,g9) = 6.7
    c: DistanceY(g4,g4) = 5
    c: DistanceY(g7,g7) = 1
    c: DistanceX(g5,g4) = 1
    c: Distance(g9,g3) = 15.5
FEATURE [PartDesign::Pad] Pad610
  Direction = (0,-1,2e-16)
  Length = 2
  Length2 = 10
  Placement = pos=(0,0,0) rot=(1,0,0;1.5708rad)
  Profile = -> Sketch918
  ReferenceAxis = -> Sketch918 [N_Axis]
  Refine = true
  Suppressed = false
  Type = 0
FEATURE [Sketcher::SketchObject] Sketch919
  ArcFitTolerance = 1e-06
  AttachmentSupport = -> [Pad610]
  ExternalGeometry = -> [Pad610]
  FullyConstrained = true
  MakeInternals = false
  MapMode = 5
  Placement = pos=(0,1.3e-15,0) rot=(-1,0,0;1.5708rad)
  sketch-geometry (15):
    g0: LineSegment StartX=19.5 StartY=-1 StartZ=0 EndX=15.5 EndY=-1 EndZ=0
    g1: LineSegment StartX=19.5 StartY=-1 StartZ=0 EndX=20.5 EndY=-3 EndZ=0
    g2: LineSegment StartX=20.5 StartY=-3 StartZ=0 EndX=20.5 EndY=-8 EndZ=0
    g3: LineSegment StartX=20.5 StartY=-8 StartZ=0 EndX=7.87562 EndY=-14.3777 EndZ=0
    g4: ArcOfCircle CenterX=6.52287 CenterY=-11.7 CenterZ=0 NormalX=0 NormalY=0 NormalZ=1 AngleXU=0 Radius=2.99999 StartAngle=3.93617 EndAngle=5.18018
    g5: LineSegment StartX=15.5 StartY=-1 StartZ=0 EndX=15.5 EndY=-7 EndZ=0
    g6: LineSegment StartX=15.5 StartY=-7 StartZ=0 EndX=7.87562 EndY=-10.8518 EndZ=0
    g7: LineSegment StartX=0 StartY=0 StartZ=0 EndX=2 EndY=0 EndZ=0
    g8: LineSegment StartX=2 StartY=0 StartZ=0 EndX=2 EndY=-7.93768 EndZ=0
    g9: LineSegment StartX=2 StartY=-7.93768 StartZ=0 EndX=4.42111 EndY=-10.3148 EndZ=0
    g10: ArcOfCircle CenterX=6.52287 CenterY=-8.17406 CenterZ=0 NormalX=0 NormalY=0 NormalZ=1 AngleXU=0 Radius=3 StartAngle=3.93617 EndAngle=5.18018
    g11: LineSegment [constr] StartX=6.52287 StartY=-8.17406 StartZ=0 EndX=6.52287 EndY=-11.7 EndZ=0
    g12: LineSegment [constr] StartX=4.42111 StartY=-10.3148 StartZ=0 EndX=4.42111 EndY=-13.8407 EndZ=0
    g13: LineSegment StartX=0 StartY=0 StartZ=0 EndX=0 EndY=-9.5 EndZ=0
    g14: LineSegment StartX=0 StartY=-9.5 StartZ=0 EndX=4.42111 EndY=-13.8407 EndZ=0
  constraints (36):
    c: Coincident(g0,g-4)
    c: Horizontal(g0)
    c: DistanceX(g0,g0) = 4
    c: Coincident(g1,g0)
    c: Coincident(g1,g-5)
    c: Coincident(g2,g1)
    c: Coincident(g2,g-6)
    c: Coincident(g3,g2)
    c: Coincident(g3,g-7)
    c: Coincident(g4,g3)
    c: Coincident(g4,g-8)
    c: Coincident(g5,g0)
    c: Vertical(g5)
    c: Coincident(g6,g5)
    c: Parallel(g6,g3)
    c: DistanceY(g5,g5) = 6
    c: Coincident(g7,g-1)
    c: Horizontal(g7)
    c: Coincident(g8,g7)
    c: Vertical(g8)
    c: Coincident(g9,g8)
    c: Parallel(g9,g-8)
    c: DistanceX(g7,g7) = 2
    c: Tangent(g10,g9) = -1.5708
    c: Tangent(g10,g6) = 1.5708
    c: Coincident(g11,g10)
    c: Coincident(g11,g4)
    c: Vertical(g11)
    c: Coincident(g12,g9)
    c: Coincident(g12,g4)
    c: Vertical(g12)
    c: Tangent(g4,g-7)
    c: Coincident(g13,g7)
    c: Coincident(g13,g-9)
    c: Coincident(g14,g4)
    c: Coincident(g14,g13)
FEATURE [PartDesign::Pad] Pad611
  BaseFeature = -> Pad610
  Direction = (0,1,2e-16)
  Length = 3
  Length2 = 10
  Placement = pos=(0,0,0) rot=(1,0,0;1.5708rad)
  Profile = -> Sketch919
  ReferenceAxis = -> Sketch919 [N_Axis]
  Refine = true
  Suppressed = false
  Type = 0
FEATURE [Sketcher::SketchObject] Sketch920
  ArcFitTolerance = 1e-06
  AttachmentSupport = -> [Pad611]
  ExternalGeometry = -> [Pad611]
  FullyConstrained = true
  MakeInternals = false
  MapMode = 5
  Placement = pos=(0,3,0) rot=(-1,0,0;1.5708rad)
  sketch-geometry (13):
    g0: LineSegment StartX=19.5 StartY=-1 StartZ=0 EndX=15.5 EndY=-1 EndZ=0
    g1: LineSegment StartX=15.5 StartY=-1 StartZ=0 EndX=15.5 EndY=-7 EndZ=0
    g2: LineSegment StartX=15.5 StartY=-7 StartZ=0 EndX=7.87562 EndY=-10.8518 EndZ=0
    g3: LineSegment StartX=4.42111 StartY=-10.3148 StartZ=0 EndX=2 EndY=-7.93768 EndZ=0
    g4: LineSegment StartX=2 StartY=-7.93768 StartZ=0 EndX=2 EndY=0 EndZ=0
    g5: LineSegment StartX=2 StartY=0 StartZ=0 EndX=0 EndY=0 EndZ=0
    g6: LineSegment StartX=0 StartY=0 StartZ=0 EndX=0 EndY=-9.5 EndZ=0
    g7: LineSegment StartX=0 StartY=-9.5 StartZ=0 EndX=4.42111 EndY=-13.8407 EndZ=0
    g8: LineSegment StartX=7.87562 StartY=-14.3777 StartZ=0 EndX=21.5 EndY=-7.49481 EndZ=0
    g9: LineSegment StartX=21.5 StartY=-7.49481 StartZ=0 EndX=21.5 EndY=-5 EndZ=0
    g10: LineSegment StartX=21.5 StartY=-5 StartZ=0 EndX=19.5 EndY=-1 EndZ=0
    g11: ArcOfCircle CenterX=6.52287 CenterY=-8.17407 CenterZ=0 NormalX=0 NormalY=0 NormalZ=1 AngleXU=0 Radius=2.99999 StartAngle=3.93617 EndAngle=5.18018
    g12: ArcOfCircle CenterX=6.52287 CenterY=-11.7 CenterZ=0 NormalX=0 NormalY=0 NormalZ=1 AngleXU=0 Radius=2.99999 StartAngle=3.93617 EndAngle=5.18018
  constraints (30):
    c: Coincident(g0,g-14)
    c: Coincident(g0,g-9)
    c: Coincident(g1,g0)
    c: Coincident(g1,g-8)
    c: Coincident(g2,g1)
    c: Coincident(g2,g-7)
    c: Coincident(g3,g-6)
    c: Coincident(g3,g-5)
    c: Coincident(g4,g3)
    c: Coincident(g4,g-4)
    c: Coincident(g5,g4)
    c: Coincident(g5,g-1)
    c: Coincident(g6,g5)
    c: Coincident(g6,g-10)
    c: Coincident(g7,g6)
    c: Coincident(g7,g-11)
    c: Coincident(g8,g-12)
    c: PointOnObject(g-13,g8)
    c: Coincident(g9,g8)
    c: Vertical(g9)
    c: Coincident(g10,g9)
    c: Coincident(g10,g0)
    c: Coincident(g11,g2)
    c: Coincident(g11,g3)
    c: Coincident(g12,g8)
    c: Coincident(g12,g7)
    c: Tangent(g12,g-11)
    c: Tangent(g11,g-6)
    c: Parallel(g-14,g10)
    c: DistanceX(g-13,g8) = 1
FEATURE [PartDesign::Pad] Pad612
  BaseFeature = -> Pad611
  Direction = (0,1,2e-16)
  Length = 5
  Length2 = 10
  Placement = pos=(0,0,0) rot=(1,0,0;1.5708rad)
  Profile = -> Sketch920
  ReferenceAxis = -> Sketch920 [N_Axis]
  Refine = true
  Suppressed = false
  Type = 0
FEATURE [Sketcher::SketchObject] Sketch921
  ArcFitTolerance = 1e-06
  AttachmentSupport = -> [Pad612]
  ExternalGeometry = -> [Pad612]
  FullyConstrained = true
  MakeInternals = false
  MapMode = 5
  Placement = pos=(0,8,0) rot=(-1,0,0;1.5708rad)
  sketch-geometry (13):
    g0: LineSegment StartX=2 StartY=0 StartZ=0 EndX=0 EndY=0 EndZ=0
    g1: LineSegment StartX=0 StartY=0 StartZ=0 EndX=0 EndY=-9.5 EndZ=0
    g2: LineSegment StartX=0 StartY=-9.5 StartZ=0 EndX=4.42111 EndY=-13.8407 EndZ=0
    g3: LineSegment StartX=2 StartY=0 StartZ=0 EndX=2 EndY=-7.93768 EndZ=0
    g4: LineSegment StartX=2 StartY=-7.93768 StartZ=0 EndX=4.42111 EndY=-10.3148 EndZ=0
    g5: LineSegment StartX=7.87562 StartY=-10.8518 StartZ=0 EndX=15.5 EndY=-7 EndZ=0
    g6: LineSegment StartX=15.5 StartY=-7 StartZ=0 EndX=15.5 EndY=-1 EndZ=0
    g7: LineSegment StartX=15.5 StartY=-1 StartZ=0 EndX=19.5 EndY=-1 EndZ=0
    g8: LineSegment StartX=19.5 StartY=-1 StartZ=0 EndX=20.5 EndY=-3 EndZ=0
    g9: LineSegment StartX=20.5 StartY=-3 StartZ=0 EndX=20.5 EndY=-8 EndZ=0
    g10: LineSegment StartX=20.5 StartY=-8 StartZ=0 EndX=7.87562 EndY=-14.3777 EndZ=0
    g11: ArcOfCircle CenterX=6.52287 CenterY=-8.17409 CenterZ=0 NormalX=0 NormalY=0 NormalZ=1 AngleXU=0 Radius=2.99997 StartAngle=3.93616 EndAngle=5.18019
    g12: ArcOfCircle CenterX=6.52287 CenterY=-11.7 CenterZ=0 NormalX=0 NormalY=0 NormalZ=1 AngleXU=0 Radius=2.99998 StartAngle=3.93616 EndAngle=5.18018
  constraints (28):
    c: Coincident(g0,g-15)
    c: Coincident(g0,g-1)
    c: Coincident(g1,g0)
    c: Coincident(g1,g-13)
    c: Coincident(g2,g1)
    c: Coincident(g2,g-12)
    c: Coincident(g3,g0)
    c: Coincident(g3,g-14)
    c: Coincident(g4,g3)
    c: Coincident(g4,g-11)
    c: Coincident(g5,g-10)
    c: Coincident(g5,g-10)
    c: Coincident(g6,g5)
    c: Coincident(g6,g-4)
    c: Coincident(g7,g6)
    c: Coincident(g7,g-6)
    c: Coincident(g8,g7)
    c: Coincident(g8,g-6)
    c: Coincident(g9,g8)
    c: Coincident(g9,g-7)
    c: Coincident(g10,g9)
    c: Coincident(g10,g-8)
    c: Coincident(g11,g5)
    c: Coincident(g11,g4)
    c: Coincident(g12,g10)
    c: Coincident(g12,g2)
    c: Tangent(g11,g-9)
    c: Tangent(g12,g-8)
FEATURE [PartDesign::Pad] Pad613
  BaseFeature = -> Pad612
  Direction = (0,1,2e-16)
  Length = 5
  Length2 = 10
  Placement = pos=(0,0,0) rot=(1,0,0;1.5708rad)
  Profile = -> Sketch921
  ReferenceAxis = -> Sketch921 [N_Axis]
  Refine = true
  Suppressed = false
  Type = 0
FEATURE [Sketcher::SketchObject] Sketch922
  ArcFitTolerance = 1e-06
  AttachmentSupport = -> [Pad613]
  ExternalGeometry = -> [Pad613]
  FullyConstrained = true
  MakeInternals = false
  MapMode = 5
  Placement = pos=(0,13,3.1e-15) rot=(-1,0,0;1.5708rad)
  sketch-geometry (12):
    g0: LineSegment StartX=2 StartY=0 StartZ=0 EndX=0 EndY=0 EndZ=0
    g1: LineSegment StartX=15.5 StartY=-7 StartZ=0 EndX=15.5 EndY=-1 EndZ=0
    g2: LineSegment StartX=15.5 StartY=-1 StartZ=0 EndX=19.5 EndY=-1 EndZ=0
    g3: LineSegment StartX=19.5 StartY=-1 StartZ=0 EndX=19.5 EndY=-8.50519 EndZ=0
    g4: LineSegment StartX=19.5 StartY=-8.50519 StartZ=0 EndX=7.87562 EndY=-14.3777 EndZ=0
    g5: LineSegment StartX=15.5 StartY=-7 StartZ=0 EndX=7.87562 EndY=-10.8518 EndZ=0
    g6: LineSegment StartX=0 StartY=0 StartZ=0 EndX=0 EndY=-9.5 EndZ=0
    g7: ArcOfCircle CenterX=6.52287 CenterY=-8.17409 CenterZ=0 NormalX=0 NormalY=0 NormalZ=1 AngleXU=0 Radius=2.99997 StartAngle=3.93616 EndAngle=5.18019
    g8: ArcOfCircle CenterX=6.52287 CenterY=-11.7 CenterZ=0 NormalX=0 NormalY=0 NormalZ=1 AngleXU=0 Radius=2.99998 StartAngle=3.93616 EndAngle=5.18018
    g9: LineSegment StartX=2 StartY=0 StartZ=0 EndX=2 EndY=-7.93768 EndZ=0
    g10: LineSegment StartX=2 StartY=-7.93768 StartZ=0 EndX=4.42111 EndY=-10.3148 EndZ=0
    g11: LineSegment StartX=4.42111 StartY=-13.8407 StartZ=0 EndX=0 EndY=-9.5 EndZ=0
  constraints (25):
    c: Coincident(g0,g-5)
    c: Coincident(g0,g-1)
    c: Coincident(g1,g-12)
    c: Coincident(g1,g-13)
    c: Coincident(g2,g1)
    c: Coincident(g2,g-13)
    c: Coincident(g3,g2)
    c: PointOnObject(g3,g-11)
    c: Vertical(g3)
    c: Coincident(g4,g3)
    c: Coincident(g4,g-11)
    c: Coincident(g5,g1)
    c: Coincident(g5,g-9)
    c: Coincident(g6,g0)
    c: Coincident(g6,g-6)
    c: Coincident(g7,g5)
    c: Coincident(g8,g4)
    c: Tangent(g7,g-8) = -1.5708
    c: Tangent(g8,g-10) = -1.5708
    c: Coincident(g9,g0)
    c: Coincident(g9,g-7)
    c: Coincident(g10,g9)
    c: Coincident(g10,g7)
    c: Coincident(g11,g8)
    c: Coincident(g11,g6)
FEATURE [PartDesign::Pad] Pad614
  BaseFeature = -> Pad613
  Direction = (0,1,2e-16)
  Length = 5
  Length2 = 10
  Placement = pos=(0,0,0) rot=(1,0,0;1.5708rad)
  Profile = -> Sketch922
  ReferenceAxis = -> Sketch922 [N_Axis]
  Refine = true
  Suppressed = false
  Type = 0
FEATURE [Sketcher::SketchObject] Sketch923
  ArcFitTolerance = 1e-06
  AttachmentSupport = -> [Pad614]
  ExternalGeometry = -> [Pad614]
  FullyConstrained = true
  MakeInternals = false
  MapMode = 5
  Placement = pos=(0,18,4.1e-15) rot=(-1,0,0;1.5708rad)
  sketch-geometry (6):
    g0: LineSegment StartX=15.5 StartY=-1 StartZ=0 EndX=15.5 EndY=-7 EndZ=0
    g1: LineSegment StartX=15.5 StartY=-1 StartZ=0 EndX=2 EndY=-1 EndZ=0
    g2: LineSegment StartX=2 StartY=-1 StartZ=0 EndX=2 EndY=-7.93768 EndZ=0
    g3: LineSegment StartX=2 StartY=-7.93768 StartZ=0 EndX=4.42111 EndY=-10.3148 EndZ=0
    g4: LineSegment StartX=7.87562 StartY=-10.8518 StartZ=0 EndX=15.5 EndY=-7 EndZ=0
    g5: ArcOfCircle CenterX=6.52287 CenterY=-8.1741 CenterZ=0 NormalX=0 NormalY=0 NormalZ=1 AngleXU=0 Radius=2.99996 StartAngle=3.93616 EndAngle=5.18019
  constraints (14):
    c: Coincident(g0,g-3)
    c: Coincident(g0,g-4)
    c: Coincident(g1,g0)
    c: PointOnObject(g1,g-7)
    c: Horizontal(g1)
    c: Coincident(g2,g1)
    c: Coincident(g2,g-7)
    c: Coincident(g3,g2)
    c: Coincident(g3,g-6)
    c: Coincident(g4,g-5)
    c: Coincident(g4,g0)
    c: Coincident(g5,g3)
    c: Coincident(g5,g4)
    c: Tangent(g5,g-5)
FEATURE [PartDesign::Pad] Pad615
  BaseFeature = -> Pad614
  Direction = (0,1,2e-16)
  Length = 2
  Length2 = 10
  Placement = pos=(0,0,0) rot=(1,0,0;1.5708rad)
  Profile = -> Sketch923
  ReferenceAxis = -> Sketch923 [N_Axis]
  Refine = true
  Reversed = true
  Suppressed = false
  Type = 0
FEATURE [Sketcher::SketchObject] Sketch924
  ArcFitTolerance = 1e-06
  AttachmentSupport = -> [Pad615]
  ExternalGeometry = -> [Pad615]
  FullyConstrained = true
  MakeInternals = false
  MapMode = 5
  Placement = pos=(7.38793,1.616e-12,14.6241) rot=(0.231768,0,0.972771;3.14159rad)
  sketch-geometry (12):
    g0: LineSegment StartX=-14.6903 StartY=-3 StartZ=0 EndX=-0.546395 EndY=-3 EndZ=0
    g1: LineSegment StartX=-0.546395 StartY=-2.5 StartZ=0 EndX=-14.6903 EndY=-2.5 EndZ=0
    g2: LineSegment StartX=-14.6903 StartY=-2.5 StartZ=0 EndX=-14.6903 EndY=-3 EndZ=0
    g3: LineSegment StartX=-14.6903 StartY=-8 StartZ=0 EndX=-14.6903 EndY=-8.5 EndZ=0
    g4: LineSegment StartX=-14.6903 StartY=-8.5 StartZ=0 EndX=-0.546395 EndY=-8.5 EndZ=0
    g5: LineSegment StartX=-0.546395 StartY=-8 StartZ=0 EndX=-14.6903 EndY=-8 EndZ=0
    g6: LineSegment StartX=-13.5699 StartY=-13 StartZ=0 EndX=-13.5699 EndY=-13.5 EndZ=0
    g7: LineSegment StartX=-13.5699 StartY=-13.5 StartZ=0 EndX=-0.546395 EndY=-13.5 EndZ=0
    g8: LineSegment StartX=-0.546395 StartY=-13 StartZ=0 EndX=-13.5699 EndY=-13 EndZ=0
    g9: ArcOfCircle CenterX=-0.546395 CenterY=-13.25 CenterZ=0 NormalX=0 NormalY=0 NormalZ=1 AngleXU=0 Radius=0.25 StartAngle=4.71239 EndAngle=7.85398
    g10: ArcOfCircle CenterX=-0.546395 CenterY=-8.25 CenterZ=0 NormalX=0 NormalY=0 NormalZ=1 AngleXU=0 Radius=0.25 StartAngle=4.71239 EndAngle=7.85398
    g11: ArcOfCircle CenterX=-0.546395 CenterY=-2.75 CenterZ=0 NormalX=0 NormalY=0 NormalZ=1 AngleXU=0 Radius=0.25 StartAngle=4.71239 EndAngle=7.85398
  constraints (34):
    c: Coincident(g1,g2)
    c: Coincident(g2,g0)
    c: Horizontal(g1)
    c: Vertical(g2)
    c: Coincident(g0,g-3)
    c: DistanceY(g2,g2) = 0.5
    c: Coincident(g3,g4)
    c: Coincident(g5,g3)
    c: Vertical(g3)
    c: Horizontal(g4)
    c: Coincident(g3,g-4)
    c: DistanceY(g3,g3) = 0.5
    c: Coincident(g6,g7)
    c: Coincident(g8,g6)
    c: Vertical(g6)
    c: Horizontal(g7)
    c: Horizontal(g8)
    c: Coincident(g6,g-5)
    c: DistanceY(g6,g6) = 0.5
    c: PointOnObject(g1,g-6)
    c: PointOnObject(g8,g-8)
    c: Coincident(g5,g-8)
    c: Coincident(g9,g8)
    c: Coincident(g9,g7)
    c: Coincident(g10,g5)
    c: Coincident(g10,g4)
    c: Coincident(g11,g1)
    c: Coincident(g11,g0)
    c: PointOnObject(g11,g-6)
    c: Coincident(g0,g-7)
    c: PointOnObject(g10,g-8)
    c: PointOnObject(g4,g-8)
    c: PointOnObject(g9,g-8)
    c: PointOnObject(g7,g-8)
FEATURE [PartDesign::Pocket] Pocket424
  BaseFeature = -> Pad615
  Direction = (-0.450915,-9.84e-14,-0.892567)
  Length = 0.5
  Length2 = 5
  Placement = pos=(0,0,0) rot=(1,0,0;1.5708rad)
  Profile = -> Sketch924
  ReferenceAxis = -> Sketch924 [N_Axis]
  Refine = true
  Suppressed = false
  Type = 0
FEATURE [Sketcher::SketchObject] Sketch925
  ArcFitTolerance = 1e-06
  AttachmentSupport = -> [Pocket424]
  ExternalGeometry = -> [Pocket424]
  FullyConstrained = true
  MakeInternals = false
  MapMode = 5
  Placement = pos=(15.2,9.9e-15,-7.6) rot=(0.850651,0,0.525731;3.14159rad)
  sketch-geometry (8):
    g0: LineSegment StartX=11.8512 StartY=-3 StartZ=0 EndX=11.8512 EndY=-2.5 EndZ=0
    g1: LineSegment StartX=11.8512 StartY=-2.5 StartZ=0 EndX=9.61509 EndY=-2.5 EndZ=0
    g2: LineSegment StartX=9.61509 StartY=-2.5 StartZ=0 EndX=9.61509 EndY=-3 EndZ=0
    g3: LineSegment StartX=9.61509 StartY=-3 StartZ=0 EndX=11.8512 EndY=-3 EndZ=0
    g4: LineSegment StartX=11.8512 StartY=-8 StartZ=0 EndX=9.61509 EndY=-8 EndZ=0
    g5: LineSegment StartX=9.61509 StartY=-8 StartZ=0 EndX=9.61509 EndY=-8.5 EndZ=0
    g6: LineSegment StartX=9.61509 StartY=-8.5 StartZ=0 EndX=11.8512 EndY=-8.5 EndZ=0
    g7: LineSegment StartX=11.8512 StartY=-8.5 StartZ=0 EndX=11.8512 EndY=-8 EndZ=0
  constraints (22):
    c: Coincident(g0,g1)
    c: Coincident(g1,g2)
    c: Coincident(g2,g3)
    c: Coincident(g3,g0)
    c: Vertical(g0)
    c: Vertical(g2)
    c: Horizontal(g1)
    c: Horizontal(g3)
    c: Coincident(g0,g-3)
    c: PointOnObject(g1,g-6)
    c: Coincident(g4,g5)
    c: Coincident(g5,g6)
    c: Coincident(g6,g7)
    c: Coincident(g7,g4)
    c: Horizontal(g4)
    c: Horizontal(g6)
    c: Vertical(g5)
    c: Vertical(g7)
    c: Coincident(g4,g-4)
    c: PointOnObject(g5,g-6)
    c: DistanceY(g5,g5) = 0.5
    c: DistanceY(g2,g2) = 0.5
FEATURE [PartDesign::Pocket] Pocket425
  BaseFeature = -> Pocket424
  Direction = (-0.894427,0,0.447214)
  Length = 0.5
  Length2 = 5
  Placement = pos=(0,0,0) rot=(1,0,0;1.5708rad)
  Profile = -> Sketch925
  ReferenceAxis = -> Sketch925 [N_Axis]
  Refine = true
  Suppressed = false
  Type = 0
FEATURE [Sketcher::SketchObject] Sketch926
  ArcFitTolerance = 1e-06
  AttachmentSupport = -> [Pocket425]
  ExternalGeometry = -> [Pocket425]
  FullyConstrained = true
  MakeInternals = false
  MapMode = 5
  Placement = pos=(19.5,0,0) rot=(0.707107,0,0.707107;3.14159rad)
  sketch-geometry (4):
    g0: LineSegment StartX=8.50519 StartY=-13.5 StartZ=0 EndX=8.50519 EndY=-13 EndZ=0
    g1: LineSegment StartX=8.50519 StartY=-13 StartZ=0 EndX=1 EndY=-13 EndZ=0
    g2: LineSegment StartX=1 StartY=-13 StartZ=0 EndX=1 EndY=-13.5 EndZ=0
    g3: LineSegment StartX=1 StartY=-13.5 StartZ=0 EndX=8.50519 EndY=-13.5 EndZ=0
  constraints (10):
    c: Coincident(g0,g1)
    c: Coincident(g1,g2)
    c: Coincident(g2,g3)
    c: Coincident(g3,g0)
    c: Vertical(g0)
    c: Vertical(g2)
    c: Horizontal(g1)
    c: Horizontal(g3)
    c: Coincident(g0,g-3)
    c: Coincident(g1,g-5)
FEATURE [PartDesign::Pocket] Pocket426
  BaseFeature = -> Pocket425
  Direction = (-1,0,2e-16)
  Length = 0.5
  Length2 = 5
  Placement = pos=(0,0,0) rot=(1,0,0;1.5708rad)
  Profile = -> Sketch926
  ReferenceAxis = -> Sketch926 [N_Axis]
  Refine = true
  Suppressed = false
  Type = 0
FEATURE [Sketcher::SketchObject] Sketch927
  ArcFitTolerance = 1e-06
  AttachmentSupport = -> [Pocket426]
  ExternalGeometry = -> [Pocket426]
  FullyConstrained = true
  MakeInternals = false
  MapMode = 5
  Placement = pos=(20.5,0,0) rot=(0.707107,0,0.707107;3.14159rad)
  sketch-geometry (8):
    g0: LineSegment StartX=3 StartY=-2.5 StartZ=0 EndX=3 EndY=-3 EndZ=0
    g1: LineSegment StartX=3 StartY=-3 StartZ=0 EndX=8 EndY=-3 EndZ=0
    g2: LineSegment StartX=8 StartY=-3 StartZ=0 EndX=8 EndY=-2.5 EndZ=0
    g3: LineSegment StartX=8 StartY=-2.5 StartZ=0 EndX=3 EndY=-2.5 EndZ=0
    g4: LineSegment StartX=3 StartY=-8 StartZ=0 EndX=3 EndY=-8.5 EndZ=0
    g5: LineSegment StartX=3 StartY=-8.5 StartZ=0 EndX=8 EndY=-8.5 EndZ=0
    g6: LineSegment StartX=8 StartY=-8.5 StartZ=0 EndX=8 EndY=-8 EndZ=0
    g7: LineSegment StartX=8 StartY=-8 StartZ=0 EndX=3 EndY=-8 EndZ=0
  constraints (20):
    c: Coincident(g0,g1)
    c: Coincident(g1,g2)
    c: Coincident(g2,g3)
    c: Coincident(g3,g0)
    c: Vertical(g0)
    c: Vertical(g2)
    c: Horizontal(g1)
    c: Horizontal(g3)
    c: Coincident(g0,g-5)
    c: Coincident(g1,g-6)
    c: Coincident(g4,g5)
    c: Coincident(g5,g6)
    c: Coincident(g6,g7)
    c: Coincident(g7,g4)
    c: Vertical(g4)
    c: Vertical(g6)
    c: Horizontal(g5)
    c: Horizontal(g7)
    c: Coincident(g4,g-4)
    c: Coincident(g5,g-3)
FEATURE [PartDesign::Pocket] Pocket427
  BaseFeature = -> Pocket426
  Direction = (-1,0,2e-16)
  Length = 0.5
  Length2 = 5
  Placement = pos=(0,0,0) rot=(1,0,0;1.5708rad)
  Profile = -> Sketch927
  ReferenceAxis = -> Sketch927 [N_Axis]
  Refine = true
  Suppressed = false
  Type = 0
FEATURE [Sketcher::SketchObject] Sketch928
  ArcFitTolerance = 1e-06
  AttachmentSupport = -> [Pocket427]
  ExternalGeometry = -> [Pocket427]
  FullyConstrained = true
  MakeInternals = false
  MapMode = 5
  Placement = pos=(0,0,1) rot=(1,0,0;3.14159rad)
  sketch-geometry (12):
    g0: LineSegment StartX=19 StartY=-13.5 StartZ=0 EndX=19 EndY=-13 EndZ=0
    g1: LineSegment StartX=19 StartY=-13 StartZ=0 EndX=15.5 EndY=-13 EndZ=0
    g2: LineSegment StartX=15.5 StartY=-13 StartZ=0 EndX=15.5 EndY=-13.5 EndZ=0
    g3: LineSegment StartX=15.5 StartY=-13.5 StartZ=0 EndX=19 EndY=-13.5 EndZ=0
    g4: LineSegment StartX=19.5 StartY=-8.5 StartZ=0 EndX=19.5 EndY=-8 EndZ=0
    g5: LineSegment StartX=19.5 StartY=-8 StartZ=0 EndX=15.5 EndY=-8 EndZ=0
    g6: LineSegment StartX=15.5 StartY=-8 StartZ=0 EndX=15.5 EndY=-8.5 EndZ=0
    g7: LineSegment StartX=15.5 StartY=-8.5 StartZ=0 EndX=19.5 EndY=-8.5 EndZ=0
    g8: LineSegment StartX=19.5 StartY=-3 StartZ=0 EndX=19.5 EndY=-2.5 EndZ=0
    g9: LineSegment StartX=19.5 StartY=-2.5 StartZ=0 EndX=15.5 EndY=-2.5 EndZ=0
    g10: LineSegment StartX=15.5 StartY=-2.5 StartZ=0 EndX=15.5 EndY=-3 EndZ=0
    g11: LineSegment StartX=15.5 StartY=-3 StartZ=0 EndX=19.5 EndY=-3 EndZ=0
  constraints (30):
    c: Coincident(g0,g1)
    c: Coincident(g1,g2)
    c: Coincident(g2,g3)
    c: Coincident(g3,g0)
    c: Vertical(g2)
    c: Horizontal(g1)
    c: Horizontal(g3)
    c: Coincident(g0,g-6)
    c: PointOnObject(g1,g-7)
    c: Coincident(g4,g5)
    c: Coincident(g5,g6)
    c: Coincident(g6,g7)
    c: Coincident(g7,g4)
    c: Vertical(g6)
    c: Horizontal(g5)
    c: Horizontal(g7)
    c: Coincident(g4,g-4)
    c: PointOnObject(g5,g-7)
    c: Coincident(g8,g9)
    c: Coincident(g9,g10)
    c: Coincident(g10,g11)
    c: Coincident(g11,g8)
    c: Vertical(g10)
    c: Horizontal(g9)
    c: Horizontal(g11)
    c: Coincident(g8,g-3)
    c: PointOnObject(g9,g-7)
    c: Coincident(g8,g-3)
    c: Coincident(g4,g-4)
    c: Coincident(g0,g-6)
FEATURE [PartDesign::Pocket] Pocket428
  BaseFeature = -> Pocket427
  Direction = (0,0,1)
  Length = 0.5
  Length2 = 5
  Placement = pos=(0,0,0) rot=(1,0,0;1.5708rad)
  Profile = -> Sketch928
  ReferenceAxis = -> Sketch928 [N_Axis]
  Refine = true
  Suppressed = false
  Type = 0
FEATURE [PartDesign::Fillet] Fillet
  Base = -> Pocket428 [Edge136,Edge74,Edge90,Edge84,Edge128,Edge24,Edge22,Edge26,Edge108,Edge114,Edge77]
  BaseFeature = -> Pocket428
  Placement = pos=(0,0,0) rot=(1,0,0;1.5708rad)
  Radius = 1
  Refine = true
  SupportTransform = false
  Suppressed = false
  UseAllEdges = false
FEATURE [Sketcher::SketchObject] Sketch929
  ArcFitTolerance = 1e-06
  AttachmentSupport = -> [Fillet]
  ExternalGeometry = -> [Fillet]
  FullyConstrained = true
  MakeInternals = false
  MapMode = 5
  Placement = pos=(0,-2,0) rot=(1,0,0;1.5708rad)
  sketch-geometry (5):
    g0: LineSegment StartX=18.5 StartY=4e-16 StartZ=0 EndX=0 EndY=0 EndZ=0
    g1: LineSegment StartX=18.5 StartY=4e-16 StartZ=0 EndX=18.5 EndY=6.5 EndZ=0
    g2: ArcOfCircle CenterX=10.8351 CenterY=-4 CenterZ=0 NormalX=0 NormalY=0 NormalZ=1 AngleXU=0 Radius=13 StartAngle=0.940228 EndAngle=1.5708
    g3: LineSegment StartX=10.8351 StartY=9 StartZ=0 EndX=0 EndY=9 EndZ=0
    g4: LineSegment StartX=0 StartY=9 StartZ=0 EndX=0 EndY=0 EndZ=0
  constraints (13):
    c: Coincident(g0,g-4)
    c: Coincident(g0,g-1)
    c: Coincident(g1,g0)
    c: Vertical(g1)
    c: Coincident(g2,g1)
    c: PointOnObject(g3,g-2)
    c: Horizontal(g3)
    c: Coincident(g4,g3)
    c: Coincident(g4,g0)
    c: DistanceY(g1,g1) = 6.5
    c: DistanceY(g4,g4) = 9
    c: Tangent(g3,g2) = -1.5708
    c: Radius(g2) = 13
FEATURE [PartDesign::Pad] Pad616
  BaseFeature = -> Fillet
  Direction = (0,-1,2e-16)
  Length = 2
  Length2 = 10
  Placement = pos=(0,0,0) rot=(1,0,0;1.5708rad)
  Profile = -> Sketch929
  ReferenceAxis = -> Sketch929 [N_Axis]
  Refine = true
  Suppressed = false
  Type = 0
FEATURE [Sketcher::SketchObject] Sketch930
  ArcFitTolerance = 1e-06
  AttachmentSupport = -> [Pad616]
  ExternalGeometry = -> [Pad616]
  FullyConstrained = true
  MakeInternals = false
  MapMode = 5
  Placement = pos=(0,0,1) rot=(1,0,0;3.14159rad)
  sketch-geometry (3):
    g0: LineSegment StartX=2 StartY=-16 StartZ=0 EndX=7 EndY=-16 EndZ=0
    g1: LineSegment StartX=7 StartY=-16 StartZ=0 EndX=2 EndY=-13.1132 EndZ=0
    g2: LineSegment StartX=2 StartY=-13.1132 StartZ=0 EndX=2 EndY=-16 EndZ=0
  constraints (8):
    c: Coincident(g0,g-3)
    c: PointOnObject(g0,g-3)
    c: Coincident(g1,g0)
    c: PointOnObject(g1,g-4)
    c: Coincident(g2,g1)
    c: Coincident(g2,g0)
    c: DistanceX(g0,g0) = 5
    c: Angle(g1,g0) = 0.523599
FEATURE [PartDesign::Pad] Pad617
  BaseFeature = -> Pad616
  Direction = (0,0,-1)
  Length = 11
  Length2 = 10
  Placement = pos=(0,0,0) rot=(1,0,0;1.5708rad)
  Profile = -> Sketch930
  ReferenceAxis = -> Sketch930 [N_Axis]
  Refine = true
  Reversed = true
  Suppressed = false
  Type = 0
FEATURE [Sketcher::SketchObject] Sketch931
  ArcFitTolerance = 1e-06
  AttachmentSupport = -> [Pad617]
  ExternalGeometry = -> [Pad617]
  FullyConstrained = true
  MakeInternals = false
  MapMode = 5
  Placement = pos=(0,0,5e-16) rot=(1,0,0;3.14159rad)
  sketch-geometry (4):
    g0: LineSegment StartX=2 StartY=-1.8e-15 StartZ=0 EndX=2 EndY=-2.88675 EndZ=0
    g1: LineSegment StartX=2 StartY=-2.88675 StartZ=0 EndX=7 EndY=-4e-16 EndZ=0
    g2: LineSegment StartX=7 StartY=0 StartZ=0 EndX=2 EndY=-1.8e-15 EndZ=0
    g3: LineSegment [constr] StartX=7 StartY=-16 StartZ=0 EndX=7 EndY=0 EndZ=0
  constraints (10):
    c: Coincident(g0,g-4)
    c: PointOnObject(g0,g-4)
    c: Coincident(g1,g0)
    c: PointOnObject(g1,g-3)
    c: Coincident(g2,g1)
    c: Coincident(g2,g0)
    c: Coincident(g3,g-5)
    c: Coincident(g3,g1)
    c: Vertical(g3)
    c: Angle(g2,g1) = 0.523599
FEATURE [PartDesign::Pad] Pad618
  BaseFeature = -> Pad617
  Direction = (0,0,-1)
  Length = 12
  Length2 = 10
  Placement = pos=(0,0,0) rot=(1,0,0;1.5708rad)
  Profile = -> Sketch931
  ReferenceAxis = -> Sketch931 [N_Axis]
  Refine = true
  Reversed = true
  Suppressed = false
  Type = 0
FEATURE [Sketcher::SketchObject] Sketch932
  ArcFitTolerance = 1e-06
  AttachmentSupport = -> [Pad618]
  ExternalGeometry = -> [Pad618]
  FullyConstrained = true
  MakeInternals = false
  MapMode = 5
  Placement = pos=(0,-2,0) rot=(1,0,0;1.5708rad)
  sketch-geometry (3):
    g0: LineSegment StartX=0 StartY=9.5 StartZ=0 EndX=4.42111 EndY=13.8407 EndZ=0
    g1: LineSegment StartX=4.42111 StartY=13.8407 StartZ=0 EndX=0 EndY=13.8407 EndZ=0
    g2: LineSegment StartX=0 StartY=13.8407 StartZ=0 EndX=0 EndY=9.5 EndZ=0
  constraints (7):
    c: Coincident(g0,g-3)
    c: Coincident(g0,g-3)
    c: Coincident(g1,g0)
    c: Horizontal(g1)
    c: Coincident(g2,g1)
    c: Coincident(g2,g0)
    c: Vertical(g2)
FEATURE [PartDesign::Pocket] Pocket429
  BaseFeature = -> Pad618
  Direction = (0,1,-2e-16)
  Length = 18
  Length2 = 5
  Placement = pos=(0,0,0) rot=(1,0,0;1.5708rad)
  Profile = -> Sketch932
  ReferenceAxis = -> Sketch932 [N_Axis]
  Refine = true
  Suppressed = false
  Type = 0
FEATURE [PartDesign::Chamfer] Chamfer039
  Angle = 60
  Base = -> Pocket429 [Edge23]
  BaseFeature = -> Pocket429
  ChamferType = 2
  FlipDirection = false
  Placement = pos=(0,0,0) rot=(1,0,0;1.5708rad)
  Refine = true
  Size = 4.3
  Size2 = 1
  SupportTransform = false
  Suppressed = false
  UseAllEdges = false
FEATURE [Sketcher::SketchObject] Sketch933
  ArcFitTolerance = 1e-06
  AttachmentSupport = -> [Chamfer039]
  ExternalGeometry = -> [Chamfer039]
  FullyConstrained = true
  MakeInternals = false
  MapMode = 5
  Placement = pos=(0,18,0) rot=(-1,0,0;1.5708rad)
  sketch-geometry (4):
    g0: LineSegment StartX=2 StartY=0 StartZ=0 EndX=0 EndY=0 EndZ=0
    g1: LineSegment StartX=0 StartY=0 StartZ=0 EndX=0 EndY=-1 EndZ=0
    g2: LineSegment StartX=0 StartY=-1 StartZ=0 EndX=2 EndY=-1 EndZ=0
    g3: LineSegment StartX=2 StartY=-1 StartZ=0 EndX=2 EndY=0 EndZ=0
  constraints (10):
    c: Coincident(g0,g1)
    c: Coincident(g1,g2)
    c: Coincident(g2,g3)
    c: Coincident(g3,g0)
    c: Horizontal(g0)
    c: Horizontal(g2)
    c: Vertical(g1)
    c: Coincident(g0,g-4)
    c: PointOnObject(g1,g-2)
    c: Coincident(g2,g-4)
FEATURE [PartDesign::Pocket] Pocket430
  BaseFeature = -> Chamfer039
  Direction = (0,-1,-2e-16)
  Length = 21
  Length2 = 5
  Placement = pos=(0,0,0) rot=(1,0,0;1.5708rad)
  Profile = -> Sketch933
  ReferenceAxis = -> Sketch933 [N_Axis]
  Refine = true
  Suppressed = false
  Type = 0
FEATURE [Sketcher::SketchObject] Sketch934
  ArcFitTolerance = 1e-06
  AttachmentSupport = -> [Pocket430]
  ExternalGeometry = -> [Pocket430]
  FullyConstrained = true
  MakeInternals = false
  MapMode = 5
  Placement = pos=(0,1.3e-15,0) rot=(-1,0,0;1.5708rad)
  sketch-geometry (3):
    g0: LineSegment StartX=2 StartY=-1 StartZ=0 EndX=7 EndY=0 EndZ=0
    g1: LineSegment StartX=7 StartY=0 StartZ=0 EndX=2 EndY=0 EndZ=0
    g2: LineSegment StartX=2 StartY=0 StartZ=0 EndX=2 EndY=-1 EndZ=0
  constraints (6):
    c: Coincident(g0,g-4)
    c: Coincident(g0,g-3)
    c: Coincident(g1,g0)
    c: Coincident(g1,g-4)
    c: Coincident(g2,g1)
    c: Coincident(g2,g0)
FEATURE [PartDesign::Pocket] Pocket431
  BaseFeature = -> Pocket430
  Direction = (0,-1,-2e-16)
  Length = 5
  Length2 = 5
  Placement = pos=(0,0,0) rot=(1,0,0;1.5708rad)
  Profile = -> Sketch934
  ReferenceAxis = -> Sketch934 [N_Axis]
  Refine = true
  Suppressed = false
  Type = 0
FEATURE [PartDesign::Pocket] Pocket432
  BaseFeature = -> Pocket431
  Direction = (0,-1,-2e-16)
  Length = 5
  Length2 = 5
  Placement = pos=(0,0,0) rot=(1,0,0;1.5708rad)
  Profile = -> Sketch934
  ReferenceAxis = -> Sketch934 [N_Axis]
  Refine = true
  Reversed = true
  Suppressed = false
  Type = 0
FEATURE [PartDesign::Chamfer] Chamfer040
  Angle = 60
  Base = -> Pocket432 [Edge54]
  BaseFeature = -> Pocket432
  ChamferType = 2
  FlipDirection = false
  Placement = pos=(0,0,0) rot=(1,0,0;1.5708rad)
  Refine = true
  Size = 4.3
  Size2 = 1
  SupportTransform = false
  Suppressed = false
  UseAllEdges = false
FEATURE [PartDesign::Fillet] Fillet023
  Base = -> Chamfer040 [Edge62,Edge63,Edge60,Edge84]
  BaseFeature = -> Chamfer040
  Placement = pos=(0,0,0) rot=(1,0,0;1.5708rad)
  Radius = 1.999
  Refine = true
  SupportTransform = false
  Suppressed = false
  UseAllEdges = false
FEATURE [Sketcher::SketchObject] Sketch935
  ArcFitTolerance = 1e-06
  AttachmentSupport = -> [Fillet023]
  ExternalGeometry = -> [Fillet023]
  FullyConstrained = true
  MakeInternals = false
  MapMode = 5
  Placement = pos=(0,-4,0) rot=(1,0,0;1.5708rad)
  sketch-geometry (3):
    g0: Circle CenterX=11.25 CenterY=3.7 CenterZ=0 NormalX=0 NormalY=0 NormalZ=1 AngleXU=0 Radius=2.55
    g1: LineSegment [constr] StartX=11.25 StartY=3.7 StartZ=0 EndX=11.25 EndY=6.25 EndZ=0
    g2: LineSegment [constr] StartX=11.25 StartY=3.7 StartZ=0 EndX=13.8 EndY=3.7 EndZ=0
  constraints (9):
    c: Radius(g0) = 2.55
    c: Coincident(g1,g0)
    c: PointOnObject(g1,g0)
    c: Vertical(g1)
    c: DistanceY(g1,g-3) = 2.75
    c: Coincident(g2,g0)
    c: PointOnObject(g2,g0)
    c: Horizontal(g2)
    c: DistanceX(g2,g-4) = 4.7
FEATURE [PartDesign::Pocket] Pocket433
  BaseFeature = -> Fillet023
  Direction = (0,1,-2e-16)
  Length = 5
  Length2 = 5
  Placement = pos=(0,0,0) rot=(1,0,0;1.5708rad)
  Profile = -> Sketch935
  ReferenceAxis = -> Sketch935 [N_Axis]
  Refine = true
  Suppressed = false
  Type = 0
FEATURE [Sketcher::SketchObject] Sketch936
  ArcFitTolerance = 1e-06
  AttachmentSupport = -> [Pocket433]
  ExternalGeometry = -> [Pocket433]
  FullyConstrained = true
  MakeInternals = false
  MapMode = 5
  Placement = pos=(0,18,0) rot=(-1,0,0;1.5708rad)
  sketch-geometry (3):
    g0: LineSegment StartX=13.5 StartY=-1 StartZ=0 EndX=11.5 EndY=-3.5 EndZ=0
    g1: LineSegment StartX=11.5 StartY=-3.5 StartZ=0 EndX=9.5 EndY=-1 EndZ=0
    g2: LineSegment StartX=9.5 StartY=-1 StartZ=0 EndX=13.5 EndY=-1 EndZ=0
  constraints (9):
    c: PointOnObject(g0,g-3)
    c: Coincident(g1,g0)
    c: PointOnObject(g1,g-3)
    c: DistanceX(g0,g-3) = 5
    c: DistanceX(g1,g0) = 4
    c: DistanceX(g0,g0) = 2
    c: DistanceY(g0,g0) = 2.5
    c: Coincident(g2,g1)
    c: Coincident(g2,g0)
FEATURE [PartDesign::Pocket] Pocket434
  BaseFeature = -> Pocket433
  Direction = (0,-1,-2e-16)
  Length = 5
  Length2 = 5
  Placement = pos=(0,0,0) rot=(1,0,0;1.5708rad)
  Profile = -> Sketch936
  ReferenceAxis = -> Sketch936 [N_Axis]
  Refine = true
  Suppressed = false
  Type = 0
FEATURE [PartDesign::Fillet] Fillet024
  Base = -> Pocket434 [Edge50,Edge118,Edge160]
  BaseFeature = -> Pocket434
  Placement = pos=(0,0,0) rot=(1,0,0;1.5708rad)
  Radius = 0.5
  Refine = true
  SupportTransform = false
  Suppressed = false
  UseAllEdges = false
FEATURE [Sketcher::SketchObject] Sketch937
  ArcFitTolerance = 1e-06
  AttachmentSupport = -> [Fillet024]
  ExternalGeometry = -> [Fillet024]
  FullyConstrained = true
  MakeInternals = false
  MapMode = 5
  Placement = pos=(0,0,0) rot=(0.707107,0,-0.707107;3.14159rad)
  sketch-geometry (2):
    g0: Circle CenterX=-5.025 CenterY=-7 CenterZ=0 NormalX=0 NormalY=0 NormalZ=1 AngleXU=0 Radius=1.925
    g1: LineSegment [constr] StartX=-5.025 StartY=-7 StartZ=0 EndX=-3.1 EndY=-7 EndZ=0
  constraints (7):
    c: Diameter(g0) = 3.85
    c: Coincident(g1,g0)
    c: PointOnObject(g1,g0)
    c: Horizontal(g1)
    c: DistanceY(g-3,g-3) = 13.4
    c: DistanceY(g0,g-3) = 6.7
    c: DistanceX(g1,g-4) = 2.1
FEATURE [PartDesign::Pad] Pad619
  BaseFeature = -> Fillet024
  Direction = (-1,0,-2e-16)
  Length = 11
  Length2 = 10
  Placement = pos=(0,0,0) rot=(1,0,0;1.5708rad)
  Profile = -> Sketch937
  ReferenceAxis = -> Sketch937 [N_Axis]
  Refine = true
  Suppressed = false
  Type = 0
FEATURE [Sketcher::SketchObject] Sketch938
  ArcFitTolerance = 1e-06
  AttachmentSupport = -> [Pad619]
  ExternalGeometry = -> [Pad619]
  FullyConstrained = true
  MakeInternals = false
  MapMode = 5
  Placement = pos=(-11,0,0) rot=(0.707107,0,-0.707107;3.14159rad)
  sketch-geometry (1):
    g0: Circle CenterX=-5.025 CenterY=-7 CenterZ=0 NormalX=0 NormalY=0 NormalZ=1 AngleXU=0 Radius=1
  constraints (2):
    c: Coincident(g0,g-3)
    c: Diameter(g0) = 2
FEATURE [PartDesign::Pad] Pad620
  BaseFeature = -> Pad619
  Direction = (-1,0,-2e-16)
  Length = 1.5
  Length2 = 10
  Placement = pos=(0,0,0) rot=(1,0,0;1.5708rad)
  Profile = -> Sketch938
  ReferenceAxis = -> Sketch938 [N_Axis]
  Refine = true
  Suppressed = false
  Type = 0
FEATURE [PartDesign::Chamfer] Chamfer041
  Angle = 45
  Base = -> Pad620 [Edge100]
  BaseFeature = -> Pad620
  ChamferType = 0
  FlipDirection = false
  Placement = pos=(0,0,0) rot=(1,0,0;1.5708rad)
  Refine = true
  Size = 0.9
  Size2 = 1
  SupportTransform = false
  Suppressed = false
  UseAllEdges = false
FEATURE [Sketcher::SketchObject] Sketch939
  ArcFitTolerance = 1e-06
  AttachmentSupport = -> [Chamfer041]
  ExternalGeometry = -> [Chamfer041]
  FullyConstrained = true
  MakeInternals = false
  MapMode = 5
  Placement = pos=(-12.5,0,0) rot=(0.707107,0,-0.707107;3.14159rad)
  sketch-geometry (1):
    g0: Circle CenterX=-5.025 CenterY=-7 CenterZ=0 NormalX=0 NormalY=0 NormalZ=1 AngleXU=0 Radius=1.925
  constraints (2):
    c: Coincident(g0,g-4)
    c: Equal(g0,g-4)
FEATURE [PartDesign::Pad] Pad621
  BaseFeature = -> Chamfer041
  Direction = (-1,0,-2e-16)
  Length = 2.5
  Length2 = 10
  Placement = pos=(0,0,0) rot=(1,0,0;1.5708rad)
  Profile = -> Sketch939
  ReferenceAxis = -> Sketch939 [N_Axis]
  Refine = true
  Suppressed = false
  Type = 0
FEATURE [PartDesign::Chamfer] Chamfer042
  Angle = 45
  Base = -> Pad621 [Edge183]
  BaseFeature = -> Pad621
  ChamferType = 0
  FlipDirection = false
  Placement = pos=(0,0,0) rot=(1,0,0;1.5708rad)
  Refine = true
  Size = 1
  Size2 = 1
  SupportTransform = false
  Suppressed = false
  UseAllEdges = false
FEATURE [PartDesign::Body] Body047  label="Left_Fist"
  AllowCompound = false
  Group = -> [Sketch918,Pad610,Sketch919,Pad611,Sketch920,Pad612,Sketch921,Pad613,Sketch922,Pad614,Sketch923,Pad615,Sketch924,Pocket424,Sketch925,Pocket425,Sketch926,Pocket426,Sketch927,Pocket427,Sketch928,Pocket428,Fillet,Sketch929,Pad616,Sketch930,Pad617,Sketch931,Pad618,Sketch932,Pocket429,Chamfer039,Sketch933,Pocket430,Sketch934,Pocket431,Pocket432,Chamfer040,Fillet023,Sketch935,Pocket433,Sketch936,+10 more]
  Origin = -> Origin051
  Placement = pos=(0,17.85,-5.02) rot=(0,0,1;3.14159rad)
  Tip = -> Chamfer042
FEATURE [Sketcher::SketchObject] Sketch977
  ArcFitTolerance = 1e-06
  AttachmentSupport = -> [XY_Plane054]
  FullyConstrained = true
  MakeInternals = false
  MapMode = 5
  sketch-geometry (8):
    g0: LineSegment StartX=0 StartY=0 StartZ=0 EndX=0 EndY=21.7 EndZ=0
    g1: LineSegment StartX=0 StartY=21.7 StartZ=0 EndX=26 EndY=21.7 EndZ=0
    g2: LineSegment StartX=0 StartY=0 StartZ=0 EndX=26 EndY=0 EndZ=0
    g3: LineSegment StartX=26 StartY=0 StartZ=0 EndX=26 EndY=2.9 EndZ=0
    g4: LineSegment StartX=26 StartY=2.9 StartZ=0 EndX=31.6 EndY=2.9 EndZ=0
    g5: LineSegment StartX=31.6 StartY=2.9 StartZ=0 EndX=31.6 EndY=18.8 EndZ=0
    g6: LineSegment StartX=31.6 StartY=18.8 StartZ=0 EndX=26 EndY=18.8 EndZ=0
    g7: LineSegment StartX=26 StartY=21.7 StartZ=0 EndX=26 EndY=18.8 EndZ=0
  constraints (23):
    c: Coincident(g0,g-1)
    c: PointOnObject(g0,g-2)
    c: DistanceY(g0,g0) = 21.7
    c: Coincident(g1,g0)
    c: Horizontal(g1)
    c: Coincident(g2,g0)
    c: PointOnObject(g2,g-1)
    c: DistanceX(g1,g1) = 26
    c: DistanceX(g2,g2) = 26
    c: Coincident(g3,g2)
    c: Vertical(g3)
    c: Coincident(g4,g3)
    c: Horizontal(g4)
    c: Coincident(g5,g4)
    c: Vertical(g5)
    c: Coincident(g6,g5)
    c: Horizontal(g6)
    c: Coincident(g7,g1)
    c: Coincident(g7,g6)
    c: Vertical(g7)
    c: DistanceY(g5,g5) = 15.9
    c: DistanceX(g4,g4) = 5.6
    c: DistanceY(g3,g3) = 2.9
FEATURE [PartDesign::Pad] Pad641
  Direction = (0,0,1)
  Length = 6
  Length2 = 10
  Profile = -> Sketch977
  ReferenceAxis = -> Sketch977 [N_Axis]
  Refine = true
  Suppressed = false
  Type = 0
FEATURE [Sketcher::SketchObject] Sketch978
  ArcFitTolerance = 1e-06
  AttachmentSupport = -> [Pad641]
  ExternalGeometry = -> [Pad641]
  FullyConstrained = true
  MakeInternals = false
  MapMode = 5
  Placement = pos=(0,0,6) rot=(0,0,1;0rad)
  sketch-geometry (4):
    g0: LineSegment StartX=0 StartY=21.7 StartZ=0 EndX=0 EndY=0 EndZ=0
    g1: LineSegment StartX=0 StartY=0 StartZ=0 EndX=26 EndY=0 EndZ=0
    g2: LineSegment StartX=26 StartY=0 StartZ=0 EndX=26 EndY=21.7 EndZ=0
    g3: LineSegment StartX=26 StartY=21.7 StartZ=0 EndX=0 EndY=21.7 EndZ=0
  constraints (10):
    c: Coincident(g0,g1)
    c: Coincident(g1,g2)
    c: Coincident(g2,g3)
    c: Coincident(g3,g0)
    c: Vertical(g0)
    c: Vertical(g2)
    c: Horizontal(g1)
    c: Horizontal(g3)
    c: Coincident(g0,g-3)
    c: Coincident(g1,g-4)
FEATURE [PartDesign::Pad] Pad642
  BaseFeature = -> Pad641
  Direction = (0,0,1)
  Length = 1
  Length2 = 10
  Profile = -> Sketch978
  ReferenceAxis = -> Sketch978 [N_Axis]
  Refine = true
  Suppressed = false
  Type = 0
FEATURE [Sketcher::SketchObject] Sketch979
  ArcFitTolerance = 1e-06
  AttachmentSupport = -> [Pad642]
  ExternalGeometry = -> [Pad642]
  FullyConstrained = true
  MakeInternals = false
  MapMode = 5
  Placement = pos=(0,0,0) rot=(1,0,0;3.14159rad)
  sketch-geometry (8):
    g0: LineSegment StartX=1.5 StartY=-2 StartZ=0 EndX=24.5 EndY=-2 EndZ=0
    g1: LineSegment StartX=24.5 StartY=-2 StartZ=0 EndX=24.5 EndY=-4.4 EndZ=0
    g2: LineSegment StartX=24.5 StartY=-4.4 StartZ=0 EndX=30.1 EndY=-4.4 EndZ=0
    g3: LineSegment StartX=30.1 StartY=-4.4 StartZ=0 EndX=30.1 EndY=-17.3 EndZ=0
    g4: LineSegment StartX=30.1 StartY=-17.3 StartZ=0 EndX=24.5 EndY=-17.3 EndZ=0
    g5: LineSegment StartX=24.5 StartY=-17.3 StartZ=0 EndX=24.5 EndY=-19.7 EndZ=0
    g6: LineSegment StartX=24.5 StartY=-19.7 StartZ=0 EndX=1.5 EndY=-19.7 EndZ=0
    g7: LineSegment StartX=1.5 StartY=-19.7 StartZ=0 EndX=1.5 EndY=-2 EndZ=0
  constraints (24):
    c: Horizontal(g0)
    c: Coincident(g1,g0)
    c: Vertical(g1)
    c: Coincident(g2,g1)
    c: Horizontal(g2)
    c: Coincident(g3,g2)
    c: Vertical(g3)
    c: Coincident(g4,g3)
    c: Horizontal(g4)
    c: Coincident(g5,g4)
    c: Vertical(g5)
    c: Coincident(g6,g5)
    c: Horizontal(g6)
    c: Coincident(g7,g6)
    c: Coincident(g7,g0)
    c: Vertical(g7)
    c: DistanceX(g-1,g0) = 1.5
    c: DistanceX(g2,g-5) = 1.5
    c: DistanceX(g0,g-5) = 1.5
    c: DistanceX(g4,g-6) = 1.5
    c: DistanceY(g-4,g5) = 2
    c: DistanceY(g0,g-3) = 2
    c: DistanceY(g1,g-5) = 1.5
    c: DistanceY(g-6,g4) = 1.5
FEATURE [PartDesign::Pocket] Pocket453
  BaseFeature = -> Pad642
  Direction = (0,0,1)
  Length = 4.5
  Length2 = 5
  Profile = -> Sketch979
  ReferenceAxis = -> Sketch979 [N_Axis]
  Refine = true
  Suppressed = false
  Type = 0
FEATURE [Sketcher::SketchObject] Sketch980
  ArcFitTolerance = 1e-06
  AttachmentSupport = -> [Pocket453]
  ExternalGeometry = -> [Pocket453]
  FullyConstrained = true
  MakeInternals = false
  MapMode = 5
  Placement = pos=(0,0,4.5) rot=(1,0,0;3.14159rad)
  sketch-geometry (4):
    g0: LineSegment StartX=1.5 StartY=-2 StartZ=0 EndX=1.5 EndY=-19.7 EndZ=0
    g1: LineSegment StartX=1.5 StartY=-19.7 StartZ=0 EndX=24.5 EndY=-19.7 EndZ=0
    g2: LineSegment StartX=24.5 StartY=-19.7 StartZ=0 EndX=24.5 EndY=-2 EndZ=0
    g3: LineSegment StartX=24.5 StartY=-2 StartZ=0 EndX=1.5 EndY=-2 EndZ=0
  constraints (10):
    c: Coincident(g0,g1)
    c: Coincident(g1,g2)
    c: Coincident(g2,g3)
    c: Coincident(g3,g0)
    c: Vertical(g0)
    c: Vertical(g2)
    c: Horizontal(g1)
    c: Horizontal(g3)
    c: Coincident(g0,g-3)
    c: Coincident(g1,g-4)
FEATURE [PartDesign::Pocket] Pocket454
  BaseFeature = -> Pocket453
  Direction = (0,0,1)
  Length = 1
  Length2 = 5
  Profile = -> Sketch980
  ReferenceAxis = -> Sketch980 [N_Axis]
  Refine = true
  Suppressed = false
  Type = 0
FEATURE [PartDesign::Chamfer] Chamfer046
  Angle = 45
  Base = -> Pocket454 [Edge4,Edge41,Edge43,Edge45,Edge2,Edge1]
  BaseFeature = -> Pocket454
  ChamferType = 0
  FlipDirection = false
  Refine = true
  Size = 0.5
  Size2 = 1
  SupportTransform = false
  Suppressed = false
  UseAllEdges = false
FEATURE [PartDesign::Chamfer] Chamfer047
  Angle = 45
  Base = -> Chamfer046 [Edge1]
  BaseFeature = -> Chamfer046
  ChamferType = 0
  FlipDirection = false
  Refine = true
  Size = 0.999
  Size2 = 1
  SupportTransform = false
  Suppressed = false
  UseAllEdges = false
FEATURE [Sketcher::SketchObject] Sketch981
  ArcFitTolerance = 1e-06
  AttachmentSupport = -> [Chamfer047]
  ExternalGeometry = -> [Chamfer047]
  FullyConstrained = true
  MakeInternals = false
  MapMode = 5
  Placement = pos=(0,0,0) rot=(1,0,0;3.14159rad)
  sketch-geometry (7):
    g0: LineSegment StartX=31.6 StartY=-6.4 StartZ=0 EndX=31.6 EndY=-15.3 EndZ=0
    g1: LineSegment StartX=31.6 StartY=-15.3 StartZ=0 EndX=39.05 EndY=-15.3 EndZ=0
    g2: LineSegment StartX=31.6 StartY=-6.4 StartZ=0 EndX=39.05 EndY=-6.4 EndZ=0
    g3: ArcOfCircle CenterX=39.05 CenterY=-10.85 CenterZ=0 NormalX=0 NormalY=0 NormalZ=1 AngleXU=0 Radius=4.45 StartAngle=4.71239 EndAngle=7.85398
    g4: LineSegment [constr] StartX=39.05 StartY=-6.4 StartZ=0 EndX=39.05 EndY=-10.85 EndZ=0
    g5: LineSegment [constr] StartX=39.05 StartY=-10.85 StartZ=0 EndX=39.05 EndY=-15.3 EndZ=0
    g6: LineSegment [constr] StartX=39.05 StartY=-10.85 StartZ=0 EndX=43.5 EndY=-10.85 EndZ=0
  constraints (21):
    c: PointOnObject(g0,g-3)
    c: PointOnObject(g0,g-3)
    c: Coincident(g1,g0)
    c: Horizontal(g1)
    c: Coincident(g2,g0)
    c: Horizontal(g2)
    c: Coincident(g3,g2)
    c: Coincident(g3,g1)
    c: Coincident(g4,g2)
    c: Coincident(g4,g3)
    c: Coincident(g5,g3)
    c: Coincident(g5,g1)
    c: Vertical(g4)
    c: Vertical(g5)
    c: Diameter(g3) = 8.9
    c: DistanceY(g-3,g-3) = 15.9
    c: DistanceY(g0,g-3) = 3.5
    c: Coincident(g6,g3)
    c: PointOnObject(g6,g3)
    c: Horizontal(g6)
    c: DistanceX(g0,g6) = 11.9
FEATURE [PartDesign::Pad] Pad643
  BaseFeature = -> Chamfer047
  Direction = (0,0,-1)
  Length = 1.8
  Length2 = 10
  Profile = -> Sketch981
  ReferenceAxis = -> Sketch981 [N_Axis]
  Refine = true
  Reversed = true
  Suppressed = false
  Type = 0
FEATURE [Sketcher::SketchObject] Sketch982
  ArcFitTolerance = 1e-06
  AttachmentSupport = -> [Pad643]
  ExternalGeometry = -> [Pad643]
  FullyConstrained = true
  MakeInternals = false
  MapMode = 5
  Placement = pos=(0,6.4,0) rot=(1,0,0;1.5708rad)
  sketch-geometry (3):
    g0: LineSegment StartX=31.6 StartY=1.8 StartZ=0 EndX=33.6 EndY=1.8 EndZ=0
    g1: LineSegment StartX=33.6 StartY=1.8 StartZ=0 EndX=31.6 EndY=3.8 EndZ=0
    g2: LineSegment StartX=31.6 StartY=3.8 StartZ=0 EndX=31.6 EndY=1.8 EndZ=0
  constraints (8):
    c: Coincident(g0,g-4)
    c: PointOnObject(g0,g-4)
    c: Coincident(g1,g0)
    c: PointOnObject(g1,g-3)
    c: Coincident(g2,g1)
    c: Coincident(g2,g0)
    c: DistanceX(g0,g0) = 2
    c: Angle(g1,g0) = 0.785398
FEATURE [PartDesign::Pad] Pad644
  BaseFeature = -> Pad643
  Direction = (0,-1,2e-16)
  Length = 1.5
  Length2 = 10
  Profile = -> Sketch982
  ReferenceAxis = -> Sketch982 [N_Axis]
  Refine = true
  Reversed = true
  Suppressed = false
  Type = 0
FEATURE [Sketcher::SketchObject] Sketch983
  ArcFitTolerance = 1e-06
  AttachmentSupport = -> [Pad644]
  ExternalGeometry = -> [Pad644]
  FullyConstrained = true
  MakeInternals = false
  MapMode = 5
  Placement = pos=(0,15.3,0) rot=(0,0.707107,0.707107;3.14159rad)
  sketch-geometry (3):
    g0: LineSegment StartX=-33.6 StartY=1.8 StartZ=0 EndX=-31.6 EndY=3.8 EndZ=0
    g1: LineSegment StartX=-31.6 StartY=3.8 StartZ=0 EndX=-31.6 EndY=1.8 EndZ=0
    g2: LineSegment StartX=-31.6 StartY=1.8 StartZ=0 EndX=-33.6 EndY=1.8 EndZ=0
  constraints (6):
    c: Coincident(g0,g-5)
    c: Coincident(g0,g-5)
    c: Coincident(g1,g0)
    c: Coincident(g1,g-4)
    c: Coincident(g2,g1)
    c: Coincident(g2,g0)
FEATURE [PartDesign::Pad] Pad645
  BaseFeature = -> Pad644
  Direction = (0,1,-2e-16)
  Length = 1.5
  Length2 = 10
  Profile = -> Sketch983
  ReferenceAxis = -> Sketch983 [N_Axis]
  Refine = true
  Reversed = true
  Suppressed = false
  Type = 0
FEATURE [Sketcher::SketchObject] Sketch984
  ArcFitTolerance = 1e-06
  AttachmentSupport = -> [Pad645]
  ExternalGeometry = -> [Pad645]
  FullyConstrained = true
  MakeInternals = false
  MapMode = 5
  Placement = pos=(0,0,1.8) rot=(0,0,1;0rad)
  sketch-geometry (4):
    g0: LineSegment StartX=31.6 StartY=13.8 StartZ=0 EndX=31.6 EndY=7.9 EndZ=0
    g1: LineSegment StartX=31.6 StartY=7.9 StartZ=0 EndX=33.6 EndY=7.9 EndZ=0
    g2: LineSegment StartX=33.6 StartY=7.9 StartZ=0 EndX=33.6 EndY=13.8 EndZ=0
    g3: LineSegment StartX=33.6 StartY=13.8 StartZ=0 EndX=31.6 EndY=13.8 EndZ=0
  constraints (10):
    c: Coincident(g0,g1)
    c: Coincident(g1,g2)
    c: Coincident(g2,g3)
    c: Coincident(g3,g0)
    c: Vertical(g0)
    c: Vertical(g2)
    c: Horizontal(g1)
    c: Horizontal(g3)
    c: Coincident(g0,g-3)
    c: Coincident(g1,g-4)
FEATURE [PartDesign::Pocket] Pocket455
  BaseFeature = -> Pad645
  Direction = (0,0,-1)
  Length = 5
  Length2 = 5
  Profile = -> Sketch984
  ReferenceAxis = -> Sketch984 [N_Axis]
  Refine = true
  Suppressed = false
  Type = 0
FEATURE [Sketcher::SketchObject] Sketch985
  ArcFitTolerance = 1e-06
  AttachmentOffset = pos=(0,0,-1.5) rot=(0,0,1;0rad)
  AttachmentSupport = -> [Pocket455]
  ExternalGeometry = -> [Pocket455]
  FullyConstrained = true
  MakeInternals = false
  MapMode = 5
  Placement = pos=(31.6,0,0) rot=(0.57735,-0.57735,-0.57735;2.0944rad)
  sketch-geometry (8):
    g0: LineSegment StartX=-15.3 StartY=0 StartZ=0 EndX=-15.3 EndY=-3 EndZ=0
    g1: LineSegment StartX=-15.3 StartY=-3 StartZ=0 EndX=-6.4 EndY=-3 EndZ=0
    g2: LineSegment StartX=-6.4 StartY=-3 StartZ=0 EndX=-6.4 EndY=0 EndZ=0
    g3: LineSegment StartX=-15.3 StartY=0 StartZ=0 EndX=-13.8 EndY=0 EndZ=0
    g4: LineSegment StartX=-13.8 StartY=0 StartZ=0 EndX=-13.8 EndY=-1.5 EndZ=0
    g5: LineSegment StartX=-13.8 StartY=-1.5 StartZ=0 EndX=-7.9 EndY=-1.5 EndZ=0
    g6: LineSegment StartX=-7.9 StartY=-1.5 StartZ=0 EndX=-7.9 EndY=0 EndZ=0
    g7: LineSegment StartX=-6.4 StartY=0 StartZ=0 EndX=-7.9 EndY=0 EndZ=0
  constraints (22):
    c: Coincident(g0,g-3)
    c: Vertical(g0)
    c: Coincident(g1,g0)
    c: Horizontal(g1)
    c: Coincident(g2,g1)
    c: Coincident(g2,g-4)
    c: Vertical(g2)
    c: Coincident(g3,g0)
    c: PointOnObject(g3,g-1)
    c: Coincident(g4,g3)
    c: Vertical(g4)
    c: Coincident(g5,g4)
    c: Horizontal(g5)
    c: Coincident(g6,g5)
    c: PointOnObject(g6,g-1)
    c: Vertical(g6)
    c: Coincident(g7,g2)
    c: Coincident(g7,g6)
    c: DistanceY(g0,g0) = 3
    c: DistanceY(g0,g4) = 1.5
    c: DistanceX(g3,g3) = 1.5
    c: DistanceX(g7,g7) = 1.5
FEATURE [PartDesign::Pad] Pad646
  BaseFeature = -> Pocket455
  Direction = (-1,0,0)
  Length = 3
  Length2 = 10
  Profile = -> Sketch985
  ReferenceAxis = -> Sketch985 [N_Axis]
  Refine = true
  Reversed = true
  Suppressed = false
  Type = 0
FEATURE [Sketcher::SketchObject] Sketch986
  ArcFitTolerance = 1e-06
  AttachmentSupport = -> [Pad646]
  ExternalGeometry = -> [Pad646]
  FullyConstrained = true
  MakeInternals = false
  MapMode = 5
  Placement = pos=(0,0,0) rot=(1,0,0;3.14159rad)
  sketch-geometry (1):
    g0: Circle CenterX=39.05 CenterY=-10.85 CenterZ=0 NormalX=0 NormalY=0 NormalZ=1 AngleXU=0 Radius=3.7
  constraints (2):
    c: Coincident(g0,g-3)
    c: Diameter(g0) = 7.4
FEATURE [PartDesign::Pad] Pad647
  BaseFeature = -> Pad646
  Direction = (0,0,-1)
  Length = 4.5
  Length2 = 10
  Profile = -> Sketch986
  ReferenceAxis = -> Sketch986 [N_Axis]
  Refine = true
  Suppressed = false
  Type = 0
FEATURE [Sketcher::SketchObject] Sketch987
  ArcFitTolerance = 1e-06
  AttachmentSupport = -> [Pad647]
  ExternalGeometry = -> [Pad647]
  FullyConstrained = true
  MakeInternals = false
  MapMode = 5
  Placement = pos=(0,0,1.8) rot=(0,0,1;0rad)
  sketch-geometry (1):
    g0: Circle CenterX=39.05 CenterY=10.85 CenterZ=0 NormalX=0 NormalY=0 NormalZ=1 AngleXU=0 Radius=2.75
  constraints (2):
    c: Coincident(g0,g-3)
    c: Radius(g0) = 2.75
FEATURE [PartDesign::Pocket] Pocket456
  BaseFeature = -> Pad647
  Direction = (0,0,-1)
  Length = 5
  Length2 = 5
  Profile = -> Sketch987
  ReferenceAxis = -> Sketch987 [N_Axis]
  Refine = true
  Suppressed = false
  Type = 0
FEATURE [Sketcher::SketchObject] Sketch988
  ArcFitTolerance = 1e-06
  AttachmentSupport = -> [Pocket456]
  ExternalGeometry = -> [Pocket456]
  FullyConstrained = true
  MakeInternals = false
  MapMode = 5
  Placement = pos=(0,0,0) rot=(0.57735,-0.57735,-0.57735;2.0944rad)
  sketch-geometry (2):
    g0: ArcOfCircle CenterX=-10.85 CenterY=0 CenterZ=0 NormalX=0 NormalY=0 NormalZ=1 AngleXU=0 Radius=2 StartAngle=0 EndAngle=3.14159
    g1: LineSegment StartX=-12.85 StartY=2e-16 StartZ=0 EndX=-8.85 EndY=0 EndZ=0
  constraints (8):
    c: PointOnObject(g0,g-3)
    c: PointOnObject(g0,g-3)
    c: PointOnObject(g0,g-3)
    c: Radius(g0) = 2
    c: DistanceX(g-3,g-1) = 21.7
    c: DistanceX(g-3,g0) = 8.85
    c: Coincident(g1,g0)
    c: Coincident(g1,g0)
FEATURE [PartDesign::Pocket] Pocket457
  BaseFeature = -> Pocket456
  Direction = (1,0,0)
  Length = 1.5
  Length2 = 5
  Profile = -> Sketch988
  ReferenceAxis = -> Sketch988 [N_Axis]
  Refine = true
  Suppressed = false
  Type = 0
FEATURE [Sketcher::SketchObject] Sketch989
  ArcFitTolerance = 1e-06
  AttachmentSupport = -> [Pocket457]
  ExternalGeometry = -> [Pocket457]
  FullyConstrained = true
  MakeInternals = false
  MapMode = 5
  Placement = pos=(0,0,5.5) rot=(1,0,0;3.14159rad)
  sketch-geometry (4):
    g0: LineSegment StartX=9.7 StartY=-9.2 StartZ=0 EndX=9.7 EndY=-12.5 EndZ=0
    g1: LineSegment StartX=9.7 StartY=-12.5 StartZ=0 EndX=19.3 EndY=-12.5 EndZ=0
    g2: LineSegment StartX=19.3 StartY=-12.5 StartZ=0 EndX=19.3 EndY=-9.2 EndZ=0
    g3: LineSegment StartX=19.3 StartY=-9.2 StartZ=0 EndX=9.7 EndY=-9.2 EndZ=0
  constraints (13):
    c: Coincident(g0,g1)
    c: Coincident(g1,g2)
    c: Coincident(g2,g3)
    c: Coincident(g3,g0)
    c: Vertical(g0)
    c: Vertical(g2)
    c: Horizontal(g1)
    c: Horizontal(g3)
    c: DistanceY(g0,g0) = 3.3
    c: DistanceX(g3,g3) = 9.6
    c: DistanceX(g-1,g0) = 9.7
    c: DistanceY(g-4,g-1) = 21.7
    c: DistanceY(g0,g-1) = 9.2
FEATURE [PartDesign::Pocket] Pocket458
  BaseFeature = -> Pocket457
  Direction = (0,0,1)
  Length = 5
  Length2 = 5
  Profile = -> Sketch989
  ReferenceAxis = -> Sketch989 [N_Axis]
  Refine = true
  Suppressed = false
  Type = 1
FEATURE [Sketcher::SketchObject] Sketch990
  ArcFitTolerance = 1e-06
  AttachmentSupport = -> [Pocket458]
  ExternalGeometry = -> [Pocket458]
  FullyConstrained = true
  MakeInternals = false
  MapMode = 5
  Placement = pos=(0,0,5.5) rot=(1,0,0;3.14159rad)
  sketch-geometry (8):
    g0: LineSegment StartX=1.5 StartY=-10.1 StartZ=0 EndX=1.5 EndY=-11.6 EndZ=0
    g1: LineSegment StartX=1.5 StartY=-11.6 StartZ=0 EndX=8.7 EndY=-11.6 EndZ=0
    g2: LineSegment StartX=8.7 StartY=-11.6 StartZ=0 EndX=8.7 EndY=-14.85 EndZ=0
    g3: LineSegment StartX=8.7 StartY=-14.85 StartZ=0 EndX=9.7 EndY=-14.85 EndZ=0
    g4: LineSegment StartX=9.7 StartY=-14.85 StartZ=0 EndX=9.7 EndY=-6.85 EndZ=0
    g5: LineSegment StartX=9.7 StartY=-6.85 StartZ=0 EndX=8.7 EndY=-6.85 EndZ=0
    g6: LineSegment StartX=8.7 StartY=-6.85 StartZ=0 EndX=8.7 EndY=-10.1 EndZ=0
    g7: LineSegment StartX=8.7 StartY=-10.1 StartZ=0 EndX=1.5 EndY=-10.1 EndZ=0
  constraints (25):
    c: PointOnObject(g0,g-3)
    c: PointOnObject(g0,g-3)
    c: Coincident(g1,g0)
    c: Horizontal(g1)
    c: Coincident(g2,g1)
    c: Vertical(g2)
    c: Coincident(g3,g2)
    c: Horizontal(g3)
    c: Coincident(g4,g3)
    c: Vertical(g4)
    c: Coincident(g5,g4)
    c: Horizontal(g5)
    c: Coincident(g6,g5)
    c: Vertical(g6)
    c: Coincident(g7,g6)
    c: Coincident(g7,g0)
    c: Horizontal(g7)
    c: DistanceY(g0,g0) = 1.5
    c: DistanceX(g5,g5) = 1
    c: DistanceX(g3,g3) = 1
    c: PointOnObject(g-4,g4)
    c: DistanceY(g3,g4) = 8
    c: DistanceY(g-5,g-5) = 3.3
    c: DistanceY(g-4,g4) = 2.35
    c: DistanceY(g6,g-4) = 0.9
FEATURE [PartDesign::Pad] Pad648
  BaseFeature = -> Pocket458
  Direction = (0,0,-1)
  Length = 3.5
  Length2 = 10
  Profile = -> Sketch990
  ReferenceAxis = -> Sketch990 [N_Axis]
  Refine = true
  Suppressed = false
  Type = 0
FEATURE [Sketcher::SketchObject] Sketch991
  ArcFitTolerance = 1e-06
  AttachmentSupport = -> [Pad648]
  ExternalGeometry = -> [Pad648]
  FullyConstrained = true
  MakeInternals = false
  MapMode = 5
  Placement = pos=(0,0,5.5) rot=(1,0,0;3.14159rad)
  sketch-geometry (8):
    g0: Circle CenterX=4.85 CenterY=-4.4 CenterZ=0 NormalX=0 NormalY=0 NormalZ=1 AngleXU=0 Radius=2.1
    g1: Circle CenterX=4.85 CenterY=-17.3 CenterZ=0 NormalX=0 NormalY=0 NormalZ=1 AngleXU=0 Radius=2.1
    g2: Circle CenterX=4.85 CenterY=-4.4 CenterZ=0 NormalX=0 NormalY=0 NormalZ=1 AngleXU=0 Radius=0.75
    g3: Circle CenterX=4.85 CenterY=-17.3 CenterZ=0 NormalX=0 NormalY=0 NormalZ=1 AngleXU=0 Radius=0.75
    g4: LineSegment [constr] StartX=4.85 StartY=-4.4 StartZ=0 EndX=4.85 EndY=-2.3 EndZ=0
    g5: LineSegment [constr] StartX=4.85 StartY=-17.3 StartZ=0 EndX=4.85 EndY=-19.4 EndZ=0
    g6: LineSegment [constr] StartX=4.85 StartY=-17.3 StartZ=0 EndX=2.75 EndY=-17.3 EndZ=0
    g7: LineSegment [constr] StartX=4.85 StartY=-4.4 StartZ=0 EndX=2.75 EndY=-4.4 EndZ=0
  constraints (22):
    c: Diameter(g1) = 4.2
    c: Diameter(g0) = 4.2
    c: Coincident(g2,g0)
    c: Coincident(g3,g1)
    c: Radius(g3) = 0.75
    c: Radius(g2) = 0.75
    c: Coincident(g4,g0)
    c: PointOnObject(g4,g0)
    c: Vertical(g4)
    c: Coincident(g5,g1)
    c: PointOnObject(g5,g1)
    c: Vertical(g5)
    c: DistanceY(g4,g-1) = 2.3
    c: DistanceY(g-4,g5) = 2.3
    c: Coincident(g6,g1)
    c: PointOnObject(g6,g1)
    c: Horizontal(g6)
    c: Coincident(g7,g0)
    c: PointOnObject(g7,g0)
    c: Horizontal(g7)
    c: DistanceX(g-1,g7) = 2.75
    c: DistanceX(g-4,g6) = 2.75
FEATURE [PartDesign::Pad] Pad649
  BaseFeature = -> Pad648
  Direction = (0,0,-1)
  Length = 6
  Length2 = 10
  Profile = -> Sketch991
  ReferenceAxis = -> Sketch991 [N_Axis]
  Refine = true
  Suppressed = false
  Type = 0
FEATURE [Sketcher::SketchObject] Sketch992
  ArcFitTolerance = 1e-06
  AttachmentSupport = -> [Pad649]
  ExternalGeometry = -> [Pad649]
  FullyConstrained = true
  MakeInternals = false
  MapMode = 5
  Placement = pos=(0,0,0) rot=(1,0,0;3.14159rad)
  sketch-geometry (8):
    g0: ArcOfCircle CenterX=4.85 CenterY=-17.3 CenterZ=0 NormalX=0 NormalY=0 NormalZ=1 AngleXU=0 Radius=2.68328 StartAngle=4.24874 EndAngle=5.17604
    g1: ArcOfCircle CenterX=4.85 CenterY=-4.4 CenterZ=0 NormalX=0 NormalY=0 NormalZ=1 AngleXU=0 Radius=2.68328 StartAngle=1.10715 EndAngle=2.03444
    g2: LineSegment StartX=3.65 StartY=-19.7 StartZ=0 EndX=3.65 EndY=-19.0234 EndZ=0
    g3: LineSegment StartX=6.05 StartY=-19.7 StartZ=0 EndX=6.05 EndY=-19.0234 EndZ=0
    g4: ArcOfCircle CenterX=4.85 CenterY=-17.3 CenterZ=0 NormalX=0 NormalY=0 NormalZ=1 AngleXU=0 Radius=2.09999 StartAngle=4.10414 EndAngle=5.32064
    g5: LineSegment StartX=3.65 StartY=-2 StartZ=0 EndX=3.65 EndY=-2.67663 EndZ=0
    g6: LineSegment StartX=6.05 StartY=-2 StartZ=0 EndX=6.05 EndY=-2.67663 EndZ=0
    g7: ArcOfCircle CenterX=4.85 CenterY=-4.39999 CenterZ=0 NormalX=0 NormalY=0 NormalZ=1 AngleXU=0 Radius=2.09999 StartAngle=0.962548 EndAngle=2.17904
  constraints (26):
    c: PointOnObject(g0,g-6)
    c: PointOnObject(g0,g-6)
    c: PointOnObject(g1,g-4)
    c: PointOnObject(g1,g-4)
    c: Coincident(g1,g-3)
    c: Coincident(g0,g-5)
    c: DistanceX(g1,g-9) = 0.9
    c: DistanceX(g0,g-10) = 0.9
    c: Coincident(g2,g0)
    c: PointOnObject(g2,g-8)
    c: Vertical(g2)
    c: Coincident(g3,g0)
    c: PointOnObject(g3,g-8)
    c: Vertical(g3)
    c: Coincident(g4,g2)
    c: Coincident(g4,g3)
    c: Tangent(g-8,g4)
    c: Coincident(g5,g1)
    c: PointOnObject(g5,g-7)
    c: Vertical(g5)
    c: Coincident(g6,g1)
    c: PointOnObject(g6,g-7)
    c: Vertical(g6)
    c: Coincident(g7,g5)
    c: Coincident(g7,g6)
    c: Tangent(g7,g-7)
FEATURE [PartDesign::Pocket] Pocket459
  BaseFeature = -> Pad649
  Direction = (0,0,1)
  Length = 5.5
  Length2 = 5
  Profile = -> Sketch992
  ReferenceAxis = -> Sketch992 [N_Axis]
  Refine = true
  Suppressed = false
  Type = 0
FEATURE [Sketcher::SketchObject] Sketch993
  ArcFitTolerance = 1e-06
  AttachmentSupport = -> [Pocket459]
  ExternalGeometry = -> [Pocket459]
  FullyConstrained = true
  MakeInternals = false
  MapMode = 5
  Placement = pos=(0,0,5.5) rot=(1,0,0;3.14159rad)
  sketch-geometry (7):
    g0: Circle CenterX=20.05 CenterY=-7.2 CenterZ=0 NormalX=0 NormalY=0 NormalZ=1 AngleXU=0 Radius=0.75
    g1: Circle CenterX=20.05 CenterY=-14.5 CenterZ=0 NormalX=0 NormalY=0 NormalZ=1 AngleXU=0 Radius=0.75
    g2: LineSegment [constr] StartX=20.05 StartY=-14.5 StartZ=0 EndX=19.3 EndY=-14.5 EndZ=0
    g3: LineSegment [constr] StartX=19.3 StartY=-14.5 StartZ=0 EndX=19.3 EndY=-12.5 EndZ=0
    g4: LineSegment [constr] StartX=20.05 StartY=-14.5 StartZ=0 EndX=20.05 EndY=-13.75 EndZ=0
    g5: LineSegment [constr] StartX=20.05 StartY=-13.75 StartZ=0 EndX=20.05 EndY=-7.95 EndZ=0
    g6: LineSegment [constr] StartX=20.05 StartY=-7.2 StartZ=0 EndX=20.05 EndY=-7.95 EndZ=0
  constraints (20):
    c: Diameter(g1) = 1.5
    c: Diameter(g0) = 1.5
    c: Coincident(g2,g1)
    c: PointOnObject(g2,g1)
    c: Horizontal(g2)
    c: Coincident(g3,g2)
    c: Coincident(g3,g-3)
    c: Vertical(g3)
    c: Coincident(g4,g1)
    c: PointOnObject(g4,g1)
    c: Vertical(g4)
    c: Coincident(g5,g4)
    c: PointOnObject(g5,g0)
    c: Vertical(g5)
    c: Coincident(g6,g0)
    c: Coincident(g6,g5)
    c: Vertical(g6)
    c: DistanceY(g5,g5) = 5.8
    c: DistanceY(g3,g-3) = 3.3
    c: DistanceY(g-3,g5) = 1.25
FEATURE [PartDesign::Pad] Pad650
  BaseFeature = -> Pocket459
  Direction = (0,0,-1)
  Length = 1.5
  Length2 = 10
  Profile = -> Sketch993
  ReferenceAxis = -> Sketch993 [N_Axis]
  Refine = true
  Suppressed = false
  Type = 0
FEATURE [Sketcher::SketchObject] Sketch994
  ArcFitTolerance = 1e-06
  AttachmentSupport = -> [Pad650]
  ExternalGeometry = -> [Pad650]
  FullyConstrained = false
  MakeInternals = false
  MapMode = 5
  Placement = pos=(0,0,7) rot=(0,0,1;0rad)
  sketch-geometry (11):
    g0: LineSegment StartX=19.3 StartY=12.5 StartZ=0 EndX=4 EndY=12.5 EndZ=0
    g1: LineSegment StartX=19.3 StartY=9.2 StartZ=0 EndX=4 EndY=9.2 EndZ=0
    g2: LineSegment StartX=4 StartY=9.2 StartZ=0 EndX=4 EndY=7.7 EndZ=0
    g3: LineSegment StartX=4 StartY=7.7 StartZ=0 EndX=21.8 EndY=7.7 EndZ=0
    g4: LineSegment StartX=21.8 StartY=7.7 StartZ=0 EndX=21.8 EndY=14 EndZ=0
    g5: LineSegment StartX=21.8 StartY=14 StartZ=0 EndX=4 EndY=14 EndZ=0
    g6: LineSegment StartX=4 StartY=14 StartZ=0 EndX=4 EndY=12.5 EndZ=0
    g7: LineSegment [constr] StartX=4 StartY=12.5 StartZ=0 EndX=4 EndY=9.2 EndZ=0
    g8: LineSegment StartX=19.3 StartY=12.5 StartZ=0 EndX=20.3 EndY=12.5 EndZ=0
    g9: LineSegment StartX=20.3 StartY=12.5 StartZ=0 EndX=20.3 EndY=9.14209 EndZ=0
    g10: LineSegment StartX=20.3 StartY=9.14209 StartZ=0 EndX=19.3 EndY=9.2 EndZ=0
  constraints (29):
    c: Coincident(g0,g-4)
    c: Horizontal(g0)
    c: Coincident(g1,g-5)
    c: Horizontal(g1)
    c: Coincident(g2,g1)
    c: Vertical(g2)
    c: Coincident(g3,g2)
    c: Horizontal(g3)
    c: Coincident(g4,g3)
    c: Vertical(g4)
    c: Coincident(g5,g4)
    c: Horizontal(g5)
    c: Coincident(g6,g5)
    c: Coincident(g6,g0)
    c: Vertical(g6)
    c: DistanceY(g2,g2) = 1.5
    c: DistanceY(g6,g6) = 1.5
    c: Coincident(g7,g0)
    c: Coincident(g7,g1)
    c: Vertical(g7)
    c: DistanceX(g5,g5) = 17.8
    c: Coincident(g8,g0)
    c: Horizontal(g8)
    c: Coincident(g9,g8)
    c: Vertical(g9)
    c: Coincident(g10,g9)
    c: Coincident(g10,g1)
    c: DistanceX(g8,g8) = 1
    c: DistanceX(g8,g4) = 1.5
FEATURE [PartDesign::Pad] Pad651
  BaseFeature = -> Pad650
  Direction = (0,0,1)
  Length = 1
  Length2 = 10
  Profile = -> Sketch994
  ReferenceAxis = -> Sketch994 [N_Axis]
  Refine = true
  Suppressed = false
  Type = 0
FEATURE [Sketcher::SketchObject] Sketch995
  ArcFitTolerance = 1e-06
  AttachmentSupport = -> [Pad651]
  ExternalGeometry = -> [Pad651]
  FullyConstrained = true
  MakeInternals = false
  MapMode = 5
  Placement = pos=(0,7.7,0) rot=(1,0,0;1.5708rad)
  sketch-geometry (3):
    g0: LineSegment StartX=4 StartY=7 StartZ=0 EndX=4 EndY=8 EndZ=0
    g1: LineSegment StartX=4 StartY=8 StartZ=0 EndX=7 EndY=8 EndZ=0
    g2: LineSegment StartX=7 StartY=8 StartZ=0 EndX=4 EndY=7 EndZ=0
  constraints (7):
    c: Coincident(g0,g-3)
    c: Coincident(g1,g0)
    c: PointOnObject(g1,g-3)
    c: Coincident(g2,g1)
    c: Coincident(g2,g0)
    c: DistanceX(g1,g1) = 3
    c: Coincident(g0,g-4)
FEATURE [PartDesign::Pocket] Pocket460
  BaseFeature = -> Pad651
  Direction = (0,1,-2e-16)
  Length = 6.3
  Length2 = 5
  Profile = -> Sketch995
  ReferenceAxis = -> Sketch995 [N_Axis]
  Refine = true
  Suppressed = false
  Type = 0
FEATURE [Sketcher::SketchObject] Sketch996
  ArcFitTolerance = 1e-06
  AttachmentSupport = -> [Pocket460]
  ExternalGeometry = -> [Pocket460]
  FullyConstrained = true
  MakeInternals = false
  MapMode = 5
  Placement = pos=(0,0,7) rot=(0,0,1;0rad)
  sketch-geometry (10):
    g0: LineSegment StartX=9.7 StartY=14 StartZ=0 EndX=14.2 EndY=14 EndZ=0
    g1: LineSegment StartX=14.2 StartY=14 StartZ=0 EndX=14.2 EndY=22.5 EndZ=0
    g2: LineSegment StartX=14.2 StartY=22.5 StartZ=0 EndX=9.7 EndY=22.5 EndZ=0
    g3: LineSegment StartX=9.7 StartY=22.5 StartZ=0 EndX=9.7 EndY=14 EndZ=0
    g4: LineSegment StartX=9.7 StartY=7.7 StartZ=0 EndX=9.7 EndY=-0.8 EndZ=0
    g5: LineSegment StartX=9.7 StartY=-0.8 StartZ=0 EndX=14.2 EndY=-0.8 EndZ=0
    g6: LineSegment StartX=14.2 StartY=-0.8 StartZ=0 EndX=14.2 EndY=7.7 EndZ=0
    g7: LineSegment StartX=14.2 StartY=7.7 StartZ=0 EndX=9.7 EndY=7.7 EndZ=0
    g8: LineSegment [constr] StartX=9.7 StartY=14 StartZ=0 EndX=9.7 EndY=12.5 EndZ=0
    g9: LineSegment [constr] StartX=9.7 StartY=9.2 StartZ=0 EndX=9.7 EndY=7.7 EndZ=0
  constraints (28):
    c: Coincident(g0,g1)
    c: Coincident(g1,g2)
    c: Coincident(g2,g3)
    c: Coincident(g3,g0)
    c: Horizontal(g0)
    c: Horizontal(g2)
    c: Vertical(g1)
    c: Vertical(g3)
    c: PointOnObject(g0,g-3)
    c: Coincident(g4,g5)
    c: Coincident(g5,g6)
    c: Coincident(g6,g7)
    c: Coincident(g7,g4)
    c: Vertical(g4)
    c: Vertical(g6)
    c: Horizontal(g5)
    c: Horizontal(g7)
    c: PointOnObject(g4,g-4)
    c: DistanceX(g7,g7) = 4.5
    c: DistanceX(g0,g0) = 4.5
    c: Coincident(g8,g0)
    c: Coincident(g8,g-5)
    c: Coincident(g9,g-5)
    c: Coincident(g9,g4)
    c: Vertical(g8)
    c: Vertical(g9)
    c: DistanceY(g5,g-7) = 0.8
    c: DistanceY(g-6,g1) = 0.8
FEATURE [PartDesign::Pad] Pad652
  BaseFeature = -> Pocket460
  Direction = (0,0,1)
  Length = 0.8
  Length2 = 10
  Profile = -> Sketch996
  ReferenceAxis = -> Sketch996 [N_Axis]
  Refine = true
  Suppressed = false
  Type = 0
FEATURE [Sketcher::SketchObject] Sketch997
  ArcFitTolerance = 1e-06
  AttachmentSupport = -> [Pad652]
  ExternalGeometry = -> [Pad652]
  FullyConstrained = true
  MakeInternals = false
  MapMode = 5
  Placement = pos=(0,0,7) rot=(0,0,1;0rad)
  sketch-geometry (24):
    g0: LineSegment StartX=14.2 StartY=21.7 StartZ=0 EndX=14.2 EndY=14 EndZ=0
    g1: LineSegment StartX=14.2 StartY=14 StartZ=0 EndX=15.7 EndY=14 EndZ=0
    g2: LineSegment StartX=15.7 StartY=14 StartZ=0 EndX=15.7 EndY=21.7 EndZ=0
    g3: LineSegment StartX=15.7 StartY=21.7 StartZ=0 EndX=14.2 EndY=21.7 EndZ=0
    g4: LineSegment StartX=17.7 StartY=21.7 StartZ=0 EndX=17.7 EndY=14 EndZ=0
    g5: LineSegment StartX=17.7 StartY=14 StartZ=0 EndX=19.2 EndY=14 EndZ=0
    g6: LineSegment StartX=19.2 StartY=14 StartZ=0 EndX=19.2 EndY=21.7 EndZ=0
    g7: LineSegment StartX=19.2 StartY=21.7 StartZ=0 EndX=17.7 EndY=21.7 EndZ=0
    g8: LineSegment StartX=21.2 StartY=21.7 StartZ=0 EndX=21.2 EndY=14 EndZ=0
    g9: LineSegment StartX=21.2 StartY=14 StartZ=0 EndX=22.7 EndY=14 EndZ=0
    g10: LineSegment StartX=22.7 StartY=14 StartZ=0 EndX=22.7 EndY=21.7 EndZ=0
    g11: LineSegment StartX=22.7 StartY=21.7 StartZ=0 EndX=21.2 EndY=21.7 EndZ=0
    g12: LineSegment StartX=14.2 StartY=7.7 StartZ=0 EndX=14.2 EndY=0 EndZ=0
    g13: LineSegment StartX=14.2 StartY=0 StartZ=0 EndX=15.7 EndY=0 EndZ=0
    g14: LineSegment StartX=15.7 StartY=0 StartZ=0 EndX=15.7 EndY=7.7 EndZ=0
    g15: LineSegment StartX=15.7 StartY=7.7 StartZ=0 EndX=14.2 EndY=7.7 EndZ=0
    g16: LineSegment StartX=17.7 StartY=7.7 StartZ=0 EndX=17.7 EndY=0 EndZ=0
    g17: LineSegment StartX=17.7 StartY=0 StartZ=0 EndX=19.2 EndY=0 EndZ=0
    g18: LineSegment StartX=19.2 StartY=0 StartZ=0 EndX=19.2 EndY=7.7 EndZ=0
    g19: LineSegment StartX=19.2 StartY=7.7 StartZ=0 EndX=17.7 EndY=7.7 EndZ=0
    g20: LineSegment StartX=21.2 StartY=7.7 StartZ=0 EndX=21.2 EndY=0 EndZ=0
    g21: LineSegment StartX=21.2 StartY=0 StartZ=0 EndX=22.7 EndY=0 EndZ=0
    g22: LineSegment StartX=22.7 StartY=0 StartZ=0 EndX=22.7 EndY=7.7 EndZ=0
    g23: LineSegment StartX=22.7 StartY=7.7 StartZ=0 EndX=21.2 EndY=7.7 EndZ=0
  constraints (70):
    c: Coincident(g0,g1)
    c: Coincident(g1,g2)
    c: Coincident(g2,g3)
    c: Coincident(g3,g0)
    c: Vertical(g0)
    c: Vertical(g2)
    c: Horizontal(g1)
    c: Horizontal(g3)
    c: Coincident(g0,g-3)
    c: PointOnObject(g1,g-6)
    c: Coincident(g4,g5)
    c: Coincident(g5,g6)
    c: Coincident(g6,g7)
    c: Coincident(g7,g4)
    c: Vertical(g4)
    c: Vertical(g6)
    c: Horizontal(g5)
    c: Horizontal(g7)
    c: PointOnObject(g4,g-3)
    c: PointOnObject(g5,g-6)
    c: Coincident(g8,g9)
    c: Coincident(g9,g10)
    c: Coincident(g10,g11)
    c: Coincident(g11,g8)
    c: Vertical(g8)
    c: Vertical(g10)
    c: Horizontal(g9)
    c: Horizontal(g11)
    c: PointOnObject(g8,g-3)
    c: PointOnObject(g8,g-6)
    c: DistanceX(g3,g3) = 1.5
    c: DistanceX(g2,g4) = 2
    c: DistanceX(g7,g7) = 1.5
    c: DistanceX(g6,g8) = 2
    c: DistanceX(g8,g10) = 1.5
    c: Coincident(g12,g13)
    c: Coincident(g13,g14)
    c: Coincident(g14,g15)
    c: Coincident(g15,g12)
    c: Vertical(g12)
    c: Vertical(g14)
    c: Horizontal(g13)
    c: Horizontal(g15)
    c: Coincident(g12,g-5)
    c: PointOnObject(g13,g-4)
    c: Coincident(g16,g17)
    c: Coincident(g17,g18)
    c: Coincident(g18,g19)
    c: Coincident(g19,g16)
    c: Vertical(g16)
    c: Vertical(g18)
    c: Horizontal(g17)
    c: Horizontal(g19)
    c: PointOnObject(g16,g-5)
    c: PointOnObject(g17,g-4)
    c: DistanceX(g15,g15) = 1.5
    c: DistanceX(g14,g16) = 2
    c: DistanceX(g16,g18) = 1.5
    c: Coincident(g20,g21)
    c: Coincident(g21,g22)
    c: Coincident(g22,g23)
    c: Coincident(g23,g20)
    c: Vertical(g20)
    c: Vertical(g22)
    c: Horizontal(g21)
    c: Horizontal(g23)
    c: PointOnObject(g20,g-5)
    c: PointOnObject(g21,g-4)
    c: DistanceX(g18,g20) = 2
    c: DistanceX(g23,g23) = 1.5
FEATURE [PartDesign::Pocket] Pocket461
  BaseFeature = -> Pad652
  Direction = (0,0,-1)
  Length = 0.5
  Length2 = 5
  Profile = -> Sketch997
  ReferenceAxis = -> Sketch997 [N_Axis]
  Refine = true
  Suppressed = false
  Type = 0
FEATURE [Sketcher::SketchObject] Sketch998
  ArcFitTolerance = 1e-06
  AttachmentSupport = -> [Pocket461]
  ExternalGeometry = -> [Pocket461]
  FullyConstrained = true
  MakeInternals = false
  MapMode = 5
  Placement = pos=(0,21.7,0) rot=(0,0.707107,0.707107;3.14159rad)
  sketch-geometry (4):
    g0: LineSegment StartX=-14.2 StartY=7 StartZ=0 EndX=-14.2 EndY=0 EndZ=0
    g1: LineSegment StartX=-14.2 StartY=0 StartZ=0 EndX=-9.7 EndY=0 EndZ=0
    g2: LineSegment StartX=-9.7 StartY=0 StartZ=0 EndX=-9.7 EndY=7 EndZ=0
    g3: LineSegment StartX=-9.7 StartY=7 StartZ=0 EndX=-14.2 EndY=7 EndZ=0
  constraints (10):
    c: Coincident(g0,g1)
    c: Coincident(g1,g2)
    c: Coincident(g2,g3)
    c: Coincident(g3,g0)
    c: Vertical(g0)
    c: Vertical(g2)
    c: Horizontal(g1)
    c: Coincident(g0,g-3)
    c: PointOnObject(g1,g-4)
    c: Coincident(g2,g-3)
FEATURE [PartDesign::Pad] Pad653
  BaseFeature = -> Pocket461
  Direction = (0,1,-2e-16)
  Length = 0.8
  Length2 = 10
  Profile = -> Sketch998
  ReferenceAxis = -> Sketch998 [N_Axis]
  Refine = true
  Suppressed = false
  Type = 0
FEATURE [Sketcher::SketchObject] Sketch999
  ArcFitTolerance = 1e-06
  AttachmentSupport = -> [Pad653]
  ExternalGeometry = -> [Pad653]
  FullyConstrained = true
  MakeInternals = false
  MapMode = 5
  Placement = pos=(0,0,0) rot=(1,0,0;1.5708rad)
  sketch-geometry (4):
    g0: LineSegment StartX=9.7 StartY=7 StartZ=0 EndX=9.7 EndY=0 EndZ=0
    g1: LineSegment StartX=9.7 StartY=0 StartZ=0 EndX=14.2 EndY=0 EndZ=0
    g2: LineSegment StartX=14.2 StartY=0 StartZ=0 EndX=14.2 EndY=7 EndZ=0
    g3: LineSegment StartX=14.2 StartY=7 StartZ=0 EndX=9.7 EndY=7 EndZ=0
  constraints (10):
    c: Coincident(g0,g1)
    c: Coincident(g1,g2)
    c: Coincident(g2,g3)
    c: Coincident(g3,g0)
    c: Vertical(g0)
    c: Vertical(g2)
    c: Horizontal(g1)
    c: Coincident(g0,g-3)
    c: PointOnObject(g1,g-4)
    c: Coincident(g2,g-3)
FEATURE [PartDesign::Pad] Pad654
  BaseFeature = -> Pad653
  Direction = (0,-1,2e-16)
  Length = 0.8
  Length2 = 10
  Profile = -> Sketch999
  ReferenceAxis = -> Sketch999 [N_Axis]
  Refine = true
  Suppressed = false
  Type = 0
FEATURE [Sketcher::SketchObject] Sketch1000
  ArcFitTolerance = 1e-06
  AttachmentSupport = -> [Pad654]
  ExternalGeometry = -> [Pad654]
  FullyConstrained = true
  MakeInternals = false
  MapMode = 5
  Placement = pos=(0,0,0) rot=(1,0,0;1.5708rad)
  sketch-geometry (12):
    g0: LineSegment StartX=14.2 StartY=6.5 StartZ=0 EndX=14.2 EndY=0 EndZ=0
    g1: LineSegment StartX=14.2 StartY=0 StartZ=0 EndX=15.7 EndY=0 EndZ=0
    g2: LineSegment StartX=15.7 StartY=0 StartZ=0 EndX=15.7 EndY=6.5 EndZ=0
    g3: LineSegment StartX=15.7 StartY=6.5 StartZ=0 EndX=14.2 EndY=6.5 EndZ=0
    g4: LineSegment StartX=17.7 StartY=6.5 StartZ=0 EndX=17.7 EndY=0 EndZ=0
    g5: LineSegment StartX=17.7 StartY=0 StartZ=0 EndX=19.2 EndY=0 EndZ=0
    g6: LineSegment StartX=19.2 StartY=0 StartZ=0 EndX=19.2 EndY=6.5 EndZ=0
    g7: LineSegment StartX=19.2 StartY=6.5 StartZ=0 EndX=17.7 EndY=6.5 EndZ=0
    g8: LineSegment StartX=21.2 StartY=6.5 StartZ=0 EndX=21.2 EndY=0 EndZ=0
    g9: LineSegment StartX=21.2 StartY=0 StartZ=0 EndX=22.7 EndY=0 EndZ=0
    g10: LineSegment StartX=22.7 StartY=0 StartZ=0 EndX=22.7 EndY=6.5 EndZ=0
    g11: LineSegment StartX=22.7 StartY=6.5 StartZ=0 EndX=21.2 EndY=6.5 EndZ=0
  constraints (30):
    c: Coincident(g0,g1)
    c: Coincident(g1,g2)
    c: Coincident(g2,g3)
    c: Coincident(g3,g0)
    c: Vertical(g0)
    c: Vertical(g2)
    c: Horizontal(g1)
    c: Coincident(g0,g-4)
    c: PointOnObject(g1,g-3)
    c: Coincident(g4,g5)
    c: Coincident(g5,g6)
    c: Coincident(g6,g7)
    c: Coincident(g7,g4)
    c: Vertical(g4)
    c: Vertical(g6)
    c: Horizontal(g5)
    c: Coincident(g4,g-5)
    c: Coincident(g8,g9)
    c: Coincident(g9,g10)
    c: Coincident(g10,g11)
    c: Coincident(g11,g8)
    c: Vertical(g8)
    c: Vertical(g10)
    c: Horizontal(g9)
    c: Coincident(g8,g-6)
    c: PointOnObject(g9,g-3)
    c: Coincident(g2,g-4)
    c: Coincident(g6,g-5)
    c: Coincident(g10,g-6)
    c: PointOnObject(g4,g-3)
FEATURE [PartDesign::Pocket] Pocket462
  BaseFeature = -> Pad654
  Direction = (0,1,-2e-16)
  Length = 0.5
  Length2 = 5
  Profile = -> Sketch1000
  ReferenceAxis = -> Sketch1000 [N_Axis]
  Refine = true
  Suppressed = false
  Type = 0
FEATURE [Sketcher::SketchObject] Sketch1001
  ArcFitTolerance = 1e-06
  AttachmentSupport = -> [Pocket462]
  ExternalGeometry = -> [Pocket462]
  FullyConstrained = true
  MakeInternals = false
  MapMode = 5
  Placement = pos=(0,21.7,0) rot=(0,0.707107,0.707107;3.14159rad)
  sketch-geometry (12):
    g0: LineSegment StartX=-15.7 StartY=6.5 StartZ=0 EndX=-15.7 EndY=0 EndZ=0
    g1: LineSegment StartX=-15.7 StartY=0 StartZ=0 EndX=-14.2 EndY=0 EndZ=0
    g2: LineSegment StartX=-14.2 StartY=0 StartZ=0 EndX=-14.2 EndY=6.5 EndZ=0
    g3: LineSegment StartX=-14.2 StartY=6.5 StartZ=0 EndX=-15.7 EndY=6.5 EndZ=0
    g4: LineSegment StartX=-17.7 StartY=6.5 StartZ=0 EndX=-19.2 EndY=6.5 EndZ=0
    g5: LineSegment StartX=-19.2 StartY=6.5 StartZ=0 EndX=-19.2 EndY=0 EndZ=0
    g6: LineSegment StartX=-19.2 StartY=0 StartZ=0 EndX=-17.7 EndY=0 EndZ=0
    g7: LineSegment StartX=-17.7 StartY=0 StartZ=0 EndX=-17.7 EndY=6.5 EndZ=0
    g8: LineSegment StartX=-21.2 StartY=6.5 StartZ=0 EndX=-22.7 EndY=6.5 EndZ=0
    g9: LineSegment StartX=-22.7 StartY=6.5 StartZ=0 EndX=-22.7 EndY=0 EndZ=0
    g10: LineSegment StartX=-22.7 StartY=0 StartZ=0 EndX=-21.2 EndY=0 EndZ=0
    g11: LineSegment StartX=-21.2 StartY=0 StartZ=0 EndX=-21.2 EndY=6.5 EndZ=0
  constraints (30):
    c: Coincident(g0,g1)
    c: Coincident(g1,g2)
    c: Coincident(g2,g3)
    c: Coincident(g3,g0)
    c: Vertical(g0)
    c: Vertical(g2)
    c: Horizontal(g1)
    c: Horizontal(g3)
    c: Coincident(g0,g-6)
    c: Coincident(g1,g-3)
    c: Coincident(g4,g5)
    c: Coincident(g5,g6)
    c: Coincident(g6,g7)
    c: Coincident(g7,g4)
    c: Horizontal(g6)
    c: Vertical(g5)
    c: Vertical(g7)
    c: Coincident(g4,g-5)
    c: PointOnObject(g5,g-3)
    c: Coincident(g8,g9)
    c: Coincident(g9,g10)
    c: Coincident(g10,g11)
    c: Coincident(g11,g8)
    c: Horizontal(g10)
    c: Vertical(g9)
    c: Vertical(g11)
    c: Coincident(g8,g-4)
    c: PointOnObject(g9,g-3)
    c: Coincident(g8,g-4)
    c: Coincident(g-5,g4)
FEATURE [PartDesign::Pocket] Pocket463
  BaseFeature = -> Pocket462
  Direction = (0,-1,2e-16)
  Length = 0.5
  Length2 = 5
  Profile = -> Sketch1001
  ReferenceAxis = -> Sketch1001 [N_Axis]
  Refine = true
  Suppressed = false
  Type = 0
FEATURE [PartDesign::Chamfer] Chamfer048
  Angle = 45
  Base = -> Pocket463 [Edge30,Edge31,Edge47,Edge54,Edge59,Edge66,Edge71,Edge78,Edge84,Edge83,Edge284,Edge292,Edge206,Edge283,Edge291,Edge299,Edge210,Edge88,Edge227,Edge92,Edge22,Edge213,Edge217,Edge218,Edge223,Edge224,Edge121]
  BaseFeature = -> Pocket463
  ChamferType = 0
  FlipDirection = false
  Refine = true
  Size = 0.999
  Size2 = 1
  SupportTransform = false
  Suppressed = false
  UseAllEdges = false
FEATURE [Sketcher::SketchObject] Sketch1002
  ArcFitTolerance = 1e-06
  AttachmentSupport = -> [Chamfer048]
  ExternalGeometry = -> [Chamfer048]
  FullyConstrained = true
  MakeInternals = false
  MapMode = 5
  Placement = pos=(0,21.7,0) rot=(0,0.707107,0.707107;3.14159rad)
  sketch-geometry (2):
    g0: ArcOfCircle CenterX=-20.2 CenterY=0 CenterZ=0 NormalX=0 NormalY=0 NormalZ=1 AngleXU=0 Radius=2.85 StartAngle=0 EndAngle=3.14159
    g1: LineSegment StartX=-23.05 StartY=3e-16 StartZ=0 EndX=-17.35 EndY=0 EndZ=0
  constraints (8):
    c: PointOnObject(g0,g-5)
    c: PointOnObject(g0,g-7)
    c: Diameter(g0) = 5.7
    c: PointOnObject(g0,g-3)
    c: DistanceX(g-4,g-6) = 2
    c: DistanceX(g-4,g0) = 1
    c: Coincident(g1,g0)
    c: Coincident(g1,g0)
FEATURE [PartDesign::Pad] Pad655
  BaseFeature = -> Chamfer048
  Direction = (0,1,-2e-16)
  Length = 1
  Length2 = 10
  Profile = -> Sketch1002
  ReferenceAxis = -> Sketch1002 [N_Axis]
  Refine = true
  Suppressed = false
  Type = 0
FEATURE [PartDesign::Pad] Pad656
  BaseFeature = -> Pad655
  Direction = (0,1,-2e-16)
  Length = 1
  Length2 = 10
  Profile = -> Sketch1002
  ReferenceAxis = -> Sketch1002 [N_Axis]
  Refine = true
  Reversed = true
  Suppressed = false
  Type = 0
FEATURE [Sketcher::SketchObject] Sketch1003
  ArcFitTolerance = 1e-06
  AttachmentSupport = -> [Pad656]
  ExternalGeometry = -> [Pad656]
  FullyConstrained = true
  MakeInternals = false
  MapMode = 5
  Placement = pos=(0,0.5,0) rot=(1,0,0;1.5708rad)
  sketch-geometry (2):
    g0: ArcOfCircle CenterX=20.2 CenterY=-7.42045e-06 CenterZ=0 NormalX=0 NormalY=0 NormalZ=1 AngleXU=0 Radius=2.85 StartAngle=2.60367e-06 EndAngle=3.14159
    g1: LineSegment StartX=17.35 StartY=5.3e-15 StartZ=0 EndX=23.05 EndY=0 EndZ=0
  constraints (5):
    c: Coincident(g0,g-4)
    c: Coincident(g0,g-4)
    c: Tangent(g0,g-3)
    c: Coincident(g1,g0)
    c: Coincident(g1,g0)
FEATURE [PartDesign::Pad] Pad657
  BaseFeature = -> Pad656
  Direction = (0,-1,2e-16)
  Length = 1.5
  Length2 = 10
  Profile = -> Sketch1003
  ReferenceAxis = -> Sketch1003 [N_Axis]
  Refine = true
  Suppressed = false
  Type = 0
FEATURE [Sketcher::SketchObject] Sketch1004
  ArcFitTolerance = 1e-06
  AttachmentSupport = -> [Pad657]
  ExternalGeometry = -> [Pad657]
  FullyConstrained = true
  MakeInternals = false
  MapMode = 5
  Placement = pos=(0,-1,2e-16) rot=(1,0,0;1.5708rad)
  sketch-geometry (4):
    g0: LineSegment StartX=19.2 StartY=2.66879 StartZ=0 EndX=19.2 EndY=0 EndZ=0
    g1: LineSegment StartX=21.2 StartY=2.66879 StartZ=0 EndX=21.2 EndY=0 EndZ=0
    g2: LineSegment StartX=21.2 StartY=0 StartZ=0 EndX=19.2 EndY=0 EndZ=0
    g3: ArcOfCircle CenterX=20.2 CenterY=-7.41995e-06 CenterZ=0 NormalX=0 NormalY=0 NormalZ=1 AngleXU=0 Radius=2.85 StartAngle=1.21229 EndAngle=1.9293
  constraints (11):
    c: Coincident(g0,g-4)
    c: Vertical(g0)
    c: Coincident(g1,g-5)
    c: Vertical(g1)
    c: Coincident(g2,g1)
    c: Coincident(g2,g0)
    c: Horizontal(g2)
    c: Coincident(g3,g0)
    c: Coincident(g3,g1)
    c: Tangent(g3,g-3)
    c: PointOnObject(g0,g-1)
FEATURE [PartDesign::Pocket] Pocket464
  BaseFeature = -> Pad657
  Direction = (0,1,-2e-16)
  Length = 0.5
  Length2 = 5
  Profile = -> Sketch1004
  ReferenceAxis = -> Sketch1004 [N_Axis]
  Refine = true
  Suppressed = false
  Type = 0
FEATURE [Sketcher::SketchObject] Sketch1005
  ArcFitTolerance = 1e-06
  AttachmentSupport = -> [Pocket464]
  ExternalGeometry = -> [Pocket464]
  FullyConstrained = true
  MakeInternals = false
  MapMode = 5
  Placement = pos=(0,22.7,0) rot=(0,0.707107,0.707107;3.14159rad)
  sketch-geometry (4):
    g0: LineSegment StartX=-21.2 StartY=2.6688 StartZ=0 EndX=-21.2 EndY=-4e-16 EndZ=0
    g1: LineSegment StartX=-19.2 StartY=2.6688 StartZ=0 EndX=-19.2 EndY=-4e-16 EndZ=0
    g2: LineSegment StartX=-21.2 StartY=-4e-16 StartZ=0 EndX=-19.2 EndY=-4e-16 EndZ=0
    g3: ArcOfCircle CenterX=-20.2 CenterY=1.84568e-05 CenterZ=0 NormalX=0 NormalY=0 NormalZ=1 AngleXU=0 Radius=2.84998 StartAngle=1.21229 EndAngle=1.92931
  constraints (11):
    c: Coincident(g0,g-5)
    c: PointOnObject(g0,g-6)
    c: Vertical(g0)
    c: Coincident(g1,g-4)
    c: PointOnObject(g1,g-6)
    c: Vertical(g1)
    c: Coincident(g2,g0)
    c: Coincident(g2,g1)
    c: Coincident(g3,g0)
    c: Coincident(g3,g1)
    c: Tangent(g3,g-3)
FEATURE [PartDesign::Pocket] Pocket465
  BaseFeature = -> Pocket464
  Direction = (0,-1,2e-16)
  Length = 0.5
  Length2 = 5
  Profile = -> Sketch1005
  ReferenceAxis = -> Sketch1005 [N_Axis]
  Refine = true
  Suppressed = false
  Type = 0
FEATURE [Sketcher::SketchObject] Sketch1006
  ArcFitTolerance = 1e-06
  AttachmentSupport = -> [Pocket465]
  ExternalGeometry = -> [Pocket465]
  FullyConstrained = true
  MakeInternals = false
  MapMode = 5
  Placement = pos=(31.6,0,0) rot=(0.57735,0.57735,0.57735;2.0944rad)
  sketch-geometry (4):
    g0: LineSegment StartX=3.899 StartY=5.001 StartZ=0 EndX=3.899 EndY=-5.999 EndZ=0
    g1: LineSegment StartX=3.899 StartY=-5.999 StartZ=0 EndX=17.801 EndY=-5.999 EndZ=0
    g2: LineSegment StartX=17.801 StartY=-5.999 StartZ=0 EndX=17.801 EndY=5.001 EndZ=0
    g3: LineSegment StartX=17.801 StartY=5.001 StartZ=0 EndX=3.899 EndY=5.001 EndZ=0
  constraints (10):
    c: Coincident(g0,g1)
    c: Coincident(g1,g2)
    c: Coincident(g2,g3)
    c: Coincident(g3,g0)
    c: Vertical(g0)
    c: Vertical(g2)
    c: Horizontal(g1)
    c: Coincident(g0,g-4)
    c: Coincident(g2,g-3)
    c: DistanceY(g0,g0) = 11
FEATURE [PartDesign::Pocket] Pocket466
  BaseFeature = -> Pocket465
  Direction = (-1,0,0)
  Length = 8
  Length2 = 5
  Profile = -> Sketch1006
  ReferenceAxis = -> Sketch1006 [N_Axis]
  Refine = true
  Reversed = true
  Suppressed = false
  Type = 1
FEATURE [Sketcher::SketchObject] Sketch1007
  ArcFitTolerance = 1e-06
  AttachmentSupport = -> [Pocket466]
  ExternalGeometry = -> [Pocket466]
  FullyConstrained = true
  MakeInternals = false
  MapMode = 5
  Placement = pos=(31.6,0,0) rot=(0.57735,0.57735,0.57735;2.0944rad)
  sketch-geometry (4):
    g0: LineSegment StartX=7.949 StartY=0 StartZ=0 EndX=13.749 EndY=0 EndZ=0
    g1: LineSegment StartX=13.749 StartY=0 StartZ=0 EndX=13.749 EndY=1.4 EndZ=0
    g2: LineSegment StartX=13.749 StartY=1.4 StartZ=0 EndX=7.949 EndY=1.4 EndZ=0
    g3: LineSegment StartX=7.949 StartY=1.4 StartZ=0 EndX=7.949 EndY=0 EndZ=0
  constraints (12):
    c: Coincident(g0,g1)
    c: Coincident(g1,g2)
    c: Coincident(g2,g3)
    c: Coincident(g3,g0)
    c: Horizontal(g0)
    c: Horizontal(g2)
    c: Vertical(g1)
    c: Vertical(g3)
    c: PointOnObject(g0,g-3)
    c: DistanceX(g2,g2) = 5.8
    c: DistanceY(g3,g3) = 1.4
    c: DistanceX(g-3,g0) = 4.05
FEATURE [PartDesign::Pad] Pad658
  BaseFeature = -> Pocket466
  Direction = (1,0,0)
  Length = 1.9
  Length2 = 10
  Profile = -> Sketch1007
  ReferenceAxis = -> Sketch1007 [N_Axis]
  Refine = true
  Suppressed = false
  Type = 0
FEATURE [PartDesign::Body] Body049  label="Right_Outer_Arm"
  AllowCompound = false
  Group = -> [Sketch977,Pad641,Sketch978,Pad642,Sketch979,Pocket453,Sketch980,Pocket454,Chamfer046,Chamfer047,Sketch981,Pad643,Sketch982,Pad644,Sketch983,Pad645,Sketch984,Pocket455,Sketch985,Pad646,Sketch986,Pad647,Sketch987,Pocket456,Sketch988,Pocket457,Sketch989,Pocket458,Sketch990,Pad648,Sketch991,Pad649,Sketch992,Pocket459,Sketch993,Pad650,Sketch994,Pad651,Sketch995,Pocket460,Sketch996,Pad652,Sketch997,+23 more]
  Origin = -> Origin054
  Placement = pos=(-106,55,-5.5) rot=(0,1,0;3.14159rad)
  Tip = -> Pad658
FEATURE [Sketcher::SketchObject] Sketch1008
  ArcFitTolerance = 1e-06
  AttachmentSupport = -> [Pocket392]
  ExternalGeometry = -> [Pocket392]
  FullyConstrained = true
  MakeInternals = false
  MapMode = 5
  Placement = pos=(0,0,-3.2) rot=(0,0,1;0rad)
  sketch-geometry (2):
    g0: Circle CenterX=39.05 CenterY=10.85 CenterZ=0 NormalX=0 NormalY=0 NormalZ=1 AngleXU=0 Radius=2.65
    g1: Circle CenterX=39.05 CenterY=10.85 CenterZ=0 NormalX=0 NormalY=0 NormalZ=1 AngleXU=0 Radius=2.74999
  constraints (4):
    c: Coincident(g0,g-3)
    c: Radius(g0) = 2.65
    c: Coincident(g1,g0)
    c: Tangent(g1,g-3)
FEATURE [PartDesign::Pad] Pad659
  BaseFeature = -> Pocket392
  Direction = (0,0,1)
  Length = 5
  Length2 = 10
  Profile = -> Sketch1008
  ReferenceAxis = -> Sketch1008 [N_Axis]
  Refine = true
  Suppressed = false
  Type = 0
FEATURE [Sketcher::SketchObject] Sketch1009
  ArcFitTolerance = 1e-06
  AttachmentSupport = -> [Pad659]
  ExternalGeometry = -> [Pad659]
  FullyConstrained = true
  MakeInternals = false
  MapMode = 5
  Placement = pos=(0,0,1.8) rot=(0,0,1;0rad)
  sketch-geometry (1):
    g0: Circle CenterX=39.05 CenterY=10.85 CenterZ=0 NormalX=0 NormalY=0 NormalZ=1 AngleXU=0 Radius=2.75
  constraints (2):
    c: Coincident(g0,g-3)
    c: Radius(g0) = 2.75
FEATURE [PartDesign::SubtractiveLoft] SubtractiveLoft001
  BaseFeature = -> Pad659
  Closed = false
  Profile = -> Sketch1009
  Refine = true
  Ruled = false
  Sections = -> [Pad659]
  Suppressed = false
FEATURE [PartDesign::Body] Body043  label="Left_Outer_Arm"
  AllowCompound = false
  Group = -> [Sketch822,Pad555,Sketch823,Pad556,Sketch824,Pocket380,Sketch825,Pocket381,Chamfer030,Chamfer031,Sketch826,Pad557,Sketch827,Pad558,Sketch828,Pad559,Sketch829,Pocket382,Sketch830,Pad560,Sketch831,Pad561,Sketch832,Pocket383,Sketch833,Pocket384,Sketch834,Pocket385,Sketch835,Pad562,Sketch836,Pad563,Sketch837,Pocket386,Sketch838,Pad564,Sketch839,Pad565,Sketch840,Pocket387,Sketch841,Pad566,Sketch842,+23 more]
  Origin = -> Origin046
  Tip = -> SubtractiveLoft001
FEATURE [App::Part] Part002  label="Left_Arm"
  Group = -> [Body045,Body043,Body046,Body029,Body047]
  Origin = -> Origin047
  Placement = pos=(-106,100,-7) rot=(0,0,1;3.14159rad)
FEATURE [PartDesign::SubShapeBinder] Binder011
  BindCopyOnChange = 0
  BindMode = 2
  ClaimChildren = false
  Context = -> Part002 [Body044.Binder007.]
  Fuse = false
  MakeFace = true
  OffsetFill = false
  OffsetIntersection = false
  OffsetJoinType = 0
  OffsetOpenResult = false
  PartialLoad = false
  Refine = true
  Relative = true
  _Version = 2
FEATURE [Sketcher::SketchObject] Sketch1010
  ArcFitTolerance = 1e-06
  AttachmentSupport = -> [Binder011]
  ExternalGeometry = -> [Binder011]
  FullyConstrained = true
  MakeInternals = false
  MapMode = 5
  Placement = pos=(0,0,1e-16) rot=(1,0,0;3.14159rad)
  sketch-geometry (8):
    g0: LineSegment StartX=0 StartY=0 StartZ=0 EndX=26 EndY=0 EndZ=0
    g1: LineSegment StartX=26 StartY=-2.9 StartZ=0 EndX=26 EndY=0 EndZ=0
    g2: LineSegment StartX=26 StartY=-2.9 StartZ=0 EndX=31.6 EndY=-2.9 EndZ=0
    g3: LineSegment StartX=31.6 StartY=-2.9 StartZ=0 EndX=31.6 EndY=-18.8 EndZ=0
    g4: LineSegment StartX=31.6 StartY=-18.8 StartZ=0 EndX=26 EndY=-18.8 EndZ=0
    g5: LineSegment StartX=26 StartY=-18.8 StartZ=0 EndX=26 EndY=-21.7 EndZ=0
    g6: LineSegment StartX=26 StartY=-21.7 StartZ=0 EndX=0 EndY=-21.7 EndZ=0
    g7: LineSegment StartX=0 StartY=-21.7 StartZ=0 EndX=0 EndY=0 EndZ=0
  constraints (21):
    c: Coincident(g0,g-1)
    c: PointOnObject(g0,g-1)
    c: Coincident(g1,g-9)
    c: Coincident(g1,g0)
    c: Vertical(g1)
    c: Coincident(g2,g1)
    c: Horizontal(g2)
    c: Coincident(g3,g2)
    c: Vertical(g3)
    c: PointOnObject(g-12,g3)
    c: Coincident(g4,g3)
    c: Coincident(g4,g-13)
    c: Horizontal(g4)
    c: Coincident(g5,g4)
    c: Vertical(g5)
    c: Coincident(g6,g5)
    c: PointOnObject(g6,g-2)
    c: Horizontal(g6)
    c: PointOnObject(g-6,g6)
    c: Coincident(g7,g6)
    c: Coincident(g7,g0)
FEATURE [PartDesign::Pad] Pad660
  Direction = (0,0,-1)
  Length = 4.5
  Length2 = 10
  Profile = -> Sketch1010
  ReferenceAxis = -> Sketch1010 [N_Axis]
  Refine = true
  Suppressed = false
  Type = 0
FEATURE [Sketcher::SketchObject] Sketch1011
  ArcFitTolerance = 1e-06
  AttachmentSupport = -> [Pad660]
  ExternalGeometry = -> [Pad660]
  FullyConstrained = true
  MakeInternals = false
  MapMode = 5
  Placement = pos=(0,0,-4.5) rot=(1,0,0;3.14159rad)
  sketch-geometry (4):
    g0: LineSegment StartX=0 StartY=0 StartZ=0 EndX=0 EndY=-21.7 EndZ=0
    g1: LineSegment StartX=0 StartY=-21.7 StartZ=0 EndX=26 EndY=-21.7 EndZ=0
    g2: LineSegment StartX=26 StartY=-21.7 StartZ=0 EndX=26 EndY=0 EndZ=0
    g3: LineSegment StartX=26 StartY=0 StartZ=0 EndX=0 EndY=0 EndZ=0
  constraints (10):
    c: Coincident(g0,g1)
    c: Coincident(g1,g2)
    c: Coincident(g2,g3)
    c: Coincident(g3,g0)
    c: Vertical(g0)
    c: Vertical(g2)
    c: Horizontal(g1)
    c: Horizontal(g3)
    c: Coincident(g0,g-1)
    c: Coincident(g1,g-5)
FEATURE [PartDesign::Pad] Pad661
  BaseFeature = -> Pad660
  Direction = (0,0,-1)
  Length = 1
  Length2 = 10
  Profile = -> Sketch1011
  ReferenceAxis = -> Sketch1011 [N_Axis]
  Refine = true
  Suppressed = false
  Type = 0
FEATURE [Sketcher::SketchObject] Sketch1012
  ArcFitTolerance = 1e-06
  AttachmentSupport = -> [Pad661]
  ExternalGeometry = -> [Pad661]
  FullyConstrained = true
  MakeInternals = false
  MapMode = 5
  Placement = pos=(31.6,0,0) rot=(0.57735,0.57735,0.57735;2.0944rad)
  sketch-geometry (4):
    g0: LineSegment StartX=7.95 StartY=0 StartZ=0 EndX=7.95 EndY=-1.4 EndZ=0
    g1: LineSegment StartX=7.95 StartY=-1.4 StartZ=0 EndX=13.75 EndY=-1.4 EndZ=0
    g2: LineSegment StartX=13.75 StartY=-1.4 StartZ=0 EndX=13.75 EndY=0 EndZ=0
    g3: LineSegment StartX=13.75 StartY=0 StartZ=0 EndX=7.95 EndY=0 EndZ=0
  constraints (12):
    c: Coincident(g0,g1)
    c: Coincident(g1,g2)
    c: Coincident(g2,g3)
    c: Coincident(g3,g0)
    c: Vertical(g0)
    c: Vertical(g2)
    c: Horizontal(g1)
    c: Horizontal(g3)
    c: PointOnObject(g0,g-1)
    c: DistanceX(g1,g1) = 5.8
    c: DistanceY(g0,g0) = 1.4
    c: DistanceX(g2,g-3) = 5.05
FEATURE [PartDesign::Pad] Pad662
  BaseFeature = -> Pad661
  Direction = (1,0,0)
  Length = 1.9
  Length2 = 10
  Profile = -> Sketch1012
  ReferenceAxis = -> Sketch1012 [N_Axis]
  Refine = true
  Suppressed = false
  Type = 0
FEATURE [Sketcher::SketchObject] Sketch1013
  ArcFitTolerance = 1e-06
  AttachmentSupport = -> [Pad662]
  ExternalGeometry = -> [Pad662]
  FullyConstrained = true
  MakeInternals = false
  MapMode = 5
  Placement = pos=(0,0,1e-16) rot=(0,0,1;0rad)
  sketch-geometry (8):
    g0: LineSegment StartX=1.5 StartY=19.7 StartZ=0 EndX=24.5 EndY=19.7 EndZ=0
    g1: LineSegment StartX=24.5 StartY=19.7 StartZ=0 EndX=24.5 EndY=17.3 EndZ=0
    g2: LineSegment StartX=24.5 StartY=17.3 StartZ=0 EndX=30.1 EndY=17.3 EndZ=0
    g3: LineSegment StartX=30.1 StartY=17.3 StartZ=0 EndX=30.1 EndY=4.4 EndZ=0
    g4: LineSegment StartX=30.1 StartY=4.4 StartZ=0 EndX=24.5 EndY=4.4 EndZ=0
    g5: LineSegment StartX=24.5 StartY=4.4 StartZ=0 EndX=24.5 EndY=2 EndZ=0
    g6: LineSegment StartX=24.5 StartY=2 StartZ=0 EndX=1.5 EndY=2 EndZ=0
    g7: LineSegment StartX=1.5 StartY=19.7 StartZ=0 EndX=1.5 EndY=2 EndZ=0
  constraints (24):
    c: Horizontal(g0)
    c: Coincident(g1,g0)
    c: Vertical(g1)
    c: Coincident(g2,g1)
    c: Horizontal(g2)
    c: Coincident(g3,g2)
    c: Vertical(g3)
    c: Coincident(g4,g3)
    c: Horizontal(g4)
    c: Coincident(g5,g4)
    c: Vertical(g5)
    c: Coincident(g6,g5)
    c: Horizontal(g6)
    c: Coincident(g7,g0)
    c: Coincident(g7,g6)
    c: Vertical(g7)
    c: DistanceX(g-8,g0) = 1.5
    c: DistanceX(g2,g-4) = 1.5
    c: DistanceX(g1,g-3) = 1.5
    c: DistanceX(g4,g-6) = 1.5
    c: DistanceY(g0,g-8) = 2
    c: DistanceY(g-7,g5) = 2
    c: DistanceY(g-6,g4) = 1.5
    c: DistanceY(g1,g-3) = 1.5
FEATURE [PartDesign::Pocket] Pocket467
  BaseFeature = -> Pad662
  Direction = (0,0,-1)
  Length = 3
  Length2 = 5
  Profile = -> Sketch1013
  ReferenceAxis = -> Sketch1013 [N_Axis]
  Refine = true
  Suppressed = false
  Type = 0
FEATURE [Sketcher::SketchObject] Sketch1014
  ArcFitTolerance = 1e-06
  AttachmentSupport = -> [Pocket467]
  ExternalGeometry = -> [Pocket467]
  FullyConstrained = true
  MakeInternals = false
  MapMode = 5
  Placement = pos=(0,0,-3) rot=(0,0,1;0rad)
  sketch-geometry (4):
    g0: LineSegment StartX=1.5 StartY=19.7 StartZ=0 EndX=1.5 EndY=2 EndZ=0
    g1: LineSegment StartX=1.5 StartY=2 StartZ=0 EndX=24.5 EndY=2 EndZ=0
    g2: LineSegment StartX=24.5 StartY=2 StartZ=0 EndX=24.5 EndY=19.7 EndZ=0
    g3: LineSegment StartX=24.5 StartY=19.7 StartZ=0 EndX=1.5 EndY=19.7 EndZ=0
  constraints (10):
    c: Coincident(g0,g1)
    c: Coincident(g1,g2)
    c: Coincident(g2,g3)
    c: Coincident(g3,g0)
    c: Vertical(g0)
    c: Vertical(g2)
    c: Horizontal(g1)
    c: Horizontal(g3)
    c: Coincident(g0,g-4)
    c: Coincident(g1,g-5)
FEATURE [PartDesign::Pocket] Pocket468
  BaseFeature = -> Pocket467
  Direction = (0,0,-1)
  Length = 1
  Length2 = 5
  Profile = -> Sketch1014
  ReferenceAxis = -> Sketch1014 [N_Axis]
  Refine = true
  Suppressed = false
  Type = 0
FEATURE [PartDesign::Chamfer] Chamfer049
  Angle = 45
  Base = -> Pocket468 [Edge58,Edge54,Edge56,Edge47,Edge49,Edge51]
  BaseFeature = -> Pocket468
  ChamferType = 0
  FlipDirection = false
  Refine = true
  Size = 0.5
  Size2 = 1
  SupportTransform = false
  Suppressed = false
  UseAllEdges = false
FEATURE [PartDesign::Chamfer] Chamfer050
  Angle = 45
  Base = -> Chamfer049 [Edge34]
  BaseFeature = -> Chamfer049
  ChamferType = 0
  FlipDirection = false
  Refine = true
  Size = 0.999
  Size2 = 1
  SupportTransform = false
  Suppressed = false
  UseAllEdges = false
FEATURE [Sketcher::SketchObject] Sketch1015
  ArcFitTolerance = 1e-06
  AttachmentSupport = -> [Chamfer050]
  ExternalGeometry = -> [Chamfer050]
  FullyConstrained = true
  MakeInternals = false
  MapMode = 5
  Placement = pos=(0,0,0) rot=(0.57735,-0.57735,-0.57735;2.0944rad)
  sketch-geometry (2):
    g0: ArcOfCircle CenterX=-10.85 CenterY=1e-16 CenterZ=0 NormalX=0 NormalY=0 NormalZ=1 AngleXU=0 Radius=2 StartAngle=3.14159 EndAngle=6.28319
    g1: LineSegment StartX=-12.85 StartY=3e-16 StartZ=0 EndX=-8.85 EndY=-4e-16 EndZ=0
  constraints (8):
    c: PointOnObject(g0,g-3)
    c: PointOnObject(g0,g-3)
    c: Radius(g0) = 2
    c: PointOnObject(g0,g-3)
    c: DistanceX(g-3,g-3) = 21.7
    c: DistanceX(g-3,g0) = 8.85
    c: Coincident(g1,g0)
    c: Coincident(g1,g0)
FEATURE [PartDesign::Pocket] Pocket469
  BaseFeature = -> Chamfer050
  Direction = (1,0,0)
  Length = 1.5
  Length2 = 5
  Profile = -> Sketch1015
  ReferenceAxis = -> Sketch1015 [N_Axis]
  Refine = true
  Suppressed = false
  Type = 0
FEATURE [Sketcher::SketchObject] Sketch1016
  ArcFitTolerance = 1e-06
  AttachmentSupport = -> [Pocket469]
  ExternalGeometry = -> [Pocket469]
  FullyConstrained = true
  MakeInternals = false
  MapMode = 5
  Placement = pos=(0,0,-4) rot=(0,0,1;0rad)
  sketch-geometry (9):
    g0: LineSegment StartX=1.5 StartY=8.6 StartZ=0 EndX=1.5 EndY=7.3 EndZ=0
    g1: LineSegment StartX=1.5 StartY=7.3 StartZ=0 EndX=14.5 EndY=7.3 EndZ=0
    g2: LineSegment StartX=14.5 StartY=7.3 StartZ=0 EndX=14.5 EndY=8.6 EndZ=0
    g3: LineSegment StartX=14.5 StartY=8.6 StartZ=0 EndX=1.5 EndY=8.6 EndZ=0
    g4: LineSegment StartX=1.5 StartY=14.4 StartZ=0 EndX=1.5 EndY=13.1 EndZ=0
    g5: LineSegment StartX=1.5 StartY=13.1 StartZ=0 EndX=14.5 EndY=13.1 EndZ=0
    g6: LineSegment StartX=14.5 StartY=13.1 StartZ=0 EndX=14.5 EndY=14.4 EndZ=0
    g7: LineSegment StartX=14.5 StartY=14.4 StartZ=0 EndX=1.5 EndY=14.4 EndZ=0
    g8: LineSegment [constr] StartX=14.5 StartY=13.1 StartZ=0 EndX=14.5 EndY=8.6 EndZ=0
  constraints (26):
    c: Coincident(g0,g1)
    c: Coincident(g1,g2)
    c: Coincident(g2,g3)
    c: Coincident(g3,g0)
    c: Vertical(g0)
    c: Vertical(g2)
    c: Horizontal(g1)
    c: Horizontal(g3)
    c: PointOnObject(g0,g-4)
    c: Coincident(g4,g5)
    c: Coincident(g5,g6)
    c: Coincident(g6,g7)
    c: Coincident(g7,g4)
    c: Vertical(g4)
    c: Vertical(g6)
    c: Horizontal(g5)
    c: Horizontal(g7)
    c: PointOnObject(g4,g-3)
    c: Coincident(g8,g5)
    c: Coincident(g8,g2)
    c: Vertical(g8)
    c: DistanceY(g8,g8) = 4.5
    c: DistanceY(g6,g6) = 1.3
    c: DistanceY(g2,g2) = 1.3
    c: DistanceY(g2,g-6) = 0.25
    c: DistanceX(g7,g7) = 13
FEATURE [PartDesign::Pad] Pad663
  BaseFeature = -> Pocket469
  Direction = (0,0,1)
  Length = 6
  Length2 = 10
  Profile = -> Sketch1016
  ReferenceAxis = -> Sketch1016 [N_Axis]
  Refine = true
  Suppressed = false
  Type = 0
FEATURE [Sketcher::SketchObject] Sketch1017
  ArcFitTolerance = 1e-06
  AttachmentSupport = -> [Pad663]
  ExternalGeometry = -> [Pad663]
  FullyConstrained = true
  MakeInternals = false
  MapMode = 5
  Placement = pos=(0,7.3,0) rot=(1,0,0;1.5708rad)
  sketch-geometry (3):
    g0: LineSegment StartX=1.5 StartY=0 StartZ=0 EndX=1.5 EndY=2 EndZ=0
    g1: LineSegment StartX=1.5 StartY=2 StartZ=0 EndX=2.22794 EndY=2 EndZ=0
    g2: LineSegment StartX=2.22794 StartY=2 StartZ=0 EndX=1.5 EndY=0 EndZ=0
  constraints (7):
    c: Coincident(g0,g-3)
    c: Coincident(g0,g-4)
    c: Coincident(g1,g0)
    c: PointOnObject(g1,g-4)
    c: Coincident(g2,g1)
    c: Coincident(g2,g0)
    c: Angle(g2,g0) = 0.349066
FEATURE [PartDesign::Pocket] Pocket470
  BaseFeature = -> Pad663
  Direction = (0,1,-2e-16)
  Length = 8
  Length2 = 5
  Profile = -> Sketch1017
  ReferenceAxis = -> Sketch1017 [N_Axis]
  Refine = true
  Suppressed = false
  Type = 0
FEATURE [Sketcher::SketchObject] Sketch1018
  ArcFitTolerance = 1e-06
  AttachmentSupport = -> [Pocket470]
  ExternalGeometry = -> [Pocket470]
  FullyConstrained = true
  MakeInternals = false
  MapMode = 5
  Placement = pos=(0,0,-4) rot=(0,0,1;0rad)
  sketch-geometry (6):
    g0: LineSegment StartX=1.5 StartY=11.5 StartZ=0 EndX=1.5 EndY=10.2 EndZ=0
    g1: LineSegment StartX=1.5 StartY=10.2 StartZ=0 EndX=14.5 EndY=10.2 EndZ=0
    g2: LineSegment StartX=14.5 StartY=10.2 StartZ=0 EndX=14.5 EndY=11.5 EndZ=0
    g3: LineSegment StartX=14.5 StartY=11.5 StartZ=0 EndX=1.5 EndY=11.5 EndZ=0
    g4: LineSegment [constr] StartX=14.5 StartY=11.5 StartZ=0 EndX=14.5 EndY=13.1 EndZ=0
    g5: LineSegment [constr] StartX=14.5 StartY=10.2 StartZ=0 EndX=14.5 EndY=8.6 EndZ=0
  constraints (17):
    c: Coincident(g0,g1)
    c: Coincident(g1,g2)
    c: Coincident(g2,g3)
    c: Coincident(g3,g0)
    c: Vertical(g0)
    c: Vertical(g2)
    c: Horizontal(g1)
    c: Horizontal(g3)
    c: PointOnObject(g0,g-3)
    c: Coincident(g4,g2)
    c: Coincident(g4,g-4)
    c: Vertical(g4)
    c: DistanceY(g2,g2) = 1.3
    c: Coincident(g5,g1)
    c: Coincident(g5,g-5)
    c: DistanceY(g4,g4) = 1.6
    c: DistanceY(g5,g5) = 1.6
FEATURE [PartDesign::Pad] Pad664
  BaseFeature = -> Pocket470
  Direction = (0,0,1)
  Length = 2
  Length2 = 10
  Profile = -> Sketch1018
  ReferenceAxis = -> Sketch1018 [N_Axis]
  Refine = true
  Suppressed = false
  Type = 0
FEATURE [Sketcher::SketchObject] Sketch1019
  ArcFitTolerance = 1e-06
  AttachmentSupport = -> [Pad664]
  ExternalGeometry = -> [Pad664]
  FullyConstrained = true
  MakeInternals = false
  MapMode = 5
  Placement = pos=(0,0,-4) rot=(0,0,1;0rad)
  sketch-geometry (2):
    g0: Circle CenterX=4.85 CenterY=17.3 CenterZ=0 NormalX=0 NormalY=0 NormalZ=1 AngleXU=0 Radius=3.15
    g1: Circle CenterX=4.85 CenterY=4.4 CenterZ=0 NormalX=0 NormalY=0 NormalZ=1 AngleXU=0 Radius=3.15
  constraints (6):
    c: Radius(g1) = 3.15
    c: Radius(g0) = 3.15
    c: DistanceX(g-3,g0) = 3.35
    c: DistanceY(g0,g-3) = 2.4
    c: DistanceX(g-4,g1) = 3.35
    c: DistanceY(g-4,g1) = 2.4
FEATURE [PartDesign::Pad] Pad665
  BaseFeature = -> Pad664
  Direction = (0,0,1)
  Length = 4
  Length2 = 10
  Profile = -> Sketch1019
  ReferenceAxis = -> Sketch1019 [N_Axis]
  Refine = true
  Suppressed = false
  Type = 0
FEATURE [Sketcher::SketchObject] Sketch1020
  ArcFitTolerance = 1e-06
  AttachmentSupport = -> [Pad665]
  ExternalGeometry = -> [Pad665]
  FullyConstrained = true
  MakeInternals = false
  MapMode = 5
  Placement = pos=(0,0,2e-16) rot=(0,0,1;0rad)
  sketch-geometry (8):
    g0: LineSegment StartX=1.5 StartY=19.7 StartZ=0 EndX=2.80978 EndY=19.7 EndZ=0
    g1: LineSegment StartX=1.5 StartY=19.7 StartZ=0 EndX=1.5 EndY=15.7 EndZ=0
    g2: LineSegment StartX=1.5 StartY=15.7 StartZ=0 EndX=2.13661 EndY=15.7 EndZ=0
    g3: ArcOfCircle CenterX=4.85 CenterY=17.3 CenterZ=0 NormalX=0 NormalY=0 NormalZ=1 AngleXU=0 Radius=3.15 StartAngle=2.27534 EndAngle=3.67438
    g4: LineSegment StartX=2.80978 StartY=2 StartZ=0 EndX=1.5 EndY=2 EndZ=0
    g5: LineSegment StartX=1.5 StartY=2 StartZ=0 EndX=1.5 EndY=6 EndZ=0
    g6: LineSegment StartX=1.5 StartY=6 StartZ=0 EndX=2.13661 EndY=6 EndZ=0
    g7: ArcOfCircle CenterX=4.85002 CenterY=4.4 CenterZ=0 NormalX=0 NormalY=0 NormalZ=1 AngleXU=0 Radius=3.15001 StartAngle=2.60881 EndAngle=4.00784
  constraints (22):
    c: Coincident(g0,g-5)
    c: Coincident(g0,g-4)
    c: Coincident(g1,g0)
    c: PointOnObject(g1,g-5)
    c: Coincident(g2,g1)
    c: PointOnObject(g2,g-4)
    c: Horizontal(g2)
    c: Coincident(g3,g2)
    c: Coincident(g3,g0)
    c: Tangent(g3,g-4)
    c: DistanceY(g1,g1) = 4
    c: Coincident(g4,g-7)
    c: Coincident(g4,g-8)
    c: Coincident(g5,g4)
    c: PointOnObject(g5,g-8)
    c: DistanceY(g5,g5) = 4
    c: Coincident(g6,g5)
    c: PointOnObject(g6,g-7)
    c: Horizontal(g6)
    c: Coincident(g7,g4)
    c: Coincident(g7,g6)
    c: Tangent(g7,g-7)
FEATURE [PartDesign::Pad] Pad666
  BaseFeature = -> Pad665
  Direction = (0,0,1)
  Length = 4
  Length2 = 10
  Profile = -> Sketch1020
  ReferenceAxis = -> Sketch1020 [N_Axis]
  Refine = true
  Reversed = true
  Suppressed = false
  Type = 0
FEATURE [Sketcher::SketchObject] Sketch1021
  ArcFitTolerance = 1e-06
  AttachmentSupport = -> [Pad666]
  ExternalGeometry = -> [Pad666]
  FullyConstrained = true
  MakeInternals = false
  MapMode = 5
  Placement = pos=(0,0,2e-16) rot=(0,0,1;0rad)
  sketch-geometry (2):
    g0: Circle CenterX=4.85 CenterY=17.3 CenterZ=0 NormalX=0 NormalY=0 NormalZ=1 AngleXU=0 Radius=2.15
    g1: Circle CenterX=4.85 CenterY=4.4 CenterZ=0 NormalX=0 NormalY=0 NormalZ=1 AngleXU=0 Radius=2.15
  constraints (4):
    c: Coincident(g0,g-3)
    c: Radius(g0) = 2.15
    c: Coincident(g1,g-4)
    c: Radius(g1) = 2.15
FEATURE [PartDesign::Pocket] Pocket471
  BaseFeature = -> Pad666
  Direction = (0,0,-1)
  Length = 0.6
  Length2 = 5
  Profile = -> Sketch1021
  ReferenceAxis = -> Sketch1021 [N_Axis]
  Refine = true
  Suppressed = false
  Type = 0
FEATURE [Sketcher::SketchObject] Sketch1022
  ArcFitTolerance = 1e-06
  AttachmentSupport = -> [Pocket471]
  ExternalGeometry = -> [Pocket471]
  FullyConstrained = true
  MakeInternals = false
  MapMode = 5
  Placement = pos=(0,0,-0.6) rot=(0,0,1;0rad)
  sketch-geometry (2):
    g0: Circle CenterX=4.85 CenterY=17.3 CenterZ=0 NormalX=0 NormalY=0 NormalZ=1 AngleXU=0 Radius=1
    g1: Circle CenterX=4.85 CenterY=4.4 CenterZ=0 NormalX=0 NormalY=0 NormalZ=1 AngleXU=0 Radius=1
  constraints (4):
    c: Coincident(g0,g-3)
    c: Radius(g0) = 1
    c: Coincident(g1,g-4)
    c: Radius(g1) = 1
FEATURE [PartDesign::Pocket] Pocket472
  BaseFeature = -> Pocket471
  Direction = (0,0,-1)
  Length = 5
  Length2 = 5
  Profile = -> Sketch1022
  ReferenceAxis = -> Sketch1022 [N_Axis]
  Refine = true
  Suppressed = false
  Type = 1
FEATURE [Sketcher::SketchObject] Sketch1023
  ArcFitTolerance = 1e-06
  AttachmentSupport = -> [Pocket472]
  ExternalGeometry = -> [Pocket472]
  FullyConstrained = true
  MakeInternals = false
  MapMode = 5
  Placement = pos=(0,0,-4) rot=(0,0,1;0rad)
  sketch-geometry (10):
    g0: LineSegment StartX=17 StartY=13.35 StartZ=0 EndX=23.1 EndY=13.35 EndZ=0
    g1: LineSegment StartX=23.1 StartY=13.35 StartZ=0 EndX=23.1 EndY=14.85 EndZ=0
    g2: LineSegment StartX=23.1 StartY=14.85 StartZ=0 EndX=17 EndY=14.85 EndZ=0
    g3: LineSegment StartX=17 StartY=14.85 StartZ=0 EndX=17 EndY=13.35 EndZ=0
    g4: LineSegment StartX=17 StartY=8.35 StartZ=0 EndX=17 EndY=6.85 EndZ=0
    g5: LineSegment StartX=17 StartY=6.85 StartZ=0 EndX=23.1 EndY=6.85 EndZ=0
    g6: LineSegment StartX=23.1 StartY=6.85 StartZ=0 EndX=23.1 EndY=8.35 EndZ=0
    g7: LineSegment StartX=23.1 StartY=8.35 StartZ=0 EndX=17 EndY=8.35 EndZ=0
    g8: LineSegment [constr] StartX=23.1 StartY=13.35 StartZ=0 EndX=23.1 EndY=8.35 EndZ=0
    g9: LineSegment [constr] StartX=17 StartY=13.35 StartZ=0 EndX=17 EndY=8.35 EndZ=0
  constraints (29):
    c: Coincident(g0,g1)
    c: Coincident(g1,g2)
    c: Coincident(g2,g3)
    c: Coincident(g3,g0)
    c: Horizontal(g0)
    c: Horizontal(g2)
    c: Vertical(g1)
    c: Vertical(g3)
    c: Coincident(g4,g5)
    c: Coincident(g5,g6)
    c: Coincident(g6,g7)
    c: Coincident(g7,g4)
    c: Vertical(g4)
    c: Vertical(g6)
    c: Horizontal(g5)
    c: Horizontal(g7)
    c: Coincident(g8,g0)
    c: Coincident(g8,g6)
    c: Coincident(g9,g0)
    c: Coincident(g9,g4)
    c: Vertical(g9)
    c: Vertical(g8)
    c: DistanceY(g3,g3) = 1.5
    c: DistanceY(g9,g9) = 5
    c: DistanceY(g4,g4) = 1.5
    c: DistanceY(g-4,g-3) = 4.5
    c: DistanceY(g-3,g0) = 0.25
    c: DistanceX(g-3,g0) = 2.5
    c: DistanceX(g2,g2) = 6.1
FEATURE [PartDesign::Pad] Pad667
  BaseFeature = -> Pocket472
  Direction = (0,0,1)
  Length = 9
  Length2 = 10
  Profile = -> Sketch1023
  ReferenceAxis = -> Sketch1023 [N_Axis]
  Refine = true
  Suppressed = false
  Type = 0
FEATURE [Sketcher::SketchObject] Sketch1024
  ArcFitTolerance = 1e-06
  AttachmentSupport = -> [Pad667]
  ExternalGeometry = -> [Pad667]
  FullyConstrained = true
  MakeInternals = false
  MapMode = 5
  Placement = pos=(0,6.85,0) rot=(1,0,0;1.5708rad)
  sketch-geometry (7):
    g0: LineSegment StartX=19 StartY=5 StartZ=0 EndX=21.1 EndY=5 EndZ=0
    g1: LineSegment StartX=21.1 StartY=5 StartZ=0 EndX=21.1 EndY=3.05 EndZ=0
    g2: LineSegment StartX=19 StartY=5 StartZ=0 EndX=19 EndY=3.05 EndZ=0
    g3: ArcOfCircle CenterX=20.05 CenterY=3.05 CenterZ=0 NormalX=0 NormalY=0 NormalZ=1 AngleXU=0 Radius=1.05 StartAngle=3.14159 EndAngle=6.28319
    g4: LineSegment [constr] StartX=20.05 StartY=3.05 StartZ=0 EndX=19 EndY=3.05 EndZ=0
    g5: LineSegment [constr] StartX=20.05 StartY=3.05 StartZ=0 EndX=21.1 EndY=3.05 EndZ=0
    g6: LineSegment [constr] StartX=20.05 StartY=3.05 StartZ=0 EndX=20.05 EndY=2 EndZ=0
  constraints (21):
    c: PointOnObject(g0,g-3)
    c: PointOnObject(g0,g-3)
    c: Coincident(g1,g0)
    c: Vertical(g1)
    c: Coincident(g2,g0)
    c: Vertical(g2)
    c: Coincident(g3,g2)
    c: Coincident(g3,g1)
    c: Coincident(g4,g3)
    c: Coincident(g4,g2)
    c: Coincident(g5,g3)
    c: Coincident(g5,g1)
    c: Horizontal(g4)
    c: Horizontal(g5)
    c: DistanceX(g0,g0) = 2.1
    c: DistanceX(g-3,g-3) = 6.1
    c: DistanceX(g-3,g0) = 2
    c: Coincident(g6,g3)
    c: PointOnObject(g6,g3)
    c: Vertical(g6)
    c: DistanceY(g6,g0) = 3
FEATURE [PartDesign::Pocket] Pocket473
  BaseFeature = -> Pad667
  Direction = (0,1,-2e-16)
  Length = 5
  Length2 = 5
  Profile = -> Sketch1024
  ReferenceAxis = -> Sketch1024 [N_Axis]
  Refine = true
  Suppressed = false
  Type = 1
FEATURE [Sketcher::SketchObject] Sketch1025
  ArcFitTolerance = 1e-06
  AttachmentSupport = -> [Pocket473]
  ExternalGeometry = -> [Pocket473]
  FullyConstrained = true
  MakeInternals = false
  MapMode = 5
  Placement = pos=(0,0,-5.5) rot=(1,0,0;3.14159rad)
  sketch-geometry (2):
    g0: Circle CenterX=4.85 CenterY=-4.4 CenterZ=0 NormalX=0 NormalY=0 NormalZ=1 AngleXU=0 Radius=2.2
    g1: Circle CenterX=4.85 CenterY=-17.3 CenterZ=0 NormalX=0 NormalY=0 NormalZ=1 AngleXU=0 Radius=2.2
  constraints (4):
    c: Coincident(g0,g-3)
    c: Coincident(g1,g-4)
    c: Diameter(g1) = 4.4
    c: Diameter(g0) = 4.4
FEATURE [PartDesign::Pocket] Pocket474
  BaseFeature = -> Pocket473
  Direction = (0,0,1)
  Length = 3
  Length2 = 5
  Profile = -> Sketch1025
  ReferenceAxis = -> Sketch1025 [N_Axis]
  Refine = true
  Suppressed = false
  Type = 0
FEATURE [Sketcher::SketchObject] Sketch1026
  ArcFitTolerance = 1e-06
  AttachmentSupport = -> [Pocket474]
  ExternalGeometry = -> [Pocket474]
  FullyConstrained = true
  MakeInternals = false
  MapMode = 5
  Placement = pos=(0,0,-5.5) rot=(1,0,0;3.14159rad)
  sketch-geometry (4):
    g0: LineSegment StartX=9.7 StartY=0.8 StartZ=0 EndX=9.7 EndY=-22.5 EndZ=0
    g1: LineSegment StartX=9.7 StartY=-22.5 StartZ=0 EndX=14.2 EndY=-22.5 EndZ=0
    g2: LineSegment StartX=14.2 StartY=-22.5 StartZ=0 EndX=14.2 EndY=0.8 EndZ=0
    g3: LineSegment StartX=14.2 StartY=0.8 StartZ=0 EndX=9.7 EndY=0.8 EndZ=0
  constraints (12):
    c: Coincident(g0,g1)
    c: Coincident(g1,g2)
    c: Coincident(g2,g3)
    c: Coincident(g3,g0)
    c: Vertical(g0)
    c: Vertical(g2)
    c: Horizontal(g1)
    c: Horizontal(g3)
    c: DistanceX(g1,g1) = 4.5
    c: DistanceX(g-3,g0) = 9.7
    c: DistanceY(g0,g-3) = 0.8
    c: DistanceY(g0,g0) = 23.3
FEATURE [PartDesign::Pad] Pad668
  BaseFeature = -> Pocket474
  Direction = (0,0,-1)
  Length = 0.8
  Length2 = 10
  Profile = -> Sketch1026
  ReferenceAxis = -> Sketch1026 [N_Axis]
  Refine = true
  Suppressed = false
  Type = 0
FEATURE [Sketcher::SketchObject] Sketch1027
  ArcFitTolerance = 1e-06
  AttachmentSupport = -> [Pad668]
  ExternalGeometry = -> [Pad668]
  FullyConstrained = true
  MakeInternals = false
  MapMode = 5
  Placement = pos=(0,0,0) rot=(1,0,0;1.5708rad)
  sketch-geometry (4):
    g0: LineSegment StartX=9.7 StartY=-5.5 StartZ=0 EndX=14.2 EndY=-5.5 EndZ=0
    g1: LineSegment StartX=14.2 StartY=-5.5 StartZ=0 EndX=14.2 EndY=0 EndZ=0
    g2: LineSegment StartX=14.2 StartY=0 StartZ=0 EndX=9.7 EndY=0 EndZ=0
    g3: LineSegment StartX=9.7 StartY=0 StartZ=0 EndX=9.7 EndY=-5.5 EndZ=0
  constraints (10):
    c: Coincident(g0,g1)
    c: Coincident(g1,g2)
    c: Coincident(g2,g3)
    c: Coincident(g3,g0)
    c: Horizontal(g2)
    c: Vertical(g1)
    c: Vertical(g3)
    c: Coincident(g0,g-3)
    c: PointOnObject(g1,g-4)
    c: Coincident(g0,g-3)
FEATURE [PartDesign::Pad] Pad669
  BaseFeature = -> Pad668
  Direction = (0,-1,2e-16)
  Length = 0.8
  Length2 = 10
  Profile = -> Sketch1027
  ReferenceAxis = -> Sketch1027 [N_Axis]
  Refine = true
  Suppressed = false
  Type = 0
FEATURE [Sketcher::SketchObject] Sketch1028
  ArcFitTolerance = 1e-06
  AttachmentSupport = -> [Pad669]
  ExternalGeometry = -> [Pad669]
  FullyConstrained = true
  MakeInternals = false
  MapMode = 5
  Placement = pos=(0,21.7,0) rot=(0,0.707107,0.707107;3.14159rad)
  sketch-geometry (4):
    g0: LineSegment StartX=-9.7 StartY=-5.5 StartZ=0 EndX=-9.7 EndY=0 EndZ=0
    g1: LineSegment StartX=-9.7 StartY=0 StartZ=0 EndX=-14.2 EndY=0 EndZ=0
    g2: LineSegment StartX=-14.2 StartY=0 StartZ=0 EndX=-14.2 EndY=-5.5 EndZ=0
    g3: LineSegment StartX=-14.2 StartY=-5.5 StartZ=0 EndX=-9.7 EndY=-5.5 EndZ=0
  constraints (10):
    c: Coincident(g0,g1)
    c: Coincident(g1,g2)
    c: Coincident(g2,g3)
    c: Coincident(g3,g0)
    c: Vertical(g0)
    c: Vertical(g2)
    c: Horizontal(g1)
    c: Coincident(g0,g-3)
    c: PointOnObject(g1,g-4)
    c: Coincident(g2,g-3)
FEATURE [PartDesign::Pad] Pad670
  BaseFeature = -> Pad669
  Direction = (0,1,-2e-16)
  Length = 0.8
  Length2 = 10
  Profile = -> Sketch1028
  ReferenceAxis = -> Sketch1028 [N_Axis]
  Refine = true
  Suppressed = false
  Type = 0
FEATURE [Sketcher::SketchObject] Sketch1029
  ArcFitTolerance = 1e-06
  AttachmentSupport = -> [Pad670]
  ExternalGeometry = -> [Pad670]
  FullyConstrained = true
  MakeInternals = false
  MapMode = 5
  Placement = pos=(0,0,-5.5) rot=(1,0,0;3.14159rad)
  sketch-geometry (12):
    g0: LineSegment StartX=14.2 StartY=0 StartZ=0 EndX=14.2 EndY=-21.7 EndZ=0
    g1: LineSegment StartX=14.2 StartY=-21.7 StartZ=0 EndX=15.7 EndY=-21.7 EndZ=0
    g2: LineSegment StartX=15.7 StartY=-21.7 StartZ=0 EndX=15.7 EndY=0 EndZ=0
    g3: LineSegment StartX=15.7 StartY=0 StartZ=0 EndX=14.2 EndY=0 EndZ=0
    g4: LineSegment StartX=17.7 StartY=-21.7 StartZ=0 EndX=19.2 EndY=-21.7 EndZ=0
    g5: LineSegment StartX=19.2 StartY=-21.7 StartZ=0 EndX=19.2 EndY=0 EndZ=0
    g6: LineSegment StartX=19.2 StartY=0 StartZ=0 EndX=17.7 EndY=0 EndZ=0
    g7: LineSegment StartX=17.7 StartY=0 StartZ=0 EndX=17.7 EndY=-21.7 EndZ=0
    g8: LineSegment StartX=21.2 StartY=0 StartZ=0 EndX=21.2 EndY=-21.7 EndZ=0
    g9: LineSegment StartX=21.2 StartY=-21.7 StartZ=0 EndX=22.7 EndY=-21.7 EndZ=0
    g10: LineSegment StartX=22.7 StartY=-21.7 StartZ=0 EndX=22.7 EndY=0 EndZ=0
    g11: LineSegment StartX=22.7 StartY=0 StartZ=0 EndX=21.2 EndY=0 EndZ=0
  constraints (36):
    c: Coincident(g0,g1)
    c: Coincident(g1,g2)
    c: Coincident(g2,g3)
    c: Coincident(g3,g0)
    c: Vertical(g0)
    c: Vertical(g2)
    c: Horizontal(g1)
    c: Horizontal(g3)
    c: Coincident(g0,g-5)
    c: PointOnObject(g1,g-4)
    c: Coincident(g4,g5)
    c: Coincident(g5,g6)
    c: Coincident(g6,g7)
    c: Coincident(g7,g4)
    c: Horizontal(g4)
    c: Horizontal(g6)
    c: Vertical(g5)
    c: Vertical(g7)
    c: PointOnObject(g4,g-4)
    c: PointOnObject(g5,g-5)
    c: Coincident(g8,g9)
    c: Coincident(g9,g10)
    c: Coincident(g10,g11)
    c: Coincident(g11,g8)
    c: Vertical(g8)
    c: Vertical(g10)
    c: Horizontal(g9)
    c: Horizontal(g11)
    c: PointOnObject(g8,g-5)
    c: PointOnObject(g9,g-4)
    c: DistanceX(g1,g1) = 1.5
    c: DistanceX(g-4,g-4) = 11.8
    c: DistanceX(g1,g4) = 2
    c: DistanceX(g4,g4) = 1.5
    c: DistanceX(g4,g8) = 2
    c: DistanceX(g9,g9) = 1.5
FEATURE [PartDesign::Pocket] Pocket475
  BaseFeature = -> Pad670
  Direction = (0,0,1)
  Length = 0.5
  Length2 = 5
  Profile = -> Sketch1029
  ReferenceAxis = -> Sketch1029 [N_Axis]
  Refine = true
  Suppressed = false
  Type = 0
FEATURE [Sketcher::SketchObject] Sketch1030
  ArcFitTolerance = 1e-06
  AttachmentSupport = -> [Pocket475]
  ExternalGeometry = -> [Pocket475]
  FullyConstrained = true
  MakeInternals = false
  MapMode = 5
  Placement = pos=(0,21.7,0) rot=(0,0.707107,0.707107;3.14159rad)
  sketch-geometry (12):
    g0: LineSegment StartX=-15.7 StartY=-5 StartZ=0 EndX=-14.2 EndY=-5 EndZ=0
    g1: LineSegment StartX=-14.2 StartY=-5 StartZ=0 EndX=-14.2 EndY=0 EndZ=0
    g2: LineSegment StartX=-14.2 StartY=0 StartZ=0 EndX=-15.7 EndY=0 EndZ=0
    g3: LineSegment StartX=-15.7 StartY=0 StartZ=0 EndX=-15.7 EndY=-5 EndZ=0
    g4: LineSegment StartX=-19.2 StartY=-5 StartZ=0 EndX=-17.7 EndY=-5 EndZ=0
    g5: LineSegment StartX=-17.7 StartY=-5 StartZ=0 EndX=-17.7 EndY=0 EndZ=0
    g6: LineSegment StartX=-17.7 StartY=0 StartZ=0 EndX=-19.2 EndY=0 EndZ=0
    g7: LineSegment StartX=-19.2 StartY=0 StartZ=0 EndX=-19.2 EndY=-5 EndZ=0
    g8: LineSegment StartX=-22.7 StartY=-5 StartZ=0 EndX=-21.2 EndY=-5 EndZ=0
    g9: LineSegment StartX=-21.2 StartY=-5 StartZ=0 EndX=-21.2 EndY=0 EndZ=0
    g10: LineSegment StartX=-21.2 StartY=0 StartZ=0 EndX=-22.7 EndY=0 EndZ=0
    g11: LineSegment StartX=-22.7 StartY=0 StartZ=0 EndX=-22.7 EndY=-5 EndZ=0
  constraints (30):
    c: Coincident(g0,g1)
    c: Coincident(g1,g2)
    c: Coincident(g2,g3)
    c: Coincident(g3,g0)
    c: Horizontal(g0)
    c: Horizontal(g2)
    c: Vertical(g1)
    c: Vertical(g3)
    c: Coincident(g0,g-3)
    c: Coincident(g1,g-6)
    c: Coincident(g4,g5)
    c: Coincident(g5,g6)
    c: Coincident(g6,g7)
    c: Coincident(g7,g4)
    c: Horizontal(g6)
    c: Vertical(g5)
    c: Vertical(g7)
    c: Coincident(g4,g-4)
    c: PointOnObject(g5,g-6)
    c: Coincident(g8,g9)
    c: Coincident(g9,g10)
    c: Coincident(g10,g11)
    c: Coincident(g11,g8)
    c: Horizontal(g10)
    c: Vertical(g9)
    c: Vertical(g11)
    c: Coincident(g8,g-5)
    c: PointOnObject(g9,g-6)
    c: Coincident(g8,g-5)
    c: Coincident(g-4,g4)
FEATURE [PartDesign::Pocket] Pocket476
  BaseFeature = -> Pocket475
  Direction = (0,-1,2e-16)
  Length = 0.5
  Length2 = 5
  Profile = -> Sketch1030
  ReferenceAxis = -> Sketch1030 [N_Axis]
  Refine = true
  Suppressed = false
  Type = 0
FEATURE [Sketcher::SketchObject] Sketch1031
  ArcFitTolerance = 1e-06
  AttachmentSupport = -> [Pocket476]
  ExternalGeometry = -> [Pocket476]
  FullyConstrained = true
  MakeInternals = false
  MapMode = 5
  Placement = pos=(0,0,0) rot=(1,0,0;1.5708rad)
  sketch-geometry (12):
    g0: LineSegment StartX=21.2 StartY=-5 StartZ=0 EndX=22.7 EndY=-5 EndZ=0
    g1: LineSegment StartX=22.7 StartY=-5 StartZ=0 EndX=22.7 EndY=0 EndZ=0
    g2: LineSegment StartX=22.7 StartY=0 StartZ=0 EndX=21.2 EndY=0 EndZ=0
    g3: LineSegment StartX=21.2 StartY=0 StartZ=0 EndX=21.2 EndY=-5 EndZ=0
    g4: LineSegment StartX=17.7 StartY=-5 StartZ=0 EndX=19.2 EndY=-5 EndZ=0
    g5: LineSegment StartX=19.2 StartY=-5 StartZ=0 EndX=19.2 EndY=0 EndZ=0
    g6: LineSegment StartX=19.2 StartY=0 StartZ=0 EndX=17.7 EndY=0 EndZ=0
    g7: LineSegment StartX=17.7 StartY=0 StartZ=0 EndX=17.7 EndY=-5 EndZ=0
    g8: LineSegment StartX=15.7 StartY=-5 StartZ=0 EndX=15.7 EndY=0 EndZ=0
    g9: LineSegment StartX=15.7 StartY=0 StartZ=0 EndX=14.2 EndY=0 EndZ=0
    g10: LineSegment StartX=14.2 StartY=0 StartZ=0 EndX=14.2 EndY=-5 EndZ=0
    g11: LineSegment StartX=14.2 StartY=-5 StartZ=0 EndX=15.7 EndY=-5 EndZ=0
  constraints (30):
    c: Coincident(g0,g1)
    c: Coincident(g1,g2)
    c: Coincident(g2,g3)
    c: Coincident(g3,g0)
    c: Horizontal(g2)
    c: Vertical(g1)
    c: Vertical(g3)
    c: Coincident(g0,g-3)
    c: PointOnObject(g1,g-6)
    c: Coincident(g4,g5)
    c: Coincident(g5,g6)
    c: Coincident(g6,g7)
    c: Coincident(g7,g4)
    c: Horizontal(g6)
    c: Vertical(g5)
    c: Vertical(g7)
    c: Coincident(g4,g-4)
    c: PointOnObject(g5,g-6)
    c: Coincident(g8,g9)
    c: Coincident(g9,g10)
    c: Coincident(g10,g11)
    c: Coincident(g11,g8)
    c: Vertical(g8)
    c: Vertical(g10)
    c: Horizontal(g9)
    c: Horizontal(g11)
    c: Coincident(g8,g-5)
    c: Coincident(g9,g-6)
    c: Coincident(g4,g-4)
    c: Coincident(g0,g-3)
FEATURE [PartDesign::Pocket] Pocket477
  BaseFeature = -> Pocket476
  Direction = (0,1,-2e-16)
  Length = 0.5
  Length2 = 5
  Profile = -> Sketch1031
  ReferenceAxis = -> Sketch1031 [N_Axis]
  Refine = true
  Suppressed = false
  Type = 0
FEATURE [Sketcher::SketchObject] Sketch1032
  ArcFitTolerance = 1e-06
  AttachmentSupport = -> [Pocket477]
  ExternalGeometry = -> [Pocket477]
  FullyConstrained = true
  MakeInternals = false
  MapMode = 5
  Placement = pos=(0,0.5,0) rot=(1,0,0;1.5708rad)
  sketch-geometry (2):
    g0: ArcOfCircle CenterX=20.2 CenterY=0 CenterZ=0 NormalX=0 NormalY=0 NormalZ=1 AngleXU=0 Radius=2.85 StartAngle=3.14159 EndAngle=6.28319
    g1: LineSegment StartX=17.35 StartY=3e-16 StartZ=0 EndX=23.05 EndY=-7e-16 EndZ=0
  constraints (7):
    c: PointOnObject(g0,g-1)
    c: PointOnObject(g0,g-1)
    c: Radius(g0) = 2.85
    c: PointOnObject(g0,g-4)
    c: DistanceX(g-3,g0) = 1.65
    c: Coincident(g1,g0)
    c: Coincident(g1,g0)
FEATURE [PartDesign::Pad] Pad671
  BaseFeature = -> Pocket477
  Direction = (0,-1,2e-16)
  Length = 1.5
  Length2 = 10
  Profile = -> Sketch1032
  ReferenceAxis = -> Sketch1032 [N_Axis]
  Refine = true
  Suppressed = false
  Type = 0
FEATURE [Sketcher::SketchObject] Sketch1033
  ArcFitTolerance = 1e-06
  AttachmentSupport = -> [Pad671]
  ExternalGeometry = -> [Pad671]
  FullyConstrained = true
  MakeInternals = false
  MapMode = 5
  Placement = pos=(0,21.2,0) rot=(0,0.707107,0.707107;3.14159rad)
  sketch-geometry (2):
    g0: ArcOfCircle CenterX=-20.2 CenterY=-4.6e-15 CenterZ=0 NormalX=0 NormalY=0 NormalZ=1 AngleXU=0 Radius=2.85 StartAngle=3.14159 EndAngle=6.28319
    g1: LineSegment StartX=-23.05 StartY=-5.5e-15 StartZ=0 EndX=-17.35 EndY=-5.3e-15 EndZ=0
  constraints (4):
    c: Tangent(g0,g-3) = -1.5708
    c: Coincident(g0,g-3)
    c: Coincident(g1,g0)
    c: Coincident(g1,g0)
FEATURE [PartDesign::Pad] Pad672
  BaseFeature = -> Pad671
  Direction = (0,1,-2e-16)
  Length = 1.5
  Length2 = 10
  Profile = -> Sketch1033
  ReferenceAxis = -> Sketch1033 [N_Axis]
  Refine = true
  Suppressed = false
  Type = 0
FEATURE [Sketcher::SketchObject] Sketch1034
  ArcFitTolerance = 1e-06
  AttachmentSupport = -> [Pad672]
  ExternalGeometry = -> [Pad672]
  FullyConstrained = true
  MakeInternals = false
  MapMode = 5
  Placement = pos=(0,22.7,0) rot=(0,0.707107,0.707107;3.14159rad)
  sketch-geometry (4):
    g0: LineSegment StartX=-21.2 StartY=-2.6688 StartZ=0 EndX=-21.2 EndY=-5.8e-15 EndZ=0
    g1: LineSegment StartX=-19.2 StartY=-2.6688 StartZ=0 EndX=-19.2 EndY=-5.8e-15 EndZ=0
    g2: LineSegment StartX=-19.2 StartY=-5.8e-15 StartZ=0 EndX=-21.2 EndY=-5.8e-15 EndZ=0
    g3: ArcOfCircle CenterX=-20.2 CenterY=-1.65468e-05 CenterZ=0 NormalX=0 NormalY=0 NormalZ=1 AngleXU=0 Radius=2.84998 StartAngle=4.35388 EndAngle=5.0709
  constraints (11):
    c: Coincident(g0,g-5)
    c: PointOnObject(g0,g-4)
    c: Vertical(g0)
    c: Coincident(g1,g-6)
    c: PointOnObject(g1,g-4)
    c: Vertical(g1)
    c: Coincident(g2,g1)
    c: Coincident(g2,g0)
    c: Coincident(g3,g0)
    c: Coincident(g3,g1)
    c: Tangent(g3,g-3)
FEATURE [PartDesign::Pocket] Pocket478
  BaseFeature = -> Pad672
  Direction = (0,-1,2e-16)
  Length = 0.5
  Length2 = 5
  Profile = -> Sketch1034
  ReferenceAxis = -> Sketch1034 [N_Axis]
  Refine = true
  Suppressed = false
  Type = 0
FEATURE [Sketcher::SketchObject] Sketch1035
  ArcFitTolerance = 1e-06
  AttachmentSupport = -> [Pocket478]
  ExternalGeometry = -> [Pocket478]
  FullyConstrained = true
  MakeInternals = false
  MapMode = 5
  Placement = pos=(0,-1,2e-16) rot=(1,0,0;1.5708rad)
  sketch-geometry (4):
    g0: LineSegment StartX=19.2 StartY=-2.6688 StartZ=0 EndX=19.2 EndY=0 EndZ=0
    g1: LineSegment StartX=21.2 StartY=-2.6688 StartZ=0 EndX=21.2 EndY=-4e-16 EndZ=0
    g2: LineSegment StartX=21.2 StartY=-4e-16 StartZ=0 EndX=19.2 EndY=0 EndZ=0
    g3: ArcOfCircle CenterX=20.2 CenterY=-2.79372e-05 CenterZ=0 NormalX=0 NormalY=0 NormalZ=1 AngleXU=0 Radius=2.84997 StartAngle=4.35388 EndAngle=5.0709
  constraints (11):
    c: Coincident(g0,g-6)
    c: PointOnObject(g0,g-3)
    c: Vertical(g0)
    c: Coincident(g1,g-5)
    c: PointOnObject(g1,g-3)
    c: Vertical(g1)
    c: Coincident(g2,g1)
    c: Coincident(g2,g0)
    c: Coincident(g3,g0)
    c: Coincident(g3,g1)
    c: Tangent(g3,g-4)
FEATURE [PartDesign::Pocket] Pocket479
  BaseFeature = -> Pocket478
  Direction = (0,1,-2e-16)
  Length = 0.5
  Length2 = 5
  Profile = -> Sketch1035
  ReferenceAxis = -> Sketch1035 [N_Axis]
  Refine = true
  Suppressed = false
  Type = 0
FEATURE [PartDesign::Chamfer] Chamfer051
  Angle = 45
  Base = -> Pocket479 [Edge188,Edge205,Edge304,Edge303,Edge302,Edge226,Edge227,Edge228,Edge229,Edge204,Edge198,Edge197,Edge189,Edge192,Edge193,Edge186,Edge185,Edge288,Edge295,Edge301,Edge164,Edge157,Edge151,Edge143,Edge140,Edge141,Edge142]
  BaseFeature = -> Pocket479
  ChamferType = 0
  FlipDirection = false
  Refine = true
  Size = 0.999
  Size2 = 1
  SupportTransform = false
  Suppressed = false
  UseAllEdges = false
FEATURE [PartDesign::Pocket] Pocket480
  BaseFeature = -> Chamfer051
  Direction = (-1,0,0)
  Length = 1.9
  Length2 = 5
  Profile = -> Chamfer051 [Face43]
  Refine = true
  Suppressed = false
  Type = 0
FEATURE [Sketcher::SketchObject] Sketch1036
  ArcFitTolerance = 1e-06
  AttachmentSupport = -> [Pocket480]
  ExternalGeometry = -> [Pocket480]
  FullyConstrained = true
  MakeInternals = false
  MapMode = 5
  sketch-geometry (6):
    g0: LineSegment StartX=31.6 StartY=15.301 StartZ=0 EndX=31.6 EndY=6.401 EndZ=0
    g1: LineSegment StartX=31.6 StartY=6.401 StartZ=0 EndX=39.05 EndY=6.401 EndZ=0
    g2: LineSegment StartX=31.6 StartY=15.301 StartZ=0 EndX=39.05 EndY=15.301 EndZ=0
    g3: ArcOfCircle CenterX=39.05 CenterY=10.851 CenterZ=0 NormalX=0 NormalY=0 NormalZ=1 AngleXU=0 Radius=4.45 StartAngle=4.71239 EndAngle=7.85398
    g4: LineSegment [constr] StartX=39.05 StartY=15.301 StartZ=0 EndX=39.05 EndY=10.851 EndZ=0
    g5: LineSegment [constr] StartX=39.05 StartY=10.851 StartZ=0 EndX=39.05 EndY=6.401 EndZ=0
  constraints (18):
    c: PointOnObject(g0,g-3)
    c: PointOnObject(g0,g-3)
    c: Coincident(g1,g0)
    c: Horizontal(g1)
    c: Coincident(g2,g0)
    c: Horizontal(g2)
    c: Coincident(g3,g2)
    c: Coincident(g3,g1)
    c: Coincident(g4,g2)
    c: Coincident(g4,g3)
    c: Coincident(g5,g3)
    c: Coincident(g5,g1)
    c: Vertical(g4)
    c: Vertical(g5)
    c: DistanceY(g0,g0) = 8.9
    c: DistanceY(g0,g-3) = 2.5
    c: DistanceY(g-3,g0) = 2.502
    c: DistanceX(g2,g2) = 7.45
FEATURE [PartDesign::Pad] Pad673
  BaseFeature = -> Pocket480
  Direction = (0,0,1)
  Length = 1.8
  Length2 = 10
  Profile = -> Sketch1036
  ReferenceAxis = -> Sketch1036 [N_Axis]
  Refine = true
  Reversed = true
  Suppressed = false
  Type = 0
FEATURE [Sketcher::SketchObject] Sketch1037
  ArcFitTolerance = 1e-06
  AttachmentSupport = -> [Pad673]
  ExternalGeometry = -> [Pad673]
  FullyConstrained = true
  MakeInternals = false
  MapMode = 5
  Placement = pos=(0,6.401,0) rot=(1,0,0;1.5708rad)
  sketch-geometry (4):
    g0: LineSegment StartX=31.6 StartY=0 StartZ=0 EndX=34.6 EndY=0 EndZ=0
    g1: LineSegment StartX=34.6 StartY=0 StartZ=0 EndX=34.6 EndY=3 EndZ=0
    g2: LineSegment StartX=34.6 StartY=3 StartZ=0 EndX=31.6 EndY=3 EndZ=0
    g3: LineSegment StartX=31.6 StartY=3 StartZ=0 EndX=31.6 EndY=0 EndZ=0
  constraints (11):
    c: Coincident(g0,g1)
    c: Coincident(g1,g2)
    c: Coincident(g2,g3)
    c: Coincident(g3,g0)
    c: Horizontal(g0)
    c: Horizontal(g2)
    c: Vertical(g1)
    c: Vertical(g3)
    c: Coincident(g0,g-3)
    c: DistanceX(g2,g2) = 3
    c: DistanceY(g1,g1) = 3
FEATURE [PartDesign::Pad] Pad674
  BaseFeature = -> Pad673
  Direction = (0,-1,2e-16)
  Length = 8.9
  Length2 = 10
  Profile = -> Sketch1037
  ReferenceAxis = -> Sketch1037 [N_Axis]
  Refine = true
  Reversed = true
  Suppressed = false
  Type = 0
FEATURE [Sketcher::SketchObject] Sketch1038
  ArcFitTolerance = 1e-06
  AttachmentSupport = -> [Pad674]
  ExternalGeometry = -> [Pad674]
  FullyConstrained = true
  MakeInternals = false
  MapMode = 5
  Placement = pos=(31.6,0,0) rot=(0.57735,-0.57735,-0.57735;2.0944rad)
  sketch-geometry (4):
    g0: LineSegment StartX=-13.801 StartY=0 StartZ=0 EndX=-7.901 EndY=0 EndZ=0
    g1: LineSegment StartX=-7.901 StartY=0 StartZ=0 EndX=-7.901 EndY=1.5 EndZ=0
    g2: LineSegment StartX=-7.901 StartY=1.5 StartZ=0 EndX=-13.801 EndY=1.5 EndZ=0
    g3: LineSegment StartX=-13.801 StartY=1.5 StartZ=0 EndX=-13.801 EndY=0 EndZ=0
  constraints (13):
    c: Coincident(g0,g1)
    c: Coincident(g1,g2)
    c: Coincident(g2,g3)
    c: Coincident(g3,g0)
    c: Horizontal(g0)
    c: Horizontal(g2)
    c: Vertical(g1)
    c: Vertical(g3)
    c: PointOnObject(g0,g-1)
    c: DistanceY(g3,g3) = 1.5
    c: DistanceX(g2,g2) = 5.9
    c: DistanceX(g-3,g-3) = 0
    c: DistanceX(g-3,g0) = 1.5
FEATURE [PartDesign::Pocket] Pocket481
  BaseFeature = -> Pad674
  Direction = (1,0,0)
  Length = 5
  Length2 = 5
  Profile = -> Sketch1038
  ReferenceAxis = -> Sketch1038 [N_Axis]
  Refine = true
  Suppressed = false
  Type = 0
FEATURE [Sketcher::SketchObject] Sketch1039
  ArcFitTolerance = 1e-06
  AttachmentSupport = -> [Pocket481]
  ExternalGeometry = -> [Pocket481]
  FullyConstrained = true
  MakeInternals = false
  MapMode = 5
  Placement = pos=(0,0,-1e-16) rot=(0,0,1;0rad)
  sketch-geometry (1):
    g0: Circle CenterX=39.05 CenterY=10.851 CenterZ=0 NormalX=0 NormalY=0 NormalZ=1 AngleXU=0 Radius=3.7
  constraints (2):
    c: Coincident(g0,g-3)
    c: Radius(g0) = 3.7
FEATURE [PartDesign::Pad] Pad675
  BaseFeature = -> Pocket481
  Direction = (0,0,1)
  Length = 4.5
  Length2 = 10
  Profile = -> Sketch1039
  ReferenceAxis = -> Sketch1039 [N_Axis]
  Refine = true
  Suppressed = false
  Type = 0
FEATURE [Sketcher::SketchObject] Sketch1040
  ArcFitTolerance = 1e-06
  AttachmentSupport = -> [Pad675]
  ExternalGeometry = -> [Pad675]
  FullyConstrained = true
  MakeInternals = false
  MapMode = 5
  Placement = pos=(0,0,-1.8) rot=(1,0,0;3.14159rad)
  sketch-geometry (6):
    g0: LineSegment StartX=31.6 StartY=-7.901 StartZ=0 EndX=31.6 EndY=-13.801 EndZ=0
    g1: LineSegment StartX=31.6 StartY=-13.801 StartZ=0 EndX=33.6 EndY=-13.801 EndZ=0
    g2: LineSegment StartX=33.6 StartY=-13.801 StartZ=0 EndX=33.6 EndY=-7.901 EndZ=0
    g3: LineSegment StartX=33.6 StartY=-7.901 StartZ=0 EndX=31.6 EndY=-7.901 EndZ=0
    g4: LineSegment [constr] StartX=33.6 StartY=-7.901 StartZ=0 EndX=34.6 EndY=-7.901 EndZ=0
    g5: LineSegment [constr] StartX=33.6 StartY=-13.801 StartZ=0 EndX=34.6 EndY=-13.801 EndZ=0
  constraints (16):
    c: Coincident(g0,g1)
    c: Coincident(g1,g2)
    c: Coincident(g2,g3)
    c: Coincident(g3,g0)
    c: Vertical(g0)
    c: Vertical(g2)
    c: Horizontal(g1)
    c: Horizontal(g3)
    c: PointOnObject(g0,g-3)
    c: DistanceX(g3,g3) = 2
    c: Coincident(g4,g2)
    c: Coincident(g4,g-4)
    c: Coincident(g5,g1)
    c: Coincident(g5,g-4)
    c: Horizontal(g5)
    c: Horizontal(g4)
FEATURE [PartDesign::Pocket] Pocket482
  BaseFeature = -> Pad675
  Direction = (0,0,1)
  Length = 2
  Length2 = 5
  Profile = -> Sketch1040
  ReferenceAxis = -> Sketch1040 [N_Axis]
  Refine = true
  Suppressed = false
  Type = 0
FEATURE [Sketcher::SketchObject] Sketch1041
  ArcFitTolerance = 1e-06
  AttachmentSupport = -> [Pocket482]
  ExternalGeometry = -> [Pocket482]
  FullyConstrained = true
  MakeInternals = false
  MapMode = 5
  Placement = pos=(0,15.301,0) rot=(0,0.707107,0.707107;3.14159rad)
  sketch-geometry (4):
    g0: LineSegment StartX=-31.6 StartY=-1.8 StartZ=0 EndX=-31.6 EndY=-3.501 EndZ=0
    g1: LineSegment StartX=-31.6 StartY=-3.501 StartZ=0 EndX=-34.6 EndY=-3.501 EndZ=0
    g2: LineSegment StartX=-34.6 StartY=-3.501 StartZ=0 EndX=-34.6 EndY=-1.8 EndZ=0
    g3: LineSegment StartX=-31.6 StartY=-1.8 StartZ=0 EndX=-34.6 EndY=-1.8 EndZ=0
  constraints (11):
    c: DistanceX(g-4,g-4) = 3
    c: PointOnObject(g2,g-3)
    c: Coincident(g0,g-5)
    c: Coincident(g1,g0)
    c: Horizontal(g1)
    c: Coincident(g2,g1)
    c: Vertical(g2)
    c: Coincident(g3,g0)
    c: Coincident(g3,g2)
    c: DistanceX(g3,g3) = 3
    c: Coincident(g0,g-3)
FEATURE [PartDesign::Pad] Pad676
  BaseFeature = -> Pocket482
  Direction = (0,1,-2e-16)
  Length = 1.5
  Length2 = 10
  Profile = -> Sketch1041
  ReferenceAxis = -> Sketch1041 [N_Axis]
  Refine = true
  Reversed = true
  Suppressed = false
  Type = 0
FEATURE [Sketcher::SketchObject] Sketch1042
  ArcFitTolerance = 1e-06
  AttachmentSupport = -> [Pad676]
  ExternalGeometry = -> [Pad676]
  FullyConstrained = true
  MakeInternals = false
  MapMode = 5
  Placement = pos=(0,6.401,0) rot=(1,0,0;1.5708rad)
  sketch-geometry (4):
    g0: LineSegment StartX=31.6 StartY=-1.8 StartZ=0 EndX=31.6 EndY=-3.501 EndZ=0
    g1: LineSegment StartX=31.6 StartY=-3.501 StartZ=0 EndX=34.6 EndY=-3.501 EndZ=0
    g2: LineSegment StartX=34.6 StartY=-3.501 StartZ=0 EndX=34.6 EndY=-1.8 EndZ=0
    g3: LineSegment StartX=34.6 StartY=-1.8 StartZ=0 EndX=31.6 EndY=-1.8 EndZ=0
  constraints (10):
    c: Coincident(g0,g1)
    c: Coincident(g1,g2)
    c: Coincident(g2,g3)
    c: Coincident(g3,g0)
    c: Vertical(g0)
    c: Vertical(g2)
    c: Horizontal(g1)
    c: Horizontal(g3)
    c: Coincident(g0,g-5)
    c: Coincident(g1,g-4)
FEATURE [PartDesign::Pad] Pad677
  BaseFeature = -> Pad676
  Direction = (0,-1,2e-16)
  Length = 1.5
  Length2 = 10
  Profile = -> Sketch1042
  ReferenceAxis = -> Sketch1042 [N_Axis]
  Refine = true
  Reversed = true
  Suppressed = false
  Type = 0
FEATURE [Sketcher::SketchObject] Sketch1043
  ArcFitTolerance = 1e-06
  AttachmentSupport = -> [Pad677]
  ExternalGeometry = -> [Pad677]
  FullyConstrained = true
  MakeInternals = false
  MapMode = 5
  Placement = pos=(0,0,-1.8) rot=(1,0,0;3.14159rad)
  sketch-geometry (1):
    g0: Circle CenterX=39.05 CenterY=-10.851 CenterZ=0 NormalX=0 NormalY=0 NormalZ=1 AngleXU=0 Radius=2.75
  constraints (2):
    c: Coincident(g0,g-3)
    c: Radius(g0) = 2.75
FEATURE [PartDesign::Pocket] Pocket483
  BaseFeature = -> Pad677
  Direction = (0,0,1)
  Length = 5
  Length2 = 5
  Profile = -> Sketch1043
  ReferenceAxis = -> Sketch1043 [N_Axis]
  Refine = true
  Suppressed = false
  Type = 0
FEATURE [Sketcher::SketchObject] Sketch1044
  ArcFitTolerance = 1e-06
  AttachmentSupport = -> [Pocket483]
  ExternalGeometry = -> [Pocket483]
  FullyConstrained = true
  MakeInternals = false
  MapMode = 5
  Placement = pos=(0,0,3.2) rot=(1,0,0;3.14159rad)
  sketch-geometry (2):
    g0: Circle CenterX=39.05 CenterY=-10.851 CenterZ=0 NormalX=0 NormalY=0 NormalZ=1 AngleXU=0 Radius=2.65
    g1: Circle CenterX=39.05 CenterY=-10.851 CenterZ=0 NormalX=0 NormalY=0 NormalZ=1 AngleXU=0 Radius=2.74999
  constraints (4):
    c: Coincident(g0,g-3)
    c: Radius(g0) = 2.65
    c: Coincident(g1,g0)
    c: Tangent(g1,g-3)
FEATURE [PartDesign::Pad] Pad678
  BaseFeature = -> Pocket483
  Direction = (0,0,-1)
  Length = 5
  Length2 = 10
  Profile = -> Sketch1044
  ReferenceAxis = -> Sketch1044 [N_Axis]
  Refine = true
  Suppressed = false
  Type = 0
FEATURE [Sketcher::SketchObject] Sketch1045
  ArcFitTolerance = 1e-06
  AttachmentSupport = -> [Pad678]
  ExternalGeometry = -> [Pad678]
  FullyConstrained = true
  MakeInternals = false
  MapMode = 5
  Placement = pos=(0,0,-1.8) rot=(1,0,0;3.14159rad)
  sketch-geometry (1):
    g0: Circle CenterX=39.05 CenterY=-10.851 CenterZ=0 NormalX=0 NormalY=0 NormalZ=1 AngleXU=0 Radius=2.75
  constraints (2):
    c: Coincident(g0,g-3)
    c: Radius(g0) = 2.75
FEATURE [PartDesign::SubtractiveLoft] SubtractiveLoft002
  BaseFeature = -> Pad678
  Closed = false
  Profile = -> Pad678 [Edge487]
  Refine = true
  Ruled = false
  Sections = -> [Sketch1045]
  Suppressed = false
FEATURE [Sketcher::SketchObject] Sketch1046
  ArcFitTolerance = 1e-06
  AttachmentSupport = -> [SubtractiveLoft002]
  ExternalGeometry = -> [SubtractiveLoft002]
  FullyConstrained = true
  MakeInternals = false
  MapMode = 5
  Placement = pos=(0,6.401,0) rot=(1,0,0;1.5708rad)
  sketch-geometry (4):
    g0: LineSegment StartX=31.6 StartY=-3.501 StartZ=0 EndX=34.6 EndY=-3.501 EndZ=0
    g1: LineSegment StartX=31.6 StartY=-3.501 StartZ=0 EndX=33.6 EndY=-1.8 EndZ=0
    g2: LineSegment StartX=34.6 StartY=-1.8 StartZ=0 EndX=33.6 EndY=-1.8 EndZ=0
    g3: LineSegment StartX=34.6 StartY=-1.8 StartZ=0 EndX=34.6 EndY=-3.501 EndZ=0
  constraints (8):
    c: Coincident(g0,g-4)
    c: Coincident(g1,g0)
    c: Coincident(g2,g-3)
    c: Coincident(g2,g1)
    c: Coincident(g3,g2)
    c: Coincident(g3,g0)
    c: Coincident(g1,g-5)
    c: Coincident(g0,g-4)
FEATURE [PartDesign::Pocket] Pocket484
  BaseFeature = -> SubtractiveLoft002
  Direction = (0,1,-2e-16)
  Length = 5
  Length2 = 5
  Profile = -> Sketch1046
  ReferenceAxis = -> Sketch1046 [N_Axis]
  Refine = true
  Suppressed = false
  Type = 1
FEATURE [Sketcher::SketchObject] Sketch1047
  ArcFitTolerance = 1e-06
  AttachmentSupport = -> [Pocket484]
  ExternalGeometry = -> [Pocket484]
  FullyConstrained = true
  MakeInternals = false
  MapMode = 5
  Placement = pos=(0,0,-5.5) rot=(1,0,0;3.14159rad)
  sketch-geometry (3):
    g0: Circle CenterX=6.659 CenterY=-10.85 CenterZ=0 NormalX=0 NormalY=0 NormalZ=1 AngleXU=0 Radius=2.5
    g1: Circle CenterX=19.659 CenterY=-10.85 CenterZ=0 NormalX=0 NormalY=0 NormalZ=1 AngleXU=0 Radius=2.5
    g2: LineSegment [constr] StartX=6.659 StartY=-10.85 StartZ=0 EndX=19.659 EndY=-10.85 EndZ=0
  constraints (9):
    c: Diameter(g0) = 5
    c: Diameter(g1) = 5
    c: Coincident(g2,g0)
    c: Coincident(g2,g1)
    c: Horizontal(g2)
    c: DistanceY(g-5,g-4) = 21.7
    c: DistanceY(g0,g-4) = 10.85
    c: DistanceX(g2,g2) = 13
    c: DistanceX(g-4,g0) = 5.66
FEATURE [PartDesign::Pad] Pad679
  BaseFeature = -> Pocket484
  Direction = (0,0,-1)
  Length = 2.8
  Length2 = 10
  Profile = -> Sketch1047
  ReferenceAxis = -> Sketch1047 [N_Axis]
  Refine = true
  Suppressed = false
  Type = 0
FEATURE [Sketcher::SketchObject] Sketch1048
  ArcFitTolerance = 1e-06
  AttachmentSupport = -> [Pad679]
  ExternalGeometry = -> [Pad679]
  FullyConstrained = true
  MakeInternals = false
  MapMode = 5
  Placement = pos=(0,0,-8.3) rot=(1,0,0;3.14159rad)
  sketch-geometry (2):
    g0: Circle CenterX=6.659 CenterY=-10.85 CenterZ=0 NormalX=0 NormalY=0 NormalZ=1 AngleXU=0 Radius=1.5
    g1: Circle CenterX=19.659 CenterY=-10.85 CenterZ=0 NormalX=0 NormalY=0 NormalZ=1 AngleXU=0 Radius=1.5
  constraints (4):
    c: Coincident(g0,g-3)
    c: Coincident(g1,g-4)
    c: Radius(g0) = 1.5
    c: Radius(g1) = 1.5
FEATURE [PartDesign::Pocket] Pocket485
  BaseFeature = -> Pad679
  Direction = (0,0,1)
  Length = 2.8
  Length2 = 5
  Profile = -> Sketch1048
  ReferenceAxis = -> Sketch1048 [N_Axis]
  Refine = true
  Suppressed = false
  Type = 0
FEATURE [Sketcher::SketchObject] Sketch1049
  ArcFitTolerance = 1e-06
  AttachmentSupport = -> [Pocket485]
  ExternalGeometry = -> [Pocket485]
  FullyConstrained = true
  MakeInternals = false
  MapMode = 5
  Placement = pos=(0,0,-5) rot=(1,0,0;3.14159rad)
  sketch-geometry (1):
    g0: Circle CenterX=19.659 CenterY=-10.85 CenterZ=0 NormalX=0 NormalY=0 NormalZ=1 AngleXU=0 Radius=2.5
  constraints (2):
    c: Coincident(g0,g-3)
    c: Equal(g0,g-3)
FEATURE [PartDesign::Pad] Pad680
  BaseFeature = -> Pocket485
  Direction = (0,0,-1)
  Length = 0.5
  Length2 = 10
  Profile = -> Sketch1049
  ReferenceAxis = -> Sketch1049 [N_Axis]
  Refine = true
  Suppressed = false
  Type = 0
FEATURE [PartDesign::Body] Body050  label="Right_Inner_Arm"
  AllowCompound = false
  Group = -> [Binder011,Sketch1010,Pad660,Sketch1011,Pad661,Sketch1012,Pad662,Sketch1013,Pocket467,Sketch1014,Pocket468,Chamfer049,Chamfer050,Sketch1015,Pocket469,Sketch1016,Pad663,Sketch1017,Pocket470,Sketch1018,Pad664,Sketch1019,Pad665,Sketch1020,Pad666,Sketch1021,Pocket471,Sketch1022,Pocket472,Sketch1023,Pad667,Sketch1024,Pocket473,Sketch1025,Pocket474,Sketch1026,Pad668,Sketch1027,Pad669,Sketch1028,Pad670,+44 more]
  Origin = -> Origin055
  Placement = pos=(-105.99,55,-5.5) rot=(0,-1,0;3.14159rad)
  Tip = -> Pad680
FEATURE [Sketcher::SketchObject] Sketch1050
  ArcFitTolerance = 1e-06
  AttachmentSupport = -> [XZ_Plane056]
  FullyConstrained = true
  MakeInternals = false
  MapMode = 5
  Placement = pos=(0,0,0) rot=(1,0,0;1.5708rad)
  sketch-geometry (1):
    g0: Circle CenterX=0 CenterY=0 CenterZ=0 NormalX=0 NormalY=0 NormalZ=1 AngleXU=0 Radius=2
  constraints (2):
    c: Coincident(g0,g-1)
    c: Radius(g0) = 2
FEATURE [PartDesign::Pad] Pad681
  Direction = (0,-1,2e-16)
  Length = 3
  Length2 = 10
  Placement = pos=(0,0,0) rot=(1,0,0;1.5708rad)
  Profile = -> Sketch1050
  ReferenceAxis = -> Sketch1050 [N_Axis]
  Refine = true
  Suppressed = false
  Type = 0
FEATURE [Sketcher::SketchObject] Sketch1051
  ArcFitTolerance = 1e-06
  AttachmentSupport = -> [Pad681]
  ExternalGeometry = -> [Pad681]
  FullyConstrained = true
  MakeInternals = false
  MapMode = 5
  Placement = pos=(0,-3,0) rot=(1,0,0;1.5708rad)
  sketch-geometry (4):
    g0: LineSegment StartX=2 StartY=1e-16 StartZ=0 EndX=6.75 EndY=1e-16 EndZ=0
    g1: LineSegment StartX=6.75 StartY=1e-16 StartZ=0 EndX=6.75 EndY=2 EndZ=0
    g2: LineSegment StartX=6.75 StartY=2 StartZ=0 EndX=-3.206e-13 EndY=2 EndZ=0
    g3: ArcOfCircle CenterX=-3.212e-13 CenterY=-3.345e-13 CenterZ=0 NormalX=0 NormalY=0 NormalZ=1 AngleXU=0 Radius=2 StartAngle=1.673e-13 EndAngle=1.5708
  constraints (13):
    c: PointOnObject(g0,g-3)
    c: PointOnObject(g0,g-1)
    c: Horizontal(g0)
    c: Coincident(g1,g0)
    c: Vertical(g1)
    c: Coincident(g2,g1)
    c: PointOnObject(g2,g-3)
    c: Horizontal(g2)
    c: DistanceX(g0,g0) = 4.75
    c: Coincident(g3,g0)
    c: Coincident(g3,g2)
    c: Tangent(g3,g-3)
    c: DistanceX(g3,g2) = 0
FEATURE [PartDesign::Pad] Pad682
  BaseFeature = -> Pad681
  Direction = (0,-1,2e-16)
  Length = 3
  Length2 = 10
  Placement = pos=(0,0,0) rot=(1,0,0;1.5708rad)
  Profile = -> Sketch1051
  ReferenceAxis = -> Sketch1051 [N_Axis]
  Refine = true
  Reversed = true
  Suppressed = false
  Type = 0
FEATURE [Sketcher::SketchObject] Sketch1052
  ArcFitTolerance = 1e-06
  AttachmentSupport = -> [Pad682]
  ExternalGeometry = -> [Pad682]
  FullyConstrained = true
  MakeInternals = false
  MapMode = 5
  Placement = pos=(0,-3,1.3e-15) rot=(1,0,0;1.5708rad)
  sketch-geometry (15):
    g0: LineSegment StartX=1 StartY=2 StartZ=0 EndX=1 EndY=8 EndZ=0
    g1: LineSegment StartX=1 StartY=8 StartZ=0 EndX=2.3 EndY=8 EndZ=0
    g2: LineSegment StartX=2.3 StartY=8 StartZ=0 EndX=2.3 EndY=8.7 EndZ=0
    g3: LineSegment StartX=2.3 StartY=8.7 StartZ=0 EndX=1 EndY=10 EndZ=0
    g4: LineSegment StartX=1 StartY=10 StartZ=0 EndX=-2.2 EndY=10 EndZ=0
    g5: LineSegment StartX=-2.2 StartY=10 StartZ=0 EndX=-9.5 EndY=2.7 EndZ=0
    g6: LineSegment StartX=-9.5 StartY=2.7 StartZ=0 EndX=-9.5 EndY=1 EndZ=0
    g7: LineSegment StartX=-9.5 StartY=1 StartZ=0 EndX=-5.25 EndY=1 EndZ=0
    g8: LineSegment StartX=-5.25 StartY=1 StartZ=0 EndX=-5.25 EndY=2 EndZ=0
    g9: LineSegment StartX=-5.25 StartY=2 StartZ=0 EndX=-2 EndY=2 EndZ=0
    g10: LineSegment StartX=-2 StartY=2 StartZ=0 EndX=-2 EndY=6.59786e-11 EndZ=0
    g11: LineSegment StartX=1 StartY=2 StartZ=0 EndX=-6.62992e-11 EndY=2 EndZ=0
    g12: ArcOfCircle CenterX=-1.1487e-05 CenterY=1.1487e-05 CenterZ=0 NormalX=0 NormalY=0 NormalZ=1 AngleXU=0 Radius=1.99999 StartAngle=1.57079 EndAngle=3.1416
    g13: LineSegment [constr] StartX=1 StartY=10 StartZ=0 EndX=1 EndY=8 EndZ=0
    g14: LineSegment [constr] StartX=-6.62992e-11 StartY=2 StartZ=0 EndX=-2 EndY=2 EndZ=0
  constraints (43):
    c: PointOnObject(g0,g-3)
    c: Vertical(g0)
    c: Coincident(g1,g0)
    c: Horizontal(g1)
    c: Coincident(g2,g1)
    c: Vertical(g2)
    c: Coincident(g3,g2)
    c: Coincident(g4,g3)
    c: Horizontal(g4)
    c: Coincident(g5,g4)
    c: Coincident(g6,g5)
    c: Vertical(g6)
    c: Coincident(g7,g6)
    c: Horizontal(g7)
    c: Coincident(g8,g7)
    c: Vertical(g8)
    c: Coincident(g9,g8)
    c: Horizontal(g9)
    c: Coincident(g10,g9)
    c: PointOnObject(g10,g-4)
    c: Vertical(g10)
    c: Coincident(g11,g0)
    c: Coincident(g11,g-4)
    c: Coincident(g12,g11)
    c: Coincident(g12,g10)
    c: DistanceY(g0,g3) = 8
    c: DistanceX(g7,g7) = 4.25
    c: DistanceY(g0,g3) = 2
    c: DistanceX(g1,g1) = 1.3
    c: Angle(g5,g4) = 2.35619
    c: Coincident(g13,g3)
    c: Coincident(g13,g0)
    c: Vertical(g13)
    c: Angle(g3,g2) = 2.35619
    c: DistanceY(g8,g8) = 1
    c: PointOnObject(g10,g-1)
    c: DistanceX(g9,g0) = 3
    c: DistanceY(g6,g6) = 1.7
    c: Coincident(g14,g11)
    c: Coincident(g14,g9)
    c: Tangent(g14,g12)
    c: Horizontal(g14)
    c: DistanceX(g9,g9) = 3.25
FEATURE [PartDesign::Pad] Pad683
  BaseFeature = -> Pad682
  Direction = (0,-1,2e-16)
  Length = 3
  Length2 = 10
  Placement = pos=(0,0,0) rot=(1,0,0;1.5708rad)
  Profile = -> Sketch1052
  ReferenceAxis = -> Sketch1052 [N_Axis]
  Refine = true
  Reversed = true
  Suppressed = false
  Type = 0
FEATURE [Sketcher::SketchObject] Sketch1053
  ArcFitTolerance = 1e-06
  AttachmentSupport = -> [Pad683]
  ExternalGeometry = -> [Pad683]
  FullyConstrained = true
  MakeInternals = false
  MapMode = 5
  Placement = pos=(0,-3,1.4e-15) rot=(1,0,0;1.5708rad)
  sketch-geometry (1):
    g0: Circle CenterX=0 CenterY=0 CenterZ=0 NormalX=0 NormalY=0 NormalZ=1 AngleXU=0 Radius=2.00001
  constraints (2):
    c: Coincident(g0,g-1)
    c: Tangent(g0,g-3)
FEATURE [PartDesign::Pad] Pad684
  BaseFeature = -> Pad683
  Direction = (0,-1,2e-16)
  Length = 1
  Length2 = 10
  Placement = pos=(0,0,0) rot=(1,0,0;1.5708rad)
  Profile = -> Sketch1053
  ReferenceAxis = -> Sketch1053 [N_Axis]
  Refine = true
  Suppressed = false
  Type = 0
FEATURE [Sketcher::SketchObject] Sketch1054
  ArcFitTolerance = 1e-06
  AttachmentSupport = -> [Pad684]
  ExternalGeometry = -> [Pad684]
  FullyConstrained = true
  MakeInternals = false
  MapMode = 5
  Placement = pos=(0,0,0) rot=(-1,0,0;1.5708rad)
  sketch-geometry (1):
    g0: Circle CenterX=0 CenterY=0 CenterZ=0 NormalX=0 NormalY=0 NormalZ=1 AngleXU=0 Radius=1.99999
  constraints (2):
    c: Coincident(g0,g-1)
    c: Tangent(g0,g-3)
FEATURE [PartDesign::Pad] Pad685
  BaseFeature = -> Pad684
  Direction = (0,1,2e-16)
  Length = 1
  Length2 = 10
  Placement = pos=(0,0,0) rot=(1,0,0;1.5708rad)
  Profile = -> Sketch1054
  ReferenceAxis = -> Sketch1054 [N_Axis]
  Refine = true
  Suppressed = false
  Type = 0
FEATURE [Sketcher::SketchObject] Sketch1055
  ArcFitTolerance = 1e-06
  AttachmentSupport = -> [Pad685]
  FullyConstrained = true
  MakeInternals = false
  MapMode = 5
  Placement = pos=(0,1,0) rot=(-1,0,0;1.5708rad)
  sketch-geometry (1):
    g0: Circle CenterX=0 CenterY=0 CenterZ=0 NormalX=0 NormalY=0 NormalZ=1 AngleXU=0 Radius=1
  constraints (2):
    c: Coincident(g0,g-1)
    c: Diameter(g0) = 2
FEATURE [PartDesign::Pad] Pad686
  BaseFeature = -> Pad685
  Direction = (0,1,2e-16)
  Length = 2.6
  Length2 = 10
  Placement = pos=(0,0,0) rot=(1,0,0;1.5708rad)
  Profile = -> Sketch1055
  ReferenceAxis = -> Sketch1055 [N_Axis]
  Refine = true
  Suppressed = false
  Type = 0
FEATURE [Sketcher::SketchObject] Sketch1056
  ArcFitTolerance = 1e-06
  AttachmentSupport = -> [Pad686]
  ExternalGeometry = -> [Pad686]
  FullyConstrained = true
  MakeInternals = false
  MapMode = 5
  Placement = pos=(0,-4,1e-15) rot=(1,0,0;1.5708rad)
  sketch-geometry (1):
    g0: Circle CenterX=0 CenterY=0 CenterZ=0 NormalX=0 NormalY=0 NormalZ=1 AngleXU=0 Radius=1
  constraints (2):
    c: Coincident(g0,g-1)
    c: Diameter(g0) = 2
FEATURE [PartDesign::Pad] Pad687
  BaseFeature = -> Pad686
  Direction = (0,-1,2e-16)
  Length = 2.6
  Length2 = 10
  Placement = pos=(0,0,0) rot=(1,0,0;1.5708rad)
  Profile = -> Sketch1056
  ReferenceAxis = -> Sketch1056 [N_Axis]
  Refine = true
  Suppressed = false
  Type = 0
FEATURE [Sketcher::SketchObject] Sketch1057
  ArcFitTolerance = 1e-06
  AttachmentSupport = -> [Pad687]
  ExternalGeometry = -> [Pad687]
  FullyConstrained = true
  MakeInternals = false
  MapMode = 5
  Placement = pos=(0,9e-16,2) rot=(0,0,1;3.14159rad)
  sketch-geometry (2):
    g0: Circle CenterX=-3.5 CenterY=1.5 CenterZ=0 NormalX=0 NormalY=0 NormalZ=1 AngleXU=0 Radius=0.75
    g1: LineSegment [constr] StartX=-3.5 StartY=1.5 StartZ=0 EndX=-4.25 EndY=1.5 EndZ=0
  constraints (7):
    c: Diameter(g0) = 1.5
    c: DistanceY(g-3,g-3) = 3
    c: DistanceY(g0,g-4) = 1.5
    c: Coincident(g1,g0)
    c: PointOnObject(g1,g0)
    c: Horizontal(g1)
    c: DistanceX(g-4,g1) = 2.5
FEATURE [PartDesign::Pad] Pad688
  BaseFeature = -> Pad687
  Direction = (0,0,1)
  Length = 1.5
  Length2 = 10
  Placement = pos=(0,0,0) rot=(1,0,0;1.5708rad)
  Profile = -> Sketch1057
  ReferenceAxis = -> Sketch1057 [N_Axis]
  Refine = true
  Suppressed = false
  Type = 0
FEATURE [Sketcher::SketchObject] Sketch1058
  ArcFitTolerance = 1e-06
  AttachmentSupport = -> [Pad688]
  ExternalGeometry = -> [Pad688]
  FullyConstrained = true
  MakeInternals = false
  MapMode = 5
  Placement = pos=(0,-3,1.4e-15) rot=(1,0,0;1.5708rad)
  sketch-geometry (5):
    g0: ArcOfCircle CenterX=9e-16 CenterY=9 CenterZ=0 NormalX=0 NormalY=0 NormalZ=1 AngleXU=0 Radius=1 StartAngle=4.71239 EndAngle=7.85398
    g1: LineSegment StartX=9e-16 StartY=10 StartZ=0 EndX=9e-16 EndY=9 EndZ=0
    g2: LineSegment StartX=9e-16 StartY=9 StartZ=0 EndX=9e-16 EndY=8 EndZ=0
    g3: LineSegment [constr] StartX=1 StartY=10 StartZ=0 EndX=1 EndY=9 EndZ=0
    g4: LineSegment [constr] StartX=9e-16 StartY=9 StartZ=0 EndX=1 EndY=9 EndZ=0
  constraints (14):
    c: Diameter(g0) = 2
    c: Coincident(g1,g0)
    c: Coincident(g1,g0)
    c: Coincident(g2,g0)
    c: Coincident(g2,g0)
    c: Vertical(g1)
    c: Vertical(g2)
    c: PointOnObject(g0,g-3)
    c: Coincident(g3,g-3)
    c: Vertical(g3)
    c: Coincident(g4,g0)
    c: PointOnObject(g4,g0)
    c: Horizontal(g4)
    c: Tangent(g3,g0) = 1.5708
FEATURE [PartDesign::Pad] Pad689
  BaseFeature = -> Pad688
  Direction = (0,-1,2e-16)
  Length = 2.5
  Length2 = 10
  Placement = pos=(0,0,0) rot=(1,0,0;1.5708rad)
  Profile = -> Sketch1058
  ReferenceAxis = -> Sketch1058 [N_Axis]
  Refine = true
  Suppressed = false
  Type = 0
FEATURE [PartDesign::Body] Body051  label="Trigger2"
  AllowCompound = false
  Group = -> [Sketch1050,Pad681,Sketch1051,Pad682,Sketch1052,Pad683,Sketch1053,Pad684,Sketch1054,Pad685,Sketch1055,Pad686,Sketch1056,Pad687,Sketch1057,Pad688,Sketch1058,Pad689]
  Origin = -> Origin056
  Placement = pos=(-126.05,64.35,-8.5) rot=(0.707107,0,0.707107;3.14159rad)
  Tip = -> Pad689
FEATURE [Sketcher::SketchObject] Sketch1059
  ArcFitTolerance = 1e-06
  AttachmentSupport = -> [XZ_Plane057]
  FullyConstrained = false
  MakeInternals = false
  MapMode = 5
  Placement = pos=(0,0,0) rot=(1,0,0;1.5708rad)
  sketch-geometry (4):
    g0: LineSegment StartX=46.5745 StartY=12.8542 StartZ=0 EndX=41.5745 EndY=12.8542 EndZ=0
    g1: LineSegment StartX=41.5745 StartY=12.8542 StartZ=0 EndX=41.5745 EndY=10.8542 EndZ=0
    g2: LineSegment StartX=41.5745 StartY=10.8542 StartZ=0 EndX=46.5745 EndY=10.8542 EndZ=0
    g3: LineSegment StartX=46.5745 StartY=10.8542 StartZ=0 EndX=46.5745 EndY=12.8542 EndZ=0
  constraints (10):
    c: Coincident(g0,g1)
    c: Coincident(g1,g2)
    c: Coincident(g2,g3)
    c: Coincident(g3,g0)
    c: Horizontal(g0)
    c: Horizontal(g2)
    c: Vertical(g1)
    c: Vertical(g3)
    c: DistanceX(g0,g0) = 5
    c: DistanceY(g3,g3) = 2
FEATURE [PartDesign::Pad] Pad690
  Direction = (0,-1,2e-16)
  Length = 5
  Length2 = 10
  Placement = pos=(0,0,0) rot=(1,0,0;1.5708rad)
  Profile = -> Sketch1059
  ReferenceAxis = -> Sketch1059 [N_Axis]
  Refine = true
  Suppressed = false
  Type = 0
FEATURE [Sketcher::SketchObject] Sketch1060
  ArcFitTolerance = 1e-06
  AttachmentSupport = -> [Pad690]
  ExternalGeometry = -> [Pad690]
  FullyConstrained = true
  MakeInternals = false
  MapMode = 5
  Placement = pos=(0,4.8e-15,10.8542) rot=(1,0,0;3.14159rad)
  sketch-geometry (1):
    g0: Circle CenterX=44.0745 CenterY=2.5 CenterZ=0 NormalX=0 NormalY=0 NormalZ=1 AngleXU=0 Radius=1
  constraints (2):
    c: Symmetric(g-3,g-4,g0)
    c: Radius(g0) = 1
FEATURE [PartDesign::Pocket] Pocket486
  BaseFeature = -> Pad690
  Direction = (0,0,1)
  Length = 5
  Length2 = 5
  Placement = pos=(0,0,0) rot=(1,0,0;1.5708rad)
  Profile = -> Sketch1060
  ReferenceAxis = -> Sketch1060 [N_Axis]
  Refine = true
  Suppressed = false
  Type = 0
FEATURE [Sketcher::SketchObject] Sketch1061
  ArcFitTolerance = 1e-06
  AttachmentSupport = -> [Pocket486]
  ExternalGeometry = -> [Pocket486]
  FullyConstrained = true
  MakeInternals = false
  MapMode = 5
  Placement = pos=(0,4.8e-15,10.8542) rot=(1,0,0;3.14159rad)
  sketch-geometry (9):
    g0: Circle [constr] CenterX=44.0745 CenterY=2.5 CenterZ=0 NormalX=0 NormalY=0 NormalZ=1 AngleXU=0 Radius=1.4
    g1: Circle [constr] CenterX=44.0745 CenterY=2.5 CenterZ=0 NormalX=0 NormalY=0 NormalZ=1 AngleXU=0 Radius=1.9
    g2: ArcOfCircle CenterX=44.0745 CenterY=2.5 CenterZ=0 NormalX=0 NormalY=0 NormalZ=1 AngleXU=0 Radius=1.4 StartAngle=3.91679 EndAngle=8.64958
    g3: ArcOfCircle CenterX=44.0745 CenterY=2.5 CenterZ=0 NormalX=0 NormalY=0 NormalZ=1 AngleXU=0 Radius=1.9 StartAngle=4.15813 EndAngle=8.40824
    g4: LineSegment [constr] StartX=43.0745 StartY=4.11555 StartZ=0 EndX=43.0745 EndY=3.4798 EndZ=0
    g5: LineSegment [constr] StartX=43.0745 StartY=3.4798 StartZ=0 EndX=43.0745 EndY=1.5202 EndZ=0
    g6: LineSegment [constr] StartX=43.0745 StartY=1.5202 StartZ=0 EndX=43.0745 EndY=0.884451 EndZ=0
    g7: LineSegment StartX=43.0745 StartY=4.11555 StartZ=0 EndX=43.0745 EndY=3.4798 EndZ=0
    g8: LineSegment StartX=43.0745 StartY=1.5202 StartZ=0 EndX=43.0745 EndY=0.884451 EndZ=0
  constraints (22):
    c: Coincident(g0,g-3)
    c: Coincident(g1,g0)
    c: Radius(g1) = 1.9
    c: Radius(g0) = 1.4
    c: Tangent(g2,g0) = -1.5708
    c: PointOnObject(g2,g0)
    c: Tangent(g3,g1) = -1.5708
    c: PointOnObject(g3,g1)
    c: Coincident(g4,g3)
    c: Coincident(g4,g2)
    c: Coincident(g5,g2)
    c: Coincident(g5,g2)
    c: Coincident(g6,g2)
    c: Coincident(g6,g3)
    c: Vertical(g5)
    c: Vertical(g6)
    c: Vertical(g4)
    c: Coincident(g7,g3)
    c: Coincident(g7,g2)
    c: Coincident(g8,g2)
    c: Coincident(g8,g3)
    c: Tangent(g5,g-3)
FEATURE [PartDesign::Pocket] Pocket487
  BaseFeature = -> Pocket486
  Direction = (0,0,1)
  Length = 5
  Length2 = 5
  Placement = pos=(0,0,0) rot=(1,0,0;1.5708rad)
  Profile = -> Sketch1061
  ReferenceAxis = -> Sketch1061 [N_Axis]
  Refine = true
  Suppressed = false
  Type = 0
FEATURE [Sketcher::SketchObject] Sketch1062
  ArcFitTolerance = 1e-06
  AttachmentSupport = -> [Pocket487]
  ExternalGeometry = -> [Pocket487]
  FullyConstrained = true
  MakeInternals = false
  MapMode = 5
  Placement = pos=(0,5.7e-15,12.8542) rot=(0,0,1;3.14159rad)
  sketch-geometry (1):
    g0: Circle CenterX=-44.0745 CenterY=2.5 CenterZ=0 NormalX=0 NormalY=0 NormalZ=1 AngleXU=0 Radius=1.9
  constraints (2):
    c: Coincident(g0,g-3)
    c: Equal(g0,g-3)
FEATURE [PartDesign::Pocket] Pocket488
  BaseFeature = -> Pocket487
  Direction = (0,0,-1)
  Length = 1
  Length2 = 5
  Placement = pos=(0,0,0) rot=(1,0,0;1.5708rad)
  Profile = -> Sketch1062
  ReferenceAxis = -> Sketch1062 [N_Axis]
  Refine = true
  Suppressed = false
  Type = 0
FEATURE [PartDesign::Pocket] Pocket489
  BaseFeature = -> Pocket488
  Direction = (0,-1,0)
  Length = 0.1
  Length2 = 5
  Placement = pos=(0,0,0) rot=(1,0,0;1.5708rad)
  Profile = -> Pocket488 [Face5]
  Refine = true
  Suppressed = false
  Type = 0
FEATURE [PartDesign::Pocket] Pocket490
  BaseFeature = -> Pocket489
  Direction = (0,1,0)
  Length = 0.1
  Length2 = 5
  Placement = pos=(0,0,0) rot=(1,0,0;1.5708rad)
  Profile = -> Pocket489 [Face11]
  Refine = true
  Suppressed = false
  Type = 0
FEATURE [Sketcher::SketchObject] Sketch1063
  ArcFitTolerance = 1e-06
  AttachmentSupport = -> [Pocket490]
  ExternalGeometry = -> [Pocket490]
  FullyConstrained = true
  MakeInternals = false
  MapMode = 5
  Placement = pos=(46.5745,0,0) rot=(0.707107,0,0.707107;3.14159rad)
  sketch-geometry (4):
    g0: LineSegment StartX=10.8542 StartY=4 StartZ=0 EndX=10.8542 EndY=1 EndZ=0
    g1: LineSegment StartX=10.8542 StartY=1 StartZ=0 EndX=12.8542 EndY=1 EndZ=0
    g2: LineSegment StartX=12.8542 StartY=1 StartZ=0 EndX=12.8542 EndY=4 EndZ=0
    g3: LineSegment StartX=12.8542 StartY=4 StartZ=0 EndX=10.8542 EndY=4 EndZ=0
  constraints (12):
    c: Coincident(g0,g1)
    c: Coincident(g1,g2)
    c: Coincident(g2,g3)
    c: Coincident(g3,g0)
    c: Vertical(g0)
    c: Vertical(g2)
    c: Horizontal(g1)
    c: Horizontal(g3)
    c: PointOnObject(g0,g-3)
    c: PointOnObject(g1,g-4)
    c: DistanceY(g0,g-3) = 0.9
    c: DistanceY(g-3,g0) = 0.9
FEATURE [PartDesign::Pocket] Pocket491
  BaseFeature = -> Pocket490
  Direction = (-1,0,2e-16)
  Length = 0.2
  Length2 = 5
  Placement = pos=(0,0,0) rot=(1,0,0;1.5708rad)
  Profile = -> Sketch1063
  ReferenceAxis = -> Sketch1063 [N_Axis]
  Refine = true
  Suppressed = false
  Type = 0
FEATURE [PartDesign::Body] Body052  label="Spring_Stop2"
  AllowCompound = false
  Group = -> [Sketch1059,Pad690,Sketch1060,Pocket486,Sketch1061,Pocket487,Sketch1062,Pocket488,Pocket489,Pocket490,Sketch1063,Pocket491]
  Origin = -> Origin057
  Placement = pos=(-111,63.35,39.05) rot=(-0.71,0,0.71;3.14159rad)
  Tip = -> Pocket491
FEATURE [App::Link] Link001  label="Left_Fist001"
  LinkedObject = -> Body047
FEATURE [Part::Mirroring] Part__Mirroring  label="Right_Fist"
  Base = (0,0,0)
  Normal = (0,1,0)
  Placement = pos=(-106,58.85,-0.5) rot=(1,0,0;3.14159rad)
  Source = -> Link001
FEATURE [App::Part] Part003  label="Right_Arm"
  Group = -> [Body049,Body050,Body051,Body052,Link001,Part__Mirroring]
  Origin = -> Origin052
  Placement = pos=(0,23,-12.5) rot=(1,0,0;3.14159rad)
FEATURE [Part::Feature] Part__Feature  label="Devastator_Gun"
  Placement = pos=(-21,-9,-11) rot=(0,0,1;1.5708rad)
  shape: bbox 28.21 x 76.11 x 10.12 mm, 308 faces (baked)
FEATURE [Sketcher::SketchObject] Sketch1064
  ArcFitTolerance = 1e-06
  AttachmentOffset = pos=(-60,-44,0) rot=(0,0,1;0rad)
  AttachmentSupport = -> [XY_Plane058]
  FullyConstrained = true
  MakeInternals = false
  MapMode = 5
  Placement = pos=(-60,-44,0) rot=(0,0,1;0rad)
  sketch-geometry (1):
    g0: Circle CenterX=0 CenterY=0 CenterZ=0 NormalX=0 NormalY=0 NormalZ=1 AngleXU=0 Radius=4.8
  constraints (2):
    c: Coincident(g0,g-1)
    c: Diameter(g0) = 9.6
FEATURE [PartDesign::Pad] Pad691
  Direction = (0,0,1)
  Length = 2
  Length2 = 10
  Profile = -> Sketch1064
  ReferenceAxis = -> Sketch1064 [N_Axis]
  Refine = true
  Suppressed = false
  Type = 0
FEATURE [Sketcher::SketchObject] Sketch1065
  ArcFitTolerance = 1e-06
  AttachmentSupport = -> [Pad691]
  ExternalGeometry = -> [Pad691]
  FullyConstrained = true
  MakeInternals = false
  MapMode = 5
  Placement = pos=(0,0,2) rot=(0,0,1;0rad)
  sketch-geometry (1):
    g0: Circle CenterX=-60 CenterY=-44 CenterZ=0 NormalX=0 NormalY=0 NormalZ=1 AngleXU=0 Radius=2.5
  constraints (2):
    c: Coincident(g0,g-3)
    c: Diameter(g0) = 5
FEATURE [PartDesign::Pad] Pad692
  BaseFeature = -> Pad691
  Direction = (0,0,1)
  Length = 1
  Length2 = 10
  Profile = -> Sketch1065
  ReferenceAxis = -> Sketch1065 [N_Axis]
  Refine = true
  Suppressed = false
  Type = 0
FEATURE [Sketcher::SketchObject] Sketch1066
  ArcFitTolerance = 1e-06
  AttachmentSupport = -> [Pad692]
  ExternalGeometry = -> [Pad692]
  FullyConstrained = true
  MakeInternals = false
  MapMode = 5
  Placement = pos=(0,0,3) rot=(0,0,1;0rad)
  sketch-geometry (1):
    g0: Circle CenterX=-60 CenterY=-44 CenterZ=0 NormalX=0 NormalY=0 NormalZ=1 AngleXU=0 Radius=4.8
  constraints (2):
    c: Coincident(g0,g-4)
    c: Equal(g0,g-4)
FEATURE [PartDesign::Pad] Pad693
  BaseFeature = -> Pad692
  Direction = (0,0,1)
  Length = 2
  Length2 = 10
  Profile = -> Sketch1066
  ReferenceAxis = -> Sketch1066 [N_Axis]
  Refine = true
  Suppressed = false
  Type = 0
FEATURE [Sketcher::SketchObject] Sketch1067
  ArcFitTolerance = 1e-06
  AttachmentSupport = -> [Pad693]
  ExternalGeometry = -> [Pad693]
  FullyConstrained = true
  MakeInternals = false
  MapMode = 5
  Placement = pos=(0,0,0) rot=(1,0,0;3.14159rad)
  sketch-geometry (1):
    g0: Circle CenterX=-60 CenterY=44 CenterZ=0 NormalX=0 NormalY=0 NormalZ=1 AngleXU=0 Radius=1.92
  constraints (2):
    c: Coincident(g0,g-3)
    c: Radius(g0) = 1.92
FEATURE [PartDesign::Pad] Pad694
  BaseFeature = -> Pad693
  Direction = (0,0,-1)
  Length = 11
  Length2 = 10
  Profile = -> Sketch1067
  ReferenceAxis = -> Sketch1067 [N_Axis]
  Refine = true
  Suppressed = false
  Type = 0
FEATURE [Sketcher::SketchObject] Sketch1068
  ArcFitTolerance = 1e-06
  AttachmentSupport = -> [Pad694]
  ExternalGeometry = -> [Pad694]
  FullyConstrained = true
  MakeInternals = false
  MapMode = 5
  Placement = pos=(0,0,-11) rot=(1,0,0;3.14159rad)
  sketch-geometry (1):
    g0: Circle CenterX=-60 CenterY=44 CenterZ=0 NormalX=0 NormalY=0 NormalZ=1 AngleXU=0 Radius=1
  constraints (2):
    c: Coincident(g0,g-3)
    c: Radius(g0) = 1
FEATURE [PartDesign::Pad] Pad695
  BaseFeature = -> Pad694
  Direction = (0,0,-1)
  Length = 1.5
  Length2 = 10
  Profile = -> Sketch1068
  ReferenceAxis = -> Sketch1068 [N_Axis]
  Refine = true
  Suppressed = false
  Type = 0
FEATURE [Sketcher::SketchObject] Sketch1069
  ArcFitTolerance = 1e-06
  AttachmentSupport = -> [Pad695]
  ExternalGeometry = -> [Pad695]
  FullyConstrained = true
  MakeInternals = false
  MapMode = 5
  Placement = pos=(0,0,-12.5) rot=(1,0,0;3.14159rad)
  sketch-geometry (1):
    g0: Circle CenterX=-60 CenterY=44 CenterZ=0 NormalX=0 NormalY=0 NormalZ=1 AngleXU=0 Radius=1.92
  constraints (2):
    c: Coincident(g0,g-4)
    c: Equal(g0,g-4)
FEATURE [PartDesign::Pad] Pad696
  BaseFeature = -> Pad695
  Direction = (0,0,-1)
  Length = 2.5
  Length2 = 10
  Profile = -> Sketch1069
  ReferenceAxis = -> Sketch1069 [N_Axis]
  Refine = true
  Suppressed = false
  Type = 0
FEATURE [PartDesign::Chamfer] Chamfer052
  Angle = 45
  Base = -> Pad696 [Edge18]
  BaseFeature = -> Pad696
  ChamferType = 0
  FlipDirection = false
  Refine = true
  Size = 1
  Size2 = 1
  SupportTransform = false
  Suppressed = false
  UseAllEdges = false
FEATURE [PartDesign::Chamfer] Chamfer053
  Angle = 45
  Base = -> Chamfer052 [Edge9]
  BaseFeature = -> Chamfer052
  ChamferType = 0
  FlipDirection = false
  Refine = true
  Size = 0.9
  Size2 = 1
  SupportTransform = false
  Suppressed = false
  UseAllEdges = false
FEATURE [Sketcher::SketchObject] Sketch1070
  ArcFitTolerance = 1e-06
  AttachmentOffset = pos=(0,0,45) rot=(0,0,1;0rad)
  AttachmentSupport = -> [XZ_Plane058]
  ExternalGeometry = -> [Chamfer053]
  FullyConstrained = true
  MakeInternals = false
  MapMode = 5
  Placement = pos=(0,-45,1e-14) rot=(1,0,0;1.5708rad)
  sketch-geometry (8):
    g0: LineSegment StartX=-53 StartY=5 StartZ=0 EndX=-58.2 EndY=5 EndZ=0
    g1: LineSegment StartX=-58.2 StartY=5 StartZ=0 EndX=-58.2 EndY=-9.8e-15 EndZ=0
    g2: LineSegment StartX=-58.2 StartY=-9.8e-15 StartZ=0 EndX=-53 EndY=-9.8e-15 EndZ=0
    g3: LineSegment StartX=-53 StartY=-9.8e-15 StartZ=0 EndX=-53 EndY=5 EndZ=0
    g4: LineSegment StartX=-67 StartY=5 StartZ=0 EndX=-67 EndY=-9.8e-15 EndZ=0
    g5: LineSegment StartX=-67 StartY=-9.8e-15 StartZ=0 EndX=-61.8 EndY=-9.8e-15 EndZ=0
    g6: LineSegment StartX=-61.8 StartY=-9.8e-15 StartZ=0 EndX=-61.8 EndY=5 EndZ=0
    g7: LineSegment StartX=-61.8 StartY=5 StartZ=0 EndX=-67 EndY=5 EndZ=0
  constraints (24):
    c: Coincident(g0,g1)
    c: Coincident(g1,g2)
    c: Coincident(g2,g3)
    c: Coincident(g3,g0)
    c: Horizontal(g0)
    c: Horizontal(g2)
    c: Vertical(g1)
    c: Vertical(g3)
    c: PointOnObject(g1,g-4)
    c: PointOnObject(g-3,g0)
    c: DistanceX(g0,g-3) = 3
    c: DistanceX(g-3,g0) = 2.2
    c: Coincident(g4,g5)
    c: Coincident(g5,g6)
    c: Coincident(g6,g7)
    c: Coincident(g7,g4)
    c: Vertical(g4)
    c: Vertical(g6)
    c: Horizontal(g5)
    c: Horizontal(g7)
    c: PointOnObject(g5,g-4)
    c: PointOnObject(g-3,g7)
    c: DistanceX(g-3,g6) = 3
    c: DistanceX(g4,g-3) = 2.2
FEATURE [PartDesign::Pad] Pad697
  BaseFeature = -> Chamfer053
  Direction = (0,-1,2e-16)
  Length = 2
  Length2 = 10
  Profile = -> Sketch1070
  ReferenceAxis = -> Sketch1070 [N_Axis]
  Refine = true
  Reversed = true
  Suppressed = false
  Type = 0
FEATURE [Sketcher::SketchObject] Sketch1071
  ArcFitTolerance = 1e-06
  AttachmentSupport = -> [Pad697]
  ExternalGeometry = -> [Pad697]
  FullyConstrained = true
  MakeInternals = false
  MapMode = 5
  Placement = pos=(0,0,5) rot=(0,0,1;0rad)
  sketch-geometry (4):
    g0: LineSegment StartX=-61 StartY=-37 StartZ=0 EndX=-61 EndY=-51 EndZ=0
    g1: LineSegment StartX=-61 StartY=-51 StartZ=0 EndX=-59 EndY=-51 EndZ=0
    g2: LineSegment StartX=-59 StartY=-51 StartZ=0 EndX=-59 EndY=-37 EndZ=0
    g3: LineSegment StartX=-59 StartY=-37 StartZ=0 EndX=-61 EndY=-37 EndZ=0
  constraints (13):
    c: Coincident(g0,g1)
    c: Coincident(g1,g2)
    c: Coincident(g2,g3)
    c: Coincident(g3,g0)
    c: Vertical(g0)
    c: Vertical(g2)
    c: Horizontal(g1)
    c: Horizontal(g3)
    c: DistanceX(g3,g3) = 2
    c: DistanceX(g-5,g-6) = 14
    c: DistanceY(g0,g0) = 14
    c: DistanceY(g-4,g0) = 7
    c: DistanceX(g0,g-4) = 1
FEATURE [PartDesign::Pad] Pad698
  BaseFeature = -> Pad697
  Direction = (0,0,1)
  Length = 5
  Length2 = 10
  Profile = -> Sketch1071
  ReferenceAxis = -> Sketch1071 [N_Axis]
  Refine = true
  Reversed = true
  Suppressed = false
  Type = 0
FEATURE [Sketcher::SketchObject] Sketch1072
  ArcFitTolerance = 1e-06
  AttachmentSupport = -> [Pad698]
  ExternalGeometry = -> [Pad698]
  FullyConstrained = true
  MakeInternals = false
  MapMode = 5
  Placement = pos=(-61,0,0) rot=(0.57735,-0.57735,-0.57735;2.0944rad)
  sketch-geometry (6):
    g0: LineSegment StartX=51 StartY=5 StartZ=0 EndX=51 EndY=0 EndZ=0
    g1: LineSegment StartX=37 StartY=5 StartZ=0 EndX=37 EndY=0 EndZ=0
    g2: LineSegment StartX=51 StartY=5 StartZ=0 EndX=50.5 EndY=5 EndZ=0
    g3: LineSegment StartX=50.5 StartY=5 StartZ=0 EndX=51 EndY=0 EndZ=0
    g4: LineSegment StartX=37 StartY=5 StartZ=0 EndX=37.5 EndY=5 EndZ=0
    g5: LineSegment StartX=37 StartY=0 StartZ=0 EndX=37.5 EndY=5 EndZ=0
  constraints (14):
    c: Coincident(g0,g-5)
    c: Coincident(g0,g-6)
    c: Coincident(g1,g-3)
    c: Coincident(g1,g-4)
    c: Coincident(g2,g0)
    c: Horizontal(g2)
    c: Coincident(g3,g2)
    c: Coincident(g3,g0)
    c: DistanceX(g2,g2) = 0.5
    c: Coincident(g4,g1)
    c: Horizontal(g4)
    c: Coincident(g5,g1)
    c: Coincident(g5,g4)
    c: DistanceX(g4,g4) = 0.5
FEATURE [PartDesign::Pocket] Pocket492
  BaseFeature = -> Pad698
  Direction = (1,0,0)
  Length = 5
  Length2 = 5
  Profile = -> Sketch1072
  ReferenceAxis = -> Sketch1072 [N_Axis]
  Refine = true
  Suppressed = false
  Type = 1
FEATURE [Sketcher::SketchObject] Sketch1073
  ArcFitTolerance = 1e-06
  AttachmentSupport = -> [Pocket492]
  ExternalGeometry = -> [Pocket492]
  FullyConstrained = true
  MakeInternals = false
  MapMode = 5
  Placement = pos=(0,-45,0) rot=(1,0,0;1.5708rad)
  sketch-geometry (6):
    g0: LineSegment StartX=-67 StartY=0 StartZ=0 EndX=-66.5 EndY=5 EndZ=0
    g1: LineSegment StartX=-66.5 StartY=5 StartZ=0 EndX=-67 EndY=5 EndZ=0
    g2: LineSegment StartX=-67 StartY=5 StartZ=0 EndX=-67 EndY=0 EndZ=0
    g3: LineSegment StartX=-53 StartY=0 StartZ=0 EndX=-53.5 EndY=5 EndZ=0
    g4: LineSegment StartX=-53.5 StartY=5 StartZ=0 EndX=-53 EndY=5 EndZ=0
    g5: LineSegment StartX=-53 StartY=5 StartZ=0 EndX=-53 EndY=0 EndZ=0
  constraints (14):
    c: Coincident(g0,g-4)
    c: PointOnObject(g0,g-3)
    c: Coincident(g1,g0)
    c: Coincident(g1,g-4)
    c: Coincident(g2,g1)
    c: Coincident(g2,g0)
    c: Coincident(g3,g-6)
    c: PointOnObject(g3,g-5)
    c: Coincident(g4,g3)
    c: Coincident(g4,g-6)
    c: Coincident(g5,g4)
    c: Coincident(g5,g3)
    c: DistanceX(g1,g1) = 0.5
    c: DistanceX(g4,g4) = 0.5
FEATURE [PartDesign::Pocket] Pocket493
  BaseFeature = -> Pocket492
  Direction = (0,1,-2e-16)
  Length = 5
  Length2 = 5
  Profile = -> Sketch1073
  ReferenceAxis = -> Sketch1073 [N_Axis]
  Refine = true
  Suppressed = false
  Type = 1
FEATURE [Sketcher::SketchObject] Sketch1074
  ArcFitTolerance = 1e-06
  AttachmentSupport = -> [Pocket493]
  ExternalGeometry = -> [Pocket493]
  FullyConstrained = true
  MakeInternals = false
  MapMode = 5
  Placement = pos=(0,0,5) rot=(0,0,1;0rad)
  sketch-geometry (1):
    g0: Circle CenterX=-60 CenterY=-44 CenterZ=0 NormalX=0 NormalY=0 NormalZ=1 AngleXU=0 Radius=2.5
  constraints (2):
    c: Coincident(g0,g-4)
    c: Equal(g0,g-4)
FEATURE [PartDesign::Pad] Pad699
  BaseFeature = -> Pocket493
  Direction = (0,0,1)
  Length = 1
  Length2 = 10
  Profile = -> Sketch1074
  ReferenceAxis = -> Sketch1074 [N_Axis]
  Refine = true
  Suppressed = false
  Type = 0
FEATURE [Sketcher::SketchObject] Sketch1075
  ArcFitTolerance = 1e-06
  AttachmentSupport = -> [Pad699]
  ExternalGeometry = -> [Pad699]
  FullyConstrained = true
  MakeInternals = false
  MapMode = 5
  Placement = pos=(0,0,6) rot=(0,0,1;0rad)
  sketch-geometry (1):
    g0: Circle CenterX=-60 CenterY=-44 CenterZ=0 NormalX=0 NormalY=0 NormalZ=1 AngleXU=0 Radius=4.05
  constraints (2):
    c: Coincident(g0,g-3)
    c: Diameter(g0) = 8.1
FEATURE [PartDesign::Pad] Pad700
  BaseFeature = -> Pad699
  Direction = (0,0,1)
  Length = 3
  Length2 = 10
  Profile = -> Sketch1075
  ReferenceAxis = -> Sketch1075 [N_Axis]
  Refine = true
  Suppressed = false
  Type = 0
FEATURE [Sketcher::SketchObject] Sketch1076
  ArcFitTolerance = 1e-06
  AttachmentSupport = -> [Pad700]
  ExternalGeometry = -> [Pad700]
  FullyConstrained = true
  MakeInternals = false
  MapMode = 5
  Placement = pos=(-59,0,0) rot=(0.57735,0.57735,0.57735;2.0944rad)
  sketch-geometry (9):
    g0: LineSegment StartX=-48.55 StartY=8.33333 StartZ=0 EndX=-48.55 EndY=7.83333 EndZ=0
    g1: LineSegment StartX=-48.55 StartY=7.83333 StartZ=0 EndX=-47.55 EndY=7.83333 EndZ=0
    g2: LineSegment StartX=-47.55 StartY=7.83333 StartZ=0 EndX=-47.55 EndY=8.33333 EndZ=0
    g3: LineSegment StartX=-47.55 StartY=8.33333 StartZ=0 EndX=-48.55 EndY=8.33333 EndZ=0
    g4: LineSegment StartX=-48.55 StartY=7.16667 StartZ=0 EndX=-48.55 EndY=6.66667 EndZ=0
    g5: LineSegment StartX=-48.55 StartY=6.66667 StartZ=0 EndX=-47.55 EndY=6.66667 EndZ=0
    g6: LineSegment StartX=-47.55 StartY=6.66667 StartZ=0 EndX=-47.55 EndY=7.16667 EndZ=0
    g7: LineSegment StartX=-47.55 StartY=7.16667 StartZ=0 EndX=-48.55 EndY=7.16667 EndZ=0
    g8: LineSegment [constr] StartX=-48.55 StartY=7.83333 StartZ=0 EndX=-48.55 EndY=7.16667 EndZ=0
  constraints (28):
    c: Coincident(g0,g1)
    c: Coincident(g1,g2)
    c: Coincident(g2,g3)
    c: Coincident(g3,g0)
    c: Vertical(g0)
    c: Vertical(g2)
    c: Horizontal(g1)
    c: Horizontal(g3)
    c: Coincident(g4,g5)
    c: Coincident(g5,g6)
    c: Coincident(g6,g7)
    c: Coincident(g7,g4)
    c: Vertical(g4)
    c: Vertical(g6)
    c: Horizontal(g5)
    c: Horizontal(g7)
    c: DistanceY(g-3,g-3) = 3
    c: DistanceY(g0,g0) = 0.5
    c: DistanceY(g4,g4) = 0.5
    c: DistanceX(g0,g-4) = 0.5
    c: Coincident(g8,g0)
    c: Coincident(g8,g4)
    c: Vertical(g8)
    c: DistanceX(g1,g1) = 1
    c: DistanceX(g5,g5) = 1
    c: DistanceY(g4,g0) = 0.666667
    c: DistanceY(g0,g-4) = 0.666667
    c: DistanceY(g-5,g4) = 0.666666
FEATURE [PartDesign::Groove] Groove002
  Angle = 360
  Angle2 = 60
  Axis = (0,0,1)
  Base = (-60,-44,9)
  BaseFeature = -> Pad700
  Profile = -> Sketch1076
  ReferenceAxis = -> Pad700 [Edge115]
  Refine = true
  Reversed = true
  Suppressed = false
  Type = 0
FEATURE [Sketcher::SketchObject] Sketch1077
  ArcFitTolerance = 1e-06
  AttachmentSupport = -> [Groove002]
  ExternalGeometry = -> [Groove002]
  FullyConstrained = true
  MakeInternals = false
  MapMode = 5
  Placement = pos=(-59,0,0) rot=(0.57735,0.57735,0.57735;2.0944rad)
  sketch-geometry (7):
    g0: LineSegment StartX=-48.05 StartY=9 StartZ=0 EndX=-45.125 EndY=22.4 EndZ=0
    g1: LineSegment StartX=-39.95 StartY=9 StartZ=0 EndX=-42.875 EndY=22.4 EndZ=0
    g2: LineSegment StartX=-42.875 StartY=22.4 StartZ=0 EndX=-45.125 EndY=22.4 EndZ=0
    g3: LineSegment StartX=-44 StartY=9 StartZ=0 EndX=-44 EndY=22.4 EndZ=0
    g4: LineSegment StartX=-45.5179 StartY=20.6 StartZ=0 EndX=-42.4821 EndY=20.6 EndZ=0
    g5: LineSegment StartX=-47.55 StartY=9 StartZ=0 EndX=-45.0179 EndY=20.6 EndZ=0
    g6: LineSegment StartX=-42.9821 StartY=20.6 StartZ=0 EndX=-40.45 EndY=9 EndZ=0
  constraints (23):
    c: Coincident(g0,g-3)
    c: Coincident(g1,g-3)
    c: Coincident(g2,g1)
    c: Coincident(g2,g0)
    c: Horizontal(g2)
    c: DistanceY(g0,g0) = 13.4
    c: DistanceX(g2,g2) = 2.25
    c: Symmetric(g-3,g-3,g3)
    c: Symmetric(g2,g2,g3)
    c: Vertical(g3)
    c: PointOnObject(g4,g0)
    c: PointOnObject(g4,g1)
    c: Horizontal(g4)
    c: DistanceY(g0,g4) = 11.6
    c: DistanceY(g4,g1) = 1.8
    c: PointOnObject(g5,g-3)
    c: PointOnObject(g5,g4)
    c: PointOnObject(g6,g4)
    c: PointOnObject(g6,g-3)
    c: Parallel(g6,g1)
    c: Parallel(g5,g0)
    c: DistanceX(g6,g1) = 0.5
    c: DistanceX(g0,g5) = 0.5
FEATURE [Sketcher::SketchObject] Sketch1078
  ArcFitTolerance = 1e-06
  AttachmentSupport = -> [Groove002]
  ExternalGeometry = -> [Groove002,Sketch1077]
  FullyConstrained = true
  MakeInternals = false
  MapMode = 5
  Placement = pos=(0,0,9) rot=(0,0,1;0rad)
  sketch-geometry (1):
    g0: Circle CenterX=-60 CenterY=-44 CenterZ=0 NormalX=0 NormalY=0 NormalZ=1 AngleXU=0 Radius=3.68816
  constraints (2):
    c: Coincident(g0,g-3)
    c: PointOnObject(g-4,g0)
FEATURE [PartDesign::Pad] Pad701
  BaseFeature = -> Groove002
  Direction = (0,0,1)
  Length = 1
  Length2 = 10
  Profile = -> Sketch1078
  ReferenceAxis = -> Sketch1078 [N_Axis]
  Refine = true
  Suppressed = false
  Type = 0
FEATURE [Sketcher::SketchObject] Sketch1079
  ArcFitTolerance = 1e-06
  AttachmentSupport = -> [Pad701]
  ExternalGeometry = -> [Pad701,Sketch1077]
  FullyConstrained = false
  MakeInternals = false
  MapMode = 5
  Placement = pos=(0,0,10) rot=(0,0,1;0rad)
  sketch-geometry (1):
    g0: Circle CenterX=-60 CenterY=-44 CenterZ=0 NormalX=0 NormalY=0 NormalZ=1 AngleXU=0 Radius=3.95
  constraints (1):
    c: Radius(g0) = 3.95
FEATURE [PartDesign::Pad] Pad702
  BaseFeature = -> Pad701
  Direction = (0,0,1)
  Length = 1.5
  Length2 = 10
  Profile = -> Sketch1079
  ReferenceAxis = -> Sketch1079 [N_Axis]
  Refine = true
  Suppressed = false
  Type = 0
FEATURE [Sketcher::SketchObject] Sketch1080
  ArcFitTolerance = 1e-06
  AttachmentSupport = -> [Pad702]
  ExternalGeometry = -> [Pad702,Sketch1077]
  FullyConstrained = true
  MakeInternals = false
  MapMode = 5
  Placement = pos=(0,0,11.5) rot=(0,0,1;0rad)
  sketch-geometry (1):
    g0: Circle CenterX=-60 CenterY=-44 CenterZ=0 NormalX=0 NormalY=0 NormalZ=1 AngleXU=0 Radius=3.17
  constraints (2):
    c: Coincident(g0,g-3)
    c: Radius(g0) = 3.17
FEATURE [PartDesign::Pad] Pad703
  BaseFeature = -> Pad702
  Direction = (0,0,1)
  Length = 1
  Length2 = 10
  Profile = -> Sketch1080
  ReferenceAxis = -> Sketch1080 [N_Axis]
  Refine = true
  Suppressed = false
  Type = 0
FEATURE [Sketcher::SketchObject] Sketch1081
  ArcFitTolerance = 1e-06
  AttachmentSupport = -> [Pad703]
  ExternalGeometry = -> [Pad703]
  FullyConstrained = true
  MakeInternals = false
  MapMode = 5
  Placement = pos=(0,0,12.5) rot=(0,0,1;0rad)
  sketch-geometry (1):
    g0: Circle CenterX=-60 CenterY=-44 CenterZ=0 NormalX=0 NormalY=0 NormalZ=1 AngleXU=0 Radius=3.4
  constraints (2):
    c: Coincident(g0,g-3)
    c: Radius(g0) = 3.4
FEATURE [PartDesign::Pad] Pad704
  BaseFeature = -> Pad703
  Direction = (0,0,1)
  Length = 1.5
  Length2 = 10
  Profile = -> Sketch1081
  ReferenceAxis = -> Sketch1081 [N_Axis]
  Refine = true
  Suppressed = false
  Type = 0
FEATURE [Sketcher::SketchObject] Sketch1082
  ArcFitTolerance = 1e-06
  AttachmentSupport = -> [Pad704]
  ExternalGeometry = -> [Pad704]
  FullyConstrained = true
  MakeInternals = false
  MapMode = 5
  Placement = pos=(0,0,14) rot=(0,0,1;0rad)
  sketch-geometry (1):
    g0: Circle CenterX=-60 CenterY=-44 CenterZ=0 NormalX=0 NormalY=0 NormalZ=1 AngleXU=0 Radius=2.65
  constraints (2):
    c: Coincident(g0,g-3)
    c: Radius(g0) = 2.65
FEATURE [PartDesign::Pad] Pad705
  BaseFeature = -> Pad704
  Direction = (0,0,1)
  Length = 1
  Length2 = 10
  Profile = -> Sketch1082
  ReferenceAxis = -> Sketch1082 [N_Axis]
  Refine = true
  Suppressed = false
  Type = 0
FEATURE [Sketcher::SketchObject] Sketch1083
  ArcFitTolerance = 1e-06
  AttachmentSupport = -> [Pad705]
  ExternalGeometry = -> [Pad705]
  FullyConstrained = true
  MakeInternals = false
  MapMode = 5
  Placement = pos=(0,0,15) rot=(0,0,1;0rad)
  sketch-geometry (1):
    g0: Circle CenterX=-60 CenterY=-44 CenterZ=0 NormalX=0 NormalY=0 NormalZ=1 AngleXU=0 Radius=2.93
  constraints (2):
    c: Coincident(g0,g-3)
    c: Radius(g0) = 2.93
FEATURE [PartDesign::Pad] Pad706
  BaseFeature = -> Pad705
  Direction = (0,0,1)
  Length = 1.5
  Length2 = 10
  Profile = -> Sketch1083
  ReferenceAxis = -> Sketch1083 [N_Axis]
  Refine = true
  Suppressed = false
  Type = 0
FEATURE [Sketcher::SketchObject] Sketch1084
  ArcFitTolerance = 1e-06
  AttachmentSupport = -> [Pad706]
  ExternalGeometry = -> [Pad706]
  FullyConstrained = true
  MakeInternals = false
  MapMode = 5
  Placement = pos=(0,0,16.5) rot=(0,0,1;0rad)
  sketch-geometry (1):
    g0: Circle CenterX=-60 CenterY=-44 CenterZ=0 NormalX=0 NormalY=0 NormalZ=1 AngleXU=0 Radius=2.15
  constraints (2):
    c: Coincident(g0,g-3)
    c: Radius(g0) = 2.15
FEATURE [PartDesign::Pad] Pad707
  BaseFeature = -> Pad706
  Direction = (0,0,1)
  Length = 1
  Length2 = 10
  Profile = -> Sketch1084
  ReferenceAxis = -> Sketch1084 [N_Axis]
  Refine = true
  Suppressed = false
  Type = 0
FEATURE [Sketcher::SketchObject] Sketch1085
  ArcFitTolerance = 1e-06
  AttachmentSupport = -> [Pad707]
  ExternalGeometry = -> [Pad707]
  FullyConstrained = true
  MakeInternals = false
  MapMode = 5
  Placement = pos=(0,0,17.5) rot=(0,0,1;0rad)
  sketch-geometry (1):
    g0: Circle CenterX=-60 CenterY=-44 CenterZ=0 NormalX=0 NormalY=0 NormalZ=1 AngleXU=0 Radius=2.4
  constraints (2):
    c: Coincident(g0,g-3)
    c: Radius(g0) = 2.4
FEATURE [PartDesign::Pad] Pad708
  BaseFeature = -> Pad707
  Direction = (0,0,1)
  Length = 1.5
  Length2 = 10
  Profile = -> Sketch1085
  ReferenceAxis = -> Sketch1085 [N_Axis]
  Refine = true
  Suppressed = false
  Type = 0
FEATURE [Sketcher::SketchObject] Sketch1086
  ArcFitTolerance = 1e-06
  AttachmentSupport = -> [Pad708]
  ExternalGeometry = -> [Pad708]
  FullyConstrained = false
  MakeInternals = false
  MapMode = 5
  Placement = pos=(0,0,19) rot=(0,0,1;0rad)
  sketch-geometry (1):
    g0: Circle CenterX=-60 CenterY=-44 CenterZ=0 NormalX=0 NormalY=0 NormalZ=1 AngleXU=0 Radius=1.69279
  constraints (1):
    c: Coincident(g0,g-3)
FEATURE [PartDesign::Pad] Pad709
  BaseFeature = -> Pad708
  Direction = (0,0,1)
  Length = 1
  Length2 = 10
  Profile = -> Sketch1086
  ReferenceAxis = -> Sketch1086 [N_Axis]
  Refine = true
  Suppressed = false
  Type = 0
FEATURE [Sketcher::SketchObject] Sketch1087
  ArcFitTolerance = 1e-06
  AttachmentSupport = -> [Pad709]
  ExternalGeometry = -> [Pad709]
  FullyConstrained = false
  MakeInternals = false
  MapMode = 5
  Placement = pos=(0,0,20) rot=(0,0,1;0rad)
  sketch-geometry (1):
    g0: Circle CenterX=-60 CenterY=-44 CenterZ=0 NormalX=0 NormalY=0 NormalZ=1 AngleXU=0 Radius=1.93303
  constraints (1):
    c: Coincident(g0,g-3)
FEATURE [PartDesign::Pad] Pad710
  BaseFeature = -> Pad709
  Direction = (0,0,1)
  Length = 1.5
  Length2 = 10
  Profile = -> Sketch1087
  ReferenceAxis = -> Sketch1087 [N_Axis]
  Refine = true
  Suppressed = false
  Type = 0
FEATURE [Sketcher::SketchObject] Sketch1088
  ArcFitTolerance = 1e-06
  AttachmentSupport = -> [Pad710]
  ExternalGeometry = -> [Pad710]
  FullyConstrained = true
  MakeInternals = false
  MapMode = 5
  Placement = pos=(0,0,21.5) rot=(0,0,1;0rad)
  sketch-geometry (1):
    g0: Circle CenterX=-60 CenterY=-44 CenterZ=0 NormalX=0 NormalY=0 NormalZ=1 AngleXU=0 Radius=1.1
  constraints (2):
    c: Coincident(g0,g-3)
    c: Diameter(g0) = 2.2
FEATURE [PartDesign::Pad] Pad711
  BaseFeature = -> Pad710
  Direction = (0,0,1)
  Length = 1.8
  Length2 = 10
  Profile = -> Sketch1088
  ReferenceAxis = -> Sketch1088 [N_Axis]
  Refine = true
  Suppressed = false
  Type = 0
FEATURE [PartDesign::Fillet] Fillet025
  Base = -> Pad711 [Edge168]
  BaseFeature = -> Pad711
  Radius = 1
  Refine = true
  SupportTransform = false
  Suppressed = false
  UseAllEdges = false
FEATURE [PartDesign::Body] Body053  label="Drill_Fist1"
  AllowCompound = false
  Group = -> [Sketch1064,Pad691,Sketch1065,Pad692,Sketch1066,Pad693,Sketch1067,Pad694,Sketch1068,Pad695,Sketch1069,Pad696,Chamfer052,Chamfer053,Sketch1070,Pad697,Sketch1071,Pad698,Sketch1072,Pocket492,Sketch1073,Pocket493,Sketch1074,Pad699,Sketch1075,Pad700,Sketch1076,Groove002,Sketch1077,Sketch1078,Pad701,Sketch1079,Pad702,Sketch1080,Pad703,Sketch1081,Pad704,Sketch1082,Pad705,Sketch1083,Pad706,Sketch1084,+10 more]
  Origin = -> Origin058
  Placement = pos=(-57,2,-66) rot=(0,1,0;1.5708rad)
  Tip = -> Fillet025
FEATURE [App::Link] Link002  label="Drill_Fist2"
  LinkPlacement = pos=(-57,132,-66) rot=(0,1,0;1.5708rad)
  LinkedObject = -> Body053
  Placement = pos=(-57,132,-66) rot=(0,1,0;1.5708rad)
FEATURE [Sketcher::SketchObject] Sketch1089
  ArcFitTolerance = 1e-06
  AttachmentSupport = -> [Pocket304]
  ExternalGeometry = -> [Pocket304]
  FullyConstrained = true
  MakeInternals = false
  MapMode = 5
  Placement = pos=(0,0,-9.1) rot=(1,0,0;3.14159rad)
  sketch-geometry (5):
    g0: ArcOfCircle CenterX=13 CenterY=-3 CenterZ=0 NormalX=0 NormalY=0 NormalZ=1 AngleXU=0 Radius=2.5 StartAngle=4.09366 EndAngle=5.33112
    g1: ArcOfCircle CenterX=12.5 CenterY=-9.8 CenterZ=0 NormalX=0 NormalY=0 NormalZ=1 AngleXU=0 Radius=2.4 StartAngle=0.622368 EndAngle=1.97777
    g2: LineSegment [constr] StartX=14.45 StartY=-5.03654 StartZ=0 EndX=11.55 EndY=-5.03654 EndZ=0
    g3: LineSegment StartX=11.55 StartY=-5.03654 StartZ=0 EndX=11.55 EndY=-7.59603 EndZ=0
    g4: LineSegment StartX=14.45 StartY=-8.40089 StartZ=0 EndX=14.45 EndY=-5.03654 EndZ=0
  constraints (12):
    c: Coincident(g0,g-6)
    c: Coincident(g1,g-6)
    c: Coincident(g2,g0)
    c: Coincident(g2,g0)
    c: Horizontal(g2)
    c: Tangent(g0,g-4) = -1.5708
    c: Tangent(g1,g-5) = -1.5708
    c: Coincident(g3,g0)
    c: Coincident(g3,g1)
    c: Vertical(g3)
    c: Coincident(g4,g1)
    c: Coincident(g4,g0)
FEATURE [PartDesign::Pad] Pad712
  BaseFeature = -> Pocket304
  Direction = (0,0,-1)
  Length = 12
  Length2 = 10
  Profile = -> Sketch1089
  ReferenceAxis = -> Sketch1089 [N_Axis]
  Refine = true
  Reversed = true
  Suppressed = false
  Type = 0
FEATURE [Sketcher::SketchObject] Sketch1090
  ArcFitTolerance = 1e-06
  AttachmentSupport = -> [Pad712]
  ExternalGeometry = -> [Pad712]
  FullyConstrained = true
  MakeInternals = false
  MapMode = 5
  Placement = pos=(-1.04054,4e-16,1.80228) rot=(0,-1,0;0.523599rad)
  sketch-geometry (4):
    g0: LineSegment StartX=2.35622 StartY=0 StartZ=0 EndX=2.35622 EndY=-0.8 EndZ=0
    g1: LineSegment StartX=2.35622 StartY=-0.8 StartZ=0 EndX=3.39545 EndY=-0.8 EndZ=0
    g2: LineSegment StartX=3.39545 StartY=-0.8 StartZ=0 EndX=3.39545 EndY=0 EndZ=0
    g3: LineSegment StartX=3.39545 StartY=0 StartZ=0 EndX=2.35622 EndY=0 EndZ=0
  constraints (10):
    c: Coincident(g0,g1)
    c: Coincident(g1,g2)
    c: Coincident(g2,g3)
    c: Coincident(g3,g0)
    c: Vertical(g0)
    c: Vertical(g2)
    c: Horizontal(g1)
    c: Horizontal(g3)
    c: Coincident(g0,g-4)
    c: Coincident(g1,g-3)
FEATURE [PartDesign::Pocket] Pocket494
  BaseFeature = -> Pad712
  Direction = (0.5,0,-0.866025)
  Length = 5
  Length2 = 5
  Profile = -> Sketch1090
  ReferenceAxis = -> Sketch1090 [N_Axis]
  Refine = true
  Reversed = true
  Suppressed = false
  Type = 0
FEATURE [PartDesign::Pad] Pad713
  BaseFeature = -> Pocket494
  Direction = (0,0,-1)
  Length = 7.8
  Length2 = 10
  Profile = -> Pocket494 [Face9]
  Refine = true
  Suppressed = false
  Type = 0
FEATURE [PartDesign::Body] Body034  label="Chestplate"
  AllowCompound = false
  Group = -> [Sketch640,Pad454,Sketch641,Pad455,Sketch642,Pocket283,Sketch643,Pocket284,Chamfer018,Chamfer019,Sketch644,Pad456,Pad457,Sketch645,Pocket285,Sketch646,Pad458,Sketch647,Pocket286,Sketch648,Pad459,Sketch649,Pocket287,Sketch650,Pad460,Chamfer020,Sketch651,Pad461,Pad462,Sketch652,Pad463,Pocket288,Sketch653,Sketch654,AdditiveLoft004,Sketch655,Pad464,Sketch656,Pad465,Sketch657,Pad466,Sketch658,Pocket289,+84 more]
  Origin = -> Origin037
  Placement = pos=(-143,14,-4.4) rot=(0,0,1;1.5708rad)
  Tip = -> Pad713
FEATURE [PartDesign::Pad] Pad714
  BaseFeature = -> Chamfer
  Direction = (0,1,0)
  Length = 1.5
  Length2 = 10
  Placement = pos=(0,0,0) rot=(1,0,0;1.5708rad)
  Profile = -> Chamfer [Face152,Face137]
  Refine = true
  Suppressed = false
  Type = 0
FEATURE [PartDesign::Pocket] Pocket495
  BaseFeature = -> Chamfer009
  Direction = (0,0,-1)
  Length = 1.5
  Length2 = 5
  Profile = -> Chamfer009 [Face39]
  Refine = true
  Suppressed = false
  Type = 0
FEATURE [PartDesign::Body] Body  label="Leg_Cannon1"
  AllowCompound = false
  Group = -> [Binder,Sketch,Pad,Sketch539,Pad387,Sketch540,Pad388,Sketch541,Pocket,Pocket247,Sketch542,Pad389,Sketch543,Pad390,Sketch544,Pad391,Sketch545,Pad392,Sketch546,Pocket248,Sketch547,Pad393,Sketch548,Pad394,Sketch549,Pocket249,Sketch550,Pocket250,Sketch551,Pad395,Sketch552,Pocket251,Sketch553,Pocket252,Sketch554,Pad396,Sketch555,Pad397,Sketch556,Pad398,Sketch557,Pad399,Sketch558,Pad400,Sketch559,Pad401,+24 more]
  Origin = -> Origin
  Placement = pos=(0,0,3) rot=(0,0,1;0rad)
  Tip = -> Pocket495
FEATURE [PartDesign::Pad] Pad715
  BaseFeature = -> Pad714
  Direction = (0,-4e-16,-1)
  Length = 1
  Length2 = 10
  Placement = pos=(0,0,0) rot=(1,0,0;1.5708rad)
  Profile = -> Pad714 [Face63,Face67]
  Refine = true
  Suppressed = false
  Type = 0
FEATURE [Sketcher::SketchObject] Sketch1091
  ArcFitTolerance = 1e-06
  AttachmentSupport = -> [Pad715]
  ExternalGeometry = -> [Pad715]
  FullyConstrained = true
  MakeInternals = false
  MapMode = 5
  Placement = pos=(0,5e-16,0) rot=(-1,0,0;1.5708rad)
  sketch-geometry (4):
    g0: LineSegment StartX=17.55 StartY=11.8 StartZ=0 EndX=17.55 EndY=-3.2 EndZ=0
    g1: LineSegment StartX=17.55 StartY=-3.2 StartZ=0 EndX=19.35 EndY=-3.2 EndZ=0
    g2: LineSegment StartX=19.35 StartY=-3.2 StartZ=0 EndX=19.35 EndY=11.8 EndZ=0
    g3: LineSegment StartX=19.35 StartY=11.8 StartZ=0 EndX=17.55 EndY=11.8 EndZ=0
  constraints (14):
    c: DistanceX(g-3,g-3) = 1.8
    c: Coincident(g0,g1)
    c: Coincident(g1,g2)
    c: Coincident(g2,g3)
    c: Coincident(g3,g0)
    c: Vertical(g0)
    c: Vertical(g2)
    c: Horizontal(g1)
    c: Horizontal(g3)
    c: PointOnObject(g0,g-4)
    c: DistanceX(g3,g3) = 1.8
    c: DistanceX(g-5,g0) = 4.05
    c: DistanceX(g2,g-4) = 4.05
    c: DistanceY(g0,g0) = 15
FEATURE [PartDesign::Pad] Pad716
  BaseFeature = -> Pad715
  Direction = (0,1,2e-16)
  Length = 2.5
  Length2 = 10
  Placement = pos=(0,0,0) rot=(1,0,0;1.5708rad)
  Profile = -> Sketch1091
  ReferenceAxis = -> Sketch1091 [N_Axis]
  Refine = true
  Suppressed = false
  Type = 0
FEATURE [PartDesign::Body] Body031  label="Leg_Connector_Body"
  AllowCompound = false
  Group = -> [Sketch508,Pad351,Sketch509,Pad352,Sketch510,Pocket235,Sketch511,Pad353,Sketch512,Pad354,Sketch513,Pad355,Sketch514,Pad356,Sketch515,Pad357,Sketch516,Pad358,Sketch517,Pocket236,Sketch518,Pad359,Sketch519,Pad360,Sketch520,Pad361,Sketch521,Pad362,Sketch522,Pad363,Sketch523,Pad364,Sketch524,Pocket237,Sketch525,Pad365,Sketch526,Pad366,Sketch527,Pocket238,Sketch528,Pad367,Pad368,Pad369,Pad370,Pad371,+45 more]
  Origin = -> Origin033
  Placement = pos=(-57.4,25.8,-8.5) rot=(-0.58,-0.58,0.58;2.0944rad)
  Tip = -> Pad716
FEATURE [App::Part] Part  label="Leg_Connector"
  Group = -> [Body031,Body,Link]
  Origin = -> Origin034
